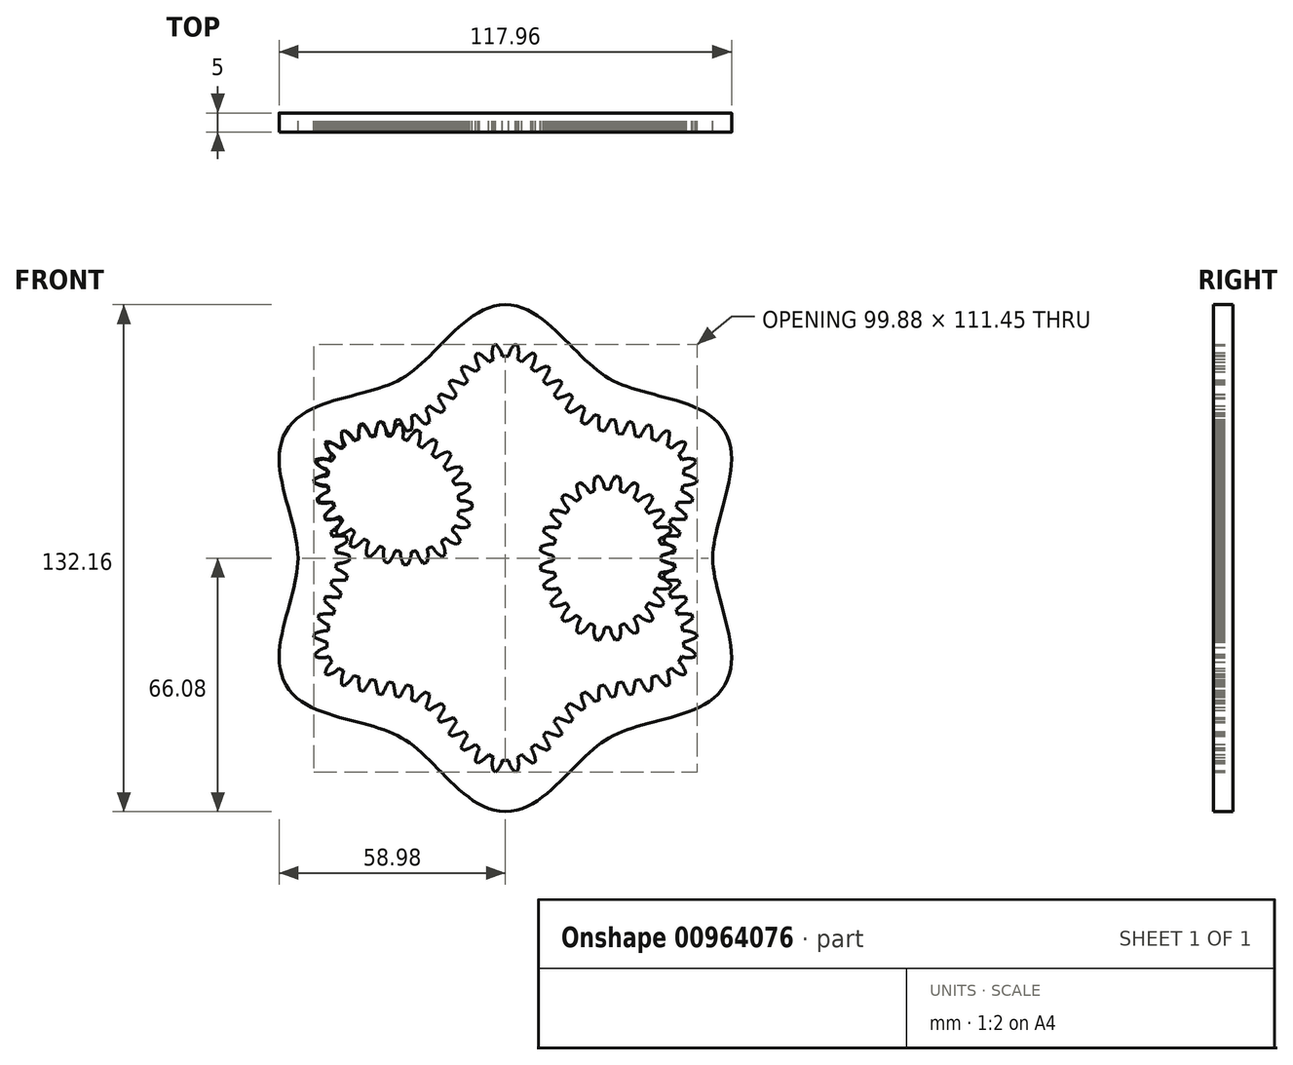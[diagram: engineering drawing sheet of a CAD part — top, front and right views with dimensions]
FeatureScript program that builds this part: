
annotation { "Feature Type Name" : "Feature", "Feature Type Description" : "" }
export const myFeature = defineFeature(function(context is Context, id is Id, definition is map)
    precondition{}
    {
        {
            var Q0;
            Q0=qCreatedBy(makeId("Front.planeOp"),FACE);
            var sketch = newSketch(context, id + "F0", { "sketchPlane" : qUnion([Q0])});
            skPoint(sketch, "E0", {"position": v(0, 66.08) * mm});
            skPoint(sketch, "E1", {"position": v(-59.16, 0) * mm});
            skSolve(sketch);
        }
        {
            var Q0;
            Q0=qCreatedBy(makeId("Front.planeOp"),FACE);
            var sketch = newSketch(context, id + "F1", { "sketchPlane" : qUnion([Q0])});
            skLineSegment(sketch, "E2", {"start": v(0, 0) * mm, "end": v(27.04, 46.83) * mm, "construction": true});
            skPoint(sketch, "E3", {"position": v(0, 66.08) * mm});
            skLineSegment(sketch, "E4", {"start": v(0, 0) * mm, "end": v(15.32, 57.19) * mm, "construction": true});
            skFitSpline(sketch, "E5", {"points": [v(0, 66.08) * mm, v(15.32, 57.19) * mm, v(27.04, 46.83) * mm], "startDerivative": vector(35.27, 0) * mm, "endDerivative": vector(23.83, -13.76) * mm});
            skLineSegment(sketch, "E6", {"start": v(23.2, 49.05) * mm, "end": v(27.04, 46.83) * mm, "construction": true});
            skLineSegment(sketch, "E7", {"start": v(0, 52.7) * mm, "end": v(0.86, 52.7) * mm});
            skLineSegment(sketch, "E8", {"start": v(3.15, 51.97) * mm, "end": v(4.31, 51.2) * mm});
            skLineSegment(sketch, "E9", {"start": v(6.74, 49.56) * mm, "end": v(7.8, 48.58) * mm});
            skLineSegment(sketch, "E10", {"start": v(9.81, 46.2) * mm, "end": v(10.7, 45.27) * mm});
            skLineSegment(sketch, "E11", {"start": v(12.7, 42.61) * mm, "end": v(13.52, 41.6) * mm});
            skLineSegment(sketch, "E12", {"start": v(15.78, 38.88) * mm, "end": v(16.73, 37.92) * mm});
            skLineSegment(sketch, "E13", {"start": v(19.8, 35.5) * mm, "end": v(20.32, 35.2) * mm});
            skLineSegment(sketch, "E14", {"start": v(2.56, 55.72) * mm, "end": v(3.13, 55.4) * mm});
            skLineSegment(sketch, "E15", {"start": v(7.18, 53.52) * mm, "end": v(7.82, 52.97) * mm});
            skLineSegment(sketch, "E16", {"start": v(10.9, 50.1) * mm, "end": v(11.58, 49.43) * mm});
            skLineSegment(sketch, "E17", {"start": v(13.99, 46.43) * mm, "end": v(14.76, 45.72) * mm});
            skLineSegment(sketch, "E18", {"start": v(16.88, 42.82) * mm, "end": v(17.59, 41.93) * mm});
            skLineSegment(sketch, "E19", {"start": v(19.84, 39.7) * mm, "end": v(20.77, 38.84) * mm});
            skArc(sketch, "E20", {"start": v(2.56, 55.72) * mm, "mid": v(1.4, 54.38) * mm, "end": v(0.86, 52.7) * mm});
            skArc(sketch, "E21", {"start": v(3.15, 51.97) * mm, "mid": v(3.46, 53.7) * mm, "end": v(3.13, 55.4) * mm});
            skArc(sketch, "E22", {"start": v(7.18, 53.52) * mm, "mid": v(5.65, 52.48) * mm, "end": v(4.31, 51.2) * mm});
            skArc(sketch, "E23", {"start": v(6.74, 49.56) * mm, "mid": v(7.47, 51.21) * mm, "end": v(7.82, 52.97) * mm});
            skArc(sketch, "E24", {"start": v(10.9, 50.1) * mm, "mid": v(9.29, 49.47) * mm, "end": v(7.8, 48.58) * mm});
            skArc(sketch, "E25", {"start": v(9.81, 46.2) * mm, "mid": v(10.8, 47.76) * mm, "end": v(11.58, 49.43) * mm});
            skArc(sketch, "E26", {"start": v(13.99, 46.43) * mm, "mid": v(12.33, 45.9) * mm, "end": v(10.7, 45.27) * mm});
            skArc(sketch, "E27", {"start": v(12.7, 42.61) * mm, "mid": v(13.78, 44.13) * mm, "end": v(14.76, 45.72) * mm});
            skArc(sketch, "E28", {"start": v(13.52, 41.6) * mm, "mid": v(15.2, 42.19) * mm, "end": v(16.88, 42.82) * mm});
            skArc(sketch, "E29", {"start": v(17.59, 41.93) * mm, "mid": v(16.64, 40.43) * mm, "end": v(15.78, 38.88) * mm});
            skArc(sketch, "E30", {"start": v(16.73, 37.92) * mm, "mid": v(18.35, 38.7) * mm, "end": v(19.84, 39.7) * mm});
            skArc(sketch, "E31", {"start": v(20.77, 38.84) * mm, "mid": v(20.1, 37.22) * mm, "end": v(19.8, 35.5) * mm});
            skPoint(sketch, "E32", {"position": v(0, 52.7) * mm});
            skPoint(sketch, "E33", {"position": v(0, 0) * mm});
            skLineSegment(sketch, "E34", {"start": v(0, 66.08) * mm, "end": v(0, 52.7) * mm});
            skLineSegment(sketch, "E35", {"start": v(20.32, 35.2) * mm, "end": v(27.04, 46.83) * mm});
            skSolve(sketch);
        }
        {
            var Q0;
            Q0 = qSketchRegion(id + "F1", true);
            extrude(context, id + "F2", {"entities" : qUnion([Q0]), "depth" : 5 * mm, "offsetDistance" : 25 * mm});
        }
        {
            var Q0;
            Q0=makeQuery(id+"F2.opExtrude","SWEPT_BODY",BODY,{"disambiguationData":[OSD([sQuery(id+"F1.wireOp",EDGE,"E5"),sQuery(id+"F1.wireOp",EDGE,"E7"),sQuery(id+"F1.wireOp",EDGE,"E8"),sQuery(id+"F1.wireOp",EDGE,"E9"),sQuery(id+"F1.wireOp",EDGE,"E10"),sQuery(id+"F1.wireOp",EDGE,"E11"),sQuery(id+"F1.wireOp",EDGE,"E12"),sQuery(id+"F1.wireOp",EDGE,"E13"),sQuery(id+"F1.wireOp",EDGE,"E14"),sQuery(id+"F1.wireOp",EDGE,"E15"),sQuery(id+"F1.wireOp",EDGE,"E16"),sQuery(id+"F1.wireOp",EDGE,"E17"),sQuery(id+"F1.wireOp",EDGE,"E18"),sQuery(id+"F1.wireOp",EDGE,"E19"),sQuery(id+"F1.wireOp",EDGE,"E20"),sQuery(id+"F1.wireOp",EDGE,"E21"),sQuery(id+"F1.wireOp",EDGE,"E22"),sQuery(id+"F1.wireOp",EDGE,"E23"),sQuery(id+"F1.wireOp",EDGE,"E24"),sQuery(id+"F1.wireOp",EDGE,"E25"),sQuery(id+"F1.wireOp",EDGE,"E26"),sQuery(id+"F1.wireOp",EDGE,"E27"),sQuery(id+"F1.wireOp",EDGE,"E28"),sQuery(id+"F1.wireOp",EDGE,"E29"),sQuery(id+"F1.wireOp",EDGE,"E30"),sQuery(id+"F1.wireOp",EDGE,"E31"),sQuery(id+"F1.wireOp",EDGE,"E34"),sQuery(id+"F1.wireOp",EDGE,"E35")])]});
            var Q1;
            Q1=qCreatedBy(makeId("Right.planeOp"),FACE);
            mirror(context, id + "F3", {"operationType" : NewBodyOperationType.ADD, "entities" : qUnion([Q0]), "mirrorPlane" : qUnion([Q1])});
        }
        {
            var Q0;
            Q0=qCreatedBy(makeId("Top.planeOp"),FACE);
            var sketch = newSketch(context, id + "F4", { "sketchPlane" : qUnion([Q0])});
            skLineSegment(sketch, "E36", {"start": v(0, 0) * mm, "end": v(0, -5) * mm, "construction": true});
            skSolve(sketch);
        }
        {
            var Q0;
            Q0=makeQuery(id+"F2.opExtrude","SWEPT_BODY",BODY,{"disambiguationData":[OSD([sQuery(id+"F1.wireOp",EDGE,"E5"),sQuery(id+"F1.wireOp",EDGE,"E7"),sQuery(id+"F1.wireOp",EDGE,"E8"),sQuery(id+"F1.wireOp",EDGE,"E9"),sQuery(id+"F1.wireOp",EDGE,"E10"),sQuery(id+"F1.wireOp",EDGE,"E11"),sQuery(id+"F1.wireOp",EDGE,"E12"),sQuery(id+"F1.wireOp",EDGE,"E13"),sQuery(id+"F1.wireOp",EDGE,"E14"),sQuery(id+"F1.wireOp",EDGE,"E15"),sQuery(id+"F1.wireOp",EDGE,"E16"),sQuery(id+"F1.wireOp",EDGE,"E17"),sQuery(id+"F1.wireOp",EDGE,"E18"),sQuery(id+"F1.wireOp",EDGE,"E19"),sQuery(id+"F1.wireOp",EDGE,"E20"),sQuery(id+"F1.wireOp",EDGE,"E21"),sQuery(id+"F1.wireOp",EDGE,"E22"),sQuery(id+"F1.wireOp",EDGE,"E23"),sQuery(id+"F1.wireOp",EDGE,"E24"),sQuery(id+"F1.wireOp",EDGE,"E25"),sQuery(id+"F1.wireOp",EDGE,"E26"),sQuery(id+"F1.wireOp",EDGE,"E27"),sQuery(id+"F1.wireOp",EDGE,"E28"),sQuery(id+"F1.wireOp",EDGE,"E29"),sQuery(id+"F1.wireOp",EDGE,"E30"),sQuery(id+"F1.wireOp",EDGE,"E31"),sQuery(id+"F1.wireOp",EDGE,"E34"),sQuery(id+"F1.wireOp",EDGE,"E35")])]});
            var Q1;
            Q1=sQuery(id+"F4.wireOp",EDGE,"E36");
            circularPattern(context, id + "F5", {"operationType" : NewBodyOperationType.ADD, "entities" : qUnion([Q0]), "axis" : qUnion([Q1]), "angle" : 360 * degree, "instanceCount" : 6, "equalSpace" : true});
        }
        {
            var Q0;
            Q0=qCreatedBy(makeId("Front.planeOp"),FACE);
            var sketch = newSketch(context, id + "F6", { "sketchPlane" : qUnion([Q0])});
            skLineSegment(sketch, "E37", {"start": v(-1.54, -16.72) * mm, "end": v(-1.46, -16.57) * mm});
            skLineSegment(sketch, "E38", {"start": v(-1.46, -16.57) * mm, "end": v(-1.39, -16.42) * mm});
            skLineSegment(sketch, "E39", {"start": v(-1.39, -16.42) * mm, "end": v(-1.32, -16.28) * mm});
            skLineSegment(sketch, "E40", {"start": v(-1.32, -16.28) * mm, "end": v(-1.26, -16.15) * mm});
            skLineSegment(sketch, "E41", {"start": v(-1.26, -16.15) * mm, "end": v(-1.2, -16.01) * mm});
            skLineSegment(sketch, "E42", {"start": v(-1.2, -16.01) * mm, "end": v(-1.15, -15.9) * mm});
            skLineSegment(sketch, "E43", {"start": v(-1.15, -15.9) * mm, "end": v(-1.1, -15.77) * mm});
            skLineSegment(sketch, "E44", {"start": v(-1.1, -15.77) * mm, "end": v(-1.06, -15.66) * mm});
            skLineSegment(sketch, "E45", {"start": v(-1.06, -15.66) * mm, "end": v(-1.03, -15.6) * mm});
            skLineSegment(sketch, "E46", {"start": v(-1.03, -15.6) * mm, "end": v(-1.02, -15.56) * mm});
            skLineSegment(sketch, "E47", {"start": v(-1.02, -15.56) * mm, "end": v(-1, -15.49) * mm});
            skLineSegment(sketch, "E48", {"start": v(-1, -15.49) * mm, "end": v(-0.96, -15.4) * mm});
            skLineSegment(sketch, "E49", {"start": v(-0.96, -15.4) * mm, "end": v(-0.93, -15.3) * mm});
            skLineSegment(sketch, "E50", {"start": v(-0.93, -15.3) * mm, "end": v(-0.9, -15.21) * mm});
            skLineSegment(sketch, "E51", {"start": v(-0.9, -15.21) * mm, "end": v(-0.88, -15.13) * mm});
            skLineSegment(sketch, "E52", {"start": v(-0.88, -15.13) * mm, "end": v(-0.86, -15.06) * mm});
            skLineSegment(sketch, "E53", {"start": v(-0.86, -15.06) * mm, "end": v(-0.84, -14.98) * mm});
            skLineSegment(sketch, "E54", {"start": v(-0.84, -14.98) * mm, "end": v(-0.83, -14.92) * mm});
            skLineSegment(sketch, "E55", {"start": v(-0.83, -14.92) * mm, "end": v(-0.81, -14.86) * mm});
            skLineSegment(sketch, "E56", {"start": v(-0.81, -14.86) * mm, "end": v(-0.8, -14.8) * mm});
            skLineSegment(sketch, "E57", {"start": v(-0.8, -14.8) * mm, "end": v(-0.72, -14.44) * mm});
            skLineSegment(sketch, "E58", {"start": v(-0.72, -14.44) * mm, "end": v(-0.71, -14.4) * mm});
            skLineSegment(sketch, "E59", {"start": v(-0.71, -14.4) * mm, "end": v(-0.7, -14.38) * mm});
            skLineSegment(sketch, "E60", {"start": v(-0.7, -14.38) * mm, "end": v(-0.69, -14.33) * mm});
            skLineSegment(sketch, "E61", {"start": v(-0.69, -14.33) * mm, "end": v(-0.67, -14.3) * mm});
            skLineSegment(sketch, "E62", {"start": v(-0.67, -14.3) * mm, "end": v(-0.66, -14.28) * mm});
            skLineSegment(sketch, "E63", {"start": v(-0.66, -14.28) * mm, "end": v(-0.65, -14.23) * mm});
            skLineSegment(sketch, "E64", {"start": v(-0.65, -14.23) * mm, "end": v(-0.63, -14.21) * mm});
            skLineSegment(sketch, "E65", {"start": v(-0.63, -14.21) * mm, "end": v(-0.6, -14.18) * mm});
            skLineSegment(sketch, "E66", {"start": v(-0.6, -14.18) * mm, "end": v(-0.58, -14.15) * mm});
            skLineSegment(sketch, "E67", {"start": v(-0.58, -14.15) * mm, "end": v(-0.55, -14.12) * mm});
            skLineSegment(sketch, "E68", {"start": v(-0.55, -14.12) * mm, "end": v(-0.52, -14.1) * mm});
            skLineSegment(sketch, "E69", {"start": v(-0.52, -14.1) * mm, "end": v(-0.5, -14.09) * mm});
            skLineSegment(sketch, "E70", {"start": v(-0.5, -14.09) * mm, "end": v(-0.48, -14.08) * mm});
            skLineSegment(sketch, "E71", {"start": v(-0.48, -14.08) * mm, "end": v(-0.48, -14.08) * mm});
            skLineSegment(sketch, "E72", {"start": v(-0.48, -14.08) * mm, "end": v(-0.46, -14.07) * mm});
            skLineSegment(sketch, "E73", {"start": v(-0.46, -14.07) * mm, "end": v(-0.44, -14.07) * mm});
            skLineSegment(sketch, "E74", {"start": v(-0.44, -14.07) * mm, "end": v(-0.28, -14.08) * mm});
            skLineSegment(sketch, "E75", {"start": v(-0.28, -14.08) * mm, "end": v(-0.05, -14.08) * mm});
            skLineSegment(sketch, "E76", {"start": v(-0.05, -14.08) * mm, "end": v(0.07, -14.08) * mm});
            skLineSegment(sketch, "E77", {"start": v(0.07, -14.08) * mm, "end": v(0.3, -14.07) * mm});
            skLineSegment(sketch, "E78", {"start": v(0.3, -14.07) * mm, "end": v(0.47, -14.07) * mm});
            skLineSegment(sketch, "E79", {"start": v(0.47, -14.07) * mm, "end": v(0.49, -14.07) * mm});
            skLineSegment(sketch, "E80", {"start": v(0.49, -14.07) * mm, "end": v(0.5, -14.08) * mm});
            skLineSegment(sketch, "E81", {"start": v(0.5, -14.08) * mm, "end": v(0.5, -14.08) * mm});
            skLineSegment(sketch, "E82", {"start": v(0.5, -14.08) * mm, "end": v(0.52, -14.08) * mm});
            skLineSegment(sketch, "E83", {"start": v(0.52, -14.08) * mm, "end": v(0.55, -14.1) * mm});
            skLineSegment(sketch, "E84", {"start": v(0.55, -14.1) * mm, "end": v(0.58, -14.12) * mm});
            skLineSegment(sketch, "E85", {"start": v(0.58, -14.12) * mm, "end": v(0.6, -14.15) * mm});
            skLineSegment(sketch, "E86", {"start": v(0.6, -14.15) * mm, "end": v(0.64, -14.19) * mm});
            skLineSegment(sketch, "E87", {"start": v(0.64, -14.19) * mm, "end": v(0.66, -14.2) * mm});
            skLineSegment(sketch, "E88", {"start": v(0.66, -14.2) * mm, "end": v(0.67, -14.25) * mm});
            skLineSegment(sketch, "E89", {"start": v(0.67, -14.25) * mm, "end": v(0.7, -14.28) * mm});
            skLineSegment(sketch, "E90", {"start": v(0.7, -14.28) * mm, "end": v(0.7, -14.3) * mm});
            skLineSegment(sketch, "E91", {"start": v(0.7, -14.3) * mm, "end": v(0.72, -14.37) * mm});
            skLineSegment(sketch, "E92", {"start": v(0.72, -14.37) * mm, "end": v(0.74, -14.4) * mm});
            skLineSegment(sketch, "E93", {"start": v(0.74, -14.4) * mm, "end": v(0.75, -14.44) * mm});
            skLineSegment(sketch, "E94", {"start": v(0.75, -14.44) * mm, "end": v(0.83, -14.8) * mm});
            skLineSegment(sketch, "E95", {"start": v(0.83, -14.8) * mm, "end": v(0.84, -14.87) * mm});
            skLineSegment(sketch, "E96", {"start": v(0.84, -14.87) * mm, "end": v(0.86, -14.95) * mm});
            skLineSegment(sketch, "E97", {"start": v(0.86, -14.95) * mm, "end": v(0.88, -15.03) * mm});
            skLineSegment(sketch, "E98", {"start": v(0.88, -15.03) * mm, "end": v(0.9, -15.1) * mm});
            skLineSegment(sketch, "E99", {"start": v(0.9, -15.1) * mm, "end": v(0.93, -15.2) * mm});
            skLineSegment(sketch, "E100", {"start": v(0.93, -15.2) * mm, "end": v(0.96, -15.29) * mm});
            skLineSegment(sketch, "E101", {"start": v(0.96, -15.29) * mm, "end": v(0.99, -15.39) * mm});
            skLineSegment(sketch, "E102", {"start": v(0.99, -15.39) * mm, "end": v(1.02, -15.48) * mm});
            skLineSegment(sketch, "E103", {"start": v(1.02, -15.48) * mm, "end": v(1.05, -15.55) * mm});
            skLineSegment(sketch, "E104", {"start": v(1.05, -15.55) * mm, "end": v(1.06, -15.59) * mm});
            skLineSegment(sketch, "E105", {"start": v(1.06, -15.59) * mm, "end": v(1.09, -15.66) * mm});
            skLineSegment(sketch, "E106", {"start": v(1.09, -15.66) * mm, "end": v(1.13, -15.77) * mm});
            skLineSegment(sketch, "E107", {"start": v(1.13, -15.77) * mm, "end": v(1.17, -15.88) * mm});
            skLineSegment(sketch, "E108", {"start": v(1.17, -15.88) * mm, "end": v(1.22, -16) * mm});
            skLineSegment(sketch, "E109", {"start": v(1.22, -16) * mm, "end": v(1.27, -16.1) * mm});
            skLineSegment(sketch, "E110", {"start": v(1.27, -16.1) * mm, "end": v(1.33, -16.23) * mm});
            skLineSegment(sketch, "E111", {"start": v(1.33, -16.23) * mm, "end": v(1.38, -16.35) * mm});
            skLineSegment(sketch, "E112", {"start": v(1.38, -16.35) * mm, "end": v(1.44, -16.47) * mm});
            skLineSegment(sketch, "E113", {"start": v(1.44, -16.47) * mm, "end": v(1.5, -16.6) * mm});
            skLineSegment(sketch, "E114", {"start": v(1.5, -16.6) * mm, "end": v(1.57, -16.72) * mm});
            skLineSegment(sketch, "E115", {"start": v(1.57, -16.72) * mm, "end": v(1.96, -17.44) * mm});
            skLineSegment(sketch, "E116", {"start": v(1.96, -17.44) * mm, "end": v(2.08, -17.43) * mm});
            skLineSegment(sketch, "E117", {"start": v(2.08, -17.43) * mm, "end": v(2.33, -17.4) * mm});
            skLineSegment(sketch, "E118", {"start": v(2.33, -17.4) * mm, "end": v(2.57, -17.38) * mm});
            skLineSegment(sketch, "E119", {"start": v(2.57, -17.38) * mm, "end": v(2.82, -17.36) * mm});
            skLineSegment(sketch, "E120", {"start": v(2.82, -17.36) * mm, "end": v(3.06, -17.33) * mm});
            skLineSegment(sketch, "E121", {"start": v(3.06, -17.33) * mm, "end": v(3.06, -17.33) * mm});
            skLineSegment(sketch, "E122", {"start": v(3.06, -17.33) * mm, "end": v(3.29, -16.64) * mm});
            skLineSegment(sketch, "E123", {"start": v(3.29, -16.64) * mm, "end": v(3.34, -16.5) * mm});
            skLineSegment(sketch, "E124", {"start": v(3.34, -16.5) * mm, "end": v(3.38, -16.35) * mm});
            skLineSegment(sketch, "E125", {"start": v(3.38, -16.35) * mm, "end": v(3.41, -16.21) * mm});
            skLineSegment(sketch, "E126", {"start": v(3.41, -16.21) * mm, "end": v(3.45, -16.08) * mm});
            skLineSegment(sketch, "E127", {"start": v(3.45, -16.08) * mm, "end": v(3.48, -15.96) * mm});
            skLineSegment(sketch, "E128", {"start": v(3.48, -15.96) * mm, "end": v(3.5, -15.84) * mm});
            skLineSegment(sketch, "E129", {"start": v(3.5, -15.84) * mm, "end": v(3.53, -15.72) * mm});
            skLineSegment(sketch, "E130", {"start": v(3.53, -15.72) * mm, "end": v(3.56, -15.6) * mm});
            skLineSegment(sketch, "E131", {"start": v(3.56, -15.6) * mm, "end": v(3.58, -15.5) * mm});
            skLineSegment(sketch, "E132", {"start": v(3.58, -15.5) * mm, "end": v(3.6, -15.4) * mm});
            skLineSegment(sketch, "E133", {"start": v(3.6, -15.4) * mm, "end": v(3.6, -15.34) * mm});
            skLineSegment(sketch, "E134", {"start": v(3.6, -15.34) * mm, "end": v(3.6, -15.31) * mm});
            skLineSegment(sketch, "E135", {"start": v(3.6, -15.31) * mm, "end": v(3.62, -15.25) * mm});
            skLineSegment(sketch, "E136", {"start": v(3.62, -15.25) * mm, "end": v(3.63, -15.16) * mm});
            skLineSegment(sketch, "E137", {"start": v(3.63, -15.16) * mm, "end": v(3.64, -15.08) * mm});
            skLineSegment(sketch, "E138", {"start": v(3.64, -15.08) * mm, "end": v(3.65, -15) * mm});
            skLineSegment(sketch, "E139", {"start": v(3.65, -15) * mm, "end": v(3.66, -14.92) * mm});
            skLineSegment(sketch, "E140", {"start": v(3.66, -14.92) * mm, "end": v(3.67, -14.84) * mm});
            skLineSegment(sketch, "E141", {"start": v(3.67, -14.84) * mm, "end": v(3.67, -14.75) * mm});
            skLineSegment(sketch, "E142", {"start": v(3.67, -14.75) * mm, "end": v(3.67, -14.68) * mm});
            skLineSegment(sketch, "E143", {"start": v(3.67, -14.68) * mm, "end": v(3.68, -14.61) * mm});
            skLineSegment(sketch, "E144", {"start": v(3.68, -14.61) * mm, "end": v(3.68, -14.55) * mm});
            skLineSegment(sketch, "E145", {"start": v(3.68, -14.55) * mm, "end": v(3.68, -14.18) * mm});
            skLineSegment(sketch, "E146", {"start": v(3.68, -14.18) * mm, "end": v(3.69, -14.14) * mm});
            skLineSegment(sketch, "E147", {"start": v(3.69, -14.14) * mm, "end": v(3.7, -14.1) * mm});
            skLineSegment(sketch, "E148", {"start": v(3.7, -14.1) * mm, "end": v(3.7, -14.04) * mm});
            skLineSegment(sketch, "E149", {"start": v(3.7, -14.04) * mm, "end": v(3.7, -14.01) * mm});
            skLineSegment(sketch, "E150", {"start": v(3.7, -14.01) * mm, "end": v(3.72, -13.98) * mm});
            skLineSegment(sketch, "E151", {"start": v(3.72, -13.98) * mm, "end": v(3.73, -13.93) * mm});
            skLineSegment(sketch, "E152", {"start": v(3.73, -13.93) * mm, "end": v(3.74, -13.9) * mm});
            skLineSegment(sketch, "E153", {"start": v(3.74, -13.9) * mm, "end": v(3.77, -13.86) * mm});
            skLineSegment(sketch, "E154", {"start": v(3.77, -13.86) * mm, "end": v(3.78, -13.83) * mm});
            skLineSegment(sketch, "E155", {"start": v(3.78, -13.83) * mm, "end": v(3.8, -13.8) * mm});
            skLineSegment(sketch, "E156", {"start": v(3.8, -13.8) * mm, "end": v(3.83, -13.78) * mm});
            skLineSegment(sketch, "E157", {"start": v(3.83, -13.78) * mm, "end": v(3.85, -13.76) * mm});
            skLineSegment(sketch, "E158", {"start": v(3.85, -13.76) * mm, "end": v(3.86, -13.76) * mm});
            skLineSegment(sketch, "E159", {"start": v(3.86, -13.76) * mm, "end": v(3.86, -13.75) * mm});
            skLineSegment(sketch, "E160", {"start": v(3.86, -13.75) * mm, "end": v(3.88, -13.75) * mm});
            skLineSegment(sketch, "E161", {"start": v(3.88, -13.75) * mm, "end": v(3.89, -13.74) * mm});
            skLineSegment(sketch, "E162", {"start": v(3.89, -13.74) * mm, "end": v(4.1, -13.7) * mm});
            skLineSegment(sketch, "E163", {"start": v(4.1, -13.7) * mm, "end": v(4.29, -13.67) * mm});
            skLineSegment(sketch, "E164", {"start": v(4.29, -13.67) * mm, "end": v(4.4, -13.65) * mm});
            skLineSegment(sketch, "E165", {"start": v(4.4, -13.65) * mm, "end": v(4.58, -13.61) * mm});
            skLineSegment(sketch, "E166", {"start": v(4.58, -13.61) * mm, "end": v(4.8, -13.57) * mm});
            skLineSegment(sketch, "E167", {"start": v(4.8, -13.57) * mm, "end": v(4.8, -13.57) * mm});
            skLineSegment(sketch, "E168", {"start": v(4.8, -13.57) * mm, "end": v(4.82, -13.57) * mm});
            skLineSegment(sketch, "E169", {"start": v(4.82, -13.57) * mm, "end": v(4.83, -13.57) * mm});
            skLineSegment(sketch, "E170", {"start": v(4.83, -13.57) * mm, "end": v(4.84, -13.57) * mm});
            skLineSegment(sketch, "E171", {"start": v(4.84, -13.57) * mm, "end": v(4.87, -13.58) * mm});
            skLineSegment(sketch, "E172", {"start": v(4.87, -13.58) * mm, "end": v(4.9, -13.6) * mm});
            skLineSegment(sketch, "E173", {"start": v(4.9, -13.6) * mm, "end": v(4.92, -13.6) * mm});
            skLineSegment(sketch, "E174", {"start": v(4.92, -13.6) * mm, "end": v(4.95, -13.63) * mm});
            skLineSegment(sketch, "E175", {"start": v(4.95, -13.63) * mm, "end": v(4.98, -13.66) * mm});
            skLineSegment(sketch, "E176", {"start": v(4.98, -13.66) * mm, "end": v(5.01, -13.7) * mm});
            skLineSegment(sketch, "E177", {"start": v(5.01, -13.7) * mm, "end": v(5.05, -13.73) * mm});
            skLineSegment(sketch, "E178", {"start": v(5.05, -13.73) * mm, "end": v(5.07, -13.75) * mm});
            skLineSegment(sketch, "E179", {"start": v(5.07, -13.75) * mm, "end": v(5.09, -13.8) * mm});
            skLineSegment(sketch, "E180", {"start": v(5.09, -13.8) * mm, "end": v(5.1, -13.82) * mm});
            skLineSegment(sketch, "E181", {"start": v(5.1, -13.82) * mm, "end": v(5.13, -13.85) * mm});
            skLineSegment(sketch, "E182", {"start": v(5.13, -13.85) * mm, "end": v(5.15, -13.91) * mm});
            skLineSegment(sketch, "E183", {"start": v(5.15, -13.91) * mm, "end": v(5.16, -13.91) * mm});
            skLineSegment(sketch, "E184", {"start": v(5.16, -13.91) * mm, "end": v(5.27, -14.19) * mm});
            skLineSegment(sketch, "E185", {"start": v(5.27, -14.19) * mm, "end": v(5.3, -14.25) * mm});
            skLineSegment(sketch, "E186", {"start": v(5.3, -14.25) * mm, "end": v(5.32, -14.3) * mm});
            skLineSegment(sketch, "E187", {"start": v(5.32, -14.3) * mm, "end": v(5.34, -14.36) * mm});
            skLineSegment(sketch, "E188", {"start": v(5.34, -14.36) * mm, "end": v(5.38, -14.43) * mm});
            skLineSegment(sketch, "E189", {"start": v(5.38, -14.43) * mm, "end": v(5.4, -14.5) * mm});
            skLineSegment(sketch, "E190", {"start": v(5.4, -14.5) * mm, "end": v(5.44, -14.56) * mm});
            skLineSegment(sketch, "E191", {"start": v(5.44, -14.56) * mm, "end": v(5.48, -14.64) * mm});
            skLineSegment(sketch, "E192", {"start": v(5.48, -14.64) * mm, "end": v(5.52, -14.71) * mm});
            skLineSegment(sketch, "E193", {"start": v(5.52, -14.71) * mm, "end": v(5.56, -14.78) * mm});
            skLineSegment(sketch, "E194", {"start": v(5.56, -14.78) * mm, "end": v(5.6, -14.87) * mm});
            skLineSegment(sketch, "E195", {"start": v(5.6, -14.87) * mm, "end": v(5.64, -14.91) * mm});
            skLineSegment(sketch, "E196", {"start": v(5.64, -14.91) * mm, "end": v(5.66, -14.95) * mm});
            skLineSegment(sketch, "E197", {"start": v(5.66, -14.95) * mm, "end": v(5.7, -15) * mm});
            skLineSegment(sketch, "E198", {"start": v(5.7, -15) * mm, "end": v(5.74, -15.08) * mm});
            skLineSegment(sketch, "E199", {"start": v(5.74, -15.08) * mm, "end": v(5.8, -15.17) * mm});
            skLineSegment(sketch, "E200", {"start": v(5.8, -15.17) * mm, "end": v(5.85, -15.25) * mm});
            skLineSegment(sketch, "E201", {"start": v(5.85, -15.25) * mm, "end": v(5.92, -15.36) * mm});
            skLineSegment(sketch, "E202", {"start": v(5.92, -15.36) * mm, "end": v(6, -15.47) * mm});
            skLineSegment(sketch, "E203", {"start": v(6, -15.47) * mm, "end": v(6.1, -15.6) * mm});
            skLineSegment(sketch, "E204", {"start": v(6.1, -15.6) * mm, "end": v(6.18, -15.71) * mm});
            skLineSegment(sketch, "E205", {"start": v(6.18, -15.71) * mm, "end": v(6.28, -15.84) * mm});
            skLineSegment(sketch, "E206", {"start": v(6.28, -15.84) * mm, "end": v(6.38, -15.96) * mm});
            skLineSegment(sketch, "E207", {"start": v(6.38, -15.96) * mm, "end": v(6.9, -16.59) * mm});
            skLineSegment(sketch, "E208", {"start": v(6.9, -16.59) * mm, "end": v(7.02, -16.55) * mm});
            skLineSegment(sketch, "E209", {"start": v(7.02, -16.55) * mm, "end": v(7.22, -16.5) * mm});
            skLineSegment(sketch, "E210", {"start": v(7.22, -16.5) * mm, "end": v(7.42, -16.44) * mm});
            skLineSegment(sketch, "E211", {"start": v(7.42, -16.44) * mm, "end": v(7.61, -16.38) * mm});
            skLineSegment(sketch, "E212", {"start": v(7.61, -16.38) * mm, "end": v(7.8, -16.32) * mm});
            skLineSegment(sketch, "E213", {"start": v(7.8, -16.32) * mm, "end": v(7.96, -16.27) * mm});
            skLineSegment(sketch, "E214", {"start": v(7.96, -16.27) * mm, "end": v(8.05, -15.52) * mm});
            skLineSegment(sketch, "E215", {"start": v(8.05, -15.52) * mm, "end": v(8.06, -15.37) * mm});
            skLineSegment(sketch, "E216", {"start": v(8.06, -15.37) * mm, "end": v(8.08, -15.2) * mm});
            skLineSegment(sketch, "E217", {"start": v(8.08, -15.2) * mm, "end": v(8.1, -15.05) * mm});
            skLineSegment(sketch, "E218", {"start": v(8.1, -15.05) * mm, "end": v(8.1, -14.9) * mm});
            skLineSegment(sketch, "E219", {"start": v(8.1, -14.9) * mm, "end": v(8.1, -14.76) * mm});
            skLineSegment(sketch, "E220", {"start": v(8.1, -14.76) * mm, "end": v(8.1, -14.63) * mm});
            skLineSegment(sketch, "E221", {"start": v(8.1, -14.63) * mm, "end": v(8.1, -14.5) * mm});
            skLineSegment(sketch, "E222", {"start": v(8.1, -14.5) * mm, "end": v(8.1, -14.39) * mm});
            skLineSegment(sketch, "E223", {"start": v(8.1, -14.39) * mm, "end": v(8.1, -14.28) * mm});
            skLineSegment(sketch, "E224", {"start": v(8.1, -14.28) * mm, "end": v(8.1, -14.21) * mm});
            skLineSegment(sketch, "E225", {"start": v(8.1, -14.21) * mm, "end": v(8.1, -14.18) * mm});
            skLineSegment(sketch, "E226", {"start": v(8.1, -14.18) * mm, "end": v(8.1, -14.12) * mm});
            skLineSegment(sketch, "E227", {"start": v(8.1, -14.12) * mm, "end": v(8.1, -14.03) * mm});
            skLineSegment(sketch, "E228", {"start": v(8.1, -14.03) * mm, "end": v(8.08, -13.95) * mm});
            skLineSegment(sketch, "E229", {"start": v(8.08, -13.95) * mm, "end": v(8.08, -13.87) * mm});
            skLineSegment(sketch, "E230", {"start": v(8.08, -13.87) * mm, "end": v(8.07, -13.8) * mm});
            skLineSegment(sketch, "E231", {"start": v(8.07, -13.8) * mm, "end": v(8.06, -13.73) * mm});
            skLineSegment(sketch, "E232", {"start": v(8.06, -13.73) * mm, "end": v(8.05, -13.67) * mm});
            skLineSegment(sketch, "E233", {"start": v(8.05, -13.67) * mm, "end": v(8.04, -13.61) * mm});
            skLineSegment(sketch, "E234", {"start": v(8.04, -13.61) * mm, "end": v(8.03, -13.56) * mm});
            skLineSegment(sketch, "E235", {"start": v(8.03, -13.56) * mm, "end": v(8.02, -13.52) * mm});
            skLineSegment(sketch, "E236", {"start": v(8.02, -13.52) * mm, "end": v(8.01, -13.47) * mm});
            skLineSegment(sketch, "E237", {"start": v(8.01, -13.47) * mm, "end": v(7.94, -13.13) * mm});
            skLineSegment(sketch, "E238", {"start": v(7.94, -13.13) * mm, "end": v(7.94, -13.13) * mm});
            skLineSegment(sketch, "E239", {"start": v(7.94, -13.13) * mm, "end": v(7.93, -13.05) * mm});
            skLineSegment(sketch, "E240", {"start": v(7.93, -13.05) * mm, "end": v(7.94, -13.05) * mm});
            skLineSegment(sketch, "E241", {"start": v(7.94, -13.05) * mm, "end": v(7.92, -12.98) * mm});
            skLineSegment(sketch, "E242", {"start": v(7.92, -12.98) * mm, "end": v(7.93, -12.95) * mm});
            skLineSegment(sketch, "E243", {"start": v(7.93, -12.95) * mm, "end": v(7.93, -12.91) * mm});
            skLineSegment(sketch, "E244", {"start": v(7.93, -12.91) * mm, "end": v(7.92, -12.87) * mm});
            skLineSegment(sketch, "E245", {"start": v(7.92, -12.87) * mm, "end": v(7.93, -12.84) * mm});
            skLineSegment(sketch, "E246", {"start": v(7.93, -12.84) * mm, "end": v(7.94, -12.8) * mm});
            skLineSegment(sketch, "E247", {"start": v(7.94, -12.8) * mm, "end": v(7.95, -12.75) * mm});
            skLineSegment(sketch, "E248", {"start": v(7.95, -12.75) * mm, "end": v(7.96, -12.7) * mm});
            skLineSegment(sketch, "E249", {"start": v(7.96, -12.7) * mm, "end": v(7.98, -12.67) * mm});
            skLineSegment(sketch, "E250", {"start": v(7.98, -12.67) * mm, "end": v(8, -12.64) * mm});
            skLineSegment(sketch, "E251", {"start": v(8, -12.64) * mm, "end": v(8.02, -12.62) * mm});
            skLineSegment(sketch, "E252", {"start": v(8.02, -12.62) * mm, "end": v(8.03, -12.61) * mm});
            skLineSegment(sketch, "E253", {"start": v(8.03, -12.61) * mm, "end": v(8.03, -12.6) * mm});
            skLineSegment(sketch, "E254", {"start": v(8.03, -12.6) * mm, "end": v(8.05, -12.6) * mm});
            skLineSegment(sketch, "E255", {"start": v(8.05, -12.6) * mm, "end": v(8.06, -12.59) * mm});
            skLineSegment(sketch, "E256", {"start": v(8.06, -12.59) * mm, "end": v(8.26, -12.5) * mm});
            skLineSegment(sketch, "E257", {"start": v(8.26, -12.5) * mm, "end": v(8.44, -12.44) * mm});
            skLineSegment(sketch, "E258", {"start": v(8.44, -12.44) * mm, "end": v(8.53, -12.4) * mm});
            skLineSegment(sketch, "E259", {"start": v(8.53, -12.4) * mm, "end": v(8.7, -12.33) * mm});
            skLineSegment(sketch, "E260", {"start": v(8.7, -12.33) * mm, "end": v(8.9, -12.24) * mm});
            skLineSegment(sketch, "E261", {"start": v(8.9, -12.24) * mm, "end": v(8.92, -12.23) * mm});
            skLineSegment(sketch, "E262", {"start": v(8.92, -12.23) * mm, "end": v(8.94, -12.23) * mm});
            skLineSegment(sketch, "E263", {"start": v(8.94, -12.23) * mm, "end": v(8.94, -12.23) * mm});
            skLineSegment(sketch, "E264", {"start": v(8.94, -12.23) * mm, "end": v(8.95, -12.23) * mm});
            skLineSegment(sketch, "E265", {"start": v(8.95, -12.23) * mm, "end": v(8.99, -12.23) * mm});
            skLineSegment(sketch, "E266", {"start": v(8.99, -12.23) * mm, "end": v(9.02, -12.24) * mm});
            skLineSegment(sketch, "E267", {"start": v(9.02, -12.24) * mm, "end": v(9.06, -12.26) * mm});
            skLineSegment(sketch, "E268", {"start": v(9.06, -12.26) * mm, "end": v(9.1, -12.28) * mm});
            skLineSegment(sketch, "E269", {"start": v(9.1, -12.28) * mm, "end": v(9.13, -12.29) * mm});
            skLineSegment(sketch, "E270", {"start": v(9.13, -12.29) * mm, "end": v(9.16, -12.32) * mm});
            skLineSegment(sketch, "E271", {"start": v(9.16, -12.32) * mm, "end": v(9.19, -12.34) * mm});
            skLineSegment(sketch, "E272", {"start": v(9.19, -12.34) * mm, "end": v(9.22, -12.36) * mm});
            skLineSegment(sketch, "E273", {"start": v(9.22, -12.36) * mm, "end": v(9.25, -12.4) * mm});
            skLineSegment(sketch, "E274", {"start": v(9.25, -12.4) * mm, "end": v(9.28, -12.43) * mm});
            skLineSegment(sketch, "E275", {"start": v(9.28, -12.43) * mm, "end": v(9.3, -12.46) * mm});
            skLineSegment(sketch, "E276", {"start": v(9.3, -12.46) * mm, "end": v(9.34, -12.5) * mm});
            skLineSegment(sketch, "E277", {"start": v(9.34, -12.5) * mm, "end": v(9.34, -12.5) * mm});
            skLineSegment(sketch, "E278", {"start": v(9.34, -12.5) * mm, "end": v(9.53, -12.78) * mm});
            skLineSegment(sketch, "E279", {"start": v(9.53, -12.78) * mm, "end": v(9.55, -12.82) * mm});
            skLineSegment(sketch, "E280", {"start": v(9.55, -12.82) * mm, "end": v(9.6, -12.88) * mm});
            skLineSegment(sketch, "E281", {"start": v(9.6, -12.88) * mm, "end": v(9.64, -12.94) * mm});
            skLineSegment(sketch, "E282", {"start": v(9.64, -12.94) * mm, "end": v(9.68, -13) * mm});
            skLineSegment(sketch, "E283", {"start": v(9.68, -13) * mm, "end": v(9.73, -13.06) * mm});
            skLineSegment(sketch, "E284", {"start": v(9.73, -13.06) * mm, "end": v(9.79, -13.13) * mm});
            skLineSegment(sketch, "E285", {"start": v(9.79, -13.13) * mm, "end": v(9.85, -13.2) * mm});
            skLineSegment(sketch, "E286", {"start": v(9.85, -13.2) * mm, "end": v(9.9, -13.27) * mm});
            skLineSegment(sketch, "E287", {"start": v(9.9, -13.27) * mm, "end": v(9.97, -13.34) * mm});
            skLineSegment(sketch, "E288", {"start": v(9.97, -13.34) * mm, "end": v(10, -13.39) * mm});
            skLineSegment(sketch, "E289", {"start": v(10, -13.39) * mm, "end": v(10.03, -13.41) * mm});
            skLineSegment(sketch, "E290", {"start": v(10.03, -13.41) * mm, "end": v(10.07, -13.45) * mm});
            skLineSegment(sketch, "E291", {"start": v(10.07, -13.45) * mm, "end": v(10.15, -13.53) * mm});
            skLineSegment(sketch, "E292", {"start": v(10.15, -13.53) * mm, "end": v(10.22, -13.6) * mm});
            skLineSegment(sketch, "E293", {"start": v(10.22, -13.6) * mm, "end": v(10.3, -13.69) * mm});
            skLineSegment(sketch, "E294", {"start": v(10.3, -13.69) * mm, "end": v(10.39, -13.77) * mm});
            skLineSegment(sketch, "E295", {"start": v(10.39, -13.77) * mm, "end": v(10.47, -13.85) * mm});
            skLineSegment(sketch, "E296", {"start": v(10.47, -13.85) * mm, "end": v(10.56, -13.92) * mm});
            skLineSegment(sketch, "E297", {"start": v(10.56, -13.92) * mm, "end": v(10.65, -14) * mm});
            skLineSegment(sketch, "E298", {"start": v(10.65, -14) * mm, "end": v(10.74, -14.08) * mm});
            skLineSegment(sketch, "E299", {"start": v(10.74, -14.08) * mm, "end": v(10.86, -14.18) * mm});
            skLineSegment(sketch, "E300", {"start": v(10.86, -14.18) * mm, "end": v(10.98, -14.28) * mm});
            skLineSegment(sketch, "E301", {"start": v(10.98, -14.28) * mm, "end": v(11.6, -14.75) * mm});
            skLineSegment(sketch, "E302", {"start": v(11.6, -14.75) * mm, "end": v(11.73, -14.68) * mm});
            skLineSegment(sketch, "E303", {"start": v(11.73, -14.68) * mm, "end": v(11.88, -14.6) * mm});
            skLineSegment(sketch, "E304", {"start": v(11.88, -14.6) * mm, "end": v(12.02, -14.52) * mm});
            skLineSegment(sketch, "E305", {"start": v(12.02, -14.52) * mm, "end": v(12.17, -14.44) * mm});
            skLineSegment(sketch, "E306", {"start": v(12.17, -14.44) * mm, "end": v(12.31, -14.36) * mm});
            skLineSegment(sketch, "E307", {"start": v(12.31, -14.36) * mm, "end": v(12.45, -14.28) * mm});
            skLineSegment(sketch, "E308", {"start": v(12.45, -14.28) * mm, "end": v(12.55, -14.22) * mm});
            skLineSegment(sketch, "E309", {"start": v(12.55, -14.22) * mm, "end": v(12.49, -13.48) * mm});
            skLineSegment(sketch, "E310", {"start": v(12.49, -13.48) * mm, "end": v(12.47, -13.33) * mm});
            skLineSegment(sketch, "E311", {"start": v(12.47, -13.33) * mm, "end": v(12.46, -13.2) * mm});
            skLineSegment(sketch, "E312", {"start": v(12.46, -13.2) * mm, "end": v(12.44, -13.06) * mm});
            skLineSegment(sketch, "E313", {"start": v(12.44, -13.06) * mm, "end": v(12.42, -12.94) * mm});
            skLineSegment(sketch, "E314", {"start": v(12.42, -12.94) * mm, "end": v(12.4, -12.82) * mm});
            skLineSegment(sketch, "E315", {"start": v(12.4, -12.82) * mm, "end": v(12.38, -12.7) * mm});
            skLineSegment(sketch, "E316", {"start": v(12.38, -12.7) * mm, "end": v(12.35, -12.57) * mm});
            skLineSegment(sketch, "E317", {"start": v(12.35, -12.57) * mm, "end": v(12.33, -12.45) * mm});
            skLineSegment(sketch, "E318", {"start": v(12.33, -12.45) * mm, "end": v(12.3, -12.34) * mm});
            skLineSegment(sketch, "E319", {"start": v(12.3, -12.34) * mm, "end": v(12.27, -12.24) * mm});
            skLineSegment(sketch, "E320", {"start": v(12.27, -12.24) * mm, "end": v(12.26, -12.17) * mm});
            skLineSegment(sketch, "E321", {"start": v(12.26, -12.17) * mm, "end": v(12.25, -12.16) * mm});
            skLineSegment(sketch, "E322", {"start": v(12.25, -12.16) * mm, "end": v(12.24, -12.1) * mm});
            skLineSegment(sketch, "E323", {"start": v(12.24, -12.1) * mm, "end": v(12.21, -12.02) * mm});
            skLineSegment(sketch, "E324", {"start": v(12.21, -12.02) * mm, "end": v(12.19, -11.94) * mm});
            skLineSegment(sketch, "E325", {"start": v(12.19, -11.94) * mm, "end": v(12.16, -11.87) * mm});
            skLineSegment(sketch, "E326", {"start": v(12.16, -11.87) * mm, "end": v(12.14, -11.82) * mm});
            skLineSegment(sketch, "E327", {"start": v(12.14, -11.82) * mm, "end": v(12.12, -11.76) * mm});
            skLineSegment(sketch, "E328", {"start": v(12.12, -11.76) * mm, "end": v(12.1, -11.7) * mm});
            skLineSegment(sketch, "E329", {"start": v(12.1, -11.7) * mm, "end": v(12.08, -11.66) * mm});
            skLineSegment(sketch, "E330", {"start": v(12.08, -11.66) * mm, "end": v(12.06, -11.62) * mm});
            skLineSegment(sketch, "E331", {"start": v(12.06, -11.62) * mm, "end": v(12.04, -11.58) * mm});
            skLineSegment(sketch, "E332", {"start": v(12.04, -11.58) * mm, "end": v(12.03, -11.56) * mm});
            skLineSegment(sketch, "E333", {"start": v(12.03, -11.56) * mm, "end": v(11.87, -11.24) * mm});
            skLineSegment(sketch, "E334", {"start": v(11.87, -11.24) * mm, "end": v(11.87, -11.24) * mm});
            skLineSegment(sketch, "E335", {"start": v(11.87, -11.24) * mm, "end": v(11.83, -11.16) * mm});
            skLineSegment(sketch, "E336", {"start": v(11.83, -11.16) * mm, "end": v(11.84, -11.15) * mm});
            skLineSegment(sketch, "E337", {"start": v(11.84, -11.15) * mm, "end": v(11.8, -11.08) * mm});
            skLineSegment(sketch, "E338", {"start": v(11.8, -11.08) * mm, "end": v(11.82, -11.07) * mm});
            skLineSegment(sketch, "E339", {"start": v(11.82, -11.07) * mm, "end": v(11.79, -11) * mm});
            skLineSegment(sketch, "E340", {"start": v(11.79, -11) * mm, "end": v(11.79, -10.97) * mm});
            skLineSegment(sketch, "E341", {"start": v(11.79, -10.97) * mm, "end": v(11.79, -10.94) * mm});
            skLineSegment(sketch, "E342", {"start": v(11.79, -10.94) * mm, "end": v(11.77, -10.9) * mm});
            skLineSegment(sketch, "E343", {"start": v(11.77, -10.9) * mm, "end": v(11.77, -10.86) * mm});
            skLineSegment(sketch, "E344", {"start": v(11.77, -10.86) * mm, "end": v(11.78, -10.83) * mm});
            skLineSegment(sketch, "E345", {"start": v(11.78, -10.83) * mm, "end": v(11.77, -10.8) * mm});
            skLineSegment(sketch, "E346", {"start": v(11.77, -10.8) * mm, "end": v(11.78, -10.76) * mm});
            skLineSegment(sketch, "E347", {"start": v(11.78, -10.76) * mm, "end": v(11.79, -10.72) * mm});
            skLineSegment(sketch, "E348", {"start": v(11.79, -10.72) * mm, "end": v(11.8, -10.68) * mm});
            skLineSegment(sketch, "E349", {"start": v(11.8, -10.68) * mm, "end": v(11.82, -10.65) * mm});
            skLineSegment(sketch, "E350", {"start": v(11.82, -10.65) * mm, "end": v(11.82, -10.64) * mm});
            skLineSegment(sketch, "E351", {"start": v(11.82, -10.64) * mm, "end": v(11.83, -10.63) * mm});
            skLineSegment(sketch, "E352", {"start": v(11.83, -10.63) * mm, "end": v(11.84, -10.62) * mm});
            skLineSegment(sketch, "E353", {"start": v(11.84, -10.62) * mm, "end": v(11.85, -10.6) * mm});
            skLineSegment(sketch, "E354", {"start": v(11.85, -10.6) * mm, "end": v(12.05, -10.47) * mm});
            skLineSegment(sketch, "E355", {"start": v(12.05, -10.47) * mm, "end": v(12.19, -10.37) * mm});
            skLineSegment(sketch, "E356", {"start": v(12.19, -10.37) * mm, "end": v(12.26, -10.32) * mm});
            skLineSegment(sketch, "E357", {"start": v(12.26, -10.32) * mm, "end": v(12.4, -10.22) * mm});
            skLineSegment(sketch, "E358", {"start": v(12.4, -10.22) * mm, "end": v(12.6, -10.08) * mm});
            skLineSegment(sketch, "E359", {"start": v(12.6, -10.08) * mm, "end": v(12.6, -10.07) * mm});
            skLineSegment(sketch, "E360", {"start": v(12.6, -10.07) * mm, "end": v(12.62, -10.06) * mm});
            skLineSegment(sketch, "E361", {"start": v(12.62, -10.06) * mm, "end": v(12.63, -10.06) * mm});
            skLineSegment(sketch, "E362", {"start": v(12.63, -10.06) * mm, "end": v(12.64, -10.06) * mm});
            skLineSegment(sketch, "E363", {"start": v(12.64, -10.06) * mm, "end": v(12.68, -10.05) * mm});
            skLineSegment(sketch, "E364", {"start": v(12.68, -10.05) * mm, "end": v(12.72, -10.05) * mm});
            skLineSegment(sketch, "E365", {"start": v(12.72, -10.05) * mm, "end": v(12.77, -10.06) * mm});
            skLineSegment(sketch, "E366", {"start": v(12.77, -10.06) * mm, "end": v(12.8, -10.06) * mm});
            skLineSegment(sketch, "E367", {"start": v(12.8, -10.06) * mm, "end": v(12.83, -10.08) * mm});
            skLineSegment(sketch, "E368", {"start": v(12.83, -10.08) * mm, "end": v(12.86, -10.09) * mm});
            skLineSegment(sketch, "E369", {"start": v(12.86, -10.09) * mm, "end": v(12.9, -10.1) * mm});
            skLineSegment(sketch, "E370", {"start": v(12.9, -10.1) * mm, "end": v(12.94, -10.12) * mm});
            skLineSegment(sketch, "E371", {"start": v(12.94, -10.12) * mm, "end": v(12.97, -10.15) * mm});
            skLineSegment(sketch, "E372", {"start": v(12.97, -10.15) * mm, "end": v(13, -10.16) * mm});
            skLineSegment(sketch, "E373", {"start": v(13, -10.16) * mm, "end": v(13.03, -10.18) * mm});
            skLineSegment(sketch, "E374", {"start": v(13.03, -10.18) * mm, "end": v(13.08, -10.22) * mm});
            skLineSegment(sketch, "E375", {"start": v(13.08, -10.22) * mm, "end": v(13.1, -10.24) * mm});
            skLineSegment(sketch, "E376", {"start": v(13.1, -10.24) * mm, "end": v(13.14, -10.26) * mm});
            skLineSegment(sketch, "E377", {"start": v(13.14, -10.26) * mm, "end": v(13.37, -10.49) * mm});
            skLineSegment(sketch, "E378", {"start": v(13.37, -10.49) * mm, "end": v(13.4, -10.52) * mm});
            skLineSegment(sketch, "E379", {"start": v(13.4, -10.52) * mm, "end": v(13.43, -10.55) * mm});
            skLineSegment(sketch, "E380", {"start": v(13.43, -10.55) * mm, "end": v(13.47, -10.6) * mm});
            skLineSegment(sketch, "E381", {"start": v(13.47, -10.6) * mm, "end": v(13.51, -10.63) * mm});
            skLineSegment(sketch, "E382", {"start": v(13.51, -10.63) * mm, "end": v(13.56, -10.67) * mm});
            skLineSegment(sketch, "E383", {"start": v(13.56, -10.67) * mm, "end": v(13.61, -10.7) * mm});
            skLineSegment(sketch, "E384", {"start": v(13.61, -10.7) * mm, "end": v(13.67, -10.76) * mm});
            skLineSegment(sketch, "E385", {"start": v(13.67, -10.76) * mm, "end": v(13.74, -10.81) * mm});
            skLineSegment(sketch, "E386", {"start": v(13.74, -10.81) * mm, "end": v(13.81, -10.86) * mm});
            skLineSegment(sketch, "E387", {"start": v(13.81, -10.86) * mm, "end": v(13.89, -10.92) * mm});
            skLineSegment(sketch, "E388", {"start": v(13.89, -10.92) * mm, "end": v(13.93, -10.95) * mm});
            skLineSegment(sketch, "E389", {"start": v(13.93, -10.95) * mm, "end": v(13.96, -10.96) * mm});
            skLineSegment(sketch, "E390", {"start": v(13.96, -10.96) * mm, "end": v(14, -11) * mm});
            skLineSegment(sketch, "E391", {"start": v(14, -11) * mm, "end": v(14.09, -11.05) * mm});
            skLineSegment(sketch, "E392", {"start": v(14.09, -11.05) * mm, "end": v(14.18, -11.1) * mm});
            skLineSegment(sketch, "E393", {"start": v(14.18, -11.1) * mm, "end": v(14.27, -11.16) * mm});
            skLineSegment(sketch, "E394", {"start": v(14.27, -11.16) * mm, "end": v(14.37, -11.22) * mm});
            skLineSegment(sketch, "E395", {"start": v(14.37, -11.22) * mm, "end": v(14.47, -11.27) * mm});
            skLineSegment(sketch, "E396", {"start": v(14.47, -11.27) * mm, "end": v(14.57, -11.33) * mm});
            skLineSegment(sketch, "E397", {"start": v(14.57, -11.33) * mm, "end": v(14.68, -11.39) * mm});
            skLineSegment(sketch, "E398", {"start": v(14.68, -11.39) * mm, "end": v(14.8, -11.45) * mm});
            skLineSegment(sketch, "E399", {"start": v(14.8, -11.45) * mm, "end": v(14.94, -11.51) * mm});
            skLineSegment(sketch, "E400", {"start": v(14.94, -11.51) * mm, "end": v(15.09, -11.57) * mm});
            skLineSegment(sketch, "E401", {"start": v(15.09, -11.57) * mm, "end": v(15.81, -11.88) * mm});
            skLineSegment(sketch, "E402", {"start": v(15.81, -11.88) * mm, "end": v(15.82, -11.87) * mm});
            skLineSegment(sketch, "E403", {"start": v(15.82, -11.87) * mm, "end": v(15.92, -11.78) * mm});
            skLineSegment(sketch, "E404", {"start": v(15.92, -11.78) * mm, "end": v(16.02, -11.7) * mm});
            skLineSegment(sketch, "E405", {"start": v(16.02, -11.7) * mm, "end": v(16.11, -11.6) * mm});
            skLineSegment(sketch, "E406", {"start": v(16.11, -11.6) * mm, "end": v(16.21, -11.51) * mm});
            skLineSegment(sketch, "E407", {"start": v(16.21, -11.51) * mm, "end": v(16.3, -11.42) * mm});
            skLineSegment(sketch, "E408", {"start": v(16.3, -11.42) * mm, "end": v(16.4, -11.33) * mm});
            skLineSegment(sketch, "E409", {"start": v(16.4, -11.33) * mm, "end": v(16.5, -11.24) * mm});
            skLineSegment(sketch, "E410", {"start": v(16.5, -11.24) * mm, "end": v(16.59, -11.15) * mm});
            skLineSegment(sketch, "E411", {"start": v(16.59, -11.15) * mm, "end": v(16.6, -11.15) * mm});
            skLineSegment(sketch, "E412", {"start": v(16.6, -11.15) * mm, "end": v(16.35, -10.42) * mm});
            skLineSegment(sketch, "E413", {"start": v(16.35, -10.42) * mm, "end": v(16.3, -10.28) * mm});
            skLineSegment(sketch, "E414", {"start": v(16.3, -10.28) * mm, "end": v(16.25, -10.16) * mm});
            skLineSegment(sketch, "E415", {"start": v(16.25, -10.16) * mm, "end": v(16.2, -10.04) * mm});
            skLineSegment(sketch, "E416", {"start": v(16.2, -10.04) * mm, "end": v(16.15, -9.91) * mm});
            skLineSegment(sketch, "E417", {"start": v(16.15, -9.91) * mm, "end": v(16.1, -9.78) * mm});
            skLineSegment(sketch, "E418", {"start": v(16.1, -9.78) * mm, "end": v(16.03, -9.66) * mm});
            skLineSegment(sketch, "E419", {"start": v(16.03, -9.66) * mm, "end": v(15.98, -9.56) * mm});
            skLineSegment(sketch, "E420", {"start": v(15.98, -9.56) * mm, "end": v(15.93, -9.45) * mm});
            skLineSegment(sketch, "E421", {"start": v(15.93, -9.45) * mm, "end": v(15.88, -9.36) * mm});
            skLineSegment(sketch, "E422", {"start": v(15.88, -9.36) * mm, "end": v(15.83, -9.28) * mm});
            skLineSegment(sketch, "E423", {"start": v(15.83, -9.28) * mm, "end": v(15.8, -9.24) * mm});
            skLineSegment(sketch, "E424", {"start": v(15.8, -9.24) * mm, "end": v(15.8, -9.22) * mm});
            skLineSegment(sketch, "E425", {"start": v(15.8, -9.22) * mm, "end": v(15.77, -9.18) * mm});
            skLineSegment(sketch, "E426", {"start": v(15.77, -9.18) * mm, "end": v(15.73, -9.11) * mm});
            skLineSegment(sketch, "E427", {"start": v(15.73, -9.11) * mm, "end": v(15.69, -9.05) * mm});
            skLineSegment(sketch, "E428", {"start": v(15.69, -9.05) * mm, "end": v(15.65, -9) * mm});
            skLineSegment(sketch, "E429", {"start": v(15.65, -9) * mm, "end": v(15.62, -8.95) * mm});
            skLineSegment(sketch, "E430", {"start": v(15.62, -8.95) * mm, "end": v(15.58, -8.9) * mm});
            skLineSegment(sketch, "E431", {"start": v(15.58, -8.9) * mm, "end": v(15.55, -8.87) * mm});
            skLineSegment(sketch, "E432", {"start": v(15.55, -8.87) * mm, "end": v(15.53, -8.84) * mm});
            skLineSegment(sketch, "E433", {"start": v(15.53, -8.84) * mm, "end": v(15.5, -8.81) * mm});
            skLineSegment(sketch, "E434", {"start": v(15.5, -8.81) * mm, "end": v(15.49, -8.8) * mm});
            skLineSegment(sketch, "E435", {"start": v(15.49, -8.8) * mm, "end": v(15.48, -8.78) * mm});
            skLineSegment(sketch, "E436", {"start": v(15.48, -8.78) * mm, "end": v(15.23, -8.53) * mm});
            skLineSegment(sketch, "E437", {"start": v(15.23, -8.53) * mm, "end": v(15.23, -8.52) * mm});
            skLineSegment(sketch, "E438", {"start": v(15.23, -8.52) * mm, "end": v(15.16, -8.45) * mm});
            skLineSegment(sketch, "E439", {"start": v(15.16, -8.45) * mm, "end": v(15.17, -8.44) * mm});
            skLineSegment(sketch, "E440", {"start": v(15.17, -8.44) * mm, "end": v(15.11, -8.38) * mm});
            skLineSegment(sketch, "E441", {"start": v(15.11, -8.38) * mm, "end": v(15.12, -8.37) * mm});
            skLineSegment(sketch, "E442", {"start": v(15.12, -8.37) * mm, "end": v(15.06, -8.3) * mm});
            skLineSegment(sketch, "E443", {"start": v(15.06, -8.3) * mm, "end": v(15.07, -8.3) * mm});
            skLineSegment(sketch, "E444", {"start": v(15.07, -8.3) * mm, "end": v(15.03, -8.24) * mm});
            skLineSegment(sketch, "E445", {"start": v(15.03, -8.24) * mm, "end": v(15.04, -8.22) * mm});
            skLineSegment(sketch, "E446", {"start": v(15.04, -8.22) * mm, "end": v(15, -8.17) * mm});
            skLineSegment(sketch, "E447", {"start": v(15, -8.17) * mm, "end": v(15, -8.15) * mm});
            skLineSegment(sketch, "E448", {"start": v(15, -8.15) * mm, "end": v(14.98, -8.1) * mm});
            skLineSegment(sketch, "E449", {"start": v(14.98, -8.1) * mm, "end": v(15, -8.08) * mm});
            skLineSegment(sketch, "E450", {"start": v(15, -8.08) * mm, "end": v(14.96, -8.04) * mm});
            skLineSegment(sketch, "E451", {"start": v(14.96, -8.04) * mm, "end": v(14.97, -8) * mm});
            skLineSegment(sketch, "E452", {"start": v(14.97, -8) * mm, "end": v(14.97, -7.97) * mm});
            skLineSegment(sketch, "E453", {"start": v(14.97, -7.97) * mm, "end": v(14.97, -7.94) * mm});
            skLineSegment(sketch, "E454", {"start": v(14.97, -7.94) * mm, "end": v(14.97, -7.9) * mm});
            skLineSegment(sketch, "E455", {"start": v(14.97, -7.9) * mm, "end": v(14.98, -7.87) * mm});
            skLineSegment(sketch, "E456", {"start": v(14.98, -7.87) * mm, "end": v(14.98, -7.86) * mm});
            skLineSegment(sketch, "E457", {"start": v(14.98, -7.86) * mm, "end": v(15, -7.84) * mm});
            skLineSegment(sketch, "E458", {"start": v(15, -7.84) * mm, "end": v(15, -7.83) * mm});
            skLineSegment(sketch, "E459", {"start": v(15, -7.83) * mm, "end": v(15.17, -7.62) * mm});
            skLineSegment(sketch, "E460", {"start": v(15.17, -7.62) * mm, "end": v(15.27, -7.5) * mm});
            skLineSegment(sketch, "E461", {"start": v(15.27, -7.5) * mm, "end": v(15.3, -7.45) * mm});
            skLineSegment(sketch, "E462", {"start": v(15.3, -7.45) * mm, "end": v(15.4, -7.33) * mm});
            skLineSegment(sketch, "E463", {"start": v(15.4, -7.33) * mm, "end": v(15.57, -7.12) * mm});
            skLineSegment(sketch, "E464", {"start": v(15.57, -7.12) * mm, "end": v(15.58, -7.1) * mm});
            skLineSegment(sketch, "E465", {"start": v(15.58, -7.1) * mm, "end": v(15.6, -7.1) * mm});
            skLineSegment(sketch, "E466", {"start": v(15.6, -7.1) * mm, "end": v(15.6, -7.1) * mm});
            skLineSegment(sketch, "E467", {"start": v(15.6, -7.1) * mm, "end": v(15.61, -7.1) * mm});
            skLineSegment(sketch, "E468", {"start": v(15.61, -7.1) * mm, "end": v(15.65, -7.07) * mm});
            skLineSegment(sketch, "E469", {"start": v(15.65, -7.07) * mm, "end": v(15.68, -7.05) * mm});
            skLineSegment(sketch, "E470", {"start": v(15.68, -7.05) * mm, "end": v(15.7, -7.06) * mm});
            skLineSegment(sketch, "E471", {"start": v(15.7, -7.06) * mm, "end": v(15.74, -7.05) * mm});
            skLineSegment(sketch, "E472", {"start": v(15.74, -7.05) * mm, "end": v(15.78, -7.04) * mm});
            skLineSegment(sketch, "E473", {"start": v(15.78, -7.04) * mm, "end": v(15.82, -7.06) * mm});
            skLineSegment(sketch, "E474", {"start": v(15.82, -7.06) * mm, "end": v(15.86, -7.05) * mm});
            skLineSegment(sketch, "E475", {"start": v(15.86, -7.05) * mm, "end": v(15.9, -7.05) * mm});
            skLineSegment(sketch, "E476", {"start": v(15.9, -7.05) * mm, "end": v(15.95, -7.08) * mm});
            skLineSegment(sketch, "E477", {"start": v(15.95, -7.08) * mm, "end": v(15.99, -7.08) * mm});
            skLineSegment(sketch, "E478", {"start": v(15.99, -7.08) * mm, "end": v(16.02, -7.08) * mm});
            skLineSegment(sketch, "E479", {"start": v(16.02, -7.08) * mm, "end": v(16.08, -7.11) * mm});
            skLineSegment(sketch, "E480", {"start": v(16.08, -7.11) * mm, "end": v(16.12, -7.12) * mm});
            skLineSegment(sketch, "E481", {"start": v(16.12, -7.12) * mm, "end": v(16.15, -7.13) * mm});
            skLineSegment(sketch, "E482", {"start": v(16.15, -7.13) * mm, "end": v(16.22, -7.17) * mm});
            skLineSegment(sketch, "E483", {"start": v(16.22, -7.17) * mm, "end": v(16.22, -7.17) * mm});
            skLineSegment(sketch, "E484", {"start": v(16.22, -7.17) * mm, "end": v(16.52, -7.35) * mm});
            skLineSegment(sketch, "E485", {"start": v(16.52, -7.35) * mm, "end": v(16.55, -7.36) * mm});
            skLineSegment(sketch, "E486", {"start": v(16.55, -7.36) * mm, "end": v(16.58, -7.38) * mm});
            skLineSegment(sketch, "E487", {"start": v(16.58, -7.38) * mm, "end": v(16.61, -7.4) * mm});
            skLineSegment(sketch, "E488", {"start": v(16.61, -7.4) * mm, "end": v(16.66, -7.42) * mm});
            skLineSegment(sketch, "E489", {"start": v(16.66, -7.42) * mm, "end": v(16.71, -7.45) * mm});
            skLineSegment(sketch, "E490", {"start": v(16.71, -7.45) * mm, "end": v(16.77, -7.48) * mm});
            skLineSegment(sketch, "E491", {"start": v(16.77, -7.48) * mm, "end": v(16.84, -7.5) * mm});
            skLineSegment(sketch, "E492", {"start": v(16.84, -7.5) * mm, "end": v(16.9, -7.53) * mm});
            skLineSegment(sketch, "E493", {"start": v(16.9, -7.53) * mm, "end": v(16.98, -7.56) * mm});
            skLineSegment(sketch, "E494", {"start": v(16.98, -7.56) * mm, "end": v(17.05, -7.6) * mm});
            skLineSegment(sketch, "E495", {"start": v(17.05, -7.6) * mm, "end": v(17.1, -7.6) * mm});
            skLineSegment(sketch, "E496", {"start": v(17.1, -7.6) * mm, "end": v(17.12, -7.61) * mm});
            skLineSegment(sketch, "E497", {"start": v(17.12, -7.61) * mm, "end": v(17.16, -7.63) * mm});
            skLineSegment(sketch, "E498", {"start": v(17.16, -7.63) * mm, "end": v(17.25, -7.66) * mm});
            skLineSegment(sketch, "E499", {"start": v(17.25, -7.66) * mm, "end": v(17.34, -7.68) * mm});
            skLineSegment(sketch, "E500", {"start": v(17.34, -7.68) * mm, "end": v(17.44, -7.7) * mm});
            skLineSegment(sketch, "E501", {"start": v(17.44, -7.7) * mm, "end": v(17.55, -7.74) * mm});
            skLineSegment(sketch, "E502", {"start": v(17.55, -7.74) * mm, "end": v(17.68, -7.77) * mm});
            skLineSegment(sketch, "E503", {"start": v(17.68, -7.77) * mm, "end": v(17.8, -7.8) * mm});
            skLineSegment(sketch, "E504", {"start": v(17.8, -7.8) * mm, "end": v(17.94, -7.82) * mm});
            skLineSegment(sketch, "E505", {"start": v(17.94, -7.82) * mm, "end": v(18.08, -7.84) * mm});
            skLineSegment(sketch, "E506", {"start": v(18.08, -7.84) * mm, "end": v(18.23, -7.86) * mm});
            skLineSegment(sketch, "E507", {"start": v(18.23, -7.86) * mm, "end": v(18.39, -7.88) * mm});
            skLineSegment(sketch, "E508", {"start": v(18.39, -7.88) * mm, "end": v(19.16, -7.95) * mm});
            skLineSegment(sketch, "E509", {"start": v(19.16, -7.95) * mm, "end": v(19.2, -7.88) * mm});
            skLineSegment(sketch, "E510", {"start": v(19.2, -7.88) * mm, "end": v(19.26, -7.79) * mm});
            skLineSegment(sketch, "E511", {"start": v(19.26, -7.79) * mm, "end": v(19.32, -7.7) * mm});
            skLineSegment(sketch, "E512", {"start": v(19.32, -7.7) * mm, "end": v(19.37, -7.6) * mm});
            skLineSegment(sketch, "E513", {"start": v(19.37, -7.6) * mm, "end": v(19.43, -7.51) * mm});
            skLineSegment(sketch, "E514", {"start": v(19.43, -7.51) * mm, "end": v(19.48, -7.42) * mm});
            skLineSegment(sketch, "E515", {"start": v(19.48, -7.42) * mm, "end": v(19.53, -7.33) * mm});
            skLineSegment(sketch, "E516", {"start": v(19.53, -7.33) * mm, "end": v(19.58, -7.24) * mm});
            skLineSegment(sketch, "E517", {"start": v(19.58, -7.24) * mm, "end": v(19.63, -7.15) * mm});
            skLineSegment(sketch, "E518", {"start": v(19.63, -7.15) * mm, "end": v(19.68, -7.06) * mm});
            skLineSegment(sketch, "E519", {"start": v(19.68, -7.06) * mm, "end": v(19.69, -7.04) * mm});
            skLineSegment(sketch, "E520", {"start": v(19.69, -7.04) * mm, "end": v(19.23, -6.4) * mm});
            skLineSegment(sketch, "E521", {"start": v(19.23, -6.4) * mm, "end": v(19.14, -6.27) * mm});
            skLineSegment(sketch, "E522", {"start": v(19.14, -6.27) * mm, "end": v(19.05, -6.14) * mm});
            skLineSegment(sketch, "E523", {"start": v(19.05, -6.14) * mm, "end": v(18.95, -6.03) * mm});
            skLineSegment(sketch, "E524", {"start": v(18.95, -6.03) * mm, "end": v(18.87, -5.93) * mm});
            skLineSegment(sketch, "E525", {"start": v(18.87, -5.93) * mm, "end": v(18.78, -5.83) * mm});
            skLineSegment(sketch, "E526", {"start": v(18.78, -5.83) * mm, "end": v(18.7, -5.74) * mm});
            skLineSegment(sketch, "E527", {"start": v(18.7, -5.74) * mm, "end": v(18.62, -5.66) * mm});
            skLineSegment(sketch, "E528", {"start": v(18.62, -5.66) * mm, "end": v(18.55, -5.6) * mm});
            skLineSegment(sketch, "E529", {"start": v(18.55, -5.6) * mm, "end": v(18.48, -5.53) * mm});
            skLineSegment(sketch, "E530", {"start": v(18.48, -5.53) * mm, "end": v(18.41, -5.47) * mm});
            skLineSegment(sketch, "E531", {"start": v(18.41, -5.47) * mm, "end": v(18.38, -5.44) * mm});
            skLineSegment(sketch, "E532", {"start": v(18.38, -5.44) * mm, "end": v(18.37, -5.43) * mm});
            skLineSegment(sketch, "E533", {"start": v(18.37, -5.43) * mm, "end": v(18.34, -5.4) * mm});
            skLineSegment(sketch, "E534", {"start": v(18.34, -5.4) * mm, "end": v(18.28, -5.35) * mm});
            skLineSegment(sketch, "E535", {"start": v(18.28, -5.35) * mm, "end": v(18.22, -5.3) * mm});
            skLineSegment(sketch, "E536", {"start": v(18.22, -5.3) * mm, "end": v(18.17, -5.27) * mm});
            skLineSegment(sketch, "E537", {"start": v(18.17, -5.27) * mm, "end": v(18.13, -5.24) * mm});
            skLineSegment(sketch, "E538", {"start": v(18.13, -5.24) * mm, "end": v(18.09, -5.22) * mm});
            skLineSegment(sketch, "E539", {"start": v(18.09, -5.22) * mm, "end": v(18.06, -5.2) * mm});
            skLineSegment(sketch, "E540", {"start": v(18.06, -5.2) * mm, "end": v(18.03, -5.18) * mm});
            skLineSegment(sketch, "E541", {"start": v(18.03, -5.18) * mm, "end": v(18.02, -5.17) * mm});
            skLineSegment(sketch, "E542", {"start": v(18.02, -5.17) * mm, "end": v(18, -5.17) * mm});
            skLineSegment(sketch, "E543", {"start": v(18, -5.17) * mm, "end": v(18, -5.17) * mm});
            skLineSegment(sketch, "E544", {"start": v(18, -5.17) * mm, "end": v(17.69, -5.02) * mm});
            skLineSegment(sketch, "E545", {"start": v(17.69, -5.02) * mm, "end": v(17.69, -5.01) * mm});
            skLineSegment(sketch, "E546", {"start": v(17.69, -5.01) * mm, "end": v(17.6, -4.96) * mm});
            skLineSegment(sketch, "E547", {"start": v(17.6, -4.96) * mm, "end": v(17.6, -4.95) * mm});
            skLineSegment(sketch, "E548", {"start": v(17.6, -4.95) * mm, "end": v(17.5, -4.9) * mm});
            skLineSegment(sketch, "E549", {"start": v(17.5, -4.9) * mm, "end": v(17.5, -4.9) * mm});
            skLineSegment(sketch, "E550", {"start": v(17.5, -4.9) * mm, "end": v(17.43, -4.85) * mm});
            skLineSegment(sketch, "E551", {"start": v(17.43, -4.85) * mm, "end": v(17.43, -4.83) * mm});
            skLineSegment(sketch, "E552", {"start": v(17.43, -4.83) * mm, "end": v(17.36, -4.79) * mm});
            skLineSegment(sketch, "E553", {"start": v(17.36, -4.79) * mm, "end": v(17.37, -4.77) * mm});
            skLineSegment(sketch, "E554", {"start": v(17.37, -4.77) * mm, "end": v(17.3, -4.73) * mm});
            skLineSegment(sketch, "E555", {"start": v(17.3, -4.73) * mm, "end": v(17.31, -4.7) * mm});
            skLineSegment(sketch, "E556", {"start": v(17.31, -4.7) * mm, "end": v(17.26, -4.67) * mm});
            skLineSegment(sketch, "E557", {"start": v(17.26, -4.67) * mm, "end": v(17.27, -4.64) * mm});
            skLineSegment(sketch, "E558", {"start": v(17.27, -4.64) * mm, "end": v(17.22, -4.61) * mm});
            skLineSegment(sketch, "E559", {"start": v(17.22, -4.61) * mm, "end": v(17.23, -4.58) * mm});
            skLineSegment(sketch, "E560", {"start": v(17.23, -4.58) * mm, "end": v(17.2, -4.56) * mm});
            skLineSegment(sketch, "E561", {"start": v(17.2, -4.56) * mm, "end": v(17.2, -4.52) * mm});
            skLineSegment(sketch, "E562", {"start": v(17.2, -4.52) * mm, "end": v(17.17, -4.5) * mm});
            skLineSegment(sketch, "E563", {"start": v(17.17, -4.5) * mm, "end": v(17.19, -4.46) * mm});
            skLineSegment(sketch, "E564", {"start": v(17.19, -4.46) * mm, "end": v(17.17, -4.43) * mm});
            skLineSegment(sketch, "E565", {"start": v(17.17, -4.43) * mm, "end": v(17.17, -4.4) * mm});
            skLineSegment(sketch, "E566", {"start": v(17.17, -4.4) * mm, "end": v(17.17, -4.4) * mm});
            skLineSegment(sketch, "E567", {"start": v(17.17, -4.4) * mm, "end": v(17.17, -4.37) * mm});
            skLineSegment(sketch, "E568", {"start": v(17.17, -4.37) * mm, "end": v(17.18, -4.35) * mm});
            skLineSegment(sketch, "E569", {"start": v(17.18, -4.35) * mm, "end": v(17.28, -4.1) * mm});
            skLineSegment(sketch, "E570", {"start": v(17.28, -4.1) * mm, "end": v(17.33, -3.96) * mm});
            skLineSegment(sketch, "E571", {"start": v(17.33, -3.96) * mm, "end": v(17.35, -3.9) * mm});
            skLineSegment(sketch, "E572", {"start": v(17.35, -3.9) * mm, "end": v(17.4, -3.78) * mm});
            skLineSegment(sketch, "E573", {"start": v(17.4, -3.78) * mm, "end": v(17.5, -3.51) * mm});
            skLineSegment(sketch, "E574", {"start": v(17.5, -3.51) * mm, "end": v(17.5, -3.5) * mm});
            skLineSegment(sketch, "E575", {"start": v(17.5, -3.5) * mm, "end": v(17.51, -3.47) * mm});
            skLineSegment(sketch, "E576", {"start": v(17.51, -3.47) * mm, "end": v(17.52, -3.47) * mm});
            skLineSegment(sketch, "E577", {"start": v(17.52, -3.47) * mm, "end": v(17.53, -3.46) * mm});
            skLineSegment(sketch, "E578", {"start": v(17.53, -3.46) * mm, "end": v(17.55, -3.43) * mm});
            skLineSegment(sketch, "E579", {"start": v(17.55, -3.43) * mm, "end": v(17.58, -3.42) * mm});
            skLineSegment(sketch, "E580", {"start": v(17.58, -3.42) * mm, "end": v(17.62, -3.4) * mm});
            skLineSegment(sketch, "E581", {"start": v(17.62, -3.4) * mm, "end": v(17.63, -3.37) * mm});
            skLineSegment(sketch, "E582", {"start": v(17.63, -3.37) * mm, "end": v(17.67, -3.38) * mm});
            skLineSegment(sketch, "E583", {"start": v(17.67, -3.38) * mm, "end": v(17.68, -3.35) * mm});
            skLineSegment(sketch, "E584", {"start": v(17.68, -3.35) * mm, "end": v(17.72, -3.36) * mm});
            skLineSegment(sketch, "E585", {"start": v(17.72, -3.36) * mm, "end": v(17.74, -3.33) * mm});
            skLineSegment(sketch, "E586", {"start": v(17.74, -3.33) * mm, "end": v(17.8, -3.34) * mm});
            skLineSegment(sketch, "E587", {"start": v(17.8, -3.34) * mm, "end": v(17.8, -3.32) * mm});
            skLineSegment(sketch, "E588", {"start": v(17.8, -3.32) * mm, "end": v(17.86, -3.33) * mm});
            skLineSegment(sketch, "E589", {"start": v(17.86, -3.33) * mm, "end": v(17.87, -3.31) * mm});
            skLineSegment(sketch, "E590", {"start": v(17.87, -3.31) * mm, "end": v(17.94, -3.32) * mm});
            skLineSegment(sketch, "E591", {"start": v(17.94, -3.32) * mm, "end": v(17.95, -3.3) * mm});
            skLineSegment(sketch, "E592", {"start": v(17.95, -3.3) * mm, "end": v(18.03, -3.32) * mm});
            skLineSegment(sketch, "E593", {"start": v(18.03, -3.32) * mm, "end": v(18.04, -3.31) * mm});
            skLineSegment(sketch, "E594", {"start": v(18.04, -3.31) * mm, "end": v(18.12, -3.33) * mm});
            skLineSegment(sketch, "E595", {"start": v(18.12, -3.33) * mm, "end": v(18.13, -3.32) * mm});
            skLineSegment(sketch, "E596", {"start": v(18.13, -3.32) * mm, "end": v(18.21, -3.34) * mm});
            skLineSegment(sketch, "E597", {"start": v(18.21, -3.34) * mm, "end": v(18.21, -3.33) * mm});
            skLineSegment(sketch, "E598", {"start": v(18.21, -3.33) * mm, "end": v(18.57, -3.43) * mm});
            skLineSegment(sketch, "E599", {"start": v(18.57, -3.43) * mm, "end": v(18.6, -3.43) * mm});
            skLineSegment(sketch, "E600", {"start": v(18.6, -3.43) * mm, "end": v(18.62, -3.44) * mm});
            skLineSegment(sketch, "E601", {"start": v(18.62, -3.44) * mm, "end": v(18.66, -3.45) * mm});
            skLineSegment(sketch, "E602", {"start": v(18.66, -3.45) * mm, "end": v(18.7, -3.45) * mm});
            skLineSegment(sketch, "E603", {"start": v(18.7, -3.45) * mm, "end": v(18.75, -3.46) * mm});
            skLineSegment(sketch, "E604", {"start": v(18.75, -3.46) * mm, "end": v(18.8, -3.47) * mm});
            skLineSegment(sketch, "E605", {"start": v(18.8, -3.47) * mm, "end": v(18.85, -3.47) * mm});
            skLineSegment(sketch, "E606", {"start": v(18.85, -3.47) * mm, "end": v(18.92, -3.48) * mm});
            skLineSegment(sketch, "E607", {"start": v(18.92, -3.48) * mm, "end": v(18.98, -3.48) * mm});
            skLineSegment(sketch, "E608", {"start": v(18.98, -3.48) * mm, "end": v(19.06, -3.48) * mm});
            skLineSegment(sketch, "E609", {"start": v(19.06, -3.48) * mm, "end": v(19.1, -3.48) * mm});
            skLineSegment(sketch, "E610", {"start": v(19.1, -3.48) * mm, "end": v(19.11, -3.49) * mm});
            skLineSegment(sketch, "E611", {"start": v(19.11, -3.49) * mm, "end": v(19.16, -3.49) * mm});
            skLineSegment(sketch, "E612", {"start": v(19.16, -3.49) * mm, "end": v(19.25, -3.48) * mm});
            skLineSegment(sketch, "E613", {"start": v(19.25, -3.48) * mm, "end": v(19.35, -3.48) * mm});
            skLineSegment(sketch, "E614", {"start": v(19.35, -3.48) * mm, "end": v(19.47, -3.47) * mm});
            skLineSegment(sketch, "E615", {"start": v(19.47, -3.47) * mm, "end": v(19.58, -3.46) * mm});
            skLineSegment(sketch, "E616", {"start": v(19.58, -3.46) * mm, "end": v(19.7, -3.45) * mm});
            skLineSegment(sketch, "E617", {"start": v(19.7, -3.45) * mm, "end": v(19.84, -3.43) * mm});
            skLineSegment(sketch, "E618", {"start": v(19.84, -3.43) * mm, "end": v(19.98, -3.4) * mm});
            skLineSegment(sketch, "E619", {"start": v(19.98, -3.4) * mm, "end": v(20.12, -3.38) * mm});
            skLineSegment(sketch, "E620", {"start": v(20.12, -3.38) * mm, "end": v(20.27, -3.35) * mm});
            skLineSegment(sketch, "E621", {"start": v(20.27, -3.35) * mm, "end": v(20.43, -3.3) * mm});
            skLineSegment(sketch, "E622", {"start": v(20.43, -3.3) * mm, "end": v(21.16, -3.1) * mm});
            skLineSegment(sketch, "E623", {"start": v(21.16, -3.1) * mm, "end": v(21.17, -3.08) * mm});
            skLineSegment(sketch, "E624", {"start": v(21.17, -3.08) * mm, "end": v(21.18, -2.99) * mm});
            skLineSegment(sketch, "E625", {"start": v(21.18, -2.99) * mm, "end": v(21.2, -2.9) * mm});
            skLineSegment(sketch, "E626", {"start": v(21.2, -2.9) * mm, "end": v(21.22, -2.8) * mm});
            skLineSegment(sketch, "E627", {"start": v(21.22, -2.8) * mm, "end": v(21.24, -2.72) * mm});
            skLineSegment(sketch, "E628", {"start": v(21.24, -2.72) * mm, "end": v(21.26, -2.63) * mm});
            skLineSegment(sketch, "E629", {"start": v(21.26, -2.63) * mm, "end": v(21.27, -2.54) * mm});
            skLineSegment(sketch, "E630", {"start": v(21.27, -2.54) * mm, "end": v(21.29, -2.45) * mm});
            skLineSegment(sketch, "E631", {"start": v(21.29, -2.45) * mm, "end": v(21.3, -2.36) * mm});
            skLineSegment(sketch, "E632", {"start": v(21.3, -2.36) * mm, "end": v(21.32, -2.27) * mm});
            skLineSegment(sketch, "E633", {"start": v(21.32, -2.27) * mm, "end": v(21.33, -2.18) * mm});
            skLineSegment(sketch, "E634", {"start": v(21.33, -2.18) * mm, "end": v(21.34, -2.12) * mm});
            skLineSegment(sketch, "E635", {"start": v(21.34, -2.12) * mm, "end": v(20.7, -1.66) * mm});
            skLineSegment(sketch, "E636", {"start": v(20.7, -1.66) * mm, "end": v(20.58, -1.57) * mm});
            skLineSegment(sketch, "E637", {"start": v(20.58, -1.57) * mm, "end": v(20.45, -1.49) * mm});
            skLineSegment(sketch, "E638", {"start": v(20.45, -1.49) * mm, "end": v(20.32, -1.4) * mm});
            skLineSegment(sketch, "E639", {"start": v(20.32, -1.4) * mm, "end": v(20.2, -1.34) * mm});
            skLineSegment(sketch, "E640", {"start": v(20.2, -1.34) * mm, "end": v(20.09, -1.28) * mm});
            skLineSegment(sketch, "E641", {"start": v(20.09, -1.28) * mm, "end": v(19.98, -1.22) * mm});
            skLineSegment(sketch, "E642", {"start": v(19.98, -1.22) * mm, "end": v(19.88, -1.17) * mm});
            skLineSegment(sketch, "E643", {"start": v(19.88, -1.17) * mm, "end": v(19.78, -1.13) * mm});
            skLineSegment(sketch, "E644", {"start": v(19.78, -1.13) * mm, "end": v(19.7, -1.1) * mm});
            skLineSegment(sketch, "E645", {"start": v(19.7, -1.1) * mm, "end": v(19.6, -1.06) * mm});
            skLineSegment(sketch, "E646", {"start": v(19.6, -1.06) * mm, "end": v(19.56, -1.04) * mm});
            skLineSegment(sketch, "E647", {"start": v(19.56, -1.04) * mm, "end": v(19.55, -1.04) * mm});
            skLineSegment(sketch, "E648", {"start": v(19.55, -1.04) * mm, "end": v(19.51, -1.02) * mm});
            skLineSegment(sketch, "E649", {"start": v(19.51, -1.02) * mm, "end": v(19.45, -1) * mm});
            skLineSegment(sketch, "E650", {"start": v(19.45, -1) * mm, "end": v(19.38, -0.98) * mm});
            skLineSegment(sketch, "E651", {"start": v(19.38, -0.98) * mm, "end": v(19.33, -0.97) * mm});
            skLineSegment(sketch, "E652", {"start": v(19.33, -0.97) * mm, "end": v(19.28, -0.95) * mm});
            skLineSegment(sketch, "E653", {"start": v(19.28, -0.95) * mm, "end": v(19.23, -0.94) * mm});
            skLineSegment(sketch, "E654", {"start": v(19.23, -0.94) * mm, "end": v(19.2, -0.94) * mm});
            skLineSegment(sketch, "E655", {"start": v(19.2, -0.94) * mm, "end": v(19.17, -0.93) * mm});
            skLineSegment(sketch, "E656", {"start": v(19.17, -0.93) * mm, "end": v(19.15, -0.93) * mm});
            skLineSegment(sketch, "E657", {"start": v(19.15, -0.93) * mm, "end": v(19.13, -0.93) * mm});
            skLineSegment(sketch, "E658", {"start": v(19.13, -0.93) * mm, "end": v(19.12, -0.92) * mm});
            skLineSegment(sketch, "E659", {"start": v(19.12, -0.92) * mm, "end": v(18.76, -0.9) * mm});
            skLineSegment(sketch, "E660", {"start": v(18.76, -0.9) * mm, "end": v(18.76, -0.9) * mm});
            skLineSegment(sketch, "E661", {"start": v(18.76, -0.9) * mm, "end": v(18.66, -0.88) * mm});
            skLineSegment(sketch, "E662", {"start": v(18.66, -0.88) * mm, "end": v(18.65, -0.87) * mm});
            skLineSegment(sketch, "E663", {"start": v(18.65, -0.87) * mm, "end": v(18.56, -0.86) * mm});
            skLineSegment(sketch, "E664", {"start": v(18.56, -0.86) * mm, "end": v(18.55, -0.84) * mm});
            skLineSegment(sketch, "E665", {"start": v(18.55, -0.84) * mm, "end": v(18.47, -0.83) * mm});
            skLineSegment(sketch, "E666", {"start": v(18.47, -0.83) * mm, "end": v(18.46, -0.8) * mm});
            skLineSegment(sketch, "E667", {"start": v(18.46, -0.8) * mm, "end": v(18.38, -0.8) * mm});
            skLineSegment(sketch, "E668", {"start": v(18.38, -0.8) * mm, "end": v(18.38, -0.77) * mm});
            skLineSegment(sketch, "E669", {"start": v(18.38, -0.77) * mm, "end": v(18.31, -0.76) * mm});
            skLineSegment(sketch, "E670", {"start": v(18.31, -0.76) * mm, "end": v(18.3, -0.74) * mm});
            skLineSegment(sketch, "E671", {"start": v(18.3, -0.74) * mm, "end": v(18.25, -0.72) * mm});
            skLineSegment(sketch, "E672", {"start": v(18.25, -0.72) * mm, "end": v(18.24, -0.7) * mm});
            skLineSegment(sketch, "E673", {"start": v(18.24, -0.7) * mm, "end": v(18.2, -0.68) * mm});
            skLineSegment(sketch, "E674", {"start": v(18.2, -0.68) * mm, "end": v(18.19, -0.65) * mm});
            skLineSegment(sketch, "E675", {"start": v(18.19, -0.65) * mm, "end": v(18.15, -0.64) * mm});
            skLineSegment(sketch, "E676", {"start": v(18.15, -0.64) * mm, "end": v(18.14, -0.6) * mm});
            skLineSegment(sketch, "E677", {"start": v(18.14, -0.6) * mm, "end": v(18.11, -0.6) * mm});
            skLineSegment(sketch, "E678", {"start": v(18.11, -0.6) * mm, "end": v(18.1, -0.56) * mm});
            skLineSegment(sketch, "E679", {"start": v(18.1, -0.56) * mm, "end": v(18.08, -0.53) * mm});
            skLineSegment(sketch, "E680", {"start": v(18.08, -0.53) * mm, "end": v(18.07, -0.5) * mm});
            skLineSegment(sketch, "E681", {"start": v(18.07, -0.5) * mm, "end": v(18.06, -0.5) * mm});
            skLineSegment(sketch, "E682", {"start": v(18.06, -0.5) * mm, "end": v(18.06, -0.47) * mm});
            skLineSegment(sketch, "E683", {"start": v(18.06, -0.47) * mm, "end": v(18.06, -0.44) * mm});
            skLineSegment(sketch, "E684", {"start": v(18.06, -0.44) * mm, "end": v(18.06, -0.17) * mm});
            skLineSegment(sketch, "E685", {"start": v(18.06, -0.17) * mm, "end": v(18.06, -0.02) * mm});
            skLineSegment(sketch, "E686", {"start": v(18.06, -0.02) * mm, "end": v(18.06, 0.02) * mm});
            skLineSegment(sketch, "E687", {"start": v(18.06, 0.02) * mm, "end": v(18.06, 0.17) * mm});
            skLineSegment(sketch, "E688", {"start": v(18.06, 0.17) * mm, "end": v(18.06, 0.44) * mm});
            skLineSegment(sketch, "E689", {"start": v(18.06, 0.44) * mm, "end": v(18.06, 0.47) * mm});
            skLineSegment(sketch, "E690", {"start": v(18.06, 0.47) * mm, "end": v(18.06, 0.5) * mm});
            skLineSegment(sketch, "E691", {"start": v(18.06, 0.5) * mm, "end": v(18.07, 0.5) * mm});
            skLineSegment(sketch, "E692", {"start": v(18.07, 0.5) * mm, "end": v(18.07, 0.5) * mm});
            skLineSegment(sketch, "E693", {"start": v(18.07, 0.5) * mm, "end": v(18.08, 0.55) * mm});
            skLineSegment(sketch, "E694", {"start": v(18.08, 0.55) * mm, "end": v(18.1, 0.56) * mm});
            skLineSegment(sketch, "E695", {"start": v(18.1, 0.56) * mm, "end": v(18.11, 0.6) * mm});
            skLineSegment(sketch, "E696", {"start": v(18.11, 0.6) * mm, "end": v(18.14, 0.6) * mm});
            skLineSegment(sketch, "E697", {"start": v(18.14, 0.6) * mm, "end": v(18.15, 0.64) * mm});
            skLineSegment(sketch, "E698", {"start": v(18.15, 0.64) * mm, "end": v(18.19, 0.65) * mm});
            skLineSegment(sketch, "E699", {"start": v(18.19, 0.65) * mm, "end": v(18.2, 0.68) * mm});
            skLineSegment(sketch, "E700", {"start": v(18.2, 0.68) * mm, "end": v(18.24, 0.7) * mm});
            skLineSegment(sketch, "E701", {"start": v(18.24, 0.7) * mm, "end": v(18.25, 0.72) * mm});
            skLineSegment(sketch, "E702", {"start": v(18.25, 0.72) * mm, "end": v(18.3, 0.74) * mm});
            skLineSegment(sketch, "E703", {"start": v(18.3, 0.74) * mm, "end": v(18.31, 0.76) * mm});
            skLineSegment(sketch, "E704", {"start": v(18.31, 0.76) * mm, "end": v(18.38, 0.77) * mm});
            skLineSegment(sketch, "E705", {"start": v(18.38, 0.77) * mm, "end": v(18.38, 0.8) * mm});
            skLineSegment(sketch, "E706", {"start": v(18.38, 0.8) * mm, "end": v(18.46, 0.8) * mm});
            skLineSegment(sketch, "E707", {"start": v(18.46, 0.8) * mm, "end": v(18.47, 0.83) * mm});
            skLineSegment(sketch, "E708", {"start": v(18.47, 0.83) * mm, "end": v(18.55, 0.84) * mm});
            skLineSegment(sketch, "E709", {"start": v(18.55, 0.84) * mm, "end": v(18.56, 0.86) * mm});
            skLineSegment(sketch, "E710", {"start": v(18.56, 0.86) * mm, "end": v(18.65, 0.87) * mm});
            skLineSegment(sketch, "E711", {"start": v(18.65, 0.87) * mm, "end": v(18.66, 0.88) * mm});
            skLineSegment(sketch, "E712", {"start": v(18.66, 0.88) * mm, "end": v(18.76, 0.9) * mm});
            skLineSegment(sketch, "E713", {"start": v(18.76, 0.9) * mm, "end": v(18.76, 0.9) * mm});
            skLineSegment(sketch, "E714", {"start": v(18.76, 0.9) * mm, "end": v(19.12, 0.93) * mm});
            skLineSegment(sketch, "E715", {"start": v(19.12, 0.93) * mm, "end": v(19.13, 0.93) * mm});
            skLineSegment(sketch, "E716", {"start": v(19.13, 0.93) * mm, "end": v(19.15, 0.93) * mm});
            skLineSegment(sketch, "E717", {"start": v(19.15, 0.93) * mm, "end": v(19.17, 0.93) * mm});
            skLineSegment(sketch, "E718", {"start": v(19.17, 0.93) * mm, "end": v(19.2, 0.94) * mm});
            skLineSegment(sketch, "E719", {"start": v(19.2, 0.94) * mm, "end": v(19.23, 0.94) * mm});
            skLineSegment(sketch, "E720", {"start": v(19.23, 0.94) * mm, "end": v(19.28, 0.95) * mm});
            skLineSegment(sketch, "E721", {"start": v(19.28, 0.95) * mm, "end": v(19.33, 0.97) * mm});
            skLineSegment(sketch, "E722", {"start": v(19.33, 0.97) * mm, "end": v(19.38, 0.98) * mm});
            skLineSegment(sketch, "E723", {"start": v(19.38, 0.98) * mm, "end": v(19.45, 1) * mm});
            skLineSegment(sketch, "E724", {"start": v(19.45, 1) * mm, "end": v(19.51, 1.02) * mm});
            skLineSegment(sketch, "E725", {"start": v(19.51, 1.02) * mm, "end": v(19.55, 1.04) * mm});
            skLineSegment(sketch, "E726", {"start": v(19.55, 1.04) * mm, "end": v(19.57, 1.04) * mm});
            skLineSegment(sketch, "E727", {"start": v(19.57, 1.04) * mm, "end": v(19.6, 1.06) * mm});
            skLineSegment(sketch, "E728", {"start": v(19.6, 1.06) * mm, "end": v(19.7, 1.1) * mm});
            skLineSegment(sketch, "E729", {"start": v(19.7, 1.1) * mm, "end": v(19.78, 1.13) * mm});
            skLineSegment(sketch, "E730", {"start": v(19.78, 1.13) * mm, "end": v(19.88, 1.17) * mm});
            skLineSegment(sketch, "E731", {"start": v(19.88, 1.17) * mm, "end": v(19.98, 1.22) * mm});
            skLineSegment(sketch, "E732", {"start": v(19.98, 1.22) * mm, "end": v(20.09, 1.28) * mm});
            skLineSegment(sketch, "E733", {"start": v(20.09, 1.28) * mm, "end": v(20.2, 1.34) * mm});
            skLineSegment(sketch, "E734", {"start": v(20.2, 1.34) * mm, "end": v(20.32, 1.41) * mm});
            skLineSegment(sketch, "E735", {"start": v(20.32, 1.41) * mm, "end": v(20.45, 1.49) * mm});
            skLineSegment(sketch, "E736", {"start": v(20.45, 1.49) * mm, "end": v(20.58, 1.57) * mm});
            skLineSegment(sketch, "E737", {"start": v(20.58, 1.57) * mm, "end": v(20.7, 1.66) * mm});
            skLineSegment(sketch, "E738", {"start": v(20.7, 1.66) * mm, "end": v(21.34, 2.12) * mm});
            skLineSegment(sketch, "E739", {"start": v(21.34, 2.12) * mm, "end": v(21.34, 2.15) * mm});
            skLineSegment(sketch, "E740", {"start": v(21.34, 2.15) * mm, "end": v(21.32, 2.24) * mm});
            skLineSegment(sketch, "E741", {"start": v(21.32, 2.24) * mm, "end": v(21.3, 2.33) * mm});
            skLineSegment(sketch, "E742", {"start": v(21.3, 2.33) * mm, "end": v(21.3, 2.42) * mm});
            skLineSegment(sketch, "E743", {"start": v(21.3, 2.42) * mm, "end": v(21.28, 2.5) * mm});
            skLineSegment(sketch, "E744", {"start": v(21.28, 2.5) * mm, "end": v(21.26, 2.6) * mm});
            skLineSegment(sketch, "E745", {"start": v(21.26, 2.6) * mm, "end": v(21.24, 2.69) * mm});
            skLineSegment(sketch, "E746", {"start": v(21.24, 2.69) * mm, "end": v(21.23, 2.78) * mm});
            skLineSegment(sketch, "E747", {"start": v(21.23, 2.78) * mm, "end": v(21.2, 2.87) * mm});
            skLineSegment(sketch, "E748", {"start": v(21.2, 2.87) * mm, "end": v(21.2, 2.96) * mm});
            skLineSegment(sketch, "E749", {"start": v(21.2, 2.96) * mm, "end": v(21.17, 3.05) * mm});
            skLineSegment(sketch, "E750", {"start": v(21.17, 3.05) * mm, "end": v(21.15, 3.13) * mm});
            skLineSegment(sketch, "E751", {"start": v(21.15, 3.13) * mm, "end": v(20.42, 3.33) * mm});
            skLineSegment(sketch, "E752", {"start": v(20.42, 3.33) * mm, "end": v(20.26, 3.36) * mm});
            skLineSegment(sketch, "E753", {"start": v(20.26, 3.36) * mm, "end": v(20.11, 3.4) * mm});
            skLineSegment(sketch, "E754", {"start": v(20.11, 3.4) * mm, "end": v(19.97, 3.42) * mm});
            skLineSegment(sketch, "E755", {"start": v(19.97, 3.42) * mm, "end": v(19.83, 3.45) * mm});
            skLineSegment(sketch, "E756", {"start": v(19.83, 3.45) * mm, "end": v(19.7, 3.47) * mm});
            skLineSegment(sketch, "E757", {"start": v(19.7, 3.47) * mm, "end": v(19.58, 3.48) * mm});
            skLineSegment(sketch, "E758", {"start": v(19.58, 3.48) * mm, "end": v(19.46, 3.5) * mm});
            skLineSegment(sketch, "E759", {"start": v(19.46, 3.5) * mm, "end": v(19.35, 3.5) * mm});
            skLineSegment(sketch, "E760", {"start": v(19.35, 3.5) * mm, "end": v(19.24, 3.5) * mm});
            skLineSegment(sketch, "E761", {"start": v(19.24, 3.5) * mm, "end": v(19.16, 3.5) * mm});
            skLineSegment(sketch, "E762", {"start": v(19.16, 3.5) * mm, "end": v(19.1, 3.5) * mm});
            skLineSegment(sketch, "E763", {"start": v(19.1, 3.5) * mm, "end": v(19.1, 3.5) * mm});
            skLineSegment(sketch, "E764", {"start": v(19.1, 3.5) * mm, "end": v(19.05, 3.5) * mm});
            skLineSegment(sketch, "E765", {"start": v(19.05, 3.5) * mm, "end": v(18.98, 3.5) * mm});
            skLineSegment(sketch, "E766", {"start": v(18.98, 3.5) * mm, "end": v(18.91, 3.5) * mm});
            skLineSegment(sketch, "E767", {"start": v(18.91, 3.5) * mm, "end": v(18.85, 3.5) * mm});
            skLineSegment(sketch, "E768", {"start": v(18.85, 3.5) * mm, "end": v(18.8, 3.48) * mm});
            skLineSegment(sketch, "E769", {"start": v(18.8, 3.48) * mm, "end": v(18.74, 3.48) * mm});
            skLineSegment(sketch, "E770", {"start": v(18.74, 3.48) * mm, "end": v(18.7, 3.47) * mm});
            skLineSegment(sketch, "E771", {"start": v(18.7, 3.47) * mm, "end": v(18.66, 3.46) * mm});
            skLineSegment(sketch, "E772", {"start": v(18.66, 3.46) * mm, "end": v(18.62, 3.46) * mm});
            skLineSegment(sketch, "E773", {"start": v(18.62, 3.46) * mm, "end": v(18.6, 3.45) * mm});
            skLineSegment(sketch, "E774", {"start": v(18.6, 3.45) * mm, "end": v(18.57, 3.45) * mm});
            skLineSegment(sketch, "E775", {"start": v(18.57, 3.45) * mm, "end": v(18.21, 3.35) * mm});
            skLineSegment(sketch, "E776", {"start": v(18.21, 3.35) * mm, "end": v(18.2, 3.36) * mm});
            skLineSegment(sketch, "E777", {"start": v(18.2, 3.36) * mm, "end": v(18.13, 3.34) * mm});
            skLineSegment(sketch, "E778", {"start": v(18.13, 3.34) * mm, "end": v(18.12, 3.35) * mm});
            skLineSegment(sketch, "E779", {"start": v(18.12, 3.35) * mm, "end": v(18.03, 3.33) * mm});
            skLineSegment(sketch, "E780", {"start": v(18.03, 3.33) * mm, "end": v(18.03, 3.34) * mm});
            skLineSegment(sketch, "E781", {"start": v(18.03, 3.34) * mm, "end": v(17.95, 3.32) * mm});
            skLineSegment(sketch, "E782", {"start": v(17.95, 3.32) * mm, "end": v(17.94, 3.34) * mm});
            skLineSegment(sketch, "E783", {"start": v(17.94, 3.34) * mm, "end": v(17.87, 3.33) * mm});
            skLineSegment(sketch, "E784", {"start": v(17.87, 3.33) * mm, "end": v(17.86, 3.35) * mm});
            skLineSegment(sketch, "E785", {"start": v(17.86, 3.35) * mm, "end": v(17.8, 3.34) * mm});
            skLineSegment(sketch, "E786", {"start": v(17.8, 3.34) * mm, "end": v(17.79, 3.36) * mm});
            skLineSegment(sketch, "E787", {"start": v(17.79, 3.36) * mm, "end": v(17.73, 3.35) * mm});
            skLineSegment(sketch, "E788", {"start": v(17.73, 3.35) * mm, "end": v(17.72, 3.37) * mm});
            skLineSegment(sketch, "E789", {"start": v(17.72, 3.37) * mm, "end": v(17.67, 3.37) * mm});
            skLineSegment(sketch, "E790", {"start": v(17.67, 3.37) * mm, "end": v(17.66, 3.4) * mm});
            skLineSegment(sketch, "E791", {"start": v(17.66, 3.4) * mm, "end": v(17.62, 3.39) * mm});
            skLineSegment(sketch, "E792", {"start": v(17.62, 3.39) * mm, "end": v(17.61, 3.42) * mm});
            skLineSegment(sketch, "E793", {"start": v(17.61, 3.42) * mm, "end": v(17.58, 3.42) * mm});
            skLineSegment(sketch, "E794", {"start": v(17.58, 3.42) * mm, "end": v(17.57, 3.45) * mm});
            skLineSegment(sketch, "E795", {"start": v(17.57, 3.45) * mm, "end": v(17.54, 3.45) * mm});
            skLineSegment(sketch, "E796", {"start": v(17.54, 3.45) * mm, "end": v(17.52, 3.48) * mm});
            skLineSegment(sketch, "E797", {"start": v(17.52, 3.48) * mm, "end": v(17.51, 3.48) * mm});
            skLineSegment(sketch, "E798", {"start": v(17.51, 3.48) * mm, "end": v(17.5, 3.49) * mm});
            skLineSegment(sketch, "E799", {"start": v(17.5, 3.49) * mm, "end": v(17.5, 3.5) * mm});
            skLineSegment(sketch, "E800", {"start": v(17.5, 3.5) * mm, "end": v(17.49, 3.53) * mm});
            skLineSegment(sketch, "E801", {"start": v(17.49, 3.53) * mm, "end": v(17.4, 3.8) * mm});
            skLineSegment(sketch, "E802", {"start": v(17.4, 3.8) * mm, "end": v(17.35, 3.92) * mm});
            skLineSegment(sketch, "E803", {"start": v(17.35, 3.92) * mm, "end": v(17.32, 3.98) * mm});
            skLineSegment(sketch, "E804", {"start": v(17.32, 3.98) * mm, "end": v(17.27, 4.1) * mm});
            skLineSegment(sketch, "E805", {"start": v(17.27, 4.1) * mm, "end": v(17.17, 4.36) * mm});
            skLineSegment(sketch, "E806", {"start": v(17.17, 4.36) * mm, "end": v(17.17, 4.39) * mm});
            skLineSegment(sketch, "E807", {"start": v(17.17, 4.39) * mm, "end": v(17.16, 4.4) * mm});
            skLineSegment(sketch, "E808", {"start": v(17.16, 4.4) * mm, "end": v(17.16, 4.41) * mm});
            skLineSegment(sketch, "E809", {"start": v(17.16, 4.41) * mm, "end": v(17.16, 4.42) * mm});
            skLineSegment(sketch, "E810", {"start": v(17.16, 4.42) * mm, "end": v(17.16, 4.46) * mm});
            skLineSegment(sketch, "E811", {"start": v(17.16, 4.46) * mm, "end": v(17.18, 4.48) * mm});
            skLineSegment(sketch, "E812", {"start": v(17.18, 4.48) * mm, "end": v(17.17, 4.52) * mm});
            skLineSegment(sketch, "E813", {"start": v(17.17, 4.52) * mm, "end": v(17.2, 4.54) * mm});
            skLineSegment(sketch, "E814", {"start": v(17.2, 4.54) * mm, "end": v(17.19, 4.57) * mm});
            skLineSegment(sketch, "E815", {"start": v(17.19, 4.57) * mm, "end": v(17.22, 4.6) * mm});
            skLineSegment(sketch, "E816", {"start": v(17.22, 4.6) * mm, "end": v(17.22, 4.63) * mm});
            skLineSegment(sketch, "E817", {"start": v(17.22, 4.63) * mm, "end": v(17.26, 4.66) * mm});
            skLineSegment(sketch, "E818", {"start": v(17.26, 4.66) * mm, "end": v(17.25, 4.69) * mm});
            skLineSegment(sketch, "E819", {"start": v(17.25, 4.69) * mm, "end": v(17.3, 4.72) * mm});
            skLineSegment(sketch, "E820", {"start": v(17.3, 4.72) * mm, "end": v(17.3, 4.74) * mm});
            skLineSegment(sketch, "E821", {"start": v(17.3, 4.74) * mm, "end": v(17.36, 4.78) * mm});
            skLineSegment(sketch, "E822", {"start": v(17.36, 4.78) * mm, "end": v(17.36, 4.8) * mm});
            skLineSegment(sketch, "E823", {"start": v(17.36, 4.8) * mm, "end": v(17.43, 4.84) * mm});
            skLineSegment(sketch, "E824", {"start": v(17.43, 4.84) * mm, "end": v(17.42, 4.86) * mm});
            skLineSegment(sketch, "E825", {"start": v(17.42, 4.86) * mm, "end": v(17.5, 4.9) * mm});
            skLineSegment(sketch, "E826", {"start": v(17.5, 4.9) * mm, "end": v(17.5, 4.92) * mm});
            skLineSegment(sketch, "E827", {"start": v(17.5, 4.92) * mm, "end": v(17.59, 4.97) * mm});
            skLineSegment(sketch, "E828", {"start": v(17.59, 4.97) * mm, "end": v(17.58, 4.98) * mm});
            skLineSegment(sketch, "E829", {"start": v(17.58, 4.98) * mm, "end": v(17.68, 5.03) * mm});
            skLineSegment(sketch, "E830", {"start": v(17.68, 5.03) * mm, "end": v(17.68, 5.04) * mm});
            skLineSegment(sketch, "E831", {"start": v(17.68, 5.04) * mm, "end": v(18, 5.18) * mm});
            skLineSegment(sketch, "E832", {"start": v(18, 5.18) * mm, "end": v(18, 5.18) * mm});
            skLineSegment(sketch, "E833", {"start": v(18, 5.18) * mm, "end": v(18, 5.19) * mm});
            skLineSegment(sketch, "E834", {"start": v(18, 5.19) * mm, "end": v(18.03, 5.2) * mm});
            skLineSegment(sketch, "E835", {"start": v(18.03, 5.2) * mm, "end": v(18.05, 5.21) * mm});
            skLineSegment(sketch, "E836", {"start": v(18.05, 5.21) * mm, "end": v(18.08, 5.23) * mm});
            skLineSegment(sketch, "E837", {"start": v(18.08, 5.23) * mm, "end": v(18.12, 5.26) * mm});
            skLineSegment(sketch, "E838", {"start": v(18.12, 5.26) * mm, "end": v(18.16, 5.29) * mm});
            skLineSegment(sketch, "E839", {"start": v(18.16, 5.29) * mm, "end": v(18.21, 5.33) * mm});
            skLineSegment(sketch, "E840", {"start": v(18.21, 5.33) * mm, "end": v(18.27, 5.37) * mm});
            skLineSegment(sketch, "E841", {"start": v(18.27, 5.37) * mm, "end": v(18.33, 5.42) * mm});
            skLineSegment(sketch, "E842", {"start": v(18.33, 5.42) * mm, "end": v(18.36, 5.44) * mm});
            skLineSegment(sketch, "E843", {"start": v(18.36, 5.44) * mm, "end": v(18.37, 5.45) * mm});
            skLineSegment(sketch, "E844", {"start": v(18.37, 5.45) * mm, "end": v(18.4, 5.48) * mm});
            skLineSegment(sketch, "E845", {"start": v(18.4, 5.48) * mm, "end": v(18.47, 5.54) * mm});
            skLineSegment(sketch, "E846", {"start": v(18.47, 5.54) * mm, "end": v(18.54, 5.6) * mm});
            skLineSegment(sketch, "E847", {"start": v(18.54, 5.6) * mm, "end": v(18.61, 5.68) * mm});
            skLineSegment(sketch, "E848", {"start": v(18.61, 5.68) * mm, "end": v(18.7, 5.76) * mm});
            skLineSegment(sketch, "E849", {"start": v(18.7, 5.76) * mm, "end": v(18.77, 5.85) * mm});
            skLineSegment(sketch, "E850", {"start": v(18.77, 5.85) * mm, "end": v(18.86, 5.95) * mm});
            skLineSegment(sketch, "E851", {"start": v(18.86, 5.95) * mm, "end": v(18.95, 6.05) * mm});
            skLineSegment(sketch, "E852", {"start": v(18.95, 6.05) * mm, "end": v(19.04, 6.16) * mm});
            skLineSegment(sketch, "E853", {"start": v(19.04, 6.16) * mm, "end": v(19.13, 6.29) * mm});
            skLineSegment(sketch, "E854", {"start": v(19.13, 6.29) * mm, "end": v(19.22, 6.4) * mm});
            skLineSegment(sketch, "E855", {"start": v(19.22, 6.4) * mm, "end": v(19.68, 7.06) * mm});
            skLineSegment(sketch, "E856", {"start": v(19.68, 7.06) * mm, "end": v(19.65, 7.12) * mm});
            skLineSegment(sketch, "E857", {"start": v(19.65, 7.12) * mm, "end": v(19.6, 7.21) * mm});
            skLineSegment(sketch, "E858", {"start": v(19.6, 7.21) * mm, "end": v(19.55, 7.3) * mm});
            skLineSegment(sketch, "E859", {"start": v(19.55, 7.3) * mm, "end": v(19.5, 7.4) * mm});
            skLineSegment(sketch, "E860", {"start": v(19.5, 7.4) * mm, "end": v(19.44, 7.48) * mm});
            skLineSegment(sketch, "E861", {"start": v(19.44, 7.48) * mm, "end": v(19.39, 7.58) * mm});
            skLineSegment(sketch, "E862", {"start": v(19.39, 7.58) * mm, "end": v(19.34, 7.67) * mm});
            skLineSegment(sketch, "E863", {"start": v(19.34, 7.67) * mm, "end": v(19.28, 7.76) * mm});
            skLineSegment(sketch, "E864", {"start": v(19.28, 7.76) * mm, "end": v(19.23, 7.85) * mm});
            skLineSegment(sketch, "E865", {"start": v(19.23, 7.85) * mm, "end": v(19.17, 7.94) * mm});
            skLineSegment(sketch, "E866", {"start": v(19.17, 7.94) * mm, "end": v(19.15, 7.96) * mm});
            skLineSegment(sketch, "E867", {"start": v(19.15, 7.96) * mm, "end": v(18.38, 7.9) * mm});
            skLineSegment(sketch, "E868", {"start": v(18.38, 7.9) * mm, "end": v(18.22, 7.88) * mm});
            skLineSegment(sketch, "E869", {"start": v(18.22, 7.88) * mm, "end": v(18.08, 7.86) * mm});
            skLineSegment(sketch, "E870", {"start": v(18.08, 7.86) * mm, "end": v(17.93, 7.83) * mm});
            skLineSegment(sketch, "E871", {"start": v(17.93, 7.83) * mm, "end": v(17.8, 7.8) * mm});
            skLineSegment(sketch, "E872", {"start": v(17.8, 7.8) * mm, "end": v(17.67, 7.78) * mm});
            skLineSegment(sketch, "E873", {"start": v(17.67, 7.78) * mm, "end": v(17.54, 7.75) * mm});
            skLineSegment(sketch, "E874", {"start": v(17.54, 7.75) * mm, "end": v(17.43, 7.73) * mm});
            skLineSegment(sketch, "E875", {"start": v(17.43, 7.73) * mm, "end": v(17.34, 7.7) * mm});
            skLineSegment(sketch, "E876", {"start": v(17.34, 7.7) * mm, "end": v(17.24, 7.67) * mm});
            skLineSegment(sketch, "E877", {"start": v(17.24, 7.67) * mm, "end": v(17.15, 7.64) * mm});
            skLineSegment(sketch, "E878", {"start": v(17.15, 7.64) * mm, "end": v(17.1, 7.63) * mm});
            skLineSegment(sketch, "E879", {"start": v(17.1, 7.63) * mm, "end": v(17.09, 7.62) * mm});
            skLineSegment(sketch, "E880", {"start": v(17.09, 7.62) * mm, "end": v(17.04, 7.6) * mm});
            skLineSegment(sketch, "E881", {"start": v(17.04, 7.6) * mm, "end": v(16.97, 7.58) * mm});
            skLineSegment(sketch, "E882", {"start": v(16.97, 7.58) * mm, "end": v(16.9, 7.55) * mm});
            skLineSegment(sketch, "E883", {"start": v(16.9, 7.55) * mm, "end": v(16.83, 7.52) * mm});
            skLineSegment(sketch, "E884", {"start": v(16.83, 7.52) * mm, "end": v(16.76, 7.5) * mm});
            skLineSegment(sketch, "E885", {"start": v(16.76, 7.5) * mm, "end": v(16.7, 7.46) * mm});
            skLineSegment(sketch, "E886", {"start": v(16.7, 7.46) * mm, "end": v(16.65, 7.44) * mm});
            skLineSegment(sketch, "E887", {"start": v(16.65, 7.44) * mm, "end": v(16.62, 7.42) * mm});
            skLineSegment(sketch, "E888", {"start": v(16.62, 7.42) * mm, "end": v(16.58, 7.4) * mm});
            skLineSegment(sketch, "E889", {"start": v(16.58, 7.4) * mm, "end": v(16.54, 7.38) * mm});
            skLineSegment(sketch, "E890", {"start": v(16.54, 7.38) * mm, "end": v(16.51, 7.36) * mm});
            skLineSegment(sketch, "E891", {"start": v(16.51, 7.36) * mm, "end": v(16.2, 7.18) * mm});
            skLineSegment(sketch, "E892", {"start": v(16.2, 7.18) * mm, "end": v(16.2, 7.18) * mm});
            skLineSegment(sketch, "E893", {"start": v(16.2, 7.18) * mm, "end": v(16.13, 7.14) * mm});
            skLineSegment(sketch, "E894", {"start": v(16.13, 7.14) * mm, "end": v(16.12, 7.15) * mm});
            skLineSegment(sketch, "E895", {"start": v(16.12, 7.15) * mm, "end": v(16.06, 7.11) * mm});
            skLineSegment(sketch, "E896", {"start": v(16.06, 7.11) * mm, "end": v(16.06, 7.12) * mm});
            skLineSegment(sketch, "E897", {"start": v(16.06, 7.12) * mm, "end": v(16, 7.1) * mm});
            skLineSegment(sketch, "E898", {"start": v(16, 7.1) * mm, "end": v(16, 7.1) * mm});
            skLineSegment(sketch, "E899", {"start": v(16, 7.1) * mm, "end": v(15.94, 7.08) * mm});
            skLineSegment(sketch, "E900", {"start": v(15.94, 7.08) * mm, "end": v(15.93, 7.09) * mm});
            skLineSegment(sketch, "E901", {"start": v(15.93, 7.09) * mm, "end": v(15.89, 7.06) * mm});
            skLineSegment(sketch, "E902", {"start": v(15.89, 7.06) * mm, "end": v(15.87, 7.08) * mm});
            skLineSegment(sketch, "E903", {"start": v(15.87, 7.08) * mm, "end": v(15.83, 7.06) * mm});
            skLineSegment(sketch, "E904", {"start": v(15.83, 7.06) * mm, "end": v(15.8, 7.07) * mm});
            skLineSegment(sketch, "E905", {"start": v(15.8, 7.07) * mm, "end": v(15.77, 7.05) * mm});
            skLineSegment(sketch, "E906", {"start": v(15.77, 7.05) * mm, "end": v(15.73, 7.07) * mm});
            skLineSegment(sketch, "E907", {"start": v(15.73, 7.07) * mm, "end": v(15.7, 7.08) * mm});
            skLineSegment(sketch, "E908", {"start": v(15.7, 7.08) * mm, "end": v(15.67, 7.07) * mm});
            skLineSegment(sketch, "E909", {"start": v(15.67, 7.07) * mm, "end": v(15.64, 7.09) * mm});
            skLineSegment(sketch, "E910", {"start": v(15.64, 7.09) * mm, "end": v(15.6, 7.1) * mm});
            skLineSegment(sketch, "E911", {"start": v(15.6, 7.1) * mm, "end": v(15.6, 7.1) * mm});
            skLineSegment(sketch, "E912", {"start": v(15.6, 7.1) * mm, "end": v(15.59, 7.11) * mm});
            skLineSegment(sketch, "E913", {"start": v(15.59, 7.11) * mm, "end": v(15.56, 7.14) * mm});
            skLineSegment(sketch, "E914", {"start": v(15.56, 7.14) * mm, "end": v(15.56, 7.14) * mm});
            skLineSegment(sketch, "E915", {"start": v(15.56, 7.14) * mm, "end": v(15.4, 7.34) * mm});
            skLineSegment(sketch, "E916", {"start": v(15.4, 7.34) * mm, "end": v(15.3, 7.47) * mm});
            skLineSegment(sketch, "E917", {"start": v(15.3, 7.47) * mm, "end": v(15.26, 7.51) * mm});
            skLineSegment(sketch, "E918", {"start": v(15.26, 7.51) * mm, "end": v(15.16, 7.64) * mm});
            skLineSegment(sketch, "E919", {"start": v(15.16, 7.64) * mm, "end": v(14.99, 7.84) * mm});
            skLineSegment(sketch, "E920", {"start": v(14.99, 7.84) * mm, "end": v(14.98, 7.86) * mm});
            skLineSegment(sketch, "E921", {"start": v(14.98, 7.86) * mm, "end": v(14.97, 7.87) * mm});
            skLineSegment(sketch, "E922", {"start": v(14.97, 7.87) * mm, "end": v(14.97, 7.88) * mm});
            skLineSegment(sketch, "E923", {"start": v(14.97, 7.88) * mm, "end": v(14.97, 7.89) * mm});
            skLineSegment(sketch, "E924", {"start": v(14.97, 7.89) * mm, "end": v(14.96, 7.93) * mm});
            skLineSegment(sketch, "E925", {"start": v(14.96, 7.93) * mm, "end": v(14.95, 7.96) * mm});
            skLineSegment(sketch, "E926", {"start": v(14.95, 7.96) * mm, "end": v(14.95, 8) * mm});
            skLineSegment(sketch, "E927", {"start": v(14.95, 8) * mm, "end": v(14.97, 8.04) * mm});
            skLineSegment(sketch, "E928", {"start": v(14.97, 8.04) * mm, "end": v(14.95, 8.06) * mm});
            skLineSegment(sketch, "E929", {"start": v(14.95, 8.06) * mm, "end": v(14.98, 8.1) * mm});
            skLineSegment(sketch, "E930", {"start": v(14.98, 8.1) * mm, "end": v(14.97, 8.12) * mm});
            skLineSegment(sketch, "E931", {"start": v(14.97, 8.12) * mm, "end": v(15, 8.16) * mm});
            skLineSegment(sketch, "E932", {"start": v(15, 8.16) * mm, "end": v(14.99, 8.18) * mm});
            skLineSegment(sketch, "E933", {"start": v(14.99, 8.18) * mm, "end": v(15.03, 8.23) * mm});
            skLineSegment(sketch, "E934", {"start": v(15.03, 8.23) * mm, "end": v(15.02, 8.25) * mm});
            skLineSegment(sketch, "E935", {"start": v(15.02, 8.25) * mm, "end": v(15.06, 8.3) * mm});
            skLineSegment(sketch, "E936", {"start": v(15.06, 8.3) * mm, "end": v(15.05, 8.32) * mm});
            skLineSegment(sketch, "E937", {"start": v(15.05, 8.32) * mm, "end": v(15.1, 8.38) * mm});
            skLineSegment(sketch, "E938", {"start": v(15.1, 8.38) * mm, "end": v(15.1, 8.4) * mm});
            skLineSegment(sketch, "E939", {"start": v(15.1, 8.4) * mm, "end": v(15.16, 8.46) * mm});
            skLineSegment(sketch, "E940", {"start": v(15.16, 8.46) * mm, "end": v(15.15, 8.47) * mm});
            skLineSegment(sketch, "E941", {"start": v(15.15, 8.47) * mm, "end": v(15.22, 8.54) * mm});
            skLineSegment(sketch, "E942", {"start": v(15.22, 8.54) * mm, "end": v(15.21, 8.54) * mm});
            skLineSegment(sketch, "E943", {"start": v(15.21, 8.54) * mm, "end": v(15.47, 8.8) * mm});
            skLineSegment(sketch, "E944", {"start": v(15.47, 8.8) * mm, "end": v(15.48, 8.8) * mm});
            skLineSegment(sketch, "E945", {"start": v(15.48, 8.8) * mm, "end": v(15.5, 8.82) * mm});
            skLineSegment(sketch, "E946", {"start": v(15.5, 8.82) * mm, "end": v(15.51, 8.85) * mm});
            skLineSegment(sketch, "E947", {"start": v(15.51, 8.85) * mm, "end": v(15.54, 8.88) * mm});
            skLineSegment(sketch, "E948", {"start": v(15.54, 8.88) * mm, "end": v(15.57, 8.92) * mm});
            skLineSegment(sketch, "E949", {"start": v(15.57, 8.92) * mm, "end": v(15.6, 8.96) * mm});
            skLineSegment(sketch, "E950", {"start": v(15.6, 8.96) * mm, "end": v(15.64, 9.02) * mm});
            skLineSegment(sketch, "E951", {"start": v(15.64, 9.02) * mm, "end": v(15.68, 9.07) * mm});
            skLineSegment(sketch, "E952", {"start": v(15.68, 9.07) * mm, "end": v(15.72, 9.13) * mm});
            skLineSegment(sketch, "E953", {"start": v(15.72, 9.13) * mm, "end": v(15.76, 9.2) * mm});
            skLineSegment(sketch, "E954", {"start": v(15.76, 9.2) * mm, "end": v(15.78, 9.23) * mm});
            skLineSegment(sketch, "E955", {"start": v(15.78, 9.23) * mm, "end": v(15.8, 9.25) * mm});
            skLineSegment(sketch, "E956", {"start": v(15.8, 9.25) * mm, "end": v(15.82, 9.3) * mm});
            skLineSegment(sketch, "E957", {"start": v(15.82, 9.3) * mm, "end": v(15.87, 9.38) * mm});
            skLineSegment(sketch, "E958", {"start": v(15.87, 9.38) * mm, "end": v(15.92, 9.47) * mm});
            skLineSegment(sketch, "E959", {"start": v(15.92, 9.47) * mm, "end": v(15.97, 9.57) * mm});
            skLineSegment(sketch, "E960", {"start": v(15.97, 9.57) * mm, "end": v(16.02, 9.68) * mm});
            skLineSegment(sketch, "E961", {"start": v(16.02, 9.68) * mm, "end": v(16.08, 9.8) * mm});
            skLineSegment(sketch, "E962", {"start": v(16.08, 9.8) * mm, "end": v(16.13, 9.91) * mm});
            skLineSegment(sketch, "E963", {"start": v(16.13, 9.91) * mm, "end": v(16.18, 10.03) * mm});
            skLineSegment(sketch, "E964", {"start": v(16.18, 10.03) * mm, "end": v(16.23, 10.15) * mm});
            skLineSegment(sketch, "E965", {"start": v(16.23, 10.15) * mm, "end": v(16.28, 10.28) * mm});
            skLineSegment(sketch, "E966", {"start": v(16.28, 10.28) * mm, "end": v(16.32, 10.41) * mm});
            skLineSegment(sketch, "E967", {"start": v(16.32, 10.41) * mm, "end": v(16.58, 11.16) * mm});
            skLineSegment(sketch, "E968", {"start": v(16.58, 11.16) * mm, "end": v(16.52, 11.22) * mm});
            skLineSegment(sketch, "E969", {"start": v(16.52, 11.22) * mm, "end": v(16.43, 11.3) * mm});
            skLineSegment(sketch, "E970", {"start": v(16.43, 11.3) * mm, "end": v(16.34, 11.4) * mm});
            skLineSegment(sketch, "E971", {"start": v(16.34, 11.4) * mm, "end": v(16.24, 11.49) * mm});
            skLineSegment(sketch, "E972", {"start": v(16.24, 11.49) * mm, "end": v(16.14, 11.58) * mm});
            skLineSegment(sketch, "E973", {"start": v(16.14, 11.58) * mm, "end": v(16.05, 11.67) * mm});
            skLineSegment(sketch, "E974", {"start": v(16.05, 11.67) * mm, "end": v(15.95, 11.75) * mm});
            skLineSegment(sketch, "E975", {"start": v(15.95, 11.75) * mm, "end": v(15.85, 11.84) * mm});
            skLineSegment(sketch, "E976", {"start": v(15.85, 11.84) * mm, "end": v(15.8, 11.89) * mm});
            skLineSegment(sketch, "E977", {"start": v(15.8, 11.89) * mm, "end": v(15.07, 11.59) * mm});
            skLineSegment(sketch, "E978", {"start": v(15.07, 11.59) * mm, "end": v(14.93, 11.52) * mm});
            skLineSegment(sketch, "E979", {"start": v(14.93, 11.52) * mm, "end": v(14.79, 11.46) * mm});
            skLineSegment(sketch, "E980", {"start": v(14.79, 11.46) * mm, "end": v(14.67, 11.4) * mm});
            skLineSegment(sketch, "E981", {"start": v(14.67, 11.4) * mm, "end": v(14.56, 11.34) * mm});
            skLineSegment(sketch, "E982", {"start": v(14.56, 11.34) * mm, "end": v(14.45, 11.29) * mm});
            skLineSegment(sketch, "E983", {"start": v(14.45, 11.29) * mm, "end": v(14.35, 11.23) * mm});
            skLineSegment(sketch, "E984", {"start": v(14.35, 11.23) * mm, "end": v(14.26, 11.18) * mm});
            skLineSegment(sketch, "E985", {"start": v(14.26, 11.18) * mm, "end": v(14.16, 11.12) * mm});
            skLineSegment(sketch, "E986", {"start": v(14.16, 11.12) * mm, "end": v(14.07, 11.06) * mm});
            skLineSegment(sketch, "E987", {"start": v(14.07, 11.06) * mm, "end": v(13.99, 11) * mm});
            skLineSegment(sketch, "E988", {"start": v(13.99, 11) * mm, "end": v(13.93, 10.97) * mm});
            skLineSegment(sketch, "E989", {"start": v(13.93, 10.97) * mm, "end": v(13.92, 10.96) * mm});
            skLineSegment(sketch, "E990", {"start": v(13.92, 10.96) * mm, "end": v(13.88, 10.93) * mm});
            skLineSegment(sketch, "E991", {"start": v(13.88, 10.93) * mm, "end": v(13.8, 10.87) * mm});
            skLineSegment(sketch, "E992", {"start": v(13.8, 10.87) * mm, "end": v(13.73, 10.82) * mm});
            skLineSegment(sketch, "E993", {"start": v(13.73, 10.82) * mm, "end": v(13.66, 10.77) * mm});
            skLineSegment(sketch, "E994", {"start": v(13.66, 10.77) * mm, "end": v(13.6, 10.72) * mm});
            skLineSegment(sketch, "E995", {"start": v(13.6, 10.72) * mm, "end": v(13.55, 10.68) * mm});
            skLineSegment(sketch, "E996", {"start": v(13.55, 10.68) * mm, "end": v(13.5, 10.64) * mm});
            skLineSegment(sketch, "E997", {"start": v(13.5, 10.64) * mm, "end": v(13.46, 10.6) * mm});
            skLineSegment(sketch, "E998", {"start": v(13.46, 10.6) * mm, "end": v(13.42, 10.57) * mm});
            skLineSegment(sketch, "E999", {"start": v(13.42, 10.57) * mm, "end": v(13.39, 10.53) * mm});
            skLineSegment(sketch, "E1000", {"start": v(13.39, 10.53) * mm, "end": v(13.35, 10.5) * mm});
            skLineSegment(sketch, "E1001", {"start": v(13.35, 10.5) * mm, "end": v(13.12, 10.27) * mm});
            skLineSegment(sketch, "E1002", {"start": v(13.12, 10.27) * mm, "end": v(13.12, 10.27) * mm});
            skLineSegment(sketch, "E1003", {"start": v(13.12, 10.27) * mm, "end": v(13.07, 10.23) * mm});
            skLineSegment(sketch, "E1004", {"start": v(13.07, 10.23) * mm, "end": v(13.06, 10.23) * mm});
            skLineSegment(sketch, "E1005", {"start": v(13.06, 10.23) * mm, "end": v(13.02, 10.19) * mm});
            skLineSegment(sketch, "E1006", {"start": v(13.02, 10.19) * mm, "end": v(13.01, 10.2) * mm});
            skLineSegment(sketch, "E1007", {"start": v(13.01, 10.2) * mm, "end": v(12.97, 10.16) * mm});
            skLineSegment(sketch, "E1008", {"start": v(12.97, 10.16) * mm, "end": v(12.96, 10.16) * mm});
            skLineSegment(sketch, "E1009", {"start": v(12.96, 10.16) * mm, "end": v(12.92, 10.13) * mm});
            skLineSegment(sketch, "E1010", {"start": v(12.92, 10.13) * mm, "end": v(12.91, 10.13) * mm});
            skLineSegment(sketch, "E1011", {"start": v(12.91, 10.13) * mm, "end": v(12.88, 10.1) * mm});
            skLineSegment(sketch, "E1012", {"start": v(12.88, 10.1) * mm, "end": v(12.87, 10.11) * mm});
            skLineSegment(sketch, "E1013", {"start": v(12.87, 10.11) * mm, "end": v(12.84, 10.09) * mm});
            skLineSegment(sketch, "E1014", {"start": v(12.84, 10.09) * mm, "end": v(12.82, 10.1) * mm});
            skLineSegment(sketch, "E1015", {"start": v(12.82, 10.1) * mm, "end": v(12.79, 10.07) * mm});
            skLineSegment(sketch, "E1016", {"start": v(12.79, 10.07) * mm, "end": v(12.77, 10.08) * mm});
            skLineSegment(sketch, "E1017", {"start": v(12.77, 10.08) * mm, "end": v(12.73, 10.07) * mm});
            skLineSegment(sketch, "E1018", {"start": v(12.73, 10.07) * mm, "end": v(12.7, 10.05) * mm});
            skLineSegment(sketch, "E1019", {"start": v(12.7, 10.05) * mm, "end": v(12.67, 10.06) * mm});
            skLineSegment(sketch, "E1020", {"start": v(12.67, 10.06) * mm, "end": v(12.63, 10.07) * mm});
            skLineSegment(sketch, "E1021", {"start": v(12.63, 10.07) * mm, "end": v(12.62, 10.07) * mm});
            skLineSegment(sketch, "E1022", {"start": v(12.62, 10.07) * mm, "end": v(12.62, 10.07) * mm});
            skLineSegment(sketch, "E1023", {"start": v(12.62, 10.07) * mm, "end": v(12.6, 10.07) * mm});
            skLineSegment(sketch, "E1024", {"start": v(12.6, 10.07) * mm, "end": v(12.58, 10.09) * mm});
            skLineSegment(sketch, "E1025", {"start": v(12.58, 10.09) * mm, "end": v(12.58, 10.09) * mm});
            skLineSegment(sketch, "E1026", {"start": v(12.58, 10.09) * mm, "end": v(12.38, 10.23) * mm});
            skLineSegment(sketch, "E1027", {"start": v(12.38, 10.23) * mm, "end": v(12.25, 10.33) * mm});
            skLineSegment(sketch, "E1028", {"start": v(12.25, 10.33) * mm, "end": v(12.18, 10.38) * mm});
            skLineSegment(sketch, "E1029", {"start": v(12.18, 10.38) * mm, "end": v(12.04, 10.48) * mm});
            skLineSegment(sketch, "E1030", {"start": v(12.04, 10.48) * mm, "end": v(11.84, 10.62) * mm});
            skLineSegment(sketch, "E1031", {"start": v(11.84, 10.62) * mm, "end": v(11.83, 10.63) * mm});
            skLineSegment(sketch, "E1032", {"start": v(11.83, 10.63) * mm, "end": v(11.81, 10.64) * mm});
            skLineSegment(sketch, "E1033", {"start": v(11.81, 10.64) * mm, "end": v(11.81, 10.65) * mm});
            skLineSegment(sketch, "E1034", {"start": v(11.81, 10.65) * mm, "end": v(11.8, 10.66) * mm});
            skLineSegment(sketch, "E1035", {"start": v(11.8, 10.66) * mm, "end": v(11.79, 10.7) * mm});
            skLineSegment(sketch, "E1036", {"start": v(11.79, 10.7) * mm, "end": v(11.78, 10.73) * mm});
            skLineSegment(sketch, "E1037", {"start": v(11.78, 10.73) * mm, "end": v(11.77, 10.77) * mm});
            skLineSegment(sketch, "E1038", {"start": v(11.77, 10.77) * mm, "end": v(11.76, 10.82) * mm});
            skLineSegment(sketch, "E1039", {"start": v(11.76, 10.82) * mm, "end": v(11.75, 10.85) * mm});
            skLineSegment(sketch, "E1040", {"start": v(11.75, 10.85) * mm, "end": v(11.77, 10.89) * mm});
            skLineSegment(sketch, "E1041", {"start": v(11.77, 10.89) * mm, "end": v(11.76, 10.92) * mm});
            skLineSegment(sketch, "E1042", {"start": v(11.76, 10.92) * mm, "end": v(11.76, 10.96) * mm});
            skLineSegment(sketch, "E1043", {"start": v(11.76, 10.96) * mm, "end": v(11.78, 11) * mm});
            skLineSegment(sketch, "E1044", {"start": v(11.78, 11) * mm, "end": v(11.77, 11.02) * mm});
            skLineSegment(sketch, "E1045", {"start": v(11.77, 11.02) * mm, "end": v(11.8, 11.08) * mm});
            skLineSegment(sketch, "E1046", {"start": v(11.8, 11.08) * mm, "end": v(11.8, 11.1) * mm});
            skLineSegment(sketch, "E1047", {"start": v(11.8, 11.1) * mm, "end": v(11.83, 11.16) * mm});
            skLineSegment(sketch, "E1048", {"start": v(11.83, 11.16) * mm, "end": v(11.82, 11.17) * mm});
            skLineSegment(sketch, "E1049", {"start": v(11.82, 11.17) * mm, "end": v(11.86, 11.25) * mm});
            skLineSegment(sketch, "E1050", {"start": v(11.86, 11.25) * mm, "end": v(11.85, 11.25) * mm});
            skLineSegment(sketch, "E1051", {"start": v(11.85, 11.25) * mm, "end": v(12.02, 11.57) * mm});
            skLineSegment(sketch, "E1052", {"start": v(12.02, 11.57) * mm, "end": v(12.03, 11.6) * mm});
            skLineSegment(sketch, "E1053", {"start": v(12.03, 11.6) * mm, "end": v(12.05, 11.63) * mm});
            skLineSegment(sketch, "E1054", {"start": v(12.05, 11.63) * mm, "end": v(12.06, 11.67) * mm});
            skLineSegment(sketch, "E1055", {"start": v(12.06, 11.67) * mm, "end": v(12.08, 11.71) * mm});
            skLineSegment(sketch, "E1056", {"start": v(12.08, 11.71) * mm, "end": v(12.1, 11.77) * mm});
            skLineSegment(sketch, "E1057", {"start": v(12.1, 11.77) * mm, "end": v(12.12, 11.82) * mm});
            skLineSegment(sketch, "E1058", {"start": v(12.12, 11.82) * mm, "end": v(12.15, 11.89) * mm});
            skLineSegment(sketch, "E1059", {"start": v(12.15, 11.89) * mm, "end": v(12.17, 11.95) * mm});
            skLineSegment(sketch, "E1060", {"start": v(12.17, 11.95) * mm, "end": v(12.2, 12.03) * mm});
            skLineSegment(sketch, "E1061", {"start": v(12.2, 12.03) * mm, "end": v(12.22, 12.12) * mm});
            skLineSegment(sketch, "E1062", {"start": v(12.22, 12.12) * mm, "end": v(12.23, 12.16) * mm});
            skLineSegment(sketch, "E1063", {"start": v(12.23, 12.16) * mm, "end": v(12.24, 12.2) * mm});
            skLineSegment(sketch, "E1064", {"start": v(12.24, 12.2) * mm, "end": v(12.26, 12.25) * mm});
            skLineSegment(sketch, "E1065", {"start": v(12.26, 12.25) * mm, "end": v(12.28, 12.35) * mm});
            skLineSegment(sketch, "E1066", {"start": v(12.28, 12.35) * mm, "end": v(12.31, 12.46) * mm});
            skLineSegment(sketch, "E1067", {"start": v(12.31, 12.46) * mm, "end": v(12.34, 12.58) * mm});
            skLineSegment(sketch, "E1068", {"start": v(12.34, 12.58) * mm, "end": v(12.36, 12.71) * mm});
            skLineSegment(sketch, "E1069", {"start": v(12.36, 12.71) * mm, "end": v(12.39, 12.84) * mm});
            skLineSegment(sketch, "E1070", {"start": v(12.39, 12.84) * mm, "end": v(12.4, 12.96) * mm});
            skLineSegment(sketch, "E1071", {"start": v(12.4, 12.96) * mm, "end": v(12.42, 13.07) * mm});
            skLineSegment(sketch, "E1072", {"start": v(12.42, 13.07) * mm, "end": v(12.44, 13.2) * mm});
            skLineSegment(sketch, "E1073", {"start": v(12.44, 13.2) * mm, "end": v(12.46, 13.34) * mm});
            skLineSegment(sketch, "E1074", {"start": v(12.46, 13.34) * mm, "end": v(12.47, 13.49) * mm});
            skLineSegment(sketch, "E1075", {"start": v(12.47, 13.49) * mm, "end": v(12.54, 14.23) * mm});
            skLineSegment(sketch, "E1076", {"start": v(12.54, 14.23) * mm, "end": v(12.5, 14.26) * mm});
            skLineSegment(sketch, "E1077", {"start": v(12.5, 14.26) * mm, "end": v(12.36, 14.34) * mm});
            skLineSegment(sketch, "E1078", {"start": v(12.36, 14.34) * mm, "end": v(12.21, 14.42) * mm});
            skLineSegment(sketch, "E1079", {"start": v(12.21, 14.42) * mm, "end": v(12.07, 14.5) * mm});
            skLineSegment(sketch, "E1080", {"start": v(12.07, 14.5) * mm, "end": v(11.92, 14.58) * mm});
            skLineSegment(sketch, "E1081", {"start": v(11.92, 14.58) * mm, "end": v(11.78, 14.66) * mm});
            skLineSegment(sketch, "E1082", {"start": v(11.78, 14.66) * mm, "end": v(11.63, 14.74) * mm});
            skLineSegment(sketch, "E1083", {"start": v(11.63, 14.74) * mm, "end": v(11.59, 14.76) * mm});
            skLineSegment(sketch, "E1084", {"start": v(11.59, 14.76) * mm, "end": v(10.97, 14.29) * mm});
            skLineSegment(sketch, "E1085", {"start": v(10.97, 14.29) * mm, "end": v(10.84, 14.19) * mm});
            skLineSegment(sketch, "E1086", {"start": v(10.84, 14.19) * mm, "end": v(10.73, 14.1) * mm});
            skLineSegment(sketch, "E1087", {"start": v(10.73, 14.1) * mm, "end": v(10.63, 14.01) * mm});
            skLineSegment(sketch, "E1088", {"start": v(10.63, 14.01) * mm, "end": v(10.54, 13.93) * mm});
            skLineSegment(sketch, "E1089", {"start": v(10.54, 13.93) * mm, "end": v(10.45, 13.85) * mm});
            skLineSegment(sketch, "E1090", {"start": v(10.45, 13.85) * mm, "end": v(10.37, 13.78) * mm});
            skLineSegment(sketch, "E1091", {"start": v(10.37, 13.78) * mm, "end": v(10.28, 13.7) * mm});
            skLineSegment(sketch, "E1092", {"start": v(10.28, 13.7) * mm, "end": v(10.2, 13.62) * mm});
            skLineSegment(sketch, "E1093", {"start": v(10.2, 13.62) * mm, "end": v(10.13, 13.54) * mm});
            skLineSegment(sketch, "E1094", {"start": v(10.13, 13.54) * mm, "end": v(10.06, 13.46) * mm});
            skLineSegment(sketch, "E1095", {"start": v(10.06, 13.46) * mm, "end": v(10.01, 13.42) * mm});
            skLineSegment(sketch, "E1096", {"start": v(10.01, 13.42) * mm, "end": v(10, 13.4) * mm});
            skLineSegment(sketch, "E1097", {"start": v(10, 13.4) * mm, "end": v(9.95, 13.35) * mm});
            skLineSegment(sketch, "E1098", {"start": v(9.95, 13.35) * mm, "end": v(9.89, 13.28) * mm});
            skLineSegment(sketch, "E1099", {"start": v(9.89, 13.28) * mm, "end": v(9.83, 13.2) * mm});
            skLineSegment(sketch, "E1100", {"start": v(9.83, 13.2) * mm, "end": v(9.77, 13.14) * mm});
            skLineSegment(sketch, "E1101", {"start": v(9.77, 13.14) * mm, "end": v(9.72, 13.07) * mm});
            skLineSegment(sketch, "E1102", {"start": v(9.72, 13.07) * mm, "end": v(9.67, 13) * mm});
            skLineSegment(sketch, "E1103", {"start": v(9.67, 13) * mm, "end": v(9.62, 12.95) * mm});
            skLineSegment(sketch, "E1104", {"start": v(9.62, 12.95) * mm, "end": v(9.58, 12.88) * mm});
            skLineSegment(sketch, "E1105", {"start": v(9.58, 12.88) * mm, "end": v(9.54, 12.83) * mm});
            skLineSegment(sketch, "E1106", {"start": v(9.54, 12.83) * mm, "end": v(9.5, 12.78) * mm});
            skLineSegment(sketch, "E1107", {"start": v(9.5, 12.78) * mm, "end": v(9.33, 12.5) * mm});
            skLineSegment(sketch, "E1108", {"start": v(9.33, 12.5) * mm, "end": v(9.32, 12.51) * mm});
            skLineSegment(sketch, "E1109", {"start": v(9.32, 12.51) * mm, "end": v(9.3, 12.46) * mm});
            skLineSegment(sketch, "E1110", {"start": v(9.3, 12.46) * mm, "end": v(9.29, 12.47) * mm});
            skLineSegment(sketch, "E1111", {"start": v(9.29, 12.47) * mm, "end": v(9.25, 12.41) * mm});
            skLineSegment(sketch, "E1112", {"start": v(9.25, 12.41) * mm, "end": v(9.24, 12.41) * mm});
            skLineSegment(sketch, "E1113", {"start": v(9.24, 12.41) * mm, "end": v(9.2, 12.36) * mm});
            skLineSegment(sketch, "E1114", {"start": v(9.2, 12.36) * mm, "end": v(9.19, 12.37) * mm});
            skLineSegment(sketch, "E1115", {"start": v(9.19, 12.37) * mm, "end": v(9.16, 12.33) * mm});
            skLineSegment(sketch, "E1116", {"start": v(9.16, 12.33) * mm, "end": v(9.14, 12.33) * mm});
            skLineSegment(sketch, "E1117", {"start": v(9.14, 12.33) * mm, "end": v(9.12, 12.3) * mm});
            skLineSegment(sketch, "E1118", {"start": v(9.12, 12.3) * mm, "end": v(9.1, 12.3) * mm});
            skLineSegment(sketch, "E1119", {"start": v(9.1, 12.3) * mm, "end": v(9.07, 12.27) * mm});
            skLineSegment(sketch, "E1120", {"start": v(9.07, 12.27) * mm, "end": v(9.03, 12.26) * mm});
            skLineSegment(sketch, "E1121", {"start": v(9.03, 12.26) * mm, "end": v(9, 12.24) * mm});
            skLineSegment(sketch, "E1122", {"start": v(9, 12.24) * mm, "end": v(8.96, 12.24) * mm});
            skLineSegment(sketch, "E1123", {"start": v(8.96, 12.24) * mm, "end": v(8.93, 12.24) * mm});
            skLineSegment(sketch, "E1124", {"start": v(8.93, 12.24) * mm, "end": v(8.93, 12.23) * mm});
            skLineSegment(sketch, "E1125", {"start": v(8.93, 12.23) * mm, "end": v(8.92, 12.24) * mm});
            skLineSegment(sketch, "E1126", {"start": v(8.92, 12.24) * mm, "end": v(8.9, 12.25) * mm});
            skLineSegment(sketch, "E1127", {"start": v(8.9, 12.25) * mm, "end": v(8.9, 12.24) * mm});
            skLineSegment(sketch, "E1128", {"start": v(8.9, 12.24) * mm, "end": v(8.69, 12.33) * mm});
            skLineSegment(sketch, "E1129", {"start": v(8.69, 12.33) * mm, "end": v(8.51, 12.4) * mm});
            skLineSegment(sketch, "E1130", {"start": v(8.51, 12.4) * mm, "end": v(8.43, 12.44) * mm});
            skLineSegment(sketch, "E1131", {"start": v(8.43, 12.44) * mm, "end": v(8.25, 12.52) * mm});
            skLineSegment(sketch, "E1132", {"start": v(8.25, 12.52) * mm, "end": v(8.04, 12.6) * mm});
            skLineSegment(sketch, "E1133", {"start": v(8.04, 12.6) * mm, "end": v(8.03, 12.6) * mm});
            skLineSegment(sketch, "E1134", {"start": v(8.03, 12.6) * mm, "end": v(8.02, 12.61) * mm});
            skLineSegment(sketch, "E1135", {"start": v(8.02, 12.61) * mm, "end": v(8.01, 12.62) * mm});
            skLineSegment(sketch, "E1136", {"start": v(8.01, 12.62) * mm, "end": v(8, 12.63) * mm});
            skLineSegment(sketch, "E1137", {"start": v(8, 12.63) * mm, "end": v(7.98, 12.65) * mm});
            skLineSegment(sketch, "E1138", {"start": v(7.98, 12.65) * mm, "end": v(7.97, 12.68) * mm});
            skLineSegment(sketch, "E1139", {"start": v(7.97, 12.68) * mm, "end": v(7.95, 12.72) * mm});
            skLineSegment(sketch, "E1140", {"start": v(7.95, 12.72) * mm, "end": v(7.94, 12.75) * mm});
            skLineSegment(sketch, "E1141", {"start": v(7.94, 12.75) * mm, "end": v(7.93, 12.8) * mm});
            skLineSegment(sketch, "E1142", {"start": v(7.93, 12.8) * mm, "end": v(7.92, 12.85) * mm});
            skLineSegment(sketch, "E1143", {"start": v(7.92, 12.85) * mm, "end": v(7.9, 12.87) * mm});
            skLineSegment(sketch, "E1144", {"start": v(7.9, 12.87) * mm, "end": v(7.92, 12.92) * mm});
            skLineSegment(sketch, "E1145", {"start": v(7.92, 12.92) * mm, "end": v(7.91, 12.95) * mm});
            skLineSegment(sketch, "E1146", {"start": v(7.91, 12.95) * mm, "end": v(7.9, 12.98) * mm});
            skLineSegment(sketch, "E1147", {"start": v(7.9, 12.98) * mm, "end": v(7.92, 13.05) * mm});
            skLineSegment(sketch, "E1148", {"start": v(7.92, 13.05) * mm, "end": v(7.91, 13.06) * mm});
            skLineSegment(sketch, "E1149", {"start": v(7.91, 13.06) * mm, "end": v(7.93, 13.13) * mm});
            skLineSegment(sketch, "E1150", {"start": v(7.93, 13.13) * mm, "end": v(7.92, 13.14) * mm});
            skLineSegment(sketch, "E1151", {"start": v(7.92, 13.14) * mm, "end": v(8, 13.47) * mm});
            skLineSegment(sketch, "E1152", {"start": v(8, 13.47) * mm, "end": v(8, 13.52) * mm});
            skLineSegment(sketch, "E1153", {"start": v(8, 13.52) * mm, "end": v(8.02, 13.57) * mm});
            skLineSegment(sketch, "E1154", {"start": v(8.02, 13.57) * mm, "end": v(8.03, 13.62) * mm});
            skLineSegment(sketch, "E1155", {"start": v(8.03, 13.62) * mm, "end": v(8.03, 13.67) * mm});
            skLineSegment(sketch, "E1156", {"start": v(8.03, 13.67) * mm, "end": v(8.04, 13.73) * mm});
            skLineSegment(sketch, "E1157", {"start": v(8.04, 13.73) * mm, "end": v(8.05, 13.8) * mm});
            skLineSegment(sketch, "E1158", {"start": v(8.05, 13.8) * mm, "end": v(8.06, 13.87) * mm});
            skLineSegment(sketch, "E1159", {"start": v(8.06, 13.87) * mm, "end": v(8.07, 13.96) * mm});
            skLineSegment(sketch, "E1160", {"start": v(8.07, 13.96) * mm, "end": v(8.07, 14.04) * mm});
            skLineSegment(sketch, "E1161", {"start": v(8.07, 14.04) * mm, "end": v(8.08, 14.13) * mm});
            skLineSegment(sketch, "E1162", {"start": v(8.08, 14.13) * mm, "end": v(8.08, 14.19) * mm});
            skLineSegment(sketch, "E1163", {"start": v(8.08, 14.19) * mm, "end": v(8.08, 14.22) * mm});
            skLineSegment(sketch, "E1164", {"start": v(8.08, 14.22) * mm, "end": v(8.09, 14.28) * mm});
            skLineSegment(sketch, "E1165", {"start": v(8.09, 14.28) * mm, "end": v(8.09, 14.4) * mm});
            skLineSegment(sketch, "E1166", {"start": v(8.09, 14.4) * mm, "end": v(8.1, 14.51) * mm});
            skLineSegment(sketch, "E1167", {"start": v(8.1, 14.51) * mm, "end": v(8.09, 14.64) * mm});
            skLineSegment(sketch, "E1168", {"start": v(8.09, 14.64) * mm, "end": v(8.09, 14.77) * mm});
            skLineSegment(sketch, "E1169", {"start": v(8.09, 14.77) * mm, "end": v(8.08, 14.9) * mm});
            skLineSegment(sketch, "E1170", {"start": v(8.08, 14.9) * mm, "end": v(8.07, 15.06) * mm});
            skLineSegment(sketch, "E1171", {"start": v(8.07, 15.06) * mm, "end": v(8.06, 15.21) * mm});
            skLineSegment(sketch, "E1172", {"start": v(8.06, 15.21) * mm, "end": v(8.05, 15.38) * mm});
            skLineSegment(sketch, "E1173", {"start": v(8.05, 15.38) * mm, "end": v(8.03, 15.53) * mm});
            skLineSegment(sketch, "E1174", {"start": v(8.03, 15.53) * mm, "end": v(7.94, 16.28) * mm});
            skLineSegment(sketch, "E1175", {"start": v(7.94, 16.28) * mm, "end": v(7.87, 16.3) * mm});
            skLineSegment(sketch, "E1176", {"start": v(7.87, 16.3) * mm, "end": v(7.68, 16.36) * mm});
            skLineSegment(sketch, "E1177", {"start": v(7.68, 16.36) * mm, "end": v(7.48, 16.42) * mm});
            skLineSegment(sketch, "E1178", {"start": v(7.48, 16.42) * mm, "end": v(7.28, 16.48) * mm});
            skLineSegment(sketch, "E1179", {"start": v(7.28, 16.48) * mm, "end": v(7.08, 16.54) * mm});
            skLineSegment(sketch, "E1180", {"start": v(7.08, 16.54) * mm, "end": v(6.88, 16.6) * mm});
            skLineSegment(sketch, "E1181", {"start": v(6.88, 16.6) * mm, "end": v(6.36, 15.96) * mm});
            skLineSegment(sketch, "E1182", {"start": v(6.36, 15.96) * mm, "end": v(6.26, 15.84) * mm});
            skLineSegment(sketch, "E1183", {"start": v(6.26, 15.84) * mm, "end": v(6.17, 15.72) * mm});
            skLineSegment(sketch, "E1184", {"start": v(6.17, 15.72) * mm, "end": v(6.07, 15.6) * mm});
            skLineSegment(sketch, "E1185", {"start": v(6.07, 15.6) * mm, "end": v(5.99, 15.48) * mm});
            skLineSegment(sketch, "E1186", {"start": v(5.99, 15.48) * mm, "end": v(5.9, 15.36) * mm});
            skLineSegment(sketch, "E1187", {"start": v(5.9, 15.36) * mm, "end": v(5.84, 15.26) * mm});
            skLineSegment(sketch, "E1188", {"start": v(5.84, 15.26) * mm, "end": v(5.78, 15.17) * mm});
            skLineSegment(sketch, "E1189", {"start": v(5.78, 15.17) * mm, "end": v(5.72, 15.09) * mm});
            skLineSegment(sketch, "E1190", {"start": v(5.72, 15.09) * mm, "end": v(5.67, 15) * mm});
            skLineSegment(sketch, "E1191", {"start": v(5.67, 15) * mm, "end": v(5.64, 14.95) * mm});
            skLineSegment(sketch, "E1192", {"start": v(5.64, 14.95) * mm, "end": v(5.62, 14.92) * mm});
            skLineSegment(sketch, "E1193", {"start": v(5.62, 14.92) * mm, "end": v(5.6, 14.87) * mm});
            skLineSegment(sketch, "E1194", {"start": v(5.6, 14.87) * mm, "end": v(5.55, 14.8) * mm});
            skLineSegment(sketch, "E1195", {"start": v(5.55, 14.8) * mm, "end": v(5.5, 14.71) * mm});
            skLineSegment(sketch, "E1196", {"start": v(5.5, 14.71) * mm, "end": v(5.46, 14.64) * mm});
            skLineSegment(sketch, "E1197", {"start": v(5.46, 14.64) * mm, "end": v(5.43, 14.57) * mm});
            skLineSegment(sketch, "E1198", {"start": v(5.43, 14.57) * mm, "end": v(5.4, 14.5) * mm});
            skLineSegment(sketch, "E1199", {"start": v(5.4, 14.5) * mm, "end": v(5.36, 14.43) * mm});
            skLineSegment(sketch, "E1200", {"start": v(5.36, 14.43) * mm, "end": v(5.33, 14.36) * mm});
            skLineSegment(sketch, "E1201", {"start": v(5.33, 14.36) * mm, "end": v(5.3, 14.3) * mm});
            skLineSegment(sketch, "E1202", {"start": v(5.3, 14.3) * mm, "end": v(5.27, 14.25) * mm});
            skLineSegment(sketch, "E1203", {"start": v(5.27, 14.25) * mm, "end": v(5.25, 14.2) * mm});
            skLineSegment(sketch, "E1204", {"start": v(5.25, 14.2) * mm, "end": v(5.14, 13.92) * mm});
            skLineSegment(sketch, "E1205", {"start": v(5.14, 13.92) * mm, "end": v(5.13, 13.92) * mm});
            skLineSegment(sketch, "E1206", {"start": v(5.13, 13.92) * mm, "end": v(5.1, 13.86) * mm});
            skLineSegment(sketch, "E1207", {"start": v(5.1, 13.86) * mm, "end": v(5.1, 13.86) * mm});
            skLineSegment(sketch, "E1208", {"start": v(5.1, 13.86) * mm, "end": v(5.08, 13.8) * mm});
            skLineSegment(sketch, "E1209", {"start": v(5.08, 13.8) * mm, "end": v(5.07, 13.8) * mm});
            skLineSegment(sketch, "E1210", {"start": v(5.07, 13.8) * mm, "end": v(5.05, 13.75) * mm});
            skLineSegment(sketch, "E1211", {"start": v(5.05, 13.75) * mm, "end": v(5.04, 13.76) * mm});
            skLineSegment(sketch, "E1212", {"start": v(5.04, 13.76) * mm, "end": v(5.02, 13.71) * mm});
            skLineSegment(sketch, "E1213", {"start": v(5.02, 13.71) * mm, "end": v(5, 13.71) * mm});
            skLineSegment(sketch, "E1214", {"start": v(5, 13.71) * mm, "end": v(4.99, 13.68) * mm});
            skLineSegment(sketch, "E1215", {"start": v(4.99, 13.68) * mm, "end": v(4.98, 13.68) * mm});
            skLineSegment(sketch, "E1216", {"start": v(4.98, 13.68) * mm, "end": v(4.95, 13.65) * mm});
            skLineSegment(sketch, "E1217", {"start": v(4.95, 13.65) * mm, "end": v(4.92, 13.62) * mm});
            skLineSegment(sketch, "E1218", {"start": v(4.92, 13.62) * mm, "end": v(4.9, 13.6) * mm});
            skLineSegment(sketch, "E1219", {"start": v(4.9, 13.6) * mm, "end": v(4.86, 13.59) * mm});
            skLineSegment(sketch, "E1220", {"start": v(4.86, 13.59) * mm, "end": v(4.84, 13.58) * mm});
            skLineSegment(sketch, "E1221", {"start": v(4.84, 13.58) * mm, "end": v(4.82, 13.57) * mm});
            skLineSegment(sketch, "E1222", {"start": v(4.82, 13.57) * mm, "end": v(4.8, 13.57) * mm});
            skLineSegment(sketch, "E1223", {"start": v(4.8, 13.57) * mm, "end": v(4.8, 13.57) * mm});
            skLineSegment(sketch, "E1224", {"start": v(4.8, 13.57) * mm, "end": v(4.78, 13.58) * mm});
            skLineSegment(sketch, "E1225", {"start": v(4.78, 13.58) * mm, "end": v(4.78, 13.57) * mm});
            skLineSegment(sketch, "E1226", {"start": v(4.78, 13.57) * mm, "end": v(4.57, 13.62) * mm});
            skLineSegment(sketch, "E1227", {"start": v(4.57, 13.62) * mm, "end": v(4.38, 13.65) * mm});
            skLineSegment(sketch, "E1228", {"start": v(4.38, 13.65) * mm, "end": v(4.27, 13.68) * mm});
            skLineSegment(sketch, "E1229", {"start": v(4.27, 13.68) * mm, "end": v(4.08, 13.71) * mm});
            skLineSegment(sketch, "E1230", {"start": v(4.08, 13.71) * mm, "end": v(3.87, 13.75) * mm});
            skLineSegment(sketch, "E1231", {"start": v(3.87, 13.75) * mm, "end": v(3.86, 13.75) * mm});
            skLineSegment(sketch, "E1232", {"start": v(3.86, 13.75) * mm, "end": v(3.85, 13.76) * mm});
            skLineSegment(sketch, "E1233", {"start": v(3.85, 13.76) * mm, "end": v(3.84, 13.76) * mm});
            skLineSegment(sketch, "E1234", {"start": v(3.84, 13.76) * mm, "end": v(3.83, 13.77) * mm});
            skLineSegment(sketch, "E1235", {"start": v(3.83, 13.77) * mm, "end": v(3.8, 13.78) * mm});
            skLineSegment(sketch, "E1236", {"start": v(3.8, 13.78) * mm, "end": v(3.79, 13.8) * mm});
            skLineSegment(sketch, "E1237", {"start": v(3.79, 13.8) * mm, "end": v(3.77, 13.83) * mm});
            skLineSegment(sketch, "E1238", {"start": v(3.77, 13.83) * mm, "end": v(3.75, 13.86) * mm});
            skLineSegment(sketch, "E1239", {"start": v(3.75, 13.86) * mm, "end": v(3.73, 13.89) * mm});
            skLineSegment(sketch, "E1240", {"start": v(3.73, 13.89) * mm, "end": v(3.73, 13.93) * mm});
            skLineSegment(sketch, "E1241", {"start": v(3.73, 13.93) * mm, "end": v(3.7, 13.96) * mm});
            skLineSegment(sketch, "E1242", {"start": v(3.7, 13.96) * mm, "end": v(3.7, 13.99) * mm});
            skLineSegment(sketch, "E1243", {"start": v(3.7, 13.99) * mm, "end": v(3.7, 14.04) * mm});
            skLineSegment(sketch, "E1244", {"start": v(3.7, 14.04) * mm, "end": v(3.68, 14.08) * mm});
            skLineSegment(sketch, "E1245", {"start": v(3.68, 14.08) * mm, "end": v(3.67, 14.11) * mm});
            skLineSegment(sketch, "E1246", {"start": v(3.67, 14.11) * mm, "end": v(3.67, 14.18) * mm});
            skLineSegment(sketch, "E1247", {"start": v(3.67, 14.18) * mm, "end": v(3.66, 14.18) * mm});
            skLineSegment(sketch, "E1248", {"start": v(3.66, 14.18) * mm, "end": v(3.66, 14.56) * mm});
            skLineSegment(sketch, "E1249", {"start": v(3.66, 14.56) * mm, "end": v(3.66, 14.62) * mm});
            skLineSegment(sketch, "E1250", {"start": v(3.66, 14.62) * mm, "end": v(3.66, 14.68) * mm});
            skLineSegment(sketch, "E1251", {"start": v(3.66, 14.68) * mm, "end": v(3.65, 14.76) * mm});
            skLineSegment(sketch, "E1252", {"start": v(3.65, 14.76) * mm, "end": v(3.65, 14.84) * mm});
            skLineSegment(sketch, "E1253", {"start": v(3.65, 14.84) * mm, "end": v(3.64, 14.92) * mm});
            skLineSegment(sketch, "E1254", {"start": v(3.64, 14.92) * mm, "end": v(3.63, 15.01) * mm});
            skLineSegment(sketch, "E1255", {"start": v(3.63, 15.01) * mm, "end": v(3.62, 15.09) * mm});
            skLineSegment(sketch, "E1256", {"start": v(3.62, 15.09) * mm, "end": v(3.61, 15.16) * mm});
            skLineSegment(sketch, "E1257", {"start": v(3.61, 15.16) * mm, "end": v(3.6, 15.26) * mm});
            skLineSegment(sketch, "E1258", {"start": v(3.6, 15.26) * mm, "end": v(3.6, 15.31) * mm});
            skLineSegment(sketch, "E1259", {"start": v(3.6, 15.31) * mm, "end": v(3.59, 15.35) * mm});
            skLineSegment(sketch, "E1260", {"start": v(3.59, 15.35) * mm, "end": v(3.58, 15.4) * mm});
            skLineSegment(sketch, "E1261", {"start": v(3.58, 15.4) * mm, "end": v(3.56, 15.51) * mm});
            skLineSegment(sketch, "E1262", {"start": v(3.56, 15.51) * mm, "end": v(3.54, 15.61) * mm});
            skLineSegment(sketch, "E1263", {"start": v(3.54, 15.61) * mm, "end": v(3.51, 15.73) * mm});
            skLineSegment(sketch, "E1264", {"start": v(3.51, 15.73) * mm, "end": v(3.5, 15.84) * mm});
            skLineSegment(sketch, "E1265", {"start": v(3.5, 15.84) * mm, "end": v(3.46, 15.96) * mm});
            skLineSegment(sketch, "E1266", {"start": v(3.46, 15.96) * mm, "end": v(3.43, 16.08) * mm});
            skLineSegment(sketch, "E1267", {"start": v(3.43, 16.08) * mm, "end": v(3.4, 16.22) * mm});
            skLineSegment(sketch, "E1268", {"start": v(3.4, 16.22) * mm, "end": v(3.36, 16.35) * mm});
            skLineSegment(sketch, "E1269", {"start": v(3.36, 16.35) * mm, "end": v(3.32, 16.5) * mm});
            skLineSegment(sketch, "E1270", {"start": v(3.32, 16.5) * mm, "end": v(3.27, 16.64) * mm});
            skLineSegment(sketch, "E1271", {"start": v(3.27, 16.64) * mm, "end": v(3.04, 17.33) * mm});
            skLineSegment(sketch, "E1272", {"start": v(3.04, 17.33) * mm, "end": v(2.9, 17.35) * mm});
            skLineSegment(sketch, "E1273", {"start": v(2.9, 17.35) * mm, "end": v(2.65, 17.38) * mm});
            skLineSegment(sketch, "E1274", {"start": v(2.65, 17.38) * mm, "end": v(2.4, 17.4) * mm});
            skLineSegment(sketch, "E1275", {"start": v(2.4, 17.4) * mm, "end": v(2.16, 17.42) * mm});
            skLineSegment(sketch, "E1276", {"start": v(2.16, 17.42) * mm, "end": v(1.94, 17.44) * mm});
            skLineSegment(sketch, "E1277", {"start": v(1.94, 17.44) * mm, "end": v(1.56, 16.72) * mm});
            skLineSegment(sketch, "E1278", {"start": v(1.56, 16.72) * mm, "end": v(1.49, 16.6) * mm});
            skLineSegment(sketch, "E1279", {"start": v(1.49, 16.6) * mm, "end": v(1.42, 16.47) * mm});
            skLineSegment(sketch, "E1280", {"start": v(1.42, 16.47) * mm, "end": v(1.37, 16.35) * mm});
            skLineSegment(sketch, "E1281", {"start": v(1.37, 16.35) * mm, "end": v(1.3, 16.23) * mm});
            skLineSegment(sketch, "E1282", {"start": v(1.3, 16.23) * mm, "end": v(1.26, 16.11) * mm});
            skLineSegment(sketch, "E1283", {"start": v(1.26, 16.11) * mm, "end": v(1.2, 16) * mm});
            skLineSegment(sketch, "E1284", {"start": v(1.2, 16) * mm, "end": v(1.16, 15.88) * mm});
            skLineSegment(sketch, "E1285", {"start": v(1.16, 15.88) * mm, "end": v(1.11, 15.77) * mm});
            skLineSegment(sketch, "E1286", {"start": v(1.11, 15.77) * mm, "end": v(1.07, 15.66) * mm});
            skLineSegment(sketch, "E1287", {"start": v(1.07, 15.66) * mm, "end": v(1.04, 15.59) * mm});
            skLineSegment(sketch, "E1288", {"start": v(1.04, 15.59) * mm, "end": v(1.03, 15.55) * mm});
            skLineSegment(sketch, "E1289", {"start": v(1.03, 15.55) * mm, "end": v(1, 15.5) * mm});
            skLineSegment(sketch, "E1290", {"start": v(1, 15.5) * mm, "end": v(0.97, 15.38) * mm});
            skLineSegment(sketch, "E1291", {"start": v(0.97, 15.38) * mm, "end": v(0.94, 15.3) * mm});
            skLineSegment(sketch, "E1292", {"start": v(0.94, 15.3) * mm, "end": v(0.91, 15.2) * mm});
            skLineSegment(sketch, "E1293", {"start": v(0.91, 15.2) * mm, "end": v(0.89, 15.11) * mm});
            skLineSegment(sketch, "E1294", {"start": v(0.89, 15.11) * mm, "end": v(0.86, 15.03) * mm});
            skLineSegment(sketch, "E1295", {"start": v(0.86, 15.03) * mm, "end": v(0.84, 14.95) * mm});
            skLineSegment(sketch, "E1296", {"start": v(0.84, 14.95) * mm, "end": v(0.83, 14.87) * mm});
            skLineSegment(sketch, "E1297", {"start": v(0.83, 14.87) * mm, "end": v(0.81, 14.8) * mm});
            skLineSegment(sketch, "E1298", {"start": v(0.81, 14.8) * mm, "end": v(0.74, 14.44) * mm});
            skLineSegment(sketch, "E1299", {"start": v(0.74, 14.44) * mm, "end": v(0.72, 14.4) * mm});
            skLineSegment(sketch, "E1300", {"start": v(0.72, 14.4) * mm, "end": v(0.7, 14.37) * mm});
            skLineSegment(sketch, "E1301", {"start": v(0.7, 14.37) * mm, "end": v(0.7, 14.3) * mm});
            skLineSegment(sketch, "E1302", {"start": v(0.7, 14.3) * mm, "end": v(0.67, 14.28) * mm});
            skLineSegment(sketch, "E1303", {"start": v(0.67, 14.28) * mm, "end": v(0.65, 14.25) * mm});
            skLineSegment(sketch, "E1304", {"start": v(0.65, 14.25) * mm, "end": v(0.64, 14.2) * mm});
            skLineSegment(sketch, "E1305", {"start": v(0.64, 14.2) * mm, "end": v(0.62, 14.19) * mm});
            skLineSegment(sketch, "E1306", {"start": v(0.62, 14.19) * mm, "end": v(0.6, 14.15) * mm});
            skLineSegment(sketch, "E1307", {"start": v(0.6, 14.15) * mm, "end": v(0.56, 14.12) * mm});
            skLineSegment(sketch, "E1308", {"start": v(0.56, 14.12) * mm, "end": v(0.53, 14.1) * mm});
            skLineSegment(sketch, "E1309", {"start": v(0.53, 14.1) * mm, "end": v(0.5, 14.09) * mm});
            skLineSegment(sketch, "E1310", {"start": v(0.5, 14.09) * mm, "end": v(0.5, 14.08) * mm});
            skLineSegment(sketch, "E1311", {"start": v(0.5, 14.08) * mm, "end": v(0.49, 14.08) * mm});
            skLineSegment(sketch, "E1312", {"start": v(0.49, 14.08) * mm, "end": v(0.47, 14.07) * mm});
            skLineSegment(sketch, "E1313", {"start": v(0.47, 14.07) * mm, "end": v(0.46, 14.07) * mm});
            skLineSegment(sketch, "E1314", {"start": v(0.46, 14.07) * mm, "end": v(0.28, 14.08) * mm});
            skLineSegment(sketch, "E1315", {"start": v(0.28, 14.08) * mm, "end": v(0.06, 14.08) * mm});
            skLineSegment(sketch, "E1316", {"start": v(0.06, 14.08) * mm, "end": v(-0.07, 14.08) * mm});
            skLineSegment(sketch, "E1317", {"start": v(-0.07, 14.08) * mm, "end": v(-0.3, 14.08) * mm});
            skLineSegment(sketch, "E1318", {"start": v(-0.3, 14.08) * mm, "end": v(-0.46, 14.07) * mm});
            skLineSegment(sketch, "E1319", {"start": v(-0.46, 14.07) * mm, "end": v(-0.48, 14.07) * mm});
            skLineSegment(sketch, "E1320", {"start": v(-0.48, 14.07) * mm, "end": v(-0.5, 14.08) * mm});
            skLineSegment(sketch, "E1321", {"start": v(-0.5, 14.08) * mm, "end": v(-0.5, 14.08) * mm});
            skLineSegment(sketch, "E1322", {"start": v(-0.5, 14.08) * mm, "end": v(-0.51, 14.09) * mm});
            skLineSegment(sketch, "E1323", {"start": v(-0.51, 14.09) * mm, "end": v(-0.54, 14.1) * mm});
            skLineSegment(sketch, "E1324", {"start": v(-0.54, 14.1) * mm, "end": v(-0.57, 14.12) * mm});
            skLineSegment(sketch, "E1325", {"start": v(-0.57, 14.12) * mm, "end": v(-0.6, 14.15) * mm});
            skLineSegment(sketch, "E1326", {"start": v(-0.6, 14.15) * mm, "end": v(-0.62, 14.18) * mm});
            skLineSegment(sketch, "E1327", {"start": v(-0.62, 14.18) * mm, "end": v(-0.64, 14.21) * mm});
            skLineSegment(sketch, "E1328", {"start": v(-0.64, 14.21) * mm, "end": v(-0.67, 14.26) * mm});
            skLineSegment(sketch, "E1329", {"start": v(-0.67, 14.26) * mm, "end": v(-0.68, 14.28) * mm});
            skLineSegment(sketch, "E1330", {"start": v(-0.68, 14.28) * mm, "end": v(-0.7, 14.33) * mm});
            skLineSegment(sketch, "E1331", {"start": v(-0.7, 14.33) * mm, "end": v(-0.71, 14.35) * mm});
            skLineSegment(sketch, "E1332", {"start": v(-0.71, 14.35) * mm, "end": v(-0.72, 14.38) * mm});
            skLineSegment(sketch, "E1333", {"start": v(-0.72, 14.38) * mm, "end": v(-0.74, 14.44) * mm});
            skLineSegment(sketch, "E1334", {"start": v(-0.74, 14.44) * mm, "end": v(-0.74, 14.44) * mm});
            skLineSegment(sketch, "E1335", {"start": v(-0.74, 14.44) * mm, "end": v(-0.82, 14.8) * mm});
            skLineSegment(sketch, "E1336", {"start": v(-0.82, 14.8) * mm, "end": v(-0.83, 14.86) * mm});
            skLineSegment(sketch, "E1337", {"start": v(-0.83, 14.86) * mm, "end": v(-0.84, 14.92) * mm});
            skLineSegment(sketch, "E1338", {"start": v(-0.84, 14.92) * mm, "end": v(-0.86, 14.98) * mm});
            skLineSegment(sketch, "E1339", {"start": v(-0.86, 14.98) * mm, "end": v(-0.88, 15.05) * mm});
            skLineSegment(sketch, "E1340", {"start": v(-0.88, 15.05) * mm, "end": v(-0.9, 15.14) * mm});
            skLineSegment(sketch, "E1341", {"start": v(-0.9, 15.14) * mm, "end": v(-0.92, 15.21) * mm});
            skLineSegment(sketch, "E1342", {"start": v(-0.92, 15.21) * mm, "end": v(-0.95, 15.3) * mm});
            skLineSegment(sketch, "E1343", {"start": v(-0.95, 15.3) * mm, "end": v(-0.98, 15.39) * mm});
            skLineSegment(sketch, "E1344", {"start": v(-0.98, 15.39) * mm, "end": v(-1.01, 15.49) * mm});
            skLineSegment(sketch, "E1345", {"start": v(-1.01, 15.49) * mm, "end": v(-1.03, 15.54) * mm});
            skLineSegment(sketch, "E1346", {"start": v(-1.03, 15.54) * mm, "end": v(-1.05, 15.6) * mm});
            skLineSegment(sketch, "E1347", {"start": v(-1.05, 15.6) * mm, "end": v(-1.08, 15.66) * mm});
            skLineSegment(sketch, "E1348", {"start": v(-1.08, 15.66) * mm, "end": v(-1.12, 15.78) * mm});
            skLineSegment(sketch, "E1349", {"start": v(-1.12, 15.78) * mm, "end": v(-1.17, 15.89) * mm});
            skLineSegment(sketch, "E1350", {"start": v(-1.17, 15.89) * mm, "end": v(-1.22, 16.02) * mm});
            skLineSegment(sketch, "E1351", {"start": v(-1.22, 16.02) * mm, "end": v(-1.28, 16.15) * mm});
            skLineSegment(sketch, "E1352", {"start": v(-1.28, 16.15) * mm, "end": v(-1.34, 16.28) * mm});
            skLineSegment(sketch, "E1353", {"start": v(-1.34, 16.28) * mm, "end": v(-1.4, 16.42) * mm});
            skLineSegment(sketch, "E1354", {"start": v(-1.4, 16.42) * mm, "end": v(-1.48, 16.57) * mm});
            skLineSegment(sketch, "E1355", {"start": v(-1.48, 16.57) * mm, "end": v(-1.56, 16.72) * mm});
            skLineSegment(sketch, "E1356", {"start": v(-1.56, 16.72) * mm, "end": v(-1.95, 17.44) * mm});
            skLineSegment(sketch, "E1357", {"start": v(-1.95, 17.44) * mm, "end": v(-2.06, 17.43) * mm});
            skLineSegment(sketch, "E1358", {"start": v(-2.06, 17.43) * mm, "end": v(-2.34, 17.4) * mm});
            skLineSegment(sketch, "E1359", {"start": v(-2.34, 17.4) * mm, "end": v(-2.62, 17.38) * mm});
            skLineSegment(sketch, "E1360", {"start": v(-2.62, 17.38) * mm, "end": v(-2.9, 17.35) * mm});
            skLineSegment(sketch, "E1361", {"start": v(-2.9, 17.35) * mm, "end": v(-3.05, 17.33) * mm});
            skLineSegment(sketch, "E1362", {"start": v(-3.05, 17.33) * mm, "end": v(-3.3, 16.6) * mm});
            skLineSegment(sketch, "E1363", {"start": v(-3.3, 16.6) * mm, "end": v(-3.34, 16.44) * mm});
            skLineSegment(sketch, "E1364", {"start": v(-3.34, 16.44) * mm, "end": v(-3.38, 16.28) * mm});
            skLineSegment(sketch, "E1365", {"start": v(-3.38, 16.28) * mm, "end": v(-3.42, 16.14) * mm});
            skLineSegment(sketch, "E1366", {"start": v(-3.42, 16.14) * mm, "end": v(-3.46, 15.99) * mm});
            skLineSegment(sketch, "E1367", {"start": v(-3.46, 15.99) * mm, "end": v(-3.5, 15.84) * mm});
            skLineSegment(sketch, "E1368", {"start": v(-3.5, 15.84) * mm, "end": v(-3.53, 15.7) * mm});
            skLineSegment(sketch, "E1369", {"start": v(-3.53, 15.7) * mm, "end": v(-3.55, 15.57) * mm});
            skLineSegment(sketch, "E1370", {"start": v(-3.55, 15.57) * mm, "end": v(-3.58, 15.44) * mm});
            skLineSegment(sketch, "E1371", {"start": v(-3.58, 15.44) * mm, "end": v(-3.6, 15.35) * mm});
            skLineSegment(sketch, "E1372", {"start": v(-3.6, 15.35) * mm, "end": v(-3.6, 15.3) * mm});
            skLineSegment(sketch, "E1373", {"start": v(-3.6, 15.3) * mm, "end": v(-3.6, 15.23) * mm});
            skLineSegment(sketch, "E1374", {"start": v(-3.6, 15.23) * mm, "end": v(-3.63, 15.11) * mm});
            skLineSegment(sketch, "E1375", {"start": v(-3.63, 15.11) * mm, "end": v(-3.64, 15) * mm});
            skLineSegment(sketch, "E1376", {"start": v(-3.64, 15) * mm, "end": v(-3.65, 14.9) * mm});
            skLineSegment(sketch, "E1377", {"start": v(-3.65, 14.9) * mm, "end": v(-3.66, 14.8) * mm});
            skLineSegment(sketch, "E1378", {"start": v(-3.66, 14.8) * mm, "end": v(-3.66, 14.72) * mm});
            skLineSegment(sketch, "E1379", {"start": v(-3.66, 14.72) * mm, "end": v(-3.67, 14.63) * mm});
            skLineSegment(sketch, "E1380", {"start": v(-3.67, 14.63) * mm, "end": v(-3.67, 14.56) * mm});
            skLineSegment(sketch, "E1381", {"start": v(-3.67, 14.56) * mm, "end": v(-3.67, 14.18) * mm});
            skLineSegment(sketch, "E1382", {"start": v(-3.67, 14.18) * mm, "end": v(-3.68, 14.18) * mm});
            skLineSegment(sketch, "E1383", {"start": v(-3.68, 14.18) * mm, "end": v(-3.68, 14.1) * mm});
            skLineSegment(sketch, "E1384", {"start": v(-3.68, 14.1) * mm, "end": v(-3.69, 14.1) * mm});
            skLineSegment(sketch, "E1385", {"start": v(-3.69, 14.1) * mm, "end": v(-3.7, 14.02) * mm});
            skLineSegment(sketch, "E1386", {"start": v(-3.7, 14.02) * mm, "end": v(-3.7, 13.99) * mm});
            skLineSegment(sketch, "E1387", {"start": v(-3.7, 13.99) * mm, "end": v(-3.72, 13.95) * mm});
            skLineSegment(sketch, "E1388", {"start": v(-3.72, 13.95) * mm, "end": v(-3.73, 13.9) * mm});
            skLineSegment(sketch, "E1389", {"start": v(-3.73, 13.9) * mm, "end": v(-3.75, 13.87) * mm});
            skLineSegment(sketch, "E1390", {"start": v(-3.75, 13.87) * mm, "end": v(-3.77, 13.85) * mm});
            skLineSegment(sketch, "E1391", {"start": v(-3.77, 13.85) * mm, "end": v(-3.79, 13.81) * mm});
            skLineSegment(sketch, "E1392", {"start": v(-3.79, 13.81) * mm, "end": v(-3.82, 13.78) * mm});
            skLineSegment(sketch, "E1393", {"start": v(-3.82, 13.78) * mm, "end": v(-3.84, 13.76) * mm});
            skLineSegment(sketch, "E1394", {"start": v(-3.84, 13.76) * mm, "end": v(-3.85, 13.76) * mm});
            skLineSegment(sketch, "E1395", {"start": v(-3.85, 13.76) * mm, "end": v(-3.87, 13.75) * mm});
            skLineSegment(sketch, "E1396", {"start": v(-3.87, 13.75) * mm, "end": v(-3.89, 13.75) * mm});
            skLineSegment(sketch, "E1397", {"start": v(-3.89, 13.75) * mm, "end": v(-4.02, 13.72) * mm});
            skLineSegment(sketch, "E1398", {"start": v(-4.02, 13.72) * mm, "end": v(-4.26, 13.68) * mm});
            skLineSegment(sketch, "E1399", {"start": v(-4.26, 13.68) * mm, "end": v(-4.4, 13.65) * mm});
            skLineSegment(sketch, "E1400", {"start": v(-4.4, 13.65) * mm, "end": v(-4.65, 13.6) * mm});
            skLineSegment(sketch, "E1401", {"start": v(-4.65, 13.6) * mm, "end": v(-4.77, 13.57) * mm});
            skLineSegment(sketch, "E1402", {"start": v(-4.77, 13.57) * mm, "end": v(-4.78, 13.58) * mm});
            skLineSegment(sketch, "E1403", {"start": v(-4.78, 13.58) * mm, "end": v(-4.8, 13.57) * mm});
            skLineSegment(sketch, "E1404", {"start": v(-4.8, 13.57) * mm, "end": v(-4.82, 13.57) * mm});
            skLineSegment(sketch, "E1405", {"start": v(-4.82, 13.57) * mm, "end": v(-4.82, 13.57) * mm});
            skLineSegment(sketch, "E1406", {"start": v(-4.82, 13.57) * mm, "end": v(-4.85, 13.58) * mm});
            skLineSegment(sketch, "E1407", {"start": v(-4.85, 13.58) * mm, "end": v(-4.89, 13.6) * mm});
            skLineSegment(sketch, "E1408", {"start": v(-4.89, 13.6) * mm, "end": v(-4.91, 13.62) * mm});
            skLineSegment(sketch, "E1409", {"start": v(-4.91, 13.62) * mm, "end": v(-4.93, 13.62) * mm});
            skLineSegment(sketch, "E1410", {"start": v(-4.93, 13.62) * mm, "end": v(-4.95, 13.65) * mm});
            skLineSegment(sketch, "E1411", {"start": v(-4.95, 13.65) * mm, "end": v(-4.97, 13.65) * mm});
            skLineSegment(sketch, "E1412", {"start": v(-4.97, 13.65) * mm, "end": v(-4.99, 13.69) * mm});
            skLineSegment(sketch, "E1413", {"start": v(-4.99, 13.69) * mm, "end": v(-5, 13.69) * mm});
            skLineSegment(sketch, "E1414", {"start": v(-5, 13.69) * mm, "end": v(-5.03, 13.73) * mm});
            skLineSegment(sketch, "E1415", {"start": v(-5.03, 13.73) * mm, "end": v(-5.04, 13.73) * mm});
            skLineSegment(sketch, "E1416", {"start": v(-5.04, 13.73) * mm, "end": v(-5.06, 13.78) * mm});
            skLineSegment(sketch, "E1417", {"start": v(-5.06, 13.78) * mm, "end": v(-5.07, 13.78) * mm});
            skLineSegment(sketch, "E1418", {"start": v(-5.07, 13.78) * mm, "end": v(-5.1, 13.84) * mm});
            skLineSegment(sketch, "E1419", {"start": v(-5.1, 13.84) * mm, "end": v(-5.1, 13.84) * mm});
            skLineSegment(sketch, "E1420", {"start": v(-5.1, 13.84) * mm, "end": v(-5.13, 13.9) * mm});
            skLineSegment(sketch, "E1421", {"start": v(-5.13, 13.9) * mm, "end": v(-5.14, 13.9) * mm});
            skLineSegment(sketch, "E1422", {"start": v(-5.14, 13.9) * mm, "end": v(-5.26, 14.2) * mm});
            skLineSegment(sketch, "E1423", {"start": v(-5.26, 14.2) * mm, "end": v(-5.29, 14.27) * mm});
            skLineSegment(sketch, "E1424", {"start": v(-5.29, 14.27) * mm, "end": v(-5.32, 14.34) * mm});
            skLineSegment(sketch, "E1425", {"start": v(-5.32, 14.34) * mm, "end": v(-5.35, 14.4) * mm});
            skLineSegment(sketch, "E1426", {"start": v(-5.35, 14.4) * mm, "end": v(-5.39, 14.48) * mm});
            skLineSegment(sketch, "E1427", {"start": v(-5.39, 14.48) * mm, "end": v(-5.43, 14.57) * mm});
            skLineSegment(sketch, "E1428", {"start": v(-5.43, 14.57) * mm, "end": v(-5.48, 14.65) * mm});
            skLineSegment(sketch, "E1429", {"start": v(-5.48, 14.65) * mm, "end": v(-5.53, 14.75) * mm});
            skLineSegment(sketch, "E1430", {"start": v(-5.53, 14.75) * mm, "end": v(-5.59, 14.85) * mm});
            skLineSegment(sketch, "E1431", {"start": v(-5.59, 14.85) * mm, "end": v(-5.63, 14.92) * mm});
            skLineSegment(sketch, "E1432", {"start": v(-5.63, 14.92) * mm, "end": v(-5.65, 14.95) * mm});
            skLineSegment(sketch, "E1433", {"start": v(-5.65, 14.95) * mm, "end": v(-5.7, 15.03) * mm});
            skLineSegment(sketch, "E1434", {"start": v(-5.7, 15.03) * mm, "end": v(-5.77, 15.14) * mm});
            skLineSegment(sketch, "E1435", {"start": v(-5.77, 15.14) * mm, "end": v(-5.84, 15.26) * mm});
            skLineSegment(sketch, "E1436", {"start": v(-5.84, 15.26) * mm, "end": v(-5.93, 15.39) * mm});
            skLineSegment(sketch, "E1437", {"start": v(-5.93, 15.39) * mm, "end": v(-6.02, 15.52) * mm});
            skLineSegment(sketch, "E1438", {"start": v(-6.02, 15.52) * mm, "end": v(-6.13, 15.66) * mm});
            skLineSegment(sketch, "E1439", {"start": v(-6.13, 15.66) * mm, "end": v(-6.24, 15.8) * mm});
            skLineSegment(sketch, "E1440", {"start": v(-6.24, 15.8) * mm, "end": v(-6.36, 15.95) * mm});
            skLineSegment(sketch, "E1441", {"start": v(-6.36, 15.95) * mm, "end": v(-6.89, 16.59) * mm});
            skLineSegment(sketch, "E1442", {"start": v(-6.89, 16.59) * mm, "end": v(-7.01, 16.56) * mm});
            skLineSegment(sketch, "E1443", {"start": v(-7.01, 16.56) * mm, "end": v(-7.31, 16.47) * mm});
            skLineSegment(sketch, "E1444", {"start": v(-7.31, 16.47) * mm, "end": v(-7.62, 16.38) * mm});
            skLineSegment(sketch, "E1445", {"start": v(-7.62, 16.38) * mm, "end": v(-7.92, 16.28) * mm});
            skLineSegment(sketch, "E1446", {"start": v(-7.92, 16.28) * mm, "end": v(-7.95, 16.27) * mm});
            skLineSegment(sketch, "E1447", {"start": v(-7.95, 16.27) * mm, "end": v(-8.05, 15.41) * mm});
            skLineSegment(sketch, "E1448", {"start": v(-8.05, 15.41) * mm, "end": v(-8.07, 15.23) * mm});
            skLineSegment(sketch, "E1449", {"start": v(-8.07, 15.23) * mm, "end": v(-8.08, 15.05) * mm});
            skLineSegment(sketch, "E1450", {"start": v(-8.08, 15.05) * mm, "end": v(-8.09, 14.88) * mm});
            skLineSegment(sketch, "E1451", {"start": v(-8.09, 14.88) * mm, "end": v(-8.1, 14.72) * mm});
            skLineSegment(sketch, "E1452", {"start": v(-8.1, 14.72) * mm, "end": v(-8.1, 14.59) * mm});
            skLineSegment(sketch, "E1453", {"start": v(-8.1, 14.59) * mm, "end": v(-8.1, 14.49) * mm});
            skLineSegment(sketch, "E1454", {"start": v(-8.1, 14.49) * mm, "end": v(-8.1, 14.39) * mm});
            skLineSegment(sketch, "E1455", {"start": v(-8.1, 14.39) * mm, "end": v(-8.1, 14.3) * mm});
            skLineSegment(sketch, "E1456", {"start": v(-8.1, 14.3) * mm, "end": v(-8.09, 14.23) * mm});
            skLineSegment(sketch, "E1457", {"start": v(-8.09, 14.23) * mm, "end": v(-8.09, 14.18) * mm});
            skLineSegment(sketch, "E1458", {"start": v(-8.09, 14.18) * mm, "end": v(-8.08, 14.12) * mm});
            skLineSegment(sketch, "E1459", {"start": v(-8.08, 14.12) * mm, "end": v(-8.08, 14.03) * mm});
            skLineSegment(sketch, "E1460", {"start": v(-8.08, 14.03) * mm, "end": v(-8.07, 13.95) * mm});
            skLineSegment(sketch, "E1461", {"start": v(-8.07, 13.95) * mm, "end": v(-8.07, 13.88) * mm});
            skLineSegment(sketch, "E1462", {"start": v(-8.07, 13.88) * mm, "end": v(-8.06, 13.8) * mm});
            skLineSegment(sketch, "E1463", {"start": v(-8.06, 13.8) * mm, "end": v(-8.05, 13.74) * mm});
            skLineSegment(sketch, "E1464", {"start": v(-8.05, 13.74) * mm, "end": v(-8.04, 13.68) * mm});
            skLineSegment(sketch, "E1465", {"start": v(-8.04, 13.68) * mm, "end": v(-8.03, 13.62) * mm});
            skLineSegment(sketch, "E1466", {"start": v(-8.03, 13.62) * mm, "end": v(-8.02, 13.57) * mm});
            skLineSegment(sketch, "E1467", {"start": v(-8.02, 13.57) * mm, "end": v(-8.01, 13.52) * mm});
            skLineSegment(sketch, "E1468", {"start": v(-8.01, 13.52) * mm, "end": v(-8, 13.48) * mm});
            skLineSegment(sketch, "E1469", {"start": v(-8, 13.48) * mm, "end": v(-7.92, 13.1) * mm});
            skLineSegment(sketch, "E1470", {"start": v(-7.92, 13.1) * mm, "end": v(-7.92, 13.07) * mm});
            skLineSegment(sketch, "E1471", {"start": v(-7.92, 13.07) * mm, "end": v(-7.92, 13.03) * mm});
            skLineSegment(sketch, "E1472", {"start": v(-7.92, 13.03) * mm, "end": v(-7.91, 12.98) * mm});
            skLineSegment(sketch, "E1473", {"start": v(-7.91, 12.98) * mm, "end": v(-7.92, 12.94) * mm});
            skLineSegment(sketch, "E1474", {"start": v(-7.92, 12.94) * mm, "end": v(-7.92, 12.91) * mm});
            skLineSegment(sketch, "E1475", {"start": v(-7.92, 12.91) * mm, "end": v(-7.91, 12.86) * mm});
            skLineSegment(sketch, "E1476", {"start": v(-7.91, 12.86) * mm, "end": v(-7.92, 12.84) * mm});
            skLineSegment(sketch, "E1477", {"start": v(-7.92, 12.84) * mm, "end": v(-7.93, 12.79) * mm});
            skLineSegment(sketch, "E1478", {"start": v(-7.93, 12.79) * mm, "end": v(-7.94, 12.75) * mm});
            skLineSegment(sketch, "E1479", {"start": v(-7.94, 12.75) * mm, "end": v(-7.95, 12.71) * mm});
            skLineSegment(sketch, "E1480", {"start": v(-7.95, 12.71) * mm, "end": v(-7.97, 12.68) * mm});
            skLineSegment(sketch, "E1481", {"start": v(-7.97, 12.68) * mm, "end": v(-7.99, 12.65) * mm});
            skLineSegment(sketch, "E1482", {"start": v(-7.99, 12.65) * mm, "end": v(-8, 12.63) * mm});
            skLineSegment(sketch, "E1483", {"start": v(-8, 12.63) * mm, "end": v(-8.02, 12.62) * mm});
            skLineSegment(sketch, "E1484", {"start": v(-8.02, 12.62) * mm, "end": v(-8.02, 12.61) * mm});
            skLineSegment(sketch, "E1485", {"start": v(-8.02, 12.61) * mm, "end": v(-8.04, 12.6) * mm});
            skLineSegment(sketch, "E1486", {"start": v(-8.04, 12.6) * mm, "end": v(-8.05, 12.6) * mm});
            skLineSegment(sketch, "E1487", {"start": v(-8.05, 12.6) * mm, "end": v(-8.22, 12.53) * mm});
            skLineSegment(sketch, "E1488", {"start": v(-8.22, 12.53) * mm, "end": v(-8.4, 12.45) * mm});
            skLineSegment(sketch, "E1489", {"start": v(-8.4, 12.45) * mm, "end": v(-8.54, 12.4) * mm});
            skLineSegment(sketch, "E1490", {"start": v(-8.54, 12.4) * mm, "end": v(-8.73, 12.31) * mm});
            skLineSegment(sketch, "E1491", {"start": v(-8.73, 12.31) * mm, "end": v(-8.9, 12.24) * mm});
            skLineSegment(sketch, "E1492", {"start": v(-8.9, 12.24) * mm, "end": v(-8.9, 12.24) * mm});
            skLineSegment(sketch, "E1493", {"start": v(-8.9, 12.24) * mm, "end": v(-8.92, 12.24) * mm});
            skLineSegment(sketch, "E1494", {"start": v(-8.92, 12.24) * mm, "end": v(-8.93, 12.23) * mm});
            skLineSegment(sketch, "E1495", {"start": v(-8.93, 12.23) * mm, "end": v(-8.95, 12.23) * mm});
            skLineSegment(sketch, "E1496", {"start": v(-8.95, 12.23) * mm, "end": v(-8.96, 12.24) * mm});
            skLineSegment(sketch, "E1497", {"start": v(-8.96, 12.24) * mm, "end": v(-9, 12.24) * mm});
            skLineSegment(sketch, "E1498", {"start": v(-9, 12.24) * mm, "end": v(-9.02, 12.25) * mm});
            skLineSegment(sketch, "E1499", {"start": v(-9.02, 12.25) * mm, "end": v(-9.05, 12.26) * mm});
            skLineSegment(sketch, "E1500", {"start": v(-9.05, 12.26) * mm, "end": v(-9.06, 12.26) * mm});
            skLineSegment(sketch, "E1501", {"start": v(-9.06, 12.26) * mm, "end": v(-9.1, 12.3) * mm});
            skLineSegment(sketch, "E1502", {"start": v(-9.1, 12.3) * mm, "end": v(-9.11, 12.29) * mm});
            skLineSegment(sketch, "E1503", {"start": v(-9.11, 12.29) * mm, "end": v(-9.14, 12.33) * mm});
            skLineSegment(sketch, "E1504", {"start": v(-9.14, 12.33) * mm, "end": v(-9.16, 12.32) * mm});
            skLineSegment(sketch, "E1505", {"start": v(-9.16, 12.32) * mm, "end": v(-9.2, 12.37) * mm});
            skLineSegment(sketch, "E1506", {"start": v(-9.2, 12.37) * mm, "end": v(-9.2, 12.37) * mm});
            skLineSegment(sketch, "E1507", {"start": v(-9.2, 12.37) * mm, "end": v(-9.25, 12.42) * mm});
            skLineSegment(sketch, "E1508", {"start": v(-9.25, 12.42) * mm, "end": v(-9.26, 12.42) * mm});
            skLineSegment(sketch, "E1509", {"start": v(-9.26, 12.42) * mm, "end": v(-9.3, 12.48) * mm});
            skLineSegment(sketch, "E1510", {"start": v(-9.3, 12.48) * mm, "end": v(-9.31, 12.48) * mm});
            skLineSegment(sketch, "E1511", {"start": v(-9.31, 12.48) * mm, "end": v(-9.54, 12.81) * mm});
            skLineSegment(sketch, "E1512", {"start": v(-9.54, 12.81) * mm, "end": v(-9.58, 12.87) * mm});
            skLineSegment(sketch, "E1513", {"start": v(-9.58, 12.87) * mm, "end": v(-9.63, 12.94) * mm});
            skLineSegment(sketch, "E1514", {"start": v(-9.63, 12.94) * mm, "end": v(-9.68, 13.02) * mm});
            skLineSegment(sketch, "E1515", {"start": v(-9.68, 13.02) * mm, "end": v(-9.74, 13.1) * mm});
            skLineSegment(sketch, "E1516", {"start": v(-9.74, 13.1) * mm, "end": v(-9.8, 13.16) * mm});
            skLineSegment(sketch, "E1517", {"start": v(-9.8, 13.16) * mm, "end": v(-9.84, 13.22) * mm});
            skLineSegment(sketch, "E1518", {"start": v(-9.84, 13.22) * mm, "end": v(-9.9, 13.28) * mm});
            skLineSegment(sketch, "E1519", {"start": v(-9.9, 13.28) * mm, "end": v(-9.95, 13.34) * mm});
            skLineSegment(sketch, "E1520", {"start": v(-9.95, 13.34) * mm, "end": v(-10, 13.39) * mm});
            skLineSegment(sketch, "E1521", {"start": v(-10, 13.39) * mm, "end": v(-10.03, 13.42) * mm});
            skLineSegment(sketch, "E1522", {"start": v(-10.03, 13.42) * mm, "end": v(-10.07, 13.47) * mm});
            skLineSegment(sketch, "E1523", {"start": v(-10.07, 13.47) * mm, "end": v(-10.14, 13.54) * mm});
            skLineSegment(sketch, "E1524", {"start": v(-10.14, 13.54) * mm, "end": v(-10.2, 13.61) * mm});
            skLineSegment(sketch, "E1525", {"start": v(-10.2, 13.61) * mm, "end": v(-10.28, 13.69) * mm});
            skLineSegment(sketch, "E1526", {"start": v(-10.28, 13.69) * mm, "end": v(-10.36, 13.76) * mm});
            skLineSegment(sketch, "E1527", {"start": v(-10.36, 13.76) * mm, "end": v(-10.45, 13.84) * mm});
            skLineSegment(sketch, "E1528", {"start": v(-10.45, 13.84) * mm, "end": v(-10.53, 13.92) * mm});
            skLineSegment(sketch, "E1529", {"start": v(-10.53, 13.92) * mm, "end": v(-10.63, 14) * mm});
            skLineSegment(sketch, "E1530", {"start": v(-10.63, 14) * mm, "end": v(-10.73, 14.08) * mm});
            skLineSegment(sketch, "E1531", {"start": v(-10.73, 14.08) * mm, "end": v(-10.83, 14.17) * mm});
            skLineSegment(sketch, "E1532", {"start": v(-10.83, 14.17) * mm, "end": v(-10.94, 14.26) * mm});
            skLineSegment(sketch, "E1533", {"start": v(-10.94, 14.26) * mm, "end": v(-11.59, 14.76) * mm});
            skLineSegment(sketch, "E1534", {"start": v(-11.59, 14.76) * mm, "end": v(-11.83, 14.63) * mm});
            skLineSegment(sketch, "E1535", {"start": v(-11.83, 14.63) * mm, "end": v(-12.13, 14.47) * mm});
            skLineSegment(sketch, "E1536", {"start": v(-12.13, 14.47) * mm, "end": v(-12.42, 14.3) * mm});
            skLineSegment(sketch, "E1537", {"start": v(-12.42, 14.3) * mm, "end": v(-12.55, 14.23) * mm});
            skLineSegment(sketch, "E1538", {"start": v(-12.55, 14.23) * mm, "end": v(-12.47, 13.43) * mm});
            skLineSegment(sketch, "E1539", {"start": v(-12.47, 13.43) * mm, "end": v(-12.46, 13.3) * mm});
            skLineSegment(sketch, "E1540", {"start": v(-12.46, 13.3) * mm, "end": v(-12.44, 13.16) * mm});
            skLineSegment(sketch, "E1541", {"start": v(-12.44, 13.16) * mm, "end": v(-12.42, 13.03) * mm});
            skLineSegment(sketch, "E1542", {"start": v(-12.42, 13.03) * mm, "end": v(-12.4, 12.9) * mm});
            skLineSegment(sketch, "E1543", {"start": v(-12.4, 12.9) * mm, "end": v(-12.38, 12.8) * mm});
            skLineSegment(sketch, "E1544", {"start": v(-12.38, 12.8) * mm, "end": v(-12.36, 12.68) * mm});
            skLineSegment(sketch, "E1545", {"start": v(-12.36, 12.68) * mm, "end": v(-12.34, 12.57) * mm});
            skLineSegment(sketch, "E1546", {"start": v(-12.34, 12.57) * mm, "end": v(-12.32, 12.46) * mm});
            skLineSegment(sketch, "E1547", {"start": v(-12.32, 12.46) * mm, "end": v(-12.3, 12.36) * mm});
            skLineSegment(sketch, "E1548", {"start": v(-12.3, 12.36) * mm, "end": v(-12.27, 12.27) * mm});
            skLineSegment(sketch, "E1549", {"start": v(-12.27, 12.27) * mm, "end": v(-12.25, 12.2) * mm});
            skLineSegment(sketch, "E1550", {"start": v(-12.25, 12.2) * mm, "end": v(-12.24, 12.15) * mm});
            skLineSegment(sketch, "E1551", {"start": v(-12.24, 12.15) * mm, "end": v(-12.22, 12.09) * mm});
            skLineSegment(sketch, "E1552", {"start": v(-12.22, 12.09) * mm, "end": v(-12.2, 12.01) * mm});
            skLineSegment(sketch, "E1553", {"start": v(-12.2, 12.01) * mm, "end": v(-12.17, 11.94) * mm});
            skLineSegment(sketch, "E1554", {"start": v(-12.17, 11.94) * mm, "end": v(-12.15, 11.87) * mm});
            skLineSegment(sketch, "E1555", {"start": v(-12.15, 11.87) * mm, "end": v(-12.12, 11.8) * mm});
            skLineSegment(sketch, "E1556", {"start": v(-12.12, 11.8) * mm, "end": v(-12.1, 11.75) * mm});
            skLineSegment(sketch, "E1557", {"start": v(-12.1, 11.75) * mm, "end": v(-12.08, 11.7) * mm});
            skLineSegment(sketch, "E1558", {"start": v(-12.08, 11.7) * mm, "end": v(-12.06, 11.66) * mm});
            skLineSegment(sketch, "E1559", {"start": v(-12.06, 11.66) * mm, "end": v(-12.05, 11.62) * mm});
            skLineSegment(sketch, "E1560", {"start": v(-12.05, 11.62) * mm, "end": v(-12.03, 11.58) * mm});
            skLineSegment(sketch, "E1561", {"start": v(-12.03, 11.58) * mm, "end": v(-12.02, 11.56) * mm});
            skLineSegment(sketch, "E1562", {"start": v(-12.02, 11.56) * mm, "end": v(-11.86, 11.26) * mm});
            skLineSegment(sketch, "E1563", {"start": v(-11.86, 11.26) * mm, "end": v(-11.87, 11.26) * mm});
            skLineSegment(sketch, "E1564", {"start": v(-11.87, 11.26) * mm, "end": v(-11.83, 11.18) * mm});
            skLineSegment(sketch, "E1565", {"start": v(-11.83, 11.18) * mm, "end": v(-11.84, 11.17) * mm});
            skLineSegment(sketch, "E1566", {"start": v(-11.84, 11.17) * mm, "end": v(-11.8, 11.1) * mm});
            skLineSegment(sketch, "E1567", {"start": v(-11.8, 11.1) * mm, "end": v(-11.81, 11.1) * mm});
            skLineSegment(sketch, "E1568", {"start": v(-11.81, 11.1) * mm, "end": v(-11.78, 11.04) * mm});
            skLineSegment(sketch, "E1569", {"start": v(-11.78, 11.04) * mm, "end": v(-11.78, 11) * mm});
            skLineSegment(sketch, "E1570", {"start": v(-11.78, 11) * mm, "end": v(-11.78, 10.96) * mm});
            skLineSegment(sketch, "E1571", {"start": v(-11.78, 10.96) * mm, "end": v(-11.76, 10.91) * mm});
            skLineSegment(sketch, "E1572", {"start": v(-11.76, 10.91) * mm, "end": v(-11.77, 10.88) * mm});
            skLineSegment(sketch, "E1573", {"start": v(-11.77, 10.88) * mm, "end": v(-11.77, 10.84) * mm});
            skLineSegment(sketch, "E1574", {"start": v(-11.77, 10.84) * mm, "end": v(-11.76, 10.8) * mm});
            skLineSegment(sketch, "E1575", {"start": v(-11.76, 10.8) * mm, "end": v(-11.77, 10.78) * mm});
            skLineSegment(sketch, "E1576", {"start": v(-11.77, 10.78) * mm, "end": v(-11.78, 10.73) * mm});
            skLineSegment(sketch, "E1577", {"start": v(-11.78, 10.73) * mm, "end": v(-11.8, 10.7) * mm});
            skLineSegment(sketch, "E1578", {"start": v(-11.8, 10.7) * mm, "end": v(-11.8, 10.66) * mm});
            skLineSegment(sketch, "E1579", {"start": v(-11.8, 10.66) * mm, "end": v(-11.82, 10.65) * mm});
            skLineSegment(sketch, "E1580", {"start": v(-11.82, 10.65) * mm, "end": v(-11.82, 10.64) * mm});
            skLineSegment(sketch, "E1581", {"start": v(-11.82, 10.64) * mm, "end": v(-11.84, 10.62) * mm});
            skLineSegment(sketch, "E1582", {"start": v(-11.84, 10.62) * mm, "end": v(-11.85, 10.61) * mm});
            skLineSegment(sketch, "E1583", {"start": v(-11.85, 10.61) * mm, "end": v(-11.98, 10.52) * mm});
            skLineSegment(sketch, "E1584", {"start": v(-11.98, 10.52) * mm, "end": v(-12.16, 10.4) * mm});
            skLineSegment(sketch, "E1585", {"start": v(-12.16, 10.4) * mm, "end": v(-12.28, 10.3) * mm});
            skLineSegment(sketch, "E1586", {"start": v(-12.28, 10.3) * mm, "end": v(-12.45, 10.18) * mm});
            skLineSegment(sketch, "E1587", {"start": v(-12.45, 10.18) * mm, "end": v(-12.58, 10.09) * mm});
            skLineSegment(sketch, "E1588", {"start": v(-12.58, 10.09) * mm, "end": v(-12.58, 10.09) * mm});
            skLineSegment(sketch, "E1589", {"start": v(-12.58, 10.09) * mm, "end": v(-12.6, 10.07) * mm});
            skLineSegment(sketch, "E1590", {"start": v(-12.6, 10.07) * mm, "end": v(-12.62, 10.07) * mm});
            skLineSegment(sketch, "E1591", {"start": v(-12.62, 10.07) * mm, "end": v(-12.64, 10.06) * mm});
            skLineSegment(sketch, "E1592", {"start": v(-12.64, 10.06) * mm, "end": v(-12.65, 10.07) * mm});
            skLineSegment(sketch, "E1593", {"start": v(-12.65, 10.07) * mm, "end": v(-12.68, 10.06) * mm});
            skLineSegment(sketch, "E1594", {"start": v(-12.68, 10.06) * mm, "end": v(-12.7, 10.05) * mm});
            skLineSegment(sketch, "E1595", {"start": v(-12.7, 10.05) * mm, "end": v(-12.73, 10.06) * mm});
            skLineSegment(sketch, "E1596", {"start": v(-12.73, 10.06) * mm, "end": v(-12.77, 10.07) * mm});
            skLineSegment(sketch, "E1597", {"start": v(-12.77, 10.07) * mm, "end": v(-12.78, 10.06) * mm});
            skLineSegment(sketch, "E1598", {"start": v(-12.78, 10.06) * mm, "end": v(-12.8, 10.08) * mm});
            skLineSegment(sketch, "E1599", {"start": v(-12.8, 10.08) * mm, "end": v(-12.82, 10.08) * mm});
            skLineSegment(sketch, "E1600", {"start": v(-12.82, 10.08) * mm, "end": v(-12.85, 10.1) * mm});
            skLineSegment(sketch, "E1601", {"start": v(-12.85, 10.1) * mm, "end": v(-12.87, 10.1) * mm});
            skLineSegment(sketch, "E1602", {"start": v(-12.87, 10.1) * mm, "end": v(-12.9, 10.12) * mm});
            skLineSegment(sketch, "E1603", {"start": v(-12.9, 10.12) * mm, "end": v(-12.91, 10.12) * mm});
            skLineSegment(sketch, "E1604", {"start": v(-12.91, 10.12) * mm, "end": v(-12.95, 10.15) * mm});
            skLineSegment(sketch, "E1605", {"start": v(-12.95, 10.15) * mm, "end": v(-12.96, 10.14) * mm});
            skLineSegment(sketch, "E1606", {"start": v(-12.96, 10.14) * mm, "end": v(-13, 10.18) * mm});
            skLineSegment(sketch, "E1607", {"start": v(-13, 10.18) * mm, "end": v(-13, 10.17) * mm});
            skLineSegment(sketch, "E1608", {"start": v(-13, 10.17) * mm, "end": v(-13.05, 10.21) * mm});
            skLineSegment(sketch, "E1609", {"start": v(-13.05, 10.21) * mm, "end": v(-13.06, 10.2) * mm});
            skLineSegment(sketch, "E1610", {"start": v(-13.06, 10.2) * mm, "end": v(-13.1, 10.25) * mm});
            skLineSegment(sketch, "E1611", {"start": v(-13.1, 10.25) * mm, "end": v(-13.1, 10.25) * mm});
            skLineSegment(sketch, "E1612", {"start": v(-13.1, 10.25) * mm, "end": v(-13.37, 10.5) * mm});
            skLineSegment(sketch, "E1613", {"start": v(-13.37, 10.5) * mm, "end": v(-13.4, 10.54) * mm});
            skLineSegment(sketch, "E1614", {"start": v(-13.4, 10.54) * mm, "end": v(-13.44, 10.57) * mm});
            skLineSegment(sketch, "E1615", {"start": v(-13.44, 10.57) * mm, "end": v(-13.48, 10.6) * mm});
            skLineSegment(sketch, "E1616", {"start": v(-13.48, 10.6) * mm, "end": v(-13.52, 10.65) * mm});
            skLineSegment(sketch, "E1617", {"start": v(-13.52, 10.65) * mm, "end": v(-13.57, 10.69) * mm});
            skLineSegment(sketch, "E1618", {"start": v(-13.57, 10.69) * mm, "end": v(-13.62, 10.73) * mm});
            skLineSegment(sketch, "E1619", {"start": v(-13.62, 10.73) * mm, "end": v(-13.67, 10.77) * mm});
            skLineSegment(sketch, "E1620", {"start": v(-13.67, 10.77) * mm, "end": v(-13.73, 10.82) * mm});
            skLineSegment(sketch, "E1621", {"start": v(-13.73, 10.82) * mm, "end": v(-13.8, 10.86) * mm});
            skLineSegment(sketch, "E1622", {"start": v(-13.8, 10.86) * mm, "end": v(-13.86, 10.91) * mm});
            skLineSegment(sketch, "E1623", {"start": v(-13.86, 10.91) * mm, "end": v(-13.92, 10.95) * mm});
            skLineSegment(sketch, "E1624", {"start": v(-13.92, 10.95) * mm, "end": v(-13.95, 10.98) * mm});
            skLineSegment(sketch, "E1625", {"start": v(-13.95, 10.98) * mm, "end": v(-14.01, 11.02) * mm});
            skLineSegment(sketch, "E1626", {"start": v(-14.01, 11.02) * mm, "end": v(-14.1, 11.07) * mm});
            skLineSegment(sketch, "E1627", {"start": v(-14.1, 11.07) * mm, "end": v(-14.18, 11.12) * mm});
            skLineSegment(sketch, "E1628", {"start": v(-14.18, 11.12) * mm, "end": v(-14.28, 11.18) * mm});
            skLineSegment(sketch, "E1629", {"start": v(-14.28, 11.18) * mm, "end": v(-14.38, 11.24) * mm});
            skLineSegment(sketch, "E1630", {"start": v(-14.38, 11.24) * mm, "end": v(-14.48, 11.3) * mm});
            skLineSegment(sketch, "E1631", {"start": v(-14.48, 11.3) * mm, "end": v(-14.6, 11.35) * mm});
            skLineSegment(sketch, "E1632", {"start": v(-14.6, 11.35) * mm, "end": v(-14.71, 11.41) * mm});
            skLineSegment(sketch, "E1633", {"start": v(-14.71, 11.41) * mm, "end": v(-14.83, 11.47) * mm});
            skLineSegment(sketch, "E1634", {"start": v(-14.83, 11.47) * mm, "end": v(-14.96, 11.53) * mm});
            skLineSegment(sketch, "E1635", {"start": v(-14.96, 11.53) * mm, "end": v(-15.1, 11.6) * mm});
            skLineSegment(sketch, "E1636", {"start": v(-15.1, 11.6) * mm, "end": v(-15.8, 11.88) * mm});
            skLineSegment(sketch, "E1637", {"start": v(-15.8, 11.88) * mm, "end": v(-16.05, 11.66) * mm});
            skLineSegment(sketch, "E1638", {"start": v(-16.05, 11.66) * mm, "end": v(-16.31, 11.42) * mm});
            skLineSegment(sketch, "E1639", {"start": v(-16.31, 11.42) * mm, "end": v(-16.56, 11.18) * mm});
            skLineSegment(sketch, "E1640", {"start": v(-16.56, 11.18) * mm, "end": v(-16.58, 11.16) * mm});
            skLineSegment(sketch, "E1641", {"start": v(-16.58, 11.16) * mm, "end": v(-16.34, 10.44) * mm});
            skLineSegment(sketch, "E1642", {"start": v(-16.34, 10.44) * mm, "end": v(-16.3, 10.3) * mm});
            skLineSegment(sketch, "E1643", {"start": v(-16.3, 10.3) * mm, "end": v(-16.24, 10.17) * mm});
            skLineSegment(sketch, "E1644", {"start": v(-16.24, 10.17) * mm, "end": v(-16.19, 10.04) * mm});
            skLineSegment(sketch, "E1645", {"start": v(-16.19, 10.04) * mm, "end": v(-16.14, 9.92) * mm});
            skLineSegment(sketch, "E1646", {"start": v(-16.14, 9.92) * mm, "end": v(-16.09, 9.8) * mm});
            skLineSegment(sketch, "E1647", {"start": v(-16.09, 9.8) * mm, "end": v(-16.04, 9.7) * mm});
            skLineSegment(sketch, "E1648", {"start": v(-16.04, 9.7) * mm, "end": v(-15.99, 9.6) * mm});
            skLineSegment(sketch, "E1649", {"start": v(-15.99, 9.6) * mm, "end": v(-15.93, 9.5) * mm});
            skLineSegment(sketch, "E1650", {"start": v(-15.93, 9.5) * mm, "end": v(-15.89, 9.4) * mm});
            skLineSegment(sketch, "E1651", {"start": v(-15.89, 9.4) * mm, "end": v(-15.84, 9.31) * mm});
            skLineSegment(sketch, "E1652", {"start": v(-15.84, 9.31) * mm, "end": v(-15.8, 9.26) * mm});
            skLineSegment(sketch, "E1653", {"start": v(-15.8, 9.26) * mm, "end": v(-15.78, 9.22) * mm});
            skLineSegment(sketch, "E1654", {"start": v(-15.78, 9.22) * mm, "end": v(-15.75, 9.16) * mm});
            skLineSegment(sketch, "E1655", {"start": v(-15.75, 9.16) * mm, "end": v(-15.7, 9.1) * mm});
            skLineSegment(sketch, "E1656", {"start": v(-15.7, 9.1) * mm, "end": v(-15.66, 9.04) * mm});
            skLineSegment(sketch, "E1657", {"start": v(-15.66, 9.04) * mm, "end": v(-15.63, 8.98) * mm});
            skLineSegment(sketch, "E1658", {"start": v(-15.63, 8.98) * mm, "end": v(-15.6, 8.94) * mm});
            skLineSegment(sketch, "E1659", {"start": v(-15.6, 8.94) * mm, "end": v(-15.56, 8.9) * mm});
            skLineSegment(sketch, "E1660", {"start": v(-15.56, 8.9) * mm, "end": v(-15.53, 8.86) * mm});
            skLineSegment(sketch, "E1661", {"start": v(-15.53, 8.86) * mm, "end": v(-15.51, 8.84) * mm});
            skLineSegment(sketch, "E1662", {"start": v(-15.51, 8.84) * mm, "end": v(-15.5, 8.81) * mm});
            skLineSegment(sketch, "E1663", {"start": v(-15.5, 8.81) * mm, "end": v(-15.48, 8.8) * mm});
            skLineSegment(sketch, "E1664", {"start": v(-15.48, 8.8) * mm, "end": v(-15.47, 8.79) * mm});
            skLineSegment(sketch, "E1665", {"start": v(-15.47, 8.79) * mm, "end": v(-15.24, 8.56) * mm});
            skLineSegment(sketch, "E1666", {"start": v(-15.24, 8.56) * mm, "end": v(-15.24, 8.55) * mm});
            skLineSegment(sketch, "E1667", {"start": v(-15.24, 8.55) * mm, "end": v(-15.17, 8.48) * mm});
            skLineSegment(sketch, "E1668", {"start": v(-15.17, 8.48) * mm, "end": v(-15.18, 8.47) * mm});
            skLineSegment(sketch, "E1669", {"start": v(-15.18, 8.47) * mm, "end": v(-15.12, 8.4) * mm});
            skLineSegment(sketch, "E1670", {"start": v(-15.12, 8.4) * mm, "end": v(-15.12, 8.4) * mm});
            skLineSegment(sketch, "E1671", {"start": v(-15.12, 8.4) * mm, "end": v(-15.07, 8.34) * mm});
            skLineSegment(sketch, "E1672", {"start": v(-15.07, 8.34) * mm, "end": v(-15.08, 8.32) * mm});
            skLineSegment(sketch, "E1673", {"start": v(-15.08, 8.32) * mm, "end": v(-15.03, 8.27) * mm});
            skLineSegment(sketch, "E1674", {"start": v(-15.03, 8.27) * mm, "end": v(-15.04, 8.25) * mm});
            skLineSegment(sketch, "E1675", {"start": v(-15.04, 8.25) * mm, "end": v(-15, 8.2) * mm});
            skLineSegment(sketch, "E1676", {"start": v(-15, 8.2) * mm, "end": v(-15.01, 8.18) * mm});
            skLineSegment(sketch, "E1677", {"start": v(-15.01, 8.18) * mm, "end": v(-14.98, 8.14) * mm});
            skLineSegment(sketch, "E1678", {"start": v(-14.98, 8.14) * mm, "end": v(-14.99, 8.12) * mm});
            skLineSegment(sketch, "E1679", {"start": v(-14.99, 8.12) * mm, "end": v(-14.96, 8.08) * mm});
            skLineSegment(sketch, "E1680", {"start": v(-14.96, 8.08) * mm, "end": v(-14.96, 8.04) * mm});
            skLineSegment(sketch, "E1681", {"start": v(-14.96, 8.04) * mm, "end": v(-14.97, 8) * mm});
            skLineSegment(sketch, "E1682", {"start": v(-14.97, 8) * mm, "end": v(-14.96, 7.96) * mm});
            skLineSegment(sketch, "E1683", {"start": v(-14.96, 7.96) * mm, "end": v(-14.96, 7.92) * mm});
            skLineSegment(sketch, "E1684", {"start": v(-14.96, 7.92) * mm, "end": v(-14.97, 7.88) * mm});
            skLineSegment(sketch, "E1685", {"start": v(-14.97, 7.88) * mm, "end": v(-14.98, 7.87) * mm});
            skLineSegment(sketch, "E1686", {"start": v(-14.98, 7.87) * mm, "end": v(-15, 7.84) * mm});
            skLineSegment(sketch, "E1687", {"start": v(-15, 7.84) * mm, "end": v(-15, 7.82) * mm});
            skLineSegment(sketch, "E1688", {"start": v(-15, 7.82) * mm, "end": v(-15.1, 7.7) * mm});
            skLineSegment(sketch, "E1689", {"start": v(-15.1, 7.7) * mm, "end": v(-15.24, 7.55) * mm});
            skLineSegment(sketch, "E1690", {"start": v(-15.24, 7.55) * mm, "end": v(-15.33, 7.43) * mm});
            skLineSegment(sketch, "E1691", {"start": v(-15.33, 7.43) * mm, "end": v(-15.46, 7.26) * mm});
            skLineSegment(sketch, "E1692", {"start": v(-15.46, 7.26) * mm, "end": v(-15.55, 7.14) * mm});
            skLineSegment(sketch, "E1693", {"start": v(-15.55, 7.14) * mm, "end": v(-15.56, 7.14) * mm});
            skLineSegment(sketch, "E1694", {"start": v(-15.56, 7.14) * mm, "end": v(-15.58, 7.11) * mm});
            skLineSegment(sketch, "E1695", {"start": v(-15.58, 7.11) * mm, "end": v(-15.6, 7.1) * mm});
            skLineSegment(sketch, "E1696", {"start": v(-15.6, 7.1) * mm, "end": v(-15.62, 7.1) * mm});
            skLineSegment(sketch, "E1697", {"start": v(-15.62, 7.1) * mm, "end": v(-15.66, 7.08) * mm});
            skLineSegment(sketch, "E1698", {"start": v(-15.66, 7.08) * mm, "end": v(-15.69, 7.06) * mm});
            skLineSegment(sketch, "E1699", {"start": v(-15.69, 7.06) * mm, "end": v(-15.72, 7.07) * mm});
            skLineSegment(sketch, "E1700", {"start": v(-15.72, 7.07) * mm, "end": v(-15.75, 7.06) * mm});
            skLineSegment(sketch, "E1701", {"start": v(-15.75, 7.06) * mm, "end": v(-15.78, 7.05) * mm});
            skLineSegment(sketch, "E1702", {"start": v(-15.78, 7.05) * mm, "end": v(-15.82, 7.07) * mm});
            skLineSegment(sketch, "E1703", {"start": v(-15.82, 7.07) * mm, "end": v(-15.84, 7.05) * mm});
            skLineSegment(sketch, "E1704", {"start": v(-15.84, 7.05) * mm, "end": v(-15.88, 7.07) * mm});
            skLineSegment(sketch, "E1705", {"start": v(-15.88, 7.07) * mm, "end": v(-15.9, 7.06) * mm});
            skLineSegment(sketch, "E1706", {"start": v(-15.9, 7.06) * mm, "end": v(-15.94, 7.08) * mm});
            skLineSegment(sketch, "E1707", {"start": v(-15.94, 7.08) * mm, "end": v(-15.95, 7.07) * mm});
            skLineSegment(sketch, "E1708", {"start": v(-15.95, 7.07) * mm, "end": v(-16, 7.1) * mm});
            skLineSegment(sketch, "E1709", {"start": v(-16, 7.1) * mm, "end": v(-16.02, 7.1) * mm});
            skLineSegment(sketch, "E1710", {"start": v(-16.02, 7.1) * mm, "end": v(-16.07, 7.12) * mm});
            skLineSegment(sketch, "E1711", {"start": v(-16.07, 7.12) * mm, "end": v(-16.08, 7.12) * mm});
            skLineSegment(sketch, "E1712", {"start": v(-16.08, 7.12) * mm, "end": v(-16.14, 7.15) * mm});
            skLineSegment(sketch, "E1713", {"start": v(-16.14, 7.15) * mm, "end": v(-16.15, 7.14) * mm});
            skLineSegment(sketch, "E1714", {"start": v(-16.15, 7.14) * mm, "end": v(-16.22, 7.18) * mm});
            skLineSegment(sketch, "E1715", {"start": v(-16.22, 7.18) * mm, "end": v(-16.22, 7.18) * mm});
            skLineSegment(sketch, "E1716", {"start": v(-16.22, 7.18) * mm, "end": v(-16.5, 7.35) * mm});
            skLineSegment(sketch, "E1717", {"start": v(-16.5, 7.35) * mm, "end": v(-16.54, 7.37) * mm});
            skLineSegment(sketch, "E1718", {"start": v(-16.54, 7.37) * mm, "end": v(-16.57, 7.4) * mm});
            skLineSegment(sketch, "E1719", {"start": v(-16.57, 7.4) * mm, "end": v(-16.61, 7.41) * mm});
            skLineSegment(sketch, "E1720", {"start": v(-16.61, 7.41) * mm, "end": v(-16.65, 7.43) * mm});
            skLineSegment(sketch, "E1721", {"start": v(-16.65, 7.43) * mm, "end": v(-16.7, 7.46) * mm});
            skLineSegment(sketch, "E1722", {"start": v(-16.7, 7.46) * mm, "end": v(-16.75, 7.48) * mm});
            skLineSegment(sketch, "E1723", {"start": v(-16.75, 7.48) * mm, "end": v(-16.81, 7.5) * mm});
            skLineSegment(sketch, "E1724", {"start": v(-16.81, 7.5) * mm, "end": v(-16.88, 7.53) * mm});
            skLineSegment(sketch, "E1725", {"start": v(-16.88, 7.53) * mm, "end": v(-16.94, 7.56) * mm});
            skLineSegment(sketch, "E1726", {"start": v(-16.94, 7.56) * mm, "end": v(-17.02, 7.6) * mm});
            skLineSegment(sketch, "E1727", {"start": v(-17.02, 7.6) * mm, "end": v(-17.08, 7.61) * mm});
            skLineSegment(sketch, "E1728", {"start": v(-17.08, 7.61) * mm, "end": v(-17.12, 7.63) * mm});
            skLineSegment(sketch, "E1729", {"start": v(-17.12, 7.63) * mm, "end": v(-17.19, 7.65) * mm});
            skLineSegment(sketch, "E1730", {"start": v(-17.19, 7.65) * mm, "end": v(-17.28, 7.68) * mm});
            skLineSegment(sketch, "E1731", {"start": v(-17.28, 7.68) * mm, "end": v(-17.38, 7.7) * mm});
            skLineSegment(sketch, "E1732", {"start": v(-17.38, 7.7) * mm, "end": v(-17.49, 7.73) * mm});
            skLineSegment(sketch, "E1733", {"start": v(-17.49, 7.73) * mm, "end": v(-17.6, 7.76) * mm});
            skLineSegment(sketch, "E1734", {"start": v(-17.6, 7.76) * mm, "end": v(-17.72, 7.79) * mm});
            skLineSegment(sketch, "E1735", {"start": v(-17.72, 7.79) * mm, "end": v(-17.85, 7.81) * mm});
            skLineSegment(sketch, "E1736", {"start": v(-17.85, 7.81) * mm, "end": v(-17.98, 7.84) * mm});
            skLineSegment(sketch, "E1737", {"start": v(-17.98, 7.84) * mm, "end": v(-18.12, 7.86) * mm});
            skLineSegment(sketch, "E1738", {"start": v(-18.12, 7.86) * mm, "end": v(-18.27, 7.88) * mm});
            skLineSegment(sketch, "E1739", {"start": v(-18.27, 7.88) * mm, "end": v(-18.43, 7.9) * mm});
            skLineSegment(sketch, "E1740", {"start": v(-18.43, 7.9) * mm, "end": v(-19.16, 7.95) * mm});
            skLineSegment(sketch, "E1741", {"start": v(-19.16, 7.95) * mm, "end": v(-19.22, 7.86) * mm});
            skLineSegment(sketch, "E1742", {"start": v(-19.22, 7.86) * mm, "end": v(-19.4, 7.55) * mm});
            skLineSegment(sketch, "E1743", {"start": v(-19.4, 7.55) * mm, "end": v(-19.58, 7.24) * mm});
            skLineSegment(sketch, "E1744", {"start": v(-19.58, 7.24) * mm, "end": v(-19.68, 7.06) * mm});
            skLineSegment(sketch, "E1745", {"start": v(-19.68, 7.06) * mm, "end": v(-19.26, 6.45) * mm});
            skLineSegment(sketch, "E1746", {"start": v(-19.26, 6.45) * mm, "end": v(-19.17, 6.32) * mm});
            skLineSegment(sketch, "E1747", {"start": v(-19.17, 6.32) * mm, "end": v(-19.08, 6.2) * mm});
            skLineSegment(sketch, "E1748", {"start": v(-19.08, 6.2) * mm, "end": v(-18.99, 6.1) * mm});
            skLineSegment(sketch, "E1749", {"start": v(-18.99, 6.1) * mm, "end": v(-18.9, 5.98) * mm});
            skLineSegment(sketch, "E1750", {"start": v(-18.9, 5.98) * mm, "end": v(-18.82, 5.89) * mm});
            skLineSegment(sketch, "E1751", {"start": v(-18.82, 5.89) * mm, "end": v(-18.74, 5.8) * mm});
            skLineSegment(sketch, "E1752", {"start": v(-18.74, 5.8) * mm, "end": v(-18.65, 5.71) * mm});
            skLineSegment(sketch, "E1753", {"start": v(-18.65, 5.71) * mm, "end": v(-18.58, 5.64) * mm});
            skLineSegment(sketch, "E1754", {"start": v(-18.58, 5.64) * mm, "end": v(-18.5, 5.56) * mm});
            skLineSegment(sketch, "E1755", {"start": v(-18.5, 5.56) * mm, "end": v(-18.43, 5.5) * mm});
            skLineSegment(sketch, "E1756", {"start": v(-18.43, 5.5) * mm, "end": v(-18.39, 5.46) * mm});
            skLineSegment(sketch, "E1757", {"start": v(-18.39, 5.46) * mm, "end": v(-18.35, 5.43) * mm});
            skLineSegment(sketch, "E1758", {"start": v(-18.35, 5.43) * mm, "end": v(-18.3, 5.4) * mm});
            skLineSegment(sketch, "E1759", {"start": v(-18.3, 5.4) * mm, "end": v(-18.25, 5.34) * mm});
            skLineSegment(sketch, "E1760", {"start": v(-18.25, 5.34) * mm, "end": v(-18.2, 5.3) * mm});
            skLineSegment(sketch, "E1761", {"start": v(-18.2, 5.3) * mm, "end": v(-18.15, 5.27) * mm});
            skLineSegment(sketch, "E1762", {"start": v(-18.15, 5.27) * mm, "end": v(-18.11, 5.24) * mm});
            skLineSegment(sketch, "E1763", {"start": v(-18.11, 5.24) * mm, "end": v(-18.08, 5.22) * mm});
            skLineSegment(sketch, "E1764", {"start": v(-18.08, 5.22) * mm, "end": v(-18.05, 5.2) * mm});
            skLineSegment(sketch, "E1765", {"start": v(-18.05, 5.2) * mm, "end": v(-18.02, 5.19) * mm});
            skLineSegment(sketch, "E1766", {"start": v(-18.02, 5.19) * mm, "end": v(-18, 5.18) * mm});
            skLineSegment(sketch, "E1767", {"start": v(-18, 5.18) * mm, "end": v(-18, 5.17) * mm});
            skLineSegment(sketch, "E1768", {"start": v(-18, 5.17) * mm, "end": v(-17.7, 5.04) * mm});
            skLineSegment(sketch, "E1769", {"start": v(-17.7, 5.04) * mm, "end": v(-17.7, 5.03) * mm});
            skLineSegment(sketch, "E1770", {"start": v(-17.7, 5.03) * mm, "end": v(-17.6, 4.98) * mm});
            skLineSegment(sketch, "E1771", {"start": v(-17.6, 4.98) * mm, "end": v(-17.6, 4.97) * mm});
            skLineSegment(sketch, "E1772", {"start": v(-17.6, 4.97) * mm, "end": v(-17.51, 4.92) * mm});
            skLineSegment(sketch, "E1773", {"start": v(-17.51, 4.92) * mm, "end": v(-17.52, 4.9) * mm});
            skLineSegment(sketch, "E1774", {"start": v(-17.52, 4.9) * mm, "end": v(-17.44, 4.87) * mm});
            skLineSegment(sketch, "E1775", {"start": v(-17.44, 4.87) * mm, "end": v(-17.44, 4.85) * mm});
            skLineSegment(sketch, "E1776", {"start": v(-17.44, 4.85) * mm, "end": v(-17.37, 4.8) * mm});
            skLineSegment(sketch, "E1777", {"start": v(-17.37, 4.8) * mm, "end": v(-17.37, 4.79) * mm});
            skLineSegment(sketch, "E1778", {"start": v(-17.37, 4.79) * mm, "end": v(-17.31, 4.75) * mm});
            skLineSegment(sketch, "E1779", {"start": v(-17.31, 4.75) * mm, "end": v(-17.32, 4.73) * mm});
            skLineSegment(sketch, "E1780", {"start": v(-17.32, 4.73) * mm, "end": v(-17.27, 4.7) * mm});
            skLineSegment(sketch, "E1781", {"start": v(-17.27, 4.7) * mm, "end": v(-17.27, 4.67) * mm});
            skLineSegment(sketch, "E1782", {"start": v(-17.27, 4.67) * mm, "end": v(-17.23, 4.64) * mm});
            skLineSegment(sketch, "E1783", {"start": v(-17.23, 4.64) * mm, "end": v(-17.23, 4.6) * mm});
            skLineSegment(sketch, "E1784", {"start": v(-17.23, 4.6) * mm, "end": v(-17.2, 4.58) * mm});
            skLineSegment(sketch, "E1785", {"start": v(-17.2, 4.58) * mm, "end": v(-17.2, 4.55) * mm});
            skLineSegment(sketch, "E1786", {"start": v(-17.2, 4.55) * mm, "end": v(-17.18, 4.53) * mm});
            skLineSegment(sketch, "E1787", {"start": v(-17.18, 4.53) * mm, "end": v(-17.19, 4.5) * mm});
            skLineSegment(sketch, "E1788", {"start": v(-17.19, 4.5) * mm, "end": v(-17.17, 4.46) * mm});
            skLineSegment(sketch, "E1789", {"start": v(-17.17, 4.46) * mm, "end": v(-17.16, 4.42) * mm});
            skLineSegment(sketch, "E1790", {"start": v(-17.16, 4.42) * mm, "end": v(-17.17, 4.4) * mm});
            skLineSegment(sketch, "E1791", {"start": v(-17.17, 4.4) * mm, "end": v(-17.17, 4.36) * mm});
            skLineSegment(sketch, "E1792", {"start": v(-17.17, 4.36) * mm, "end": v(-17.18, 4.34) * mm});
            skLineSegment(sketch, "E1793", {"start": v(-17.18, 4.34) * mm, "end": v(-17.24, 4.2) * mm});
            skLineSegment(sketch, "E1794", {"start": v(-17.24, 4.2) * mm, "end": v(-17.31, 4) * mm});
            skLineSegment(sketch, "E1795", {"start": v(-17.31, 4) * mm, "end": v(-17.36, 3.87) * mm});
            skLineSegment(sketch, "E1796", {"start": v(-17.36, 3.87) * mm, "end": v(-17.43, 3.68) * mm});
            skLineSegment(sketch, "E1797", {"start": v(-17.43, 3.68) * mm, "end": v(-17.48, 3.54) * mm});
            skLineSegment(sketch, "E1798", {"start": v(-17.48, 3.54) * mm, "end": v(-17.5, 3.52) * mm});
            skLineSegment(sketch, "E1799", {"start": v(-17.5, 3.52) * mm, "end": v(-17.5, 3.5) * mm});
            skLineSegment(sketch, "E1800", {"start": v(-17.5, 3.5) * mm, "end": v(-17.51, 3.48) * mm});
            skLineSegment(sketch, "E1801", {"start": v(-17.51, 3.48) * mm, "end": v(-17.54, 3.46) * mm});
            skLineSegment(sketch, "E1802", {"start": v(-17.54, 3.46) * mm, "end": v(-17.56, 3.43) * mm});
            skLineSegment(sketch, "E1803", {"start": v(-17.56, 3.43) * mm, "end": v(-17.59, 3.43) * mm});
            skLineSegment(sketch, "E1804", {"start": v(-17.59, 3.43) * mm, "end": v(-17.6, 3.4) * mm});
            skLineSegment(sketch, "E1805", {"start": v(-17.6, 3.4) * mm, "end": v(-17.64, 3.4) * mm});
            skLineSegment(sketch, "E1806", {"start": v(-17.64, 3.4) * mm, "end": v(-17.65, 3.37) * mm});
            skLineSegment(sketch, "E1807", {"start": v(-17.65, 3.37) * mm, "end": v(-17.7, 3.38) * mm});
            skLineSegment(sketch, "E1808", {"start": v(-17.7, 3.38) * mm, "end": v(-17.7, 3.35) * mm});
            skLineSegment(sketch, "E1809", {"start": v(-17.7, 3.35) * mm, "end": v(-17.75, 3.36) * mm});
            skLineSegment(sketch, "E1810", {"start": v(-17.75, 3.36) * mm, "end": v(-17.77, 3.34) * mm});
            skLineSegment(sketch, "E1811", {"start": v(-17.77, 3.34) * mm, "end": v(-17.82, 3.34) * mm});
            skLineSegment(sketch, "E1812", {"start": v(-17.82, 3.34) * mm, "end": v(-17.83, 3.32) * mm});
            skLineSegment(sketch, "E1813", {"start": v(-17.83, 3.32) * mm, "end": v(-17.9, 3.34) * mm});
            skLineSegment(sketch, "E1814", {"start": v(-17.9, 3.34) * mm, "end": v(-17.9, 3.32) * mm});
            skLineSegment(sketch, "E1815", {"start": v(-17.9, 3.32) * mm, "end": v(-17.98, 3.33) * mm});
            skLineSegment(sketch, "E1816", {"start": v(-17.98, 3.33) * mm, "end": v(-17.98, 3.32) * mm});
            skLineSegment(sketch, "E1817", {"start": v(-17.98, 3.32) * mm, "end": v(-18.06, 3.33) * mm});
            skLineSegment(sketch, "E1818", {"start": v(-18.06, 3.33) * mm, "end": v(-18.07, 3.32) * mm});
            skLineSegment(sketch, "E1819", {"start": v(-18.07, 3.32) * mm, "end": v(-18.15, 3.34) * mm});
            skLineSegment(sketch, "E1820", {"start": v(-18.15, 3.34) * mm, "end": v(-18.16, 3.33) * mm});
            skLineSegment(sketch, "E1821", {"start": v(-18.16, 3.33) * mm, "end": v(-18.24, 3.36) * mm});
            skLineSegment(sketch, "E1822", {"start": v(-18.24, 3.36) * mm, "end": v(-18.25, 3.35) * mm});
            skLineSegment(sketch, "E1823", {"start": v(-18.25, 3.35) * mm, "end": v(-18.57, 3.44) * mm});
            skLineSegment(sketch, "E1824", {"start": v(-18.57, 3.44) * mm, "end": v(-18.58, 3.44) * mm});
            skLineSegment(sketch, "E1825", {"start": v(-18.58, 3.44) * mm, "end": v(-18.61, 3.45) * mm});
            skLineSegment(sketch, "E1826", {"start": v(-18.61, 3.45) * mm, "end": v(-18.64, 3.45) * mm});
            skLineSegment(sketch, "E1827", {"start": v(-18.64, 3.45) * mm, "end": v(-18.68, 3.46) * mm});
            skLineSegment(sketch, "E1828", {"start": v(-18.68, 3.46) * mm, "end": v(-18.72, 3.47) * mm});
            skLineSegment(sketch, "E1829", {"start": v(-18.72, 3.47) * mm, "end": v(-18.77, 3.47) * mm});
            skLineSegment(sketch, "E1830", {"start": v(-18.77, 3.47) * mm, "end": v(-18.82, 3.48) * mm});
            skLineSegment(sketch, "E1831", {"start": v(-18.82, 3.48) * mm, "end": v(-18.88, 3.49) * mm});
            skLineSegment(sketch, "E1832", {"start": v(-18.88, 3.49) * mm, "end": v(-18.95, 3.5) * mm});
            skLineSegment(sketch, "E1833", {"start": v(-18.95, 3.5) * mm, "end": v(-19.02, 3.5) * mm});
            skLineSegment(sketch, "E1834", {"start": v(-19.02, 3.5) * mm, "end": v(-19.08, 3.5) * mm});
            skLineSegment(sketch, "E1835", {"start": v(-19.08, 3.5) * mm, "end": v(-19.13, 3.5) * mm});
            skLineSegment(sketch, "E1836", {"start": v(-19.13, 3.5) * mm, "end": v(-19.19, 3.5) * mm});
            skLineSegment(sketch, "E1837", {"start": v(-19.19, 3.5) * mm, "end": v(-19.29, 3.5) * mm});
            skLineSegment(sketch, "E1838", {"start": v(-19.29, 3.5) * mm, "end": v(-19.39, 3.49) * mm});
            skLineSegment(sketch, "E1839", {"start": v(-19.39, 3.49) * mm, "end": v(-19.5, 3.48) * mm});
            skLineSegment(sketch, "E1840", {"start": v(-19.5, 3.48) * mm, "end": v(-19.6, 3.47) * mm});
            skLineSegment(sketch, "E1841", {"start": v(-19.6, 3.47) * mm, "end": v(-19.73, 3.46) * mm});
            skLineSegment(sketch, "E1842", {"start": v(-19.73, 3.46) * mm, "end": v(-19.86, 3.44) * mm});
            skLineSegment(sketch, "E1843", {"start": v(-19.86, 3.44) * mm, "end": v(-20, 3.41) * mm});
            skLineSegment(sketch, "E1844", {"start": v(-20, 3.41) * mm, "end": v(-20.14, 3.39) * mm});
            skLineSegment(sketch, "E1845", {"start": v(-20.14, 3.39) * mm, "end": v(-20.28, 3.35) * mm});
            skLineSegment(sketch, "E1846", {"start": v(-20.28, 3.35) * mm, "end": v(-20.44, 3.31) * mm});
            skLineSegment(sketch, "E1847", {"start": v(-20.44, 3.31) * mm, "end": v(-21.16, 3.12) * mm});
            skLineSegment(sketch, "E1848", {"start": v(-21.16, 3.12) * mm, "end": v(-21.2, 2.9) * mm});
            skLineSegment(sketch, "E1849", {"start": v(-21.2, 2.9) * mm, "end": v(-21.27, 2.55) * mm});
            skLineSegment(sketch, "E1850", {"start": v(-21.27, 2.55) * mm, "end": v(-21.33, 2.2) * mm});
            skLineSegment(sketch, "E1851", {"start": v(-21.33, 2.2) * mm, "end": v(-21.34, 2.12) * mm});
            skLineSegment(sketch, "E1852", {"start": v(-21.34, 2.12) * mm, "end": v(-20.74, 1.68) * mm});
            skLineSegment(sketch, "E1853", {"start": v(-20.74, 1.68) * mm, "end": v(-20.6, 1.58) * mm});
            skLineSegment(sketch, "E1854", {"start": v(-20.6, 1.58) * mm, "end": v(-20.48, 1.5) * mm});
            skLineSegment(sketch, "E1855", {"start": v(-20.48, 1.5) * mm, "end": v(-20.36, 1.42) * mm});
            skLineSegment(sketch, "E1856", {"start": v(-20.36, 1.42) * mm, "end": v(-20.24, 1.35) * mm});
            skLineSegment(sketch, "E1857", {"start": v(-20.24, 1.35) * mm, "end": v(-20.13, 1.3) * mm});
            skLineSegment(sketch, "E1858", {"start": v(-20.13, 1.3) * mm, "end": v(-20.02, 1.23) * mm});
            skLineSegment(sketch, "E1859", {"start": v(-20.02, 1.23) * mm, "end": v(-19.92, 1.18) * mm});
            skLineSegment(sketch, "E1860", {"start": v(-19.92, 1.18) * mm, "end": v(-19.82, 1.14) * mm});
            skLineSegment(sketch, "E1861", {"start": v(-19.82, 1.14) * mm, "end": v(-19.73, 1.1) * mm});
            skLineSegment(sketch, "E1862", {"start": v(-19.73, 1.1) * mm, "end": v(-19.64, 1.06) * mm});
            skLineSegment(sketch, "E1863", {"start": v(-19.64, 1.06) * mm, "end": v(-19.58, 1.04) * mm});
            skLineSegment(sketch, "E1864", {"start": v(-19.58, 1.04) * mm, "end": v(-19.54, 1.02) * mm});
            skLineSegment(sketch, "E1865", {"start": v(-19.54, 1.02) * mm, "end": v(-19.49, 1) * mm});
            skLineSegment(sketch, "E1866", {"start": v(-19.49, 1) * mm, "end": v(-19.42, 0.98) * mm});
            skLineSegment(sketch, "E1867", {"start": v(-19.42, 0.98) * mm, "end": v(-19.36, 0.97) * mm});
            skLineSegment(sketch, "E1868", {"start": v(-19.36, 0.97) * mm, "end": v(-19.3, 0.95) * mm});
            skLineSegment(sketch, "E1869", {"start": v(-19.3, 0.95) * mm, "end": v(-19.26, 0.94) * mm});
            skLineSegment(sketch, "E1870", {"start": v(-19.26, 0.94) * mm, "end": v(-19.22, 0.93) * mm});
            skLineSegment(sketch, "E1871", {"start": v(-19.22, 0.93) * mm, "end": v(-19.19, 0.93) * mm});
            skLineSegment(sketch, "E1872", {"start": v(-19.19, 0.93) * mm, "end": v(-19.16, 0.92) * mm});
            skLineSegment(sketch, "E1873", {"start": v(-19.16, 0.92) * mm, "end": v(-19.14, 0.92) * mm});
            skLineSegment(sketch, "E1874", {"start": v(-19.14, 0.92) * mm, "end": v(-19.13, 0.92) * mm});
            skLineSegment(sketch, "E1875", {"start": v(-19.13, 0.92) * mm, "end": v(-19.12, 0.92) * mm});
            skLineSegment(sketch, "E1876", {"start": v(-19.12, 0.92) * mm, "end": v(-18.79, 0.9) * mm});
            skLineSegment(sketch, "E1877", {"start": v(-18.79, 0.9) * mm, "end": v(-18.78, 0.89) * mm});
            skLineSegment(sketch, "E1878", {"start": v(-18.78, 0.89) * mm, "end": v(-18.68, 0.88) * mm});
            skLineSegment(sketch, "E1879", {"start": v(-18.68, 0.88) * mm, "end": v(-18.68, 0.87) * mm});
            skLineSegment(sketch, "E1880", {"start": v(-18.68, 0.87) * mm, "end": v(-18.58, 0.86) * mm});
            skLineSegment(sketch, "E1881", {"start": v(-18.58, 0.86) * mm, "end": v(-18.58, 0.84) * mm});
            skLineSegment(sketch, "E1882", {"start": v(-18.58, 0.84) * mm, "end": v(-18.5, 0.83) * mm});
            skLineSegment(sketch, "E1883", {"start": v(-18.5, 0.83) * mm, "end": v(-18.49, 0.81) * mm});
            skLineSegment(sketch, "E1884", {"start": v(-18.49, 0.81) * mm, "end": v(-18.4, 0.8) * mm});
            skLineSegment(sketch, "E1885", {"start": v(-18.4, 0.8) * mm, "end": v(-18.4, 0.78) * mm});
            skLineSegment(sketch, "E1886", {"start": v(-18.4, 0.78) * mm, "end": v(-18.34, 0.77) * mm});
            skLineSegment(sketch, "E1887", {"start": v(-18.34, 0.77) * mm, "end": v(-18.33, 0.74) * mm});
            skLineSegment(sketch, "E1888", {"start": v(-18.33, 0.74) * mm, "end": v(-18.27, 0.73) * mm});
            skLineSegment(sketch, "E1889", {"start": v(-18.27, 0.73) * mm, "end": v(-18.27, 0.7) * mm});
            skLineSegment(sketch, "E1890", {"start": v(-18.27, 0.7) * mm, "end": v(-18.21, 0.69) * mm});
            skLineSegment(sketch, "E1891", {"start": v(-18.21, 0.69) * mm, "end": v(-18.2, 0.66) * mm});
            skLineSegment(sketch, "E1892", {"start": v(-18.2, 0.66) * mm, "end": v(-18.16, 0.65) * mm});
            skLineSegment(sketch, "E1893", {"start": v(-18.16, 0.65) * mm, "end": v(-18.16, 0.61) * mm});
            skLineSegment(sketch, "E1894", {"start": v(-18.16, 0.61) * mm, "end": v(-18.12, 0.6) * mm});
            skLineSegment(sketch, "E1895", {"start": v(-18.12, 0.6) * mm, "end": v(-18.12, 0.57) * mm});
            skLineSegment(sketch, "E1896", {"start": v(-18.12, 0.57) * mm, "end": v(-18.1, 0.54) * mm});
            skLineSegment(sketch, "E1897", {"start": v(-18.1, 0.54) * mm, "end": v(-18.07, 0.5) * mm});
            skLineSegment(sketch, "E1898", {"start": v(-18.07, 0.5) * mm, "end": v(-18.06, 0.48) * mm});
            skLineSegment(sketch, "E1899", {"start": v(-18.06, 0.48) * mm, "end": v(-18.06, 0.44) * mm});
            skLineSegment(sketch, "E1900", {"start": v(-18.06, 0.44) * mm, "end": v(-18.06, 0.42) * mm});
            skLineSegment(sketch, "E1901", {"start": v(-18.06, 0.42) * mm, "end": v(-18.06, 0.26) * mm});
            skLineSegment(sketch, "E1902", {"start": v(-18.06, 0.26) * mm, "end": v(-18.06, 0.06) * mm});
            skLineSegment(sketch, "E1903", {"start": v(-18.06, 0.06) * mm, "end": v(-18.06, -0.08) * mm});
            skLineSegment(sketch, "E1904", {"start": v(-18.06, -0.08) * mm, "end": v(-18.06, -0.28) * mm});
            skLineSegment(sketch, "E1905", {"start": v(-18.06, -0.28) * mm, "end": v(-18.06, -0.43) * mm});
            skLineSegment(sketch, "E1906", {"start": v(-18.06, -0.43) * mm, "end": v(-18.06, -0.46) * mm});
            skLineSegment(sketch, "E1907", {"start": v(-18.06, -0.46) * mm, "end": v(-18.06, -0.48) * mm});
            skLineSegment(sketch, "E1908", {"start": v(-18.06, -0.48) * mm, "end": v(-18.07, -0.5) * mm});
            skLineSegment(sketch, "E1909", {"start": v(-18.07, -0.5) * mm, "end": v(-18.08, -0.53) * mm});
            skLineSegment(sketch, "E1910", {"start": v(-18.08, -0.53) * mm, "end": v(-18.1, -0.57) * mm});
            skLineSegment(sketch, "E1911", {"start": v(-18.1, -0.57) * mm, "end": v(-18.12, -0.58) * mm});
            skLineSegment(sketch, "E1912", {"start": v(-18.12, -0.58) * mm, "end": v(-18.12, -0.62) * mm});
            skLineSegment(sketch, "E1913", {"start": v(-18.12, -0.62) * mm, "end": v(-18.16, -0.63) * mm});
            skLineSegment(sketch, "E1914", {"start": v(-18.16, -0.63) * mm, "end": v(-18.16, -0.66) * mm});
            skLineSegment(sketch, "E1915", {"start": v(-18.16, -0.66) * mm, "end": v(-18.2, -0.67) * mm});
            skLineSegment(sketch, "E1916", {"start": v(-18.2, -0.67) * mm, "end": v(-18.21, -0.7) * mm});
            skLineSegment(sketch, "E1917", {"start": v(-18.21, -0.7) * mm, "end": v(-18.26, -0.72) * mm});
            skLineSegment(sketch, "E1918", {"start": v(-18.26, -0.72) * mm, "end": v(-18.27, -0.74) * mm});
            skLineSegment(sketch, "E1919", {"start": v(-18.27, -0.74) * mm, "end": v(-18.33, -0.76) * mm});
            skLineSegment(sketch, "E1920", {"start": v(-18.33, -0.76) * mm, "end": v(-18.33, -0.78) * mm});
            skLineSegment(sketch, "E1921", {"start": v(-18.33, -0.78) * mm, "end": v(-18.4, -0.8) * mm});
            skLineSegment(sketch, "E1922", {"start": v(-18.4, -0.8) * mm, "end": v(-18.4, -0.81) * mm});
            skLineSegment(sketch, "E1923", {"start": v(-18.4, -0.81) * mm, "end": v(-18.49, -0.83) * mm});
            skLineSegment(sketch, "E1924", {"start": v(-18.49, -0.83) * mm, "end": v(-18.5, -0.84) * mm});
            skLineSegment(sketch, "E1925", {"start": v(-18.5, -0.84) * mm, "end": v(-18.58, -0.86) * mm});
            skLineSegment(sketch, "E1926", {"start": v(-18.58, -0.86) * mm, "end": v(-18.58, -0.87) * mm});
            skLineSegment(sketch, "E1927", {"start": v(-18.58, -0.87) * mm, "end": v(-18.68, -0.88) * mm});
            skLineSegment(sketch, "E1928", {"start": v(-18.68, -0.88) * mm, "end": v(-18.68, -0.9) * mm});
            skLineSegment(sketch, "E1929", {"start": v(-18.68, -0.9) * mm, "end": v(-18.78, -0.9) * mm});
            skLineSegment(sketch, "E1930", {"start": v(-18.78, -0.9) * mm, "end": v(-18.78, -0.91) * mm});
            skLineSegment(sketch, "E1931", {"start": v(-18.78, -0.91) * mm, "end": v(-19.12, -0.93) * mm});
            skLineSegment(sketch, "E1932", {"start": v(-19.12, -0.93) * mm, "end": v(-19.13, -0.93) * mm});
            skLineSegment(sketch, "E1933", {"start": v(-19.13, -0.93) * mm, "end": v(-19.14, -0.94) * mm});
            skLineSegment(sketch, "E1934", {"start": v(-19.14, -0.94) * mm, "end": v(-19.16, -0.94) * mm});
            skLineSegment(sketch, "E1935", {"start": v(-19.16, -0.94) * mm, "end": v(-19.19, -0.94) * mm});
            skLineSegment(sketch, "E1936", {"start": v(-19.19, -0.94) * mm, "end": v(-19.22, -0.95) * mm});
            skLineSegment(sketch, "E1937", {"start": v(-19.22, -0.95) * mm, "end": v(-19.26, -0.96) * mm});
            skLineSegment(sketch, "E1938", {"start": v(-19.26, -0.96) * mm, "end": v(-19.3, -0.97) * mm});
            skLineSegment(sketch, "E1939", {"start": v(-19.3, -0.97) * mm, "end": v(-19.36, -0.98) * mm});
            skLineSegment(sketch, "E1940", {"start": v(-19.36, -0.98) * mm, "end": v(-19.42, -1) * mm});
            skLineSegment(sketch, "E1941", {"start": v(-19.42, -1) * mm, "end": v(-19.49, -1.02) * mm});
            skLineSegment(sketch, "E1942", {"start": v(-19.49, -1.02) * mm, "end": v(-19.54, -1.04) * mm});
            skLineSegment(sketch, "E1943", {"start": v(-19.54, -1.04) * mm, "end": v(-19.58, -1.06) * mm});
            skLineSegment(sketch, "E1944", {"start": v(-19.58, -1.06) * mm, "end": v(-19.64, -1.08) * mm});
            skLineSegment(sketch, "E1945", {"start": v(-19.64, -1.08) * mm, "end": v(-19.73, -1.11) * mm});
            skLineSegment(sketch, "E1946", {"start": v(-19.73, -1.11) * mm, "end": v(-19.82, -1.15) * mm});
            skLineSegment(sketch, "E1947", {"start": v(-19.82, -1.15) * mm, "end": v(-19.91, -1.2) * mm});
            skLineSegment(sketch, "E1948", {"start": v(-19.91, -1.2) * mm, "end": v(-20.02, -1.25) * mm});
            skLineSegment(sketch, "E1949", {"start": v(-20.02, -1.25) * mm, "end": v(-20.13, -1.3) * mm});
            skLineSegment(sketch, "E1950", {"start": v(-20.13, -1.3) * mm, "end": v(-20.24, -1.37) * mm});
            skLineSegment(sketch, "E1951", {"start": v(-20.24, -1.37) * mm, "end": v(-20.36, -1.44) * mm});
            skLineSegment(sketch, "E1952", {"start": v(-20.36, -1.44) * mm, "end": v(-20.48, -1.52) * mm});
            skLineSegment(sketch, "E1953", {"start": v(-20.48, -1.52) * mm, "end": v(-20.6, -1.6) * mm});
            skLineSegment(sketch, "E1954", {"start": v(-20.6, -1.6) * mm, "end": v(-20.74, -1.7) * mm});
            skLineSegment(sketch, "E1955", {"start": v(-20.74, -1.7) * mm, "end": v(-21.34, -2.14) * mm});
            skLineSegment(sketch, "E1956", {"start": v(-21.34, -2.14) * mm, "end": v(-21.29, -2.44) * mm});
            skLineSegment(sketch, "E1957", {"start": v(-21.29, -2.44) * mm, "end": v(-21.22, -2.79) * mm});
            skLineSegment(sketch, "E1958", {"start": v(-21.22, -2.79) * mm, "end": v(-21.15, -3.14) * mm});
            skLineSegment(sketch, "E1959", {"start": v(-21.15, -3.14) * mm, "end": v(-20.44, -3.33) * mm});
            skLineSegment(sketch, "E1960", {"start": v(-20.44, -3.33) * mm, "end": v(-20.28, -3.37) * mm});
            skLineSegment(sketch, "E1961", {"start": v(-20.28, -3.37) * mm, "end": v(-20.13, -3.4) * mm});
            skLineSegment(sketch, "E1962", {"start": v(-20.13, -3.4) * mm, "end": v(-20, -3.43) * mm});
            skLineSegment(sketch, "E1963", {"start": v(-20, -3.43) * mm, "end": v(-19.85, -3.45) * mm});
            skLineSegment(sketch, "E1964", {"start": v(-19.85, -3.45) * mm, "end": v(-19.73, -3.47) * mm});
            skLineSegment(sketch, "E1965", {"start": v(-19.73, -3.47) * mm, "end": v(-19.6, -3.49) * mm});
            skLineSegment(sketch, "E1966", {"start": v(-19.6, -3.49) * mm, "end": v(-19.49, -3.5) * mm});
            skLineSegment(sketch, "E1967", {"start": v(-19.49, -3.5) * mm, "end": v(-19.38, -3.5) * mm});
            skLineSegment(sketch, "E1968", {"start": v(-19.38, -3.5) * mm, "end": v(-19.28, -3.51) * mm});
            skLineSegment(sketch, "E1969", {"start": v(-19.28, -3.51) * mm, "end": v(-19.19, -3.51) * mm});
            skLineSegment(sketch, "E1970", {"start": v(-19.19, -3.51) * mm, "end": v(-19.12, -3.51) * mm});
            skLineSegment(sketch, "E1971", {"start": v(-19.12, -3.51) * mm, "end": v(-19.08, -3.51) * mm});
            skLineSegment(sketch, "E1972", {"start": v(-19.08, -3.51) * mm, "end": v(-19.02, -3.51) * mm});
            skLineSegment(sketch, "E1973", {"start": v(-19.02, -3.51) * mm, "end": v(-18.95, -3.5) * mm});
            skLineSegment(sketch, "E1974", {"start": v(-18.95, -3.5) * mm, "end": v(-18.88, -3.5) * mm});
            skLineSegment(sketch, "E1975", {"start": v(-18.88, -3.5) * mm, "end": v(-18.82, -3.5) * mm});
            skLineSegment(sketch, "E1976", {"start": v(-18.82, -3.5) * mm, "end": v(-18.76, -3.5) * mm});
            skLineSegment(sketch, "E1977", {"start": v(-18.76, -3.5) * mm, "end": v(-18.71, -3.48) * mm});
            skLineSegment(sketch, "E1978", {"start": v(-18.71, -3.48) * mm, "end": v(-18.67, -3.48) * mm});
            skLineSegment(sketch, "E1979", {"start": v(-18.67, -3.48) * mm, "end": v(-18.64, -3.47) * mm});
            skLineSegment(sketch, "E1980", {"start": v(-18.64, -3.47) * mm, "end": v(-18.6, -3.46) * mm});
            skLineSegment(sketch, "E1981", {"start": v(-18.6, -3.46) * mm, "end": v(-18.58, -3.46) * mm});
            skLineSegment(sketch, "E1982", {"start": v(-18.58, -3.46) * mm, "end": v(-18.56, -3.45) * mm});
            skLineSegment(sketch, "E1983", {"start": v(-18.56, -3.45) * mm, "end": v(-18.24, -3.37) * mm});
            skLineSegment(sketch, "E1984", {"start": v(-18.24, -3.37) * mm, "end": v(-18.24, -3.37) * mm});
            skLineSegment(sketch, "E1985", {"start": v(-18.24, -3.37) * mm, "end": v(-18.15, -3.35) * mm});
            skLineSegment(sketch, "E1986", {"start": v(-18.15, -3.35) * mm, "end": v(-18.14, -3.36) * mm});
            skLineSegment(sketch, "E1987", {"start": v(-18.14, -3.36) * mm, "end": v(-18.06, -3.34) * mm});
            skLineSegment(sketch, "E1988", {"start": v(-18.06, -3.34) * mm, "end": v(-18.06, -3.35) * mm});
            skLineSegment(sketch, "E1989", {"start": v(-18.06, -3.35) * mm, "end": v(-17.98, -3.33) * mm});
            skLineSegment(sketch, "E1990", {"start": v(-17.98, -3.33) * mm, "end": v(-17.97, -3.35) * mm});
            skLineSegment(sketch, "E1991", {"start": v(-17.97, -3.35) * mm, "end": v(-17.9, -3.33) * mm});
            skLineSegment(sketch, "E1992", {"start": v(-17.9, -3.33) * mm, "end": v(-17.9, -3.35) * mm});
            skLineSegment(sketch, "E1993", {"start": v(-17.9, -3.35) * mm, "end": v(-17.83, -3.34) * mm});
            skLineSegment(sketch, "E1994", {"start": v(-17.83, -3.34) * mm, "end": v(-17.82, -3.36) * mm});
            skLineSegment(sketch, "E1995", {"start": v(-17.82, -3.36) * mm, "end": v(-17.76, -3.35) * mm});
            skLineSegment(sketch, "E1996", {"start": v(-17.76, -3.35) * mm, "end": v(-17.75, -3.37) * mm});
            skLineSegment(sketch, "E1997", {"start": v(-17.75, -3.37) * mm, "end": v(-17.7, -3.37) * mm});
            skLineSegment(sketch, "E1998", {"start": v(-17.7, -3.37) * mm, "end": v(-17.69, -3.4) * mm});
            skLineSegment(sketch, "E1999", {"start": v(-17.69, -3.4) * mm, "end": v(-17.64, -3.39) * mm});
            skLineSegment(sketch, "E2000", {"start": v(-17.64, -3.39) * mm, "end": v(-17.63, -3.41) * mm});
            skLineSegment(sketch, "E2001", {"start": v(-17.63, -3.41) * mm, "end": v(-17.6, -3.41) * mm});
            skLineSegment(sketch, "E2002", {"start": v(-17.6, -3.41) * mm, "end": v(-17.58, -3.44) * mm});
            skLineSegment(sketch, "E2003", {"start": v(-17.58, -3.44) * mm, "end": v(-17.55, -3.46) * mm});
            skLineSegment(sketch, "E2004", {"start": v(-17.55, -3.46) * mm, "end": v(-17.52, -3.48) * mm});
            skLineSegment(sketch, "E2005", {"start": v(-17.52, -3.48) * mm, "end": v(-17.5, -3.5) * mm});
            skLineSegment(sketch, "E2006", {"start": v(-17.5, -3.5) * mm, "end": v(-17.49, -3.53) * mm});
            skLineSegment(sketch, "E2007", {"start": v(-17.49, -3.53) * mm, "end": v(-17.48, -3.55) * mm});
            skLineSegment(sketch, "E2008", {"start": v(-17.48, -3.55) * mm, "end": v(-17.43, -3.7) * mm});
            skLineSegment(sketch, "E2009", {"start": v(-17.43, -3.7) * mm, "end": v(-17.36, -3.89) * mm});
            skLineSegment(sketch, "E2010", {"start": v(-17.36, -3.89) * mm, "end": v(-17.3, -4.02) * mm});
            skLineSegment(sketch, "E2011", {"start": v(-17.3, -4.02) * mm, "end": v(-17.23, -4.21) * mm});
            skLineSegment(sketch, "E2012", {"start": v(-17.23, -4.21) * mm, "end": v(-17.17, -4.35) * mm});
            skLineSegment(sketch, "E2013", {"start": v(-17.17, -4.35) * mm, "end": v(-17.17, -4.38) * mm});
            skLineSegment(sketch, "E2014", {"start": v(-17.17, -4.38) * mm, "end": v(-17.16, -4.4) * mm});
            skLineSegment(sketch, "E2015", {"start": v(-17.16, -4.4) * mm, "end": v(-17.16, -4.42) * mm});
            skLineSegment(sketch, "E2016", {"start": v(-17.16, -4.42) * mm, "end": v(-17.16, -4.45) * mm});
            skLineSegment(sketch, "E2017", {"start": v(-17.16, -4.45) * mm, "end": v(-17.16, -4.5) * mm});
            skLineSegment(sketch, "E2018", {"start": v(-17.16, -4.5) * mm, "end": v(-17.18, -4.5) * mm});
            skLineSegment(sketch, "E2019", {"start": v(-17.18, -4.5) * mm, "end": v(-17.17, -4.54) * mm});
            skLineSegment(sketch, "E2020", {"start": v(-17.17, -4.54) * mm, "end": v(-17.2, -4.56) * mm});
            skLineSegment(sketch, "E2021", {"start": v(-17.2, -4.56) * mm, "end": v(-17.2, -4.6) * mm});
            skLineSegment(sketch, "E2022", {"start": v(-17.2, -4.6) * mm, "end": v(-17.23, -4.62) * mm});
            skLineSegment(sketch, "E2023", {"start": v(-17.23, -4.62) * mm, "end": v(-17.22, -4.65) * mm});
            skLineSegment(sketch, "E2024", {"start": v(-17.22, -4.65) * mm, "end": v(-17.26, -4.68) * mm});
            skLineSegment(sketch, "E2025", {"start": v(-17.26, -4.68) * mm, "end": v(-17.26, -4.7) * mm});
            skLineSegment(sketch, "E2026", {"start": v(-17.26, -4.7) * mm, "end": v(-17.31, -4.74) * mm});
            skLineSegment(sketch, "E2027", {"start": v(-17.31, -4.74) * mm, "end": v(-17.3, -4.76) * mm});
            skLineSegment(sketch, "E2028", {"start": v(-17.3, -4.76) * mm, "end": v(-17.37, -4.8) * mm});
            skLineSegment(sketch, "E2029", {"start": v(-17.37, -4.8) * mm, "end": v(-17.36, -4.82) * mm});
            skLineSegment(sketch, "E2030", {"start": v(-17.36, -4.82) * mm, "end": v(-17.43, -4.86) * mm});
            skLineSegment(sketch, "E2031", {"start": v(-17.43, -4.86) * mm, "end": v(-17.43, -4.88) * mm});
            skLineSegment(sketch, "E2032", {"start": v(-17.43, -4.88) * mm, "end": v(-17.5, -4.92) * mm});
            skLineSegment(sketch, "E2033", {"start": v(-17.5, -4.92) * mm, "end": v(-17.5, -4.94) * mm});
            skLineSegment(sketch, "E2034", {"start": v(-17.5, -4.94) * mm, "end": v(-17.6, -4.98) * mm});
            skLineSegment(sketch, "E2035", {"start": v(-17.6, -4.98) * mm, "end": v(-17.6, -5) * mm});
            skLineSegment(sketch, "E2036", {"start": v(-17.6, -5) * mm, "end": v(-17.69, -5.04) * mm});
            skLineSegment(sketch, "E2037", {"start": v(-17.69, -5.04) * mm, "end": v(-17.69, -5.05) * mm});
            skLineSegment(sketch, "E2038", {"start": v(-17.69, -5.05) * mm, "end": v(-17.99, -5.19) * mm});
            skLineSegment(sketch, "E2039", {"start": v(-17.99, -5.19) * mm, "end": v(-18, -5.2) * mm});
            skLineSegment(sketch, "E2040", {"start": v(-18, -5.2) * mm, "end": v(-18, -5.2) * mm});
            skLineSegment(sketch, "E2041", {"start": v(-18, -5.2) * mm, "end": v(-18.02, -5.2) * mm});
            skLineSegment(sketch, "E2042", {"start": v(-18.02, -5.2) * mm, "end": v(-18.04, -5.22) * mm});
            skLineSegment(sketch, "E2043", {"start": v(-18.04, -5.22) * mm, "end": v(-18.07, -5.24) * mm});
            skLineSegment(sketch, "E2044", {"start": v(-18.07, -5.24) * mm, "end": v(-18.1, -5.26) * mm});
            skLineSegment(sketch, "E2045", {"start": v(-18.1, -5.26) * mm, "end": v(-18.15, -5.29) * mm});
            skLineSegment(sketch, "E2046", {"start": v(-18.15, -5.29) * mm, "end": v(-18.2, -5.32) * mm});
            skLineSegment(sketch, "E2047", {"start": v(-18.2, -5.32) * mm, "end": v(-18.25, -5.36) * mm});
            skLineSegment(sketch, "E2048", {"start": v(-18.25, -5.36) * mm, "end": v(-18.3, -5.4) * mm});
            skLineSegment(sketch, "E2049", {"start": v(-18.3, -5.4) * mm, "end": v(-18.35, -5.44) * mm});
            skLineSegment(sketch, "E2050", {"start": v(-18.35, -5.44) * mm, "end": v(-18.38, -5.47) * mm});
            skLineSegment(sketch, "E2051", {"start": v(-18.38, -5.47) * mm, "end": v(-18.43, -5.52) * mm});
            skLineSegment(sketch, "E2052", {"start": v(-18.43, -5.52) * mm, "end": v(-18.5, -5.58) * mm});
            skLineSegment(sketch, "E2053", {"start": v(-18.5, -5.58) * mm, "end": v(-18.57, -5.65) * mm});
            skLineSegment(sketch, "E2054", {"start": v(-18.57, -5.65) * mm, "end": v(-18.65, -5.73) * mm});
            skLineSegment(sketch, "E2055", {"start": v(-18.65, -5.73) * mm, "end": v(-18.73, -5.81) * mm});
            skLineSegment(sketch, "E2056", {"start": v(-18.73, -5.81) * mm, "end": v(-18.81, -5.9) * mm});
            skLineSegment(sketch, "E2057", {"start": v(-18.81, -5.9) * mm, "end": v(-18.9, -6) * mm});
            skLineSegment(sketch, "E2058", {"start": v(-18.9, -6) * mm, "end": v(-18.98, -6.1) * mm});
            skLineSegment(sketch, "E2059", {"start": v(-18.98, -6.1) * mm, "end": v(-19.07, -6.22) * mm});
            skLineSegment(sketch, "E2060", {"start": v(-19.07, -6.22) * mm, "end": v(-19.16, -6.34) * mm});
            skLineSegment(sketch, "E2061", {"start": v(-19.16, -6.34) * mm, "end": v(-19.25, -6.46) * mm});
            skLineSegment(sketch, "E2062", {"start": v(-19.25, -6.46) * mm, "end": v(-19.67, -7.07) * mm});
            skLineSegment(sketch, "E2063", {"start": v(-19.67, -7.07) * mm, "end": v(-19.64, -7.14) * mm});
            skLineSegment(sketch, "E2064", {"start": v(-19.64, -7.14) * mm, "end": v(-19.46, -7.45) * mm});
            skLineSegment(sketch, "E2065", {"start": v(-19.46, -7.45) * mm, "end": v(-19.28, -7.76) * mm});
            skLineSegment(sketch, "E2066", {"start": v(-19.28, -7.76) * mm, "end": v(-19.15, -7.97) * mm});
            skLineSegment(sketch, "E2067", {"start": v(-19.15, -7.97) * mm, "end": v(-18.42, -7.9) * mm});
            skLineSegment(sketch, "E2068", {"start": v(-18.42, -7.9) * mm, "end": v(-18.26, -7.9) * mm});
            skLineSegment(sketch, "E2069", {"start": v(-18.26, -7.9) * mm, "end": v(-18.1, -7.87) * mm});
            skLineSegment(sketch, "E2070", {"start": v(-18.1, -7.87) * mm, "end": v(-17.97, -7.85) * mm});
            skLineSegment(sketch, "E2071", {"start": v(-17.97, -7.85) * mm, "end": v(-17.83, -7.83) * mm});
            skLineSegment(sketch, "E2072", {"start": v(-17.83, -7.83) * mm, "end": v(-17.7, -7.8) * mm});
            skLineSegment(sketch, "E2073", {"start": v(-17.7, -7.8) * mm, "end": v(-17.59, -7.77) * mm});
            skLineSegment(sketch, "E2074", {"start": v(-17.59, -7.77) * mm, "end": v(-17.48, -7.75) * mm});
            skLineSegment(sketch, "E2075", {"start": v(-17.48, -7.75) * mm, "end": v(-17.37, -7.72) * mm});
            skLineSegment(sketch, "E2076", {"start": v(-17.37, -7.72) * mm, "end": v(-17.27, -7.7) * mm});
            skLineSegment(sketch, "E2077", {"start": v(-17.27, -7.7) * mm, "end": v(-17.18, -7.66) * mm});
            skLineSegment(sketch, "E2078", {"start": v(-17.18, -7.66) * mm, "end": v(-17.1, -7.64) * mm});
            skLineSegment(sketch, "E2079", {"start": v(-17.1, -7.64) * mm, "end": v(-17.07, -7.62) * mm});
            skLineSegment(sketch, "E2080", {"start": v(-17.07, -7.62) * mm, "end": v(-17.01, -7.6) * mm});
            skLineSegment(sketch, "E2081", {"start": v(-17.01, -7.6) * mm, "end": v(-16.93, -7.58) * mm});
            skLineSegment(sketch, "E2082", {"start": v(-16.93, -7.58) * mm, "end": v(-16.86, -7.55) * mm});
            skLineSegment(sketch, "E2083", {"start": v(-16.86, -7.55) * mm, "end": v(-16.8, -7.52) * mm});
            skLineSegment(sketch, "E2084", {"start": v(-16.8, -7.52) * mm, "end": v(-16.74, -7.5) * mm});
            skLineSegment(sketch, "E2085", {"start": v(-16.74, -7.5) * mm, "end": v(-16.7, -7.47) * mm});
            skLineSegment(sketch, "E2086", {"start": v(-16.7, -7.47) * mm, "end": v(-16.64, -7.45) * mm});
            skLineSegment(sketch, "E2087", {"start": v(-16.64, -7.45) * mm, "end": v(-16.6, -7.43) * mm});
            skLineSegment(sketch, "E2088", {"start": v(-16.6, -7.43) * mm, "end": v(-16.56, -7.4) * mm});
            skLineSegment(sketch, "E2089", {"start": v(-16.56, -7.4) * mm, "end": v(-16.53, -7.39) * mm});
            skLineSegment(sketch, "E2090", {"start": v(-16.53, -7.39) * mm, "end": v(-16.5, -7.37) * mm});
            skLineSegment(sketch, "E2091", {"start": v(-16.5, -7.37) * mm, "end": v(-16.21, -7.2) * mm});
            skLineSegment(sketch, "E2092", {"start": v(-16.21, -7.2) * mm, "end": v(-16.2, -7.2) * mm});
            skLineSegment(sketch, "E2093", {"start": v(-16.2, -7.2) * mm, "end": v(-16.14, -7.16) * mm});
            skLineSegment(sketch, "E2094", {"start": v(-16.14, -7.16) * mm, "end": v(-16.13, -7.16) * mm});
            skLineSegment(sketch, "E2095", {"start": v(-16.13, -7.16) * mm, "end": v(-16.07, -7.13) * mm});
            skLineSegment(sketch, "E2096", {"start": v(-16.07, -7.13) * mm, "end": v(-16.04, -7.12) * mm});
            skLineSegment(sketch, "E2097", {"start": v(-16.04, -7.12) * mm, "end": v(-16, -7.11) * mm});
            skLineSegment(sketch, "E2098", {"start": v(-16, -7.11) * mm, "end": v(-15.94, -7.09) * mm});
            skLineSegment(sketch, "E2099", {"start": v(-15.94, -7.09) * mm, "end": v(-15.9, -7.08) * mm});
            skLineSegment(sketch, "E2100", {"start": v(-15.9, -7.08) * mm, "end": v(-15.87, -7.08) * mm});
            skLineSegment(sketch, "E2101", {"start": v(-15.87, -7.08) * mm, "end": v(-15.83, -7.06) * mm});
            skLineSegment(sketch, "E2102", {"start": v(-15.83, -7.06) * mm, "end": v(-15.8, -7.07) * mm});
            skLineSegment(sketch, "E2103", {"start": v(-15.8, -7.07) * mm, "end": v(-15.76, -7.08) * mm});
            skLineSegment(sketch, "E2104", {"start": v(-15.76, -7.08) * mm, "end": v(-15.72, -7.06) * mm});
            skLineSegment(sketch, "E2105", {"start": v(-15.72, -7.06) * mm, "end": v(-15.7, -7.08) * mm});
            skLineSegment(sketch, "E2106", {"start": v(-15.7, -7.08) * mm, "end": v(-15.66, -7.1) * mm});
            skLineSegment(sketch, "E2107", {"start": v(-15.66, -7.1) * mm, "end": v(-15.63, -7.1) * mm});
            skLineSegment(sketch, "E2108", {"start": v(-15.63, -7.1) * mm, "end": v(-15.6, -7.1) * mm});
            skLineSegment(sketch, "E2109", {"start": v(-15.6, -7.1) * mm, "end": v(-15.58, -7.12) * mm});
            skLineSegment(sketch, "E2110", {"start": v(-15.58, -7.12) * mm, "end": v(-15.56, -7.14) * mm});
            skLineSegment(sketch, "E2111", {"start": v(-15.56, -7.14) * mm, "end": v(-15.54, -7.15) * mm});
            skLineSegment(sketch, "E2112", {"start": v(-15.54, -7.15) * mm, "end": v(-15.45, -7.27) * mm});
            skLineSegment(sketch, "E2113", {"start": v(-15.45, -7.27) * mm, "end": v(-15.32, -7.44) * mm});
            skLineSegment(sketch, "E2114", {"start": v(-15.32, -7.44) * mm, "end": v(-15.23, -7.56) * mm});
            skLineSegment(sketch, "E2115", {"start": v(-15.23, -7.56) * mm, "end": v(-15.1, -7.72) * mm});
            skLineSegment(sketch, "E2116", {"start": v(-15.1, -7.72) * mm, "end": v(-15, -7.84) * mm});
            skLineSegment(sketch, "E2117", {"start": v(-15, -7.84) * mm, "end": v(-14.98, -7.85) * mm});
            skLineSegment(sketch, "E2118", {"start": v(-14.98, -7.85) * mm, "end": v(-14.97, -7.87) * mm});
            skLineSegment(sketch, "E2119", {"start": v(-14.97, -7.87) * mm, "end": v(-14.96, -7.89) * mm});
            skLineSegment(sketch, "E2120", {"start": v(-14.96, -7.89) * mm, "end": v(-14.96, -7.9) * mm});
            skLineSegment(sketch, "E2121", {"start": v(-14.96, -7.9) * mm, "end": v(-14.94, -7.94) * mm});
            skLineSegment(sketch, "E2122", {"start": v(-14.94, -7.94) * mm, "end": v(-14.95, -7.98) * mm});
            skLineSegment(sketch, "E2123", {"start": v(-14.95, -7.98) * mm, "end": v(-14.96, -8.01) * mm});
            skLineSegment(sketch, "E2124", {"start": v(-14.96, -8.01) * mm, "end": v(-14.95, -8.05) * mm});
            skLineSegment(sketch, "E2125", {"start": v(-14.95, -8.05) * mm, "end": v(-14.95, -8.1) * mm});
            skLineSegment(sketch, "E2126", {"start": v(-14.95, -8.1) * mm, "end": v(-14.98, -8.13) * mm});
            skLineSegment(sketch, "E2127", {"start": v(-14.98, -8.13) * mm, "end": v(-14.97, -8.15) * mm});
            skLineSegment(sketch, "E2128", {"start": v(-14.97, -8.15) * mm, "end": v(-15, -8.2) * mm});
            skLineSegment(sketch, "E2129", {"start": v(-15, -8.2) * mm, "end": v(-14.99, -8.21) * mm});
            skLineSegment(sketch, "E2130", {"start": v(-14.99, -8.21) * mm, "end": v(-15.03, -8.26) * mm});
            skLineSegment(sketch, "E2131", {"start": v(-15.03, -8.26) * mm, "end": v(-15.02, -8.28) * mm});
            skLineSegment(sketch, "E2132", {"start": v(-15.02, -8.28) * mm, "end": v(-15.07, -8.33) * mm});
            skLineSegment(sketch, "E2133", {"start": v(-15.07, -8.33) * mm, "end": v(-15.06, -8.35) * mm});
            skLineSegment(sketch, "E2134", {"start": v(-15.06, -8.35) * mm, "end": v(-15.11, -8.4) * mm});
            skLineSegment(sketch, "E2135", {"start": v(-15.11, -8.4) * mm, "end": v(-15.1, -8.42) * mm});
            skLineSegment(sketch, "E2136", {"start": v(-15.1, -8.42) * mm, "end": v(-15.17, -8.49) * mm});
            skLineSegment(sketch, "E2137", {"start": v(-15.17, -8.49) * mm, "end": v(-15.16, -8.5) * mm});
            skLineSegment(sketch, "E2138", {"start": v(-15.16, -8.5) * mm, "end": v(-15.23, -8.57) * mm});
            skLineSegment(sketch, "E2139", {"start": v(-15.23, -8.57) * mm, "end": v(-15.23, -8.57) * mm});
            skLineSegment(sketch, "E2140", {"start": v(-15.23, -8.57) * mm, "end": v(-15.46, -8.8) * mm});
            skLineSegment(sketch, "E2141", {"start": v(-15.46, -8.8) * mm, "end": v(-15.47, -8.81) * mm});
            skLineSegment(sketch, "E2142", {"start": v(-15.47, -8.81) * mm, "end": v(-15.48, -8.83) * mm});
            skLineSegment(sketch, "E2143", {"start": v(-15.48, -8.83) * mm, "end": v(-15.5, -8.85) * mm});
            skLineSegment(sketch, "E2144", {"start": v(-15.5, -8.85) * mm, "end": v(-15.52, -8.88) * mm});
            skLineSegment(sketch, "E2145", {"start": v(-15.52, -8.88) * mm, "end": v(-15.55, -8.91) * mm});
            skLineSegment(sketch, "E2146", {"start": v(-15.55, -8.91) * mm, "end": v(-15.58, -8.95) * mm});
            skLineSegment(sketch, "E2147", {"start": v(-15.58, -8.95) * mm, "end": v(-15.62, -9) * mm});
            skLineSegment(sketch, "E2148", {"start": v(-15.62, -9) * mm, "end": v(-15.65, -9.05) * mm});
            skLineSegment(sketch, "E2149", {"start": v(-15.65, -9.05) * mm, "end": v(-15.7, -9.11) * mm});
            skLineSegment(sketch, "E2150", {"start": v(-15.7, -9.11) * mm, "end": v(-15.73, -9.17) * mm});
            skLineSegment(sketch, "E2151", {"start": v(-15.73, -9.17) * mm, "end": v(-15.77, -9.23) * mm});
            skLineSegment(sketch, "E2152", {"start": v(-15.77, -9.23) * mm, "end": v(-15.8, -9.27) * mm});
            skLineSegment(sketch, "E2153", {"start": v(-15.8, -9.27) * mm, "end": v(-15.83, -9.33) * mm});
            skLineSegment(sketch, "E2154", {"start": v(-15.83, -9.33) * mm, "end": v(-15.87, -9.41) * mm});
            skLineSegment(sketch, "E2155", {"start": v(-15.87, -9.41) * mm, "end": v(-15.92, -9.5) * mm});
            skLineSegment(sketch, "E2156", {"start": v(-15.92, -9.5) * mm, "end": v(-15.97, -9.6) * mm});
            skLineSegment(sketch, "E2157", {"start": v(-15.97, -9.6) * mm, "end": v(-16.02, -9.7) * mm});
            skLineSegment(sketch, "E2158", {"start": v(-16.02, -9.7) * mm, "end": v(-16.07, -9.82) * mm});
            skLineSegment(sketch, "E2159", {"start": v(-16.07, -9.82) * mm, "end": v(-16.13, -9.93) * mm});
            skLineSegment(sketch, "E2160", {"start": v(-16.13, -9.93) * mm, "end": v(-16.18, -10.05) * mm});
            skLineSegment(sketch, "E2161", {"start": v(-16.18, -10.05) * mm, "end": v(-16.23, -10.18) * mm});
            skLineSegment(sketch, "E2162", {"start": v(-16.23, -10.18) * mm, "end": v(-16.28, -10.31) * mm});
            skLineSegment(sketch, "E2163", {"start": v(-16.28, -10.31) * mm, "end": v(-16.33, -10.45) * mm});
            skLineSegment(sketch, "E2164", {"start": v(-16.33, -10.45) * mm, "end": v(-16.57, -11.17) * mm});
            skLineSegment(sketch, "E2165", {"start": v(-16.57, -11.17) * mm, "end": v(-16.4, -11.34) * mm});
            skLineSegment(sketch, "E2166", {"start": v(-16.4, -11.34) * mm, "end": v(-16.14, -11.58) * mm});
            skLineSegment(sketch, "E2167", {"start": v(-16.14, -11.58) * mm, "end": v(-15.88, -11.82) * mm});
            skLineSegment(sketch, "E2168", {"start": v(-15.88, -11.82) * mm, "end": v(-15.79, -11.9) * mm});
            skLineSegment(sketch, "E2169", {"start": v(-15.79, -11.9) * mm, "end": v(-15.09, -11.6) * mm});
            skLineSegment(sketch, "E2170", {"start": v(-15.09, -11.6) * mm, "end": v(-14.95, -11.55) * mm});
            skLineSegment(sketch, "E2171", {"start": v(-14.95, -11.55) * mm, "end": v(-14.82, -11.49) * mm});
            skLineSegment(sketch, "E2172", {"start": v(-14.82, -11.49) * mm, "end": v(-14.7, -11.43) * mm});
            skLineSegment(sketch, "E2173", {"start": v(-14.7, -11.43) * mm, "end": v(-14.58, -11.37) * mm});
            skLineSegment(sketch, "E2174", {"start": v(-14.58, -11.37) * mm, "end": v(-14.47, -11.3) * mm});
            skLineSegment(sketch, "E2175", {"start": v(-14.47, -11.3) * mm, "end": v(-14.36, -11.25) * mm});
            skLineSegment(sketch, "E2176", {"start": v(-14.36, -11.25) * mm, "end": v(-14.26, -11.19) * mm});
            skLineSegment(sketch, "E2177", {"start": v(-14.26, -11.19) * mm, "end": v(-14.17, -11.14) * mm});
            skLineSegment(sketch, "E2178", {"start": v(-14.17, -11.14) * mm, "end": v(-14.08, -11.08) * mm});
            skLineSegment(sketch, "E2179", {"start": v(-14.08, -11.08) * mm, "end": v(-14, -11.03) * mm});
            skLineSegment(sketch, "E2180", {"start": v(-14, -11.03) * mm, "end": v(-13.94, -10.99) * mm});
            skLineSegment(sketch, "E2181", {"start": v(-13.94, -10.99) * mm, "end": v(-13.9, -10.96) * mm});
            skLineSegment(sketch, "E2182", {"start": v(-13.9, -10.96) * mm, "end": v(-13.85, -10.92) * mm});
            skLineSegment(sketch, "E2183", {"start": v(-13.85, -10.92) * mm, "end": v(-13.78, -10.87) * mm});
            skLineSegment(sketch, "E2184", {"start": v(-13.78, -10.87) * mm, "end": v(-13.72, -10.83) * mm});
            skLineSegment(sketch, "E2185", {"start": v(-13.72, -10.83) * mm, "end": v(-13.66, -10.78) * mm});
            skLineSegment(sketch, "E2186", {"start": v(-13.66, -10.78) * mm, "end": v(-13.6, -10.74) * mm});
            skLineSegment(sketch, "E2187", {"start": v(-13.6, -10.74) * mm, "end": v(-13.55, -10.7) * mm});
            skLineSegment(sketch, "E2188", {"start": v(-13.55, -10.7) * mm, "end": v(-13.5, -10.66) * mm});
            skLineSegment(sketch, "E2189", {"start": v(-13.5, -10.66) * mm, "end": v(-13.46, -10.62) * mm});
            skLineSegment(sketch, "E2190", {"start": v(-13.46, -10.62) * mm, "end": v(-13.42, -10.58) * mm});
            skLineSegment(sketch, "E2191", {"start": v(-13.42, -10.58) * mm, "end": v(-13.4, -10.55) * mm});
            skLineSegment(sketch, "E2192", {"start": v(-13.4, -10.55) * mm, "end": v(-13.36, -10.52) * mm});
            skLineSegment(sketch, "E2193", {"start": v(-13.36, -10.52) * mm, "end": v(-13.1, -10.26) * mm});
            skLineSegment(sketch, "E2194", {"start": v(-13.1, -10.26) * mm, "end": v(-13.06, -10.24) * mm});
            skLineSegment(sketch, "E2195", {"start": v(-13.06, -10.24) * mm, "end": v(-13.04, -10.22) * mm});
            skLineSegment(sketch, "E2196", {"start": v(-13.04, -10.22) * mm, "end": v(-13, -10.18) * mm});
            skLineSegment(sketch, "E2197", {"start": v(-13, -10.18) * mm, "end": v(-12.97, -10.17) * mm});
            skLineSegment(sketch, "E2198", {"start": v(-12.97, -10.17) * mm, "end": v(-12.94, -10.16) * mm});
            skLineSegment(sketch, "E2199", {"start": v(-12.94, -10.16) * mm, "end": v(-12.9, -10.13) * mm});
            skLineSegment(sketch, "E2200", {"start": v(-12.9, -10.13) * mm, "end": v(-12.87, -10.12) * mm});
            skLineSegment(sketch, "E2201", {"start": v(-12.87, -10.12) * mm, "end": v(-12.83, -10.1) * mm});
            skLineSegment(sketch, "E2202", {"start": v(-12.83, -10.1) * mm, "end": v(-12.78, -10.08) * mm});
            skLineSegment(sketch, "E2203", {"start": v(-12.78, -10.08) * mm, "end": v(-12.74, -10.07) * mm});
            skLineSegment(sketch, "E2204", {"start": v(-12.74, -10.07) * mm, "end": v(-12.7, -10.07) * mm});
            skLineSegment(sketch, "E2205", {"start": v(-12.7, -10.07) * mm, "end": v(-12.66, -10.07) * mm});
            skLineSegment(sketch, "E2206", {"start": v(-12.66, -10.07) * mm, "end": v(-12.63, -10.07) * mm});
            skLineSegment(sketch, "E2207", {"start": v(-12.63, -10.07) * mm, "end": v(-12.61, -10.08) * mm});
            skLineSegment(sketch, "E2208", {"start": v(-12.61, -10.08) * mm, "end": v(-12.6, -10.08) * mm});
            skLineSegment(sketch, "E2209", {"start": v(-12.6, -10.08) * mm, "end": v(-12.58, -10.09) * mm});
            skLineSegment(sketch, "E2210", {"start": v(-12.58, -10.09) * mm, "end": v(-12.56, -10.1) * mm});
            skLineSegment(sketch, "E2211", {"start": v(-12.56, -10.1) * mm, "end": v(-12.44, -10.2) * mm});
            skLineSegment(sketch, "E2212", {"start": v(-12.44, -10.2) * mm, "end": v(-12.27, -10.32) * mm});
            skLineSegment(sketch, "E2213", {"start": v(-12.27, -10.32) * mm, "end": v(-12.14, -10.4) * mm});
            skLineSegment(sketch, "E2214", {"start": v(-12.14, -10.4) * mm, "end": v(-11.97, -10.53) * mm});
            skLineSegment(sketch, "E2215", {"start": v(-11.97, -10.53) * mm, "end": v(-11.84, -10.62) * mm});
            skLineSegment(sketch, "E2216", {"start": v(-11.84, -10.62) * mm, "end": v(-11.82, -10.63) * mm});
            skLineSegment(sketch, "E2217", {"start": v(-11.82, -10.63) * mm, "end": v(-11.81, -10.64) * mm});
            skLineSegment(sketch, "E2218", {"start": v(-11.81, -10.64) * mm, "end": v(-11.8, -10.65) * mm});
            skLineSegment(sketch, "E2219", {"start": v(-11.8, -10.65) * mm, "end": v(-11.8, -10.67) * mm});
            skLineSegment(sketch, "E2220", {"start": v(-11.8, -10.67) * mm, "end": v(-11.78, -10.7) * mm});
            skLineSegment(sketch, "E2221", {"start": v(-11.78, -10.7) * mm, "end": v(-11.76, -10.74) * mm});
            skLineSegment(sketch, "E2222", {"start": v(-11.76, -10.74) * mm, "end": v(-11.76, -10.78) * mm});
            skLineSegment(sketch, "E2223", {"start": v(-11.76, -10.78) * mm, "end": v(-11.74, -10.81) * mm});
            skLineSegment(sketch, "E2224", {"start": v(-11.74, -10.81) * mm, "end": v(-11.76, -10.85) * mm});
            skLineSegment(sketch, "E2225", {"start": v(-11.76, -10.85) * mm, "end": v(-11.75, -10.89) * mm});
            skLineSegment(sketch, "E2226", {"start": v(-11.75, -10.89) * mm, "end": v(-11.75, -10.92) * mm});
            skLineSegment(sketch, "E2227", {"start": v(-11.75, -10.92) * mm, "end": v(-11.77, -10.97) * mm});
            skLineSegment(sketch, "E2228", {"start": v(-11.77, -10.97) * mm, "end": v(-11.77, -11) * mm});
            skLineSegment(sketch, "E2229", {"start": v(-11.77, -11) * mm, "end": v(-11.77, -11.04) * mm});
            skLineSegment(sketch, "E2230", {"start": v(-11.77, -11.04) * mm, "end": v(-11.8, -11.1) * mm});
            skLineSegment(sketch, "E2231", {"start": v(-11.8, -11.1) * mm, "end": v(-11.8, -11.11) * mm});
            skLineSegment(sketch, "E2232", {"start": v(-11.8, -11.11) * mm, "end": v(-11.82, -11.18) * mm});
            skLineSegment(sketch, "E2233", {"start": v(-11.82, -11.18) * mm, "end": v(-11.82, -11.19) * mm});
            skLineSegment(sketch, "E2234", {"start": v(-11.82, -11.19) * mm, "end": v(-11.85, -11.26) * mm});
            skLineSegment(sketch, "E2235", {"start": v(-11.85, -11.26) * mm, "end": v(-11.85, -11.27) * mm});
            skLineSegment(sketch, "E2236", {"start": v(-11.85, -11.27) * mm, "end": v(-12, -11.57) * mm});
            skLineSegment(sketch, "E2237", {"start": v(-12, -11.57) * mm, "end": v(-12.02, -11.6) * mm});
            skLineSegment(sketch, "E2238", {"start": v(-12.02, -11.6) * mm, "end": v(-12.03, -11.62) * mm});
            skLineSegment(sketch, "E2239", {"start": v(-12.03, -11.62) * mm, "end": v(-12.05, -11.67) * mm});
            skLineSegment(sketch, "E2240", {"start": v(-12.05, -11.67) * mm, "end": v(-12.07, -11.7) * mm});
            skLineSegment(sketch, "E2241", {"start": v(-12.07, -11.7) * mm, "end": v(-12.09, -11.76) * mm});
            skLineSegment(sketch, "E2242", {"start": v(-12.09, -11.76) * mm, "end": v(-12.1, -11.82) * mm});
            skLineSegment(sketch, "E2243", {"start": v(-12.1, -11.82) * mm, "end": v(-12.13, -11.88) * mm});
            skLineSegment(sketch, "E2244", {"start": v(-12.13, -11.88) * mm, "end": v(-12.16, -11.94) * mm});
            skLineSegment(sketch, "E2245", {"start": v(-12.16, -11.94) * mm, "end": v(-12.18, -12.02) * mm});
            skLineSegment(sketch, "E2246", {"start": v(-12.18, -12.02) * mm, "end": v(-12.2, -12.1) * mm});
            skLineSegment(sketch, "E2247", {"start": v(-12.2, -12.1) * mm, "end": v(-12.22, -12.16) * mm});
            skLineSegment(sketch, "E2248", {"start": v(-12.22, -12.16) * mm, "end": v(-12.24, -12.2) * mm});
            skLineSegment(sketch, "E2249", {"start": v(-12.24, -12.2) * mm, "end": v(-12.25, -12.28) * mm});
            skLineSegment(sketch, "E2250", {"start": v(-12.25, -12.28) * mm, "end": v(-12.28, -12.37) * mm});
            skLineSegment(sketch, "E2251", {"start": v(-12.28, -12.37) * mm, "end": v(-12.3, -12.47) * mm});
            skLineSegment(sketch, "E2252", {"start": v(-12.3, -12.47) * mm, "end": v(-12.32, -12.58) * mm});
            skLineSegment(sketch, "E2253", {"start": v(-12.32, -12.58) * mm, "end": v(-12.35, -12.68) * mm});
            skLineSegment(sketch, "E2254", {"start": v(-12.35, -12.68) * mm, "end": v(-12.37, -12.8) * mm});
            skLineSegment(sketch, "E2255", {"start": v(-12.37, -12.8) * mm, "end": v(-12.39, -12.92) * mm});
            skLineSegment(sketch, "E2256", {"start": v(-12.39, -12.92) * mm, "end": v(-12.4, -13.04) * mm});
            skLineSegment(sketch, "E2257", {"start": v(-12.4, -13.04) * mm, "end": v(-12.42, -13.17) * mm});
            skLineSegment(sketch, "E2258", {"start": v(-12.42, -13.17) * mm, "end": v(-12.44, -13.3) * mm});
            skLineSegment(sketch, "E2259", {"start": v(-12.44, -13.3) * mm, "end": v(-12.46, -13.44) * mm});
            skLineSegment(sketch, "E2260", {"start": v(-12.46, -13.44) * mm, "end": v(-12.53, -14.24) * mm});
            skLineSegment(sketch, "E2261", {"start": v(-12.53, -14.24) * mm, "end": v(-12.52, -14.24) * mm});
            skLineSegment(sketch, "E2262", {"start": v(-12.52, -14.24) * mm, "end": v(-12.22, -14.41) * mm});
            skLineSegment(sketch, "E2263", {"start": v(-12.22, -14.41) * mm, "end": v(-11.93, -14.58) * mm});
            skLineSegment(sketch, "E2264", {"start": v(-11.93, -14.58) * mm, "end": v(-11.63, -14.73) * mm});
            skLineSegment(sketch, "E2265", {"start": v(-11.63, -14.73) * mm, "end": v(-11.57, -14.77) * mm});
            skLineSegment(sketch, "E2266", {"start": v(-11.57, -14.77) * mm, "end": v(-10.92, -14.26) * mm});
            skLineSegment(sketch, "E2267", {"start": v(-10.92, -14.26) * mm, "end": v(-10.81, -14.18) * mm});
            skLineSegment(sketch, "E2268", {"start": v(-10.81, -14.18) * mm, "end": v(-10.7, -14.1) * mm});
            skLineSegment(sketch, "E2269", {"start": v(-10.7, -14.1) * mm, "end": v(-10.6, -14) * mm});
            skLineSegment(sketch, "E2270", {"start": v(-10.6, -14) * mm, "end": v(-10.52, -13.93) * mm});
            skLineSegment(sketch, "E2271", {"start": v(-10.52, -13.93) * mm, "end": v(-10.43, -13.85) * mm});
            skLineSegment(sketch, "E2272", {"start": v(-10.43, -13.85) * mm, "end": v(-10.34, -13.77) * mm});
            skLineSegment(sketch, "E2273", {"start": v(-10.34, -13.77) * mm, "end": v(-10.27, -13.7) * mm});
            skLineSegment(sketch, "E2274", {"start": v(-10.27, -13.7) * mm, "end": v(-10.2, -13.62) * mm});
            skLineSegment(sketch, "E2275", {"start": v(-10.2, -13.62) * mm, "end": v(-10.12, -13.55) * mm});
            skLineSegment(sketch, "E2276", {"start": v(-10.12, -13.55) * mm, "end": v(-10.06, -13.48) * mm});
            skLineSegment(sketch, "E2277", {"start": v(-10.06, -13.48) * mm, "end": v(-10, -13.43) * mm});
            skLineSegment(sketch, "E2278", {"start": v(-10, -13.43) * mm, "end": v(-9.98, -13.4) * mm});
            skLineSegment(sketch, "E2279", {"start": v(-9.98, -13.4) * mm, "end": v(-9.94, -13.35) * mm});
            skLineSegment(sketch, "E2280", {"start": v(-9.94, -13.35) * mm, "end": v(-9.88, -13.28) * mm});
            skLineSegment(sketch, "E2281", {"start": v(-9.88, -13.28) * mm, "end": v(-9.83, -13.22) * mm});
            skLineSegment(sketch, "E2282", {"start": v(-9.83, -13.22) * mm, "end": v(-9.78, -13.17) * mm});
            skLineSegment(sketch, "E2283", {"start": v(-9.78, -13.17) * mm, "end": v(-9.73, -13.1) * mm});
            skLineSegment(sketch, "E2284", {"start": v(-9.73, -13.1) * mm, "end": v(-9.66, -13.02) * mm});
            skLineSegment(sketch, "E2285", {"start": v(-9.66, -13.02) * mm, "end": v(-9.61, -12.95) * mm});
            skLineSegment(sketch, "E2286", {"start": v(-9.61, -12.95) * mm, "end": v(-9.56, -12.88) * mm});
            skLineSegment(sketch, "E2287", {"start": v(-9.56, -12.88) * mm, "end": v(-9.52, -12.82) * mm});
            skLineSegment(sketch, "E2288", {"start": v(-9.52, -12.82) * mm, "end": v(-9.3, -12.48) * mm});
            skLineSegment(sketch, "E2289", {"start": v(-9.3, -12.48) * mm, "end": v(-9.29, -12.49) * mm});
            skLineSegment(sketch, "E2290", {"start": v(-9.29, -12.49) * mm, "end": v(-9.24, -12.42) * mm});
            skLineSegment(sketch, "E2291", {"start": v(-9.24, -12.42) * mm, "end": v(-9.23, -12.43) * mm});
            skLineSegment(sketch, "E2292", {"start": v(-9.23, -12.43) * mm, "end": v(-9.2, -12.37) * mm});
            skLineSegment(sketch, "E2293", {"start": v(-9.2, -12.37) * mm, "end": v(-9.16, -12.35) * mm});
            skLineSegment(sketch, "E2294", {"start": v(-9.16, -12.35) * mm, "end": v(-9.13, -12.33) * mm});
            skLineSegment(sketch, "E2295", {"start": v(-9.13, -12.33) * mm, "end": v(-9.1, -12.3) * mm});
            skLineSegment(sketch, "E2296", {"start": v(-9.1, -12.3) * mm, "end": v(-9.06, -12.28) * mm});
            skLineSegment(sketch, "E2297", {"start": v(-9.06, -12.28) * mm, "end": v(-9.03, -12.27) * mm});
            skLineSegment(sketch, "E2298", {"start": v(-9.03, -12.27) * mm, "end": v(-9, -12.26) * mm});
            skLineSegment(sketch, "E2299", {"start": v(-9, -12.26) * mm, "end": v(-8.98, -12.25) * mm});
            skLineSegment(sketch, "E2300", {"start": v(-8.98, -12.25) * mm, "end": v(-8.95, -12.24) * mm});
            skLineSegment(sketch, "E2301", {"start": v(-8.95, -12.24) * mm, "end": v(-8.93, -12.24) * mm});
            skLineSegment(sketch, "E2302", {"start": v(-8.93, -12.24) * mm, "end": v(-8.91, -12.24) * mm});
            skLineSegment(sketch, "E2303", {"start": v(-8.91, -12.24) * mm, "end": v(-8.9, -12.25) * mm});
            skLineSegment(sketch, "E2304", {"start": v(-8.9, -12.25) * mm, "end": v(-8.88, -12.25) * mm});
            skLineSegment(sketch, "E2305", {"start": v(-8.88, -12.25) * mm, "end": v(-8.72, -12.32) * mm});
            skLineSegment(sketch, "E2306", {"start": v(-8.72, -12.32) * mm, "end": v(-8.53, -12.4) * mm});
            skLineSegment(sketch, "E2307", {"start": v(-8.53, -12.4) * mm, "end": v(-8.39, -12.46) * mm});
            skLineSegment(sketch, "E2308", {"start": v(-8.39, -12.46) * mm, "end": v(-8.2, -12.53) * mm});
            skLineSegment(sketch, "E2309", {"start": v(-8.2, -12.53) * mm, "end": v(-8.04, -12.6) * mm});
            skLineSegment(sketch, "E2310", {"start": v(-8.04, -12.6) * mm, "end": v(-8.02, -12.6) * mm});
            skLineSegment(sketch, "E2311", {"start": v(-8.02, -12.6) * mm, "end": v(-8.01, -12.61) * mm});
            skLineSegment(sketch, "E2312", {"start": v(-8.01, -12.61) * mm, "end": v(-8, -12.62) * mm});
            skLineSegment(sketch, "E2313", {"start": v(-8, -12.62) * mm, "end": v(-8, -12.63) * mm});
            skLineSegment(sketch, "E2314", {"start": v(-8, -12.63) * mm, "end": v(-7.97, -12.66) * mm});
            skLineSegment(sketch, "E2315", {"start": v(-7.97, -12.66) * mm, "end": v(-7.95, -12.68) * mm});
            skLineSegment(sketch, "E2316", {"start": v(-7.95, -12.68) * mm, "end": v(-7.94, -12.72) * mm});
            skLineSegment(sketch, "E2317", {"start": v(-7.94, -12.72) * mm, "end": v(-7.93, -12.75) * mm});
            skLineSegment(sketch, "E2318", {"start": v(-7.93, -12.75) * mm, "end": v(-7.92, -12.8) * mm});
            skLineSegment(sketch, "E2319", {"start": v(-7.92, -12.8) * mm, "end": v(-7.9, -12.84) * mm});
            skLineSegment(sketch, "E2320", {"start": v(-7.9, -12.84) * mm, "end": v(-7.9, -12.87) * mm});
            skLineSegment(sketch, "E2321", {"start": v(-7.9, -12.87) * mm, "end": v(-7.9, -12.92) * mm});
            skLineSegment(sketch, "E2322", {"start": v(-7.9, -12.92) * mm, "end": v(-7.9, -12.95) * mm});
            skLineSegment(sketch, "E2323", {"start": v(-7.9, -12.95) * mm, "end": v(-7.9, -12.98) * mm});
            skLineSegment(sketch, "E2324", {"start": v(-7.9, -12.98) * mm, "end": v(-7.9, -13.04) * mm});
            skLineSegment(sketch, "E2325", {"start": v(-7.9, -13.04) * mm, "end": v(-7.9, -13.08) * mm});
            skLineSegment(sketch, "E2326", {"start": v(-7.9, -13.08) * mm, "end": v(-7.9, -13.11) * mm});
            skLineSegment(sketch, "E2327", {"start": v(-7.9, -13.11) * mm, "end": v(-8, -13.5) * mm});
            skLineSegment(sketch, "E2328", {"start": v(-8, -13.5) * mm, "end": v(-8, -13.53) * mm});
            skLineSegment(sketch, "E2329", {"start": v(-8, -13.53) * mm, "end": v(-8, -13.58) * mm});
            skLineSegment(sketch, "E2330", {"start": v(-8, -13.58) * mm, "end": v(-8.02, -13.63) * mm});
            skLineSegment(sketch, "E2331", {"start": v(-8.02, -13.63) * mm, "end": v(-8.02, -13.69) * mm});
            skLineSegment(sketch, "E2332", {"start": v(-8.02, -13.69) * mm, "end": v(-8.03, -13.74) * mm});
            skLineSegment(sketch, "E2333", {"start": v(-8.03, -13.74) * mm, "end": v(-8.04, -13.82) * mm});
            skLineSegment(sketch, "E2334", {"start": v(-8.04, -13.82) * mm, "end": v(-8.05, -13.89) * mm});
            skLineSegment(sketch, "E2335", {"start": v(-8.05, -13.89) * mm, "end": v(-8.06, -13.96) * mm});
            skLineSegment(sketch, "E2336", {"start": v(-8.06, -13.96) * mm, "end": v(-8.06, -14.04) * mm});
            skLineSegment(sketch, "E2337", {"start": v(-8.06, -14.04) * mm, "end": v(-8.07, -14.12) * mm});
            skLineSegment(sketch, "E2338", {"start": v(-8.07, -14.12) * mm, "end": v(-8.07, -14.18) * mm});
            skLineSegment(sketch, "E2339", {"start": v(-8.07, -14.18) * mm, "end": v(-8.07, -14.23) * mm});
            skLineSegment(sketch, "E2340", {"start": v(-8.07, -14.23) * mm, "end": v(-8.08, -14.3) * mm});
            skLineSegment(sketch, "E2341", {"start": v(-8.08, -14.3) * mm, "end": v(-8.08, -14.4) * mm});
            skLineSegment(sketch, "E2342", {"start": v(-8.08, -14.4) * mm, "end": v(-8.08, -14.5) * mm});
            skLineSegment(sketch, "E2343", {"start": v(-8.08, -14.5) * mm, "end": v(-8.08, -14.6) * mm});
            skLineSegment(sketch, "E2344", {"start": v(-8.08, -14.6) * mm, "end": v(-8.08, -14.72) * mm});
            skLineSegment(sketch, "E2345", {"start": v(-8.08, -14.72) * mm, "end": v(-8.07, -14.9) * mm});
            skLineSegment(sketch, "E2346", {"start": v(-8.07, -14.9) * mm, "end": v(-8.06, -15.06) * mm});
            skLineSegment(sketch, "E2347", {"start": v(-8.06, -15.06) * mm, "end": v(-8.05, -15.24) * mm});
            skLineSegment(sketch, "E2348", {"start": v(-8.05, -15.24) * mm, "end": v(-8.03, -15.42) * mm});
            skLineSegment(sketch, "E2349", {"start": v(-8.03, -15.42) * mm, "end": v(-7.94, -16.28) * mm});
            skLineSegment(sketch, "E2350", {"start": v(-7.94, -16.28) * mm, "end": v(-7.71, -16.35) * mm});
            skLineSegment(sketch, "E2351", {"start": v(-7.71, -16.35) * mm, "end": v(-7.4, -16.44) * mm});
            skLineSegment(sketch, "E2352", {"start": v(-7.4, -16.44) * mm, "end": v(-7.1, -16.53) * mm});
            skLineSegment(sketch, "E2353", {"start": v(-7.1, -16.53) * mm, "end": v(-6.87, -16.6) * mm});
            skLineSegment(sketch, "E2354", {"start": v(-6.87, -16.6) * mm, "end": v(-6.34, -15.96) * mm});
            skLineSegment(sketch, "E2355", {"start": v(-6.34, -15.96) * mm, "end": v(-6.22, -15.8) * mm});
            skLineSegment(sketch, "E2356", {"start": v(-6.22, -15.8) * mm, "end": v(-6.1, -15.66) * mm});
            skLineSegment(sketch, "E2357", {"start": v(-6.1, -15.66) * mm, "end": v(-6, -15.52) * mm});
            skLineSegment(sketch, "E2358", {"start": v(-6, -15.52) * mm, "end": v(-5.91, -15.4) * mm});
            skLineSegment(sketch, "E2359", {"start": v(-5.91, -15.4) * mm, "end": v(-5.83, -15.26) * mm});
            skLineSegment(sketch, "E2360", {"start": v(-5.83, -15.26) * mm, "end": v(-5.75, -15.15) * mm});
            skLineSegment(sketch, "E2361", {"start": v(-5.75, -15.15) * mm, "end": v(-5.68, -15.03) * mm});
            skLineSegment(sketch, "E2362", {"start": v(-5.68, -15.03) * mm, "end": v(-5.63, -14.96) * mm});
            skLineSegment(sketch, "E2363", {"start": v(-5.63, -14.96) * mm, "end": v(-5.6, -14.92) * mm});
            skLineSegment(sketch, "E2364", {"start": v(-5.6, -14.92) * mm, "end": v(-5.57, -14.85) * mm});
            skLineSegment(sketch, "E2365", {"start": v(-5.57, -14.85) * mm, "end": v(-5.51, -14.75) * mm});
            skLineSegment(sketch, "E2366", {"start": v(-5.51, -14.75) * mm, "end": v(-5.46, -14.66) * mm});
            skLineSegment(sketch, "E2367", {"start": v(-5.46, -14.66) * mm, "end": v(-5.41, -14.57) * mm});
            skLineSegment(sketch, "E2368", {"start": v(-5.41, -14.57) * mm, "end": v(-5.37, -14.49) * mm});
            skLineSegment(sketch, "E2369", {"start": v(-5.37, -14.49) * mm, "end": v(-5.34, -14.4) * mm});
            skLineSegment(sketch, "E2370", {"start": v(-5.34, -14.4) * mm, "end": v(-5.3, -14.34) * mm});
            skLineSegment(sketch, "E2371", {"start": v(-5.3, -14.34) * mm, "end": v(-5.27, -14.27) * mm});
            skLineSegment(sketch, "E2372", {"start": v(-5.27, -14.27) * mm, "end": v(-5.25, -14.21) * mm});
            skLineSegment(sketch, "E2373", {"start": v(-5.25, -14.21) * mm, "end": v(-5.12, -13.9) * mm});
            skLineSegment(sketch, "E2374", {"start": v(-5.12, -13.9) * mm, "end": v(-5.1, -13.87) * mm});
            skLineSegment(sketch, "E2375", {"start": v(-5.1, -13.87) * mm, "end": v(-5.08, -13.84) * mm});
            skLineSegment(sketch, "E2376", {"start": v(-5.08, -13.84) * mm, "end": v(-5.06, -13.78) * mm});
            skLineSegment(sketch, "E2377", {"start": v(-5.06, -13.78) * mm, "end": v(-5.03, -13.76) * mm});
            skLineSegment(sketch, "E2378", {"start": v(-5.03, -13.76) * mm, "end": v(-5, -13.73) * mm});
            skLineSegment(sketch, "E2379", {"start": v(-5, -13.73) * mm, "end": v(-4.99, -13.69) * mm});
            skLineSegment(sketch, "E2380", {"start": v(-4.99, -13.69) * mm, "end": v(-4.96, -13.67) * mm});
            skLineSegment(sketch, "E2381", {"start": v(-4.96, -13.67) * mm, "end": v(-4.93, -13.65) * mm});
            skLineSegment(sketch, "E2382", {"start": v(-4.93, -13.65) * mm, "end": v(-4.9, -13.62) * mm});
            skLineSegment(sketch, "E2383", {"start": v(-4.9, -13.62) * mm, "end": v(-4.87, -13.6) * mm});
            skLineSegment(sketch, "E2384", {"start": v(-4.87, -13.6) * mm, "end": v(-4.83, -13.58) * mm});
            skLineSegment(sketch, "E2385", {"start": v(-4.83, -13.58) * mm, "end": v(-4.8, -13.57) * mm});
            skLineSegment(sketch, "E2386", {"start": v(-4.8, -13.57) * mm, "end": v(-4.8, -13.57) * mm});
            skLineSegment(sketch, "E2387", {"start": v(-4.8, -13.57) * mm, "end": v(-4.77, -13.58) * mm});
            skLineSegment(sketch, "E2388", {"start": v(-4.77, -13.58) * mm, "end": v(-4.76, -13.58) * mm});
            skLineSegment(sketch, "E2389", {"start": v(-4.76, -13.58) * mm, "end": v(-4.64, -13.6) * mm});
            skLineSegment(sketch, "E2390", {"start": v(-4.64, -13.6) * mm, "end": v(-4.38, -13.65) * mm});
            skLineSegment(sketch, "E2391", {"start": v(-4.38, -13.65) * mm, "end": v(-4.24, -13.68) * mm});
            skLineSegment(sketch, "E2392", {"start": v(-4.24, -13.68) * mm, "end": v(-4, -13.73) * mm});
            skLineSegment(sketch, "E2393", {"start": v(-4, -13.73) * mm, "end": v(-3.87, -13.75) * mm});
            skLineSegment(sketch, "E2394", {"start": v(-3.87, -13.75) * mm, "end": v(-3.85, -13.75) * mm});
            skLineSegment(sketch, "E2395", {"start": v(-3.85, -13.75) * mm, "end": v(-3.84, -13.76) * mm});
            skLineSegment(sketch, "E2396", {"start": v(-3.84, -13.76) * mm, "end": v(-3.83, -13.76) * mm});
            skLineSegment(sketch, "E2397", {"start": v(-3.83, -13.76) * mm, "end": v(-3.82, -13.77) * mm});
            skLineSegment(sketch, "E2398", {"start": v(-3.82, -13.77) * mm, "end": v(-3.79, -13.8) * mm});
            skLineSegment(sketch, "E2399", {"start": v(-3.79, -13.8) * mm, "end": v(-3.76, -13.83) * mm});
            skLineSegment(sketch, "E2400", {"start": v(-3.76, -13.83) * mm, "end": v(-3.74, -13.85) * mm});
            skLineSegment(sketch, "E2401", {"start": v(-3.74, -13.85) * mm, "end": v(-3.73, -13.9) * mm});
            skLineSegment(sketch, "E2402", {"start": v(-3.73, -13.9) * mm, "end": v(-3.71, -13.93) * mm});
            skLineSegment(sketch, "E2403", {"start": v(-3.71, -13.93) * mm, "end": v(-3.7, -13.96) * mm});
            skLineSegment(sketch, "E2404", {"start": v(-3.7, -13.96) * mm, "end": v(-3.69, -14.02) * mm});
            skLineSegment(sketch, "E2405", {"start": v(-3.69, -14.02) * mm, "end": v(-3.67, -14.02) * mm});
            skLineSegment(sketch, "E2406", {"start": v(-3.67, -14.02) * mm, "end": v(-3.67, -14.1) * mm});
            skLineSegment(sketch, "E2407", {"start": v(-3.67, -14.1) * mm, "end": v(-3.66, -14.1) * mm});
            skLineSegment(sketch, "E2408", {"start": v(-3.66, -14.1) * mm, "end": v(-3.66, -14.18) * mm});
            skLineSegment(sketch, "E2409", {"start": v(-3.66, -14.18) * mm, "end": v(-3.65, -14.18) * mm});
            skLineSegment(sketch, "E2410", {"start": v(-3.65, -14.18) * mm, "end": v(-3.65, -14.56) * mm});
            skLineSegment(sketch, "E2411", {"start": v(-3.65, -14.56) * mm, "end": v(-3.65, -14.64) * mm});
            skLineSegment(sketch, "E2412", {"start": v(-3.65, -14.64) * mm, "end": v(-3.64, -14.72) * mm});
            skLineSegment(sketch, "E2413", {"start": v(-3.64, -14.72) * mm, "end": v(-3.64, -14.8) * mm});
            skLineSegment(sketch, "E2414", {"start": v(-3.64, -14.8) * mm, "end": v(-3.63, -14.9) * mm});
            skLineSegment(sketch, "E2415", {"start": v(-3.63, -14.9) * mm, "end": v(-3.62, -15) * mm});
            skLineSegment(sketch, "E2416", {"start": v(-3.62, -15) * mm, "end": v(-3.6, -15.12) * mm});
            skLineSegment(sketch, "E2417", {"start": v(-3.6, -15.12) * mm, "end": v(-3.6, -15.23) * mm});
            skLineSegment(sketch, "E2418", {"start": v(-3.6, -15.23) * mm, "end": v(-3.58, -15.3) * mm});
            skLineSegment(sketch, "E2419", {"start": v(-3.58, -15.3) * mm, "end": v(-3.57, -15.35) * mm});
            skLineSegment(sketch, "E2420", {"start": v(-3.57, -15.35) * mm, "end": v(-3.56, -15.44) * mm});
            skLineSegment(sketch, "E2421", {"start": v(-3.56, -15.44) * mm, "end": v(-3.54, -15.57) * mm});
            skLineSegment(sketch, "E2422", {"start": v(-3.54, -15.57) * mm, "end": v(-3.5, -15.7) * mm});
            skLineSegment(sketch, "E2423", {"start": v(-3.5, -15.7) * mm, "end": v(-3.48, -15.84) * mm});
            skLineSegment(sketch, "E2424", {"start": v(-3.48, -15.84) * mm, "end": v(-3.44, -15.99) * mm});
            skLineSegment(sketch, "E2425", {"start": v(-3.44, -15.99) * mm, "end": v(-3.4, -16.14) * mm});
            skLineSegment(sketch, "E2426", {"start": v(-3.4, -16.14) * mm, "end": v(-3.37, -16.29) * mm});
            skLineSegment(sketch, "E2427", {"start": v(-3.37, -16.29) * mm, "end": v(-3.32, -16.44) * mm});
            skLineSegment(sketch, "E2428", {"start": v(-3.32, -16.44) * mm, "end": v(-3.27, -16.6) * mm});
            skLineSegment(sketch, "E2429", {"start": v(-3.27, -16.6) * mm, "end": v(-3.04, -17.34) * mm});
            skLineSegment(sketch, "E2430", {"start": v(-3.04, -17.34) * mm, "end": v(-3, -17.34) * mm});
            skLineSegment(sketch, "E2431", {"start": v(-3, -17.34) * mm, "end": v(-2.71, -17.37) * mm});
            skLineSegment(sketch, "E2432", {"start": v(-2.71, -17.37) * mm, "end": v(-2.43, -17.4) * mm});
            skLineSegment(sketch, "E2433", {"start": v(-2.43, -17.4) * mm, "end": v(-2.15, -17.42) * mm});
            skLineSegment(sketch, "E2434", {"start": v(-2.15, -17.42) * mm, "end": v(-1.93, -17.44) * mm});
            skLineSegment(sketch, "E2435", {"start": v(-1.93, -17.44) * mm, "end": v(-1.54, -16.72) * mm});
            skSolve(sketch);
        }
        {
            var Q0;
            Q0 = qSketchRegion(id + "F6", true);
            var Q1;
            {var subQ0=makeQuery(id+"F2.opExtrude","CAP_FACE",FACE,{"disambiguationData":[OSD([sQuery(id+"F1.wireOp",EDGE,"E5"),sQuery(id+"F1.wireOp",EDGE,"E7"),sQuery(id+"F1.wireOp",EDGE,"E8"),sQuery(id+"F1.wireOp",EDGE,"E9"),sQuery(id+"F1.wireOp",EDGE,"E10"),sQuery(id+"F1.wireOp",EDGE,"E11"),sQuery(id+"F1.wireOp",EDGE,"E12"),sQuery(id+"F1.wireOp",EDGE,"E13"),sQuery(id+"F1.wireOp",EDGE,"E14"),sQuery(id+"F1.wireOp",EDGE,"E15"),sQuery(id+"F1.wireOp",EDGE,"E16"),sQuery(id+"F1.wireOp",EDGE,"E17"),sQuery(id+"F1.wireOp",EDGE,"E18"),sQuery(id+"F1.wireOp",EDGE,"E19"),sQuery(id+"F1.wireOp",EDGE,"E20"),sQuery(id+"F1.wireOp",EDGE,"E21"),sQuery(id+"F1.wireOp",EDGE,"E22"),sQuery(id+"F1.wireOp",EDGE,"E23"),sQuery(id+"F1.wireOp",EDGE,"E24"),sQuery(id+"F1.wireOp",EDGE,"E25"),sQuery(id+"F1.wireOp",EDGE,"E26"),sQuery(id+"F1.wireOp",EDGE,"E27"),sQuery(id+"F1.wireOp",EDGE,"E28"),sQuery(id+"F1.wireOp",EDGE,"E29"),sQuery(id+"F1.wireOp",EDGE,"E30"),sQuery(id+"F1.wireOp",EDGE,"E31"),sQuery(id+"F1.wireOp",EDGE,"E34"),sQuery(id+"F1.wireOp",EDGE,"E35")])],"isStart":false});var subQ1=makeQuery(id+"F3.boolean.opBoolean","MERGE",FACE,{"derivedFrom":[subQ0,makeQuery(id+"F3.opPattern","COPY",FACE,{"derivedFrom":subQ0,"instanceName":"1"})]});Q1=makeQuery(id+"F5.boolean.opBoolean","MERGE",FACE,{"derivedFrom":[subQ1,makeQuery(id+"F5.opPattern","COPY",FACE,{"derivedFrom":subQ1,"instanceName":"1"}),makeQuery(id+"F5.opPattern","COPY",FACE,{"derivedFrom":subQ1,"instanceName":"2"}),makeQuery(id+"F5.opPattern","COPY",FACE,{"derivedFrom":subQ1,"instanceName":"3"}),makeQuery(id+"F5.opPattern","COPY",FACE,{"derivedFrom":subQ1,"instanceName":"4"}),makeQuery(id+"F5.opPattern","COPY",FACE,{"derivedFrom":subQ1,"instanceName":"5"})]});}
            extrude(context, id + "F7", {"entities" : qUnion([Q0]), "endBound" : BoundingType.UP_TO_SURFACE, "depth" : 25 * mm, "endBoundEntityFace" : qUnion([Q1]), "offsetDistance" : 25 * mm});
        }
        {
            var Q0;
            Q0=makeQuery(id+"F7.opExtrude","SWEPT_BODY",BODY,{"disambiguationData":[OSD([sQuery(id+"F6.wireOp",EDGE,"E37"),sQuery(id+"F6.wireOp",EDGE,"E38"),sQuery(id+"F6.wireOp",EDGE,"E39"),sQuery(id+"F6.wireOp",EDGE,"E40"),sQuery(id+"F6.wireOp",EDGE,"E41"),sQuery(id+"F6.wireOp",EDGE,"E42"),sQuery(id+"F6.wireOp",EDGE,"E43"),sQuery(id+"F6.wireOp",EDGE,"E44"),sQuery(id+"F6.wireOp",EDGE,"E45"),sQuery(id+"F6.wireOp",EDGE,"E46"),sQuery(id+"F6.wireOp",EDGE,"E47"),sQuery(id+"F6.wireOp",EDGE,"E48"),sQuery(id+"F6.wireOp",EDGE,"E49"),sQuery(id+"F6.wireOp",EDGE,"E50"),sQuery(id+"F6.wireOp",EDGE,"E51"),sQuery(id+"F6.wireOp",EDGE,"E52"),sQuery(id+"F6.wireOp",EDGE,"E53"),sQuery(id+"F6.wireOp",EDGE,"E54"),sQuery(id+"F6.wireOp",EDGE,"E55"),sQuery(id+"F6.wireOp",EDGE,"E56"),sQuery(id+"F6.wireOp",EDGE,"E57"),sQuery(id+"F6.wireOp",EDGE,"E58"),sQuery(id+"F6.wireOp",EDGE,"E59"),sQuery(id+"F6.wireOp",EDGE,"E60"),sQuery(id+"F6.wireOp",EDGE,"E61"),sQuery(id+"F6.wireOp",EDGE,"E62"),sQuery(id+"F6.wireOp",EDGE,"E63"),sQuery(id+"F6.wireOp",EDGE,"E64"),sQuery(id+"F6.wireOp",EDGE,"E65"),sQuery(id+"F6.wireOp",EDGE,"E66"),sQuery(id+"F6.wireOp",EDGE,"E67"),sQuery(id+"F6.wireOp",EDGE,"E68"),sQuery(id+"F6.wireOp",EDGE,"E69"),sQuery(id+"F6.wireOp",EDGE,"E70"),sQuery(id+"F6.wireOp",EDGE,"E71"),sQuery(id+"F6.wireOp",EDGE,"E72"),sQuery(id+"F6.wireOp",EDGE,"E73"),sQuery(id+"F6.wireOp",EDGE,"E74"),sQuery(id+"F6.wireOp",EDGE,"E75"),sQuery(id+"F6.wireOp",EDGE,"E76"),sQuery(id+"F6.wireOp",EDGE,"E77"),sQuery(id+"F6.wireOp",EDGE,"E78"),sQuery(id+"F6.wireOp",EDGE,"E79"),sQuery(id+"F6.wireOp",EDGE,"E80"),sQuery(id+"F6.wireOp",EDGE,"E81"),sQuery(id+"F6.wireOp",EDGE,"E82"),sQuery(id+"F6.wireOp",EDGE,"E83"),sQuery(id+"F6.wireOp",EDGE,"E84"),sQuery(id+"F6.wireOp",EDGE,"E85"),sQuery(id+"F6.wireOp",EDGE,"E86"),sQuery(id+"F6.wireOp",EDGE,"E87"),sQuery(id+"F6.wireOp",EDGE,"E88"),sQuery(id+"F6.wireOp",EDGE,"E89"),sQuery(id+"F6.wireOp",EDGE,"E90"),sQuery(id+"F6.wireOp",EDGE,"E91"),sQuery(id+"F6.wireOp",EDGE,"E92"),sQuery(id+"F6.wireOp",EDGE,"E93"),sQuery(id+"F6.wireOp",EDGE,"E94"),sQuery(id+"F6.wireOp",EDGE,"E95"),sQuery(id+"F6.wireOp",EDGE,"E96"),sQuery(id+"F6.wireOp",EDGE,"E97"),sQuery(id+"F6.wireOp",EDGE,"E98"),sQuery(id+"F6.wireOp",EDGE,"E99"),sQuery(id+"F6.wireOp",EDGE,"E100"),sQuery(id+"F6.wireOp",EDGE,"E101"),sQuery(id+"F6.wireOp",EDGE,"E102"),sQuery(id+"F6.wireOp",EDGE,"E103"),sQuery(id+"F6.wireOp",EDGE,"E104"),sQuery(id+"F6.wireOp",EDGE,"E105"),sQuery(id+"F6.wireOp",EDGE,"E106"),sQuery(id+"F6.wireOp",EDGE,"E107"),sQuery(id+"F6.wireOp",EDGE,"E108"),sQuery(id+"F6.wireOp",EDGE,"E109"),sQuery(id+"F6.wireOp",EDGE,"E110"),sQuery(id+"F6.wireOp",EDGE,"E111"),sQuery(id+"F6.wireOp",EDGE,"E112"),sQuery(id+"F6.wireOp",EDGE,"E113"),sQuery(id+"F6.wireOp",EDGE,"E114"),sQuery(id+"F6.wireOp",EDGE,"E115"),sQuery(id+"F6.wireOp",EDGE,"E116"),sQuery(id+"F6.wireOp",EDGE,"E117"),sQuery(id+"F6.wireOp",EDGE,"E118"),sQuery(id+"F6.wireOp",EDGE,"E119"),sQuery(id+"F6.wireOp",EDGE,"E120"),sQuery(id+"F6.wireOp",EDGE,"E121"),sQuery(id+"F6.wireOp",EDGE,"E122"),sQuery(id+"F6.wireOp",EDGE,"E123"),sQuery(id+"F6.wireOp",EDGE,"E124"),sQuery(id+"F6.wireOp",EDGE,"E125"),sQuery(id+"F6.wireOp",EDGE,"E126"),sQuery(id+"F6.wireOp",EDGE,"E127"),sQuery(id+"F6.wireOp",EDGE,"E128"),sQuery(id+"F6.wireOp",EDGE,"E129"),sQuery(id+"F6.wireOp",EDGE,"E130"),sQuery(id+"F6.wireOp",EDGE,"E131"),sQuery(id+"F6.wireOp",EDGE,"E132"),sQuery(id+"F6.wireOp",EDGE,"E133"),sQuery(id+"F6.wireOp",EDGE,"E134"),sQuery(id+"F6.wireOp",EDGE,"E135"),sQuery(id+"F6.wireOp",EDGE,"E136"),sQuery(id+"F6.wireOp",EDGE,"E137"),sQuery(id+"F6.wireOp",EDGE,"E138"),sQuery(id+"F6.wireOp",EDGE,"E139"),sQuery(id+"F6.wireOp",EDGE,"E140"),sQuery(id+"F6.wireOp",EDGE,"E141"),sQuery(id+"F6.wireOp",EDGE,"E142"),sQuery(id+"F6.wireOp",EDGE,"E143"),sQuery(id+"F6.wireOp",EDGE,"E144"),sQuery(id+"F6.wireOp",EDGE,"E145"),sQuery(id+"F6.wireOp",EDGE,"E146"),sQuery(id+"F6.wireOp",EDGE,"E147"),sQuery(id+"F6.wireOp",EDGE,"E148"),sQuery(id+"F6.wireOp",EDGE,"E149"),sQuery(id+"F6.wireOp",EDGE,"E150"),sQuery(id+"F6.wireOp",EDGE,"E151"),sQuery(id+"F6.wireOp",EDGE,"E152"),sQuery(id+"F6.wireOp",EDGE,"E153"),sQuery(id+"F6.wireOp",EDGE,"E154"),sQuery(id+"F6.wireOp",EDGE,"E155"),sQuery(id+"F6.wireOp",EDGE,"E156"),sQuery(id+"F6.wireOp",EDGE,"E157"),sQuery(id+"F6.wireOp",EDGE,"E158"),sQuery(id+"F6.wireOp",EDGE,"E159"),sQuery(id+"F6.wireOp",EDGE,"E160"),sQuery(id+"F6.wireOp",EDGE,"E161"),sQuery(id+"F6.wireOp",EDGE,"E162"),sQuery(id+"F6.wireOp",EDGE,"E163"),sQuery(id+"F6.wireOp",EDGE,"E164"),sQuery(id+"F6.wireOp",EDGE,"E165"),sQuery(id+"F6.wireOp",EDGE,"E166"),sQuery(id+"F6.wireOp",EDGE,"E167"),sQuery(id+"F6.wireOp",EDGE,"E168"),sQuery(id+"F6.wireOp",EDGE,"E169"),sQuery(id+"F6.wireOp",EDGE,"E170"),sQuery(id+"F6.wireOp",EDGE,"E171"),sQuery(id+"F6.wireOp",EDGE,"E172"),sQuery(id+"F6.wireOp",EDGE,"E173"),sQuery(id+"F6.wireOp",EDGE,"E174"),sQuery(id+"F6.wireOp",EDGE,"E175"),sQuery(id+"F6.wireOp",EDGE,"E176"),sQuery(id+"F6.wireOp",EDGE,"E177"),sQuery(id+"F6.wireOp",EDGE,"E178"),sQuery(id+"F6.wireOp",EDGE,"E179"),sQuery(id+"F6.wireOp",EDGE,"E180"),sQuery(id+"F6.wireOp",EDGE,"E181"),sQuery(id+"F6.wireOp",EDGE,"E182"),sQuery(id+"F6.wireOp",EDGE,"E183"),sQuery(id+"F6.wireOp",EDGE,"E184"),sQuery(id+"F6.wireOp",EDGE,"E185"),sQuery(id+"F6.wireOp",EDGE,"E186"),sQuery(id+"F6.wireOp",EDGE,"E187"),sQuery(id+"F6.wireOp",EDGE,"E188"),sQuery(id+"F6.wireOp",EDGE,"E189"),sQuery(id+"F6.wireOp",EDGE,"E190"),sQuery(id+"F6.wireOp",EDGE,"E191"),sQuery(id+"F6.wireOp",EDGE,"E192"),sQuery(id+"F6.wireOp",EDGE,"E193"),sQuery(id+"F6.wireOp",EDGE,"E194"),sQuery(id+"F6.wireOp",EDGE,"E195"),sQuery(id+"F6.wireOp",EDGE,"E196"),sQuery(id+"F6.wireOp",EDGE,"E197"),sQuery(id+"F6.wireOp",EDGE,"E198"),sQuery(id+"F6.wireOp",EDGE,"E199"),sQuery(id+"F6.wireOp",EDGE,"E200"),sQuery(id+"F6.wireOp",EDGE,"E201"),sQuery(id+"F6.wireOp",EDGE,"E202"),sQuery(id+"F6.wireOp",EDGE,"E203"),sQuery(id+"F6.wireOp",EDGE,"E204"),sQuery(id+"F6.wireOp",EDGE,"E205"),sQuery(id+"F6.wireOp",EDGE,"E206"),sQuery(id+"F6.wireOp",EDGE,"E207"),sQuery(id+"F6.wireOp",EDGE,"E208"),sQuery(id+"F6.wireOp",EDGE,"E209"),sQuery(id+"F6.wireOp",EDGE,"E210"),sQuery(id+"F6.wireOp",EDGE,"E211"),sQuery(id+"F6.wireOp",EDGE,"E212"),sQuery(id+"F6.wireOp",EDGE,"E213"),sQuery(id+"F6.wireOp",EDGE,"E214"),sQuery(id+"F6.wireOp",EDGE,"E215"),sQuery(id+"F6.wireOp",EDGE,"E216"),sQuery(id+"F6.wireOp",EDGE,"E217"),sQuery(id+"F6.wireOp",EDGE,"E218"),sQuery(id+"F6.wireOp",EDGE,"E219"),sQuery(id+"F6.wireOp",EDGE,"E220"),sQuery(id+"F6.wireOp",EDGE,"E221"),sQuery(id+"F6.wireOp",EDGE,"E222"),sQuery(id+"F6.wireOp",EDGE,"E223"),sQuery(id+"F6.wireOp",EDGE,"E224"),sQuery(id+"F6.wireOp",EDGE,"E225"),sQuery(id+"F6.wireOp",EDGE,"E226"),sQuery(id+"F6.wireOp",EDGE,"E227"),sQuery(id+"F6.wireOp",EDGE,"E228"),sQuery(id+"F6.wireOp",EDGE,"E229"),sQuery(id+"F6.wireOp",EDGE,"E230"),sQuery(id+"F6.wireOp",EDGE,"E231"),sQuery(id+"F6.wireOp",EDGE,"E232"),sQuery(id+"F6.wireOp",EDGE,"E233"),sQuery(id+"F6.wireOp",EDGE,"E234"),sQuery(id+"F6.wireOp",EDGE,"E235"),sQuery(id+"F6.wireOp",EDGE,"E236"),sQuery(id+"F6.wireOp",EDGE,"E237"),sQuery(id+"F6.wireOp",EDGE,"E238"),sQuery(id+"F6.wireOp",EDGE,"E239"),sQuery(id+"F6.wireOp",EDGE,"E240"),sQuery(id+"F6.wireOp",EDGE,"E241"),sQuery(id+"F6.wireOp",EDGE,"E242"),sQuery(id+"F6.wireOp",EDGE,"E243"),sQuery(id+"F6.wireOp",EDGE,"E244"),sQuery(id+"F6.wireOp",EDGE,"E245"),sQuery(id+"F6.wireOp",EDGE,"E246"),sQuery(id+"F6.wireOp",EDGE,"E247"),sQuery(id+"F6.wireOp",EDGE,"E248"),sQuery(id+"F6.wireOp",EDGE,"E249"),sQuery(id+"F6.wireOp",EDGE,"E250"),sQuery(id+"F6.wireOp",EDGE,"E251"),sQuery(id+"F6.wireOp",EDGE,"E252"),sQuery(id+"F6.wireOp",EDGE,"E253"),sQuery(id+"F6.wireOp",EDGE,"E254"),sQuery(id+"F6.wireOp",EDGE,"E255"),sQuery(id+"F6.wireOp",EDGE,"E256"),sQuery(id+"F6.wireOp",EDGE,"E257"),sQuery(id+"F6.wireOp",EDGE,"E258"),sQuery(id+"F6.wireOp",EDGE,"E259"),sQuery(id+"F6.wireOp",EDGE,"E260"),sQuery(id+"F6.wireOp",EDGE,"E261"),sQuery(id+"F6.wireOp",EDGE,"E262"),sQuery(id+"F6.wireOp",EDGE,"E263"),sQuery(id+"F6.wireOp",EDGE,"E264"),sQuery(id+"F6.wireOp",EDGE,"E265"),sQuery(id+"F6.wireOp",EDGE,"E266"),sQuery(id+"F6.wireOp",EDGE,"E267"),sQuery(id+"F6.wireOp",EDGE,"E268"),sQuery(id+"F6.wireOp",EDGE,"E269"),sQuery(id+"F6.wireOp",EDGE,"E270"),sQuery(id+"F6.wireOp",EDGE,"E271"),sQuery(id+"F6.wireOp",EDGE,"E272"),sQuery(id+"F6.wireOp",EDGE,"E273"),sQuery(id+"F6.wireOp",EDGE,"E274"),sQuery(id+"F6.wireOp",EDGE,"E275"),sQuery(id+"F6.wireOp",EDGE,"E276"),sQuery(id+"F6.wireOp",EDGE,"E277"),sQuery(id+"F6.wireOp",EDGE,"E278"),sQuery(id+"F6.wireOp",EDGE,"E279"),sQuery(id+"F6.wireOp",EDGE,"E280"),sQuery(id+"F6.wireOp",EDGE,"E281"),sQuery(id+"F6.wireOp",EDGE,"E282"),sQuery(id+"F6.wireOp",EDGE,"E283"),sQuery(id+"F6.wireOp",EDGE,"E284"),sQuery(id+"F6.wireOp",EDGE,"E285"),sQuery(id+"F6.wireOp",EDGE,"E286"),sQuery(id+"F6.wireOp",EDGE,"E287"),sQuery(id+"F6.wireOp",EDGE,"E288"),sQuery(id+"F6.wireOp",EDGE,"E289"),sQuery(id+"F6.wireOp",EDGE,"E290"),sQuery(id+"F6.wireOp",EDGE,"E291"),sQuery(id+"F6.wireOp",EDGE,"E292"),sQuery(id+"F6.wireOp",EDGE,"E293"),sQuery(id+"F6.wireOp",EDGE,"E294"),sQuery(id+"F6.wireOp",EDGE,"E295"),sQuery(id+"F6.wireOp",EDGE,"E296"),sQuery(id+"F6.wireOp",EDGE,"E297"),sQuery(id+"F6.wireOp",EDGE,"E298"),sQuery(id+"F6.wireOp",EDGE,"E299"),sQuery(id+"F6.wireOp",EDGE,"E300"),sQuery(id+"F6.wireOp",EDGE,"E301"),sQuery(id+"F6.wireOp",EDGE,"E302"),sQuery(id+"F6.wireOp",EDGE,"E303"),sQuery(id+"F6.wireOp",EDGE,"E304"),sQuery(id+"F6.wireOp",EDGE,"E305"),sQuery(id+"F6.wireOp",EDGE,"E306"),sQuery(id+"F6.wireOp",EDGE,"E307"),sQuery(id+"F6.wireOp",EDGE,"E308"),sQuery(id+"F6.wireOp",EDGE,"E309"),sQuery(id+"F6.wireOp",EDGE,"E310"),sQuery(id+"F6.wireOp",EDGE,"E311"),sQuery(id+"F6.wireOp",EDGE,"E312"),sQuery(id+"F6.wireOp",EDGE,"E313"),sQuery(id+"F6.wireOp",EDGE,"E314"),sQuery(id+"F6.wireOp",EDGE,"E315"),sQuery(id+"F6.wireOp",EDGE,"E316"),sQuery(id+"F6.wireOp",EDGE,"E317"),sQuery(id+"F6.wireOp",EDGE,"E318"),sQuery(id+"F6.wireOp",EDGE,"E319"),sQuery(id+"F6.wireOp",EDGE,"E320"),sQuery(id+"F6.wireOp",EDGE,"E321"),sQuery(id+"F6.wireOp",EDGE,"E322"),sQuery(id+"F6.wireOp",EDGE,"E323"),sQuery(id+"F6.wireOp",EDGE,"E324"),sQuery(id+"F6.wireOp",EDGE,"E325"),sQuery(id+"F6.wireOp",EDGE,"E326"),sQuery(id+"F6.wireOp",EDGE,"E327"),sQuery(id+"F6.wireOp",EDGE,"E328"),sQuery(id+"F6.wireOp",EDGE,"E329"),sQuery(id+"F6.wireOp",EDGE,"E330"),sQuery(id+"F6.wireOp",EDGE,"E331"),sQuery(id+"F6.wireOp",EDGE,"E332"),sQuery(id+"F6.wireOp",EDGE,"E333"),sQuery(id+"F6.wireOp",EDGE,"E334"),sQuery(id+"F6.wireOp",EDGE,"E335"),sQuery(id+"F6.wireOp",EDGE,"E336"),sQuery(id+"F6.wireOp",EDGE,"E337"),sQuery(id+"F6.wireOp",EDGE,"E338"),sQuery(id+"F6.wireOp",EDGE,"E339"),sQuery(id+"F6.wireOp",EDGE,"E340"),sQuery(id+"F6.wireOp",EDGE,"E341"),sQuery(id+"F6.wireOp",EDGE,"E342"),sQuery(id+"F6.wireOp",EDGE,"E343"),sQuery(id+"F6.wireOp",EDGE,"E344"),sQuery(id+"F6.wireOp",EDGE,"E345"),sQuery(id+"F6.wireOp",EDGE,"E346"),sQuery(id+"F6.wireOp",EDGE,"E347"),sQuery(id+"F6.wireOp",EDGE,"E348"),sQuery(id+"F6.wireOp",EDGE,"E349"),sQuery(id+"F6.wireOp",EDGE,"E350"),sQuery(id+"F6.wireOp",EDGE,"E351"),sQuery(id+"F6.wireOp",EDGE,"E352"),sQuery(id+"F6.wireOp",EDGE,"E353"),sQuery(id+"F6.wireOp",EDGE,"E354"),sQuery(id+"F6.wireOp",EDGE,"E355"),sQuery(id+"F6.wireOp",EDGE,"E356"),sQuery(id+"F6.wireOp",EDGE,"E357"),sQuery(id+"F6.wireOp",EDGE,"E358"),sQuery(id+"F6.wireOp",EDGE,"E359"),sQuery(id+"F6.wireOp",EDGE,"E360"),sQuery(id+"F6.wireOp",EDGE,"E361"),sQuery(id+"F6.wireOp",EDGE,"E362"),sQuery(id+"F6.wireOp",EDGE,"E363"),sQuery(id+"F6.wireOp",EDGE,"E364"),sQuery(id+"F6.wireOp",EDGE,"E365"),sQuery(id+"F6.wireOp",EDGE,"E366"),sQuery(id+"F6.wireOp",EDGE,"E367"),sQuery(id+"F6.wireOp",EDGE,"E368"),sQuery(id+"F6.wireOp",EDGE,"E369"),sQuery(id+"F6.wireOp",EDGE,"E370"),sQuery(id+"F6.wireOp",EDGE,"E371"),sQuery(id+"F6.wireOp",EDGE,"E372"),sQuery(id+"F6.wireOp",EDGE,"E373"),sQuery(id+"F6.wireOp",EDGE,"E374"),sQuery(id+"F6.wireOp",EDGE,"E375"),sQuery(id+"F6.wireOp",EDGE,"E376"),sQuery(id+"F6.wireOp",EDGE,"E377"),sQuery(id+"F6.wireOp",EDGE,"E378"),sQuery(id+"F6.wireOp",EDGE,"E379"),sQuery(id+"F6.wireOp",EDGE,"E380"),sQuery(id+"F6.wireOp",EDGE,"E381"),sQuery(id+"F6.wireOp",EDGE,"E382"),sQuery(id+"F6.wireOp",EDGE,"E383"),sQuery(id+"F6.wireOp",EDGE,"E384"),sQuery(id+"F6.wireOp",EDGE,"E385"),sQuery(id+"F6.wireOp",EDGE,"E386"),sQuery(id+"F6.wireOp",EDGE,"E387"),sQuery(id+"F6.wireOp",EDGE,"E388"),sQuery(id+"F6.wireOp",EDGE,"E389"),sQuery(id+"F6.wireOp",EDGE,"E390"),sQuery(id+"F6.wireOp",EDGE,"E391"),sQuery(id+"F6.wireOp",EDGE,"E392"),sQuery(id+"F6.wireOp",EDGE,"E393"),sQuery(id+"F6.wireOp",EDGE,"E394"),sQuery(id+"F6.wireOp",EDGE,"E395"),sQuery(id+"F6.wireOp",EDGE,"E396"),sQuery(id+"F6.wireOp",EDGE,"E397"),sQuery(id+"F6.wireOp",EDGE,"E398"),sQuery(id+"F6.wireOp",EDGE,"E399"),sQuery(id+"F6.wireOp",EDGE,"E400"),sQuery(id+"F6.wireOp",EDGE,"E401"),sQuery(id+"F6.wireOp",EDGE,"E402"),sQuery(id+"F6.wireOp",EDGE,"E403"),sQuery(id+"F6.wireOp",EDGE,"E404"),sQuery(id+"F6.wireOp",EDGE,"E405"),sQuery(id+"F6.wireOp",EDGE,"E406"),sQuery(id+"F6.wireOp",EDGE,"E407"),sQuery(id+"F6.wireOp",EDGE,"E408"),sQuery(id+"F6.wireOp",EDGE,"E409"),sQuery(id+"F6.wireOp",EDGE,"E410"),sQuery(id+"F6.wireOp",EDGE,"E411"),sQuery(id+"F6.wireOp",EDGE,"E412"),sQuery(id+"F6.wireOp",EDGE,"E413"),sQuery(id+"F6.wireOp",EDGE,"E414"),sQuery(id+"F6.wireOp",EDGE,"E415"),sQuery(id+"F6.wireOp",EDGE,"E416"),sQuery(id+"F6.wireOp",EDGE,"E417"),sQuery(id+"F6.wireOp",EDGE,"E418"),sQuery(id+"F6.wireOp",EDGE,"E419"),sQuery(id+"F6.wireOp",EDGE,"E420"),sQuery(id+"F6.wireOp",EDGE,"E421"),sQuery(id+"F6.wireOp",EDGE,"E422"),sQuery(id+"F6.wireOp",EDGE,"E423"),sQuery(id+"F6.wireOp",EDGE,"E424"),sQuery(id+"F6.wireOp",EDGE,"E425"),sQuery(id+"F6.wireOp",EDGE,"E426"),sQuery(id+"F6.wireOp",EDGE,"E427"),sQuery(id+"F6.wireOp",EDGE,"E428"),sQuery(id+"F6.wireOp",EDGE,"E429"),sQuery(id+"F6.wireOp",EDGE,"E430"),sQuery(id+"F6.wireOp",EDGE,"E431"),sQuery(id+"F6.wireOp",EDGE,"E432"),sQuery(id+"F6.wireOp",EDGE,"E433"),sQuery(id+"F6.wireOp",EDGE,"E434"),sQuery(id+"F6.wireOp",EDGE,"E435"),sQuery(id+"F6.wireOp",EDGE,"E436"),sQuery(id+"F6.wireOp",EDGE,"E437"),sQuery(id+"F6.wireOp",EDGE,"E438"),sQuery(id+"F6.wireOp",EDGE,"E439"),sQuery(id+"F6.wireOp",EDGE,"E440"),sQuery(id+"F6.wireOp",EDGE,"E441"),sQuery(id+"F6.wireOp",EDGE,"E442"),sQuery(id+"F6.wireOp",EDGE,"E443"),sQuery(id+"F6.wireOp",EDGE,"E444"),sQuery(id+"F6.wireOp",EDGE,"E445"),sQuery(id+"F6.wireOp",EDGE,"E446"),sQuery(id+"F6.wireOp",EDGE,"E447"),sQuery(id+"F6.wireOp",EDGE,"E448"),sQuery(id+"F6.wireOp",EDGE,"E449"),sQuery(id+"F6.wireOp",EDGE,"E450"),sQuery(id+"F6.wireOp",EDGE,"E451"),sQuery(id+"F6.wireOp",EDGE,"E452"),sQuery(id+"F6.wireOp",EDGE,"E453"),sQuery(id+"F6.wireOp",EDGE,"E454"),sQuery(id+"F6.wireOp",EDGE,"E455"),sQuery(id+"F6.wireOp",EDGE,"E456"),sQuery(id+"F6.wireOp",EDGE,"E457"),sQuery(id+"F6.wireOp",EDGE,"E458"),sQuery(id+"F6.wireOp",EDGE,"E459"),sQuery(id+"F6.wireOp",EDGE,"E460"),sQuery(id+"F6.wireOp",EDGE,"E461"),sQuery(id+"F6.wireOp",EDGE,"E462"),sQuery(id+"F6.wireOp",EDGE,"E463"),sQuery(id+"F6.wireOp",EDGE,"E464"),sQuery(id+"F6.wireOp",EDGE,"E465"),sQuery(id+"F6.wireOp",EDGE,"E466"),sQuery(id+"F6.wireOp",EDGE,"E467"),sQuery(id+"F6.wireOp",EDGE,"E468"),sQuery(id+"F6.wireOp",EDGE,"E469"),sQuery(id+"F6.wireOp",EDGE,"E470"),sQuery(id+"F6.wireOp",EDGE,"E471"),sQuery(id+"F6.wireOp",EDGE,"E472"),sQuery(id+"F6.wireOp",EDGE,"E473"),sQuery(id+"F6.wireOp",EDGE,"E474"),sQuery(id+"F6.wireOp",EDGE,"E475"),sQuery(id+"F6.wireOp",EDGE,"E476"),sQuery(id+"F6.wireOp",EDGE,"E477"),sQuery(id+"F6.wireOp",EDGE,"E478"),sQuery(id+"F6.wireOp",EDGE,"E479"),sQuery(id+"F6.wireOp",EDGE,"E480"),sQuery(id+"F6.wireOp",EDGE,"E481"),sQuery(id+"F6.wireOp",EDGE,"E482"),sQuery(id+"F6.wireOp",EDGE,"E483"),sQuery(id+"F6.wireOp",EDGE,"E484"),sQuery(id+"F6.wireOp",EDGE,"E485"),sQuery(id+"F6.wireOp",EDGE,"E486"),sQuery(id+"F6.wireOp",EDGE,"E487"),sQuery(id+"F6.wireOp",EDGE,"E488"),sQuery(id+"F6.wireOp",EDGE,"E489"),sQuery(id+"F6.wireOp",EDGE,"E490"),sQuery(id+"F6.wireOp",EDGE,"E491"),sQuery(id+"F6.wireOp",EDGE,"E492"),sQuery(id+"F6.wireOp",EDGE,"E493"),sQuery(id+"F6.wireOp",EDGE,"E494"),sQuery(id+"F6.wireOp",EDGE,"E495"),sQuery(id+"F6.wireOp",EDGE,"E496"),sQuery(id+"F6.wireOp",EDGE,"E497"),sQuery(id+"F6.wireOp",EDGE,"E498"),sQuery(id+"F6.wireOp",EDGE,"E499"),sQuery(id+"F6.wireOp",EDGE,"E500"),sQuery(id+"F6.wireOp",EDGE,"E501"),sQuery(id+"F6.wireOp",EDGE,"E502"),sQuery(id+"F6.wireOp",EDGE,"E503"),sQuery(id+"F6.wireOp",EDGE,"E504"),sQuery(id+"F6.wireOp",EDGE,"E505"),sQuery(id+"F6.wireOp",EDGE,"E506"),sQuery(id+"F6.wireOp",EDGE,"E507"),sQuery(id+"F6.wireOp",EDGE,"E508"),sQuery(id+"F6.wireOp",EDGE,"E509"),sQuery(id+"F6.wireOp",EDGE,"E510"),sQuery(id+"F6.wireOp",EDGE,"E511"),sQuery(id+"F6.wireOp",EDGE,"E512"),sQuery(id+"F6.wireOp",EDGE,"E513"),sQuery(id+"F6.wireOp",EDGE,"E514"),sQuery(id+"F6.wireOp",EDGE,"E515"),sQuery(id+"F6.wireOp",EDGE,"E516"),sQuery(id+"F6.wireOp",EDGE,"E517"),sQuery(id+"F6.wireOp",EDGE,"E518"),sQuery(id+"F6.wireOp",EDGE,"E519"),sQuery(id+"F6.wireOp",EDGE,"E520"),sQuery(id+"F6.wireOp",EDGE,"E521"),sQuery(id+"F6.wireOp",EDGE,"E522"),sQuery(id+"F6.wireOp",EDGE,"E523"),sQuery(id+"F6.wireOp",EDGE,"E524"),sQuery(id+"F6.wireOp",EDGE,"E525"),sQuery(id+"F6.wireOp",EDGE,"E526"),sQuery(id+"F6.wireOp",EDGE,"E527"),sQuery(id+"F6.wireOp",EDGE,"E528"),sQuery(id+"F6.wireOp",EDGE,"E529"),sQuery(id+"F6.wireOp",EDGE,"E530"),sQuery(id+"F6.wireOp",EDGE,"E531"),sQuery(id+"F6.wireOp",EDGE,"E532"),sQuery(id+"F6.wireOp",EDGE,"E533"),sQuery(id+"F6.wireOp",EDGE,"E534"),sQuery(id+"F6.wireOp",EDGE,"E535"),sQuery(id+"F6.wireOp",EDGE,"E536"),sQuery(id+"F6.wireOp",EDGE,"E537"),sQuery(id+"F6.wireOp",EDGE,"E538"),sQuery(id+"F6.wireOp",EDGE,"E539"),sQuery(id+"F6.wireOp",EDGE,"E540"),sQuery(id+"F6.wireOp",EDGE,"E541"),sQuery(id+"F6.wireOp",EDGE,"E542"),sQuery(id+"F6.wireOp",EDGE,"E543"),sQuery(id+"F6.wireOp",EDGE,"E544"),sQuery(id+"F6.wireOp",EDGE,"E545"),sQuery(id+"F6.wireOp",EDGE,"E546"),sQuery(id+"F6.wireOp",EDGE,"E547"),sQuery(id+"F6.wireOp",EDGE,"E548"),sQuery(id+"F6.wireOp",EDGE,"E549"),sQuery(id+"F6.wireOp",EDGE,"E550"),sQuery(id+"F6.wireOp",EDGE,"E551"),sQuery(id+"F6.wireOp",EDGE,"E552"),sQuery(id+"F6.wireOp",EDGE,"E553"),sQuery(id+"F6.wireOp",EDGE,"E554"),sQuery(id+"F6.wireOp",EDGE,"E555"),sQuery(id+"F6.wireOp",EDGE,"E556"),sQuery(id+"F6.wireOp",EDGE,"E557"),sQuery(id+"F6.wireOp",EDGE,"E558"),sQuery(id+"F6.wireOp",EDGE,"E559"),sQuery(id+"F6.wireOp",EDGE,"E560"),sQuery(id+"F6.wireOp",EDGE,"E561"),sQuery(id+"F6.wireOp",EDGE,"E562"),sQuery(id+"F6.wireOp",EDGE,"E563"),sQuery(id+"F6.wireOp",EDGE,"E564"),sQuery(id+"F6.wireOp",EDGE,"E565"),sQuery(id+"F6.wireOp",EDGE,"E566"),sQuery(id+"F6.wireOp",EDGE,"E567"),sQuery(id+"F6.wireOp",EDGE,"E568"),sQuery(id+"F6.wireOp",EDGE,"E569"),sQuery(id+"F6.wireOp",EDGE,"E570"),sQuery(id+"F6.wireOp",EDGE,"E571"),sQuery(id+"F6.wireOp",EDGE,"E572"),sQuery(id+"F6.wireOp",EDGE,"E573"),sQuery(id+"F6.wireOp",EDGE,"E574"),sQuery(id+"F6.wireOp",EDGE,"E575"),sQuery(id+"F6.wireOp",EDGE,"E576"),sQuery(id+"F6.wireOp",EDGE,"E577"),sQuery(id+"F6.wireOp",EDGE,"E578"),sQuery(id+"F6.wireOp",EDGE,"E579"),sQuery(id+"F6.wireOp",EDGE,"E580"),sQuery(id+"F6.wireOp",EDGE,"E581"),sQuery(id+"F6.wireOp",EDGE,"E582"),sQuery(id+"F6.wireOp",EDGE,"E583"),sQuery(id+"F6.wireOp",EDGE,"E584"),sQuery(id+"F6.wireOp",EDGE,"E585"),sQuery(id+"F6.wireOp",EDGE,"E586"),sQuery(id+"F6.wireOp",EDGE,"E587"),sQuery(id+"F6.wireOp",EDGE,"E588"),sQuery(id+"F6.wireOp",EDGE,"E589"),sQuery(id+"F6.wireOp",EDGE,"E590"),sQuery(id+"F6.wireOp",EDGE,"E591"),sQuery(id+"F6.wireOp",EDGE,"E592"),sQuery(id+"F6.wireOp",EDGE,"E593"),sQuery(id+"F6.wireOp",EDGE,"E594"),sQuery(id+"F6.wireOp",EDGE,"E595"),sQuery(id+"F6.wireOp",EDGE,"E596"),sQuery(id+"F6.wireOp",EDGE,"E597"),sQuery(id+"F6.wireOp",EDGE,"E598"),sQuery(id+"F6.wireOp",EDGE,"E599"),sQuery(id+"F6.wireOp",EDGE,"E600"),sQuery(id+"F6.wireOp",EDGE,"E601"),sQuery(id+"F6.wireOp",EDGE,"E602"),sQuery(id+"F6.wireOp",EDGE,"E603"),sQuery(id+"F6.wireOp",EDGE,"E604"),sQuery(id+"F6.wireOp",EDGE,"E605"),sQuery(id+"F6.wireOp",EDGE,"E606"),sQuery(id+"F6.wireOp",EDGE,"E607"),sQuery(id+"F6.wireOp",EDGE,"E608"),sQuery(id+"F6.wireOp",EDGE,"E609"),sQuery(id+"F6.wireOp",EDGE,"E610"),sQuery(id+"F6.wireOp",EDGE,"E611"),sQuery(id+"F6.wireOp",EDGE,"E612"),sQuery(id+"F6.wireOp",EDGE,"E613"),sQuery(id+"F6.wireOp",EDGE,"E614"),sQuery(id+"F6.wireOp",EDGE,"E615"),sQuery(id+"F6.wireOp",EDGE,"E616"),sQuery(id+"F6.wireOp",EDGE,"E617"),sQuery(id+"F6.wireOp",EDGE,"E618"),sQuery(id+"F6.wireOp",EDGE,"E619"),sQuery(id+"F6.wireOp",EDGE,"E620"),sQuery(id+"F6.wireOp",EDGE,"E621"),sQuery(id+"F6.wireOp",EDGE,"E622"),sQuery(id+"F6.wireOp",EDGE,"E623"),sQuery(id+"F6.wireOp",EDGE,"E624"),sQuery(id+"F6.wireOp",EDGE,"E625"),sQuery(id+"F6.wireOp",EDGE,"E626"),sQuery(id+"F6.wireOp",EDGE,"E627"),sQuery(id+"F6.wireOp",EDGE,"E628"),sQuery(id+"F6.wireOp",EDGE,"E629"),sQuery(id+"F6.wireOp",EDGE,"E630"),sQuery(id+"F6.wireOp",EDGE,"E631"),sQuery(id+"F6.wireOp",EDGE,"E632"),sQuery(id+"F6.wireOp",EDGE,"E633"),sQuery(id+"F6.wireOp",EDGE,"E634"),sQuery(id+"F6.wireOp",EDGE,"E635"),sQuery(id+"F6.wireOp",EDGE,"E636"),sQuery(id+"F6.wireOp",EDGE,"E637"),sQuery(id+"F6.wireOp",EDGE,"E638"),sQuery(id+"F6.wireOp",EDGE,"E639"),sQuery(id+"F6.wireOp",EDGE,"E640"),sQuery(id+"F6.wireOp",EDGE,"E641"),sQuery(id+"F6.wireOp",EDGE,"E642"),sQuery(id+"F6.wireOp",EDGE,"E643"),sQuery(id+"F6.wireOp",EDGE,"E644"),sQuery(id+"F6.wireOp",EDGE,"E645"),sQuery(id+"F6.wireOp",EDGE,"E646"),sQuery(id+"F6.wireOp",EDGE,"E647"),sQuery(id+"F6.wireOp",EDGE,"E648"),sQuery(id+"F6.wireOp",EDGE,"E649"),sQuery(id+"F6.wireOp",EDGE,"E650"),sQuery(id+"F6.wireOp",EDGE,"E651"),sQuery(id+"F6.wireOp",EDGE,"E652"),sQuery(id+"F6.wireOp",EDGE,"E653"),sQuery(id+"F6.wireOp",EDGE,"E654"),sQuery(id+"F6.wireOp",EDGE,"E655"),sQuery(id+"F6.wireOp",EDGE,"E656"),sQuery(id+"F6.wireOp",EDGE,"E657"),sQuery(id+"F6.wireOp",EDGE,"E658"),sQuery(id+"F6.wireOp",EDGE,"E659"),sQuery(id+"F6.wireOp",EDGE,"E660"),sQuery(id+"F6.wireOp",EDGE,"E661"),sQuery(id+"F6.wireOp",EDGE,"E662"),sQuery(id+"F6.wireOp",EDGE,"E663"),sQuery(id+"F6.wireOp",EDGE,"E664"),sQuery(id+"F6.wireOp",EDGE,"E665"),sQuery(id+"F6.wireOp",EDGE,"E666"),sQuery(id+"F6.wireOp",EDGE,"E667"),sQuery(id+"F6.wireOp",EDGE,"E668"),sQuery(id+"F6.wireOp",EDGE,"E669"),sQuery(id+"F6.wireOp",EDGE,"E670"),sQuery(id+"F6.wireOp",EDGE,"E671"),sQuery(id+"F6.wireOp",EDGE,"E672"),sQuery(id+"F6.wireOp",EDGE,"E673"),sQuery(id+"F6.wireOp",EDGE,"E674"),sQuery(id+"F6.wireOp",EDGE,"E675"),sQuery(id+"F6.wireOp",EDGE,"E676"),sQuery(id+"F6.wireOp",EDGE,"E677"),sQuery(id+"F6.wireOp",EDGE,"E678"),sQuery(id+"F6.wireOp",EDGE,"E679"),sQuery(id+"F6.wireOp",EDGE,"E680"),sQuery(id+"F6.wireOp",EDGE,"E681"),sQuery(id+"F6.wireOp",EDGE,"E682"),sQuery(id+"F6.wireOp",EDGE,"E683"),sQuery(id+"F6.wireOp",EDGE,"E684"),sQuery(id+"F6.wireOp",EDGE,"E685"),sQuery(id+"F6.wireOp",EDGE,"E686"),sQuery(id+"F6.wireOp",EDGE,"E687"),sQuery(id+"F6.wireOp",EDGE,"E688"),sQuery(id+"F6.wireOp",EDGE,"E689"),sQuery(id+"F6.wireOp",EDGE,"E690"),sQuery(id+"F6.wireOp",EDGE,"E691"),sQuery(id+"F6.wireOp",EDGE,"E692"),sQuery(id+"F6.wireOp",EDGE,"E693"),sQuery(id+"F6.wireOp",EDGE,"E694"),sQuery(id+"F6.wireOp",EDGE,"E695"),sQuery(id+"F6.wireOp",EDGE,"E696"),sQuery(id+"F6.wireOp",EDGE,"E697"),sQuery(id+"F6.wireOp",EDGE,"E698"),sQuery(id+"F6.wireOp",EDGE,"E699"),sQuery(id+"F6.wireOp",EDGE,"E700"),sQuery(id+"F6.wireOp",EDGE,"E701"),sQuery(id+"F6.wireOp",EDGE,"E702"),sQuery(id+"F6.wireOp",EDGE,"E703"),sQuery(id+"F6.wireOp",EDGE,"E704"),sQuery(id+"F6.wireOp",EDGE,"E705"),sQuery(id+"F6.wireOp",EDGE,"E706"),sQuery(id+"F6.wireOp",EDGE,"E707"),sQuery(id+"F6.wireOp",EDGE,"E708"),sQuery(id+"F6.wireOp",EDGE,"E709"),sQuery(id+"F6.wireOp",EDGE,"E710"),sQuery(id+"F6.wireOp",EDGE,"E711"),sQuery(id+"F6.wireOp",EDGE,"E712"),sQuery(id+"F6.wireOp",EDGE,"E713"),sQuery(id+"F6.wireOp",EDGE,"E714"),sQuery(id+"F6.wireOp",EDGE,"E715"),sQuery(id+"F6.wireOp",EDGE,"E716"),sQuery(id+"F6.wireOp",EDGE,"E717"),sQuery(id+"F6.wireOp",EDGE,"E718"),sQuery(id+"F6.wireOp",EDGE,"E719"),sQuery(id+"F6.wireOp",EDGE,"E720"),sQuery(id+"F6.wireOp",EDGE,"E721"),sQuery(id+"F6.wireOp",EDGE,"E722"),sQuery(id+"F6.wireOp",EDGE,"E723"),sQuery(id+"F6.wireOp",EDGE,"E724"),sQuery(id+"F6.wireOp",EDGE,"E725"),sQuery(id+"F6.wireOp",EDGE,"E726"),sQuery(id+"F6.wireOp",EDGE,"E727"),sQuery(id+"F6.wireOp",EDGE,"E728"),sQuery(id+"F6.wireOp",EDGE,"E729"),sQuery(id+"F6.wireOp",EDGE,"E730"),sQuery(id+"F6.wireOp",EDGE,"E731"),sQuery(id+"F6.wireOp",EDGE,"E732"),sQuery(id+"F6.wireOp",EDGE,"E733"),sQuery(id+"F6.wireOp",EDGE,"E734"),sQuery(id+"F6.wireOp",EDGE,"E735"),sQuery(id+"F6.wireOp",EDGE,"E736"),sQuery(id+"F6.wireOp",EDGE,"E737"),sQuery(id+"F6.wireOp",EDGE,"E738"),sQuery(id+"F6.wireOp",EDGE,"E739"),sQuery(id+"F6.wireOp",EDGE,"E740"),sQuery(id+"F6.wireOp",EDGE,"E741"),sQuery(id+"F6.wireOp",EDGE,"E742"),sQuery(id+"F6.wireOp",EDGE,"E743"),sQuery(id+"F6.wireOp",EDGE,"E744"),sQuery(id+"F6.wireOp",EDGE,"E745"),sQuery(id+"F6.wireOp",EDGE,"E746"),sQuery(id+"F6.wireOp",EDGE,"E747"),sQuery(id+"F6.wireOp",EDGE,"E748"),sQuery(id+"F6.wireOp",EDGE,"E749"),sQuery(id+"F6.wireOp",EDGE,"E750"),sQuery(id+"F6.wireOp",EDGE,"E751"),sQuery(id+"F6.wireOp",EDGE,"E752"),sQuery(id+"F6.wireOp",EDGE,"E753"),sQuery(id+"F6.wireOp",EDGE,"E754"),sQuery(id+"F6.wireOp",EDGE,"E755"),sQuery(id+"F6.wireOp",EDGE,"E756"),sQuery(id+"F6.wireOp",EDGE,"E757"),sQuery(id+"F6.wireOp",EDGE,"E758"),sQuery(id+"F6.wireOp",EDGE,"E759"),sQuery(id+"F6.wireOp",EDGE,"E760"),sQuery(id+"F6.wireOp",EDGE,"E761"),sQuery(id+"F6.wireOp",EDGE,"E762"),sQuery(id+"F6.wireOp",EDGE,"E763"),sQuery(id+"F6.wireOp",EDGE,"E764"),sQuery(id+"F6.wireOp",EDGE,"E765"),sQuery(id+"F6.wireOp",EDGE,"E766"),sQuery(id+"F6.wireOp",EDGE,"E767"),sQuery(id+"F6.wireOp",EDGE,"E768"),sQuery(id+"F6.wireOp",EDGE,"E769"),sQuery(id+"F6.wireOp",EDGE,"E770"),sQuery(id+"F6.wireOp",EDGE,"E771"),sQuery(id+"F6.wireOp",EDGE,"E772"),sQuery(id+"F6.wireOp",EDGE,"E773"),sQuery(id+"F6.wireOp",EDGE,"E774"),sQuery(id+"F6.wireOp",EDGE,"E775"),sQuery(id+"F6.wireOp",EDGE,"E776"),sQuery(id+"F6.wireOp",EDGE,"E777"),sQuery(id+"F6.wireOp",EDGE,"E778"),sQuery(id+"F6.wireOp",EDGE,"E779"),sQuery(id+"F6.wireOp",EDGE,"E780"),sQuery(id+"F6.wireOp",EDGE,"E781"),sQuery(id+"F6.wireOp",EDGE,"E782"),sQuery(id+"F6.wireOp",EDGE,"E783"),sQuery(id+"F6.wireOp",EDGE,"E784"),sQuery(id+"F6.wireOp",EDGE,"E785"),sQuery(id+"F6.wireOp",EDGE,"E786"),sQuery(id+"F6.wireOp",EDGE,"E787"),sQuery(id+"F6.wireOp",EDGE,"E788"),sQuery(id+"F6.wireOp",EDGE,"E789"),sQuery(id+"F6.wireOp",EDGE,"E790"),sQuery(id+"F6.wireOp",EDGE,"E791"),sQuery(id+"F6.wireOp",EDGE,"E792"),sQuery(id+"F6.wireOp",EDGE,"E793"),sQuery(id+"F6.wireOp",EDGE,"E794"),sQuery(id+"F6.wireOp",EDGE,"E795"),sQuery(id+"F6.wireOp",EDGE,"E796"),sQuery(id+"F6.wireOp",EDGE,"E797"),sQuery(id+"F6.wireOp",EDGE,"E798"),sQuery(id+"F6.wireOp",EDGE,"E799"),sQuery(id+"F6.wireOp",EDGE,"E800"),sQuery(id+"F6.wireOp",EDGE,"E801"),sQuery(id+"F6.wireOp",EDGE,"E802"),sQuery(id+"F6.wireOp",EDGE,"E803"),sQuery(id+"F6.wireOp",EDGE,"E804"),sQuery(id+"F6.wireOp",EDGE,"E805"),sQuery(id+"F6.wireOp",EDGE,"E806"),sQuery(id+"F6.wireOp",EDGE,"E807"),sQuery(id+"F6.wireOp",EDGE,"E808"),sQuery(id+"F6.wireOp",EDGE,"E809"),sQuery(id+"F6.wireOp",EDGE,"E810"),sQuery(id+"F6.wireOp",EDGE,"E811"),sQuery(id+"F6.wireOp",EDGE,"E812"),sQuery(id+"F6.wireOp",EDGE,"E813"),sQuery(id+"F6.wireOp",EDGE,"E814"),sQuery(id+"F6.wireOp",EDGE,"E815"),sQuery(id+"F6.wireOp",EDGE,"E816"),sQuery(id+"F6.wireOp",EDGE,"E817"),sQuery(id+"F6.wireOp",EDGE,"E818"),sQuery(id+"F6.wireOp",EDGE,"E819"),sQuery(id+"F6.wireOp",EDGE,"E820"),sQuery(id+"F6.wireOp",EDGE,"E821"),sQuery(id+"F6.wireOp",EDGE,"E822"),sQuery(id+"F6.wireOp",EDGE,"E823"),sQuery(id+"F6.wireOp",EDGE,"E824"),sQuery(id+"F6.wireOp",EDGE,"E825"),sQuery(id+"F6.wireOp",EDGE,"E826"),sQuery(id+"F6.wireOp",EDGE,"E827"),sQuery(id+"F6.wireOp",EDGE,"E828"),sQuery(id+"F6.wireOp",EDGE,"E829"),sQuery(id+"F6.wireOp",EDGE,"E830"),sQuery(id+"F6.wireOp",EDGE,"E831"),sQuery(id+"F6.wireOp",EDGE,"E832"),sQuery(id+"F6.wireOp",EDGE,"E833"),sQuery(id+"F6.wireOp",EDGE,"E834"),sQuery(id+"F6.wireOp",EDGE,"E835"),sQuery(id+"F6.wireOp",EDGE,"E836"),sQuery(id+"F6.wireOp",EDGE,"E837"),sQuery(id+"F6.wireOp",EDGE,"E838"),sQuery(id+"F6.wireOp",EDGE,"E839"),sQuery(id+"F6.wireOp",EDGE,"E840"),sQuery(id+"F6.wireOp",EDGE,"E841"),sQuery(id+"F6.wireOp",EDGE,"E842"),sQuery(id+"F6.wireOp",EDGE,"E843"),sQuery(id+"F6.wireOp",EDGE,"E844"),sQuery(id+"F6.wireOp",EDGE,"E845"),sQuery(id+"F6.wireOp",EDGE,"E846"),sQuery(id+"F6.wireOp",EDGE,"E847"),sQuery(id+"F6.wireOp",EDGE,"E848"),sQuery(id+"F6.wireOp",EDGE,"E849"),sQuery(id+"F6.wireOp",EDGE,"E850"),sQuery(id+"F6.wireOp",EDGE,"E851"),sQuery(id+"F6.wireOp",EDGE,"E852"),sQuery(id+"F6.wireOp",EDGE,"E853"),sQuery(id+"F6.wireOp",EDGE,"E854"),sQuery(id+"F6.wireOp",EDGE,"E855"),sQuery(id+"F6.wireOp",EDGE,"E856"),sQuery(id+"F6.wireOp",EDGE,"E857"),sQuery(id+"F6.wireOp",EDGE,"E858"),sQuery(id+"F6.wireOp",EDGE,"E859"),sQuery(id+"F6.wireOp",EDGE,"E860"),sQuery(id+"F6.wireOp",EDGE,"E861"),sQuery(id+"F6.wireOp",EDGE,"E862"),sQuery(id+"F6.wireOp",EDGE,"E863"),sQuery(id+"F6.wireOp",EDGE,"E864"),sQuery(id+"F6.wireOp",EDGE,"E865"),sQuery(id+"F6.wireOp",EDGE,"E866"),sQuery(id+"F6.wireOp",EDGE,"E867"),sQuery(id+"F6.wireOp",EDGE,"E868"),sQuery(id+"F6.wireOp",EDGE,"E869"),sQuery(id+"F6.wireOp",EDGE,"E870"),sQuery(id+"F6.wireOp",EDGE,"E871"),sQuery(id+"F6.wireOp",EDGE,"E872"),sQuery(id+"F6.wireOp",EDGE,"E873"),sQuery(id+"F6.wireOp",EDGE,"E874"),sQuery(id+"F6.wireOp",EDGE,"E875"),sQuery(id+"F6.wireOp",EDGE,"E876"),sQuery(id+"F6.wireOp",EDGE,"E877"),sQuery(id+"F6.wireOp",EDGE,"E878"),sQuery(id+"F6.wireOp",EDGE,"E879"),sQuery(id+"F6.wireOp",EDGE,"E880"),sQuery(id+"F6.wireOp",EDGE,"E881"),sQuery(id+"F6.wireOp",EDGE,"E882"),sQuery(id+"F6.wireOp",EDGE,"E883"),sQuery(id+"F6.wireOp",EDGE,"E884"),sQuery(id+"F6.wireOp",EDGE,"E885"),sQuery(id+"F6.wireOp",EDGE,"E886"),sQuery(id+"F6.wireOp",EDGE,"E887"),sQuery(id+"F6.wireOp",EDGE,"E888"),sQuery(id+"F6.wireOp",EDGE,"E889"),sQuery(id+"F6.wireOp",EDGE,"E890"),sQuery(id+"F6.wireOp",EDGE,"E891"),sQuery(id+"F6.wireOp",EDGE,"E892"),sQuery(id+"F6.wireOp",EDGE,"E893"),sQuery(id+"F6.wireOp",EDGE,"E894"),sQuery(id+"F6.wireOp",EDGE,"E895"),sQuery(id+"F6.wireOp",EDGE,"E896"),sQuery(id+"F6.wireOp",EDGE,"E897"),sQuery(id+"F6.wireOp",EDGE,"E898"),sQuery(id+"F6.wireOp",EDGE,"E899"),sQuery(id+"F6.wireOp",EDGE,"E900"),sQuery(id+"F6.wireOp",EDGE,"E901"),sQuery(id+"F6.wireOp",EDGE,"E902"),sQuery(id+"F6.wireOp",EDGE,"E903"),sQuery(id+"F6.wireOp",EDGE,"E904"),sQuery(id+"F6.wireOp",EDGE,"E905"),sQuery(id+"F6.wireOp",EDGE,"E906"),sQuery(id+"F6.wireOp",EDGE,"E907"),sQuery(id+"F6.wireOp",EDGE,"E908"),sQuery(id+"F6.wireOp",EDGE,"E909"),sQuery(id+"F6.wireOp",EDGE,"E910"),sQuery(id+"F6.wireOp",EDGE,"E911"),sQuery(id+"F6.wireOp",EDGE,"E911"),sQuery(id+"F6.wireOp",EDGE,"E912"),sQuery(id+"F6.wireOp",EDGE,"E913"),sQuery(id+"F6.wireOp",EDGE,"E914"),sQuery(id+"F6.wireOp",EDGE,"E915"),sQuery(id+"F6.wireOp",EDGE,"E916"),sQuery(id+"F6.wireOp",EDGE,"E917"),sQuery(id+"F6.wireOp",EDGE,"E918"),sQuery(id+"F6.wireOp",EDGE,"E919"),sQuery(id+"F6.wireOp",EDGE,"E920"),sQuery(id+"F6.wireOp",EDGE,"E921"),sQuery(id+"F6.wireOp",EDGE,"E922"),sQuery(id+"F6.wireOp",EDGE,"E923"),sQuery(id+"F6.wireOp",EDGE,"E924"),sQuery(id+"F6.wireOp",EDGE,"E925"),sQuery(id+"F6.wireOp",EDGE,"E926"),sQuery(id+"F6.wireOp",EDGE,"E927"),sQuery(id+"F6.wireOp",EDGE,"E928"),sQuery(id+"F6.wireOp",EDGE,"E929"),sQuery(id+"F6.wireOp",EDGE,"E930"),sQuery(id+"F6.wireOp",EDGE,"E931"),sQuery(id+"F6.wireOp",EDGE,"E932"),sQuery(id+"F6.wireOp",EDGE,"E933"),sQuery(id+"F6.wireOp",EDGE,"E934"),sQuery(id+"F6.wireOp",EDGE,"E935"),sQuery(id+"F6.wireOp",EDGE,"E936"),sQuery(id+"F6.wireOp",EDGE,"E937"),sQuery(id+"F6.wireOp",EDGE,"E938"),sQuery(id+"F6.wireOp",EDGE,"E939"),sQuery(id+"F6.wireOp",EDGE,"E940"),sQuery(id+"F6.wireOp",EDGE,"E941"),sQuery(id+"F6.wireOp",EDGE,"E942"),sQuery(id+"F6.wireOp",EDGE,"E943"),sQuery(id+"F6.wireOp",EDGE,"E944"),sQuery(id+"F6.wireOp",EDGE,"E945"),sQuery(id+"F6.wireOp",EDGE,"E946"),sQuery(id+"F6.wireOp",EDGE,"E947"),sQuery(id+"F6.wireOp",EDGE,"E948"),sQuery(id+"F6.wireOp",EDGE,"E949"),sQuery(id+"F6.wireOp",EDGE,"E950"),sQuery(id+"F6.wireOp",EDGE,"E951"),sQuery(id+"F6.wireOp",EDGE,"E952"),sQuery(id+"F6.wireOp",EDGE,"E953"),sQuery(id+"F6.wireOp",EDGE,"E954"),sQuery(id+"F6.wireOp",EDGE,"E955"),sQuery(id+"F6.wireOp",EDGE,"E956"),sQuery(id+"F6.wireOp",EDGE,"E957"),sQuery(id+"F6.wireOp",EDGE,"E958"),sQuery(id+"F6.wireOp",EDGE,"E959"),sQuery(id+"F6.wireOp",EDGE,"E960"),sQuery(id+"F6.wireOp",EDGE,"E961"),sQuery(id+"F6.wireOp",EDGE,"E962"),sQuery(id+"F6.wireOp",EDGE,"E963"),sQuery(id+"F6.wireOp",EDGE,"E964"),sQuery(id+"F6.wireOp",EDGE,"E965"),sQuery(id+"F6.wireOp",EDGE,"E966"),sQuery(id+"F6.wireOp",EDGE,"E967"),sQuery(id+"F6.wireOp",EDGE,"E968"),sQuery(id+"F6.wireOp",EDGE,"E969"),sQuery(id+"F6.wireOp",EDGE,"E970"),sQuery(id+"F6.wireOp",EDGE,"E971"),sQuery(id+"F6.wireOp",EDGE,"E972"),sQuery(id+"F6.wireOp",EDGE,"E973"),sQuery(id+"F6.wireOp",EDGE,"E974"),sQuery(id+"F6.wireOp",EDGE,"E975"),sQuery(id+"F6.wireOp",EDGE,"E976"),sQuery(id+"F6.wireOp",EDGE,"E977"),sQuery(id+"F6.wireOp",EDGE,"E978"),sQuery(id+"F6.wireOp",EDGE,"E979"),sQuery(id+"F6.wireOp",EDGE,"E980"),sQuery(id+"F6.wireOp",EDGE,"E981"),sQuery(id+"F6.wireOp",EDGE,"E982"),sQuery(id+"F6.wireOp",EDGE,"E983"),sQuery(id+"F6.wireOp",EDGE,"E984"),sQuery(id+"F6.wireOp",EDGE,"E985"),sQuery(id+"F6.wireOp",EDGE,"E986"),sQuery(id+"F6.wireOp",EDGE,"E987"),sQuery(id+"F6.wireOp",EDGE,"E988"),sQuery(id+"F6.wireOp",EDGE,"E989"),sQuery(id+"F6.wireOp",EDGE,"E990"),sQuery(id+"F6.wireOp",EDGE,"E991"),sQuery(id+"F6.wireOp",EDGE,"E992"),sQuery(id+"F6.wireOp",EDGE,"E993"),sQuery(id+"F6.wireOp",EDGE,"E994"),sQuery(id+"F6.wireOp",EDGE,"E995"),sQuery(id+"F6.wireOp",EDGE,"E996"),sQuery(id+"F6.wireOp",EDGE,"E997"),sQuery(id+"F6.wireOp",EDGE,"E998"),sQuery(id+"F6.wireOp",EDGE,"E999"),sQuery(id+"F6.wireOp",EDGE,"E1000"),sQuery(id+"F6.wireOp",EDGE,"E1001"),sQuery(id+"F6.wireOp",EDGE,"E1002"),sQuery(id+"F6.wireOp",EDGE,"E1003"),sQuery(id+"F6.wireOp",EDGE,"E1004"),sQuery(id+"F6.wireOp",EDGE,"E1005"),sQuery(id+"F6.wireOp",EDGE,"E1006"),sQuery(id+"F6.wireOp",EDGE,"E1007"),sQuery(id+"F6.wireOp",EDGE,"E1008"),sQuery(id+"F6.wireOp",EDGE,"E1009"),sQuery(id+"F6.wireOp",EDGE,"E1010"),sQuery(id+"F6.wireOp",EDGE,"E1011"),sQuery(id+"F6.wireOp",EDGE,"E1012"),sQuery(id+"F6.wireOp",EDGE,"E1013"),sQuery(id+"F6.wireOp",EDGE,"E1014"),sQuery(id+"F6.wireOp",EDGE,"E1015"),sQuery(id+"F6.wireOp",EDGE,"E1016"),sQuery(id+"F6.wireOp",EDGE,"E1017"),sQuery(id+"F6.wireOp",EDGE,"E1018"),sQuery(id+"F6.wireOp",EDGE,"E1019"),sQuery(id+"F6.wireOp",EDGE,"E1020"),sQuery(id+"F6.wireOp",EDGE,"E1021"),sQuery(id+"F6.wireOp",EDGE,"E1022"),sQuery(id+"F6.wireOp",EDGE,"E1023"),sQuery(id+"F6.wireOp",EDGE,"E1024"),sQuery(id+"F6.wireOp",EDGE,"E1025"),sQuery(id+"F6.wireOp",EDGE,"E1026"),sQuery(id+"F6.wireOp",EDGE,"E1027"),sQuery(id+"F6.wireOp",EDGE,"E1028"),sQuery(id+"F6.wireOp",EDGE,"E1029"),sQuery(id+"F6.wireOp",EDGE,"E1030"),sQuery(id+"F6.wireOp",EDGE,"E1031"),sQuery(id+"F6.wireOp",EDGE,"E1032"),sQuery(id+"F6.wireOp",EDGE,"E1033"),sQuery(id+"F6.wireOp",EDGE,"E1034"),sQuery(id+"F6.wireOp",EDGE,"E1035"),sQuery(id+"F6.wireOp",EDGE,"E1036"),sQuery(id+"F6.wireOp",EDGE,"E1037"),sQuery(id+"F6.wireOp",EDGE,"E1038"),sQuery(id+"F6.wireOp",EDGE,"E1039"),sQuery(id+"F6.wireOp",EDGE,"E1040"),sQuery(id+"F6.wireOp",EDGE,"E1041"),sQuery(id+"F6.wireOp",EDGE,"E1042"),sQuery(id+"F6.wireOp",EDGE,"E1043"),sQuery(id+"F6.wireOp",EDGE,"E1044"),sQuery(id+"F6.wireOp",EDGE,"E1045"),sQuery(id+"F6.wireOp",EDGE,"E1046"),sQuery(id+"F6.wireOp",EDGE,"E1047"),sQuery(id+"F6.wireOp",EDGE,"E1048"),sQuery(id+"F6.wireOp",EDGE,"E1049"),sQuery(id+"F6.wireOp",EDGE,"E1050"),sQuery(id+"F6.wireOp",EDGE,"E1051"),sQuery(id+"F6.wireOp",EDGE,"E1052"),sQuery(id+"F6.wireOp",EDGE,"E1053"),sQuery(id+"F6.wireOp",EDGE,"E1054"),sQuery(id+"F6.wireOp",EDGE,"E1055"),sQuery(id+"F6.wireOp",EDGE,"E1056"),sQuery(id+"F6.wireOp",EDGE,"E1057"),sQuery(id+"F6.wireOp",EDGE,"E1058"),sQuery(id+"F6.wireOp",EDGE,"E1059"),sQuery(id+"F6.wireOp",EDGE,"E1060"),sQuery(id+"F6.wireOp",EDGE,"E1061"),sQuery(id+"F6.wireOp",EDGE,"E1062"),sQuery(id+"F6.wireOp",EDGE,"E1063"),sQuery(id+"F6.wireOp",EDGE,"E1064"),sQuery(id+"F6.wireOp",EDGE,"E1065"),sQuery(id+"F6.wireOp",EDGE,"E1066"),sQuery(id+"F6.wireOp",EDGE,"E1067"),sQuery(id+"F6.wireOp",EDGE,"E1068"),sQuery(id+"F6.wireOp",EDGE,"E1069"),sQuery(id+"F6.wireOp",EDGE,"E1070"),sQuery(id+"F6.wireOp",EDGE,"E1071"),sQuery(id+"F6.wireOp",EDGE,"E1072"),sQuery(id+"F6.wireOp",EDGE,"E1073"),sQuery(id+"F6.wireOp",EDGE,"E1074"),sQuery(id+"F6.wireOp",EDGE,"E1075"),sQuery(id+"F6.wireOp",EDGE,"E1076"),sQuery(id+"F6.wireOp",EDGE,"E1077"),sQuery(id+"F6.wireOp",EDGE,"E1078"),sQuery(id+"F6.wireOp",EDGE,"E1079"),sQuery(id+"F6.wireOp",EDGE,"E1080"),sQuery(id+"F6.wireOp",EDGE,"E1081"),sQuery(id+"F6.wireOp",EDGE,"E1082"),sQuery(id+"F6.wireOp",EDGE,"E1083"),sQuery(id+"F6.wireOp",EDGE,"E1084"),sQuery(id+"F6.wireOp",EDGE,"E1085"),sQuery(id+"F6.wireOp",EDGE,"E1086"),sQuery(id+"F6.wireOp",EDGE,"E1087"),sQuery(id+"F6.wireOp",EDGE,"E1088"),sQuery(id+"F6.wireOp",EDGE,"E1089"),sQuery(id+"F6.wireOp",EDGE,"E1090"),sQuery(id+"F6.wireOp",EDGE,"E1091"),sQuery(id+"F6.wireOp",EDGE,"E1092"),sQuery(id+"F6.wireOp",EDGE,"E1093"),sQuery(id+"F6.wireOp",EDGE,"E1094"),sQuery(id+"F6.wireOp",EDGE,"E1095"),sQuery(id+"F6.wireOp",EDGE,"E1096"),sQuery(id+"F6.wireOp",EDGE,"E1097"),sQuery(id+"F6.wireOp",EDGE,"E1098"),sQuery(id+"F6.wireOp",EDGE,"E1099"),sQuery(id+"F6.wireOp",EDGE,"E1100"),sQuery(id+"F6.wireOp",EDGE,"E1101"),sQuery(id+"F6.wireOp",EDGE,"E1102"),sQuery(id+"F6.wireOp",EDGE,"E1103"),sQuery(id+"F6.wireOp",EDGE,"E1104"),sQuery(id+"F6.wireOp",EDGE,"E1105"),sQuery(id+"F6.wireOp",EDGE,"E1106"),sQuery(id+"F6.wireOp",EDGE,"E1107"),sQuery(id+"F6.wireOp",EDGE,"E1108"),sQuery(id+"F6.wireOp",EDGE,"E1109"),sQuery(id+"F6.wireOp",EDGE,"E1110"),sQuery(id+"F6.wireOp",EDGE,"E1111"),sQuery(id+"F6.wireOp",EDGE,"E1112"),sQuery(id+"F6.wireOp",EDGE,"E1113"),sQuery(id+"F6.wireOp",EDGE,"E1114"),sQuery(id+"F6.wireOp",EDGE,"E1115"),sQuery(id+"F6.wireOp",EDGE,"E1116"),sQuery(id+"F6.wireOp",EDGE,"E1117"),sQuery(id+"F6.wireOp",EDGE,"E1118"),sQuery(id+"F6.wireOp",EDGE,"E1119"),sQuery(id+"F6.wireOp",EDGE,"E1120"),sQuery(id+"F6.wireOp",EDGE,"E1121"),sQuery(id+"F6.wireOp",EDGE,"E1122"),sQuery(id+"F6.wireOp",EDGE,"E1123"),sQuery(id+"F6.wireOp",EDGE,"E1124"),sQuery(id+"F6.wireOp",EDGE,"E1125"),sQuery(id+"F6.wireOp",EDGE,"E1126"),sQuery(id+"F6.wireOp",EDGE,"E1127"),sQuery(id+"F6.wireOp",EDGE,"E1128"),sQuery(id+"F6.wireOp",EDGE,"E1129"),sQuery(id+"F6.wireOp",EDGE,"E1130"),sQuery(id+"F6.wireOp",EDGE,"E1131"),sQuery(id+"F6.wireOp",EDGE,"E1132"),sQuery(id+"F6.wireOp",EDGE,"E1133"),sQuery(id+"F6.wireOp",EDGE,"E1134"),sQuery(id+"F6.wireOp",EDGE,"E1135"),sQuery(id+"F6.wireOp",EDGE,"E1136"),sQuery(id+"F6.wireOp",EDGE,"E1137"),sQuery(id+"F6.wireOp",EDGE,"E1138"),sQuery(id+"F6.wireOp",EDGE,"E1139"),sQuery(id+"F6.wireOp",EDGE,"E1140"),sQuery(id+"F6.wireOp",EDGE,"E1141"),sQuery(id+"F6.wireOp",EDGE,"E1142"),sQuery(id+"F6.wireOp",EDGE,"E1143"),sQuery(id+"F6.wireOp",EDGE,"E1144"),sQuery(id+"F6.wireOp",EDGE,"E1145"),sQuery(id+"F6.wireOp",EDGE,"E1146"),sQuery(id+"F6.wireOp",EDGE,"E1147"),sQuery(id+"F6.wireOp",EDGE,"E1148"),sQuery(id+"F6.wireOp",EDGE,"E1149"),sQuery(id+"F6.wireOp",EDGE,"E1150"),sQuery(id+"F6.wireOp",EDGE,"E1151"),sQuery(id+"F6.wireOp",EDGE,"E1152"),sQuery(id+"F6.wireOp",EDGE,"E1153"),sQuery(id+"F6.wireOp",EDGE,"E1154"),sQuery(id+"F6.wireOp",EDGE,"E1155"),sQuery(id+"F6.wireOp",EDGE,"E1156"),sQuery(id+"F6.wireOp",EDGE,"E1157"),sQuery(id+"F6.wireOp",EDGE,"E1158"),sQuery(id+"F6.wireOp",EDGE,"E1159"),sQuery(id+"F6.wireOp",EDGE,"E1160"),sQuery(id+"F6.wireOp",EDGE,"E1161"),sQuery(id+"F6.wireOp",EDGE,"E1162"),sQuery(id+"F6.wireOp",EDGE,"E1163"),sQuery(id+"F6.wireOp",EDGE,"E1164"),sQuery(id+"F6.wireOp",EDGE,"E1165"),sQuery(id+"F6.wireOp",EDGE,"E1166"),sQuery(id+"F6.wireOp",EDGE,"E1167"),sQuery(id+"F6.wireOp",EDGE,"E1168"),sQuery(id+"F6.wireOp",EDGE,"E1169"),sQuery(id+"F6.wireOp",EDGE,"E1170"),sQuery(id+"F6.wireOp",EDGE,"E1171"),sQuery(id+"F6.wireOp",EDGE,"E1172"),sQuery(id+"F6.wireOp",EDGE,"E1173"),sQuery(id+"F6.wireOp",EDGE,"E1174"),sQuery(id+"F6.wireOp",EDGE,"E1175"),sQuery(id+"F6.wireOp",EDGE,"E1176"),sQuery(id+"F6.wireOp",EDGE,"E1177"),sQuery(id+"F6.wireOp",EDGE,"E1178"),sQuery(id+"F6.wireOp",EDGE,"E1179"),sQuery(id+"F6.wireOp",EDGE,"E1180"),sQuery(id+"F6.wireOp",EDGE,"E1181"),sQuery(id+"F6.wireOp",EDGE,"E1182"),sQuery(id+"F6.wireOp",EDGE,"E1183"),sQuery(id+"F6.wireOp",EDGE,"E1184"),sQuery(id+"F6.wireOp",EDGE,"E1185"),sQuery(id+"F6.wireOp",EDGE,"E1186"),sQuery(id+"F6.wireOp",EDGE,"E1187"),sQuery(id+"F6.wireOp",EDGE,"E1188"),sQuery(id+"F6.wireOp",EDGE,"E1189"),sQuery(id+"F6.wireOp",EDGE,"E1190"),sQuery(id+"F6.wireOp",EDGE,"E1191"),sQuery(id+"F6.wireOp",EDGE,"E1192"),sQuery(id+"F6.wireOp",EDGE,"E1193"),sQuery(id+"F6.wireOp",EDGE,"E1194"),sQuery(id+"F6.wireOp",EDGE,"E1195"),sQuery(id+"F6.wireOp",EDGE,"E1196"),sQuery(id+"F6.wireOp",EDGE,"E1197"),sQuery(id+"F6.wireOp",EDGE,"E1198"),sQuery(id+"F6.wireOp",EDGE,"E1199"),sQuery(id+"F6.wireOp",EDGE,"E1200"),sQuery(id+"F6.wireOp",EDGE,"E1201"),sQuery(id+"F6.wireOp",EDGE,"E1202"),sQuery(id+"F6.wireOp",EDGE,"E1203"),sQuery(id+"F6.wireOp",EDGE,"E1204"),sQuery(id+"F6.wireOp",EDGE,"E1205"),sQuery(id+"F6.wireOp",EDGE,"E1206"),sQuery(id+"F6.wireOp",EDGE,"E1207"),sQuery(id+"F6.wireOp",EDGE,"E1208"),sQuery(id+"F6.wireOp",EDGE,"E1209"),sQuery(id+"F6.wireOp",EDGE,"E1210"),sQuery(id+"F6.wireOp",EDGE,"E1211"),sQuery(id+"F6.wireOp",EDGE,"E1212"),sQuery(id+"F6.wireOp",EDGE,"E1213"),sQuery(id+"F6.wireOp",EDGE,"E1214"),sQuery(id+"F6.wireOp",EDGE,"E1215"),sQuery(id+"F6.wireOp",EDGE,"E1216"),sQuery(id+"F6.wireOp",EDGE,"E1217"),sQuery(id+"F6.wireOp",EDGE,"E1218"),sQuery(id+"F6.wireOp",EDGE,"E1219"),sQuery(id+"F6.wireOp",EDGE,"E1220"),sQuery(id+"F6.wireOp",EDGE,"E1221"),sQuery(id+"F6.wireOp",EDGE,"E1222"),sQuery(id+"F6.wireOp",EDGE,"E1223"),sQuery(id+"F6.wireOp",EDGE,"E1224"),sQuery(id+"F6.wireOp",EDGE,"E1225"),sQuery(id+"F6.wireOp",EDGE,"E1226"),sQuery(id+"F6.wireOp",EDGE,"E1227"),sQuery(id+"F6.wireOp",EDGE,"E1228"),sQuery(id+"F6.wireOp",EDGE,"E1229"),sQuery(id+"F6.wireOp",EDGE,"E1230"),sQuery(id+"F6.wireOp",EDGE,"E1231"),sQuery(id+"F6.wireOp",EDGE,"E1232"),sQuery(id+"F6.wireOp",EDGE,"E1233"),sQuery(id+"F6.wireOp",EDGE,"E1234"),sQuery(id+"F6.wireOp",EDGE,"E1235"),sQuery(id+"F6.wireOp",EDGE,"E1236"),sQuery(id+"F6.wireOp",EDGE,"E1237"),sQuery(id+"F6.wireOp",EDGE,"E1238"),sQuery(id+"F6.wireOp",EDGE,"E1239"),sQuery(id+"F6.wireOp",EDGE,"E1240"),sQuery(id+"F6.wireOp",EDGE,"E1241"),sQuery(id+"F6.wireOp",EDGE,"E1242"),sQuery(id+"F6.wireOp",EDGE,"E1243"),sQuery(id+"F6.wireOp",EDGE,"E1244"),sQuery(id+"F6.wireOp",EDGE,"E1245"),sQuery(id+"F6.wireOp",EDGE,"E1246"),sQuery(id+"F6.wireOp",EDGE,"E1247"),sQuery(id+"F6.wireOp",EDGE,"E1248"),sQuery(id+"F6.wireOp",EDGE,"E1249"),sQuery(id+"F6.wireOp",EDGE,"E1250"),sQuery(id+"F6.wireOp",EDGE,"E1251"),sQuery(id+"F6.wireOp",EDGE,"E1252"),sQuery(id+"F6.wireOp",EDGE,"E1253"),sQuery(id+"F6.wireOp",EDGE,"E1254"),sQuery(id+"F6.wireOp",EDGE,"E1255"),sQuery(id+"F6.wireOp",EDGE,"E1256"),sQuery(id+"F6.wireOp",EDGE,"E1257"),sQuery(id+"F6.wireOp",EDGE,"E1258"),sQuery(id+"F6.wireOp",EDGE,"E1259"),sQuery(id+"F6.wireOp",EDGE,"E1260"),sQuery(id+"F6.wireOp",EDGE,"E1261"),sQuery(id+"F6.wireOp",EDGE,"E1262"),sQuery(id+"F6.wireOp",EDGE,"E1263"),sQuery(id+"F6.wireOp",EDGE,"E1264"),sQuery(id+"F6.wireOp",EDGE,"E1265"),sQuery(id+"F6.wireOp",EDGE,"E1266"),sQuery(id+"F6.wireOp",EDGE,"E1267"),sQuery(id+"F6.wireOp",EDGE,"E1268"),sQuery(id+"F6.wireOp",EDGE,"E1269"),sQuery(id+"F6.wireOp",EDGE,"E1270"),sQuery(id+"F6.wireOp",EDGE,"E1271"),sQuery(id+"F6.wireOp",EDGE,"E1272"),sQuery(id+"F6.wireOp",EDGE,"E1273"),sQuery(id+"F6.wireOp",EDGE,"E1274"),sQuery(id+"F6.wireOp",EDGE,"E1275"),sQuery(id+"F6.wireOp",EDGE,"E1276"),sQuery(id+"F6.wireOp",EDGE,"E1277"),sQuery(id+"F6.wireOp",EDGE,"E1278"),sQuery(id+"F6.wireOp",EDGE,"E1279"),sQuery(id+"F6.wireOp",EDGE,"E1280"),sQuery(id+"F6.wireOp",EDGE,"E1281"),sQuery(id+"F6.wireOp",EDGE,"E1282"),sQuery(id+"F6.wireOp",EDGE,"E1283"),sQuery(id+"F6.wireOp",EDGE,"E1284"),sQuery(id+"F6.wireOp",EDGE,"E1285"),sQuery(id+"F6.wireOp",EDGE,"E1286"),sQuery(id+"F6.wireOp",EDGE,"E1287"),sQuery(id+"F6.wireOp",EDGE,"E1288"),sQuery(id+"F6.wireOp",EDGE,"E1289"),sQuery(id+"F6.wireOp",EDGE,"E1290"),sQuery(id+"F6.wireOp",EDGE,"E1291"),sQuery(id+"F6.wireOp",EDGE,"E1292"),sQuery(id+"F6.wireOp",EDGE,"E1293"),sQuery(id+"F6.wireOp",EDGE,"E1294"),sQuery(id+"F6.wireOp",EDGE,"E1295"),sQuery(id+"F6.wireOp",EDGE,"E1296"),sQuery(id+"F6.wireOp",EDGE,"E1297"),sQuery(id+"F6.wireOp",EDGE,"E1298"),sQuery(id+"F6.wireOp",EDGE,"E1299"),sQuery(id+"F6.wireOp",EDGE,"E1300"),sQuery(id+"F6.wireOp",EDGE,"E1301"),sQuery(id+"F6.wireOp",EDGE,"E1302"),sQuery(id+"F6.wireOp",EDGE,"E1303"),sQuery(id+"F6.wireOp",EDGE,"E1304"),sQuery(id+"F6.wireOp",EDGE,"E1305"),sQuery(id+"F6.wireOp",EDGE,"E1306"),sQuery(id+"F6.wireOp",EDGE,"E1307"),sQuery(id+"F6.wireOp",EDGE,"E1308"),sQuery(id+"F6.wireOp",EDGE,"E1309"),sQuery(id+"F6.wireOp",EDGE,"E1310"),sQuery(id+"F6.wireOp",EDGE,"E1311"),sQuery(id+"F6.wireOp",EDGE,"E1312"),sQuery(id+"F6.wireOp",EDGE,"E1313"),sQuery(id+"F6.wireOp",EDGE,"E1314"),sQuery(id+"F6.wireOp",EDGE,"E1315"),sQuery(id+"F6.wireOp",EDGE,"E1316"),sQuery(id+"F6.wireOp",EDGE,"E1317"),sQuery(id+"F6.wireOp",EDGE,"E1318"),sQuery(id+"F6.wireOp",EDGE,"E1319"),sQuery(id+"F6.wireOp",EDGE,"E1320"),sQuery(id+"F6.wireOp",EDGE,"E1321"),sQuery(id+"F6.wireOp",EDGE,"E1322"),sQuery(id+"F6.wireOp",EDGE,"E1323"),sQuery(id+"F6.wireOp",EDGE,"E1324"),sQuery(id+"F6.wireOp",EDGE,"E1325"),sQuery(id+"F6.wireOp",EDGE,"E1326"),sQuery(id+"F6.wireOp",EDGE,"E1327"),sQuery(id+"F6.wireOp",EDGE,"E1328"),sQuery(id+"F6.wireOp",EDGE,"E1329"),sQuery(id+"F6.wireOp",EDGE,"E1330"),sQuery(id+"F6.wireOp",EDGE,"E1331"),sQuery(id+"F6.wireOp",EDGE,"E1332"),sQuery(id+"F6.wireOp",EDGE,"E1333"),sQuery(id+"F6.wireOp",EDGE,"E1334"),sQuery(id+"F6.wireOp",EDGE,"E1335"),sQuery(id+"F6.wireOp",EDGE,"E1336"),sQuery(id+"F6.wireOp",EDGE,"E1337"),sQuery(id+"F6.wireOp",EDGE,"E1338"),sQuery(id+"F6.wireOp",EDGE,"E1339"),sQuery(id+"F6.wireOp",EDGE,"E1340"),sQuery(id+"F6.wireOp",EDGE,"E1341"),sQuery(id+"F6.wireOp",EDGE,"E1342"),sQuery(id+"F6.wireOp",EDGE,"E1343"),sQuery(id+"F6.wireOp",EDGE,"E1344"),sQuery(id+"F6.wireOp",EDGE,"E1345"),sQuery(id+"F6.wireOp",EDGE,"E1346"),sQuery(id+"F6.wireOp",EDGE,"E1347"),sQuery(id+"F6.wireOp",EDGE,"E1348"),sQuery(id+"F6.wireOp",EDGE,"E1349"),sQuery(id+"F6.wireOp",EDGE,"E1350"),sQuery(id+"F6.wireOp",EDGE,"E1351"),sQuery(id+"F6.wireOp",EDGE,"E1352"),sQuery(id+"F6.wireOp",EDGE,"E1353"),sQuery(id+"F6.wireOp",EDGE,"E1354"),sQuery(id+"F6.wireOp",EDGE,"E1355"),sQuery(id+"F6.wireOp",EDGE,"E1356"),sQuery(id+"F6.wireOp",EDGE,"E1357"),sQuery(id+"F6.wireOp",EDGE,"E1358"),sQuery(id+"F6.wireOp",EDGE,"E1359"),sQuery(id+"F6.wireOp",EDGE,"E1360"),sQuery(id+"F6.wireOp",EDGE,"E1361"),sQuery(id+"F6.wireOp",EDGE,"E1362"),sQuery(id+"F6.wireOp",EDGE,"E1363"),sQuery(id+"F6.wireOp",EDGE,"E1364"),sQuery(id+"F6.wireOp",EDGE,"E1365"),sQuery(id+"F6.wireOp",EDGE,"E1366"),sQuery(id+"F6.wireOp",EDGE,"E1367"),sQuery(id+"F6.wireOp",EDGE,"E1368"),sQuery(id+"F6.wireOp",EDGE,"E1369"),sQuery(id+"F6.wireOp",EDGE,"E1370"),sQuery(id+"F6.wireOp",EDGE,"E1371"),sQuery(id+"F6.wireOp",EDGE,"E1372"),sQuery(id+"F6.wireOp",EDGE,"E1373"),sQuery(id+"F6.wireOp",EDGE,"E1374"),sQuery(id+"F6.wireOp",EDGE,"E1375"),sQuery(id+"F6.wireOp",EDGE,"E1376"),sQuery(id+"F6.wireOp",EDGE,"E1377"),sQuery(id+"F6.wireOp",EDGE,"E1378"),sQuery(id+"F6.wireOp",EDGE,"E1379"),sQuery(id+"F6.wireOp",EDGE,"E1380"),sQuery(id+"F6.wireOp",EDGE,"E1381"),sQuery(id+"F6.wireOp",EDGE,"E1382"),sQuery(id+"F6.wireOp",EDGE,"E1383"),sQuery(id+"F6.wireOp",EDGE,"E1384"),sQuery(id+"F6.wireOp",EDGE,"E1385"),sQuery(id+"F6.wireOp",EDGE,"E1386"),sQuery(id+"F6.wireOp",EDGE,"E1387"),sQuery(id+"F6.wireOp",EDGE,"E1388"),sQuery(id+"F6.wireOp",EDGE,"E1389"),sQuery(id+"F6.wireOp",EDGE,"E1390"),sQuery(id+"F6.wireOp",EDGE,"E1391"),sQuery(id+"F6.wireOp",EDGE,"E1392"),sQuery(id+"F6.wireOp",EDGE,"E1393"),sQuery(id+"F6.wireOp",EDGE,"E1394"),sQuery(id+"F6.wireOp",EDGE,"E1395"),sQuery(id+"F6.wireOp",EDGE,"E1396"),sQuery(id+"F6.wireOp",EDGE,"E1397"),sQuery(id+"F6.wireOp",EDGE,"E1398"),sQuery(id+"F6.wireOp",EDGE,"E1399"),sQuery(id+"F6.wireOp",EDGE,"E1400"),sQuery(id+"F6.wireOp",EDGE,"E1401"),sQuery(id+"F6.wireOp",EDGE,"E1402"),sQuery(id+"F6.wireOp",EDGE,"E1403"),sQuery(id+"F6.wireOp",EDGE,"E1404"),sQuery(id+"F6.wireOp",EDGE,"E1405"),sQuery(id+"F6.wireOp",EDGE,"E1406"),sQuery(id+"F6.wireOp",EDGE,"E1407"),sQuery(id+"F6.wireOp",EDGE,"E1408"),sQuery(id+"F6.wireOp",EDGE,"E1409"),sQuery(id+"F6.wireOp",EDGE,"E1410"),sQuery(id+"F6.wireOp",EDGE,"E1411"),sQuery(id+"F6.wireOp",EDGE,"E1412"),sQuery(id+"F6.wireOp",EDGE,"E1413"),sQuery(id+"F6.wireOp",EDGE,"E1414"),sQuery(id+"F6.wireOp",EDGE,"E1415"),sQuery(id+"F6.wireOp",EDGE,"E1416"),sQuery(id+"F6.wireOp",EDGE,"E1417"),sQuery(id+"F6.wireOp",EDGE,"E1418"),sQuery(id+"F6.wireOp",EDGE,"E1419"),sQuery(id+"F6.wireOp",EDGE,"E1420"),sQuery(id+"F6.wireOp",EDGE,"E1421"),sQuery(id+"F6.wireOp",EDGE,"E1422"),sQuery(id+"F6.wireOp",EDGE,"E1423"),sQuery(id+"F6.wireOp",EDGE,"E1424"),sQuery(id+"F6.wireOp",EDGE,"E1425"),sQuery(id+"F6.wireOp",EDGE,"E1426"),sQuery(id+"F6.wireOp",EDGE,"E1427"),sQuery(id+"F6.wireOp",EDGE,"E1428"),sQuery(id+"F6.wireOp",EDGE,"E1429"),sQuery(id+"F6.wireOp",EDGE,"E1430"),sQuery(id+"F6.wireOp",EDGE,"E1431"),sQuery(id+"F6.wireOp",EDGE,"E1432"),sQuery(id+"F6.wireOp",EDGE,"E1433"),sQuery(id+"F6.wireOp",EDGE,"E1434"),sQuery(id+"F6.wireOp",EDGE,"E1435"),sQuery(id+"F6.wireOp",EDGE,"E1436"),sQuery(id+"F6.wireOp",EDGE,"E1437"),sQuery(id+"F6.wireOp",EDGE,"E1438"),sQuery(id+"F6.wireOp",EDGE,"E1439"),sQuery(id+"F6.wireOp",EDGE,"E1440"),sQuery(id+"F6.wireOp",EDGE,"E1441"),sQuery(id+"F6.wireOp",EDGE,"E1442"),sQuery(id+"F6.wireOp",EDGE,"E1443"),sQuery(id+"F6.wireOp",EDGE,"E1444"),sQuery(id+"F6.wireOp",EDGE,"E1445"),sQuery(id+"F6.wireOp",EDGE,"E1446"),sQuery(id+"F6.wireOp",EDGE,"E1447"),sQuery(id+"F6.wireOp",EDGE,"E1448"),sQuery(id+"F6.wireOp",EDGE,"E1449"),sQuery(id+"F6.wireOp",EDGE,"E1450"),sQuery(id+"F6.wireOp",EDGE,"E1451"),sQuery(id+"F6.wireOp",EDGE,"E1452"),sQuery(id+"F6.wireOp",EDGE,"E1453"),sQuery(id+"F6.wireOp",EDGE,"E1454"),sQuery(id+"F6.wireOp",EDGE,"E1455"),sQuery(id+"F6.wireOp",EDGE,"E1456"),sQuery(id+"F6.wireOp",EDGE,"E1457"),sQuery(id+"F6.wireOp",EDGE,"E1458"),sQuery(id+"F6.wireOp",EDGE,"E1459"),sQuery(id+"F6.wireOp",EDGE,"E1460"),sQuery(id+"F6.wireOp",EDGE,"E1461"),sQuery(id+"F6.wireOp",EDGE,"E1462"),sQuery(id+"F6.wireOp",EDGE,"E1463"),sQuery(id+"F6.wireOp",EDGE,"E1464"),sQuery(id+"F6.wireOp",EDGE,"E1465"),sQuery(id+"F6.wireOp",EDGE,"E1466"),sQuery(id+"F6.wireOp",EDGE,"E1467"),sQuery(id+"F6.wireOp",EDGE,"E1468"),sQuery(id+"F6.wireOp",EDGE,"E1469"),sQuery(id+"F6.wireOp",EDGE,"E1470"),sQuery(id+"F6.wireOp",EDGE,"E1471"),sQuery(id+"F6.wireOp",EDGE,"E1472"),sQuery(id+"F6.wireOp",EDGE,"E1473"),sQuery(id+"F6.wireOp",EDGE,"E1474"),sQuery(id+"F6.wireOp",EDGE,"E1475"),sQuery(id+"F6.wireOp",EDGE,"E1476"),sQuery(id+"F6.wireOp",EDGE,"E1477"),sQuery(id+"F6.wireOp",EDGE,"E1478"),sQuery(id+"F6.wireOp",EDGE,"E1479"),sQuery(id+"F6.wireOp",EDGE,"E1480"),sQuery(id+"F6.wireOp",EDGE,"E1481"),sQuery(id+"F6.wireOp",EDGE,"E1482"),sQuery(id+"F6.wireOp",EDGE,"E1483"),sQuery(id+"F6.wireOp",EDGE,"E1484"),sQuery(id+"F6.wireOp",EDGE,"E1485"),sQuery(id+"F6.wireOp",EDGE,"E1486"),sQuery(id+"F6.wireOp",EDGE,"E1487"),sQuery(id+"F6.wireOp",EDGE,"E1488"),sQuery(id+"F6.wireOp",EDGE,"E1489"),sQuery(id+"F6.wireOp",EDGE,"E1490"),sQuery(id+"F6.wireOp",EDGE,"E1491"),sQuery(id+"F6.wireOp",EDGE,"E1492"),sQuery(id+"F6.wireOp",EDGE,"E1493"),sQuery(id+"F6.wireOp",EDGE,"E1494"),sQuery(id+"F6.wireOp",EDGE,"E1495"),sQuery(id+"F6.wireOp",EDGE,"E1496"),sQuery(id+"F6.wireOp",EDGE,"E1497"),sQuery(id+"F6.wireOp",EDGE,"E1498"),sQuery(id+"F6.wireOp",EDGE,"E1499"),sQuery(id+"F6.wireOp",EDGE,"E1500"),sQuery(id+"F6.wireOp",EDGE,"E1501"),sQuery(id+"F6.wireOp",EDGE,"E1502"),sQuery(id+"F6.wireOp",EDGE,"E1503"),sQuery(id+"F6.wireOp",EDGE,"E1504"),sQuery(id+"F6.wireOp",EDGE,"E1505"),sQuery(id+"F6.wireOp",EDGE,"E1506"),sQuery(id+"F6.wireOp",EDGE,"E1507"),sQuery(id+"F6.wireOp",EDGE,"E1508"),sQuery(id+"F6.wireOp",EDGE,"E1509"),sQuery(id+"F6.wireOp",EDGE,"E1510"),sQuery(id+"F6.wireOp",EDGE,"E1511"),sQuery(id+"F6.wireOp",EDGE,"E1512"),sQuery(id+"F6.wireOp",EDGE,"E1513"),sQuery(id+"F6.wireOp",EDGE,"E1514"),sQuery(id+"F6.wireOp",EDGE,"E1515"),sQuery(id+"F6.wireOp",EDGE,"E1516"),sQuery(id+"F6.wireOp",EDGE,"E1517"),sQuery(id+"F6.wireOp",EDGE,"E1518"),sQuery(id+"F6.wireOp",EDGE,"E1519"),sQuery(id+"F6.wireOp",EDGE,"E1520"),sQuery(id+"F6.wireOp",EDGE,"E1521"),sQuery(id+"F6.wireOp",EDGE,"E1522"),sQuery(id+"F6.wireOp",EDGE,"E1523"),sQuery(id+"F6.wireOp",EDGE,"E1524"),sQuery(id+"F6.wireOp",EDGE,"E1525"),sQuery(id+"F6.wireOp",EDGE,"E1526"),sQuery(id+"F6.wireOp",EDGE,"E1527"),sQuery(id+"F6.wireOp",EDGE,"E1528"),sQuery(id+"F6.wireOp",EDGE,"E1529"),sQuery(id+"F6.wireOp",EDGE,"E1530"),sQuery(id+"F6.wireOp",EDGE,"E1531"),sQuery(id+"F6.wireOp",EDGE,"E1532"),sQuery(id+"F6.wireOp",EDGE,"E1533"),sQuery(id+"F6.wireOp",EDGE,"E1534"),sQuery(id+"F6.wireOp",EDGE,"E1535"),sQuery(id+"F6.wireOp",EDGE,"E1536"),sQuery(id+"F6.wireOp",EDGE,"E1537"),sQuery(id+"F6.wireOp",EDGE,"E1538"),sQuery(id+"F6.wireOp",EDGE,"E1539"),sQuery(id+"F6.wireOp",EDGE,"E1540"),sQuery(id+"F6.wireOp",EDGE,"E1541"),sQuery(id+"F6.wireOp",EDGE,"E1542"),sQuery(id+"F6.wireOp",EDGE,"E1543"),sQuery(id+"F6.wireOp",EDGE,"E1544"),sQuery(id+"F6.wireOp",EDGE,"E1545"),sQuery(id+"F6.wireOp",EDGE,"E1546"),sQuery(id+"F6.wireOp",EDGE,"E1547"),sQuery(id+"F6.wireOp",EDGE,"E1548"),sQuery(id+"F6.wireOp",EDGE,"E1549"),sQuery(id+"F6.wireOp",EDGE,"E1550"),sQuery(id+"F6.wireOp",EDGE,"E1551"),sQuery(id+"F6.wireOp",EDGE,"E1552"),sQuery(id+"F6.wireOp",EDGE,"E1553"),sQuery(id+"F6.wireOp",EDGE,"E1554"),sQuery(id+"F6.wireOp",EDGE,"E1555"),sQuery(id+"F6.wireOp",EDGE,"E1556"),sQuery(id+"F6.wireOp",EDGE,"E1557"),sQuery(id+"F6.wireOp",EDGE,"E1558"),sQuery(id+"F6.wireOp",EDGE,"E1559"),sQuery(id+"F6.wireOp",EDGE,"E1560"),sQuery(id+"F6.wireOp",EDGE,"E1561"),sQuery(id+"F6.wireOp",EDGE,"E1562"),sQuery(id+"F6.wireOp",EDGE,"E1563"),sQuery(id+"F6.wireOp",EDGE,"E1564"),sQuery(id+"F6.wireOp",EDGE,"E1565"),sQuery(id+"F6.wireOp",EDGE,"E1566"),sQuery(id+"F6.wireOp",EDGE,"E1567"),sQuery(id+"F6.wireOp",EDGE,"E1568"),sQuery(id+"F6.wireOp",EDGE,"E1569"),sQuery(id+"F6.wireOp",EDGE,"E1570"),sQuery(id+"F6.wireOp",EDGE,"E1571"),sQuery(id+"F6.wireOp",EDGE,"E1572"),sQuery(id+"F6.wireOp",EDGE,"E1573"),sQuery(id+"F6.wireOp",EDGE,"E1574"),sQuery(id+"F6.wireOp",EDGE,"E1575"),sQuery(id+"F6.wireOp",EDGE,"E1576"),sQuery(id+"F6.wireOp",EDGE,"E1577"),sQuery(id+"F6.wireOp",EDGE,"E1578"),sQuery(id+"F6.wireOp",EDGE,"E1579"),sQuery(id+"F6.wireOp",EDGE,"E1580"),sQuery(id+"F6.wireOp",EDGE,"E1581"),sQuery(id+"F6.wireOp",EDGE,"E1582"),sQuery(id+"F6.wireOp",EDGE,"E1583"),sQuery(id+"F6.wireOp",EDGE,"E1584"),sQuery(id+"F6.wireOp",EDGE,"E1585"),sQuery(id+"F6.wireOp",EDGE,"E1586"),sQuery(id+"F6.wireOp",EDGE,"E1587"),sQuery(id+"F6.wireOp",EDGE,"E1588"),sQuery(id+"F6.wireOp",EDGE,"E1589"),sQuery(id+"F6.wireOp",EDGE,"E1590"),sQuery(id+"F6.wireOp",EDGE,"E1591"),sQuery(id+"F6.wireOp",EDGE,"E1592"),sQuery(id+"F6.wireOp",EDGE,"E1593"),sQuery(id+"F6.wireOp",EDGE,"E1594"),sQuery(id+"F6.wireOp",EDGE,"E1595"),sQuery(id+"F6.wireOp",EDGE,"E1596"),sQuery(id+"F6.wireOp",EDGE,"E1597"),sQuery(id+"F6.wireOp",EDGE,"E1598"),sQuery(id+"F6.wireOp",EDGE,"E1599"),sQuery(id+"F6.wireOp",EDGE,"E1600"),sQuery(id+"F6.wireOp",EDGE,"E1601"),sQuery(id+"F6.wireOp",EDGE,"E1602"),sQuery(id+"F6.wireOp",EDGE,"E1603"),sQuery(id+"F6.wireOp",EDGE,"E1604"),sQuery(id+"F6.wireOp",EDGE,"E1605"),sQuery(id+"F6.wireOp",EDGE,"E1606"),sQuery(id+"F6.wireOp",EDGE,"E1607"),sQuery(id+"F6.wireOp",EDGE,"E1608"),sQuery(id+"F6.wireOp",EDGE,"E1609"),sQuery(id+"F6.wireOp",EDGE,"E1610"),sQuery(id+"F6.wireOp",EDGE,"E1611"),sQuery(id+"F6.wireOp",EDGE,"E1612"),sQuery(id+"F6.wireOp",EDGE,"E1613"),sQuery(id+"F6.wireOp",EDGE,"E1614"),sQuery(id+"F6.wireOp",EDGE,"E1615"),sQuery(id+"F6.wireOp",EDGE,"E1616"),sQuery(id+"F6.wireOp",EDGE,"E1617"),sQuery(id+"F6.wireOp",EDGE,"E1618"),sQuery(id+"F6.wireOp",EDGE,"E1619"),sQuery(id+"F6.wireOp",EDGE,"E1620"),sQuery(id+"F6.wireOp",EDGE,"E1621"),sQuery(id+"F6.wireOp",EDGE,"E1622"),sQuery(id+"F6.wireOp",EDGE,"E1623"),sQuery(id+"F6.wireOp",EDGE,"E1624"),sQuery(id+"F6.wireOp",EDGE,"E1625"),sQuery(id+"F6.wireOp",EDGE,"E1626"),sQuery(id+"F6.wireOp",EDGE,"E1627"),sQuery(id+"F6.wireOp",EDGE,"E1628"),sQuery(id+"F6.wireOp",EDGE,"E1629"),sQuery(id+"F6.wireOp",EDGE,"E1630"),sQuery(id+"F6.wireOp",EDGE,"E1631"),sQuery(id+"F6.wireOp",EDGE,"E1632"),sQuery(id+"F6.wireOp",EDGE,"E1633"),sQuery(id+"F6.wireOp",EDGE,"E1634"),sQuery(id+"F6.wireOp",EDGE,"E1635"),sQuery(id+"F6.wireOp",EDGE,"E1636"),sQuery(id+"F6.wireOp",EDGE,"E1637"),sQuery(id+"F6.wireOp",EDGE,"E1638"),sQuery(id+"F6.wireOp",EDGE,"E1639"),sQuery(id+"F6.wireOp",EDGE,"E1640"),sQuery(id+"F6.wireOp",EDGE,"E1641"),sQuery(id+"F6.wireOp",EDGE,"E1642"),sQuery(id+"F6.wireOp",EDGE,"E1643"),sQuery(id+"F6.wireOp",EDGE,"E1644"),sQuery(id+"F6.wireOp",EDGE,"E1645"),sQuery(id+"F6.wireOp",EDGE,"E1646"),sQuery(id+"F6.wireOp",EDGE,"E1647"),sQuery(id+"F6.wireOp",EDGE,"E1648"),sQuery(id+"F6.wireOp",EDGE,"E1649"),sQuery(id+"F6.wireOp",EDGE,"E1650"),sQuery(id+"F6.wireOp",EDGE,"E1651"),sQuery(id+"F6.wireOp",EDGE,"E1652"),sQuery(id+"F6.wireOp",EDGE,"E1653"),sQuery(id+"F6.wireOp",EDGE,"E1654"),sQuery(id+"F6.wireOp",EDGE,"E1655"),sQuery(id+"F6.wireOp",EDGE,"E1656"),sQuery(id+"F6.wireOp",EDGE,"E1657"),sQuery(id+"F6.wireOp",EDGE,"E1658"),sQuery(id+"F6.wireOp",EDGE,"E1659"),sQuery(id+"F6.wireOp",EDGE,"E1660"),sQuery(id+"F6.wireOp",EDGE,"E1661"),sQuery(id+"F6.wireOp",EDGE,"E1662"),sQuery(id+"F6.wireOp",EDGE,"E1663"),sQuery(id+"F6.wireOp",EDGE,"E1664"),sQuery(id+"F6.wireOp",EDGE,"E1665"),sQuery(id+"F6.wireOp",EDGE,"E1666"),sQuery(id+"F6.wireOp",EDGE,"E1667"),sQuery(id+"F6.wireOp",EDGE,"E1668"),sQuery(id+"F6.wireOp",EDGE,"E1669"),sQuery(id+"F6.wireOp",EDGE,"E1670"),sQuery(id+"F6.wireOp",EDGE,"E1671"),sQuery(id+"F6.wireOp",EDGE,"E1672"),sQuery(id+"F6.wireOp",EDGE,"E1673"),sQuery(id+"F6.wireOp",EDGE,"E1674"),sQuery(id+"F6.wireOp",EDGE,"E1675"),sQuery(id+"F6.wireOp",EDGE,"E1676"),sQuery(id+"F6.wireOp",EDGE,"E1677"),sQuery(id+"F6.wireOp",EDGE,"E1678"),sQuery(id+"F6.wireOp",EDGE,"E1679"),sQuery(id+"F6.wireOp",EDGE,"E1680"),sQuery(id+"F6.wireOp",EDGE,"E1681"),sQuery(id+"F6.wireOp",EDGE,"E1682"),sQuery(id+"F6.wireOp",EDGE,"E1683"),sQuery(id+"F6.wireOp",EDGE,"E1684"),sQuery(id+"F6.wireOp",EDGE,"E1685"),sQuery(id+"F6.wireOp",EDGE,"E1686"),sQuery(id+"F6.wireOp",EDGE,"E1687"),sQuery(id+"F6.wireOp",EDGE,"E1688"),sQuery(id+"F6.wireOp",EDGE,"E1689"),sQuery(id+"F6.wireOp",EDGE,"E1690"),sQuery(id+"F6.wireOp",EDGE,"E1691"),sQuery(id+"F6.wireOp",EDGE,"E1692"),sQuery(id+"F6.wireOp",EDGE,"E1693"),sQuery(id+"F6.wireOp",EDGE,"E1694"),sQuery(id+"F6.wireOp",EDGE,"E1695"),sQuery(id+"F6.wireOp",EDGE,"E1696"),sQuery(id+"F6.wireOp",EDGE,"E1697"),sQuery(id+"F6.wireOp",EDGE,"E1698"),sQuery(id+"F6.wireOp",EDGE,"E1699"),sQuery(id+"F6.wireOp",EDGE,"E1700"),sQuery(id+"F6.wireOp",EDGE,"E1701"),sQuery(id+"F6.wireOp",EDGE,"E1702"),sQuery(id+"F6.wireOp",EDGE,"E1703"),sQuery(id+"F6.wireOp",EDGE,"E1704"),sQuery(id+"F6.wireOp",EDGE,"E1705"),sQuery(id+"F6.wireOp",EDGE,"E1706"),sQuery(id+"F6.wireOp",EDGE,"E1707"),sQuery(id+"F6.wireOp",EDGE,"E1708"),sQuery(id+"F6.wireOp",EDGE,"E1709"),sQuery(id+"F6.wireOp",EDGE,"E1710"),sQuery(id+"F6.wireOp",EDGE,"E1711"),sQuery(id+"F6.wireOp",EDGE,"E1712"),sQuery(id+"F6.wireOp",EDGE,"E1713"),sQuery(id+"F6.wireOp",EDGE,"E1714"),sQuery(id+"F6.wireOp",EDGE,"E1715"),sQuery(id+"F6.wireOp",EDGE,"E1716"),sQuery(id+"F6.wireOp",EDGE,"E1717"),sQuery(id+"F6.wireOp",EDGE,"E1718"),sQuery(id+"F6.wireOp",EDGE,"E1719"),sQuery(id+"F6.wireOp",EDGE,"E1720"),sQuery(id+"F6.wireOp",EDGE,"E1721"),sQuery(id+"F6.wireOp",EDGE,"E1722"),sQuery(id+"F6.wireOp",EDGE,"E1723"),sQuery(id+"F6.wireOp",EDGE,"E1724"),sQuery(id+"F6.wireOp",EDGE,"E1725"),sQuery(id+"F6.wireOp",EDGE,"E1726"),sQuery(id+"F6.wireOp",EDGE,"E1727"),sQuery(id+"F6.wireOp",EDGE,"E1728"),sQuery(id+"F6.wireOp",EDGE,"E1729"),sQuery(id+"F6.wireOp",EDGE,"E1730"),sQuery(id+"F6.wireOp",EDGE,"E1731"),sQuery(id+"F6.wireOp",EDGE,"E1732"),sQuery(id+"F6.wireOp",EDGE,"E1733"),sQuery(id+"F6.wireOp",EDGE,"E1734"),sQuery(id+"F6.wireOp",EDGE,"E1735"),sQuery(id+"F6.wireOp",EDGE,"E1736"),sQuery(id+"F6.wireOp",EDGE,"E1737"),sQuery(id+"F6.wireOp",EDGE,"E1738"),sQuery(id+"F6.wireOp",EDGE,"E1739"),sQuery(id+"F6.wireOp",EDGE,"E1740"),sQuery(id+"F6.wireOp",EDGE,"E1741"),sQuery(id+"F6.wireOp",EDGE,"E1742"),sQuery(id+"F6.wireOp",EDGE,"E1743"),sQuery(id+"F6.wireOp",EDGE,"E1744"),sQuery(id+"F6.wireOp",EDGE,"E1745"),sQuery(id+"F6.wireOp",EDGE,"E1746"),sQuery(id+"F6.wireOp",EDGE,"E1747"),sQuery(id+"F6.wireOp",EDGE,"E1748"),sQuery(id+"F6.wireOp",EDGE,"E1749"),sQuery(id+"F6.wireOp",EDGE,"E1750"),sQuery(id+"F6.wireOp",EDGE,"E1751"),sQuery(id+"F6.wireOp",EDGE,"E1752"),sQuery(id+"F6.wireOp",EDGE,"E1753"),sQuery(id+"F6.wireOp",EDGE,"E1754"),sQuery(id+"F6.wireOp",EDGE,"E1755"),sQuery(id+"F6.wireOp",EDGE,"E1756"),sQuery(id+"F6.wireOp",EDGE,"E1757"),sQuery(id+"F6.wireOp",EDGE,"E1758"),sQuery(id+"F6.wireOp",EDGE,"E1759"),sQuery(id+"F6.wireOp",EDGE,"E1760"),sQuery(id+"F6.wireOp",EDGE,"E1761"),sQuery(id+"F6.wireOp",EDGE,"E1762"),sQuery(id+"F6.wireOp",EDGE,"E1763"),sQuery(id+"F6.wireOp",EDGE,"E1764"),sQuery(id+"F6.wireOp",EDGE,"E1765"),sQuery(id+"F6.wireOp",EDGE,"E1766"),sQuery(id+"F6.wireOp",EDGE,"E1767"),sQuery(id+"F6.wireOp",EDGE,"E1768"),sQuery(id+"F6.wireOp",EDGE,"E1769"),sQuery(id+"F6.wireOp",EDGE,"E1770"),sQuery(id+"F6.wireOp",EDGE,"E1771"),sQuery(id+"F6.wireOp",EDGE,"E1772"),sQuery(id+"F6.wireOp",EDGE,"E1773"),sQuery(id+"F6.wireOp",EDGE,"E1774"),sQuery(id+"F6.wireOp",EDGE,"E1775"),sQuery(id+"F6.wireOp",EDGE,"E1776"),sQuery(id+"F6.wireOp",EDGE,"E1777"),sQuery(id+"F6.wireOp",EDGE,"E1778"),sQuery(id+"F6.wireOp",EDGE,"E1779"),sQuery(id+"F6.wireOp",EDGE,"E1780"),sQuery(id+"F6.wireOp",EDGE,"E1781"),sQuery(id+"F6.wireOp",EDGE,"E1782"),sQuery(id+"F6.wireOp",EDGE,"E1783"),sQuery(id+"F6.wireOp",EDGE,"E1784"),sQuery(id+"F6.wireOp",EDGE,"E1785"),sQuery(id+"F6.wireOp",EDGE,"E1786"),sQuery(id+"F6.wireOp",EDGE,"E1787"),sQuery(id+"F6.wireOp",EDGE,"E1788"),sQuery(id+"F6.wireOp",EDGE,"E1789"),sQuery(id+"F6.wireOp",EDGE,"E1790"),sQuery(id+"F6.wireOp",EDGE,"E1791"),sQuery(id+"F6.wireOp",EDGE,"E1792"),sQuery(id+"F6.wireOp",EDGE,"E1793"),sQuery(id+"F6.wireOp",EDGE,"E1794"),sQuery(id+"F6.wireOp",EDGE,"E1795"),sQuery(id+"F6.wireOp",EDGE,"E1796"),sQuery(id+"F6.wireOp",EDGE,"E1797"),sQuery(id+"F6.wireOp",EDGE,"E1798"),sQuery(id+"F6.wireOp",EDGE,"E1799"),sQuery(id+"F6.wireOp",EDGE,"E1800"),sQuery(id+"F6.wireOp",EDGE,"E1801"),sQuery(id+"F6.wireOp",EDGE,"E1802"),sQuery(id+"F6.wireOp",EDGE,"E1803"),sQuery(id+"F6.wireOp",EDGE,"E1804"),sQuery(id+"F6.wireOp",EDGE,"E1805"),sQuery(id+"F6.wireOp",EDGE,"E1806"),sQuery(id+"F6.wireOp",EDGE,"E1807"),sQuery(id+"F6.wireOp",EDGE,"E1808"),sQuery(id+"F6.wireOp",EDGE,"E1809"),sQuery(id+"F6.wireOp",EDGE,"E1810"),sQuery(id+"F6.wireOp",EDGE,"E1811"),sQuery(id+"F6.wireOp",EDGE,"E1812"),sQuery(id+"F6.wireOp",EDGE,"E1813"),sQuery(id+"F6.wireOp",EDGE,"E1814"),sQuery(id+"F6.wireOp",EDGE,"E1815"),sQuery(id+"F6.wireOp",EDGE,"E1816"),sQuery(id+"F6.wireOp",EDGE,"E1817"),sQuery(id+"F6.wireOp",EDGE,"E1818"),sQuery(id+"F6.wireOp",EDGE,"E1819"),sQuery(id+"F6.wireOp",EDGE,"E1820"),sQuery(id+"F6.wireOp",EDGE,"E1821"),sQuery(id+"F6.wireOp",EDGE,"E1822"),sQuery(id+"F6.wireOp",EDGE,"E1823"),sQuery(id+"F6.wireOp",EDGE,"E1824"),sQuery(id+"F6.wireOp",EDGE,"E1825"),sQuery(id+"F6.wireOp",EDGE,"E1826"),sQuery(id+"F6.wireOp",EDGE,"E1827"),sQuery(id+"F6.wireOp",EDGE,"E1828"),sQuery(id+"F6.wireOp",EDGE,"E1829"),sQuery(id+"F6.wireOp",EDGE,"E1830"),sQuery(id+"F6.wireOp",EDGE,"E1831"),sQuery(id+"F6.wireOp",EDGE,"E1832"),sQuery(id+"F6.wireOp",EDGE,"E1833"),sQuery(id+"F6.wireOp",EDGE,"E1834"),sQuery(id+"F6.wireOp",EDGE,"E1835"),sQuery(id+"F6.wireOp",EDGE,"E1836"),sQuery(id+"F6.wireOp",EDGE,"E1837"),sQuery(id+"F6.wireOp",EDGE,"E1838"),sQuery(id+"F6.wireOp",EDGE,"E1839"),sQuery(id+"F6.wireOp",EDGE,"E1840"),sQuery(id+"F6.wireOp",EDGE,"E1841"),sQuery(id+"F6.wireOp",EDGE,"E1842"),sQuery(id+"F6.wireOp",EDGE,"E1843"),sQuery(id+"F6.wireOp",EDGE,"E1844"),sQuery(id+"F6.wireOp",EDGE,"E1845"),sQuery(id+"F6.wireOp",EDGE,"E1846"),sQuery(id+"F6.wireOp",EDGE,"E1847"),sQuery(id+"F6.wireOp",EDGE,"E1848"),sQuery(id+"F6.wireOp",EDGE,"E1849"),sQuery(id+"F6.wireOp",EDGE,"E1850"),sQuery(id+"F6.wireOp",EDGE,"E1851"),sQuery(id+"F6.wireOp",EDGE,"E1852"),sQuery(id+"F6.wireOp",EDGE,"E1853"),sQuery(id+"F6.wireOp",EDGE,"E1854"),sQuery(id+"F6.wireOp",EDGE,"E1855"),sQuery(id+"F6.wireOp",EDGE,"E1856"),sQuery(id+"F6.wireOp",EDGE,"E1857"),sQuery(id+"F6.wireOp",EDGE,"E1858"),sQuery(id+"F6.wireOp",EDGE,"E1859"),sQuery(id+"F6.wireOp",EDGE,"E1860"),sQuery(id+"F6.wireOp",EDGE,"E1861"),sQuery(id+"F6.wireOp",EDGE,"E1862"),sQuery(id+"F6.wireOp",EDGE,"E1863"),sQuery(id+"F6.wireOp",EDGE,"E1864"),sQuery(id+"F6.wireOp",EDGE,"E1865"),sQuery(id+"F6.wireOp",EDGE,"E1866"),sQuery(id+"F6.wireOp",EDGE,"E1867"),sQuery(id+"F6.wireOp",EDGE,"E1868"),sQuery(id+"F6.wireOp",EDGE,"E1869"),sQuery(id+"F6.wireOp",EDGE,"E1870"),sQuery(id+"F6.wireOp",EDGE,"E1871"),sQuery(id+"F6.wireOp",EDGE,"E1872"),sQuery(id+"F6.wireOp",EDGE,"E1873"),sQuery(id+"F6.wireOp",EDGE,"E1874"),sQuery(id+"F6.wireOp",EDGE,"E1875"),sQuery(id+"F6.wireOp",EDGE,"E1876"),sQuery(id+"F6.wireOp",EDGE,"E1877"),sQuery(id+"F6.wireOp",EDGE,"E1878"),sQuery(id+"F6.wireOp",EDGE,"E1879"),sQuery(id+"F6.wireOp",EDGE,"E1880"),sQuery(id+"F6.wireOp",EDGE,"E1881"),sQuery(id+"F6.wireOp",EDGE,"E1882"),sQuery(id+"F6.wireOp",EDGE,"E1883"),sQuery(id+"F6.wireOp",EDGE,"E1884"),sQuery(id+"F6.wireOp",EDGE,"E1885"),sQuery(id+"F6.wireOp",EDGE,"E1886"),sQuery(id+"F6.wireOp",EDGE,"E1887"),sQuery(id+"F6.wireOp",EDGE,"E1888"),sQuery(id+"F6.wireOp",EDGE,"E1889"),sQuery(id+"F6.wireOp",EDGE,"E1890"),sQuery(id+"F6.wireOp",EDGE,"E1891"),sQuery(id+"F6.wireOp",EDGE,"E1892"),sQuery(id+"F6.wireOp",EDGE,"E1893"),sQuery(id+"F6.wireOp",EDGE,"E1894"),sQuery(id+"F6.wireOp",EDGE,"E1895"),sQuery(id+"F6.wireOp",EDGE,"E1896"),sQuery(id+"F6.wireOp",EDGE,"E1897"),sQuery(id+"F6.wireOp",EDGE,"E1898"),sQuery(id+"F6.wireOp",EDGE,"E1899"),sQuery(id+"F6.wireOp",EDGE,"E1900"),sQuery(id+"F6.wireOp",EDGE,"E1901"),sQuery(id+"F6.wireOp",EDGE,"E1902"),sQuery(id+"F6.wireOp",EDGE,"E1903"),sQuery(id+"F6.wireOp",EDGE,"E1904"),sQuery(id+"F6.wireOp",EDGE,"E1905"),sQuery(id+"F6.wireOp",EDGE,"E1906"),sQuery(id+"F6.wireOp",EDGE,"E1907"),sQuery(id+"F6.wireOp",EDGE,"E1908"),sQuery(id+"F6.wireOp",EDGE,"E1909"),sQuery(id+"F6.wireOp",EDGE,"E1910"),sQuery(id+"F6.wireOp",EDGE,"E1911"),sQuery(id+"F6.wireOp",EDGE,"E1912"),sQuery(id+"F6.wireOp",EDGE,"E1913"),sQuery(id+"F6.wireOp",EDGE,"E1914"),sQuery(id+"F6.wireOp",EDGE,"E1915"),sQuery(id+"F6.wireOp",EDGE,"E1916"),sQuery(id+"F6.wireOp",EDGE,"E1917"),sQuery(id+"F6.wireOp",EDGE,"E1918"),sQuery(id+"F6.wireOp",EDGE,"E1919"),sQuery(id+"F6.wireOp",EDGE,"E1920"),sQuery(id+"F6.wireOp",EDGE,"E1921"),sQuery(id+"F6.wireOp",EDGE,"E1922"),sQuery(id+"F6.wireOp",EDGE,"E1923"),sQuery(id+"F6.wireOp",EDGE,"E1924"),sQuery(id+"F6.wireOp",EDGE,"E1925"),sQuery(id+"F6.wireOp",EDGE,"E1926"),sQuery(id+"F6.wireOp",EDGE,"E1927"),sQuery(id+"F6.wireOp",EDGE,"E1928"),sQuery(id+"F6.wireOp",EDGE,"E1929"),sQuery(id+"F6.wireOp",EDGE,"E1930"),sQuery(id+"F6.wireOp",EDGE,"E1931"),sQuery(id+"F6.wireOp",EDGE,"E1932"),sQuery(id+"F6.wireOp",EDGE,"E1933"),sQuery(id+"F6.wireOp",EDGE,"E1934"),sQuery(id+"F6.wireOp",EDGE,"E1935"),sQuery(id+"F6.wireOp",EDGE,"E1936"),sQuery(id+"F6.wireOp",EDGE,"E1937"),sQuery(id+"F6.wireOp",EDGE,"E1938"),sQuery(id+"F6.wireOp",EDGE,"E1939"),sQuery(id+"F6.wireOp",EDGE,"E1940"),sQuery(id+"F6.wireOp",EDGE,"E1941"),sQuery(id+"F6.wireOp",EDGE,"E1942"),sQuery(id+"F6.wireOp",EDGE,"E1943"),sQuery(id+"F6.wireOp",EDGE,"E1944"),sQuery(id+"F6.wireOp",EDGE,"E1945"),sQuery(id+"F6.wireOp",EDGE,"E1946"),sQuery(id+"F6.wireOp",EDGE,"E1947"),sQuery(id+"F6.wireOp",EDGE,"E1948"),sQuery(id+"F6.wireOp",EDGE,"E1949"),sQuery(id+"F6.wireOp",EDGE,"E1950"),sQuery(id+"F6.wireOp",EDGE,"E1951"),sQuery(id+"F6.wireOp",EDGE,"E1952"),sQuery(id+"F6.wireOp",EDGE,"E1953"),sQuery(id+"F6.wireOp",EDGE,"E1954"),sQuery(id+"F6.wireOp",EDGE,"E1955"),sQuery(id+"F6.wireOp",EDGE,"E1956"),sQuery(id+"F6.wireOp",EDGE,"E1957"),sQuery(id+"F6.wireOp",EDGE,"E1958"),sQuery(id+"F6.wireOp",EDGE,"E1959"),sQuery(id+"F6.wireOp",EDGE,"E1960"),sQuery(id+"F6.wireOp",EDGE,"E1961"),sQuery(id+"F6.wireOp",EDGE,"E1962"),sQuery(id+"F6.wireOp",EDGE,"E1963"),sQuery(id+"F6.wireOp",EDGE,"E1964"),sQuery(id+"F6.wireOp",EDGE,"E1965"),sQuery(id+"F6.wireOp",EDGE,"E1966"),sQuery(id+"F6.wireOp",EDGE,"E1967"),sQuery(id+"F6.wireOp",EDGE,"E1968"),sQuery(id+"F6.wireOp",EDGE,"E1969"),sQuery(id+"F6.wireOp",EDGE,"E1970"),sQuery(id+"F6.wireOp",EDGE,"E1971"),sQuery(id+"F6.wireOp",EDGE,"E1972"),sQuery(id+"F6.wireOp",EDGE,"E1973"),sQuery(id+"F6.wireOp",EDGE,"E1974"),sQuery(id+"F6.wireOp",EDGE,"E1975"),sQuery(id+"F6.wireOp",EDGE,"E1976"),sQuery(id+"F6.wireOp",EDGE,"E1977"),sQuery(id+"F6.wireOp",EDGE,"E1978"),sQuery(id+"F6.wireOp",EDGE,"E1979"),sQuery(id+"F6.wireOp",EDGE,"E1980"),sQuery(id+"F6.wireOp",EDGE,"E1981"),sQuery(id+"F6.wireOp",EDGE,"E1982"),sQuery(id+"F6.wireOp",EDGE,"E1983"),sQuery(id+"F6.wireOp",EDGE,"E1984"),sQuery(id+"F6.wireOp",EDGE,"E1985"),sQuery(id+"F6.wireOp",EDGE,"E1986"),sQuery(id+"F6.wireOp",EDGE,"E1987"),sQuery(id+"F6.wireOp",EDGE,"E1988"),sQuery(id+"F6.wireOp",EDGE,"E1989"),sQuery(id+"F6.wireOp",EDGE,"E1990"),sQuery(id+"F6.wireOp",EDGE,"E1991"),sQuery(id+"F6.wireOp",EDGE,"E1992"),sQuery(id+"F6.wireOp",EDGE,"E1993"),sQuery(id+"F6.wireOp",EDGE,"E1994"),sQuery(id+"F6.wireOp",EDGE,"E1995"),sQuery(id+"F6.wireOp",EDGE,"E1996"),sQuery(id+"F6.wireOp",EDGE,"E1997"),sQuery(id+"F6.wireOp",EDGE,"E1998"),sQuery(id+"F6.wireOp",EDGE,"E1999"),sQuery(id+"F6.wireOp",EDGE,"E2000"),sQuery(id+"F6.wireOp",EDGE,"E2001"),sQuery(id+"F6.wireOp",EDGE,"E2002"),sQuery(id+"F6.wireOp",EDGE,"E2003"),sQuery(id+"F6.wireOp",EDGE,"E2004"),sQuery(id+"F6.wireOp",EDGE,"E2005"),sQuery(id+"F6.wireOp",EDGE,"E2006"),sQuery(id+"F6.wireOp",EDGE,"E2007"),sQuery(id+"F6.wireOp",EDGE,"E2008"),sQuery(id+"F6.wireOp",EDGE,"E2009"),sQuery(id+"F6.wireOp",EDGE,"E2010"),sQuery(id+"F6.wireOp",EDGE,"E2011"),sQuery(id+"F6.wireOp",EDGE,"E2012"),sQuery(id+"F6.wireOp",EDGE,"E2013"),sQuery(id+"F6.wireOp",EDGE,"E2014"),sQuery(id+"F6.wireOp",EDGE,"E2015"),sQuery(id+"F6.wireOp",EDGE,"E2016"),sQuery(id+"F6.wireOp",EDGE,"E2017"),sQuery(id+"F6.wireOp",EDGE,"E2018"),sQuery(id+"F6.wireOp",EDGE,"E2019"),sQuery(id+"F6.wireOp",EDGE,"E2020"),sQuery(id+"F6.wireOp",EDGE,"E2021"),sQuery(id+"F6.wireOp",EDGE,"E2022"),sQuery(id+"F6.wireOp",EDGE,"E2023"),sQuery(id+"F6.wireOp",EDGE,"E2024"),sQuery(id+"F6.wireOp",EDGE,"E2025"),sQuery(id+"F6.wireOp",EDGE,"E2026"),sQuery(id+"F6.wireOp",EDGE,"E2027"),sQuery(id+"F6.wireOp",EDGE,"E2028"),sQuery(id+"F6.wireOp",EDGE,"E2029"),sQuery(id+"F6.wireOp",EDGE,"E2030"),sQuery(id+"F6.wireOp",EDGE,"E2031"),sQuery(id+"F6.wireOp",EDGE,"E2032"),sQuery(id+"F6.wireOp",EDGE,"E2033"),sQuery(id+"F6.wireOp",EDGE,"E2034"),sQuery(id+"F6.wireOp",EDGE,"E2035"),sQuery(id+"F6.wireOp",EDGE,"E2036"),sQuery(id+"F6.wireOp",EDGE,"E2037"),sQuery(id+"F6.wireOp",EDGE,"E2038"),sQuery(id+"F6.wireOp",EDGE,"E2039"),sQuery(id+"F6.wireOp",EDGE,"E2040"),sQuery(id+"F6.wireOp",EDGE,"E2041"),sQuery(id+"F6.wireOp",EDGE,"E2042"),sQuery(id+"F6.wireOp",EDGE,"E2043"),sQuery(id+"F6.wireOp",EDGE,"E2044"),sQuery(id+"F6.wireOp",EDGE,"E2045"),sQuery(id+"F6.wireOp",EDGE,"E2046"),sQuery(id+"F6.wireOp",EDGE,"E2047"),sQuery(id+"F6.wireOp",EDGE,"E2048"),sQuery(id+"F6.wireOp",EDGE,"E2049"),sQuery(id+"F6.wireOp",EDGE,"E2050"),sQuery(id+"F6.wireOp",EDGE,"E2051"),sQuery(id+"F6.wireOp",EDGE,"E2052"),sQuery(id+"F6.wireOp",EDGE,"E2053"),sQuery(id+"F6.wireOp",EDGE,"E2054"),sQuery(id+"F6.wireOp",EDGE,"E2055"),sQuery(id+"F6.wireOp",EDGE,"E2056"),sQuery(id+"F6.wireOp",EDGE,"E2057"),sQuery(id+"F6.wireOp",EDGE,"E2058"),sQuery(id+"F6.wireOp",EDGE,"E2059"),sQuery(id+"F6.wireOp",EDGE,"E2060"),sQuery(id+"F6.wireOp",EDGE,"E2061"),sQuery(id+"F6.wireOp",EDGE,"E2062"),sQuery(id+"F6.wireOp",EDGE,"E2063"),sQuery(id+"F6.wireOp",EDGE,"E2064"),sQuery(id+"F6.wireOp",EDGE,"E2065"),sQuery(id+"F6.wireOp",EDGE,"E2066"),sQuery(id+"F6.wireOp",EDGE,"E2067"),sQuery(id+"F6.wireOp",EDGE,"E2068"),sQuery(id+"F6.wireOp",EDGE,"E2069"),sQuery(id+"F6.wireOp",EDGE,"E2070"),sQuery(id+"F6.wireOp",EDGE,"E2071"),sQuery(id+"F6.wireOp",EDGE,"E2072"),sQuery(id+"F6.wireOp",EDGE,"E2073"),sQuery(id+"F6.wireOp",EDGE,"E2074"),sQuery(id+"F6.wireOp",EDGE,"E2075"),sQuery(id+"F6.wireOp",EDGE,"E2076"),sQuery(id+"F6.wireOp",EDGE,"E2077"),sQuery(id+"F6.wireOp",EDGE,"E2078"),sQuery(id+"F6.wireOp",EDGE,"E2079"),sQuery(id+"F6.wireOp",EDGE,"E2080"),sQuery(id+"F6.wireOp",EDGE,"E2081"),sQuery(id+"F6.wireOp",EDGE,"E2082"),sQuery(id+"F6.wireOp",EDGE,"E2083"),sQuery(id+"F6.wireOp",EDGE,"E2084"),sQuery(id+"F6.wireOp",EDGE,"E2085"),sQuery(id+"F6.wireOp",EDGE,"E2086"),sQuery(id+"F6.wireOp",EDGE,"E2087"),sQuery(id+"F6.wireOp",EDGE,"E2088"),sQuery(id+"F6.wireOp",EDGE,"E2089"),sQuery(id+"F6.wireOp",EDGE,"E2090"),sQuery(id+"F6.wireOp",EDGE,"E2091"),sQuery(id+"F6.wireOp",EDGE,"E2092"),sQuery(id+"F6.wireOp",EDGE,"E2093"),sQuery(id+"F6.wireOp",EDGE,"E2094"),sQuery(id+"F6.wireOp",EDGE,"E2095"),sQuery(id+"F6.wireOp",EDGE,"E2096"),sQuery(id+"F6.wireOp",EDGE,"E2097"),sQuery(id+"F6.wireOp",EDGE,"E2098"),sQuery(id+"F6.wireOp",EDGE,"E2099"),sQuery(id+"F6.wireOp",EDGE,"E2100"),sQuery(id+"F6.wireOp",EDGE,"E2101"),sQuery(id+"F6.wireOp",EDGE,"E2102"),sQuery(id+"F6.wireOp",EDGE,"E2103"),sQuery(id+"F6.wireOp",EDGE,"E2104"),sQuery(id+"F6.wireOp",EDGE,"E2105"),sQuery(id+"F6.wireOp",EDGE,"E2106"),sQuery(id+"F6.wireOp",EDGE,"E2107"),sQuery(id+"F6.wireOp",EDGE,"E2108"),sQuery(id+"F6.wireOp",EDGE,"E2109"),sQuery(id+"F6.wireOp",EDGE,"E2110"),sQuery(id+"F6.wireOp",EDGE,"E2111"),sQuery(id+"F6.wireOp",EDGE,"E2112"),sQuery(id+"F6.wireOp",EDGE,"E2113"),sQuery(id+"F6.wireOp",EDGE,"E2114"),sQuery(id+"F6.wireOp",EDGE,"E2115"),sQuery(id+"F6.wireOp",EDGE,"E2116"),sQuery(id+"F6.wireOp",EDGE,"E2117"),sQuery(id+"F6.wireOp",EDGE,"E2118"),sQuery(id+"F6.wireOp",EDGE,"E2119"),sQuery(id+"F6.wireOp",EDGE,"E2120"),sQuery(id+"F6.wireOp",EDGE,"E2121"),sQuery(id+"F6.wireOp",EDGE,"E2122"),sQuery(id+"F6.wireOp",EDGE,"E2123"),sQuery(id+"F6.wireOp",EDGE,"E2124"),sQuery(id+"F6.wireOp",EDGE,"E2125"),sQuery(id+"F6.wireOp",EDGE,"E2126"),sQuery(id+"F6.wireOp",EDGE,"E2127"),sQuery(id+"F6.wireOp",EDGE,"E2128"),sQuery(id+"F6.wireOp",EDGE,"E2129"),sQuery(id+"F6.wireOp",EDGE,"E2130"),sQuery(id+"F6.wireOp",EDGE,"E2131"),sQuery(id+"F6.wireOp",EDGE,"E2132"),sQuery(id+"F6.wireOp",EDGE,"E2133"),sQuery(id+"F6.wireOp",EDGE,"E2134"),sQuery(id+"F6.wireOp",EDGE,"E2135"),sQuery(id+"F6.wireOp",EDGE,"E2136"),sQuery(id+"F6.wireOp",EDGE,"E2137"),sQuery(id+"F6.wireOp",EDGE,"E2138"),sQuery(id+"F6.wireOp",EDGE,"E2139"),sQuery(id+"F6.wireOp",EDGE,"E2140"),sQuery(id+"F6.wireOp",EDGE,"E2141"),sQuery(id+"F6.wireOp",EDGE,"E2142"),sQuery(id+"F6.wireOp",EDGE,"E2143"),sQuery(id+"F6.wireOp",EDGE,"E2144"),sQuery(id+"F6.wireOp",EDGE,"E2145"),sQuery(id+"F6.wireOp",EDGE,"E2146"),sQuery(id+"F6.wireOp",EDGE,"E2147"),sQuery(id+"F6.wireOp",EDGE,"E2148"),sQuery(id+"F6.wireOp",EDGE,"E2149"),sQuery(id+"F6.wireOp",EDGE,"E2150"),sQuery(id+"F6.wireOp",EDGE,"E2151"),sQuery(id+"F6.wireOp",EDGE,"E2152"),sQuery(id+"F6.wireOp",EDGE,"E2153"),sQuery(id+"F6.wireOp",EDGE,"E2154"),sQuery(id+"F6.wireOp",EDGE,"E2155"),sQuery(id+"F6.wireOp",EDGE,"E2156"),sQuery(id+"F6.wireOp",EDGE,"E2157"),sQuery(id+"F6.wireOp",EDGE,"E2158"),sQuery(id+"F6.wireOp",EDGE,"E2159"),sQuery(id+"F6.wireOp",EDGE,"E2160"),sQuery(id+"F6.wireOp",EDGE,"E2161"),sQuery(id+"F6.wireOp",EDGE,"E2162"),sQuery(id+"F6.wireOp",EDGE,"E2163"),sQuery(id+"F6.wireOp",EDGE,"E2164"),sQuery(id+"F6.wireOp",EDGE,"E2165"),sQuery(id+"F6.wireOp",EDGE,"E2166"),sQuery(id+"F6.wireOp",EDGE,"E2167"),sQuery(id+"F6.wireOp",EDGE,"E2168"),sQuery(id+"F6.wireOp",EDGE,"E2169"),sQuery(id+"F6.wireOp",EDGE,"E2170"),sQuery(id+"F6.wireOp",EDGE,"E2171"),sQuery(id+"F6.wireOp",EDGE,"E2172"),sQuery(id+"F6.wireOp",EDGE,"E2173"),sQuery(id+"F6.wireOp",EDGE,"E2174"),sQuery(id+"F6.wireOp",EDGE,"E2175"),sQuery(id+"F6.wireOp",EDGE,"E2176"),sQuery(id+"F6.wireOp",EDGE,"E2177"),sQuery(id+"F6.wireOp",EDGE,"E2178"),sQuery(id+"F6.wireOp",EDGE,"E2179"),sQuery(id+"F6.wireOp",EDGE,"E2180"),sQuery(id+"F6.wireOp",EDGE,"E2181"),sQuery(id+"F6.wireOp",EDGE,"E2182"),sQuery(id+"F6.wireOp",EDGE,"E2183"),sQuery(id+"F6.wireOp",EDGE,"E2184"),sQuery(id+"F6.wireOp",EDGE,"E2185"),sQuery(id+"F6.wireOp",EDGE,"E2186"),sQuery(id+"F6.wireOp",EDGE,"E2187"),sQuery(id+"F6.wireOp",EDGE,"E2188"),sQuery(id+"F6.wireOp",EDGE,"E2189"),sQuery(id+"F6.wireOp",EDGE,"E2190"),sQuery(id+"F6.wireOp",EDGE,"E2191"),sQuery(id+"F6.wireOp",EDGE,"E2192"),sQuery(id+"F6.wireOp",EDGE,"E2193"),sQuery(id+"F6.wireOp",EDGE,"E2194"),sQuery(id+"F6.wireOp",EDGE,"E2195"),sQuery(id+"F6.wireOp",EDGE,"E2196"),sQuery(id+"F6.wireOp",EDGE,"E2197"),sQuery(id+"F6.wireOp",EDGE,"E2198"),sQuery(id+"F6.wireOp",EDGE,"E2199"),sQuery(id+"F6.wireOp",EDGE,"E2200"),sQuery(id+"F6.wireOp",EDGE,"E2201"),sQuery(id+"F6.wireOp",EDGE,"E2202"),sQuery(id+"F6.wireOp",EDGE,"E2203"),sQuery(id+"F6.wireOp",EDGE,"E2204"),sQuery(id+"F6.wireOp",EDGE,"E2205"),sQuery(id+"F6.wireOp",EDGE,"E2206"),sQuery(id+"F6.wireOp",EDGE,"E2207"),sQuery(id+"F6.wireOp",EDGE,"E2208"),sQuery(id+"F6.wireOp",EDGE,"E2209"),sQuery(id+"F6.wireOp",EDGE,"E2210"),sQuery(id+"F6.wireOp",EDGE,"E2211"),sQuery(id+"F6.wireOp",EDGE,"E2212"),sQuery(id+"F6.wireOp",EDGE,"E2213"),sQuery(id+"F6.wireOp",EDGE,"E2214"),sQuery(id+"F6.wireOp",EDGE,"E2215"),sQuery(id+"F6.wireOp",EDGE,"E2216"),sQuery(id+"F6.wireOp",EDGE,"E2217"),sQuery(id+"F6.wireOp",EDGE,"E2218"),sQuery(id+"F6.wireOp",EDGE,"E2219"),sQuery(id+"F6.wireOp",EDGE,"E2220"),sQuery(id+"F6.wireOp",EDGE,"E2221"),sQuery(id+"F6.wireOp",EDGE,"E2222"),sQuery(id+"F6.wireOp",EDGE,"E2223"),sQuery(id+"F6.wireOp",EDGE,"E2224"),sQuery(id+"F6.wireOp",EDGE,"E2225"),sQuery(id+"F6.wireOp",EDGE,"E2226"),sQuery(id+"F6.wireOp",EDGE,"E2227"),sQuery(id+"F6.wireOp",EDGE,"E2228"),sQuery(id+"F6.wireOp",EDGE,"E2229"),sQuery(id+"F6.wireOp",EDGE,"E2230"),sQuery(id+"F6.wireOp",EDGE,"E2231"),sQuery(id+"F6.wireOp",EDGE,"E2232"),sQuery(id+"F6.wireOp",EDGE,"E2233"),sQuery(id+"F6.wireOp",EDGE,"E2234"),sQuery(id+"F6.wireOp",EDGE,"E2235"),sQuery(id+"F6.wireOp",EDGE,"E2236"),sQuery(id+"F6.wireOp",EDGE,"E2237"),sQuery(id+"F6.wireOp",EDGE,"E2238"),sQuery(id+"F6.wireOp",EDGE,"E2239"),sQuery(id+"F6.wireOp",EDGE,"E2240"),sQuery(id+"F6.wireOp",EDGE,"E2241"),sQuery(id+"F6.wireOp",EDGE,"E2242"),sQuery(id+"F6.wireOp",EDGE,"E2243"),sQuery(id+"F6.wireOp",EDGE,"E2244"),sQuery(id+"F6.wireOp",EDGE,"E2245"),sQuery(id+"F6.wireOp",EDGE,"E2246"),sQuery(id+"F6.wireOp",EDGE,"E2247"),sQuery(id+"F6.wireOp",EDGE,"E2248"),sQuery(id+"F6.wireOp",EDGE,"E2249"),sQuery(id+"F6.wireOp",EDGE,"E2250"),sQuery(id+"F6.wireOp",EDGE,"E2251"),sQuery(id+"F6.wireOp",EDGE,"E2252"),sQuery(id+"F6.wireOp",EDGE,"E2253"),sQuery(id+"F6.wireOp",EDGE,"E2254"),sQuery(id+"F6.wireOp",EDGE,"E2255"),sQuery(id+"F6.wireOp",EDGE,"E2256"),sQuery(id+"F6.wireOp",EDGE,"E2257"),sQuery(id+"F6.wireOp",EDGE,"E2258"),sQuery(id+"F6.wireOp",EDGE,"E2259"),sQuery(id+"F6.wireOp",EDGE,"E2260"),sQuery(id+"F6.wireOp",EDGE,"E2261"),sQuery(id+"F6.wireOp",EDGE,"E2262"),sQuery(id+"F6.wireOp",EDGE,"E2263"),sQuery(id+"F6.wireOp",EDGE,"E2264"),sQuery(id+"F6.wireOp",EDGE,"E2265"),sQuery(id+"F6.wireOp",EDGE,"E2266"),sQuery(id+"F6.wireOp",EDGE,"E2267"),sQuery(id+"F6.wireOp",EDGE,"E2268"),sQuery(id+"F6.wireOp",EDGE,"E2269"),sQuery(id+"F6.wireOp",EDGE,"E2270"),sQuery(id+"F6.wireOp",EDGE,"E2271"),sQuery(id+"F6.wireOp",EDGE,"E2272"),sQuery(id+"F6.wireOp",EDGE,"E2273"),sQuery(id+"F6.wireOp",EDGE,"E2274"),sQuery(id+"F6.wireOp",EDGE,"E2275"),sQuery(id+"F6.wireOp",EDGE,"E2276"),sQuery(id+"F6.wireOp",EDGE,"E2277"),sQuery(id+"F6.wireOp",EDGE,"E2278"),sQuery(id+"F6.wireOp",EDGE,"E2279"),sQuery(id+"F6.wireOp",EDGE,"E2280"),sQuery(id+"F6.wireOp",EDGE,"E2281"),sQuery(id+"F6.wireOp",EDGE,"E2282"),sQuery(id+"F6.wireOp",EDGE,"E2283"),sQuery(id+"F6.wireOp",EDGE,"E2284"),sQuery(id+"F6.wireOp",EDGE,"E2285"),sQuery(id+"F6.wireOp",EDGE,"E2286"),sQuery(id+"F6.wireOp",EDGE,"E2287"),sQuery(id+"F6.wireOp",EDGE,"E2288"),sQuery(id+"F6.wireOp",EDGE,"E2289"),sQuery(id+"F6.wireOp",EDGE,"E2290"),sQuery(id+"F6.wireOp",EDGE,"E2291"),sQuery(id+"F6.wireOp",EDGE,"E2292"),sQuery(id+"F6.wireOp",EDGE,"E2293"),sQuery(id+"F6.wireOp",EDGE,"E2294"),sQuery(id+"F6.wireOp",EDGE,"E2295"),sQuery(id+"F6.wireOp",EDGE,"E2296"),sQuery(id+"F6.wireOp",EDGE,"E2297"),sQuery(id+"F6.wireOp",EDGE,"E2298"),sQuery(id+"F6.wireOp",EDGE,"E2299"),sQuery(id+"F6.wireOp",EDGE,"E2300"),sQuery(id+"F6.wireOp",EDGE,"E2301"),sQuery(id+"F6.wireOp",EDGE,"E2302"),sQuery(id+"F6.wireOp",EDGE,"E2303"),sQuery(id+"F6.wireOp",EDGE,"E2304"),sQuery(id+"F6.wireOp",EDGE,"E2305"),sQuery(id+"F6.wireOp",EDGE,"E2306"),sQuery(id+"F6.wireOp",EDGE,"E2307"),sQuery(id+"F6.wireOp",EDGE,"E2308"),sQuery(id+"F6.wireOp",EDGE,"E2309"),sQuery(id+"F6.wireOp",EDGE,"E2310"),sQuery(id+"F6.wireOp",EDGE,"E2311"),sQuery(id+"F6.wireOp",EDGE,"E2312"),sQuery(id+"F6.wireOp",EDGE,"E2313"),sQuery(id+"F6.wireOp",EDGE,"E2314"),sQuery(id+"F6.wireOp",EDGE,"E2315"),sQuery(id+"F6.wireOp",EDGE,"E2316"),sQuery(id+"F6.wireOp",EDGE,"E2317"),sQuery(id+"F6.wireOp",EDGE,"E2318"),sQuery(id+"F6.wireOp",EDGE,"E2319"),sQuery(id+"F6.wireOp",EDGE,"E2320"),sQuery(id+"F6.wireOp",EDGE,"E2321"),sQuery(id+"F6.wireOp",EDGE,"E2322"),sQuery(id+"F6.wireOp",EDGE,"E2323"),sQuery(id+"F6.wireOp",EDGE,"E2324"),sQuery(id+"F6.wireOp",EDGE,"E2325"),sQuery(id+"F6.wireOp",EDGE,"E2326"),sQuery(id+"F6.wireOp",EDGE,"E2327"),sQuery(id+"F6.wireOp",EDGE,"E2328"),sQuery(id+"F6.wireOp",EDGE,"E2329"),sQuery(id+"F6.wireOp",EDGE,"E2330"),sQuery(id+"F6.wireOp",EDGE,"E2331"),sQuery(id+"F6.wireOp",EDGE,"E2332"),sQuery(id+"F6.wireOp",EDGE,"E2333"),sQuery(id+"F6.wireOp",EDGE,"E2334"),sQuery(id+"F6.wireOp",EDGE,"E2335"),sQuery(id+"F6.wireOp",EDGE,"E2336"),sQuery(id+"F6.wireOp",EDGE,"E2337"),sQuery(id+"F6.wireOp",EDGE,"E2338"),sQuery(id+"F6.wireOp",EDGE,"E2339"),sQuery(id+"F6.wireOp",EDGE,"E2340"),sQuery(id+"F6.wireOp",EDGE,"E2341"),sQuery(id+"F6.wireOp",EDGE,"E2342"),sQuery(id+"F6.wireOp",EDGE,"E2343"),sQuery(id+"F6.wireOp",EDGE,"E2344"),sQuery(id+"F6.wireOp",EDGE,"E2345"),sQuery(id+"F6.wireOp",EDGE,"E2346"),sQuery(id+"F6.wireOp",EDGE,"E2347"),sQuery(id+"F6.wireOp",EDGE,"E2348"),sQuery(id+"F6.wireOp",EDGE,"E2349"),sQuery(id+"F6.wireOp",EDGE,"E2350"),sQuery(id+"F6.wireOp",EDGE,"E2351"),sQuery(id+"F6.wireOp",EDGE,"E2352"),sQuery(id+"F6.wireOp",EDGE,"E2353"),sQuery(id+"F6.wireOp",EDGE,"E2354"),sQuery(id+"F6.wireOp",EDGE,"E2355"),sQuery(id+"F6.wireOp",EDGE,"E2356"),sQuery(id+"F6.wireOp",EDGE,"E2357"),sQuery(id+"F6.wireOp",EDGE,"E2358"),sQuery(id+"F6.wireOp",EDGE,"E2359"),sQuery(id+"F6.wireOp",EDGE,"E2360"),sQuery(id+"F6.wireOp",EDGE,"E2361"),sQuery(id+"F6.wireOp",EDGE,"E2362"),sQuery(id+"F6.wireOp",EDGE,"E2363"),sQuery(id+"F6.wireOp",EDGE,"E2364"),sQuery(id+"F6.wireOp",EDGE,"E2365"),sQuery(id+"F6.wireOp",EDGE,"E2366"),sQuery(id+"F6.wireOp",EDGE,"E2367"),sQuery(id+"F6.wireOp",EDGE,"E2368"),sQuery(id+"F6.wireOp",EDGE,"E2369"),sQuery(id+"F6.wireOp",EDGE,"E2370"),sQuery(id+"F6.wireOp",EDGE,"E2371"),sQuery(id+"F6.wireOp",EDGE,"E2372"),sQuery(id+"F6.wireOp",EDGE,"E2373"),sQuery(id+"F6.wireOp",EDGE,"E2374"),sQuery(id+"F6.wireOp",EDGE,"E2375"),sQuery(id+"F6.wireOp",EDGE,"E2376"),sQuery(id+"F6.wireOp",EDGE,"E2377"),sQuery(id+"F6.wireOp",EDGE,"E2378"),sQuery(id+"F6.wireOp",EDGE,"E2379"),sQuery(id+"F6.wireOp",EDGE,"E2380"),sQuery(id+"F6.wireOp",EDGE,"E2381"),sQuery(id+"F6.wireOp",EDGE,"E2382"),sQuery(id+"F6.wireOp",EDGE,"E2383"),sQuery(id+"F6.wireOp",EDGE,"E2384"),sQuery(id+"F6.wireOp",EDGE,"E2385"),sQuery(id+"F6.wireOp",EDGE,"E2386"),sQuery(id+"F6.wireOp",EDGE,"E2387"),sQuery(id+"F6.wireOp",EDGE,"E2388"),sQuery(id+"F6.wireOp",EDGE,"E2389"),sQuery(id+"F6.wireOp",EDGE,"E2390"),sQuery(id+"F6.wireOp",EDGE,"E2391"),sQuery(id+"F6.wireOp",EDGE,"E2392"),sQuery(id+"F6.wireOp",EDGE,"E2393"),sQuery(id+"F6.wireOp",EDGE,"E2394"),sQuery(id+"F6.wireOp",EDGE,"E2395"),sQuery(id+"F6.wireOp",EDGE,"E2396"),sQuery(id+"F6.wireOp",EDGE,"E2397"),sQuery(id+"F6.wireOp",EDGE,"E2398"),sQuery(id+"F6.wireOp",EDGE,"E2399"),sQuery(id+"F6.wireOp",EDGE,"E2400"),sQuery(id+"F6.wireOp",EDGE,"E2401"),sQuery(id+"F6.wireOp",EDGE,"E2402"),sQuery(id+"F6.wireOp",EDGE,"E2403"),sQuery(id+"F6.wireOp",EDGE,"E2404"),sQuery(id+"F6.wireOp",EDGE,"E2405"),sQuery(id+"F6.wireOp",EDGE,"E2406"),sQuery(id+"F6.wireOp",EDGE,"E2407"),sQuery(id+"F6.wireOp",EDGE,"E2408"),sQuery(id+"F6.wireOp",EDGE,"E2409"),sQuery(id+"F6.wireOp",EDGE,"E2410"),sQuery(id+"F6.wireOp",EDGE,"E2411"),sQuery(id+"F6.wireOp",EDGE,"E2412"),sQuery(id+"F6.wireOp",EDGE,"E2413"),sQuery(id+"F6.wireOp",EDGE,"E2414"),sQuery(id+"F6.wireOp",EDGE,"E2415"),sQuery(id+"F6.wireOp",EDGE,"E2416"),sQuery(id+"F6.wireOp",EDGE,"E2417"),sQuery(id+"F6.wireOp",EDGE,"E2418"),sQuery(id+"F6.wireOp",EDGE,"E2419"),sQuery(id+"F6.wireOp",EDGE,"E2420"),sQuery(id+"F6.wireOp",EDGE,"E2421"),sQuery(id+"F6.wireOp",EDGE,"E2422"),sQuery(id+"F6.wireOp",EDGE,"E2423"),sQuery(id+"F6.wireOp",EDGE,"E2424"),sQuery(id+"F6.wireOp",EDGE,"E2425"),sQuery(id+"F6.wireOp",EDGE,"E2426"),sQuery(id+"F6.wireOp",EDGE,"E2427"),sQuery(id+"F6.wireOp",EDGE,"E2428"),sQuery(id+"F6.wireOp",EDGE,"E2429"),sQuery(id+"F6.wireOp",EDGE,"E2430"),sQuery(id+"F6.wireOp",EDGE,"E2431"),sQuery(id+"F6.wireOp",EDGE,"E2432"),sQuery(id+"F6.wireOp",EDGE,"E2433"),sQuery(id+"F6.wireOp",EDGE,"E2434"),sQuery(id+"F6.wireOp",EDGE,"E2435")])]});
            var Q1;
            Q1=sQuery(id+"F4.wireOp",EDGE,"E36");
            transform(context, id + "F8", {"entities" : qUnion([Q0]), "transformType" : TransformType.ROTATION, "transformAxis" : qUnion([Q1]), "angle" : 90 * degree, "makeCopy" : false});
        }
        {
            var Q0;
            Q0=qCreatedBy(makeId("Front.planeOp"),FACE);
            var sketch = newSketch(context, id + "F9", { "sketchPlane" : qUnion([Q0])});
            skPoint(sketch, "E2436", {"position": v(14.08, 0) * mm});
            skPoint(sketch, "E2437", {"position": v(40.65, 0) * mm});
            skSolve(sketch);
        }
        {
            var Q0;
            Q0=makeQuery(id+"F7.opExtrude","SWEPT_BODY",BODY,{"disambiguationData":[OSD([sQuery(id+"F6.wireOp",EDGE,"E37"),sQuery(id+"F6.wireOp",EDGE,"E38"),sQuery(id+"F6.wireOp",EDGE,"E39"),sQuery(id+"F6.wireOp",EDGE,"E40"),sQuery(id+"F6.wireOp",EDGE,"E41"),sQuery(id+"F6.wireOp",EDGE,"E42"),sQuery(id+"F6.wireOp",EDGE,"E43"),sQuery(id+"F6.wireOp",EDGE,"E44"),sQuery(id+"F6.wireOp",EDGE,"E45"),sQuery(id+"F6.wireOp",EDGE,"E46"),sQuery(id+"F6.wireOp",EDGE,"E47"),sQuery(id+"F6.wireOp",EDGE,"E48"),sQuery(id+"F6.wireOp",EDGE,"E49"),sQuery(id+"F6.wireOp",EDGE,"E50"),sQuery(id+"F6.wireOp",EDGE,"E51"),sQuery(id+"F6.wireOp",EDGE,"E52"),sQuery(id+"F6.wireOp",EDGE,"E53"),sQuery(id+"F6.wireOp",EDGE,"E54"),sQuery(id+"F6.wireOp",EDGE,"E55"),sQuery(id+"F6.wireOp",EDGE,"E56"),sQuery(id+"F6.wireOp",EDGE,"E57"),sQuery(id+"F6.wireOp",EDGE,"E58"),sQuery(id+"F6.wireOp",EDGE,"E59"),sQuery(id+"F6.wireOp",EDGE,"E60"),sQuery(id+"F6.wireOp",EDGE,"E61"),sQuery(id+"F6.wireOp",EDGE,"E62"),sQuery(id+"F6.wireOp",EDGE,"E63"),sQuery(id+"F6.wireOp",EDGE,"E64"),sQuery(id+"F6.wireOp",EDGE,"E65"),sQuery(id+"F6.wireOp",EDGE,"E66"),sQuery(id+"F6.wireOp",EDGE,"E67"),sQuery(id+"F6.wireOp",EDGE,"E68"),sQuery(id+"F6.wireOp",EDGE,"E69"),sQuery(id+"F6.wireOp",EDGE,"E70"),sQuery(id+"F6.wireOp",EDGE,"E71"),sQuery(id+"F6.wireOp",EDGE,"E72"),sQuery(id+"F6.wireOp",EDGE,"E73"),sQuery(id+"F6.wireOp",EDGE,"E74"),sQuery(id+"F6.wireOp",EDGE,"E75"),sQuery(id+"F6.wireOp",EDGE,"E76"),sQuery(id+"F6.wireOp",EDGE,"E77"),sQuery(id+"F6.wireOp",EDGE,"E78"),sQuery(id+"F6.wireOp",EDGE,"E79"),sQuery(id+"F6.wireOp",EDGE,"E80"),sQuery(id+"F6.wireOp",EDGE,"E81"),sQuery(id+"F6.wireOp",EDGE,"E82"),sQuery(id+"F6.wireOp",EDGE,"E83"),sQuery(id+"F6.wireOp",EDGE,"E84"),sQuery(id+"F6.wireOp",EDGE,"E85"),sQuery(id+"F6.wireOp",EDGE,"E86"),sQuery(id+"F6.wireOp",EDGE,"E87"),sQuery(id+"F6.wireOp",EDGE,"E88"),sQuery(id+"F6.wireOp",EDGE,"E89"),sQuery(id+"F6.wireOp",EDGE,"E90"),sQuery(id+"F6.wireOp",EDGE,"E91"),sQuery(id+"F6.wireOp",EDGE,"E92"),sQuery(id+"F6.wireOp",EDGE,"E93"),sQuery(id+"F6.wireOp",EDGE,"E94"),sQuery(id+"F6.wireOp",EDGE,"E95"),sQuery(id+"F6.wireOp",EDGE,"E96"),sQuery(id+"F6.wireOp",EDGE,"E97"),sQuery(id+"F6.wireOp",EDGE,"E98"),sQuery(id+"F6.wireOp",EDGE,"E99"),sQuery(id+"F6.wireOp",EDGE,"E100"),sQuery(id+"F6.wireOp",EDGE,"E101"),sQuery(id+"F6.wireOp",EDGE,"E102"),sQuery(id+"F6.wireOp",EDGE,"E103"),sQuery(id+"F6.wireOp",EDGE,"E104"),sQuery(id+"F6.wireOp",EDGE,"E105"),sQuery(id+"F6.wireOp",EDGE,"E106"),sQuery(id+"F6.wireOp",EDGE,"E107"),sQuery(id+"F6.wireOp",EDGE,"E108"),sQuery(id+"F6.wireOp",EDGE,"E109"),sQuery(id+"F6.wireOp",EDGE,"E110"),sQuery(id+"F6.wireOp",EDGE,"E111"),sQuery(id+"F6.wireOp",EDGE,"E112"),sQuery(id+"F6.wireOp",EDGE,"E113"),sQuery(id+"F6.wireOp",EDGE,"E114"),sQuery(id+"F6.wireOp",EDGE,"E115"),sQuery(id+"F6.wireOp",EDGE,"E116"),sQuery(id+"F6.wireOp",EDGE,"E117"),sQuery(id+"F6.wireOp",EDGE,"E118"),sQuery(id+"F6.wireOp",EDGE,"E119"),sQuery(id+"F6.wireOp",EDGE,"E120"),sQuery(id+"F6.wireOp",EDGE,"E121"),sQuery(id+"F6.wireOp",EDGE,"E122"),sQuery(id+"F6.wireOp",EDGE,"E123"),sQuery(id+"F6.wireOp",EDGE,"E124"),sQuery(id+"F6.wireOp",EDGE,"E125"),sQuery(id+"F6.wireOp",EDGE,"E126"),sQuery(id+"F6.wireOp",EDGE,"E127"),sQuery(id+"F6.wireOp",EDGE,"E128"),sQuery(id+"F6.wireOp",EDGE,"E129"),sQuery(id+"F6.wireOp",EDGE,"E130"),sQuery(id+"F6.wireOp",EDGE,"E131"),sQuery(id+"F6.wireOp",EDGE,"E132"),sQuery(id+"F6.wireOp",EDGE,"E133"),sQuery(id+"F6.wireOp",EDGE,"E134"),sQuery(id+"F6.wireOp",EDGE,"E135"),sQuery(id+"F6.wireOp",EDGE,"E136"),sQuery(id+"F6.wireOp",EDGE,"E137"),sQuery(id+"F6.wireOp",EDGE,"E138"),sQuery(id+"F6.wireOp",EDGE,"E139"),sQuery(id+"F6.wireOp",EDGE,"E140"),sQuery(id+"F6.wireOp",EDGE,"E141"),sQuery(id+"F6.wireOp",EDGE,"E142"),sQuery(id+"F6.wireOp",EDGE,"E143"),sQuery(id+"F6.wireOp",EDGE,"E144"),sQuery(id+"F6.wireOp",EDGE,"E145"),sQuery(id+"F6.wireOp",EDGE,"E146"),sQuery(id+"F6.wireOp",EDGE,"E147"),sQuery(id+"F6.wireOp",EDGE,"E148"),sQuery(id+"F6.wireOp",EDGE,"E149"),sQuery(id+"F6.wireOp",EDGE,"E150"),sQuery(id+"F6.wireOp",EDGE,"E151"),sQuery(id+"F6.wireOp",EDGE,"E152"),sQuery(id+"F6.wireOp",EDGE,"E153"),sQuery(id+"F6.wireOp",EDGE,"E154"),sQuery(id+"F6.wireOp",EDGE,"E155"),sQuery(id+"F6.wireOp",EDGE,"E156"),sQuery(id+"F6.wireOp",EDGE,"E157"),sQuery(id+"F6.wireOp",EDGE,"E158"),sQuery(id+"F6.wireOp",EDGE,"E159"),sQuery(id+"F6.wireOp",EDGE,"E160"),sQuery(id+"F6.wireOp",EDGE,"E161"),sQuery(id+"F6.wireOp",EDGE,"E162"),sQuery(id+"F6.wireOp",EDGE,"E163"),sQuery(id+"F6.wireOp",EDGE,"E164"),sQuery(id+"F6.wireOp",EDGE,"E165"),sQuery(id+"F6.wireOp",EDGE,"E166"),sQuery(id+"F6.wireOp",EDGE,"E167"),sQuery(id+"F6.wireOp",EDGE,"E168"),sQuery(id+"F6.wireOp",EDGE,"E169"),sQuery(id+"F6.wireOp",EDGE,"E170"),sQuery(id+"F6.wireOp",EDGE,"E171"),sQuery(id+"F6.wireOp",EDGE,"E172"),sQuery(id+"F6.wireOp",EDGE,"E173"),sQuery(id+"F6.wireOp",EDGE,"E174"),sQuery(id+"F6.wireOp",EDGE,"E175"),sQuery(id+"F6.wireOp",EDGE,"E176"),sQuery(id+"F6.wireOp",EDGE,"E177"),sQuery(id+"F6.wireOp",EDGE,"E178"),sQuery(id+"F6.wireOp",EDGE,"E179"),sQuery(id+"F6.wireOp",EDGE,"E180"),sQuery(id+"F6.wireOp",EDGE,"E181"),sQuery(id+"F6.wireOp",EDGE,"E182"),sQuery(id+"F6.wireOp",EDGE,"E183"),sQuery(id+"F6.wireOp",EDGE,"E184"),sQuery(id+"F6.wireOp",EDGE,"E185"),sQuery(id+"F6.wireOp",EDGE,"E186"),sQuery(id+"F6.wireOp",EDGE,"E187"),sQuery(id+"F6.wireOp",EDGE,"E188"),sQuery(id+"F6.wireOp",EDGE,"E189"),sQuery(id+"F6.wireOp",EDGE,"E190"),sQuery(id+"F6.wireOp",EDGE,"E191"),sQuery(id+"F6.wireOp",EDGE,"E192"),sQuery(id+"F6.wireOp",EDGE,"E193"),sQuery(id+"F6.wireOp",EDGE,"E194"),sQuery(id+"F6.wireOp",EDGE,"E195"),sQuery(id+"F6.wireOp",EDGE,"E196"),sQuery(id+"F6.wireOp",EDGE,"E197"),sQuery(id+"F6.wireOp",EDGE,"E198"),sQuery(id+"F6.wireOp",EDGE,"E199"),sQuery(id+"F6.wireOp",EDGE,"E200"),sQuery(id+"F6.wireOp",EDGE,"E201"),sQuery(id+"F6.wireOp",EDGE,"E202"),sQuery(id+"F6.wireOp",EDGE,"E203"),sQuery(id+"F6.wireOp",EDGE,"E204"),sQuery(id+"F6.wireOp",EDGE,"E205"),sQuery(id+"F6.wireOp",EDGE,"E206"),sQuery(id+"F6.wireOp",EDGE,"E207"),sQuery(id+"F6.wireOp",EDGE,"E208"),sQuery(id+"F6.wireOp",EDGE,"E209"),sQuery(id+"F6.wireOp",EDGE,"E210"),sQuery(id+"F6.wireOp",EDGE,"E211"),sQuery(id+"F6.wireOp",EDGE,"E212"),sQuery(id+"F6.wireOp",EDGE,"E213"),sQuery(id+"F6.wireOp",EDGE,"E214"),sQuery(id+"F6.wireOp",EDGE,"E215"),sQuery(id+"F6.wireOp",EDGE,"E216"),sQuery(id+"F6.wireOp",EDGE,"E217"),sQuery(id+"F6.wireOp",EDGE,"E218"),sQuery(id+"F6.wireOp",EDGE,"E219"),sQuery(id+"F6.wireOp",EDGE,"E220"),sQuery(id+"F6.wireOp",EDGE,"E221"),sQuery(id+"F6.wireOp",EDGE,"E222"),sQuery(id+"F6.wireOp",EDGE,"E223"),sQuery(id+"F6.wireOp",EDGE,"E224"),sQuery(id+"F6.wireOp",EDGE,"E225"),sQuery(id+"F6.wireOp",EDGE,"E226"),sQuery(id+"F6.wireOp",EDGE,"E227"),sQuery(id+"F6.wireOp",EDGE,"E228"),sQuery(id+"F6.wireOp",EDGE,"E229"),sQuery(id+"F6.wireOp",EDGE,"E230"),sQuery(id+"F6.wireOp",EDGE,"E231"),sQuery(id+"F6.wireOp",EDGE,"E232"),sQuery(id+"F6.wireOp",EDGE,"E233"),sQuery(id+"F6.wireOp",EDGE,"E234"),sQuery(id+"F6.wireOp",EDGE,"E235"),sQuery(id+"F6.wireOp",EDGE,"E236"),sQuery(id+"F6.wireOp",EDGE,"E237"),sQuery(id+"F6.wireOp",EDGE,"E238"),sQuery(id+"F6.wireOp",EDGE,"E239"),sQuery(id+"F6.wireOp",EDGE,"E240"),sQuery(id+"F6.wireOp",EDGE,"E241"),sQuery(id+"F6.wireOp",EDGE,"E242"),sQuery(id+"F6.wireOp",EDGE,"E243"),sQuery(id+"F6.wireOp",EDGE,"E244"),sQuery(id+"F6.wireOp",EDGE,"E245"),sQuery(id+"F6.wireOp",EDGE,"E246"),sQuery(id+"F6.wireOp",EDGE,"E247"),sQuery(id+"F6.wireOp",EDGE,"E248"),sQuery(id+"F6.wireOp",EDGE,"E249"),sQuery(id+"F6.wireOp",EDGE,"E250"),sQuery(id+"F6.wireOp",EDGE,"E251"),sQuery(id+"F6.wireOp",EDGE,"E252"),sQuery(id+"F6.wireOp",EDGE,"E253"),sQuery(id+"F6.wireOp",EDGE,"E254"),sQuery(id+"F6.wireOp",EDGE,"E255"),sQuery(id+"F6.wireOp",EDGE,"E256"),sQuery(id+"F6.wireOp",EDGE,"E257"),sQuery(id+"F6.wireOp",EDGE,"E258"),sQuery(id+"F6.wireOp",EDGE,"E259"),sQuery(id+"F6.wireOp",EDGE,"E260"),sQuery(id+"F6.wireOp",EDGE,"E261"),sQuery(id+"F6.wireOp",EDGE,"E262"),sQuery(id+"F6.wireOp",EDGE,"E263"),sQuery(id+"F6.wireOp",EDGE,"E264"),sQuery(id+"F6.wireOp",EDGE,"E265"),sQuery(id+"F6.wireOp",EDGE,"E266"),sQuery(id+"F6.wireOp",EDGE,"E267"),sQuery(id+"F6.wireOp",EDGE,"E268"),sQuery(id+"F6.wireOp",EDGE,"E269"),sQuery(id+"F6.wireOp",EDGE,"E270"),sQuery(id+"F6.wireOp",EDGE,"E271"),sQuery(id+"F6.wireOp",EDGE,"E272"),sQuery(id+"F6.wireOp",EDGE,"E273"),sQuery(id+"F6.wireOp",EDGE,"E274"),sQuery(id+"F6.wireOp",EDGE,"E275"),sQuery(id+"F6.wireOp",EDGE,"E276"),sQuery(id+"F6.wireOp",EDGE,"E277"),sQuery(id+"F6.wireOp",EDGE,"E278"),sQuery(id+"F6.wireOp",EDGE,"E279"),sQuery(id+"F6.wireOp",EDGE,"E280"),sQuery(id+"F6.wireOp",EDGE,"E281"),sQuery(id+"F6.wireOp",EDGE,"E282"),sQuery(id+"F6.wireOp",EDGE,"E283"),sQuery(id+"F6.wireOp",EDGE,"E284"),sQuery(id+"F6.wireOp",EDGE,"E285"),sQuery(id+"F6.wireOp",EDGE,"E286"),sQuery(id+"F6.wireOp",EDGE,"E287"),sQuery(id+"F6.wireOp",EDGE,"E288"),sQuery(id+"F6.wireOp",EDGE,"E289"),sQuery(id+"F6.wireOp",EDGE,"E290"),sQuery(id+"F6.wireOp",EDGE,"E291"),sQuery(id+"F6.wireOp",EDGE,"E292"),sQuery(id+"F6.wireOp",EDGE,"E293"),sQuery(id+"F6.wireOp",EDGE,"E294"),sQuery(id+"F6.wireOp",EDGE,"E295"),sQuery(id+"F6.wireOp",EDGE,"E296"),sQuery(id+"F6.wireOp",EDGE,"E297"),sQuery(id+"F6.wireOp",EDGE,"E298"),sQuery(id+"F6.wireOp",EDGE,"E299"),sQuery(id+"F6.wireOp",EDGE,"E300"),sQuery(id+"F6.wireOp",EDGE,"E301"),sQuery(id+"F6.wireOp",EDGE,"E302"),sQuery(id+"F6.wireOp",EDGE,"E303"),sQuery(id+"F6.wireOp",EDGE,"E304"),sQuery(id+"F6.wireOp",EDGE,"E305"),sQuery(id+"F6.wireOp",EDGE,"E306"),sQuery(id+"F6.wireOp",EDGE,"E307"),sQuery(id+"F6.wireOp",EDGE,"E308"),sQuery(id+"F6.wireOp",EDGE,"E309"),sQuery(id+"F6.wireOp",EDGE,"E310"),sQuery(id+"F6.wireOp",EDGE,"E311"),sQuery(id+"F6.wireOp",EDGE,"E312"),sQuery(id+"F6.wireOp",EDGE,"E313"),sQuery(id+"F6.wireOp",EDGE,"E314"),sQuery(id+"F6.wireOp",EDGE,"E315"),sQuery(id+"F6.wireOp",EDGE,"E316"),sQuery(id+"F6.wireOp",EDGE,"E317"),sQuery(id+"F6.wireOp",EDGE,"E318"),sQuery(id+"F6.wireOp",EDGE,"E319"),sQuery(id+"F6.wireOp",EDGE,"E320"),sQuery(id+"F6.wireOp",EDGE,"E321"),sQuery(id+"F6.wireOp",EDGE,"E322"),sQuery(id+"F6.wireOp",EDGE,"E323"),sQuery(id+"F6.wireOp",EDGE,"E324"),sQuery(id+"F6.wireOp",EDGE,"E325"),sQuery(id+"F6.wireOp",EDGE,"E326"),sQuery(id+"F6.wireOp",EDGE,"E327"),sQuery(id+"F6.wireOp",EDGE,"E328"),sQuery(id+"F6.wireOp",EDGE,"E329"),sQuery(id+"F6.wireOp",EDGE,"E330"),sQuery(id+"F6.wireOp",EDGE,"E331"),sQuery(id+"F6.wireOp",EDGE,"E332"),sQuery(id+"F6.wireOp",EDGE,"E333"),sQuery(id+"F6.wireOp",EDGE,"E334"),sQuery(id+"F6.wireOp",EDGE,"E335"),sQuery(id+"F6.wireOp",EDGE,"E336"),sQuery(id+"F6.wireOp",EDGE,"E337"),sQuery(id+"F6.wireOp",EDGE,"E338"),sQuery(id+"F6.wireOp",EDGE,"E339"),sQuery(id+"F6.wireOp",EDGE,"E340"),sQuery(id+"F6.wireOp",EDGE,"E341"),sQuery(id+"F6.wireOp",EDGE,"E342"),sQuery(id+"F6.wireOp",EDGE,"E343"),sQuery(id+"F6.wireOp",EDGE,"E344"),sQuery(id+"F6.wireOp",EDGE,"E345"),sQuery(id+"F6.wireOp",EDGE,"E346"),sQuery(id+"F6.wireOp",EDGE,"E347"),sQuery(id+"F6.wireOp",EDGE,"E348"),sQuery(id+"F6.wireOp",EDGE,"E349"),sQuery(id+"F6.wireOp",EDGE,"E350"),sQuery(id+"F6.wireOp",EDGE,"E351"),sQuery(id+"F6.wireOp",EDGE,"E352"),sQuery(id+"F6.wireOp",EDGE,"E353"),sQuery(id+"F6.wireOp",EDGE,"E354"),sQuery(id+"F6.wireOp",EDGE,"E355"),sQuery(id+"F6.wireOp",EDGE,"E356"),sQuery(id+"F6.wireOp",EDGE,"E357"),sQuery(id+"F6.wireOp",EDGE,"E358"),sQuery(id+"F6.wireOp",EDGE,"E359"),sQuery(id+"F6.wireOp",EDGE,"E360"),sQuery(id+"F6.wireOp",EDGE,"E361"),sQuery(id+"F6.wireOp",EDGE,"E362"),sQuery(id+"F6.wireOp",EDGE,"E363"),sQuery(id+"F6.wireOp",EDGE,"E364"),sQuery(id+"F6.wireOp",EDGE,"E365"),sQuery(id+"F6.wireOp",EDGE,"E366"),sQuery(id+"F6.wireOp",EDGE,"E367"),sQuery(id+"F6.wireOp",EDGE,"E368"),sQuery(id+"F6.wireOp",EDGE,"E369"),sQuery(id+"F6.wireOp",EDGE,"E370"),sQuery(id+"F6.wireOp",EDGE,"E371"),sQuery(id+"F6.wireOp",EDGE,"E372"),sQuery(id+"F6.wireOp",EDGE,"E373"),sQuery(id+"F6.wireOp",EDGE,"E374"),sQuery(id+"F6.wireOp",EDGE,"E375"),sQuery(id+"F6.wireOp",EDGE,"E376"),sQuery(id+"F6.wireOp",EDGE,"E377"),sQuery(id+"F6.wireOp",EDGE,"E378"),sQuery(id+"F6.wireOp",EDGE,"E379"),sQuery(id+"F6.wireOp",EDGE,"E380"),sQuery(id+"F6.wireOp",EDGE,"E381"),sQuery(id+"F6.wireOp",EDGE,"E382"),sQuery(id+"F6.wireOp",EDGE,"E383"),sQuery(id+"F6.wireOp",EDGE,"E384"),sQuery(id+"F6.wireOp",EDGE,"E385"),sQuery(id+"F6.wireOp",EDGE,"E386"),sQuery(id+"F6.wireOp",EDGE,"E387"),sQuery(id+"F6.wireOp",EDGE,"E388"),sQuery(id+"F6.wireOp",EDGE,"E389"),sQuery(id+"F6.wireOp",EDGE,"E390"),sQuery(id+"F6.wireOp",EDGE,"E391"),sQuery(id+"F6.wireOp",EDGE,"E392"),sQuery(id+"F6.wireOp",EDGE,"E393"),sQuery(id+"F6.wireOp",EDGE,"E394"),sQuery(id+"F6.wireOp",EDGE,"E395"),sQuery(id+"F6.wireOp",EDGE,"E396"),sQuery(id+"F6.wireOp",EDGE,"E397"),sQuery(id+"F6.wireOp",EDGE,"E398"),sQuery(id+"F6.wireOp",EDGE,"E399"),sQuery(id+"F6.wireOp",EDGE,"E400"),sQuery(id+"F6.wireOp",EDGE,"E401"),sQuery(id+"F6.wireOp",EDGE,"E402"),sQuery(id+"F6.wireOp",EDGE,"E403"),sQuery(id+"F6.wireOp",EDGE,"E404"),sQuery(id+"F6.wireOp",EDGE,"E405"),sQuery(id+"F6.wireOp",EDGE,"E406"),sQuery(id+"F6.wireOp",EDGE,"E407"),sQuery(id+"F6.wireOp",EDGE,"E408"),sQuery(id+"F6.wireOp",EDGE,"E409"),sQuery(id+"F6.wireOp",EDGE,"E410"),sQuery(id+"F6.wireOp",EDGE,"E411"),sQuery(id+"F6.wireOp",EDGE,"E412"),sQuery(id+"F6.wireOp",EDGE,"E413"),sQuery(id+"F6.wireOp",EDGE,"E414"),sQuery(id+"F6.wireOp",EDGE,"E415"),sQuery(id+"F6.wireOp",EDGE,"E416"),sQuery(id+"F6.wireOp",EDGE,"E417"),sQuery(id+"F6.wireOp",EDGE,"E418"),sQuery(id+"F6.wireOp",EDGE,"E419"),sQuery(id+"F6.wireOp",EDGE,"E420"),sQuery(id+"F6.wireOp",EDGE,"E421"),sQuery(id+"F6.wireOp",EDGE,"E422"),sQuery(id+"F6.wireOp",EDGE,"E423"),sQuery(id+"F6.wireOp",EDGE,"E424"),sQuery(id+"F6.wireOp",EDGE,"E425"),sQuery(id+"F6.wireOp",EDGE,"E426"),sQuery(id+"F6.wireOp",EDGE,"E427"),sQuery(id+"F6.wireOp",EDGE,"E428"),sQuery(id+"F6.wireOp",EDGE,"E429"),sQuery(id+"F6.wireOp",EDGE,"E430"),sQuery(id+"F6.wireOp",EDGE,"E431"),sQuery(id+"F6.wireOp",EDGE,"E432"),sQuery(id+"F6.wireOp",EDGE,"E433"),sQuery(id+"F6.wireOp",EDGE,"E434"),sQuery(id+"F6.wireOp",EDGE,"E435"),sQuery(id+"F6.wireOp",EDGE,"E436"),sQuery(id+"F6.wireOp",EDGE,"E437"),sQuery(id+"F6.wireOp",EDGE,"E438"),sQuery(id+"F6.wireOp",EDGE,"E439"),sQuery(id+"F6.wireOp",EDGE,"E440"),sQuery(id+"F6.wireOp",EDGE,"E441"),sQuery(id+"F6.wireOp",EDGE,"E442"),sQuery(id+"F6.wireOp",EDGE,"E443"),sQuery(id+"F6.wireOp",EDGE,"E444"),sQuery(id+"F6.wireOp",EDGE,"E445"),sQuery(id+"F6.wireOp",EDGE,"E446"),sQuery(id+"F6.wireOp",EDGE,"E447"),sQuery(id+"F6.wireOp",EDGE,"E448"),sQuery(id+"F6.wireOp",EDGE,"E449"),sQuery(id+"F6.wireOp",EDGE,"E450"),sQuery(id+"F6.wireOp",EDGE,"E451"),sQuery(id+"F6.wireOp",EDGE,"E452"),sQuery(id+"F6.wireOp",EDGE,"E453"),sQuery(id+"F6.wireOp",EDGE,"E454"),sQuery(id+"F6.wireOp",EDGE,"E455"),sQuery(id+"F6.wireOp",EDGE,"E456"),sQuery(id+"F6.wireOp",EDGE,"E457"),sQuery(id+"F6.wireOp",EDGE,"E458"),sQuery(id+"F6.wireOp",EDGE,"E459"),sQuery(id+"F6.wireOp",EDGE,"E460"),sQuery(id+"F6.wireOp",EDGE,"E461"),sQuery(id+"F6.wireOp",EDGE,"E462"),sQuery(id+"F6.wireOp",EDGE,"E463"),sQuery(id+"F6.wireOp",EDGE,"E464"),sQuery(id+"F6.wireOp",EDGE,"E465"),sQuery(id+"F6.wireOp",EDGE,"E466"),sQuery(id+"F6.wireOp",EDGE,"E467"),sQuery(id+"F6.wireOp",EDGE,"E468"),sQuery(id+"F6.wireOp",EDGE,"E469"),sQuery(id+"F6.wireOp",EDGE,"E470"),sQuery(id+"F6.wireOp",EDGE,"E471"),sQuery(id+"F6.wireOp",EDGE,"E472"),sQuery(id+"F6.wireOp",EDGE,"E473"),sQuery(id+"F6.wireOp",EDGE,"E474"),sQuery(id+"F6.wireOp",EDGE,"E475"),sQuery(id+"F6.wireOp",EDGE,"E476"),sQuery(id+"F6.wireOp",EDGE,"E477"),sQuery(id+"F6.wireOp",EDGE,"E478"),sQuery(id+"F6.wireOp",EDGE,"E479"),sQuery(id+"F6.wireOp",EDGE,"E480"),sQuery(id+"F6.wireOp",EDGE,"E481"),sQuery(id+"F6.wireOp",EDGE,"E482"),sQuery(id+"F6.wireOp",EDGE,"E483"),sQuery(id+"F6.wireOp",EDGE,"E484"),sQuery(id+"F6.wireOp",EDGE,"E485"),sQuery(id+"F6.wireOp",EDGE,"E486"),sQuery(id+"F6.wireOp",EDGE,"E487"),sQuery(id+"F6.wireOp",EDGE,"E488"),sQuery(id+"F6.wireOp",EDGE,"E489"),sQuery(id+"F6.wireOp",EDGE,"E490"),sQuery(id+"F6.wireOp",EDGE,"E491"),sQuery(id+"F6.wireOp",EDGE,"E492"),sQuery(id+"F6.wireOp",EDGE,"E493"),sQuery(id+"F6.wireOp",EDGE,"E494"),sQuery(id+"F6.wireOp",EDGE,"E495"),sQuery(id+"F6.wireOp",EDGE,"E496"),sQuery(id+"F6.wireOp",EDGE,"E497"),sQuery(id+"F6.wireOp",EDGE,"E498"),sQuery(id+"F6.wireOp",EDGE,"E499"),sQuery(id+"F6.wireOp",EDGE,"E500"),sQuery(id+"F6.wireOp",EDGE,"E501"),sQuery(id+"F6.wireOp",EDGE,"E502"),sQuery(id+"F6.wireOp",EDGE,"E503"),sQuery(id+"F6.wireOp",EDGE,"E504"),sQuery(id+"F6.wireOp",EDGE,"E505"),sQuery(id+"F6.wireOp",EDGE,"E506"),sQuery(id+"F6.wireOp",EDGE,"E507"),sQuery(id+"F6.wireOp",EDGE,"E508"),sQuery(id+"F6.wireOp",EDGE,"E509"),sQuery(id+"F6.wireOp",EDGE,"E510"),sQuery(id+"F6.wireOp",EDGE,"E511"),sQuery(id+"F6.wireOp",EDGE,"E512"),sQuery(id+"F6.wireOp",EDGE,"E513"),sQuery(id+"F6.wireOp",EDGE,"E514"),sQuery(id+"F6.wireOp",EDGE,"E515"),sQuery(id+"F6.wireOp",EDGE,"E516"),sQuery(id+"F6.wireOp",EDGE,"E517"),sQuery(id+"F6.wireOp",EDGE,"E518"),sQuery(id+"F6.wireOp",EDGE,"E519"),sQuery(id+"F6.wireOp",EDGE,"E520"),sQuery(id+"F6.wireOp",EDGE,"E521"),sQuery(id+"F6.wireOp",EDGE,"E522"),sQuery(id+"F6.wireOp",EDGE,"E523"),sQuery(id+"F6.wireOp",EDGE,"E524"),sQuery(id+"F6.wireOp",EDGE,"E525"),sQuery(id+"F6.wireOp",EDGE,"E526"),sQuery(id+"F6.wireOp",EDGE,"E527"),sQuery(id+"F6.wireOp",EDGE,"E528"),sQuery(id+"F6.wireOp",EDGE,"E529"),sQuery(id+"F6.wireOp",EDGE,"E530"),sQuery(id+"F6.wireOp",EDGE,"E531"),sQuery(id+"F6.wireOp",EDGE,"E532"),sQuery(id+"F6.wireOp",EDGE,"E533"),sQuery(id+"F6.wireOp",EDGE,"E534"),sQuery(id+"F6.wireOp",EDGE,"E535"),sQuery(id+"F6.wireOp",EDGE,"E536"),sQuery(id+"F6.wireOp",EDGE,"E537"),sQuery(id+"F6.wireOp",EDGE,"E538"),sQuery(id+"F6.wireOp",EDGE,"E539"),sQuery(id+"F6.wireOp",EDGE,"E540"),sQuery(id+"F6.wireOp",EDGE,"E541"),sQuery(id+"F6.wireOp",EDGE,"E542"),sQuery(id+"F6.wireOp",EDGE,"E543"),sQuery(id+"F6.wireOp",EDGE,"E544"),sQuery(id+"F6.wireOp",EDGE,"E545"),sQuery(id+"F6.wireOp",EDGE,"E546"),sQuery(id+"F6.wireOp",EDGE,"E547"),sQuery(id+"F6.wireOp",EDGE,"E548"),sQuery(id+"F6.wireOp",EDGE,"E549"),sQuery(id+"F6.wireOp",EDGE,"E550"),sQuery(id+"F6.wireOp",EDGE,"E551"),sQuery(id+"F6.wireOp",EDGE,"E552"),sQuery(id+"F6.wireOp",EDGE,"E553"),sQuery(id+"F6.wireOp",EDGE,"E554"),sQuery(id+"F6.wireOp",EDGE,"E555"),sQuery(id+"F6.wireOp",EDGE,"E556"),sQuery(id+"F6.wireOp",EDGE,"E557"),sQuery(id+"F6.wireOp",EDGE,"E558"),sQuery(id+"F6.wireOp",EDGE,"E559"),sQuery(id+"F6.wireOp",EDGE,"E560"),sQuery(id+"F6.wireOp",EDGE,"E561"),sQuery(id+"F6.wireOp",EDGE,"E562"),sQuery(id+"F6.wireOp",EDGE,"E563"),sQuery(id+"F6.wireOp",EDGE,"E564"),sQuery(id+"F6.wireOp",EDGE,"E565"),sQuery(id+"F6.wireOp",EDGE,"E566"),sQuery(id+"F6.wireOp",EDGE,"E567"),sQuery(id+"F6.wireOp",EDGE,"E568"),sQuery(id+"F6.wireOp",EDGE,"E569"),sQuery(id+"F6.wireOp",EDGE,"E570"),sQuery(id+"F6.wireOp",EDGE,"E571"),sQuery(id+"F6.wireOp",EDGE,"E572"),sQuery(id+"F6.wireOp",EDGE,"E573"),sQuery(id+"F6.wireOp",EDGE,"E574"),sQuery(id+"F6.wireOp",EDGE,"E575"),sQuery(id+"F6.wireOp",EDGE,"E576"),sQuery(id+"F6.wireOp",EDGE,"E577"),sQuery(id+"F6.wireOp",EDGE,"E578"),sQuery(id+"F6.wireOp",EDGE,"E579"),sQuery(id+"F6.wireOp",EDGE,"E580"),sQuery(id+"F6.wireOp",EDGE,"E581"),sQuery(id+"F6.wireOp",EDGE,"E582"),sQuery(id+"F6.wireOp",EDGE,"E583"),sQuery(id+"F6.wireOp",EDGE,"E584"),sQuery(id+"F6.wireOp",EDGE,"E585"),sQuery(id+"F6.wireOp",EDGE,"E586"),sQuery(id+"F6.wireOp",EDGE,"E587"),sQuery(id+"F6.wireOp",EDGE,"E588"),sQuery(id+"F6.wireOp",EDGE,"E589"),sQuery(id+"F6.wireOp",EDGE,"E590"),sQuery(id+"F6.wireOp",EDGE,"E591"),sQuery(id+"F6.wireOp",EDGE,"E592"),sQuery(id+"F6.wireOp",EDGE,"E593"),sQuery(id+"F6.wireOp",EDGE,"E594"),sQuery(id+"F6.wireOp",EDGE,"E595"),sQuery(id+"F6.wireOp",EDGE,"E596"),sQuery(id+"F6.wireOp",EDGE,"E597"),sQuery(id+"F6.wireOp",EDGE,"E598"),sQuery(id+"F6.wireOp",EDGE,"E599"),sQuery(id+"F6.wireOp",EDGE,"E600"),sQuery(id+"F6.wireOp",EDGE,"E601"),sQuery(id+"F6.wireOp",EDGE,"E602"),sQuery(id+"F6.wireOp",EDGE,"E603"),sQuery(id+"F6.wireOp",EDGE,"E604"),sQuery(id+"F6.wireOp",EDGE,"E605"),sQuery(id+"F6.wireOp",EDGE,"E606"),sQuery(id+"F6.wireOp",EDGE,"E607"),sQuery(id+"F6.wireOp",EDGE,"E608"),sQuery(id+"F6.wireOp",EDGE,"E609"),sQuery(id+"F6.wireOp",EDGE,"E610"),sQuery(id+"F6.wireOp",EDGE,"E611"),sQuery(id+"F6.wireOp",EDGE,"E612"),sQuery(id+"F6.wireOp",EDGE,"E613"),sQuery(id+"F6.wireOp",EDGE,"E614"),sQuery(id+"F6.wireOp",EDGE,"E615"),sQuery(id+"F6.wireOp",EDGE,"E616"),sQuery(id+"F6.wireOp",EDGE,"E617"),sQuery(id+"F6.wireOp",EDGE,"E618"),sQuery(id+"F6.wireOp",EDGE,"E619"),sQuery(id+"F6.wireOp",EDGE,"E620"),sQuery(id+"F6.wireOp",EDGE,"E621"),sQuery(id+"F6.wireOp",EDGE,"E622"),sQuery(id+"F6.wireOp",EDGE,"E623"),sQuery(id+"F6.wireOp",EDGE,"E624"),sQuery(id+"F6.wireOp",EDGE,"E625"),sQuery(id+"F6.wireOp",EDGE,"E626"),sQuery(id+"F6.wireOp",EDGE,"E627"),sQuery(id+"F6.wireOp",EDGE,"E628"),sQuery(id+"F6.wireOp",EDGE,"E629"),sQuery(id+"F6.wireOp",EDGE,"E630"),sQuery(id+"F6.wireOp",EDGE,"E631"),sQuery(id+"F6.wireOp",EDGE,"E632"),sQuery(id+"F6.wireOp",EDGE,"E633"),sQuery(id+"F6.wireOp",EDGE,"E634"),sQuery(id+"F6.wireOp",EDGE,"E635"),sQuery(id+"F6.wireOp",EDGE,"E636"),sQuery(id+"F6.wireOp",EDGE,"E637"),sQuery(id+"F6.wireOp",EDGE,"E638"),sQuery(id+"F6.wireOp",EDGE,"E639"),sQuery(id+"F6.wireOp",EDGE,"E640"),sQuery(id+"F6.wireOp",EDGE,"E641"),sQuery(id+"F6.wireOp",EDGE,"E642"),sQuery(id+"F6.wireOp",EDGE,"E643"),sQuery(id+"F6.wireOp",EDGE,"E644"),sQuery(id+"F6.wireOp",EDGE,"E645"),sQuery(id+"F6.wireOp",EDGE,"E646"),sQuery(id+"F6.wireOp",EDGE,"E647"),sQuery(id+"F6.wireOp",EDGE,"E648"),sQuery(id+"F6.wireOp",EDGE,"E649"),sQuery(id+"F6.wireOp",EDGE,"E650"),sQuery(id+"F6.wireOp",EDGE,"E651"),sQuery(id+"F6.wireOp",EDGE,"E652"),sQuery(id+"F6.wireOp",EDGE,"E653"),sQuery(id+"F6.wireOp",EDGE,"E654"),sQuery(id+"F6.wireOp",EDGE,"E655"),sQuery(id+"F6.wireOp",EDGE,"E656"),sQuery(id+"F6.wireOp",EDGE,"E657"),sQuery(id+"F6.wireOp",EDGE,"E658"),sQuery(id+"F6.wireOp",EDGE,"E659"),sQuery(id+"F6.wireOp",EDGE,"E660"),sQuery(id+"F6.wireOp",EDGE,"E661"),sQuery(id+"F6.wireOp",EDGE,"E662"),sQuery(id+"F6.wireOp",EDGE,"E663"),sQuery(id+"F6.wireOp",EDGE,"E664"),sQuery(id+"F6.wireOp",EDGE,"E665"),sQuery(id+"F6.wireOp",EDGE,"E666"),sQuery(id+"F6.wireOp",EDGE,"E667"),sQuery(id+"F6.wireOp",EDGE,"E668"),sQuery(id+"F6.wireOp",EDGE,"E669"),sQuery(id+"F6.wireOp",EDGE,"E670"),sQuery(id+"F6.wireOp",EDGE,"E671"),sQuery(id+"F6.wireOp",EDGE,"E672"),sQuery(id+"F6.wireOp",EDGE,"E673"),sQuery(id+"F6.wireOp",EDGE,"E674"),sQuery(id+"F6.wireOp",EDGE,"E675"),sQuery(id+"F6.wireOp",EDGE,"E676"),sQuery(id+"F6.wireOp",EDGE,"E677"),sQuery(id+"F6.wireOp",EDGE,"E678"),sQuery(id+"F6.wireOp",EDGE,"E679"),sQuery(id+"F6.wireOp",EDGE,"E680"),sQuery(id+"F6.wireOp",EDGE,"E681"),sQuery(id+"F6.wireOp",EDGE,"E682"),sQuery(id+"F6.wireOp",EDGE,"E683"),sQuery(id+"F6.wireOp",EDGE,"E684"),sQuery(id+"F6.wireOp",EDGE,"E685"),sQuery(id+"F6.wireOp",EDGE,"E686"),sQuery(id+"F6.wireOp",EDGE,"E687"),sQuery(id+"F6.wireOp",EDGE,"E688"),sQuery(id+"F6.wireOp",EDGE,"E689"),sQuery(id+"F6.wireOp",EDGE,"E690"),sQuery(id+"F6.wireOp",EDGE,"E691"),sQuery(id+"F6.wireOp",EDGE,"E692"),sQuery(id+"F6.wireOp",EDGE,"E693"),sQuery(id+"F6.wireOp",EDGE,"E694"),sQuery(id+"F6.wireOp",EDGE,"E695"),sQuery(id+"F6.wireOp",EDGE,"E696"),sQuery(id+"F6.wireOp",EDGE,"E697"),sQuery(id+"F6.wireOp",EDGE,"E698"),sQuery(id+"F6.wireOp",EDGE,"E699"),sQuery(id+"F6.wireOp",EDGE,"E700"),sQuery(id+"F6.wireOp",EDGE,"E701"),sQuery(id+"F6.wireOp",EDGE,"E702"),sQuery(id+"F6.wireOp",EDGE,"E703"),sQuery(id+"F6.wireOp",EDGE,"E704"),sQuery(id+"F6.wireOp",EDGE,"E705"),sQuery(id+"F6.wireOp",EDGE,"E706"),sQuery(id+"F6.wireOp",EDGE,"E707"),sQuery(id+"F6.wireOp",EDGE,"E708"),sQuery(id+"F6.wireOp",EDGE,"E709"),sQuery(id+"F6.wireOp",EDGE,"E710"),sQuery(id+"F6.wireOp",EDGE,"E711"),sQuery(id+"F6.wireOp",EDGE,"E712"),sQuery(id+"F6.wireOp",EDGE,"E713"),sQuery(id+"F6.wireOp",EDGE,"E714"),sQuery(id+"F6.wireOp",EDGE,"E715"),sQuery(id+"F6.wireOp",EDGE,"E716"),sQuery(id+"F6.wireOp",EDGE,"E717"),sQuery(id+"F6.wireOp",EDGE,"E718"),sQuery(id+"F6.wireOp",EDGE,"E719"),sQuery(id+"F6.wireOp",EDGE,"E720"),sQuery(id+"F6.wireOp",EDGE,"E721"),sQuery(id+"F6.wireOp",EDGE,"E722"),sQuery(id+"F6.wireOp",EDGE,"E723"),sQuery(id+"F6.wireOp",EDGE,"E724"),sQuery(id+"F6.wireOp",EDGE,"E725"),sQuery(id+"F6.wireOp",EDGE,"E726"),sQuery(id+"F6.wireOp",EDGE,"E727"),sQuery(id+"F6.wireOp",EDGE,"E728"),sQuery(id+"F6.wireOp",EDGE,"E729"),sQuery(id+"F6.wireOp",EDGE,"E730"),sQuery(id+"F6.wireOp",EDGE,"E731"),sQuery(id+"F6.wireOp",EDGE,"E732"),sQuery(id+"F6.wireOp",EDGE,"E733"),sQuery(id+"F6.wireOp",EDGE,"E734"),sQuery(id+"F6.wireOp",EDGE,"E735"),sQuery(id+"F6.wireOp",EDGE,"E736"),sQuery(id+"F6.wireOp",EDGE,"E737"),sQuery(id+"F6.wireOp",EDGE,"E738"),sQuery(id+"F6.wireOp",EDGE,"E739"),sQuery(id+"F6.wireOp",EDGE,"E740"),sQuery(id+"F6.wireOp",EDGE,"E741"),sQuery(id+"F6.wireOp",EDGE,"E742"),sQuery(id+"F6.wireOp",EDGE,"E743"),sQuery(id+"F6.wireOp",EDGE,"E744"),sQuery(id+"F6.wireOp",EDGE,"E745"),sQuery(id+"F6.wireOp",EDGE,"E746"),sQuery(id+"F6.wireOp",EDGE,"E747"),sQuery(id+"F6.wireOp",EDGE,"E748"),sQuery(id+"F6.wireOp",EDGE,"E749"),sQuery(id+"F6.wireOp",EDGE,"E750"),sQuery(id+"F6.wireOp",EDGE,"E751"),sQuery(id+"F6.wireOp",EDGE,"E752"),sQuery(id+"F6.wireOp",EDGE,"E753"),sQuery(id+"F6.wireOp",EDGE,"E754"),sQuery(id+"F6.wireOp",EDGE,"E755"),sQuery(id+"F6.wireOp",EDGE,"E756"),sQuery(id+"F6.wireOp",EDGE,"E757"),sQuery(id+"F6.wireOp",EDGE,"E758"),sQuery(id+"F6.wireOp",EDGE,"E759"),sQuery(id+"F6.wireOp",EDGE,"E760"),sQuery(id+"F6.wireOp",EDGE,"E761"),sQuery(id+"F6.wireOp",EDGE,"E762"),sQuery(id+"F6.wireOp",EDGE,"E763"),sQuery(id+"F6.wireOp",EDGE,"E764"),sQuery(id+"F6.wireOp",EDGE,"E765"),sQuery(id+"F6.wireOp",EDGE,"E766"),sQuery(id+"F6.wireOp",EDGE,"E767"),sQuery(id+"F6.wireOp",EDGE,"E768"),sQuery(id+"F6.wireOp",EDGE,"E769"),sQuery(id+"F6.wireOp",EDGE,"E770"),sQuery(id+"F6.wireOp",EDGE,"E771"),sQuery(id+"F6.wireOp",EDGE,"E772"),sQuery(id+"F6.wireOp",EDGE,"E773"),sQuery(id+"F6.wireOp",EDGE,"E774"),sQuery(id+"F6.wireOp",EDGE,"E775"),sQuery(id+"F6.wireOp",EDGE,"E776"),sQuery(id+"F6.wireOp",EDGE,"E777"),sQuery(id+"F6.wireOp",EDGE,"E778"),sQuery(id+"F6.wireOp",EDGE,"E779"),sQuery(id+"F6.wireOp",EDGE,"E780"),sQuery(id+"F6.wireOp",EDGE,"E781"),sQuery(id+"F6.wireOp",EDGE,"E782"),sQuery(id+"F6.wireOp",EDGE,"E783"),sQuery(id+"F6.wireOp",EDGE,"E784"),sQuery(id+"F6.wireOp",EDGE,"E785"),sQuery(id+"F6.wireOp",EDGE,"E786"),sQuery(id+"F6.wireOp",EDGE,"E787"),sQuery(id+"F6.wireOp",EDGE,"E788"),sQuery(id+"F6.wireOp",EDGE,"E789"),sQuery(id+"F6.wireOp",EDGE,"E790"),sQuery(id+"F6.wireOp",EDGE,"E791"),sQuery(id+"F6.wireOp",EDGE,"E792"),sQuery(id+"F6.wireOp",EDGE,"E793"),sQuery(id+"F6.wireOp",EDGE,"E794"),sQuery(id+"F6.wireOp",EDGE,"E795"),sQuery(id+"F6.wireOp",EDGE,"E796"),sQuery(id+"F6.wireOp",EDGE,"E797"),sQuery(id+"F6.wireOp",EDGE,"E798"),sQuery(id+"F6.wireOp",EDGE,"E799"),sQuery(id+"F6.wireOp",EDGE,"E800"),sQuery(id+"F6.wireOp",EDGE,"E801"),sQuery(id+"F6.wireOp",EDGE,"E802"),sQuery(id+"F6.wireOp",EDGE,"E803"),sQuery(id+"F6.wireOp",EDGE,"E804"),sQuery(id+"F6.wireOp",EDGE,"E805"),sQuery(id+"F6.wireOp",EDGE,"E806"),sQuery(id+"F6.wireOp",EDGE,"E807"),sQuery(id+"F6.wireOp",EDGE,"E808"),sQuery(id+"F6.wireOp",EDGE,"E809"),sQuery(id+"F6.wireOp",EDGE,"E810"),sQuery(id+"F6.wireOp",EDGE,"E811"),sQuery(id+"F6.wireOp",EDGE,"E812"),sQuery(id+"F6.wireOp",EDGE,"E813"),sQuery(id+"F6.wireOp",EDGE,"E814"),sQuery(id+"F6.wireOp",EDGE,"E815"),sQuery(id+"F6.wireOp",EDGE,"E816"),sQuery(id+"F6.wireOp",EDGE,"E817"),sQuery(id+"F6.wireOp",EDGE,"E818"),sQuery(id+"F6.wireOp",EDGE,"E819"),sQuery(id+"F6.wireOp",EDGE,"E820"),sQuery(id+"F6.wireOp",EDGE,"E821"),sQuery(id+"F6.wireOp",EDGE,"E822"),sQuery(id+"F6.wireOp",EDGE,"E823"),sQuery(id+"F6.wireOp",EDGE,"E824"),sQuery(id+"F6.wireOp",EDGE,"E825"),sQuery(id+"F6.wireOp",EDGE,"E826"),sQuery(id+"F6.wireOp",EDGE,"E827"),sQuery(id+"F6.wireOp",EDGE,"E828"),sQuery(id+"F6.wireOp",EDGE,"E829"),sQuery(id+"F6.wireOp",EDGE,"E830"),sQuery(id+"F6.wireOp",EDGE,"E831"),sQuery(id+"F6.wireOp",EDGE,"E832"),sQuery(id+"F6.wireOp",EDGE,"E833"),sQuery(id+"F6.wireOp",EDGE,"E834"),sQuery(id+"F6.wireOp",EDGE,"E835"),sQuery(id+"F6.wireOp",EDGE,"E836"),sQuery(id+"F6.wireOp",EDGE,"E837"),sQuery(id+"F6.wireOp",EDGE,"E838"),sQuery(id+"F6.wireOp",EDGE,"E839"),sQuery(id+"F6.wireOp",EDGE,"E840"),sQuery(id+"F6.wireOp",EDGE,"E841"),sQuery(id+"F6.wireOp",EDGE,"E842"),sQuery(id+"F6.wireOp",EDGE,"E843"),sQuery(id+"F6.wireOp",EDGE,"E844"),sQuery(id+"F6.wireOp",EDGE,"E845"),sQuery(id+"F6.wireOp",EDGE,"E846"),sQuery(id+"F6.wireOp",EDGE,"E847"),sQuery(id+"F6.wireOp",EDGE,"E848"),sQuery(id+"F6.wireOp",EDGE,"E849"),sQuery(id+"F6.wireOp",EDGE,"E850"),sQuery(id+"F6.wireOp",EDGE,"E851"),sQuery(id+"F6.wireOp",EDGE,"E852"),sQuery(id+"F6.wireOp",EDGE,"E853"),sQuery(id+"F6.wireOp",EDGE,"E854"),sQuery(id+"F6.wireOp",EDGE,"E855"),sQuery(id+"F6.wireOp",EDGE,"E856"),sQuery(id+"F6.wireOp",EDGE,"E857"),sQuery(id+"F6.wireOp",EDGE,"E858"),sQuery(id+"F6.wireOp",EDGE,"E859"),sQuery(id+"F6.wireOp",EDGE,"E860"),sQuery(id+"F6.wireOp",EDGE,"E861"),sQuery(id+"F6.wireOp",EDGE,"E862"),sQuery(id+"F6.wireOp",EDGE,"E863"),sQuery(id+"F6.wireOp",EDGE,"E864"),sQuery(id+"F6.wireOp",EDGE,"E865"),sQuery(id+"F6.wireOp",EDGE,"E866"),sQuery(id+"F6.wireOp",EDGE,"E867"),sQuery(id+"F6.wireOp",EDGE,"E868"),sQuery(id+"F6.wireOp",EDGE,"E869"),sQuery(id+"F6.wireOp",EDGE,"E870"),sQuery(id+"F6.wireOp",EDGE,"E871"),sQuery(id+"F6.wireOp",EDGE,"E872"),sQuery(id+"F6.wireOp",EDGE,"E873"),sQuery(id+"F6.wireOp",EDGE,"E874"),sQuery(id+"F6.wireOp",EDGE,"E875"),sQuery(id+"F6.wireOp",EDGE,"E876"),sQuery(id+"F6.wireOp",EDGE,"E877"),sQuery(id+"F6.wireOp",EDGE,"E878"),sQuery(id+"F6.wireOp",EDGE,"E879"),sQuery(id+"F6.wireOp",EDGE,"E880"),sQuery(id+"F6.wireOp",EDGE,"E881"),sQuery(id+"F6.wireOp",EDGE,"E882"),sQuery(id+"F6.wireOp",EDGE,"E883"),sQuery(id+"F6.wireOp",EDGE,"E884"),sQuery(id+"F6.wireOp",EDGE,"E885"),sQuery(id+"F6.wireOp",EDGE,"E886"),sQuery(id+"F6.wireOp",EDGE,"E887"),sQuery(id+"F6.wireOp",EDGE,"E888"),sQuery(id+"F6.wireOp",EDGE,"E889"),sQuery(id+"F6.wireOp",EDGE,"E890"),sQuery(id+"F6.wireOp",EDGE,"E891"),sQuery(id+"F6.wireOp",EDGE,"E892"),sQuery(id+"F6.wireOp",EDGE,"E893"),sQuery(id+"F6.wireOp",EDGE,"E894"),sQuery(id+"F6.wireOp",EDGE,"E895"),sQuery(id+"F6.wireOp",EDGE,"E896"),sQuery(id+"F6.wireOp",EDGE,"E897"),sQuery(id+"F6.wireOp",EDGE,"E898"),sQuery(id+"F6.wireOp",EDGE,"E899"),sQuery(id+"F6.wireOp",EDGE,"E900"),sQuery(id+"F6.wireOp",EDGE,"E901"),sQuery(id+"F6.wireOp",EDGE,"E902"),sQuery(id+"F6.wireOp",EDGE,"E903"),sQuery(id+"F6.wireOp",EDGE,"E904"),sQuery(id+"F6.wireOp",EDGE,"E905"),sQuery(id+"F6.wireOp",EDGE,"E906"),sQuery(id+"F6.wireOp",EDGE,"E907"),sQuery(id+"F6.wireOp",EDGE,"E908"),sQuery(id+"F6.wireOp",EDGE,"E909"),sQuery(id+"F6.wireOp",EDGE,"E910"),sQuery(id+"F6.wireOp",EDGE,"E911"),sQuery(id+"F6.wireOp",EDGE,"E911"),sQuery(id+"F6.wireOp",EDGE,"E912"),sQuery(id+"F6.wireOp",EDGE,"E913"),sQuery(id+"F6.wireOp",EDGE,"E914"),sQuery(id+"F6.wireOp",EDGE,"E915"),sQuery(id+"F6.wireOp",EDGE,"E916"),sQuery(id+"F6.wireOp",EDGE,"E917"),sQuery(id+"F6.wireOp",EDGE,"E918"),sQuery(id+"F6.wireOp",EDGE,"E919"),sQuery(id+"F6.wireOp",EDGE,"E920"),sQuery(id+"F6.wireOp",EDGE,"E921"),sQuery(id+"F6.wireOp",EDGE,"E922"),sQuery(id+"F6.wireOp",EDGE,"E923"),sQuery(id+"F6.wireOp",EDGE,"E924"),sQuery(id+"F6.wireOp",EDGE,"E925"),sQuery(id+"F6.wireOp",EDGE,"E926"),sQuery(id+"F6.wireOp",EDGE,"E927"),sQuery(id+"F6.wireOp",EDGE,"E928"),sQuery(id+"F6.wireOp",EDGE,"E929"),sQuery(id+"F6.wireOp",EDGE,"E930"),sQuery(id+"F6.wireOp",EDGE,"E931"),sQuery(id+"F6.wireOp",EDGE,"E932"),sQuery(id+"F6.wireOp",EDGE,"E933"),sQuery(id+"F6.wireOp",EDGE,"E934"),sQuery(id+"F6.wireOp",EDGE,"E935"),sQuery(id+"F6.wireOp",EDGE,"E936"),sQuery(id+"F6.wireOp",EDGE,"E937"),sQuery(id+"F6.wireOp",EDGE,"E938"),sQuery(id+"F6.wireOp",EDGE,"E939"),sQuery(id+"F6.wireOp",EDGE,"E940"),sQuery(id+"F6.wireOp",EDGE,"E941"),sQuery(id+"F6.wireOp",EDGE,"E942"),sQuery(id+"F6.wireOp",EDGE,"E943"),sQuery(id+"F6.wireOp",EDGE,"E944"),sQuery(id+"F6.wireOp",EDGE,"E945"),sQuery(id+"F6.wireOp",EDGE,"E946"),sQuery(id+"F6.wireOp",EDGE,"E947"),sQuery(id+"F6.wireOp",EDGE,"E948"),sQuery(id+"F6.wireOp",EDGE,"E949"),sQuery(id+"F6.wireOp",EDGE,"E950"),sQuery(id+"F6.wireOp",EDGE,"E951"),sQuery(id+"F6.wireOp",EDGE,"E952"),sQuery(id+"F6.wireOp",EDGE,"E953"),sQuery(id+"F6.wireOp",EDGE,"E954"),sQuery(id+"F6.wireOp",EDGE,"E955"),sQuery(id+"F6.wireOp",EDGE,"E956"),sQuery(id+"F6.wireOp",EDGE,"E957"),sQuery(id+"F6.wireOp",EDGE,"E958"),sQuery(id+"F6.wireOp",EDGE,"E959"),sQuery(id+"F6.wireOp",EDGE,"E960"),sQuery(id+"F6.wireOp",EDGE,"E961"),sQuery(id+"F6.wireOp",EDGE,"E962"),sQuery(id+"F6.wireOp",EDGE,"E963"),sQuery(id+"F6.wireOp",EDGE,"E964"),sQuery(id+"F6.wireOp",EDGE,"E965"),sQuery(id+"F6.wireOp",EDGE,"E966"),sQuery(id+"F6.wireOp",EDGE,"E967"),sQuery(id+"F6.wireOp",EDGE,"E968"),sQuery(id+"F6.wireOp",EDGE,"E969"),sQuery(id+"F6.wireOp",EDGE,"E970"),sQuery(id+"F6.wireOp",EDGE,"E971"),sQuery(id+"F6.wireOp",EDGE,"E972"),sQuery(id+"F6.wireOp",EDGE,"E973"),sQuery(id+"F6.wireOp",EDGE,"E974"),sQuery(id+"F6.wireOp",EDGE,"E975"),sQuery(id+"F6.wireOp",EDGE,"E976"),sQuery(id+"F6.wireOp",EDGE,"E977"),sQuery(id+"F6.wireOp",EDGE,"E978"),sQuery(id+"F6.wireOp",EDGE,"E979"),sQuery(id+"F6.wireOp",EDGE,"E980"),sQuery(id+"F6.wireOp",EDGE,"E981"),sQuery(id+"F6.wireOp",EDGE,"E982"),sQuery(id+"F6.wireOp",EDGE,"E983"),sQuery(id+"F6.wireOp",EDGE,"E984"),sQuery(id+"F6.wireOp",EDGE,"E985"),sQuery(id+"F6.wireOp",EDGE,"E986"),sQuery(id+"F6.wireOp",EDGE,"E987"),sQuery(id+"F6.wireOp",EDGE,"E988"),sQuery(id+"F6.wireOp",EDGE,"E989"),sQuery(id+"F6.wireOp",EDGE,"E990"),sQuery(id+"F6.wireOp",EDGE,"E991"),sQuery(id+"F6.wireOp",EDGE,"E992"),sQuery(id+"F6.wireOp",EDGE,"E993"),sQuery(id+"F6.wireOp",EDGE,"E994"),sQuery(id+"F6.wireOp",EDGE,"E995"),sQuery(id+"F6.wireOp",EDGE,"E996"),sQuery(id+"F6.wireOp",EDGE,"E997"),sQuery(id+"F6.wireOp",EDGE,"E998"),sQuery(id+"F6.wireOp",EDGE,"E999"),sQuery(id+"F6.wireOp",EDGE,"E1000"),sQuery(id+"F6.wireOp",EDGE,"E1001"),sQuery(id+"F6.wireOp",EDGE,"E1002"),sQuery(id+"F6.wireOp",EDGE,"E1003"),sQuery(id+"F6.wireOp",EDGE,"E1004"),sQuery(id+"F6.wireOp",EDGE,"E1005"),sQuery(id+"F6.wireOp",EDGE,"E1006"),sQuery(id+"F6.wireOp",EDGE,"E1007"),sQuery(id+"F6.wireOp",EDGE,"E1008"),sQuery(id+"F6.wireOp",EDGE,"E1009"),sQuery(id+"F6.wireOp",EDGE,"E1010"),sQuery(id+"F6.wireOp",EDGE,"E1011"),sQuery(id+"F6.wireOp",EDGE,"E1012"),sQuery(id+"F6.wireOp",EDGE,"E1013"),sQuery(id+"F6.wireOp",EDGE,"E1014"),sQuery(id+"F6.wireOp",EDGE,"E1015"),sQuery(id+"F6.wireOp",EDGE,"E1016"),sQuery(id+"F6.wireOp",EDGE,"E1017"),sQuery(id+"F6.wireOp",EDGE,"E1018"),sQuery(id+"F6.wireOp",EDGE,"E1019"),sQuery(id+"F6.wireOp",EDGE,"E1020"),sQuery(id+"F6.wireOp",EDGE,"E1021"),sQuery(id+"F6.wireOp",EDGE,"E1022"),sQuery(id+"F6.wireOp",EDGE,"E1023"),sQuery(id+"F6.wireOp",EDGE,"E1024"),sQuery(id+"F6.wireOp",EDGE,"E1025"),sQuery(id+"F6.wireOp",EDGE,"E1026"),sQuery(id+"F6.wireOp",EDGE,"E1027"),sQuery(id+"F6.wireOp",EDGE,"E1028"),sQuery(id+"F6.wireOp",EDGE,"E1029"),sQuery(id+"F6.wireOp",EDGE,"E1030"),sQuery(id+"F6.wireOp",EDGE,"E1031"),sQuery(id+"F6.wireOp",EDGE,"E1032"),sQuery(id+"F6.wireOp",EDGE,"E1033"),sQuery(id+"F6.wireOp",EDGE,"E1034"),sQuery(id+"F6.wireOp",EDGE,"E1035"),sQuery(id+"F6.wireOp",EDGE,"E1036"),sQuery(id+"F6.wireOp",EDGE,"E1037"),sQuery(id+"F6.wireOp",EDGE,"E1038"),sQuery(id+"F6.wireOp",EDGE,"E1039"),sQuery(id+"F6.wireOp",EDGE,"E1040"),sQuery(id+"F6.wireOp",EDGE,"E1041"),sQuery(id+"F6.wireOp",EDGE,"E1042"),sQuery(id+"F6.wireOp",EDGE,"E1043"),sQuery(id+"F6.wireOp",EDGE,"E1044"),sQuery(id+"F6.wireOp",EDGE,"E1045"),sQuery(id+"F6.wireOp",EDGE,"E1046"),sQuery(id+"F6.wireOp",EDGE,"E1047"),sQuery(id+"F6.wireOp",EDGE,"E1048"),sQuery(id+"F6.wireOp",EDGE,"E1049"),sQuery(id+"F6.wireOp",EDGE,"E1050"),sQuery(id+"F6.wireOp",EDGE,"E1051"),sQuery(id+"F6.wireOp",EDGE,"E1052"),sQuery(id+"F6.wireOp",EDGE,"E1053"),sQuery(id+"F6.wireOp",EDGE,"E1054"),sQuery(id+"F6.wireOp",EDGE,"E1055"),sQuery(id+"F6.wireOp",EDGE,"E1056"),sQuery(id+"F6.wireOp",EDGE,"E1057"),sQuery(id+"F6.wireOp",EDGE,"E1058"),sQuery(id+"F6.wireOp",EDGE,"E1059"),sQuery(id+"F6.wireOp",EDGE,"E1060"),sQuery(id+"F6.wireOp",EDGE,"E1061"),sQuery(id+"F6.wireOp",EDGE,"E1062"),sQuery(id+"F6.wireOp",EDGE,"E1063"),sQuery(id+"F6.wireOp",EDGE,"E1064"),sQuery(id+"F6.wireOp",EDGE,"E1065"),sQuery(id+"F6.wireOp",EDGE,"E1066"),sQuery(id+"F6.wireOp",EDGE,"E1067"),sQuery(id+"F6.wireOp",EDGE,"E1068"),sQuery(id+"F6.wireOp",EDGE,"E1069"),sQuery(id+"F6.wireOp",EDGE,"E1070"),sQuery(id+"F6.wireOp",EDGE,"E1071"),sQuery(id+"F6.wireOp",EDGE,"E1072"),sQuery(id+"F6.wireOp",EDGE,"E1073"),sQuery(id+"F6.wireOp",EDGE,"E1074"),sQuery(id+"F6.wireOp",EDGE,"E1075"),sQuery(id+"F6.wireOp",EDGE,"E1076"),sQuery(id+"F6.wireOp",EDGE,"E1077"),sQuery(id+"F6.wireOp",EDGE,"E1078"),sQuery(id+"F6.wireOp",EDGE,"E1079"),sQuery(id+"F6.wireOp",EDGE,"E1080"),sQuery(id+"F6.wireOp",EDGE,"E1081"),sQuery(id+"F6.wireOp",EDGE,"E1082"),sQuery(id+"F6.wireOp",EDGE,"E1083"),sQuery(id+"F6.wireOp",EDGE,"E1084"),sQuery(id+"F6.wireOp",EDGE,"E1085"),sQuery(id+"F6.wireOp",EDGE,"E1086"),sQuery(id+"F6.wireOp",EDGE,"E1087"),sQuery(id+"F6.wireOp",EDGE,"E1088"),sQuery(id+"F6.wireOp",EDGE,"E1089"),sQuery(id+"F6.wireOp",EDGE,"E1090"),sQuery(id+"F6.wireOp",EDGE,"E1091"),sQuery(id+"F6.wireOp",EDGE,"E1092"),sQuery(id+"F6.wireOp",EDGE,"E1093"),sQuery(id+"F6.wireOp",EDGE,"E1094"),sQuery(id+"F6.wireOp",EDGE,"E1095"),sQuery(id+"F6.wireOp",EDGE,"E1096"),sQuery(id+"F6.wireOp",EDGE,"E1097"),sQuery(id+"F6.wireOp",EDGE,"E1098"),sQuery(id+"F6.wireOp",EDGE,"E1099"),sQuery(id+"F6.wireOp",EDGE,"E1100"),sQuery(id+"F6.wireOp",EDGE,"E1101"),sQuery(id+"F6.wireOp",EDGE,"E1102"),sQuery(id+"F6.wireOp",EDGE,"E1103"),sQuery(id+"F6.wireOp",EDGE,"E1104"),sQuery(id+"F6.wireOp",EDGE,"E1105"),sQuery(id+"F6.wireOp",EDGE,"E1106"),sQuery(id+"F6.wireOp",EDGE,"E1107"),sQuery(id+"F6.wireOp",EDGE,"E1108"),sQuery(id+"F6.wireOp",EDGE,"E1109"),sQuery(id+"F6.wireOp",EDGE,"E1110"),sQuery(id+"F6.wireOp",EDGE,"E1111"),sQuery(id+"F6.wireOp",EDGE,"E1112"),sQuery(id+"F6.wireOp",EDGE,"E1113"),sQuery(id+"F6.wireOp",EDGE,"E1114"),sQuery(id+"F6.wireOp",EDGE,"E1115"),sQuery(id+"F6.wireOp",EDGE,"E1116"),sQuery(id+"F6.wireOp",EDGE,"E1117"),sQuery(id+"F6.wireOp",EDGE,"E1118"),sQuery(id+"F6.wireOp",EDGE,"E1119"),sQuery(id+"F6.wireOp",EDGE,"E1120"),sQuery(id+"F6.wireOp",EDGE,"E1121"),sQuery(id+"F6.wireOp",EDGE,"E1122"),sQuery(id+"F6.wireOp",EDGE,"E1123"),sQuery(id+"F6.wireOp",EDGE,"E1124"),sQuery(id+"F6.wireOp",EDGE,"E1125"),sQuery(id+"F6.wireOp",EDGE,"E1126"),sQuery(id+"F6.wireOp",EDGE,"E1127"),sQuery(id+"F6.wireOp",EDGE,"E1128"),sQuery(id+"F6.wireOp",EDGE,"E1129"),sQuery(id+"F6.wireOp",EDGE,"E1130"),sQuery(id+"F6.wireOp",EDGE,"E1131"),sQuery(id+"F6.wireOp",EDGE,"E1132"),sQuery(id+"F6.wireOp",EDGE,"E1133"),sQuery(id+"F6.wireOp",EDGE,"E1134"),sQuery(id+"F6.wireOp",EDGE,"E1135"),sQuery(id+"F6.wireOp",EDGE,"E1136"),sQuery(id+"F6.wireOp",EDGE,"E1137"),sQuery(id+"F6.wireOp",EDGE,"E1138"),sQuery(id+"F6.wireOp",EDGE,"E1139"),sQuery(id+"F6.wireOp",EDGE,"E1140"),sQuery(id+"F6.wireOp",EDGE,"E1141"),sQuery(id+"F6.wireOp",EDGE,"E1142"),sQuery(id+"F6.wireOp",EDGE,"E1143"),sQuery(id+"F6.wireOp",EDGE,"E1144"),sQuery(id+"F6.wireOp",EDGE,"E1145"),sQuery(id+"F6.wireOp",EDGE,"E1146"),sQuery(id+"F6.wireOp",EDGE,"E1147"),sQuery(id+"F6.wireOp",EDGE,"E1148"),sQuery(id+"F6.wireOp",EDGE,"E1149"),sQuery(id+"F6.wireOp",EDGE,"E1150"),sQuery(id+"F6.wireOp",EDGE,"E1151"),sQuery(id+"F6.wireOp",EDGE,"E1152"),sQuery(id+"F6.wireOp",EDGE,"E1153"),sQuery(id+"F6.wireOp",EDGE,"E1154"),sQuery(id+"F6.wireOp",EDGE,"E1155"),sQuery(id+"F6.wireOp",EDGE,"E1156"),sQuery(id+"F6.wireOp",EDGE,"E1157"),sQuery(id+"F6.wireOp",EDGE,"E1158"),sQuery(id+"F6.wireOp",EDGE,"E1159"),sQuery(id+"F6.wireOp",EDGE,"E1160"),sQuery(id+"F6.wireOp",EDGE,"E1161"),sQuery(id+"F6.wireOp",EDGE,"E1162"),sQuery(id+"F6.wireOp",EDGE,"E1163"),sQuery(id+"F6.wireOp",EDGE,"E1164"),sQuery(id+"F6.wireOp",EDGE,"E1165"),sQuery(id+"F6.wireOp",EDGE,"E1166"),sQuery(id+"F6.wireOp",EDGE,"E1167"),sQuery(id+"F6.wireOp",EDGE,"E1168"),sQuery(id+"F6.wireOp",EDGE,"E1169"),sQuery(id+"F6.wireOp",EDGE,"E1170"),sQuery(id+"F6.wireOp",EDGE,"E1171"),sQuery(id+"F6.wireOp",EDGE,"E1172"),sQuery(id+"F6.wireOp",EDGE,"E1173"),sQuery(id+"F6.wireOp",EDGE,"E1174"),sQuery(id+"F6.wireOp",EDGE,"E1175"),sQuery(id+"F6.wireOp",EDGE,"E1176"),sQuery(id+"F6.wireOp",EDGE,"E1177"),sQuery(id+"F6.wireOp",EDGE,"E1178"),sQuery(id+"F6.wireOp",EDGE,"E1179"),sQuery(id+"F6.wireOp",EDGE,"E1180"),sQuery(id+"F6.wireOp",EDGE,"E1181"),sQuery(id+"F6.wireOp",EDGE,"E1182"),sQuery(id+"F6.wireOp",EDGE,"E1183"),sQuery(id+"F6.wireOp",EDGE,"E1184"),sQuery(id+"F6.wireOp",EDGE,"E1185"),sQuery(id+"F6.wireOp",EDGE,"E1186"),sQuery(id+"F6.wireOp",EDGE,"E1187"),sQuery(id+"F6.wireOp",EDGE,"E1188"),sQuery(id+"F6.wireOp",EDGE,"E1189"),sQuery(id+"F6.wireOp",EDGE,"E1190"),sQuery(id+"F6.wireOp",EDGE,"E1191"),sQuery(id+"F6.wireOp",EDGE,"E1192"),sQuery(id+"F6.wireOp",EDGE,"E1193"),sQuery(id+"F6.wireOp",EDGE,"E1194"),sQuery(id+"F6.wireOp",EDGE,"E1195"),sQuery(id+"F6.wireOp",EDGE,"E1196"),sQuery(id+"F6.wireOp",EDGE,"E1197"),sQuery(id+"F6.wireOp",EDGE,"E1198"),sQuery(id+"F6.wireOp",EDGE,"E1199"),sQuery(id+"F6.wireOp",EDGE,"E1200"),sQuery(id+"F6.wireOp",EDGE,"E1201"),sQuery(id+"F6.wireOp",EDGE,"E1202"),sQuery(id+"F6.wireOp",EDGE,"E1203"),sQuery(id+"F6.wireOp",EDGE,"E1204"),sQuery(id+"F6.wireOp",EDGE,"E1205"),sQuery(id+"F6.wireOp",EDGE,"E1206"),sQuery(id+"F6.wireOp",EDGE,"E1207"),sQuery(id+"F6.wireOp",EDGE,"E1208"),sQuery(id+"F6.wireOp",EDGE,"E1209"),sQuery(id+"F6.wireOp",EDGE,"E1210"),sQuery(id+"F6.wireOp",EDGE,"E1211"),sQuery(id+"F6.wireOp",EDGE,"E1212"),sQuery(id+"F6.wireOp",EDGE,"E1213"),sQuery(id+"F6.wireOp",EDGE,"E1214"),sQuery(id+"F6.wireOp",EDGE,"E1215"),sQuery(id+"F6.wireOp",EDGE,"E1216"),sQuery(id+"F6.wireOp",EDGE,"E1217"),sQuery(id+"F6.wireOp",EDGE,"E1218"),sQuery(id+"F6.wireOp",EDGE,"E1219"),sQuery(id+"F6.wireOp",EDGE,"E1220"),sQuery(id+"F6.wireOp",EDGE,"E1221"),sQuery(id+"F6.wireOp",EDGE,"E1222"),sQuery(id+"F6.wireOp",EDGE,"E1223"),sQuery(id+"F6.wireOp",EDGE,"E1224"),sQuery(id+"F6.wireOp",EDGE,"E1225"),sQuery(id+"F6.wireOp",EDGE,"E1226"),sQuery(id+"F6.wireOp",EDGE,"E1227"),sQuery(id+"F6.wireOp",EDGE,"E1228"),sQuery(id+"F6.wireOp",EDGE,"E1229"),sQuery(id+"F6.wireOp",EDGE,"E1230"),sQuery(id+"F6.wireOp",EDGE,"E1231"),sQuery(id+"F6.wireOp",EDGE,"E1232"),sQuery(id+"F6.wireOp",EDGE,"E1233"),sQuery(id+"F6.wireOp",EDGE,"E1234"),sQuery(id+"F6.wireOp",EDGE,"E1235"),sQuery(id+"F6.wireOp",EDGE,"E1236"),sQuery(id+"F6.wireOp",EDGE,"E1237"),sQuery(id+"F6.wireOp",EDGE,"E1238"),sQuery(id+"F6.wireOp",EDGE,"E1239"),sQuery(id+"F6.wireOp",EDGE,"E1240"),sQuery(id+"F6.wireOp",EDGE,"E1241"),sQuery(id+"F6.wireOp",EDGE,"E1242"),sQuery(id+"F6.wireOp",EDGE,"E1243"),sQuery(id+"F6.wireOp",EDGE,"E1244"),sQuery(id+"F6.wireOp",EDGE,"E1245"),sQuery(id+"F6.wireOp",EDGE,"E1246"),sQuery(id+"F6.wireOp",EDGE,"E1247"),sQuery(id+"F6.wireOp",EDGE,"E1248"),sQuery(id+"F6.wireOp",EDGE,"E1249"),sQuery(id+"F6.wireOp",EDGE,"E1250"),sQuery(id+"F6.wireOp",EDGE,"E1251"),sQuery(id+"F6.wireOp",EDGE,"E1252"),sQuery(id+"F6.wireOp",EDGE,"E1253"),sQuery(id+"F6.wireOp",EDGE,"E1254"),sQuery(id+"F6.wireOp",EDGE,"E1255"),sQuery(id+"F6.wireOp",EDGE,"E1256"),sQuery(id+"F6.wireOp",EDGE,"E1257"),sQuery(id+"F6.wireOp",EDGE,"E1258"),sQuery(id+"F6.wireOp",EDGE,"E1259"),sQuery(id+"F6.wireOp",EDGE,"E1260"),sQuery(id+"F6.wireOp",EDGE,"E1261"),sQuery(id+"F6.wireOp",EDGE,"E1262"),sQuery(id+"F6.wireOp",EDGE,"E1263"),sQuery(id+"F6.wireOp",EDGE,"E1264"),sQuery(id+"F6.wireOp",EDGE,"E1265"),sQuery(id+"F6.wireOp",EDGE,"E1266"),sQuery(id+"F6.wireOp",EDGE,"E1267"),sQuery(id+"F6.wireOp",EDGE,"E1268"),sQuery(id+"F6.wireOp",EDGE,"E1269"),sQuery(id+"F6.wireOp",EDGE,"E1270"),sQuery(id+"F6.wireOp",EDGE,"E1271"),sQuery(id+"F6.wireOp",EDGE,"E1272"),sQuery(id+"F6.wireOp",EDGE,"E1273"),sQuery(id+"F6.wireOp",EDGE,"E1274"),sQuery(id+"F6.wireOp",EDGE,"E1275"),sQuery(id+"F6.wireOp",EDGE,"E1276"),sQuery(id+"F6.wireOp",EDGE,"E1277"),sQuery(id+"F6.wireOp",EDGE,"E1278"),sQuery(id+"F6.wireOp",EDGE,"E1279"),sQuery(id+"F6.wireOp",EDGE,"E1280"),sQuery(id+"F6.wireOp",EDGE,"E1281"),sQuery(id+"F6.wireOp",EDGE,"E1282"),sQuery(id+"F6.wireOp",EDGE,"E1283"),sQuery(id+"F6.wireOp",EDGE,"E1284"),sQuery(id+"F6.wireOp",EDGE,"E1285"),sQuery(id+"F6.wireOp",EDGE,"E1286"),sQuery(id+"F6.wireOp",EDGE,"E1287"),sQuery(id+"F6.wireOp",EDGE,"E1288"),sQuery(id+"F6.wireOp",EDGE,"E1289"),sQuery(id+"F6.wireOp",EDGE,"E1290"),sQuery(id+"F6.wireOp",EDGE,"E1291"),sQuery(id+"F6.wireOp",EDGE,"E1292"),sQuery(id+"F6.wireOp",EDGE,"E1293"),sQuery(id+"F6.wireOp",EDGE,"E1294"),sQuery(id+"F6.wireOp",EDGE,"E1295"),sQuery(id+"F6.wireOp",EDGE,"E1296"),sQuery(id+"F6.wireOp",EDGE,"E1297"),sQuery(id+"F6.wireOp",EDGE,"E1298"),sQuery(id+"F6.wireOp",EDGE,"E1299"),sQuery(id+"F6.wireOp",EDGE,"E1300"),sQuery(id+"F6.wireOp",EDGE,"E1301"),sQuery(id+"F6.wireOp",EDGE,"E1302"),sQuery(id+"F6.wireOp",EDGE,"E1303"),sQuery(id+"F6.wireOp",EDGE,"E1304"),sQuery(id+"F6.wireOp",EDGE,"E1305"),sQuery(id+"F6.wireOp",EDGE,"E1306"),sQuery(id+"F6.wireOp",EDGE,"E1307"),sQuery(id+"F6.wireOp",EDGE,"E1308"),sQuery(id+"F6.wireOp",EDGE,"E1309"),sQuery(id+"F6.wireOp",EDGE,"E1310"),sQuery(id+"F6.wireOp",EDGE,"E1311"),sQuery(id+"F6.wireOp",EDGE,"E1312"),sQuery(id+"F6.wireOp",EDGE,"E1313"),sQuery(id+"F6.wireOp",EDGE,"E1314"),sQuery(id+"F6.wireOp",EDGE,"E1315"),sQuery(id+"F6.wireOp",EDGE,"E1316"),sQuery(id+"F6.wireOp",EDGE,"E1317"),sQuery(id+"F6.wireOp",EDGE,"E1318"),sQuery(id+"F6.wireOp",EDGE,"E1319"),sQuery(id+"F6.wireOp",EDGE,"E1320"),sQuery(id+"F6.wireOp",EDGE,"E1321"),sQuery(id+"F6.wireOp",EDGE,"E1322"),sQuery(id+"F6.wireOp",EDGE,"E1323"),sQuery(id+"F6.wireOp",EDGE,"E1324"),sQuery(id+"F6.wireOp",EDGE,"E1325"),sQuery(id+"F6.wireOp",EDGE,"E1326"),sQuery(id+"F6.wireOp",EDGE,"E1327"),sQuery(id+"F6.wireOp",EDGE,"E1328"),sQuery(id+"F6.wireOp",EDGE,"E1329"),sQuery(id+"F6.wireOp",EDGE,"E1330"),sQuery(id+"F6.wireOp",EDGE,"E1331"),sQuery(id+"F6.wireOp",EDGE,"E1332"),sQuery(id+"F6.wireOp",EDGE,"E1333"),sQuery(id+"F6.wireOp",EDGE,"E1334"),sQuery(id+"F6.wireOp",EDGE,"E1335"),sQuery(id+"F6.wireOp",EDGE,"E1336"),sQuery(id+"F6.wireOp",EDGE,"E1337"),sQuery(id+"F6.wireOp",EDGE,"E1338"),sQuery(id+"F6.wireOp",EDGE,"E1339"),sQuery(id+"F6.wireOp",EDGE,"E1340"),sQuery(id+"F6.wireOp",EDGE,"E1341"),sQuery(id+"F6.wireOp",EDGE,"E1342"),sQuery(id+"F6.wireOp",EDGE,"E1343"),sQuery(id+"F6.wireOp",EDGE,"E1344"),sQuery(id+"F6.wireOp",EDGE,"E1345"),sQuery(id+"F6.wireOp",EDGE,"E1346"),sQuery(id+"F6.wireOp",EDGE,"E1347"),sQuery(id+"F6.wireOp",EDGE,"E1348"),sQuery(id+"F6.wireOp",EDGE,"E1349"),sQuery(id+"F6.wireOp",EDGE,"E1350"),sQuery(id+"F6.wireOp",EDGE,"E1351"),sQuery(id+"F6.wireOp",EDGE,"E1352"),sQuery(id+"F6.wireOp",EDGE,"E1353"),sQuery(id+"F6.wireOp",EDGE,"E1354"),sQuery(id+"F6.wireOp",EDGE,"E1355"),sQuery(id+"F6.wireOp",EDGE,"E1356"),sQuery(id+"F6.wireOp",EDGE,"E1357"),sQuery(id+"F6.wireOp",EDGE,"E1358"),sQuery(id+"F6.wireOp",EDGE,"E1359"),sQuery(id+"F6.wireOp",EDGE,"E1360"),sQuery(id+"F6.wireOp",EDGE,"E1361"),sQuery(id+"F6.wireOp",EDGE,"E1362"),sQuery(id+"F6.wireOp",EDGE,"E1363"),sQuery(id+"F6.wireOp",EDGE,"E1364"),sQuery(id+"F6.wireOp",EDGE,"E1365"),sQuery(id+"F6.wireOp",EDGE,"E1366"),sQuery(id+"F6.wireOp",EDGE,"E1367"),sQuery(id+"F6.wireOp",EDGE,"E1368"),sQuery(id+"F6.wireOp",EDGE,"E1369"),sQuery(id+"F6.wireOp",EDGE,"E1370"),sQuery(id+"F6.wireOp",EDGE,"E1371"),sQuery(id+"F6.wireOp",EDGE,"E1372"),sQuery(id+"F6.wireOp",EDGE,"E1373"),sQuery(id+"F6.wireOp",EDGE,"E1374"),sQuery(id+"F6.wireOp",EDGE,"E1375"),sQuery(id+"F6.wireOp",EDGE,"E1376"),sQuery(id+"F6.wireOp",EDGE,"E1377"),sQuery(id+"F6.wireOp",EDGE,"E1378"),sQuery(id+"F6.wireOp",EDGE,"E1379"),sQuery(id+"F6.wireOp",EDGE,"E1380"),sQuery(id+"F6.wireOp",EDGE,"E1381"),sQuery(id+"F6.wireOp",EDGE,"E1382"),sQuery(id+"F6.wireOp",EDGE,"E1383"),sQuery(id+"F6.wireOp",EDGE,"E1384"),sQuery(id+"F6.wireOp",EDGE,"E1385"),sQuery(id+"F6.wireOp",EDGE,"E1386"),sQuery(id+"F6.wireOp",EDGE,"E1387"),sQuery(id+"F6.wireOp",EDGE,"E1388"),sQuery(id+"F6.wireOp",EDGE,"E1389"),sQuery(id+"F6.wireOp",EDGE,"E1390"),sQuery(id+"F6.wireOp",EDGE,"E1391"),sQuery(id+"F6.wireOp",EDGE,"E1392"),sQuery(id+"F6.wireOp",EDGE,"E1393"),sQuery(id+"F6.wireOp",EDGE,"E1394"),sQuery(id+"F6.wireOp",EDGE,"E1395"),sQuery(id+"F6.wireOp",EDGE,"E1396"),sQuery(id+"F6.wireOp",EDGE,"E1397"),sQuery(id+"F6.wireOp",EDGE,"E1398"),sQuery(id+"F6.wireOp",EDGE,"E1399"),sQuery(id+"F6.wireOp",EDGE,"E1400"),sQuery(id+"F6.wireOp",EDGE,"E1401"),sQuery(id+"F6.wireOp",EDGE,"E1402"),sQuery(id+"F6.wireOp",EDGE,"E1403"),sQuery(id+"F6.wireOp",EDGE,"E1404"),sQuery(id+"F6.wireOp",EDGE,"E1405"),sQuery(id+"F6.wireOp",EDGE,"E1406"),sQuery(id+"F6.wireOp",EDGE,"E1407"),sQuery(id+"F6.wireOp",EDGE,"E1408"),sQuery(id+"F6.wireOp",EDGE,"E1409"),sQuery(id+"F6.wireOp",EDGE,"E1410"),sQuery(id+"F6.wireOp",EDGE,"E1411"),sQuery(id+"F6.wireOp",EDGE,"E1412"),sQuery(id+"F6.wireOp",EDGE,"E1413"),sQuery(id+"F6.wireOp",EDGE,"E1414"),sQuery(id+"F6.wireOp",EDGE,"E1415"),sQuery(id+"F6.wireOp",EDGE,"E1416"),sQuery(id+"F6.wireOp",EDGE,"E1417"),sQuery(id+"F6.wireOp",EDGE,"E1418"),sQuery(id+"F6.wireOp",EDGE,"E1419"),sQuery(id+"F6.wireOp",EDGE,"E1420"),sQuery(id+"F6.wireOp",EDGE,"E1421"),sQuery(id+"F6.wireOp",EDGE,"E1422"),sQuery(id+"F6.wireOp",EDGE,"E1423"),sQuery(id+"F6.wireOp",EDGE,"E1424"),sQuery(id+"F6.wireOp",EDGE,"E1425"),sQuery(id+"F6.wireOp",EDGE,"E1426"),sQuery(id+"F6.wireOp",EDGE,"E1427"),sQuery(id+"F6.wireOp",EDGE,"E1428"),sQuery(id+"F6.wireOp",EDGE,"E1429"),sQuery(id+"F6.wireOp",EDGE,"E1430"),sQuery(id+"F6.wireOp",EDGE,"E1431"),sQuery(id+"F6.wireOp",EDGE,"E1432"),sQuery(id+"F6.wireOp",EDGE,"E1433"),sQuery(id+"F6.wireOp",EDGE,"E1434"),sQuery(id+"F6.wireOp",EDGE,"E1435"),sQuery(id+"F6.wireOp",EDGE,"E1436"),sQuery(id+"F6.wireOp",EDGE,"E1437"),sQuery(id+"F6.wireOp",EDGE,"E1438"),sQuery(id+"F6.wireOp",EDGE,"E1439"),sQuery(id+"F6.wireOp",EDGE,"E1440"),sQuery(id+"F6.wireOp",EDGE,"E1441"),sQuery(id+"F6.wireOp",EDGE,"E1442"),sQuery(id+"F6.wireOp",EDGE,"E1443"),sQuery(id+"F6.wireOp",EDGE,"E1444"),sQuery(id+"F6.wireOp",EDGE,"E1445"),sQuery(id+"F6.wireOp",EDGE,"E1446"),sQuery(id+"F6.wireOp",EDGE,"E1447"),sQuery(id+"F6.wireOp",EDGE,"E1448"),sQuery(id+"F6.wireOp",EDGE,"E1449"),sQuery(id+"F6.wireOp",EDGE,"E1450"),sQuery(id+"F6.wireOp",EDGE,"E1451"),sQuery(id+"F6.wireOp",EDGE,"E1452"),sQuery(id+"F6.wireOp",EDGE,"E1453"),sQuery(id+"F6.wireOp",EDGE,"E1454"),sQuery(id+"F6.wireOp",EDGE,"E1455"),sQuery(id+"F6.wireOp",EDGE,"E1456"),sQuery(id+"F6.wireOp",EDGE,"E1457"),sQuery(id+"F6.wireOp",EDGE,"E1458"),sQuery(id+"F6.wireOp",EDGE,"E1459"),sQuery(id+"F6.wireOp",EDGE,"E1460"),sQuery(id+"F6.wireOp",EDGE,"E1461"),sQuery(id+"F6.wireOp",EDGE,"E1462"),sQuery(id+"F6.wireOp",EDGE,"E1463"),sQuery(id+"F6.wireOp",EDGE,"E1464"),sQuery(id+"F6.wireOp",EDGE,"E1465"),sQuery(id+"F6.wireOp",EDGE,"E1466"),sQuery(id+"F6.wireOp",EDGE,"E1467"),sQuery(id+"F6.wireOp",EDGE,"E1468"),sQuery(id+"F6.wireOp",EDGE,"E1469"),sQuery(id+"F6.wireOp",EDGE,"E1470"),sQuery(id+"F6.wireOp",EDGE,"E1471"),sQuery(id+"F6.wireOp",EDGE,"E1472"),sQuery(id+"F6.wireOp",EDGE,"E1473"),sQuery(id+"F6.wireOp",EDGE,"E1474"),sQuery(id+"F6.wireOp",EDGE,"E1475"),sQuery(id+"F6.wireOp",EDGE,"E1476"),sQuery(id+"F6.wireOp",EDGE,"E1477"),sQuery(id+"F6.wireOp",EDGE,"E1478"),sQuery(id+"F6.wireOp",EDGE,"E1479"),sQuery(id+"F6.wireOp",EDGE,"E1480"),sQuery(id+"F6.wireOp",EDGE,"E1481"),sQuery(id+"F6.wireOp",EDGE,"E1482"),sQuery(id+"F6.wireOp",EDGE,"E1483"),sQuery(id+"F6.wireOp",EDGE,"E1484"),sQuery(id+"F6.wireOp",EDGE,"E1485"),sQuery(id+"F6.wireOp",EDGE,"E1486"),sQuery(id+"F6.wireOp",EDGE,"E1487"),sQuery(id+"F6.wireOp",EDGE,"E1488"),sQuery(id+"F6.wireOp",EDGE,"E1489"),sQuery(id+"F6.wireOp",EDGE,"E1490"),sQuery(id+"F6.wireOp",EDGE,"E1491"),sQuery(id+"F6.wireOp",EDGE,"E1492"),sQuery(id+"F6.wireOp",EDGE,"E1493"),sQuery(id+"F6.wireOp",EDGE,"E1494"),sQuery(id+"F6.wireOp",EDGE,"E1495"),sQuery(id+"F6.wireOp",EDGE,"E1496"),sQuery(id+"F6.wireOp",EDGE,"E1497"),sQuery(id+"F6.wireOp",EDGE,"E1498"),sQuery(id+"F6.wireOp",EDGE,"E1499"),sQuery(id+"F6.wireOp",EDGE,"E1500"),sQuery(id+"F6.wireOp",EDGE,"E1501"),sQuery(id+"F6.wireOp",EDGE,"E1502"),sQuery(id+"F6.wireOp",EDGE,"E1503"),sQuery(id+"F6.wireOp",EDGE,"E1504"),sQuery(id+"F6.wireOp",EDGE,"E1505"),sQuery(id+"F6.wireOp",EDGE,"E1506"),sQuery(id+"F6.wireOp",EDGE,"E1507"),sQuery(id+"F6.wireOp",EDGE,"E1508"),sQuery(id+"F6.wireOp",EDGE,"E1509"),sQuery(id+"F6.wireOp",EDGE,"E1510"),sQuery(id+"F6.wireOp",EDGE,"E1511"),sQuery(id+"F6.wireOp",EDGE,"E1512"),sQuery(id+"F6.wireOp",EDGE,"E1513"),sQuery(id+"F6.wireOp",EDGE,"E1514"),sQuery(id+"F6.wireOp",EDGE,"E1515"),sQuery(id+"F6.wireOp",EDGE,"E1516"),sQuery(id+"F6.wireOp",EDGE,"E1517"),sQuery(id+"F6.wireOp",EDGE,"E1518"),sQuery(id+"F6.wireOp",EDGE,"E1519"),sQuery(id+"F6.wireOp",EDGE,"E1520"),sQuery(id+"F6.wireOp",EDGE,"E1521"),sQuery(id+"F6.wireOp",EDGE,"E1522"),sQuery(id+"F6.wireOp",EDGE,"E1523"),sQuery(id+"F6.wireOp",EDGE,"E1524"),sQuery(id+"F6.wireOp",EDGE,"E1525"),sQuery(id+"F6.wireOp",EDGE,"E1526"),sQuery(id+"F6.wireOp",EDGE,"E1527"),sQuery(id+"F6.wireOp",EDGE,"E1528"),sQuery(id+"F6.wireOp",EDGE,"E1529"),sQuery(id+"F6.wireOp",EDGE,"E1530"),sQuery(id+"F6.wireOp",EDGE,"E1531"),sQuery(id+"F6.wireOp",EDGE,"E1532"),sQuery(id+"F6.wireOp",EDGE,"E1533"),sQuery(id+"F6.wireOp",EDGE,"E1534"),sQuery(id+"F6.wireOp",EDGE,"E1535"),sQuery(id+"F6.wireOp",EDGE,"E1536"),sQuery(id+"F6.wireOp",EDGE,"E1537"),sQuery(id+"F6.wireOp",EDGE,"E1538"),sQuery(id+"F6.wireOp",EDGE,"E1539"),sQuery(id+"F6.wireOp",EDGE,"E1540"),sQuery(id+"F6.wireOp",EDGE,"E1541"),sQuery(id+"F6.wireOp",EDGE,"E1542"),sQuery(id+"F6.wireOp",EDGE,"E1543"),sQuery(id+"F6.wireOp",EDGE,"E1544"),sQuery(id+"F6.wireOp",EDGE,"E1545"),sQuery(id+"F6.wireOp",EDGE,"E1546"),sQuery(id+"F6.wireOp",EDGE,"E1547"),sQuery(id+"F6.wireOp",EDGE,"E1548"),sQuery(id+"F6.wireOp",EDGE,"E1549"),sQuery(id+"F6.wireOp",EDGE,"E1550"),sQuery(id+"F6.wireOp",EDGE,"E1551"),sQuery(id+"F6.wireOp",EDGE,"E1552"),sQuery(id+"F6.wireOp",EDGE,"E1553"),sQuery(id+"F6.wireOp",EDGE,"E1554"),sQuery(id+"F6.wireOp",EDGE,"E1555"),sQuery(id+"F6.wireOp",EDGE,"E1556"),sQuery(id+"F6.wireOp",EDGE,"E1557"),sQuery(id+"F6.wireOp",EDGE,"E1558"),sQuery(id+"F6.wireOp",EDGE,"E1559"),sQuery(id+"F6.wireOp",EDGE,"E1560"),sQuery(id+"F6.wireOp",EDGE,"E1561"),sQuery(id+"F6.wireOp",EDGE,"E1562"),sQuery(id+"F6.wireOp",EDGE,"E1563"),sQuery(id+"F6.wireOp",EDGE,"E1564"),sQuery(id+"F6.wireOp",EDGE,"E1565"),sQuery(id+"F6.wireOp",EDGE,"E1566"),sQuery(id+"F6.wireOp",EDGE,"E1567"),sQuery(id+"F6.wireOp",EDGE,"E1568"),sQuery(id+"F6.wireOp",EDGE,"E1569"),sQuery(id+"F6.wireOp",EDGE,"E1570"),sQuery(id+"F6.wireOp",EDGE,"E1571"),sQuery(id+"F6.wireOp",EDGE,"E1572"),sQuery(id+"F6.wireOp",EDGE,"E1573"),sQuery(id+"F6.wireOp",EDGE,"E1574"),sQuery(id+"F6.wireOp",EDGE,"E1575"),sQuery(id+"F6.wireOp",EDGE,"E1576"),sQuery(id+"F6.wireOp",EDGE,"E1577"),sQuery(id+"F6.wireOp",EDGE,"E1578"),sQuery(id+"F6.wireOp",EDGE,"E1579"),sQuery(id+"F6.wireOp",EDGE,"E1580"),sQuery(id+"F6.wireOp",EDGE,"E1581"),sQuery(id+"F6.wireOp",EDGE,"E1582"),sQuery(id+"F6.wireOp",EDGE,"E1583"),sQuery(id+"F6.wireOp",EDGE,"E1584"),sQuery(id+"F6.wireOp",EDGE,"E1585"),sQuery(id+"F6.wireOp",EDGE,"E1586"),sQuery(id+"F6.wireOp",EDGE,"E1587"),sQuery(id+"F6.wireOp",EDGE,"E1588"),sQuery(id+"F6.wireOp",EDGE,"E1589"),sQuery(id+"F6.wireOp",EDGE,"E1590"),sQuery(id+"F6.wireOp",EDGE,"E1591"),sQuery(id+"F6.wireOp",EDGE,"E1592"),sQuery(id+"F6.wireOp",EDGE,"E1593"),sQuery(id+"F6.wireOp",EDGE,"E1594"),sQuery(id+"F6.wireOp",EDGE,"E1595"),sQuery(id+"F6.wireOp",EDGE,"E1596"),sQuery(id+"F6.wireOp",EDGE,"E1597"),sQuery(id+"F6.wireOp",EDGE,"E1598"),sQuery(id+"F6.wireOp",EDGE,"E1599"),sQuery(id+"F6.wireOp",EDGE,"E1600"),sQuery(id+"F6.wireOp",EDGE,"E1601"),sQuery(id+"F6.wireOp",EDGE,"E1602"),sQuery(id+"F6.wireOp",EDGE,"E1603"),sQuery(id+"F6.wireOp",EDGE,"E1604"),sQuery(id+"F6.wireOp",EDGE,"E1605"),sQuery(id+"F6.wireOp",EDGE,"E1606"),sQuery(id+"F6.wireOp",EDGE,"E1607"),sQuery(id+"F6.wireOp",EDGE,"E1608"),sQuery(id+"F6.wireOp",EDGE,"E1609"),sQuery(id+"F6.wireOp",EDGE,"E1610"),sQuery(id+"F6.wireOp",EDGE,"E1611"),sQuery(id+"F6.wireOp",EDGE,"E1612"),sQuery(id+"F6.wireOp",EDGE,"E1613"),sQuery(id+"F6.wireOp",EDGE,"E1614"),sQuery(id+"F6.wireOp",EDGE,"E1615"),sQuery(id+"F6.wireOp",EDGE,"E1616"),sQuery(id+"F6.wireOp",EDGE,"E1617"),sQuery(id+"F6.wireOp",EDGE,"E1618"),sQuery(id+"F6.wireOp",EDGE,"E1619"),sQuery(id+"F6.wireOp",EDGE,"E1620"),sQuery(id+"F6.wireOp",EDGE,"E1621"),sQuery(id+"F6.wireOp",EDGE,"E1622"),sQuery(id+"F6.wireOp",EDGE,"E1623"),sQuery(id+"F6.wireOp",EDGE,"E1624"),sQuery(id+"F6.wireOp",EDGE,"E1625"),sQuery(id+"F6.wireOp",EDGE,"E1626"),sQuery(id+"F6.wireOp",EDGE,"E1627"),sQuery(id+"F6.wireOp",EDGE,"E1628"),sQuery(id+"F6.wireOp",EDGE,"E1629"),sQuery(id+"F6.wireOp",EDGE,"E1630"),sQuery(id+"F6.wireOp",EDGE,"E1631"),sQuery(id+"F6.wireOp",EDGE,"E1632"),sQuery(id+"F6.wireOp",EDGE,"E1633"),sQuery(id+"F6.wireOp",EDGE,"E1634"),sQuery(id+"F6.wireOp",EDGE,"E1635"),sQuery(id+"F6.wireOp",EDGE,"E1636"),sQuery(id+"F6.wireOp",EDGE,"E1637"),sQuery(id+"F6.wireOp",EDGE,"E1638"),sQuery(id+"F6.wireOp",EDGE,"E1639"),sQuery(id+"F6.wireOp",EDGE,"E1640"),sQuery(id+"F6.wireOp",EDGE,"E1641"),sQuery(id+"F6.wireOp",EDGE,"E1642"),sQuery(id+"F6.wireOp",EDGE,"E1643"),sQuery(id+"F6.wireOp",EDGE,"E1644"),sQuery(id+"F6.wireOp",EDGE,"E1645"),sQuery(id+"F6.wireOp",EDGE,"E1646"),sQuery(id+"F6.wireOp",EDGE,"E1647"),sQuery(id+"F6.wireOp",EDGE,"E1648"),sQuery(id+"F6.wireOp",EDGE,"E1649"),sQuery(id+"F6.wireOp",EDGE,"E1650"),sQuery(id+"F6.wireOp",EDGE,"E1651"),sQuery(id+"F6.wireOp",EDGE,"E1652"),sQuery(id+"F6.wireOp",EDGE,"E1653"),sQuery(id+"F6.wireOp",EDGE,"E1654"),sQuery(id+"F6.wireOp",EDGE,"E1655"),sQuery(id+"F6.wireOp",EDGE,"E1656"),sQuery(id+"F6.wireOp",EDGE,"E1657"),sQuery(id+"F6.wireOp",EDGE,"E1658"),sQuery(id+"F6.wireOp",EDGE,"E1659"),sQuery(id+"F6.wireOp",EDGE,"E1660"),sQuery(id+"F6.wireOp",EDGE,"E1661"),sQuery(id+"F6.wireOp",EDGE,"E1662"),sQuery(id+"F6.wireOp",EDGE,"E1663"),sQuery(id+"F6.wireOp",EDGE,"E1664"),sQuery(id+"F6.wireOp",EDGE,"E1665"),sQuery(id+"F6.wireOp",EDGE,"E1666"),sQuery(id+"F6.wireOp",EDGE,"E1667"),sQuery(id+"F6.wireOp",EDGE,"E1668"),sQuery(id+"F6.wireOp",EDGE,"E1669"),sQuery(id+"F6.wireOp",EDGE,"E1670"),sQuery(id+"F6.wireOp",EDGE,"E1671"),sQuery(id+"F6.wireOp",EDGE,"E1672"),sQuery(id+"F6.wireOp",EDGE,"E1673"),sQuery(id+"F6.wireOp",EDGE,"E1674"),sQuery(id+"F6.wireOp",EDGE,"E1675"),sQuery(id+"F6.wireOp",EDGE,"E1676"),sQuery(id+"F6.wireOp",EDGE,"E1677"),sQuery(id+"F6.wireOp",EDGE,"E1678"),sQuery(id+"F6.wireOp",EDGE,"E1679"),sQuery(id+"F6.wireOp",EDGE,"E1680"),sQuery(id+"F6.wireOp",EDGE,"E1681"),sQuery(id+"F6.wireOp",EDGE,"E1682"),sQuery(id+"F6.wireOp",EDGE,"E1683"),sQuery(id+"F6.wireOp",EDGE,"E1684"),sQuery(id+"F6.wireOp",EDGE,"E1685"),sQuery(id+"F6.wireOp",EDGE,"E1686"),sQuery(id+"F6.wireOp",EDGE,"E1687"),sQuery(id+"F6.wireOp",EDGE,"E1688"),sQuery(id+"F6.wireOp",EDGE,"E1689"),sQuery(id+"F6.wireOp",EDGE,"E1690"),sQuery(id+"F6.wireOp",EDGE,"E1691"),sQuery(id+"F6.wireOp",EDGE,"E1692"),sQuery(id+"F6.wireOp",EDGE,"E1693"),sQuery(id+"F6.wireOp",EDGE,"E1694"),sQuery(id+"F6.wireOp",EDGE,"E1695"),sQuery(id+"F6.wireOp",EDGE,"E1696"),sQuery(id+"F6.wireOp",EDGE,"E1697"),sQuery(id+"F6.wireOp",EDGE,"E1698"),sQuery(id+"F6.wireOp",EDGE,"E1699"),sQuery(id+"F6.wireOp",EDGE,"E1700"),sQuery(id+"F6.wireOp",EDGE,"E1701"),sQuery(id+"F6.wireOp",EDGE,"E1702"),sQuery(id+"F6.wireOp",EDGE,"E1703"),sQuery(id+"F6.wireOp",EDGE,"E1704"),sQuery(id+"F6.wireOp",EDGE,"E1705"),sQuery(id+"F6.wireOp",EDGE,"E1706"),sQuery(id+"F6.wireOp",EDGE,"E1707"),sQuery(id+"F6.wireOp",EDGE,"E1708"),sQuery(id+"F6.wireOp",EDGE,"E1709"),sQuery(id+"F6.wireOp",EDGE,"E1710"),sQuery(id+"F6.wireOp",EDGE,"E1711"),sQuery(id+"F6.wireOp",EDGE,"E1712"),sQuery(id+"F6.wireOp",EDGE,"E1713"),sQuery(id+"F6.wireOp",EDGE,"E1714"),sQuery(id+"F6.wireOp",EDGE,"E1715"),sQuery(id+"F6.wireOp",EDGE,"E1716"),sQuery(id+"F6.wireOp",EDGE,"E1717"),sQuery(id+"F6.wireOp",EDGE,"E1718"),sQuery(id+"F6.wireOp",EDGE,"E1719"),sQuery(id+"F6.wireOp",EDGE,"E1720"),sQuery(id+"F6.wireOp",EDGE,"E1721"),sQuery(id+"F6.wireOp",EDGE,"E1722"),sQuery(id+"F6.wireOp",EDGE,"E1723"),sQuery(id+"F6.wireOp",EDGE,"E1724"),sQuery(id+"F6.wireOp",EDGE,"E1725"),sQuery(id+"F6.wireOp",EDGE,"E1726"),sQuery(id+"F6.wireOp",EDGE,"E1727"),sQuery(id+"F6.wireOp",EDGE,"E1728"),sQuery(id+"F6.wireOp",EDGE,"E1729"),sQuery(id+"F6.wireOp",EDGE,"E1730"),sQuery(id+"F6.wireOp",EDGE,"E1731"),sQuery(id+"F6.wireOp",EDGE,"E1732"),sQuery(id+"F6.wireOp",EDGE,"E1733"),sQuery(id+"F6.wireOp",EDGE,"E1734"),sQuery(id+"F6.wireOp",EDGE,"E1735"),sQuery(id+"F6.wireOp",EDGE,"E1736"),sQuery(id+"F6.wireOp",EDGE,"E1737"),sQuery(id+"F6.wireOp",EDGE,"E1738"),sQuery(id+"F6.wireOp",EDGE,"E1739"),sQuery(id+"F6.wireOp",EDGE,"E1740"),sQuery(id+"F6.wireOp",EDGE,"E1741"),sQuery(id+"F6.wireOp",EDGE,"E1742"),sQuery(id+"F6.wireOp",EDGE,"E1743"),sQuery(id+"F6.wireOp",EDGE,"E1744"),sQuery(id+"F6.wireOp",EDGE,"E1745"),sQuery(id+"F6.wireOp",EDGE,"E1746"),sQuery(id+"F6.wireOp",EDGE,"E1747"),sQuery(id+"F6.wireOp",EDGE,"E1748"),sQuery(id+"F6.wireOp",EDGE,"E1749"),sQuery(id+"F6.wireOp",EDGE,"E1750"),sQuery(id+"F6.wireOp",EDGE,"E1751"),sQuery(id+"F6.wireOp",EDGE,"E1752"),sQuery(id+"F6.wireOp",EDGE,"E1753"),sQuery(id+"F6.wireOp",EDGE,"E1754"),sQuery(id+"F6.wireOp",EDGE,"E1755"),sQuery(id+"F6.wireOp",EDGE,"E1756"),sQuery(id+"F6.wireOp",EDGE,"E1757"),sQuery(id+"F6.wireOp",EDGE,"E1758"),sQuery(id+"F6.wireOp",EDGE,"E1759"),sQuery(id+"F6.wireOp",EDGE,"E1760"),sQuery(id+"F6.wireOp",EDGE,"E1761"),sQuery(id+"F6.wireOp",EDGE,"E1762"),sQuery(id+"F6.wireOp",EDGE,"E1763"),sQuery(id+"F6.wireOp",EDGE,"E1764"),sQuery(id+"F6.wireOp",EDGE,"E1765"),sQuery(id+"F6.wireOp",EDGE,"E1766"),sQuery(id+"F6.wireOp",EDGE,"E1767"),sQuery(id+"F6.wireOp",EDGE,"E1768"),sQuery(id+"F6.wireOp",EDGE,"E1769"),sQuery(id+"F6.wireOp",EDGE,"E1770"),sQuery(id+"F6.wireOp",EDGE,"E1771"),sQuery(id+"F6.wireOp",EDGE,"E1772"),sQuery(id+"F6.wireOp",EDGE,"E1773"),sQuery(id+"F6.wireOp",EDGE,"E1774"),sQuery(id+"F6.wireOp",EDGE,"E1775"),sQuery(id+"F6.wireOp",EDGE,"E1776"),sQuery(id+"F6.wireOp",EDGE,"E1777"),sQuery(id+"F6.wireOp",EDGE,"E1778"),sQuery(id+"F6.wireOp",EDGE,"E1779"),sQuery(id+"F6.wireOp",EDGE,"E1780"),sQuery(id+"F6.wireOp",EDGE,"E1781"),sQuery(id+"F6.wireOp",EDGE,"E1782"),sQuery(id+"F6.wireOp",EDGE,"E1783"),sQuery(id+"F6.wireOp",EDGE,"E1784"),sQuery(id+"F6.wireOp",EDGE,"E1785"),sQuery(id+"F6.wireOp",EDGE,"E1786"),sQuery(id+"F6.wireOp",EDGE,"E1787"),sQuery(id+"F6.wireOp",EDGE,"E1788"),sQuery(id+"F6.wireOp",EDGE,"E1789"),sQuery(id+"F6.wireOp",EDGE,"E1790"),sQuery(id+"F6.wireOp",EDGE,"E1791"),sQuery(id+"F6.wireOp",EDGE,"E1792"),sQuery(id+"F6.wireOp",EDGE,"E1793"),sQuery(id+"F6.wireOp",EDGE,"E1794"),sQuery(id+"F6.wireOp",EDGE,"E1795"),sQuery(id+"F6.wireOp",EDGE,"E1796"),sQuery(id+"F6.wireOp",EDGE,"E1797"),sQuery(id+"F6.wireOp",EDGE,"E1798"),sQuery(id+"F6.wireOp",EDGE,"E1799"),sQuery(id+"F6.wireOp",EDGE,"E1800"),sQuery(id+"F6.wireOp",EDGE,"E1801"),sQuery(id+"F6.wireOp",EDGE,"E1802"),sQuery(id+"F6.wireOp",EDGE,"E1803"),sQuery(id+"F6.wireOp",EDGE,"E1804"),sQuery(id+"F6.wireOp",EDGE,"E1805"),sQuery(id+"F6.wireOp",EDGE,"E1806"),sQuery(id+"F6.wireOp",EDGE,"E1807"),sQuery(id+"F6.wireOp",EDGE,"E1808"),sQuery(id+"F6.wireOp",EDGE,"E1809"),sQuery(id+"F6.wireOp",EDGE,"E1810"),sQuery(id+"F6.wireOp",EDGE,"E1811"),sQuery(id+"F6.wireOp",EDGE,"E1812"),sQuery(id+"F6.wireOp",EDGE,"E1813"),sQuery(id+"F6.wireOp",EDGE,"E1814"),sQuery(id+"F6.wireOp",EDGE,"E1815"),sQuery(id+"F6.wireOp",EDGE,"E1816"),sQuery(id+"F6.wireOp",EDGE,"E1817"),sQuery(id+"F6.wireOp",EDGE,"E1818"),sQuery(id+"F6.wireOp",EDGE,"E1819"),sQuery(id+"F6.wireOp",EDGE,"E1820"),sQuery(id+"F6.wireOp",EDGE,"E1821"),sQuery(id+"F6.wireOp",EDGE,"E1822"),sQuery(id+"F6.wireOp",EDGE,"E1823"),sQuery(id+"F6.wireOp",EDGE,"E1824"),sQuery(id+"F6.wireOp",EDGE,"E1825"),sQuery(id+"F6.wireOp",EDGE,"E1826"),sQuery(id+"F6.wireOp",EDGE,"E1827"),sQuery(id+"F6.wireOp",EDGE,"E1828"),sQuery(id+"F6.wireOp",EDGE,"E1829"),sQuery(id+"F6.wireOp",EDGE,"E1830"),sQuery(id+"F6.wireOp",EDGE,"E1831"),sQuery(id+"F6.wireOp",EDGE,"E1832"),sQuery(id+"F6.wireOp",EDGE,"E1833"),sQuery(id+"F6.wireOp",EDGE,"E1834"),sQuery(id+"F6.wireOp",EDGE,"E1835"),sQuery(id+"F6.wireOp",EDGE,"E1836"),sQuery(id+"F6.wireOp",EDGE,"E1837"),sQuery(id+"F6.wireOp",EDGE,"E1838"),sQuery(id+"F6.wireOp",EDGE,"E1839"),sQuery(id+"F6.wireOp",EDGE,"E1840"),sQuery(id+"F6.wireOp",EDGE,"E1841"),sQuery(id+"F6.wireOp",EDGE,"E1842"),sQuery(id+"F6.wireOp",EDGE,"E1843"),sQuery(id+"F6.wireOp",EDGE,"E1844"),sQuery(id+"F6.wireOp",EDGE,"E1845"),sQuery(id+"F6.wireOp",EDGE,"E1846"),sQuery(id+"F6.wireOp",EDGE,"E1847"),sQuery(id+"F6.wireOp",EDGE,"E1848"),sQuery(id+"F6.wireOp",EDGE,"E1849"),sQuery(id+"F6.wireOp",EDGE,"E1850"),sQuery(id+"F6.wireOp",EDGE,"E1851"),sQuery(id+"F6.wireOp",EDGE,"E1852"),sQuery(id+"F6.wireOp",EDGE,"E1853"),sQuery(id+"F6.wireOp",EDGE,"E1854"),sQuery(id+"F6.wireOp",EDGE,"E1855"),sQuery(id+"F6.wireOp",EDGE,"E1856"),sQuery(id+"F6.wireOp",EDGE,"E1857"),sQuery(id+"F6.wireOp",EDGE,"E1858"),sQuery(id+"F6.wireOp",EDGE,"E1859"),sQuery(id+"F6.wireOp",EDGE,"E1860"),sQuery(id+"F6.wireOp",EDGE,"E1861"),sQuery(id+"F6.wireOp",EDGE,"E1862"),sQuery(id+"F6.wireOp",EDGE,"E1863"),sQuery(id+"F6.wireOp",EDGE,"E1864"),sQuery(id+"F6.wireOp",EDGE,"E1865"),sQuery(id+"F6.wireOp",EDGE,"E1866"),sQuery(id+"F6.wireOp",EDGE,"E1867"),sQuery(id+"F6.wireOp",EDGE,"E1868"),sQuery(id+"F6.wireOp",EDGE,"E1869"),sQuery(id+"F6.wireOp",EDGE,"E1870"),sQuery(id+"F6.wireOp",EDGE,"E1871"),sQuery(id+"F6.wireOp",EDGE,"E1872"),sQuery(id+"F6.wireOp",EDGE,"E1873"),sQuery(id+"F6.wireOp",EDGE,"E1874"),sQuery(id+"F6.wireOp",EDGE,"E1875"),sQuery(id+"F6.wireOp",EDGE,"E1876"),sQuery(id+"F6.wireOp",EDGE,"E1877"),sQuery(id+"F6.wireOp",EDGE,"E1878"),sQuery(id+"F6.wireOp",EDGE,"E1879"),sQuery(id+"F6.wireOp",EDGE,"E1880"),sQuery(id+"F6.wireOp",EDGE,"E1881"),sQuery(id+"F6.wireOp",EDGE,"E1882"),sQuery(id+"F6.wireOp",EDGE,"E1883"),sQuery(id+"F6.wireOp",EDGE,"E1884"),sQuery(id+"F6.wireOp",EDGE,"E1885"),sQuery(id+"F6.wireOp",EDGE,"E1886"),sQuery(id+"F6.wireOp",EDGE,"E1887"),sQuery(id+"F6.wireOp",EDGE,"E1888"),sQuery(id+"F6.wireOp",EDGE,"E1889"),sQuery(id+"F6.wireOp",EDGE,"E1890"),sQuery(id+"F6.wireOp",EDGE,"E1891"),sQuery(id+"F6.wireOp",EDGE,"E1892"),sQuery(id+"F6.wireOp",EDGE,"E1893"),sQuery(id+"F6.wireOp",EDGE,"E1894"),sQuery(id+"F6.wireOp",EDGE,"E1895"),sQuery(id+"F6.wireOp",EDGE,"E1896"),sQuery(id+"F6.wireOp",EDGE,"E1897"),sQuery(id+"F6.wireOp",EDGE,"E1898"),sQuery(id+"F6.wireOp",EDGE,"E1899"),sQuery(id+"F6.wireOp",EDGE,"E1900"),sQuery(id+"F6.wireOp",EDGE,"E1901"),sQuery(id+"F6.wireOp",EDGE,"E1902"),sQuery(id+"F6.wireOp",EDGE,"E1903"),sQuery(id+"F6.wireOp",EDGE,"E1904"),sQuery(id+"F6.wireOp",EDGE,"E1905"),sQuery(id+"F6.wireOp",EDGE,"E1906"),sQuery(id+"F6.wireOp",EDGE,"E1907"),sQuery(id+"F6.wireOp",EDGE,"E1908"),sQuery(id+"F6.wireOp",EDGE,"E1909"),sQuery(id+"F6.wireOp",EDGE,"E1910"),sQuery(id+"F6.wireOp",EDGE,"E1911"),sQuery(id+"F6.wireOp",EDGE,"E1912"),sQuery(id+"F6.wireOp",EDGE,"E1913"),sQuery(id+"F6.wireOp",EDGE,"E1914"),sQuery(id+"F6.wireOp",EDGE,"E1915"),sQuery(id+"F6.wireOp",EDGE,"E1916"),sQuery(id+"F6.wireOp",EDGE,"E1917"),sQuery(id+"F6.wireOp",EDGE,"E1918"),sQuery(id+"F6.wireOp",EDGE,"E1919"),sQuery(id+"F6.wireOp",EDGE,"E1920"),sQuery(id+"F6.wireOp",EDGE,"E1921"),sQuery(id+"F6.wireOp",EDGE,"E1922"),sQuery(id+"F6.wireOp",EDGE,"E1923"),sQuery(id+"F6.wireOp",EDGE,"E1924"),sQuery(id+"F6.wireOp",EDGE,"E1925"),sQuery(id+"F6.wireOp",EDGE,"E1926"),sQuery(id+"F6.wireOp",EDGE,"E1927"),sQuery(id+"F6.wireOp",EDGE,"E1928"),sQuery(id+"F6.wireOp",EDGE,"E1929"),sQuery(id+"F6.wireOp",EDGE,"E1930"),sQuery(id+"F6.wireOp",EDGE,"E1931"),sQuery(id+"F6.wireOp",EDGE,"E1932"),sQuery(id+"F6.wireOp",EDGE,"E1933"),sQuery(id+"F6.wireOp",EDGE,"E1934"),sQuery(id+"F6.wireOp",EDGE,"E1935"),sQuery(id+"F6.wireOp",EDGE,"E1936"),sQuery(id+"F6.wireOp",EDGE,"E1937"),sQuery(id+"F6.wireOp",EDGE,"E1938"),sQuery(id+"F6.wireOp",EDGE,"E1939"),sQuery(id+"F6.wireOp",EDGE,"E1940"),sQuery(id+"F6.wireOp",EDGE,"E1941"),sQuery(id+"F6.wireOp",EDGE,"E1942"),sQuery(id+"F6.wireOp",EDGE,"E1943"),sQuery(id+"F6.wireOp",EDGE,"E1944"),sQuery(id+"F6.wireOp",EDGE,"E1945"),sQuery(id+"F6.wireOp",EDGE,"E1946"),sQuery(id+"F6.wireOp",EDGE,"E1947"),sQuery(id+"F6.wireOp",EDGE,"E1948"),sQuery(id+"F6.wireOp",EDGE,"E1949"),sQuery(id+"F6.wireOp",EDGE,"E1950"),sQuery(id+"F6.wireOp",EDGE,"E1951"),sQuery(id+"F6.wireOp",EDGE,"E1952"),sQuery(id+"F6.wireOp",EDGE,"E1953"),sQuery(id+"F6.wireOp",EDGE,"E1954"),sQuery(id+"F6.wireOp",EDGE,"E1955"),sQuery(id+"F6.wireOp",EDGE,"E1956"),sQuery(id+"F6.wireOp",EDGE,"E1957"),sQuery(id+"F6.wireOp",EDGE,"E1958"),sQuery(id+"F6.wireOp",EDGE,"E1959"),sQuery(id+"F6.wireOp",EDGE,"E1960"),sQuery(id+"F6.wireOp",EDGE,"E1961"),sQuery(id+"F6.wireOp",EDGE,"E1962"),sQuery(id+"F6.wireOp",EDGE,"E1963"),sQuery(id+"F6.wireOp",EDGE,"E1964"),sQuery(id+"F6.wireOp",EDGE,"E1965"),sQuery(id+"F6.wireOp",EDGE,"E1966"),sQuery(id+"F6.wireOp",EDGE,"E1967"),sQuery(id+"F6.wireOp",EDGE,"E1968"),sQuery(id+"F6.wireOp",EDGE,"E1969"),sQuery(id+"F6.wireOp",EDGE,"E1970"),sQuery(id+"F6.wireOp",EDGE,"E1971"),sQuery(id+"F6.wireOp",EDGE,"E1972"),sQuery(id+"F6.wireOp",EDGE,"E1973"),sQuery(id+"F6.wireOp",EDGE,"E1974"),sQuery(id+"F6.wireOp",EDGE,"E1975"),sQuery(id+"F6.wireOp",EDGE,"E1976"),sQuery(id+"F6.wireOp",EDGE,"E1977"),sQuery(id+"F6.wireOp",EDGE,"E1978"),sQuery(id+"F6.wireOp",EDGE,"E1979"),sQuery(id+"F6.wireOp",EDGE,"E1980"),sQuery(id+"F6.wireOp",EDGE,"E1981"),sQuery(id+"F6.wireOp",EDGE,"E1982"),sQuery(id+"F6.wireOp",EDGE,"E1983"),sQuery(id+"F6.wireOp",EDGE,"E1984"),sQuery(id+"F6.wireOp",EDGE,"E1985"),sQuery(id+"F6.wireOp",EDGE,"E1986"),sQuery(id+"F6.wireOp",EDGE,"E1987"),sQuery(id+"F6.wireOp",EDGE,"E1988"),sQuery(id+"F6.wireOp",EDGE,"E1989"),sQuery(id+"F6.wireOp",EDGE,"E1990"),sQuery(id+"F6.wireOp",EDGE,"E1991"),sQuery(id+"F6.wireOp",EDGE,"E1992"),sQuery(id+"F6.wireOp",EDGE,"E1993"),sQuery(id+"F6.wireOp",EDGE,"E1994"),sQuery(id+"F6.wireOp",EDGE,"E1995"),sQuery(id+"F6.wireOp",EDGE,"E1996"),sQuery(id+"F6.wireOp",EDGE,"E1997"),sQuery(id+"F6.wireOp",EDGE,"E1998"),sQuery(id+"F6.wireOp",EDGE,"E1999"),sQuery(id+"F6.wireOp",EDGE,"E2000"),sQuery(id+"F6.wireOp",EDGE,"E2001"),sQuery(id+"F6.wireOp",EDGE,"E2002"),sQuery(id+"F6.wireOp",EDGE,"E2003"),sQuery(id+"F6.wireOp",EDGE,"E2004"),sQuery(id+"F6.wireOp",EDGE,"E2005"),sQuery(id+"F6.wireOp",EDGE,"E2006"),sQuery(id+"F6.wireOp",EDGE,"E2007"),sQuery(id+"F6.wireOp",EDGE,"E2008"),sQuery(id+"F6.wireOp",EDGE,"E2009"),sQuery(id+"F6.wireOp",EDGE,"E2010"),sQuery(id+"F6.wireOp",EDGE,"E2011"),sQuery(id+"F6.wireOp",EDGE,"E2012"),sQuery(id+"F6.wireOp",EDGE,"E2013"),sQuery(id+"F6.wireOp",EDGE,"E2014"),sQuery(id+"F6.wireOp",EDGE,"E2015"),sQuery(id+"F6.wireOp",EDGE,"E2016"),sQuery(id+"F6.wireOp",EDGE,"E2017"),sQuery(id+"F6.wireOp",EDGE,"E2018"),sQuery(id+"F6.wireOp",EDGE,"E2019"),sQuery(id+"F6.wireOp",EDGE,"E2020"),sQuery(id+"F6.wireOp",EDGE,"E2021"),sQuery(id+"F6.wireOp",EDGE,"E2022"),sQuery(id+"F6.wireOp",EDGE,"E2023"),sQuery(id+"F6.wireOp",EDGE,"E2024"),sQuery(id+"F6.wireOp",EDGE,"E2025"),sQuery(id+"F6.wireOp",EDGE,"E2026"),sQuery(id+"F6.wireOp",EDGE,"E2027"),sQuery(id+"F6.wireOp",EDGE,"E2028"),sQuery(id+"F6.wireOp",EDGE,"E2029"),sQuery(id+"F6.wireOp",EDGE,"E2030"),sQuery(id+"F6.wireOp",EDGE,"E2031"),sQuery(id+"F6.wireOp",EDGE,"E2032"),sQuery(id+"F6.wireOp",EDGE,"E2033"),sQuery(id+"F6.wireOp",EDGE,"E2034"),sQuery(id+"F6.wireOp",EDGE,"E2035"),sQuery(id+"F6.wireOp",EDGE,"E2036"),sQuery(id+"F6.wireOp",EDGE,"E2037"),sQuery(id+"F6.wireOp",EDGE,"E2038"),sQuery(id+"F6.wireOp",EDGE,"E2039"),sQuery(id+"F6.wireOp",EDGE,"E2040"),sQuery(id+"F6.wireOp",EDGE,"E2041"),sQuery(id+"F6.wireOp",EDGE,"E2042"),sQuery(id+"F6.wireOp",EDGE,"E2043"),sQuery(id+"F6.wireOp",EDGE,"E2044"),sQuery(id+"F6.wireOp",EDGE,"E2045"),sQuery(id+"F6.wireOp",EDGE,"E2046"),sQuery(id+"F6.wireOp",EDGE,"E2047"),sQuery(id+"F6.wireOp",EDGE,"E2048"),sQuery(id+"F6.wireOp",EDGE,"E2049"),sQuery(id+"F6.wireOp",EDGE,"E2050"),sQuery(id+"F6.wireOp",EDGE,"E2051"),sQuery(id+"F6.wireOp",EDGE,"E2052"),sQuery(id+"F6.wireOp",EDGE,"E2053"),sQuery(id+"F6.wireOp",EDGE,"E2054"),sQuery(id+"F6.wireOp",EDGE,"E2055"),sQuery(id+"F6.wireOp",EDGE,"E2056"),sQuery(id+"F6.wireOp",EDGE,"E2057"),sQuery(id+"F6.wireOp",EDGE,"E2058"),sQuery(id+"F6.wireOp",EDGE,"E2059"),sQuery(id+"F6.wireOp",EDGE,"E2060"),sQuery(id+"F6.wireOp",EDGE,"E2061"),sQuery(id+"F6.wireOp",EDGE,"E2062"),sQuery(id+"F6.wireOp",EDGE,"E2063"),sQuery(id+"F6.wireOp",EDGE,"E2064"),sQuery(id+"F6.wireOp",EDGE,"E2065"),sQuery(id+"F6.wireOp",EDGE,"E2066"),sQuery(id+"F6.wireOp",EDGE,"E2067"),sQuery(id+"F6.wireOp",EDGE,"E2068"),sQuery(id+"F6.wireOp",EDGE,"E2069"),sQuery(id+"F6.wireOp",EDGE,"E2070"),sQuery(id+"F6.wireOp",EDGE,"E2071"),sQuery(id+"F6.wireOp",EDGE,"E2072"),sQuery(id+"F6.wireOp",EDGE,"E2073"),sQuery(id+"F6.wireOp",EDGE,"E2074"),sQuery(id+"F6.wireOp",EDGE,"E2075"),sQuery(id+"F6.wireOp",EDGE,"E2076"),sQuery(id+"F6.wireOp",EDGE,"E2077"),sQuery(id+"F6.wireOp",EDGE,"E2078"),sQuery(id+"F6.wireOp",EDGE,"E2079"),sQuery(id+"F6.wireOp",EDGE,"E2080"),sQuery(id+"F6.wireOp",EDGE,"E2081"),sQuery(id+"F6.wireOp",EDGE,"E2082"),sQuery(id+"F6.wireOp",EDGE,"E2083"),sQuery(id+"F6.wireOp",EDGE,"E2084"),sQuery(id+"F6.wireOp",EDGE,"E2085"),sQuery(id+"F6.wireOp",EDGE,"E2086"),sQuery(id+"F6.wireOp",EDGE,"E2087"),sQuery(id+"F6.wireOp",EDGE,"E2088"),sQuery(id+"F6.wireOp",EDGE,"E2089"),sQuery(id+"F6.wireOp",EDGE,"E2090"),sQuery(id+"F6.wireOp",EDGE,"E2091"),sQuery(id+"F6.wireOp",EDGE,"E2092"),sQuery(id+"F6.wireOp",EDGE,"E2093"),sQuery(id+"F6.wireOp",EDGE,"E2094"),sQuery(id+"F6.wireOp",EDGE,"E2095"),sQuery(id+"F6.wireOp",EDGE,"E2096"),sQuery(id+"F6.wireOp",EDGE,"E2097"),sQuery(id+"F6.wireOp",EDGE,"E2098"),sQuery(id+"F6.wireOp",EDGE,"E2099"),sQuery(id+"F6.wireOp",EDGE,"E2100"),sQuery(id+"F6.wireOp",EDGE,"E2101"),sQuery(id+"F6.wireOp",EDGE,"E2102"),sQuery(id+"F6.wireOp",EDGE,"E2103"),sQuery(id+"F6.wireOp",EDGE,"E2104"),sQuery(id+"F6.wireOp",EDGE,"E2105"),sQuery(id+"F6.wireOp",EDGE,"E2106"),sQuery(id+"F6.wireOp",EDGE,"E2107"),sQuery(id+"F6.wireOp",EDGE,"E2108"),sQuery(id+"F6.wireOp",EDGE,"E2109"),sQuery(id+"F6.wireOp",EDGE,"E2110"),sQuery(id+"F6.wireOp",EDGE,"E2111"),sQuery(id+"F6.wireOp",EDGE,"E2112"),sQuery(id+"F6.wireOp",EDGE,"E2113"),sQuery(id+"F6.wireOp",EDGE,"E2114"),sQuery(id+"F6.wireOp",EDGE,"E2115"),sQuery(id+"F6.wireOp",EDGE,"E2116"),sQuery(id+"F6.wireOp",EDGE,"E2117"),sQuery(id+"F6.wireOp",EDGE,"E2118"),sQuery(id+"F6.wireOp",EDGE,"E2119"),sQuery(id+"F6.wireOp",EDGE,"E2120"),sQuery(id+"F6.wireOp",EDGE,"E2121"),sQuery(id+"F6.wireOp",EDGE,"E2122"),sQuery(id+"F6.wireOp",EDGE,"E2123"),sQuery(id+"F6.wireOp",EDGE,"E2124"),sQuery(id+"F6.wireOp",EDGE,"E2125"),sQuery(id+"F6.wireOp",EDGE,"E2126"),sQuery(id+"F6.wireOp",EDGE,"E2127"),sQuery(id+"F6.wireOp",EDGE,"E2128"),sQuery(id+"F6.wireOp",EDGE,"E2129"),sQuery(id+"F6.wireOp",EDGE,"E2130"),sQuery(id+"F6.wireOp",EDGE,"E2131"),sQuery(id+"F6.wireOp",EDGE,"E2132"),sQuery(id+"F6.wireOp",EDGE,"E2133"),sQuery(id+"F6.wireOp",EDGE,"E2134"),sQuery(id+"F6.wireOp",EDGE,"E2135"),sQuery(id+"F6.wireOp",EDGE,"E2136"),sQuery(id+"F6.wireOp",EDGE,"E2137"),sQuery(id+"F6.wireOp",EDGE,"E2138"),sQuery(id+"F6.wireOp",EDGE,"E2139"),sQuery(id+"F6.wireOp",EDGE,"E2140"),sQuery(id+"F6.wireOp",EDGE,"E2141"),sQuery(id+"F6.wireOp",EDGE,"E2142"),sQuery(id+"F6.wireOp",EDGE,"E2143"),sQuery(id+"F6.wireOp",EDGE,"E2144"),sQuery(id+"F6.wireOp",EDGE,"E2145"),sQuery(id+"F6.wireOp",EDGE,"E2146"),sQuery(id+"F6.wireOp",EDGE,"E2147"),sQuery(id+"F6.wireOp",EDGE,"E2148"),sQuery(id+"F6.wireOp",EDGE,"E2149"),sQuery(id+"F6.wireOp",EDGE,"E2150"),sQuery(id+"F6.wireOp",EDGE,"E2151"),sQuery(id+"F6.wireOp",EDGE,"E2152"),sQuery(id+"F6.wireOp",EDGE,"E2153"),sQuery(id+"F6.wireOp",EDGE,"E2154"),sQuery(id+"F6.wireOp",EDGE,"E2155"),sQuery(id+"F6.wireOp",EDGE,"E2156"),sQuery(id+"F6.wireOp",EDGE,"E2157"),sQuery(id+"F6.wireOp",EDGE,"E2158"),sQuery(id+"F6.wireOp",EDGE,"E2159"),sQuery(id+"F6.wireOp",EDGE,"E2160"),sQuery(id+"F6.wireOp",EDGE,"E2161"),sQuery(id+"F6.wireOp",EDGE,"E2162"),sQuery(id+"F6.wireOp",EDGE,"E2163"),sQuery(id+"F6.wireOp",EDGE,"E2164"),sQuery(id+"F6.wireOp",EDGE,"E2165"),sQuery(id+"F6.wireOp",EDGE,"E2166"),sQuery(id+"F6.wireOp",EDGE,"E2167"),sQuery(id+"F6.wireOp",EDGE,"E2168"),sQuery(id+"F6.wireOp",EDGE,"E2169"),sQuery(id+"F6.wireOp",EDGE,"E2170"),sQuery(id+"F6.wireOp",EDGE,"E2171"),sQuery(id+"F6.wireOp",EDGE,"E2172"),sQuery(id+"F6.wireOp",EDGE,"E2173"),sQuery(id+"F6.wireOp",EDGE,"E2174"),sQuery(id+"F6.wireOp",EDGE,"E2175"),sQuery(id+"F6.wireOp",EDGE,"E2176"),sQuery(id+"F6.wireOp",EDGE,"E2177"),sQuery(id+"F6.wireOp",EDGE,"E2178"),sQuery(id+"F6.wireOp",EDGE,"E2179"),sQuery(id+"F6.wireOp",EDGE,"E2180"),sQuery(id+"F6.wireOp",EDGE,"E2181"),sQuery(id+"F6.wireOp",EDGE,"E2182"),sQuery(id+"F6.wireOp",EDGE,"E2183"),sQuery(id+"F6.wireOp",EDGE,"E2184"),sQuery(id+"F6.wireOp",EDGE,"E2185"),sQuery(id+"F6.wireOp",EDGE,"E2186"),sQuery(id+"F6.wireOp",EDGE,"E2187"),sQuery(id+"F6.wireOp",EDGE,"E2188"),sQuery(id+"F6.wireOp",EDGE,"E2189"),sQuery(id+"F6.wireOp",EDGE,"E2190"),sQuery(id+"F6.wireOp",EDGE,"E2191"),sQuery(id+"F6.wireOp",EDGE,"E2192"),sQuery(id+"F6.wireOp",EDGE,"E2193"),sQuery(id+"F6.wireOp",EDGE,"E2194"),sQuery(id+"F6.wireOp",EDGE,"E2195"),sQuery(id+"F6.wireOp",EDGE,"E2196"),sQuery(id+"F6.wireOp",EDGE,"E2197"),sQuery(id+"F6.wireOp",EDGE,"E2198"),sQuery(id+"F6.wireOp",EDGE,"E2199"),sQuery(id+"F6.wireOp",EDGE,"E2200"),sQuery(id+"F6.wireOp",EDGE,"E2201"),sQuery(id+"F6.wireOp",EDGE,"E2202"),sQuery(id+"F6.wireOp",EDGE,"E2203"),sQuery(id+"F6.wireOp",EDGE,"E2204"),sQuery(id+"F6.wireOp",EDGE,"E2205"),sQuery(id+"F6.wireOp",EDGE,"E2206"),sQuery(id+"F6.wireOp",EDGE,"E2207"),sQuery(id+"F6.wireOp",EDGE,"E2208"),sQuery(id+"F6.wireOp",EDGE,"E2209"),sQuery(id+"F6.wireOp",EDGE,"E2210"),sQuery(id+"F6.wireOp",EDGE,"E2211"),sQuery(id+"F6.wireOp",EDGE,"E2212"),sQuery(id+"F6.wireOp",EDGE,"E2213"),sQuery(id+"F6.wireOp",EDGE,"E2214"),sQuery(id+"F6.wireOp",EDGE,"E2215"),sQuery(id+"F6.wireOp",EDGE,"E2216"),sQuery(id+"F6.wireOp",EDGE,"E2217"),sQuery(id+"F6.wireOp",EDGE,"E2218"),sQuery(id+"F6.wireOp",EDGE,"E2219"),sQuery(id+"F6.wireOp",EDGE,"E2220"),sQuery(id+"F6.wireOp",EDGE,"E2221"),sQuery(id+"F6.wireOp",EDGE,"E2222"),sQuery(id+"F6.wireOp",EDGE,"E2223"),sQuery(id+"F6.wireOp",EDGE,"E2224"),sQuery(id+"F6.wireOp",EDGE,"E2225"),sQuery(id+"F6.wireOp",EDGE,"E2226"),sQuery(id+"F6.wireOp",EDGE,"E2227"),sQuery(id+"F6.wireOp",EDGE,"E2228"),sQuery(id+"F6.wireOp",EDGE,"E2229"),sQuery(id+"F6.wireOp",EDGE,"E2230"),sQuery(id+"F6.wireOp",EDGE,"E2231"),sQuery(id+"F6.wireOp",EDGE,"E2232"),sQuery(id+"F6.wireOp",EDGE,"E2233"),sQuery(id+"F6.wireOp",EDGE,"E2234"),sQuery(id+"F6.wireOp",EDGE,"E2235"),sQuery(id+"F6.wireOp",EDGE,"E2236"),sQuery(id+"F6.wireOp",EDGE,"E2237"),sQuery(id+"F6.wireOp",EDGE,"E2238"),sQuery(id+"F6.wireOp",EDGE,"E2239"),sQuery(id+"F6.wireOp",EDGE,"E2240"),sQuery(id+"F6.wireOp",EDGE,"E2241"),sQuery(id+"F6.wireOp",EDGE,"E2242"),sQuery(id+"F6.wireOp",EDGE,"E2243"),sQuery(id+"F6.wireOp",EDGE,"E2244"),sQuery(id+"F6.wireOp",EDGE,"E2245"),sQuery(id+"F6.wireOp",EDGE,"E2246"),sQuery(id+"F6.wireOp",EDGE,"E2247"),sQuery(id+"F6.wireOp",EDGE,"E2248"),sQuery(id+"F6.wireOp",EDGE,"E2249"),sQuery(id+"F6.wireOp",EDGE,"E2250"),sQuery(id+"F6.wireOp",EDGE,"E2251"),sQuery(id+"F6.wireOp",EDGE,"E2252"),sQuery(id+"F6.wireOp",EDGE,"E2253"),sQuery(id+"F6.wireOp",EDGE,"E2254"),sQuery(id+"F6.wireOp",EDGE,"E2255"),sQuery(id+"F6.wireOp",EDGE,"E2256"),sQuery(id+"F6.wireOp",EDGE,"E2257"),sQuery(id+"F6.wireOp",EDGE,"E2258"),sQuery(id+"F6.wireOp",EDGE,"E2259"),sQuery(id+"F6.wireOp",EDGE,"E2260"),sQuery(id+"F6.wireOp",EDGE,"E2261"),sQuery(id+"F6.wireOp",EDGE,"E2262"),sQuery(id+"F6.wireOp",EDGE,"E2263"),sQuery(id+"F6.wireOp",EDGE,"E2264"),sQuery(id+"F6.wireOp",EDGE,"E2265"),sQuery(id+"F6.wireOp",EDGE,"E2266"),sQuery(id+"F6.wireOp",EDGE,"E2267"),sQuery(id+"F6.wireOp",EDGE,"E2268"),sQuery(id+"F6.wireOp",EDGE,"E2269"),sQuery(id+"F6.wireOp",EDGE,"E2270"),sQuery(id+"F6.wireOp",EDGE,"E2271"),sQuery(id+"F6.wireOp",EDGE,"E2272"),sQuery(id+"F6.wireOp",EDGE,"E2273"),sQuery(id+"F6.wireOp",EDGE,"E2274"),sQuery(id+"F6.wireOp",EDGE,"E2275"),sQuery(id+"F6.wireOp",EDGE,"E2276"),sQuery(id+"F6.wireOp",EDGE,"E2277"),sQuery(id+"F6.wireOp",EDGE,"E2278"),sQuery(id+"F6.wireOp",EDGE,"E2279"),sQuery(id+"F6.wireOp",EDGE,"E2280"),sQuery(id+"F6.wireOp",EDGE,"E2281"),sQuery(id+"F6.wireOp",EDGE,"E2282"),sQuery(id+"F6.wireOp",EDGE,"E2283"),sQuery(id+"F6.wireOp",EDGE,"E2284"),sQuery(id+"F6.wireOp",EDGE,"E2285"),sQuery(id+"F6.wireOp",EDGE,"E2286"),sQuery(id+"F6.wireOp",EDGE,"E2287"),sQuery(id+"F6.wireOp",EDGE,"E2288"),sQuery(id+"F6.wireOp",EDGE,"E2289"),sQuery(id+"F6.wireOp",EDGE,"E2290"),sQuery(id+"F6.wireOp",EDGE,"E2291"),sQuery(id+"F6.wireOp",EDGE,"E2292"),sQuery(id+"F6.wireOp",EDGE,"E2293"),sQuery(id+"F6.wireOp",EDGE,"E2294"),sQuery(id+"F6.wireOp",EDGE,"E2295"),sQuery(id+"F6.wireOp",EDGE,"E2296"),sQuery(id+"F6.wireOp",EDGE,"E2297"),sQuery(id+"F6.wireOp",EDGE,"E2298"),sQuery(id+"F6.wireOp",EDGE,"E2299"),sQuery(id+"F6.wireOp",EDGE,"E2300"),sQuery(id+"F6.wireOp",EDGE,"E2301"),sQuery(id+"F6.wireOp",EDGE,"E2302"),sQuery(id+"F6.wireOp",EDGE,"E2303"),sQuery(id+"F6.wireOp",EDGE,"E2304"),sQuery(id+"F6.wireOp",EDGE,"E2305"),sQuery(id+"F6.wireOp",EDGE,"E2306"),sQuery(id+"F6.wireOp",EDGE,"E2307"),sQuery(id+"F6.wireOp",EDGE,"E2308"),sQuery(id+"F6.wireOp",EDGE,"E2309"),sQuery(id+"F6.wireOp",EDGE,"E2310"),sQuery(id+"F6.wireOp",EDGE,"E2311"),sQuery(id+"F6.wireOp",EDGE,"E2312"),sQuery(id+"F6.wireOp",EDGE,"E2313"),sQuery(id+"F6.wireOp",EDGE,"E2314"),sQuery(id+"F6.wireOp",EDGE,"E2315"),sQuery(id+"F6.wireOp",EDGE,"E2316"),sQuery(id+"F6.wireOp",EDGE,"E2317"),sQuery(id+"F6.wireOp",EDGE,"E2318"),sQuery(id+"F6.wireOp",EDGE,"E2319"),sQuery(id+"F6.wireOp",EDGE,"E2320"),sQuery(id+"F6.wireOp",EDGE,"E2321"),sQuery(id+"F6.wireOp",EDGE,"E2322"),sQuery(id+"F6.wireOp",EDGE,"E2323"),sQuery(id+"F6.wireOp",EDGE,"E2324"),sQuery(id+"F6.wireOp",EDGE,"E2325"),sQuery(id+"F6.wireOp",EDGE,"E2326"),sQuery(id+"F6.wireOp",EDGE,"E2327"),sQuery(id+"F6.wireOp",EDGE,"E2328"),sQuery(id+"F6.wireOp",EDGE,"E2329"),sQuery(id+"F6.wireOp",EDGE,"E2330"),sQuery(id+"F6.wireOp",EDGE,"E2331"),sQuery(id+"F6.wireOp",EDGE,"E2332"),sQuery(id+"F6.wireOp",EDGE,"E2333"),sQuery(id+"F6.wireOp",EDGE,"E2334"),sQuery(id+"F6.wireOp",EDGE,"E2335"),sQuery(id+"F6.wireOp",EDGE,"E2336"),sQuery(id+"F6.wireOp",EDGE,"E2337"),sQuery(id+"F6.wireOp",EDGE,"E2338"),sQuery(id+"F6.wireOp",EDGE,"E2339"),sQuery(id+"F6.wireOp",EDGE,"E2340"),sQuery(id+"F6.wireOp",EDGE,"E2341"),sQuery(id+"F6.wireOp",EDGE,"E2342"),sQuery(id+"F6.wireOp",EDGE,"E2343"),sQuery(id+"F6.wireOp",EDGE,"E2344"),sQuery(id+"F6.wireOp",EDGE,"E2345"),sQuery(id+"F6.wireOp",EDGE,"E2346"),sQuery(id+"F6.wireOp",EDGE,"E2347"),sQuery(id+"F6.wireOp",EDGE,"E2348"),sQuery(id+"F6.wireOp",EDGE,"E2349"),sQuery(id+"F6.wireOp",EDGE,"E2350"),sQuery(id+"F6.wireOp",EDGE,"E2351"),sQuery(id+"F6.wireOp",EDGE,"E2352"),sQuery(id+"F6.wireOp",EDGE,"E2353"),sQuery(id+"F6.wireOp",EDGE,"E2354"),sQuery(id+"F6.wireOp",EDGE,"E2355"),sQuery(id+"F6.wireOp",EDGE,"E2356"),sQuery(id+"F6.wireOp",EDGE,"E2357"),sQuery(id+"F6.wireOp",EDGE,"E2358"),sQuery(id+"F6.wireOp",EDGE,"E2359"),sQuery(id+"F6.wireOp",EDGE,"E2360"),sQuery(id+"F6.wireOp",EDGE,"E2361"),sQuery(id+"F6.wireOp",EDGE,"E2362"),sQuery(id+"F6.wireOp",EDGE,"E2363"),sQuery(id+"F6.wireOp",EDGE,"E2364"),sQuery(id+"F6.wireOp",EDGE,"E2365"),sQuery(id+"F6.wireOp",EDGE,"E2366"),sQuery(id+"F6.wireOp",EDGE,"E2367"),sQuery(id+"F6.wireOp",EDGE,"E2368"),sQuery(id+"F6.wireOp",EDGE,"E2369"),sQuery(id+"F6.wireOp",EDGE,"E2370"),sQuery(id+"F6.wireOp",EDGE,"E2371"),sQuery(id+"F6.wireOp",EDGE,"E2372"),sQuery(id+"F6.wireOp",EDGE,"E2373"),sQuery(id+"F6.wireOp",EDGE,"E2374"),sQuery(id+"F6.wireOp",EDGE,"E2375"),sQuery(id+"F6.wireOp",EDGE,"E2376"),sQuery(id+"F6.wireOp",EDGE,"E2377"),sQuery(id+"F6.wireOp",EDGE,"E2378"),sQuery(id+"F6.wireOp",EDGE,"E2379"),sQuery(id+"F6.wireOp",EDGE,"E2380"),sQuery(id+"F6.wireOp",EDGE,"E2381"),sQuery(id+"F6.wireOp",EDGE,"E2382"),sQuery(id+"F6.wireOp",EDGE,"E2383"),sQuery(id+"F6.wireOp",EDGE,"E2384"),sQuery(id+"F6.wireOp",EDGE,"E2385"),sQuery(id+"F6.wireOp",EDGE,"E2386"),sQuery(id+"F6.wireOp",EDGE,"E2387"),sQuery(id+"F6.wireOp",EDGE,"E2388"),sQuery(id+"F6.wireOp",EDGE,"E2389"),sQuery(id+"F6.wireOp",EDGE,"E2390"),sQuery(id+"F6.wireOp",EDGE,"E2391"),sQuery(id+"F6.wireOp",EDGE,"E2392"),sQuery(id+"F6.wireOp",EDGE,"E2393"),sQuery(id+"F6.wireOp",EDGE,"E2394"),sQuery(id+"F6.wireOp",EDGE,"E2395"),sQuery(id+"F6.wireOp",EDGE,"E2396"),sQuery(id+"F6.wireOp",EDGE,"E2397"),sQuery(id+"F6.wireOp",EDGE,"E2398"),sQuery(id+"F6.wireOp",EDGE,"E2399"),sQuery(id+"F6.wireOp",EDGE,"E2400"),sQuery(id+"F6.wireOp",EDGE,"E2401"),sQuery(id+"F6.wireOp",EDGE,"E2402"),sQuery(id+"F6.wireOp",EDGE,"E2403"),sQuery(id+"F6.wireOp",EDGE,"E2404"),sQuery(id+"F6.wireOp",EDGE,"E2405"),sQuery(id+"F6.wireOp",EDGE,"E2406"),sQuery(id+"F6.wireOp",EDGE,"E2407"),sQuery(id+"F6.wireOp",EDGE,"E2408"),sQuery(id+"F6.wireOp",EDGE,"E2409"),sQuery(id+"F6.wireOp",EDGE,"E2410"),sQuery(id+"F6.wireOp",EDGE,"E2411"),sQuery(id+"F6.wireOp",EDGE,"E2412"),sQuery(id+"F6.wireOp",EDGE,"E2413"),sQuery(id+"F6.wireOp",EDGE,"E2414"),sQuery(id+"F6.wireOp",EDGE,"E2415"),sQuery(id+"F6.wireOp",EDGE,"E2416"),sQuery(id+"F6.wireOp",EDGE,"E2417"),sQuery(id+"F6.wireOp",EDGE,"E2418"),sQuery(id+"F6.wireOp",EDGE,"E2419"),sQuery(id+"F6.wireOp",EDGE,"E2420"),sQuery(id+"F6.wireOp",EDGE,"E2421"),sQuery(id+"F6.wireOp",EDGE,"E2422"),sQuery(id+"F6.wireOp",EDGE,"E2423"),sQuery(id+"F6.wireOp",EDGE,"E2424"),sQuery(id+"F6.wireOp",EDGE,"E2425"),sQuery(id+"F6.wireOp",EDGE,"E2426"),sQuery(id+"F6.wireOp",EDGE,"E2427"),sQuery(id+"F6.wireOp",EDGE,"E2428"),sQuery(id+"F6.wireOp",EDGE,"E2429"),sQuery(id+"F6.wireOp",EDGE,"E2430"),sQuery(id+"F6.wireOp",EDGE,"E2431"),sQuery(id+"F6.wireOp",EDGE,"E2432"),sQuery(id+"F6.wireOp",EDGE,"E2433"),sQuery(id+"F6.wireOp",EDGE,"E2434"),sQuery(id+"F6.wireOp",EDGE,"E2435")])]});
            var Q1;
            Q1=sQuery(id+"F4.wireOp",EDGE,"E36");
            transform(context, id + "F10", {"entities" : qUnion([Q0]), "transformType" : TransformType.ROTATION, "transformAxis" : qUnion([Q1]), "angle" : 60 * degree, "makeCopy" : true});
        }
        {
            var Q0;
            Q0=makeQuery(id+"F7.opExtrude","SWEPT_BODY",BODY,{"disambiguationData":[OSD([sQuery(id+"F6.wireOp",EDGE,"E37"),sQuery(id+"F6.wireOp",EDGE,"E38"),sQuery(id+"F6.wireOp",EDGE,"E39"),sQuery(id+"F6.wireOp",EDGE,"E40"),sQuery(id+"F6.wireOp",EDGE,"E41"),sQuery(id+"F6.wireOp",EDGE,"E42"),sQuery(id+"F6.wireOp",EDGE,"E43"),sQuery(id+"F6.wireOp",EDGE,"E44"),sQuery(id+"F6.wireOp",EDGE,"E45"),sQuery(id+"F6.wireOp",EDGE,"E46"),sQuery(id+"F6.wireOp",EDGE,"E47"),sQuery(id+"F6.wireOp",EDGE,"E48"),sQuery(id+"F6.wireOp",EDGE,"E49"),sQuery(id+"F6.wireOp",EDGE,"E50"),sQuery(id+"F6.wireOp",EDGE,"E51"),sQuery(id+"F6.wireOp",EDGE,"E52"),sQuery(id+"F6.wireOp",EDGE,"E53"),sQuery(id+"F6.wireOp",EDGE,"E54"),sQuery(id+"F6.wireOp",EDGE,"E55"),sQuery(id+"F6.wireOp",EDGE,"E56"),sQuery(id+"F6.wireOp",EDGE,"E57"),sQuery(id+"F6.wireOp",EDGE,"E58"),sQuery(id+"F6.wireOp",EDGE,"E59"),sQuery(id+"F6.wireOp",EDGE,"E60"),sQuery(id+"F6.wireOp",EDGE,"E61"),sQuery(id+"F6.wireOp",EDGE,"E62"),sQuery(id+"F6.wireOp",EDGE,"E63"),sQuery(id+"F6.wireOp",EDGE,"E64"),sQuery(id+"F6.wireOp",EDGE,"E65"),sQuery(id+"F6.wireOp",EDGE,"E66"),sQuery(id+"F6.wireOp",EDGE,"E67"),sQuery(id+"F6.wireOp",EDGE,"E68"),sQuery(id+"F6.wireOp",EDGE,"E69"),sQuery(id+"F6.wireOp",EDGE,"E70"),sQuery(id+"F6.wireOp",EDGE,"E71"),sQuery(id+"F6.wireOp",EDGE,"E72"),sQuery(id+"F6.wireOp",EDGE,"E73"),sQuery(id+"F6.wireOp",EDGE,"E74"),sQuery(id+"F6.wireOp",EDGE,"E75"),sQuery(id+"F6.wireOp",EDGE,"E76"),sQuery(id+"F6.wireOp",EDGE,"E77"),sQuery(id+"F6.wireOp",EDGE,"E78"),sQuery(id+"F6.wireOp",EDGE,"E79"),sQuery(id+"F6.wireOp",EDGE,"E80"),sQuery(id+"F6.wireOp",EDGE,"E81"),sQuery(id+"F6.wireOp",EDGE,"E82"),sQuery(id+"F6.wireOp",EDGE,"E83"),sQuery(id+"F6.wireOp",EDGE,"E84"),sQuery(id+"F6.wireOp",EDGE,"E85"),sQuery(id+"F6.wireOp",EDGE,"E86"),sQuery(id+"F6.wireOp",EDGE,"E87"),sQuery(id+"F6.wireOp",EDGE,"E88"),sQuery(id+"F6.wireOp",EDGE,"E89"),sQuery(id+"F6.wireOp",EDGE,"E90"),sQuery(id+"F6.wireOp",EDGE,"E91"),sQuery(id+"F6.wireOp",EDGE,"E92"),sQuery(id+"F6.wireOp",EDGE,"E93"),sQuery(id+"F6.wireOp",EDGE,"E94"),sQuery(id+"F6.wireOp",EDGE,"E95"),sQuery(id+"F6.wireOp",EDGE,"E96"),sQuery(id+"F6.wireOp",EDGE,"E97"),sQuery(id+"F6.wireOp",EDGE,"E98"),sQuery(id+"F6.wireOp",EDGE,"E99"),sQuery(id+"F6.wireOp",EDGE,"E100"),sQuery(id+"F6.wireOp",EDGE,"E101"),sQuery(id+"F6.wireOp",EDGE,"E102"),sQuery(id+"F6.wireOp",EDGE,"E103"),sQuery(id+"F6.wireOp",EDGE,"E104"),sQuery(id+"F6.wireOp",EDGE,"E105"),sQuery(id+"F6.wireOp",EDGE,"E106"),sQuery(id+"F6.wireOp",EDGE,"E107"),sQuery(id+"F6.wireOp",EDGE,"E108"),sQuery(id+"F6.wireOp",EDGE,"E109"),sQuery(id+"F6.wireOp",EDGE,"E110"),sQuery(id+"F6.wireOp",EDGE,"E111"),sQuery(id+"F6.wireOp",EDGE,"E112"),sQuery(id+"F6.wireOp",EDGE,"E113"),sQuery(id+"F6.wireOp",EDGE,"E114"),sQuery(id+"F6.wireOp",EDGE,"E115"),sQuery(id+"F6.wireOp",EDGE,"E116"),sQuery(id+"F6.wireOp",EDGE,"E117"),sQuery(id+"F6.wireOp",EDGE,"E118"),sQuery(id+"F6.wireOp",EDGE,"E119"),sQuery(id+"F6.wireOp",EDGE,"E120"),sQuery(id+"F6.wireOp",EDGE,"E121"),sQuery(id+"F6.wireOp",EDGE,"E122"),sQuery(id+"F6.wireOp",EDGE,"E123"),sQuery(id+"F6.wireOp",EDGE,"E124"),sQuery(id+"F6.wireOp",EDGE,"E125"),sQuery(id+"F6.wireOp",EDGE,"E126"),sQuery(id+"F6.wireOp",EDGE,"E127"),sQuery(id+"F6.wireOp",EDGE,"E128"),sQuery(id+"F6.wireOp",EDGE,"E129"),sQuery(id+"F6.wireOp",EDGE,"E130"),sQuery(id+"F6.wireOp",EDGE,"E131"),sQuery(id+"F6.wireOp",EDGE,"E132"),sQuery(id+"F6.wireOp",EDGE,"E133"),sQuery(id+"F6.wireOp",EDGE,"E134"),sQuery(id+"F6.wireOp",EDGE,"E135"),sQuery(id+"F6.wireOp",EDGE,"E136"),sQuery(id+"F6.wireOp",EDGE,"E137"),sQuery(id+"F6.wireOp",EDGE,"E138"),sQuery(id+"F6.wireOp",EDGE,"E139"),sQuery(id+"F6.wireOp",EDGE,"E140"),sQuery(id+"F6.wireOp",EDGE,"E141"),sQuery(id+"F6.wireOp",EDGE,"E142"),sQuery(id+"F6.wireOp",EDGE,"E143"),sQuery(id+"F6.wireOp",EDGE,"E144"),sQuery(id+"F6.wireOp",EDGE,"E145"),sQuery(id+"F6.wireOp",EDGE,"E146"),sQuery(id+"F6.wireOp",EDGE,"E147"),sQuery(id+"F6.wireOp",EDGE,"E148"),sQuery(id+"F6.wireOp",EDGE,"E149"),sQuery(id+"F6.wireOp",EDGE,"E150"),sQuery(id+"F6.wireOp",EDGE,"E151"),sQuery(id+"F6.wireOp",EDGE,"E152"),sQuery(id+"F6.wireOp",EDGE,"E153"),sQuery(id+"F6.wireOp",EDGE,"E154"),sQuery(id+"F6.wireOp",EDGE,"E155"),sQuery(id+"F6.wireOp",EDGE,"E156"),sQuery(id+"F6.wireOp",EDGE,"E157"),sQuery(id+"F6.wireOp",EDGE,"E158"),sQuery(id+"F6.wireOp",EDGE,"E159"),sQuery(id+"F6.wireOp",EDGE,"E160"),sQuery(id+"F6.wireOp",EDGE,"E161"),sQuery(id+"F6.wireOp",EDGE,"E162"),sQuery(id+"F6.wireOp",EDGE,"E163"),sQuery(id+"F6.wireOp",EDGE,"E164"),sQuery(id+"F6.wireOp",EDGE,"E165"),sQuery(id+"F6.wireOp",EDGE,"E166"),sQuery(id+"F6.wireOp",EDGE,"E167"),sQuery(id+"F6.wireOp",EDGE,"E168"),sQuery(id+"F6.wireOp",EDGE,"E169"),sQuery(id+"F6.wireOp",EDGE,"E170"),sQuery(id+"F6.wireOp",EDGE,"E171"),sQuery(id+"F6.wireOp",EDGE,"E172"),sQuery(id+"F6.wireOp",EDGE,"E173"),sQuery(id+"F6.wireOp",EDGE,"E174"),sQuery(id+"F6.wireOp",EDGE,"E175"),sQuery(id+"F6.wireOp",EDGE,"E176"),sQuery(id+"F6.wireOp",EDGE,"E177"),sQuery(id+"F6.wireOp",EDGE,"E178"),sQuery(id+"F6.wireOp",EDGE,"E179"),sQuery(id+"F6.wireOp",EDGE,"E180"),sQuery(id+"F6.wireOp",EDGE,"E181"),sQuery(id+"F6.wireOp",EDGE,"E182"),sQuery(id+"F6.wireOp",EDGE,"E183"),sQuery(id+"F6.wireOp",EDGE,"E184"),sQuery(id+"F6.wireOp",EDGE,"E185"),sQuery(id+"F6.wireOp",EDGE,"E186"),sQuery(id+"F6.wireOp",EDGE,"E187"),sQuery(id+"F6.wireOp",EDGE,"E188"),sQuery(id+"F6.wireOp",EDGE,"E189"),sQuery(id+"F6.wireOp",EDGE,"E190"),sQuery(id+"F6.wireOp",EDGE,"E191"),sQuery(id+"F6.wireOp",EDGE,"E192"),sQuery(id+"F6.wireOp",EDGE,"E193"),sQuery(id+"F6.wireOp",EDGE,"E194"),sQuery(id+"F6.wireOp",EDGE,"E195"),sQuery(id+"F6.wireOp",EDGE,"E196"),sQuery(id+"F6.wireOp",EDGE,"E197"),sQuery(id+"F6.wireOp",EDGE,"E198"),sQuery(id+"F6.wireOp",EDGE,"E199"),sQuery(id+"F6.wireOp",EDGE,"E200"),sQuery(id+"F6.wireOp",EDGE,"E201"),sQuery(id+"F6.wireOp",EDGE,"E202"),sQuery(id+"F6.wireOp",EDGE,"E203"),sQuery(id+"F6.wireOp",EDGE,"E204"),sQuery(id+"F6.wireOp",EDGE,"E205"),sQuery(id+"F6.wireOp",EDGE,"E206"),sQuery(id+"F6.wireOp",EDGE,"E207"),sQuery(id+"F6.wireOp",EDGE,"E208"),sQuery(id+"F6.wireOp",EDGE,"E209"),sQuery(id+"F6.wireOp",EDGE,"E210"),sQuery(id+"F6.wireOp",EDGE,"E211"),sQuery(id+"F6.wireOp",EDGE,"E212"),sQuery(id+"F6.wireOp",EDGE,"E213"),sQuery(id+"F6.wireOp",EDGE,"E214"),sQuery(id+"F6.wireOp",EDGE,"E215"),sQuery(id+"F6.wireOp",EDGE,"E216"),sQuery(id+"F6.wireOp",EDGE,"E217"),sQuery(id+"F6.wireOp",EDGE,"E218"),sQuery(id+"F6.wireOp",EDGE,"E219"),sQuery(id+"F6.wireOp",EDGE,"E220"),sQuery(id+"F6.wireOp",EDGE,"E221"),sQuery(id+"F6.wireOp",EDGE,"E222"),sQuery(id+"F6.wireOp",EDGE,"E223"),sQuery(id+"F6.wireOp",EDGE,"E224"),sQuery(id+"F6.wireOp",EDGE,"E225"),sQuery(id+"F6.wireOp",EDGE,"E226"),sQuery(id+"F6.wireOp",EDGE,"E227"),sQuery(id+"F6.wireOp",EDGE,"E228"),sQuery(id+"F6.wireOp",EDGE,"E229"),sQuery(id+"F6.wireOp",EDGE,"E230"),sQuery(id+"F6.wireOp",EDGE,"E231"),sQuery(id+"F6.wireOp",EDGE,"E232"),sQuery(id+"F6.wireOp",EDGE,"E233"),sQuery(id+"F6.wireOp",EDGE,"E234"),sQuery(id+"F6.wireOp",EDGE,"E235"),sQuery(id+"F6.wireOp",EDGE,"E236"),sQuery(id+"F6.wireOp",EDGE,"E237"),sQuery(id+"F6.wireOp",EDGE,"E238"),sQuery(id+"F6.wireOp",EDGE,"E239"),sQuery(id+"F6.wireOp",EDGE,"E240"),sQuery(id+"F6.wireOp",EDGE,"E241"),sQuery(id+"F6.wireOp",EDGE,"E242"),sQuery(id+"F6.wireOp",EDGE,"E243"),sQuery(id+"F6.wireOp",EDGE,"E244"),sQuery(id+"F6.wireOp",EDGE,"E245"),sQuery(id+"F6.wireOp",EDGE,"E246"),sQuery(id+"F6.wireOp",EDGE,"E247"),sQuery(id+"F6.wireOp",EDGE,"E248"),sQuery(id+"F6.wireOp",EDGE,"E249"),sQuery(id+"F6.wireOp",EDGE,"E250"),sQuery(id+"F6.wireOp",EDGE,"E251"),sQuery(id+"F6.wireOp",EDGE,"E252"),sQuery(id+"F6.wireOp",EDGE,"E253"),sQuery(id+"F6.wireOp",EDGE,"E254"),sQuery(id+"F6.wireOp",EDGE,"E255"),sQuery(id+"F6.wireOp",EDGE,"E256"),sQuery(id+"F6.wireOp",EDGE,"E257"),sQuery(id+"F6.wireOp",EDGE,"E258"),sQuery(id+"F6.wireOp",EDGE,"E259"),sQuery(id+"F6.wireOp",EDGE,"E260"),sQuery(id+"F6.wireOp",EDGE,"E261"),sQuery(id+"F6.wireOp",EDGE,"E262"),sQuery(id+"F6.wireOp",EDGE,"E263"),sQuery(id+"F6.wireOp",EDGE,"E264"),sQuery(id+"F6.wireOp",EDGE,"E265"),sQuery(id+"F6.wireOp",EDGE,"E266"),sQuery(id+"F6.wireOp",EDGE,"E267"),sQuery(id+"F6.wireOp",EDGE,"E268"),sQuery(id+"F6.wireOp",EDGE,"E269"),sQuery(id+"F6.wireOp",EDGE,"E270"),sQuery(id+"F6.wireOp",EDGE,"E271"),sQuery(id+"F6.wireOp",EDGE,"E272"),sQuery(id+"F6.wireOp",EDGE,"E273"),sQuery(id+"F6.wireOp",EDGE,"E274"),sQuery(id+"F6.wireOp",EDGE,"E275"),sQuery(id+"F6.wireOp",EDGE,"E276"),sQuery(id+"F6.wireOp",EDGE,"E277"),sQuery(id+"F6.wireOp",EDGE,"E278"),sQuery(id+"F6.wireOp",EDGE,"E279"),sQuery(id+"F6.wireOp",EDGE,"E280"),sQuery(id+"F6.wireOp",EDGE,"E281"),sQuery(id+"F6.wireOp",EDGE,"E282"),sQuery(id+"F6.wireOp",EDGE,"E283"),sQuery(id+"F6.wireOp",EDGE,"E284"),sQuery(id+"F6.wireOp",EDGE,"E285"),sQuery(id+"F6.wireOp",EDGE,"E286"),sQuery(id+"F6.wireOp",EDGE,"E287"),sQuery(id+"F6.wireOp",EDGE,"E288"),sQuery(id+"F6.wireOp",EDGE,"E289"),sQuery(id+"F6.wireOp",EDGE,"E290"),sQuery(id+"F6.wireOp",EDGE,"E291"),sQuery(id+"F6.wireOp",EDGE,"E292"),sQuery(id+"F6.wireOp",EDGE,"E293"),sQuery(id+"F6.wireOp",EDGE,"E294"),sQuery(id+"F6.wireOp",EDGE,"E295"),sQuery(id+"F6.wireOp",EDGE,"E296"),sQuery(id+"F6.wireOp",EDGE,"E297"),sQuery(id+"F6.wireOp",EDGE,"E298"),sQuery(id+"F6.wireOp",EDGE,"E299"),sQuery(id+"F6.wireOp",EDGE,"E300"),sQuery(id+"F6.wireOp",EDGE,"E301"),sQuery(id+"F6.wireOp",EDGE,"E302"),sQuery(id+"F6.wireOp",EDGE,"E303"),sQuery(id+"F6.wireOp",EDGE,"E304"),sQuery(id+"F6.wireOp",EDGE,"E305"),sQuery(id+"F6.wireOp",EDGE,"E306"),sQuery(id+"F6.wireOp",EDGE,"E307"),sQuery(id+"F6.wireOp",EDGE,"E308"),sQuery(id+"F6.wireOp",EDGE,"E309"),sQuery(id+"F6.wireOp",EDGE,"E310"),sQuery(id+"F6.wireOp",EDGE,"E311"),sQuery(id+"F6.wireOp",EDGE,"E312"),sQuery(id+"F6.wireOp",EDGE,"E313"),sQuery(id+"F6.wireOp",EDGE,"E314"),sQuery(id+"F6.wireOp",EDGE,"E315"),sQuery(id+"F6.wireOp",EDGE,"E316"),sQuery(id+"F6.wireOp",EDGE,"E317"),sQuery(id+"F6.wireOp",EDGE,"E318"),sQuery(id+"F6.wireOp",EDGE,"E319"),sQuery(id+"F6.wireOp",EDGE,"E320"),sQuery(id+"F6.wireOp",EDGE,"E321"),sQuery(id+"F6.wireOp",EDGE,"E322"),sQuery(id+"F6.wireOp",EDGE,"E323"),sQuery(id+"F6.wireOp",EDGE,"E324"),sQuery(id+"F6.wireOp",EDGE,"E325"),sQuery(id+"F6.wireOp",EDGE,"E326"),sQuery(id+"F6.wireOp",EDGE,"E327"),sQuery(id+"F6.wireOp",EDGE,"E328"),sQuery(id+"F6.wireOp",EDGE,"E329"),sQuery(id+"F6.wireOp",EDGE,"E330"),sQuery(id+"F6.wireOp",EDGE,"E331"),sQuery(id+"F6.wireOp",EDGE,"E332"),sQuery(id+"F6.wireOp",EDGE,"E333"),sQuery(id+"F6.wireOp",EDGE,"E334"),sQuery(id+"F6.wireOp",EDGE,"E335"),sQuery(id+"F6.wireOp",EDGE,"E336"),sQuery(id+"F6.wireOp",EDGE,"E337"),sQuery(id+"F6.wireOp",EDGE,"E338"),sQuery(id+"F6.wireOp",EDGE,"E339"),sQuery(id+"F6.wireOp",EDGE,"E340"),sQuery(id+"F6.wireOp",EDGE,"E341"),sQuery(id+"F6.wireOp",EDGE,"E342"),sQuery(id+"F6.wireOp",EDGE,"E343"),sQuery(id+"F6.wireOp",EDGE,"E344"),sQuery(id+"F6.wireOp",EDGE,"E345"),sQuery(id+"F6.wireOp",EDGE,"E346"),sQuery(id+"F6.wireOp",EDGE,"E347"),sQuery(id+"F6.wireOp",EDGE,"E348"),sQuery(id+"F6.wireOp",EDGE,"E349"),sQuery(id+"F6.wireOp",EDGE,"E350"),sQuery(id+"F6.wireOp",EDGE,"E351"),sQuery(id+"F6.wireOp",EDGE,"E352"),sQuery(id+"F6.wireOp",EDGE,"E353"),sQuery(id+"F6.wireOp",EDGE,"E354"),sQuery(id+"F6.wireOp",EDGE,"E355"),sQuery(id+"F6.wireOp",EDGE,"E356"),sQuery(id+"F6.wireOp",EDGE,"E357"),sQuery(id+"F6.wireOp",EDGE,"E358"),sQuery(id+"F6.wireOp",EDGE,"E359"),sQuery(id+"F6.wireOp",EDGE,"E360"),sQuery(id+"F6.wireOp",EDGE,"E361"),sQuery(id+"F6.wireOp",EDGE,"E362"),sQuery(id+"F6.wireOp",EDGE,"E363"),sQuery(id+"F6.wireOp",EDGE,"E364"),sQuery(id+"F6.wireOp",EDGE,"E365"),sQuery(id+"F6.wireOp",EDGE,"E366"),sQuery(id+"F6.wireOp",EDGE,"E367"),sQuery(id+"F6.wireOp",EDGE,"E368"),sQuery(id+"F6.wireOp",EDGE,"E369"),sQuery(id+"F6.wireOp",EDGE,"E370"),sQuery(id+"F6.wireOp",EDGE,"E371"),sQuery(id+"F6.wireOp",EDGE,"E372"),sQuery(id+"F6.wireOp",EDGE,"E373"),sQuery(id+"F6.wireOp",EDGE,"E374"),sQuery(id+"F6.wireOp",EDGE,"E375"),sQuery(id+"F6.wireOp",EDGE,"E376"),sQuery(id+"F6.wireOp",EDGE,"E377"),sQuery(id+"F6.wireOp",EDGE,"E378"),sQuery(id+"F6.wireOp",EDGE,"E379"),sQuery(id+"F6.wireOp",EDGE,"E380"),sQuery(id+"F6.wireOp",EDGE,"E381"),sQuery(id+"F6.wireOp",EDGE,"E382"),sQuery(id+"F6.wireOp",EDGE,"E383"),sQuery(id+"F6.wireOp",EDGE,"E384"),sQuery(id+"F6.wireOp",EDGE,"E385"),sQuery(id+"F6.wireOp",EDGE,"E386"),sQuery(id+"F6.wireOp",EDGE,"E387"),sQuery(id+"F6.wireOp",EDGE,"E388"),sQuery(id+"F6.wireOp",EDGE,"E389"),sQuery(id+"F6.wireOp",EDGE,"E390"),sQuery(id+"F6.wireOp",EDGE,"E391"),sQuery(id+"F6.wireOp",EDGE,"E392"),sQuery(id+"F6.wireOp",EDGE,"E393"),sQuery(id+"F6.wireOp",EDGE,"E394"),sQuery(id+"F6.wireOp",EDGE,"E395"),sQuery(id+"F6.wireOp",EDGE,"E396"),sQuery(id+"F6.wireOp",EDGE,"E397"),sQuery(id+"F6.wireOp",EDGE,"E398"),sQuery(id+"F6.wireOp",EDGE,"E399"),sQuery(id+"F6.wireOp",EDGE,"E400"),sQuery(id+"F6.wireOp",EDGE,"E401"),sQuery(id+"F6.wireOp",EDGE,"E402"),sQuery(id+"F6.wireOp",EDGE,"E403"),sQuery(id+"F6.wireOp",EDGE,"E404"),sQuery(id+"F6.wireOp",EDGE,"E405"),sQuery(id+"F6.wireOp",EDGE,"E406"),sQuery(id+"F6.wireOp",EDGE,"E407"),sQuery(id+"F6.wireOp",EDGE,"E408"),sQuery(id+"F6.wireOp",EDGE,"E409"),sQuery(id+"F6.wireOp",EDGE,"E410"),sQuery(id+"F6.wireOp",EDGE,"E411"),sQuery(id+"F6.wireOp",EDGE,"E412"),sQuery(id+"F6.wireOp",EDGE,"E413"),sQuery(id+"F6.wireOp",EDGE,"E414"),sQuery(id+"F6.wireOp",EDGE,"E415"),sQuery(id+"F6.wireOp",EDGE,"E416"),sQuery(id+"F6.wireOp",EDGE,"E417"),sQuery(id+"F6.wireOp",EDGE,"E418"),sQuery(id+"F6.wireOp",EDGE,"E419"),sQuery(id+"F6.wireOp",EDGE,"E420"),sQuery(id+"F6.wireOp",EDGE,"E421"),sQuery(id+"F6.wireOp",EDGE,"E422"),sQuery(id+"F6.wireOp",EDGE,"E423"),sQuery(id+"F6.wireOp",EDGE,"E424"),sQuery(id+"F6.wireOp",EDGE,"E425"),sQuery(id+"F6.wireOp",EDGE,"E426"),sQuery(id+"F6.wireOp",EDGE,"E427"),sQuery(id+"F6.wireOp",EDGE,"E428"),sQuery(id+"F6.wireOp",EDGE,"E429"),sQuery(id+"F6.wireOp",EDGE,"E430"),sQuery(id+"F6.wireOp",EDGE,"E431"),sQuery(id+"F6.wireOp",EDGE,"E432"),sQuery(id+"F6.wireOp",EDGE,"E433"),sQuery(id+"F6.wireOp",EDGE,"E434"),sQuery(id+"F6.wireOp",EDGE,"E435"),sQuery(id+"F6.wireOp",EDGE,"E436"),sQuery(id+"F6.wireOp",EDGE,"E437"),sQuery(id+"F6.wireOp",EDGE,"E438"),sQuery(id+"F6.wireOp",EDGE,"E439"),sQuery(id+"F6.wireOp",EDGE,"E440"),sQuery(id+"F6.wireOp",EDGE,"E441"),sQuery(id+"F6.wireOp",EDGE,"E442"),sQuery(id+"F6.wireOp",EDGE,"E443"),sQuery(id+"F6.wireOp",EDGE,"E444"),sQuery(id+"F6.wireOp",EDGE,"E445"),sQuery(id+"F6.wireOp",EDGE,"E446"),sQuery(id+"F6.wireOp",EDGE,"E447"),sQuery(id+"F6.wireOp",EDGE,"E448"),sQuery(id+"F6.wireOp",EDGE,"E449"),sQuery(id+"F6.wireOp",EDGE,"E450"),sQuery(id+"F6.wireOp",EDGE,"E451"),sQuery(id+"F6.wireOp",EDGE,"E452"),sQuery(id+"F6.wireOp",EDGE,"E453"),sQuery(id+"F6.wireOp",EDGE,"E454"),sQuery(id+"F6.wireOp",EDGE,"E455"),sQuery(id+"F6.wireOp",EDGE,"E456"),sQuery(id+"F6.wireOp",EDGE,"E457"),sQuery(id+"F6.wireOp",EDGE,"E458"),sQuery(id+"F6.wireOp",EDGE,"E459"),sQuery(id+"F6.wireOp",EDGE,"E460"),sQuery(id+"F6.wireOp",EDGE,"E461"),sQuery(id+"F6.wireOp",EDGE,"E462"),sQuery(id+"F6.wireOp",EDGE,"E463"),sQuery(id+"F6.wireOp",EDGE,"E464"),sQuery(id+"F6.wireOp",EDGE,"E465"),sQuery(id+"F6.wireOp",EDGE,"E466"),sQuery(id+"F6.wireOp",EDGE,"E467"),sQuery(id+"F6.wireOp",EDGE,"E468"),sQuery(id+"F6.wireOp",EDGE,"E469"),sQuery(id+"F6.wireOp",EDGE,"E470"),sQuery(id+"F6.wireOp",EDGE,"E471"),sQuery(id+"F6.wireOp",EDGE,"E472"),sQuery(id+"F6.wireOp",EDGE,"E473"),sQuery(id+"F6.wireOp",EDGE,"E474"),sQuery(id+"F6.wireOp",EDGE,"E475"),sQuery(id+"F6.wireOp",EDGE,"E476"),sQuery(id+"F6.wireOp",EDGE,"E477"),sQuery(id+"F6.wireOp",EDGE,"E478"),sQuery(id+"F6.wireOp",EDGE,"E479"),sQuery(id+"F6.wireOp",EDGE,"E480"),sQuery(id+"F6.wireOp",EDGE,"E481"),sQuery(id+"F6.wireOp",EDGE,"E482"),sQuery(id+"F6.wireOp",EDGE,"E483"),sQuery(id+"F6.wireOp",EDGE,"E484"),sQuery(id+"F6.wireOp",EDGE,"E485"),sQuery(id+"F6.wireOp",EDGE,"E486"),sQuery(id+"F6.wireOp",EDGE,"E487"),sQuery(id+"F6.wireOp",EDGE,"E488"),sQuery(id+"F6.wireOp",EDGE,"E489"),sQuery(id+"F6.wireOp",EDGE,"E490"),sQuery(id+"F6.wireOp",EDGE,"E491"),sQuery(id+"F6.wireOp",EDGE,"E492"),sQuery(id+"F6.wireOp",EDGE,"E493"),sQuery(id+"F6.wireOp",EDGE,"E494"),sQuery(id+"F6.wireOp",EDGE,"E495"),sQuery(id+"F6.wireOp",EDGE,"E496"),sQuery(id+"F6.wireOp",EDGE,"E497"),sQuery(id+"F6.wireOp",EDGE,"E498"),sQuery(id+"F6.wireOp",EDGE,"E499"),sQuery(id+"F6.wireOp",EDGE,"E500"),sQuery(id+"F6.wireOp",EDGE,"E501"),sQuery(id+"F6.wireOp",EDGE,"E502"),sQuery(id+"F6.wireOp",EDGE,"E503"),sQuery(id+"F6.wireOp",EDGE,"E504"),sQuery(id+"F6.wireOp",EDGE,"E505"),sQuery(id+"F6.wireOp",EDGE,"E506"),sQuery(id+"F6.wireOp",EDGE,"E507"),sQuery(id+"F6.wireOp",EDGE,"E508"),sQuery(id+"F6.wireOp",EDGE,"E509"),sQuery(id+"F6.wireOp",EDGE,"E510"),sQuery(id+"F6.wireOp",EDGE,"E511"),sQuery(id+"F6.wireOp",EDGE,"E512"),sQuery(id+"F6.wireOp",EDGE,"E513"),sQuery(id+"F6.wireOp",EDGE,"E514"),sQuery(id+"F6.wireOp",EDGE,"E515"),sQuery(id+"F6.wireOp",EDGE,"E516"),sQuery(id+"F6.wireOp",EDGE,"E517"),sQuery(id+"F6.wireOp",EDGE,"E518"),sQuery(id+"F6.wireOp",EDGE,"E519"),sQuery(id+"F6.wireOp",EDGE,"E520"),sQuery(id+"F6.wireOp",EDGE,"E521"),sQuery(id+"F6.wireOp",EDGE,"E522"),sQuery(id+"F6.wireOp",EDGE,"E523"),sQuery(id+"F6.wireOp",EDGE,"E524"),sQuery(id+"F6.wireOp",EDGE,"E525"),sQuery(id+"F6.wireOp",EDGE,"E526"),sQuery(id+"F6.wireOp",EDGE,"E527"),sQuery(id+"F6.wireOp",EDGE,"E528"),sQuery(id+"F6.wireOp",EDGE,"E529"),sQuery(id+"F6.wireOp",EDGE,"E530"),sQuery(id+"F6.wireOp",EDGE,"E531"),sQuery(id+"F6.wireOp",EDGE,"E532"),sQuery(id+"F6.wireOp",EDGE,"E533"),sQuery(id+"F6.wireOp",EDGE,"E534"),sQuery(id+"F6.wireOp",EDGE,"E535"),sQuery(id+"F6.wireOp",EDGE,"E536"),sQuery(id+"F6.wireOp",EDGE,"E537"),sQuery(id+"F6.wireOp",EDGE,"E538"),sQuery(id+"F6.wireOp",EDGE,"E539"),sQuery(id+"F6.wireOp",EDGE,"E540"),sQuery(id+"F6.wireOp",EDGE,"E541"),sQuery(id+"F6.wireOp",EDGE,"E542"),sQuery(id+"F6.wireOp",EDGE,"E543"),sQuery(id+"F6.wireOp",EDGE,"E544"),sQuery(id+"F6.wireOp",EDGE,"E545"),sQuery(id+"F6.wireOp",EDGE,"E546"),sQuery(id+"F6.wireOp",EDGE,"E547"),sQuery(id+"F6.wireOp",EDGE,"E548"),sQuery(id+"F6.wireOp",EDGE,"E549"),sQuery(id+"F6.wireOp",EDGE,"E550"),sQuery(id+"F6.wireOp",EDGE,"E551"),sQuery(id+"F6.wireOp",EDGE,"E552"),sQuery(id+"F6.wireOp",EDGE,"E553"),sQuery(id+"F6.wireOp",EDGE,"E554"),sQuery(id+"F6.wireOp",EDGE,"E555"),sQuery(id+"F6.wireOp",EDGE,"E556"),sQuery(id+"F6.wireOp",EDGE,"E557"),sQuery(id+"F6.wireOp",EDGE,"E558"),sQuery(id+"F6.wireOp",EDGE,"E559"),sQuery(id+"F6.wireOp",EDGE,"E560"),sQuery(id+"F6.wireOp",EDGE,"E561"),sQuery(id+"F6.wireOp",EDGE,"E562"),sQuery(id+"F6.wireOp",EDGE,"E563"),sQuery(id+"F6.wireOp",EDGE,"E564"),sQuery(id+"F6.wireOp",EDGE,"E565"),sQuery(id+"F6.wireOp",EDGE,"E566"),sQuery(id+"F6.wireOp",EDGE,"E567"),sQuery(id+"F6.wireOp",EDGE,"E568"),sQuery(id+"F6.wireOp",EDGE,"E569"),sQuery(id+"F6.wireOp",EDGE,"E570"),sQuery(id+"F6.wireOp",EDGE,"E571"),sQuery(id+"F6.wireOp",EDGE,"E572"),sQuery(id+"F6.wireOp",EDGE,"E573"),sQuery(id+"F6.wireOp",EDGE,"E574"),sQuery(id+"F6.wireOp",EDGE,"E575"),sQuery(id+"F6.wireOp",EDGE,"E576"),sQuery(id+"F6.wireOp",EDGE,"E577"),sQuery(id+"F6.wireOp",EDGE,"E578"),sQuery(id+"F6.wireOp",EDGE,"E579"),sQuery(id+"F6.wireOp",EDGE,"E580"),sQuery(id+"F6.wireOp",EDGE,"E581"),sQuery(id+"F6.wireOp",EDGE,"E582"),sQuery(id+"F6.wireOp",EDGE,"E583"),sQuery(id+"F6.wireOp",EDGE,"E584"),sQuery(id+"F6.wireOp",EDGE,"E585"),sQuery(id+"F6.wireOp",EDGE,"E586"),sQuery(id+"F6.wireOp",EDGE,"E587"),sQuery(id+"F6.wireOp",EDGE,"E588"),sQuery(id+"F6.wireOp",EDGE,"E589"),sQuery(id+"F6.wireOp",EDGE,"E590"),sQuery(id+"F6.wireOp",EDGE,"E591"),sQuery(id+"F6.wireOp",EDGE,"E592"),sQuery(id+"F6.wireOp",EDGE,"E593"),sQuery(id+"F6.wireOp",EDGE,"E594"),sQuery(id+"F6.wireOp",EDGE,"E595"),sQuery(id+"F6.wireOp",EDGE,"E596"),sQuery(id+"F6.wireOp",EDGE,"E597"),sQuery(id+"F6.wireOp",EDGE,"E598"),sQuery(id+"F6.wireOp",EDGE,"E599"),sQuery(id+"F6.wireOp",EDGE,"E600"),sQuery(id+"F6.wireOp",EDGE,"E601"),sQuery(id+"F6.wireOp",EDGE,"E602"),sQuery(id+"F6.wireOp",EDGE,"E603"),sQuery(id+"F6.wireOp",EDGE,"E604"),sQuery(id+"F6.wireOp",EDGE,"E605"),sQuery(id+"F6.wireOp",EDGE,"E606"),sQuery(id+"F6.wireOp",EDGE,"E607"),sQuery(id+"F6.wireOp",EDGE,"E608"),sQuery(id+"F6.wireOp",EDGE,"E609"),sQuery(id+"F6.wireOp",EDGE,"E610"),sQuery(id+"F6.wireOp",EDGE,"E611"),sQuery(id+"F6.wireOp",EDGE,"E612"),sQuery(id+"F6.wireOp",EDGE,"E613"),sQuery(id+"F6.wireOp",EDGE,"E614"),sQuery(id+"F6.wireOp",EDGE,"E615"),sQuery(id+"F6.wireOp",EDGE,"E616"),sQuery(id+"F6.wireOp",EDGE,"E617"),sQuery(id+"F6.wireOp",EDGE,"E618"),sQuery(id+"F6.wireOp",EDGE,"E619"),sQuery(id+"F6.wireOp",EDGE,"E620"),sQuery(id+"F6.wireOp",EDGE,"E621"),sQuery(id+"F6.wireOp",EDGE,"E622"),sQuery(id+"F6.wireOp",EDGE,"E623"),sQuery(id+"F6.wireOp",EDGE,"E624"),sQuery(id+"F6.wireOp",EDGE,"E625"),sQuery(id+"F6.wireOp",EDGE,"E626"),sQuery(id+"F6.wireOp",EDGE,"E627"),sQuery(id+"F6.wireOp",EDGE,"E628"),sQuery(id+"F6.wireOp",EDGE,"E629"),sQuery(id+"F6.wireOp",EDGE,"E630"),sQuery(id+"F6.wireOp",EDGE,"E631"),sQuery(id+"F6.wireOp",EDGE,"E632"),sQuery(id+"F6.wireOp",EDGE,"E633"),sQuery(id+"F6.wireOp",EDGE,"E634"),sQuery(id+"F6.wireOp",EDGE,"E635"),sQuery(id+"F6.wireOp",EDGE,"E636"),sQuery(id+"F6.wireOp",EDGE,"E637"),sQuery(id+"F6.wireOp",EDGE,"E638"),sQuery(id+"F6.wireOp",EDGE,"E639"),sQuery(id+"F6.wireOp",EDGE,"E640"),sQuery(id+"F6.wireOp",EDGE,"E641"),sQuery(id+"F6.wireOp",EDGE,"E642"),sQuery(id+"F6.wireOp",EDGE,"E643"),sQuery(id+"F6.wireOp",EDGE,"E644"),sQuery(id+"F6.wireOp",EDGE,"E645"),sQuery(id+"F6.wireOp",EDGE,"E646"),sQuery(id+"F6.wireOp",EDGE,"E647"),sQuery(id+"F6.wireOp",EDGE,"E648"),sQuery(id+"F6.wireOp",EDGE,"E649"),sQuery(id+"F6.wireOp",EDGE,"E650"),sQuery(id+"F6.wireOp",EDGE,"E651"),sQuery(id+"F6.wireOp",EDGE,"E652"),sQuery(id+"F6.wireOp",EDGE,"E653"),sQuery(id+"F6.wireOp",EDGE,"E654"),sQuery(id+"F6.wireOp",EDGE,"E655"),sQuery(id+"F6.wireOp",EDGE,"E656"),sQuery(id+"F6.wireOp",EDGE,"E657"),sQuery(id+"F6.wireOp",EDGE,"E658"),sQuery(id+"F6.wireOp",EDGE,"E659"),sQuery(id+"F6.wireOp",EDGE,"E660"),sQuery(id+"F6.wireOp",EDGE,"E661"),sQuery(id+"F6.wireOp",EDGE,"E662"),sQuery(id+"F6.wireOp",EDGE,"E663"),sQuery(id+"F6.wireOp",EDGE,"E664"),sQuery(id+"F6.wireOp",EDGE,"E665"),sQuery(id+"F6.wireOp",EDGE,"E666"),sQuery(id+"F6.wireOp",EDGE,"E667"),sQuery(id+"F6.wireOp",EDGE,"E668"),sQuery(id+"F6.wireOp",EDGE,"E669"),sQuery(id+"F6.wireOp",EDGE,"E670"),sQuery(id+"F6.wireOp",EDGE,"E671"),sQuery(id+"F6.wireOp",EDGE,"E672"),sQuery(id+"F6.wireOp",EDGE,"E673"),sQuery(id+"F6.wireOp",EDGE,"E674"),sQuery(id+"F6.wireOp",EDGE,"E675"),sQuery(id+"F6.wireOp",EDGE,"E676"),sQuery(id+"F6.wireOp",EDGE,"E677"),sQuery(id+"F6.wireOp",EDGE,"E678"),sQuery(id+"F6.wireOp",EDGE,"E679"),sQuery(id+"F6.wireOp",EDGE,"E680"),sQuery(id+"F6.wireOp",EDGE,"E681"),sQuery(id+"F6.wireOp",EDGE,"E682"),sQuery(id+"F6.wireOp",EDGE,"E683"),sQuery(id+"F6.wireOp",EDGE,"E684"),sQuery(id+"F6.wireOp",EDGE,"E685"),sQuery(id+"F6.wireOp",EDGE,"E686"),sQuery(id+"F6.wireOp",EDGE,"E687"),sQuery(id+"F6.wireOp",EDGE,"E688"),sQuery(id+"F6.wireOp",EDGE,"E689"),sQuery(id+"F6.wireOp",EDGE,"E690"),sQuery(id+"F6.wireOp",EDGE,"E691"),sQuery(id+"F6.wireOp",EDGE,"E692"),sQuery(id+"F6.wireOp",EDGE,"E693"),sQuery(id+"F6.wireOp",EDGE,"E694"),sQuery(id+"F6.wireOp",EDGE,"E695"),sQuery(id+"F6.wireOp",EDGE,"E696"),sQuery(id+"F6.wireOp",EDGE,"E697"),sQuery(id+"F6.wireOp",EDGE,"E698"),sQuery(id+"F6.wireOp",EDGE,"E699"),sQuery(id+"F6.wireOp",EDGE,"E700"),sQuery(id+"F6.wireOp",EDGE,"E701"),sQuery(id+"F6.wireOp",EDGE,"E702"),sQuery(id+"F6.wireOp",EDGE,"E703"),sQuery(id+"F6.wireOp",EDGE,"E704"),sQuery(id+"F6.wireOp",EDGE,"E705"),sQuery(id+"F6.wireOp",EDGE,"E706"),sQuery(id+"F6.wireOp",EDGE,"E707"),sQuery(id+"F6.wireOp",EDGE,"E708"),sQuery(id+"F6.wireOp",EDGE,"E709"),sQuery(id+"F6.wireOp",EDGE,"E710"),sQuery(id+"F6.wireOp",EDGE,"E711"),sQuery(id+"F6.wireOp",EDGE,"E712"),sQuery(id+"F6.wireOp",EDGE,"E713"),sQuery(id+"F6.wireOp",EDGE,"E714"),sQuery(id+"F6.wireOp",EDGE,"E715"),sQuery(id+"F6.wireOp",EDGE,"E716"),sQuery(id+"F6.wireOp",EDGE,"E717"),sQuery(id+"F6.wireOp",EDGE,"E718"),sQuery(id+"F6.wireOp",EDGE,"E719"),sQuery(id+"F6.wireOp",EDGE,"E720"),sQuery(id+"F6.wireOp",EDGE,"E721"),sQuery(id+"F6.wireOp",EDGE,"E722"),sQuery(id+"F6.wireOp",EDGE,"E723"),sQuery(id+"F6.wireOp",EDGE,"E724"),sQuery(id+"F6.wireOp",EDGE,"E725"),sQuery(id+"F6.wireOp",EDGE,"E726"),sQuery(id+"F6.wireOp",EDGE,"E727"),sQuery(id+"F6.wireOp",EDGE,"E728"),sQuery(id+"F6.wireOp",EDGE,"E729"),sQuery(id+"F6.wireOp",EDGE,"E730"),sQuery(id+"F6.wireOp",EDGE,"E731"),sQuery(id+"F6.wireOp",EDGE,"E732"),sQuery(id+"F6.wireOp",EDGE,"E733"),sQuery(id+"F6.wireOp",EDGE,"E734"),sQuery(id+"F6.wireOp",EDGE,"E735"),sQuery(id+"F6.wireOp",EDGE,"E736"),sQuery(id+"F6.wireOp",EDGE,"E737"),sQuery(id+"F6.wireOp",EDGE,"E738"),sQuery(id+"F6.wireOp",EDGE,"E739"),sQuery(id+"F6.wireOp",EDGE,"E740"),sQuery(id+"F6.wireOp",EDGE,"E741"),sQuery(id+"F6.wireOp",EDGE,"E742"),sQuery(id+"F6.wireOp",EDGE,"E743"),sQuery(id+"F6.wireOp",EDGE,"E744"),sQuery(id+"F6.wireOp",EDGE,"E745"),sQuery(id+"F6.wireOp",EDGE,"E746"),sQuery(id+"F6.wireOp",EDGE,"E747"),sQuery(id+"F6.wireOp",EDGE,"E748"),sQuery(id+"F6.wireOp",EDGE,"E749"),sQuery(id+"F6.wireOp",EDGE,"E750"),sQuery(id+"F6.wireOp",EDGE,"E751"),sQuery(id+"F6.wireOp",EDGE,"E752"),sQuery(id+"F6.wireOp",EDGE,"E753"),sQuery(id+"F6.wireOp",EDGE,"E754"),sQuery(id+"F6.wireOp",EDGE,"E755"),sQuery(id+"F6.wireOp",EDGE,"E756"),sQuery(id+"F6.wireOp",EDGE,"E757"),sQuery(id+"F6.wireOp",EDGE,"E758"),sQuery(id+"F6.wireOp",EDGE,"E759"),sQuery(id+"F6.wireOp",EDGE,"E760"),sQuery(id+"F6.wireOp",EDGE,"E761"),sQuery(id+"F6.wireOp",EDGE,"E762"),sQuery(id+"F6.wireOp",EDGE,"E763"),sQuery(id+"F6.wireOp",EDGE,"E764"),sQuery(id+"F6.wireOp",EDGE,"E765"),sQuery(id+"F6.wireOp",EDGE,"E766"),sQuery(id+"F6.wireOp",EDGE,"E767"),sQuery(id+"F6.wireOp",EDGE,"E768"),sQuery(id+"F6.wireOp",EDGE,"E769"),sQuery(id+"F6.wireOp",EDGE,"E770"),sQuery(id+"F6.wireOp",EDGE,"E771"),sQuery(id+"F6.wireOp",EDGE,"E772"),sQuery(id+"F6.wireOp",EDGE,"E773"),sQuery(id+"F6.wireOp",EDGE,"E774"),sQuery(id+"F6.wireOp",EDGE,"E775"),sQuery(id+"F6.wireOp",EDGE,"E776"),sQuery(id+"F6.wireOp",EDGE,"E777"),sQuery(id+"F6.wireOp",EDGE,"E778"),sQuery(id+"F6.wireOp",EDGE,"E779"),sQuery(id+"F6.wireOp",EDGE,"E780"),sQuery(id+"F6.wireOp",EDGE,"E781"),sQuery(id+"F6.wireOp",EDGE,"E782"),sQuery(id+"F6.wireOp",EDGE,"E783"),sQuery(id+"F6.wireOp",EDGE,"E784"),sQuery(id+"F6.wireOp",EDGE,"E785"),sQuery(id+"F6.wireOp",EDGE,"E786"),sQuery(id+"F6.wireOp",EDGE,"E787"),sQuery(id+"F6.wireOp",EDGE,"E788"),sQuery(id+"F6.wireOp",EDGE,"E789"),sQuery(id+"F6.wireOp",EDGE,"E790"),sQuery(id+"F6.wireOp",EDGE,"E791"),sQuery(id+"F6.wireOp",EDGE,"E792"),sQuery(id+"F6.wireOp",EDGE,"E793"),sQuery(id+"F6.wireOp",EDGE,"E794"),sQuery(id+"F6.wireOp",EDGE,"E795"),sQuery(id+"F6.wireOp",EDGE,"E796"),sQuery(id+"F6.wireOp",EDGE,"E797"),sQuery(id+"F6.wireOp",EDGE,"E798"),sQuery(id+"F6.wireOp",EDGE,"E799"),sQuery(id+"F6.wireOp",EDGE,"E800"),sQuery(id+"F6.wireOp",EDGE,"E801"),sQuery(id+"F6.wireOp",EDGE,"E802"),sQuery(id+"F6.wireOp",EDGE,"E803"),sQuery(id+"F6.wireOp",EDGE,"E804"),sQuery(id+"F6.wireOp",EDGE,"E805"),sQuery(id+"F6.wireOp",EDGE,"E806"),sQuery(id+"F6.wireOp",EDGE,"E807"),sQuery(id+"F6.wireOp",EDGE,"E808"),sQuery(id+"F6.wireOp",EDGE,"E809"),sQuery(id+"F6.wireOp",EDGE,"E810"),sQuery(id+"F6.wireOp",EDGE,"E811"),sQuery(id+"F6.wireOp",EDGE,"E812"),sQuery(id+"F6.wireOp",EDGE,"E813"),sQuery(id+"F6.wireOp",EDGE,"E814"),sQuery(id+"F6.wireOp",EDGE,"E815"),sQuery(id+"F6.wireOp",EDGE,"E816"),sQuery(id+"F6.wireOp",EDGE,"E817"),sQuery(id+"F6.wireOp",EDGE,"E818"),sQuery(id+"F6.wireOp",EDGE,"E819"),sQuery(id+"F6.wireOp",EDGE,"E820"),sQuery(id+"F6.wireOp",EDGE,"E821"),sQuery(id+"F6.wireOp",EDGE,"E822"),sQuery(id+"F6.wireOp",EDGE,"E823"),sQuery(id+"F6.wireOp",EDGE,"E824"),sQuery(id+"F6.wireOp",EDGE,"E825"),sQuery(id+"F6.wireOp",EDGE,"E826"),sQuery(id+"F6.wireOp",EDGE,"E827"),sQuery(id+"F6.wireOp",EDGE,"E828"),sQuery(id+"F6.wireOp",EDGE,"E829"),sQuery(id+"F6.wireOp",EDGE,"E830"),sQuery(id+"F6.wireOp",EDGE,"E831"),sQuery(id+"F6.wireOp",EDGE,"E832"),sQuery(id+"F6.wireOp",EDGE,"E833"),sQuery(id+"F6.wireOp",EDGE,"E834"),sQuery(id+"F6.wireOp",EDGE,"E835"),sQuery(id+"F6.wireOp",EDGE,"E836"),sQuery(id+"F6.wireOp",EDGE,"E837"),sQuery(id+"F6.wireOp",EDGE,"E838"),sQuery(id+"F6.wireOp",EDGE,"E839"),sQuery(id+"F6.wireOp",EDGE,"E840"),sQuery(id+"F6.wireOp",EDGE,"E841"),sQuery(id+"F6.wireOp",EDGE,"E842"),sQuery(id+"F6.wireOp",EDGE,"E843"),sQuery(id+"F6.wireOp",EDGE,"E844"),sQuery(id+"F6.wireOp",EDGE,"E845"),sQuery(id+"F6.wireOp",EDGE,"E846"),sQuery(id+"F6.wireOp",EDGE,"E847"),sQuery(id+"F6.wireOp",EDGE,"E848"),sQuery(id+"F6.wireOp",EDGE,"E849"),sQuery(id+"F6.wireOp",EDGE,"E850"),sQuery(id+"F6.wireOp",EDGE,"E851"),sQuery(id+"F6.wireOp",EDGE,"E852"),sQuery(id+"F6.wireOp",EDGE,"E853"),sQuery(id+"F6.wireOp",EDGE,"E854"),sQuery(id+"F6.wireOp",EDGE,"E855"),sQuery(id+"F6.wireOp",EDGE,"E856"),sQuery(id+"F6.wireOp",EDGE,"E857"),sQuery(id+"F6.wireOp",EDGE,"E858"),sQuery(id+"F6.wireOp",EDGE,"E859"),sQuery(id+"F6.wireOp",EDGE,"E860"),sQuery(id+"F6.wireOp",EDGE,"E861"),sQuery(id+"F6.wireOp",EDGE,"E862"),sQuery(id+"F6.wireOp",EDGE,"E863"),sQuery(id+"F6.wireOp",EDGE,"E864"),sQuery(id+"F6.wireOp",EDGE,"E865"),sQuery(id+"F6.wireOp",EDGE,"E866"),sQuery(id+"F6.wireOp",EDGE,"E867"),sQuery(id+"F6.wireOp",EDGE,"E868"),sQuery(id+"F6.wireOp",EDGE,"E869"),sQuery(id+"F6.wireOp",EDGE,"E870"),sQuery(id+"F6.wireOp",EDGE,"E871"),sQuery(id+"F6.wireOp",EDGE,"E872"),sQuery(id+"F6.wireOp",EDGE,"E873"),sQuery(id+"F6.wireOp",EDGE,"E874"),sQuery(id+"F6.wireOp",EDGE,"E875"),sQuery(id+"F6.wireOp",EDGE,"E876"),sQuery(id+"F6.wireOp",EDGE,"E877"),sQuery(id+"F6.wireOp",EDGE,"E878"),sQuery(id+"F6.wireOp",EDGE,"E879"),sQuery(id+"F6.wireOp",EDGE,"E880"),sQuery(id+"F6.wireOp",EDGE,"E881"),sQuery(id+"F6.wireOp",EDGE,"E882"),sQuery(id+"F6.wireOp",EDGE,"E883"),sQuery(id+"F6.wireOp",EDGE,"E884"),sQuery(id+"F6.wireOp",EDGE,"E885"),sQuery(id+"F6.wireOp",EDGE,"E886"),sQuery(id+"F6.wireOp",EDGE,"E887"),sQuery(id+"F6.wireOp",EDGE,"E888"),sQuery(id+"F6.wireOp",EDGE,"E889"),sQuery(id+"F6.wireOp",EDGE,"E890"),sQuery(id+"F6.wireOp",EDGE,"E891"),sQuery(id+"F6.wireOp",EDGE,"E892"),sQuery(id+"F6.wireOp",EDGE,"E893"),sQuery(id+"F6.wireOp",EDGE,"E894"),sQuery(id+"F6.wireOp",EDGE,"E895"),sQuery(id+"F6.wireOp",EDGE,"E896"),sQuery(id+"F6.wireOp",EDGE,"E897"),sQuery(id+"F6.wireOp",EDGE,"E898"),sQuery(id+"F6.wireOp",EDGE,"E899"),sQuery(id+"F6.wireOp",EDGE,"E900"),sQuery(id+"F6.wireOp",EDGE,"E901"),sQuery(id+"F6.wireOp",EDGE,"E902"),sQuery(id+"F6.wireOp",EDGE,"E903"),sQuery(id+"F6.wireOp",EDGE,"E904"),sQuery(id+"F6.wireOp",EDGE,"E905"),sQuery(id+"F6.wireOp",EDGE,"E906"),sQuery(id+"F6.wireOp",EDGE,"E907"),sQuery(id+"F6.wireOp",EDGE,"E908"),sQuery(id+"F6.wireOp",EDGE,"E909"),sQuery(id+"F6.wireOp",EDGE,"E910"),sQuery(id+"F6.wireOp",EDGE,"E911"),sQuery(id+"F6.wireOp",EDGE,"E911"),sQuery(id+"F6.wireOp",EDGE,"E912"),sQuery(id+"F6.wireOp",EDGE,"E913"),sQuery(id+"F6.wireOp",EDGE,"E914"),sQuery(id+"F6.wireOp",EDGE,"E915"),sQuery(id+"F6.wireOp",EDGE,"E916"),sQuery(id+"F6.wireOp",EDGE,"E917"),sQuery(id+"F6.wireOp",EDGE,"E918"),sQuery(id+"F6.wireOp",EDGE,"E919"),sQuery(id+"F6.wireOp",EDGE,"E920"),sQuery(id+"F6.wireOp",EDGE,"E921"),sQuery(id+"F6.wireOp",EDGE,"E922"),sQuery(id+"F6.wireOp",EDGE,"E923"),sQuery(id+"F6.wireOp",EDGE,"E924"),sQuery(id+"F6.wireOp",EDGE,"E925"),sQuery(id+"F6.wireOp",EDGE,"E926"),sQuery(id+"F6.wireOp",EDGE,"E927"),sQuery(id+"F6.wireOp",EDGE,"E928"),sQuery(id+"F6.wireOp",EDGE,"E929"),sQuery(id+"F6.wireOp",EDGE,"E930"),sQuery(id+"F6.wireOp",EDGE,"E931"),sQuery(id+"F6.wireOp",EDGE,"E932"),sQuery(id+"F6.wireOp",EDGE,"E933"),sQuery(id+"F6.wireOp",EDGE,"E934"),sQuery(id+"F6.wireOp",EDGE,"E935"),sQuery(id+"F6.wireOp",EDGE,"E936"),sQuery(id+"F6.wireOp",EDGE,"E937"),sQuery(id+"F6.wireOp",EDGE,"E938"),sQuery(id+"F6.wireOp",EDGE,"E939"),sQuery(id+"F6.wireOp",EDGE,"E940"),sQuery(id+"F6.wireOp",EDGE,"E941"),sQuery(id+"F6.wireOp",EDGE,"E942"),sQuery(id+"F6.wireOp",EDGE,"E943"),sQuery(id+"F6.wireOp",EDGE,"E944"),sQuery(id+"F6.wireOp",EDGE,"E945"),sQuery(id+"F6.wireOp",EDGE,"E946"),sQuery(id+"F6.wireOp",EDGE,"E947"),sQuery(id+"F6.wireOp",EDGE,"E948"),sQuery(id+"F6.wireOp",EDGE,"E949"),sQuery(id+"F6.wireOp",EDGE,"E950"),sQuery(id+"F6.wireOp",EDGE,"E951"),sQuery(id+"F6.wireOp",EDGE,"E952"),sQuery(id+"F6.wireOp",EDGE,"E953"),sQuery(id+"F6.wireOp",EDGE,"E954"),sQuery(id+"F6.wireOp",EDGE,"E955"),sQuery(id+"F6.wireOp",EDGE,"E956"),sQuery(id+"F6.wireOp",EDGE,"E957"),sQuery(id+"F6.wireOp",EDGE,"E958"),sQuery(id+"F6.wireOp",EDGE,"E959"),sQuery(id+"F6.wireOp",EDGE,"E960"),sQuery(id+"F6.wireOp",EDGE,"E961"),sQuery(id+"F6.wireOp",EDGE,"E962"),sQuery(id+"F6.wireOp",EDGE,"E963"),sQuery(id+"F6.wireOp",EDGE,"E964"),sQuery(id+"F6.wireOp",EDGE,"E965"),sQuery(id+"F6.wireOp",EDGE,"E966"),sQuery(id+"F6.wireOp",EDGE,"E967"),sQuery(id+"F6.wireOp",EDGE,"E968"),sQuery(id+"F6.wireOp",EDGE,"E969"),sQuery(id+"F6.wireOp",EDGE,"E970"),sQuery(id+"F6.wireOp",EDGE,"E971"),sQuery(id+"F6.wireOp",EDGE,"E972"),sQuery(id+"F6.wireOp",EDGE,"E973"),sQuery(id+"F6.wireOp",EDGE,"E974"),sQuery(id+"F6.wireOp",EDGE,"E975"),sQuery(id+"F6.wireOp",EDGE,"E976"),sQuery(id+"F6.wireOp",EDGE,"E977"),sQuery(id+"F6.wireOp",EDGE,"E978"),sQuery(id+"F6.wireOp",EDGE,"E979"),sQuery(id+"F6.wireOp",EDGE,"E980"),sQuery(id+"F6.wireOp",EDGE,"E981"),sQuery(id+"F6.wireOp",EDGE,"E982"),sQuery(id+"F6.wireOp",EDGE,"E983"),sQuery(id+"F6.wireOp",EDGE,"E984"),sQuery(id+"F6.wireOp",EDGE,"E985"),sQuery(id+"F6.wireOp",EDGE,"E986"),sQuery(id+"F6.wireOp",EDGE,"E987"),sQuery(id+"F6.wireOp",EDGE,"E988"),sQuery(id+"F6.wireOp",EDGE,"E989"),sQuery(id+"F6.wireOp",EDGE,"E990"),sQuery(id+"F6.wireOp",EDGE,"E991"),sQuery(id+"F6.wireOp",EDGE,"E992"),sQuery(id+"F6.wireOp",EDGE,"E993"),sQuery(id+"F6.wireOp",EDGE,"E994"),sQuery(id+"F6.wireOp",EDGE,"E995"),sQuery(id+"F6.wireOp",EDGE,"E996"),sQuery(id+"F6.wireOp",EDGE,"E997"),sQuery(id+"F6.wireOp",EDGE,"E998"),sQuery(id+"F6.wireOp",EDGE,"E999"),sQuery(id+"F6.wireOp",EDGE,"E1000"),sQuery(id+"F6.wireOp",EDGE,"E1001"),sQuery(id+"F6.wireOp",EDGE,"E1002"),sQuery(id+"F6.wireOp",EDGE,"E1003"),sQuery(id+"F6.wireOp",EDGE,"E1004"),sQuery(id+"F6.wireOp",EDGE,"E1005"),sQuery(id+"F6.wireOp",EDGE,"E1006"),sQuery(id+"F6.wireOp",EDGE,"E1007"),sQuery(id+"F6.wireOp",EDGE,"E1008"),sQuery(id+"F6.wireOp",EDGE,"E1009"),sQuery(id+"F6.wireOp",EDGE,"E1010"),sQuery(id+"F6.wireOp",EDGE,"E1011"),sQuery(id+"F6.wireOp",EDGE,"E1012"),sQuery(id+"F6.wireOp",EDGE,"E1013"),sQuery(id+"F6.wireOp",EDGE,"E1014"),sQuery(id+"F6.wireOp",EDGE,"E1015"),sQuery(id+"F6.wireOp",EDGE,"E1016"),sQuery(id+"F6.wireOp",EDGE,"E1017"),sQuery(id+"F6.wireOp",EDGE,"E1018"),sQuery(id+"F6.wireOp",EDGE,"E1019"),sQuery(id+"F6.wireOp",EDGE,"E1020"),sQuery(id+"F6.wireOp",EDGE,"E1021"),sQuery(id+"F6.wireOp",EDGE,"E1022"),sQuery(id+"F6.wireOp",EDGE,"E1023"),sQuery(id+"F6.wireOp",EDGE,"E1024"),sQuery(id+"F6.wireOp",EDGE,"E1025"),sQuery(id+"F6.wireOp",EDGE,"E1026"),sQuery(id+"F6.wireOp",EDGE,"E1027"),sQuery(id+"F6.wireOp",EDGE,"E1028"),sQuery(id+"F6.wireOp",EDGE,"E1029"),sQuery(id+"F6.wireOp",EDGE,"E1030"),sQuery(id+"F6.wireOp",EDGE,"E1031"),sQuery(id+"F6.wireOp",EDGE,"E1032"),sQuery(id+"F6.wireOp",EDGE,"E1033"),sQuery(id+"F6.wireOp",EDGE,"E1034"),sQuery(id+"F6.wireOp",EDGE,"E1035"),sQuery(id+"F6.wireOp",EDGE,"E1036"),sQuery(id+"F6.wireOp",EDGE,"E1037"),sQuery(id+"F6.wireOp",EDGE,"E1038"),sQuery(id+"F6.wireOp",EDGE,"E1039"),sQuery(id+"F6.wireOp",EDGE,"E1040"),sQuery(id+"F6.wireOp",EDGE,"E1041"),sQuery(id+"F6.wireOp",EDGE,"E1042"),sQuery(id+"F6.wireOp",EDGE,"E1043"),sQuery(id+"F6.wireOp",EDGE,"E1044"),sQuery(id+"F6.wireOp",EDGE,"E1045"),sQuery(id+"F6.wireOp",EDGE,"E1046"),sQuery(id+"F6.wireOp",EDGE,"E1047"),sQuery(id+"F6.wireOp",EDGE,"E1048"),sQuery(id+"F6.wireOp",EDGE,"E1049"),sQuery(id+"F6.wireOp",EDGE,"E1050"),sQuery(id+"F6.wireOp",EDGE,"E1051"),sQuery(id+"F6.wireOp",EDGE,"E1052"),sQuery(id+"F6.wireOp",EDGE,"E1053"),sQuery(id+"F6.wireOp",EDGE,"E1054"),sQuery(id+"F6.wireOp",EDGE,"E1055"),sQuery(id+"F6.wireOp",EDGE,"E1056"),sQuery(id+"F6.wireOp",EDGE,"E1057"),sQuery(id+"F6.wireOp",EDGE,"E1058"),sQuery(id+"F6.wireOp",EDGE,"E1059"),sQuery(id+"F6.wireOp",EDGE,"E1060"),sQuery(id+"F6.wireOp",EDGE,"E1061"),sQuery(id+"F6.wireOp",EDGE,"E1062"),sQuery(id+"F6.wireOp",EDGE,"E1063"),sQuery(id+"F6.wireOp",EDGE,"E1064"),sQuery(id+"F6.wireOp",EDGE,"E1065"),sQuery(id+"F6.wireOp",EDGE,"E1066"),sQuery(id+"F6.wireOp",EDGE,"E1067"),sQuery(id+"F6.wireOp",EDGE,"E1068"),sQuery(id+"F6.wireOp",EDGE,"E1069"),sQuery(id+"F6.wireOp",EDGE,"E1070"),sQuery(id+"F6.wireOp",EDGE,"E1071"),sQuery(id+"F6.wireOp",EDGE,"E1072"),sQuery(id+"F6.wireOp",EDGE,"E1073"),sQuery(id+"F6.wireOp",EDGE,"E1074"),sQuery(id+"F6.wireOp",EDGE,"E1075"),sQuery(id+"F6.wireOp",EDGE,"E1076"),sQuery(id+"F6.wireOp",EDGE,"E1077"),sQuery(id+"F6.wireOp",EDGE,"E1078"),sQuery(id+"F6.wireOp",EDGE,"E1079"),sQuery(id+"F6.wireOp",EDGE,"E1080"),sQuery(id+"F6.wireOp",EDGE,"E1081"),sQuery(id+"F6.wireOp",EDGE,"E1082"),sQuery(id+"F6.wireOp",EDGE,"E1083"),sQuery(id+"F6.wireOp",EDGE,"E1084"),sQuery(id+"F6.wireOp",EDGE,"E1085"),sQuery(id+"F6.wireOp",EDGE,"E1086"),sQuery(id+"F6.wireOp",EDGE,"E1087"),sQuery(id+"F6.wireOp",EDGE,"E1088"),sQuery(id+"F6.wireOp",EDGE,"E1089"),sQuery(id+"F6.wireOp",EDGE,"E1090"),sQuery(id+"F6.wireOp",EDGE,"E1091"),sQuery(id+"F6.wireOp",EDGE,"E1092"),sQuery(id+"F6.wireOp",EDGE,"E1093"),sQuery(id+"F6.wireOp",EDGE,"E1094"),sQuery(id+"F6.wireOp",EDGE,"E1095"),sQuery(id+"F6.wireOp",EDGE,"E1096"),sQuery(id+"F6.wireOp",EDGE,"E1097"),sQuery(id+"F6.wireOp",EDGE,"E1098"),sQuery(id+"F6.wireOp",EDGE,"E1099"),sQuery(id+"F6.wireOp",EDGE,"E1100"),sQuery(id+"F6.wireOp",EDGE,"E1101"),sQuery(id+"F6.wireOp",EDGE,"E1102"),sQuery(id+"F6.wireOp",EDGE,"E1103"),sQuery(id+"F6.wireOp",EDGE,"E1104"),sQuery(id+"F6.wireOp",EDGE,"E1105"),sQuery(id+"F6.wireOp",EDGE,"E1106"),sQuery(id+"F6.wireOp",EDGE,"E1107"),sQuery(id+"F6.wireOp",EDGE,"E1108"),sQuery(id+"F6.wireOp",EDGE,"E1109"),sQuery(id+"F6.wireOp",EDGE,"E1110"),sQuery(id+"F6.wireOp",EDGE,"E1111"),sQuery(id+"F6.wireOp",EDGE,"E1112"),sQuery(id+"F6.wireOp",EDGE,"E1113"),sQuery(id+"F6.wireOp",EDGE,"E1114"),sQuery(id+"F6.wireOp",EDGE,"E1115"),sQuery(id+"F6.wireOp",EDGE,"E1116"),sQuery(id+"F6.wireOp",EDGE,"E1117"),sQuery(id+"F6.wireOp",EDGE,"E1118"),sQuery(id+"F6.wireOp",EDGE,"E1119"),sQuery(id+"F6.wireOp",EDGE,"E1120"),sQuery(id+"F6.wireOp",EDGE,"E1121"),sQuery(id+"F6.wireOp",EDGE,"E1122"),sQuery(id+"F6.wireOp",EDGE,"E1123"),sQuery(id+"F6.wireOp",EDGE,"E1124"),sQuery(id+"F6.wireOp",EDGE,"E1125"),sQuery(id+"F6.wireOp",EDGE,"E1126"),sQuery(id+"F6.wireOp",EDGE,"E1127"),sQuery(id+"F6.wireOp",EDGE,"E1128"),sQuery(id+"F6.wireOp",EDGE,"E1129"),sQuery(id+"F6.wireOp",EDGE,"E1130"),sQuery(id+"F6.wireOp",EDGE,"E1131"),sQuery(id+"F6.wireOp",EDGE,"E1132"),sQuery(id+"F6.wireOp",EDGE,"E1133"),sQuery(id+"F6.wireOp",EDGE,"E1134"),sQuery(id+"F6.wireOp",EDGE,"E1135"),sQuery(id+"F6.wireOp",EDGE,"E1136"),sQuery(id+"F6.wireOp",EDGE,"E1137"),sQuery(id+"F6.wireOp",EDGE,"E1138"),sQuery(id+"F6.wireOp",EDGE,"E1139"),sQuery(id+"F6.wireOp",EDGE,"E1140"),sQuery(id+"F6.wireOp",EDGE,"E1141"),sQuery(id+"F6.wireOp",EDGE,"E1142"),sQuery(id+"F6.wireOp",EDGE,"E1143"),sQuery(id+"F6.wireOp",EDGE,"E1144"),sQuery(id+"F6.wireOp",EDGE,"E1145"),sQuery(id+"F6.wireOp",EDGE,"E1146"),sQuery(id+"F6.wireOp",EDGE,"E1147"),sQuery(id+"F6.wireOp",EDGE,"E1148"),sQuery(id+"F6.wireOp",EDGE,"E1149"),sQuery(id+"F6.wireOp",EDGE,"E1150"),sQuery(id+"F6.wireOp",EDGE,"E1151"),sQuery(id+"F6.wireOp",EDGE,"E1152"),sQuery(id+"F6.wireOp",EDGE,"E1153"),sQuery(id+"F6.wireOp",EDGE,"E1154"),sQuery(id+"F6.wireOp",EDGE,"E1155"),sQuery(id+"F6.wireOp",EDGE,"E1156"),sQuery(id+"F6.wireOp",EDGE,"E1157"),sQuery(id+"F6.wireOp",EDGE,"E1158"),sQuery(id+"F6.wireOp",EDGE,"E1159"),sQuery(id+"F6.wireOp",EDGE,"E1160"),sQuery(id+"F6.wireOp",EDGE,"E1161"),sQuery(id+"F6.wireOp",EDGE,"E1162"),sQuery(id+"F6.wireOp",EDGE,"E1163"),sQuery(id+"F6.wireOp",EDGE,"E1164"),sQuery(id+"F6.wireOp",EDGE,"E1165"),sQuery(id+"F6.wireOp",EDGE,"E1166"),sQuery(id+"F6.wireOp",EDGE,"E1167"),sQuery(id+"F6.wireOp",EDGE,"E1168"),sQuery(id+"F6.wireOp",EDGE,"E1169"),sQuery(id+"F6.wireOp",EDGE,"E1170"),sQuery(id+"F6.wireOp",EDGE,"E1171"),sQuery(id+"F6.wireOp",EDGE,"E1172"),sQuery(id+"F6.wireOp",EDGE,"E1173"),sQuery(id+"F6.wireOp",EDGE,"E1174"),sQuery(id+"F6.wireOp",EDGE,"E1175"),sQuery(id+"F6.wireOp",EDGE,"E1176"),sQuery(id+"F6.wireOp",EDGE,"E1177"),sQuery(id+"F6.wireOp",EDGE,"E1178"),sQuery(id+"F6.wireOp",EDGE,"E1179"),sQuery(id+"F6.wireOp",EDGE,"E1180"),sQuery(id+"F6.wireOp",EDGE,"E1181"),sQuery(id+"F6.wireOp",EDGE,"E1182"),sQuery(id+"F6.wireOp",EDGE,"E1183"),sQuery(id+"F6.wireOp",EDGE,"E1184"),sQuery(id+"F6.wireOp",EDGE,"E1185"),sQuery(id+"F6.wireOp",EDGE,"E1186"),sQuery(id+"F6.wireOp",EDGE,"E1187"),sQuery(id+"F6.wireOp",EDGE,"E1188"),sQuery(id+"F6.wireOp",EDGE,"E1189"),sQuery(id+"F6.wireOp",EDGE,"E1190"),sQuery(id+"F6.wireOp",EDGE,"E1191"),sQuery(id+"F6.wireOp",EDGE,"E1192"),sQuery(id+"F6.wireOp",EDGE,"E1193"),sQuery(id+"F6.wireOp",EDGE,"E1194"),sQuery(id+"F6.wireOp",EDGE,"E1195"),sQuery(id+"F6.wireOp",EDGE,"E1196"),sQuery(id+"F6.wireOp",EDGE,"E1197"),sQuery(id+"F6.wireOp",EDGE,"E1198"),sQuery(id+"F6.wireOp",EDGE,"E1199"),sQuery(id+"F6.wireOp",EDGE,"E1200"),sQuery(id+"F6.wireOp",EDGE,"E1201"),sQuery(id+"F6.wireOp",EDGE,"E1202"),sQuery(id+"F6.wireOp",EDGE,"E1203"),sQuery(id+"F6.wireOp",EDGE,"E1204"),sQuery(id+"F6.wireOp",EDGE,"E1205"),sQuery(id+"F6.wireOp",EDGE,"E1206"),sQuery(id+"F6.wireOp",EDGE,"E1207"),sQuery(id+"F6.wireOp",EDGE,"E1208"),sQuery(id+"F6.wireOp",EDGE,"E1209"),sQuery(id+"F6.wireOp",EDGE,"E1210"),sQuery(id+"F6.wireOp",EDGE,"E1211"),sQuery(id+"F6.wireOp",EDGE,"E1212"),sQuery(id+"F6.wireOp",EDGE,"E1213"),sQuery(id+"F6.wireOp",EDGE,"E1214"),sQuery(id+"F6.wireOp",EDGE,"E1215"),sQuery(id+"F6.wireOp",EDGE,"E1216"),sQuery(id+"F6.wireOp",EDGE,"E1217"),sQuery(id+"F6.wireOp",EDGE,"E1218"),sQuery(id+"F6.wireOp",EDGE,"E1219"),sQuery(id+"F6.wireOp",EDGE,"E1220"),sQuery(id+"F6.wireOp",EDGE,"E1221"),sQuery(id+"F6.wireOp",EDGE,"E1222"),sQuery(id+"F6.wireOp",EDGE,"E1223"),sQuery(id+"F6.wireOp",EDGE,"E1224"),sQuery(id+"F6.wireOp",EDGE,"E1225"),sQuery(id+"F6.wireOp",EDGE,"E1226"),sQuery(id+"F6.wireOp",EDGE,"E1227"),sQuery(id+"F6.wireOp",EDGE,"E1228"),sQuery(id+"F6.wireOp",EDGE,"E1229"),sQuery(id+"F6.wireOp",EDGE,"E1230"),sQuery(id+"F6.wireOp",EDGE,"E1231"),sQuery(id+"F6.wireOp",EDGE,"E1232"),sQuery(id+"F6.wireOp",EDGE,"E1233"),sQuery(id+"F6.wireOp",EDGE,"E1234"),sQuery(id+"F6.wireOp",EDGE,"E1235"),sQuery(id+"F6.wireOp",EDGE,"E1236"),sQuery(id+"F6.wireOp",EDGE,"E1237"),sQuery(id+"F6.wireOp",EDGE,"E1238"),sQuery(id+"F6.wireOp",EDGE,"E1239"),sQuery(id+"F6.wireOp",EDGE,"E1240"),sQuery(id+"F6.wireOp",EDGE,"E1241"),sQuery(id+"F6.wireOp",EDGE,"E1242"),sQuery(id+"F6.wireOp",EDGE,"E1243"),sQuery(id+"F6.wireOp",EDGE,"E1244"),sQuery(id+"F6.wireOp",EDGE,"E1245"),sQuery(id+"F6.wireOp",EDGE,"E1246"),sQuery(id+"F6.wireOp",EDGE,"E1247"),sQuery(id+"F6.wireOp",EDGE,"E1248"),sQuery(id+"F6.wireOp",EDGE,"E1249"),sQuery(id+"F6.wireOp",EDGE,"E1250"),sQuery(id+"F6.wireOp",EDGE,"E1251"),sQuery(id+"F6.wireOp",EDGE,"E1252"),sQuery(id+"F6.wireOp",EDGE,"E1253"),sQuery(id+"F6.wireOp",EDGE,"E1254"),sQuery(id+"F6.wireOp",EDGE,"E1255"),sQuery(id+"F6.wireOp",EDGE,"E1256"),sQuery(id+"F6.wireOp",EDGE,"E1257"),sQuery(id+"F6.wireOp",EDGE,"E1258"),sQuery(id+"F6.wireOp",EDGE,"E1259"),sQuery(id+"F6.wireOp",EDGE,"E1260"),sQuery(id+"F6.wireOp",EDGE,"E1261"),sQuery(id+"F6.wireOp",EDGE,"E1262"),sQuery(id+"F6.wireOp",EDGE,"E1263"),sQuery(id+"F6.wireOp",EDGE,"E1264"),sQuery(id+"F6.wireOp",EDGE,"E1265"),sQuery(id+"F6.wireOp",EDGE,"E1266"),sQuery(id+"F6.wireOp",EDGE,"E1267"),sQuery(id+"F6.wireOp",EDGE,"E1268"),sQuery(id+"F6.wireOp",EDGE,"E1269"),sQuery(id+"F6.wireOp",EDGE,"E1270"),sQuery(id+"F6.wireOp",EDGE,"E1271"),sQuery(id+"F6.wireOp",EDGE,"E1272"),sQuery(id+"F6.wireOp",EDGE,"E1273"),sQuery(id+"F6.wireOp",EDGE,"E1274"),sQuery(id+"F6.wireOp",EDGE,"E1275"),sQuery(id+"F6.wireOp",EDGE,"E1276"),sQuery(id+"F6.wireOp",EDGE,"E1277"),sQuery(id+"F6.wireOp",EDGE,"E1278"),sQuery(id+"F6.wireOp",EDGE,"E1279"),sQuery(id+"F6.wireOp",EDGE,"E1280"),sQuery(id+"F6.wireOp",EDGE,"E1281"),sQuery(id+"F6.wireOp",EDGE,"E1282"),sQuery(id+"F6.wireOp",EDGE,"E1283"),sQuery(id+"F6.wireOp",EDGE,"E1284"),sQuery(id+"F6.wireOp",EDGE,"E1285"),sQuery(id+"F6.wireOp",EDGE,"E1286"),sQuery(id+"F6.wireOp",EDGE,"E1287"),sQuery(id+"F6.wireOp",EDGE,"E1288"),sQuery(id+"F6.wireOp",EDGE,"E1289"),sQuery(id+"F6.wireOp",EDGE,"E1290"),sQuery(id+"F6.wireOp",EDGE,"E1291"),sQuery(id+"F6.wireOp",EDGE,"E1292"),sQuery(id+"F6.wireOp",EDGE,"E1293"),sQuery(id+"F6.wireOp",EDGE,"E1294"),sQuery(id+"F6.wireOp",EDGE,"E1295"),sQuery(id+"F6.wireOp",EDGE,"E1296"),sQuery(id+"F6.wireOp",EDGE,"E1297"),sQuery(id+"F6.wireOp",EDGE,"E1298"),sQuery(id+"F6.wireOp",EDGE,"E1299"),sQuery(id+"F6.wireOp",EDGE,"E1300"),sQuery(id+"F6.wireOp",EDGE,"E1301"),sQuery(id+"F6.wireOp",EDGE,"E1302"),sQuery(id+"F6.wireOp",EDGE,"E1303"),sQuery(id+"F6.wireOp",EDGE,"E1304"),sQuery(id+"F6.wireOp",EDGE,"E1305"),sQuery(id+"F6.wireOp",EDGE,"E1306"),sQuery(id+"F6.wireOp",EDGE,"E1307"),sQuery(id+"F6.wireOp",EDGE,"E1308"),sQuery(id+"F6.wireOp",EDGE,"E1309"),sQuery(id+"F6.wireOp",EDGE,"E1310"),sQuery(id+"F6.wireOp",EDGE,"E1311"),sQuery(id+"F6.wireOp",EDGE,"E1312"),sQuery(id+"F6.wireOp",EDGE,"E1313"),sQuery(id+"F6.wireOp",EDGE,"E1314"),sQuery(id+"F6.wireOp",EDGE,"E1315"),sQuery(id+"F6.wireOp",EDGE,"E1316"),sQuery(id+"F6.wireOp",EDGE,"E1317"),sQuery(id+"F6.wireOp",EDGE,"E1318"),sQuery(id+"F6.wireOp",EDGE,"E1319"),sQuery(id+"F6.wireOp",EDGE,"E1320"),sQuery(id+"F6.wireOp",EDGE,"E1321"),sQuery(id+"F6.wireOp",EDGE,"E1322"),sQuery(id+"F6.wireOp",EDGE,"E1323"),sQuery(id+"F6.wireOp",EDGE,"E1324"),sQuery(id+"F6.wireOp",EDGE,"E1325"),sQuery(id+"F6.wireOp",EDGE,"E1326"),sQuery(id+"F6.wireOp",EDGE,"E1327"),sQuery(id+"F6.wireOp",EDGE,"E1328"),sQuery(id+"F6.wireOp",EDGE,"E1329"),sQuery(id+"F6.wireOp",EDGE,"E1330"),sQuery(id+"F6.wireOp",EDGE,"E1331"),sQuery(id+"F6.wireOp",EDGE,"E1332"),sQuery(id+"F6.wireOp",EDGE,"E1333"),sQuery(id+"F6.wireOp",EDGE,"E1334"),sQuery(id+"F6.wireOp",EDGE,"E1335"),sQuery(id+"F6.wireOp",EDGE,"E1336"),sQuery(id+"F6.wireOp",EDGE,"E1337"),sQuery(id+"F6.wireOp",EDGE,"E1338"),sQuery(id+"F6.wireOp",EDGE,"E1339"),sQuery(id+"F6.wireOp",EDGE,"E1340"),sQuery(id+"F6.wireOp",EDGE,"E1341"),sQuery(id+"F6.wireOp",EDGE,"E1342"),sQuery(id+"F6.wireOp",EDGE,"E1343"),sQuery(id+"F6.wireOp",EDGE,"E1344"),sQuery(id+"F6.wireOp",EDGE,"E1345"),sQuery(id+"F6.wireOp",EDGE,"E1346"),sQuery(id+"F6.wireOp",EDGE,"E1347"),sQuery(id+"F6.wireOp",EDGE,"E1348"),sQuery(id+"F6.wireOp",EDGE,"E1349"),sQuery(id+"F6.wireOp",EDGE,"E1350"),sQuery(id+"F6.wireOp",EDGE,"E1351"),sQuery(id+"F6.wireOp",EDGE,"E1352"),sQuery(id+"F6.wireOp",EDGE,"E1353"),sQuery(id+"F6.wireOp",EDGE,"E1354"),sQuery(id+"F6.wireOp",EDGE,"E1355"),sQuery(id+"F6.wireOp",EDGE,"E1356"),sQuery(id+"F6.wireOp",EDGE,"E1357"),sQuery(id+"F6.wireOp",EDGE,"E1358"),sQuery(id+"F6.wireOp",EDGE,"E1359"),sQuery(id+"F6.wireOp",EDGE,"E1360"),sQuery(id+"F6.wireOp",EDGE,"E1361"),sQuery(id+"F6.wireOp",EDGE,"E1362"),sQuery(id+"F6.wireOp",EDGE,"E1363"),sQuery(id+"F6.wireOp",EDGE,"E1364"),sQuery(id+"F6.wireOp",EDGE,"E1365"),sQuery(id+"F6.wireOp",EDGE,"E1366"),sQuery(id+"F6.wireOp",EDGE,"E1367"),sQuery(id+"F6.wireOp",EDGE,"E1368"),sQuery(id+"F6.wireOp",EDGE,"E1369"),sQuery(id+"F6.wireOp",EDGE,"E1370"),sQuery(id+"F6.wireOp",EDGE,"E1371"),sQuery(id+"F6.wireOp",EDGE,"E1372"),sQuery(id+"F6.wireOp",EDGE,"E1373"),sQuery(id+"F6.wireOp",EDGE,"E1374"),sQuery(id+"F6.wireOp",EDGE,"E1375"),sQuery(id+"F6.wireOp",EDGE,"E1376"),sQuery(id+"F6.wireOp",EDGE,"E1377"),sQuery(id+"F6.wireOp",EDGE,"E1378"),sQuery(id+"F6.wireOp",EDGE,"E1379"),sQuery(id+"F6.wireOp",EDGE,"E1380"),sQuery(id+"F6.wireOp",EDGE,"E1381"),sQuery(id+"F6.wireOp",EDGE,"E1382"),sQuery(id+"F6.wireOp",EDGE,"E1383"),sQuery(id+"F6.wireOp",EDGE,"E1384"),sQuery(id+"F6.wireOp",EDGE,"E1385"),sQuery(id+"F6.wireOp",EDGE,"E1386"),sQuery(id+"F6.wireOp",EDGE,"E1387"),sQuery(id+"F6.wireOp",EDGE,"E1388"),sQuery(id+"F6.wireOp",EDGE,"E1389"),sQuery(id+"F6.wireOp",EDGE,"E1390"),sQuery(id+"F6.wireOp",EDGE,"E1391"),sQuery(id+"F6.wireOp",EDGE,"E1392"),sQuery(id+"F6.wireOp",EDGE,"E1393"),sQuery(id+"F6.wireOp",EDGE,"E1394"),sQuery(id+"F6.wireOp",EDGE,"E1395"),sQuery(id+"F6.wireOp",EDGE,"E1396"),sQuery(id+"F6.wireOp",EDGE,"E1397"),sQuery(id+"F6.wireOp",EDGE,"E1398"),sQuery(id+"F6.wireOp",EDGE,"E1399"),sQuery(id+"F6.wireOp",EDGE,"E1400"),sQuery(id+"F6.wireOp",EDGE,"E1401"),sQuery(id+"F6.wireOp",EDGE,"E1402"),sQuery(id+"F6.wireOp",EDGE,"E1403"),sQuery(id+"F6.wireOp",EDGE,"E1404"),sQuery(id+"F6.wireOp",EDGE,"E1405"),sQuery(id+"F6.wireOp",EDGE,"E1406"),sQuery(id+"F6.wireOp",EDGE,"E1407"),sQuery(id+"F6.wireOp",EDGE,"E1408"),sQuery(id+"F6.wireOp",EDGE,"E1409"),sQuery(id+"F6.wireOp",EDGE,"E1410"),sQuery(id+"F6.wireOp",EDGE,"E1411"),sQuery(id+"F6.wireOp",EDGE,"E1412"),sQuery(id+"F6.wireOp",EDGE,"E1413"),sQuery(id+"F6.wireOp",EDGE,"E1414"),sQuery(id+"F6.wireOp",EDGE,"E1415"),sQuery(id+"F6.wireOp",EDGE,"E1416"),sQuery(id+"F6.wireOp",EDGE,"E1417"),sQuery(id+"F6.wireOp",EDGE,"E1418"),sQuery(id+"F6.wireOp",EDGE,"E1419"),sQuery(id+"F6.wireOp",EDGE,"E1420"),sQuery(id+"F6.wireOp",EDGE,"E1421"),sQuery(id+"F6.wireOp",EDGE,"E1422"),sQuery(id+"F6.wireOp",EDGE,"E1423"),sQuery(id+"F6.wireOp",EDGE,"E1424"),sQuery(id+"F6.wireOp",EDGE,"E1425"),sQuery(id+"F6.wireOp",EDGE,"E1426"),sQuery(id+"F6.wireOp",EDGE,"E1427"),sQuery(id+"F6.wireOp",EDGE,"E1428"),sQuery(id+"F6.wireOp",EDGE,"E1429"),sQuery(id+"F6.wireOp",EDGE,"E1430"),sQuery(id+"F6.wireOp",EDGE,"E1431"),sQuery(id+"F6.wireOp",EDGE,"E1432"),sQuery(id+"F6.wireOp",EDGE,"E1433"),sQuery(id+"F6.wireOp",EDGE,"E1434"),sQuery(id+"F6.wireOp",EDGE,"E1435"),sQuery(id+"F6.wireOp",EDGE,"E1436"),sQuery(id+"F6.wireOp",EDGE,"E1437"),sQuery(id+"F6.wireOp",EDGE,"E1438"),sQuery(id+"F6.wireOp",EDGE,"E1439"),sQuery(id+"F6.wireOp",EDGE,"E1440"),sQuery(id+"F6.wireOp",EDGE,"E1441"),sQuery(id+"F6.wireOp",EDGE,"E1442"),sQuery(id+"F6.wireOp",EDGE,"E1443"),sQuery(id+"F6.wireOp",EDGE,"E1444"),sQuery(id+"F6.wireOp",EDGE,"E1445"),sQuery(id+"F6.wireOp",EDGE,"E1446"),sQuery(id+"F6.wireOp",EDGE,"E1447"),sQuery(id+"F6.wireOp",EDGE,"E1448"),sQuery(id+"F6.wireOp",EDGE,"E1449"),sQuery(id+"F6.wireOp",EDGE,"E1450"),sQuery(id+"F6.wireOp",EDGE,"E1451"),sQuery(id+"F6.wireOp",EDGE,"E1452"),sQuery(id+"F6.wireOp",EDGE,"E1453"),sQuery(id+"F6.wireOp",EDGE,"E1454"),sQuery(id+"F6.wireOp",EDGE,"E1455"),sQuery(id+"F6.wireOp",EDGE,"E1456"),sQuery(id+"F6.wireOp",EDGE,"E1457"),sQuery(id+"F6.wireOp",EDGE,"E1458"),sQuery(id+"F6.wireOp",EDGE,"E1459"),sQuery(id+"F6.wireOp",EDGE,"E1460"),sQuery(id+"F6.wireOp",EDGE,"E1461"),sQuery(id+"F6.wireOp",EDGE,"E1462"),sQuery(id+"F6.wireOp",EDGE,"E1463"),sQuery(id+"F6.wireOp",EDGE,"E1464"),sQuery(id+"F6.wireOp",EDGE,"E1465"),sQuery(id+"F6.wireOp",EDGE,"E1466"),sQuery(id+"F6.wireOp",EDGE,"E1467"),sQuery(id+"F6.wireOp",EDGE,"E1468"),sQuery(id+"F6.wireOp",EDGE,"E1469"),sQuery(id+"F6.wireOp",EDGE,"E1470"),sQuery(id+"F6.wireOp",EDGE,"E1471"),sQuery(id+"F6.wireOp",EDGE,"E1472"),sQuery(id+"F6.wireOp",EDGE,"E1473"),sQuery(id+"F6.wireOp",EDGE,"E1474"),sQuery(id+"F6.wireOp",EDGE,"E1475"),sQuery(id+"F6.wireOp",EDGE,"E1476"),sQuery(id+"F6.wireOp",EDGE,"E1477"),sQuery(id+"F6.wireOp",EDGE,"E1478"),sQuery(id+"F6.wireOp",EDGE,"E1479"),sQuery(id+"F6.wireOp",EDGE,"E1480"),sQuery(id+"F6.wireOp",EDGE,"E1481"),sQuery(id+"F6.wireOp",EDGE,"E1482"),sQuery(id+"F6.wireOp",EDGE,"E1483"),sQuery(id+"F6.wireOp",EDGE,"E1484"),sQuery(id+"F6.wireOp",EDGE,"E1485"),sQuery(id+"F6.wireOp",EDGE,"E1486"),sQuery(id+"F6.wireOp",EDGE,"E1487"),sQuery(id+"F6.wireOp",EDGE,"E1488"),sQuery(id+"F6.wireOp",EDGE,"E1489"),sQuery(id+"F6.wireOp",EDGE,"E1490"),sQuery(id+"F6.wireOp",EDGE,"E1491"),sQuery(id+"F6.wireOp",EDGE,"E1492"),sQuery(id+"F6.wireOp",EDGE,"E1493"),sQuery(id+"F6.wireOp",EDGE,"E1494"),sQuery(id+"F6.wireOp",EDGE,"E1495"),sQuery(id+"F6.wireOp",EDGE,"E1496"),sQuery(id+"F6.wireOp",EDGE,"E1497"),sQuery(id+"F6.wireOp",EDGE,"E1498"),sQuery(id+"F6.wireOp",EDGE,"E1499"),sQuery(id+"F6.wireOp",EDGE,"E1500"),sQuery(id+"F6.wireOp",EDGE,"E1501"),sQuery(id+"F6.wireOp",EDGE,"E1502"),sQuery(id+"F6.wireOp",EDGE,"E1503"),sQuery(id+"F6.wireOp",EDGE,"E1504"),sQuery(id+"F6.wireOp",EDGE,"E1505"),sQuery(id+"F6.wireOp",EDGE,"E1506"),sQuery(id+"F6.wireOp",EDGE,"E1507"),sQuery(id+"F6.wireOp",EDGE,"E1508"),sQuery(id+"F6.wireOp",EDGE,"E1509"),sQuery(id+"F6.wireOp",EDGE,"E1510"),sQuery(id+"F6.wireOp",EDGE,"E1511"),sQuery(id+"F6.wireOp",EDGE,"E1512"),sQuery(id+"F6.wireOp",EDGE,"E1513"),sQuery(id+"F6.wireOp",EDGE,"E1514"),sQuery(id+"F6.wireOp",EDGE,"E1515"),sQuery(id+"F6.wireOp",EDGE,"E1516"),sQuery(id+"F6.wireOp",EDGE,"E1517"),sQuery(id+"F6.wireOp",EDGE,"E1518"),sQuery(id+"F6.wireOp",EDGE,"E1519"),sQuery(id+"F6.wireOp",EDGE,"E1520"),sQuery(id+"F6.wireOp",EDGE,"E1521"),sQuery(id+"F6.wireOp",EDGE,"E1522"),sQuery(id+"F6.wireOp",EDGE,"E1523"),sQuery(id+"F6.wireOp",EDGE,"E1524"),sQuery(id+"F6.wireOp",EDGE,"E1525"),sQuery(id+"F6.wireOp",EDGE,"E1526"),sQuery(id+"F6.wireOp",EDGE,"E1527"),sQuery(id+"F6.wireOp",EDGE,"E1528"),sQuery(id+"F6.wireOp",EDGE,"E1529"),sQuery(id+"F6.wireOp",EDGE,"E1530"),sQuery(id+"F6.wireOp",EDGE,"E1531"),sQuery(id+"F6.wireOp",EDGE,"E1532"),sQuery(id+"F6.wireOp",EDGE,"E1533"),sQuery(id+"F6.wireOp",EDGE,"E1534"),sQuery(id+"F6.wireOp",EDGE,"E1535"),sQuery(id+"F6.wireOp",EDGE,"E1536"),sQuery(id+"F6.wireOp",EDGE,"E1537"),sQuery(id+"F6.wireOp",EDGE,"E1538"),sQuery(id+"F6.wireOp",EDGE,"E1539"),sQuery(id+"F6.wireOp",EDGE,"E1540"),sQuery(id+"F6.wireOp",EDGE,"E1541"),sQuery(id+"F6.wireOp",EDGE,"E1542"),sQuery(id+"F6.wireOp",EDGE,"E1543"),sQuery(id+"F6.wireOp",EDGE,"E1544"),sQuery(id+"F6.wireOp",EDGE,"E1545"),sQuery(id+"F6.wireOp",EDGE,"E1546"),sQuery(id+"F6.wireOp",EDGE,"E1547"),sQuery(id+"F6.wireOp",EDGE,"E1548"),sQuery(id+"F6.wireOp",EDGE,"E1549"),sQuery(id+"F6.wireOp",EDGE,"E1550"),sQuery(id+"F6.wireOp",EDGE,"E1551"),sQuery(id+"F6.wireOp",EDGE,"E1552"),sQuery(id+"F6.wireOp",EDGE,"E1553"),sQuery(id+"F6.wireOp",EDGE,"E1554"),sQuery(id+"F6.wireOp",EDGE,"E1555"),sQuery(id+"F6.wireOp",EDGE,"E1556"),sQuery(id+"F6.wireOp",EDGE,"E1557"),sQuery(id+"F6.wireOp",EDGE,"E1558"),sQuery(id+"F6.wireOp",EDGE,"E1559"),sQuery(id+"F6.wireOp",EDGE,"E1560"),sQuery(id+"F6.wireOp",EDGE,"E1561"),sQuery(id+"F6.wireOp",EDGE,"E1562"),sQuery(id+"F6.wireOp",EDGE,"E1563"),sQuery(id+"F6.wireOp",EDGE,"E1564"),sQuery(id+"F6.wireOp",EDGE,"E1565"),sQuery(id+"F6.wireOp",EDGE,"E1566"),sQuery(id+"F6.wireOp",EDGE,"E1567"),sQuery(id+"F6.wireOp",EDGE,"E1568"),sQuery(id+"F6.wireOp",EDGE,"E1569"),sQuery(id+"F6.wireOp",EDGE,"E1570"),sQuery(id+"F6.wireOp",EDGE,"E1571"),sQuery(id+"F6.wireOp",EDGE,"E1572"),sQuery(id+"F6.wireOp",EDGE,"E1573"),sQuery(id+"F6.wireOp",EDGE,"E1574"),sQuery(id+"F6.wireOp",EDGE,"E1575"),sQuery(id+"F6.wireOp",EDGE,"E1576"),sQuery(id+"F6.wireOp",EDGE,"E1577"),sQuery(id+"F6.wireOp",EDGE,"E1578"),sQuery(id+"F6.wireOp",EDGE,"E1579"),sQuery(id+"F6.wireOp",EDGE,"E1580"),sQuery(id+"F6.wireOp",EDGE,"E1581"),sQuery(id+"F6.wireOp",EDGE,"E1582"),sQuery(id+"F6.wireOp",EDGE,"E1583"),sQuery(id+"F6.wireOp",EDGE,"E1584"),sQuery(id+"F6.wireOp",EDGE,"E1585"),sQuery(id+"F6.wireOp",EDGE,"E1586"),sQuery(id+"F6.wireOp",EDGE,"E1587"),sQuery(id+"F6.wireOp",EDGE,"E1588"),sQuery(id+"F6.wireOp",EDGE,"E1589"),sQuery(id+"F6.wireOp",EDGE,"E1590"),sQuery(id+"F6.wireOp",EDGE,"E1591"),sQuery(id+"F6.wireOp",EDGE,"E1592"),sQuery(id+"F6.wireOp",EDGE,"E1593"),sQuery(id+"F6.wireOp",EDGE,"E1594"),sQuery(id+"F6.wireOp",EDGE,"E1595"),sQuery(id+"F6.wireOp",EDGE,"E1596"),sQuery(id+"F6.wireOp",EDGE,"E1597"),sQuery(id+"F6.wireOp",EDGE,"E1598"),sQuery(id+"F6.wireOp",EDGE,"E1599"),sQuery(id+"F6.wireOp",EDGE,"E1600"),sQuery(id+"F6.wireOp",EDGE,"E1601"),sQuery(id+"F6.wireOp",EDGE,"E1602"),sQuery(id+"F6.wireOp",EDGE,"E1603"),sQuery(id+"F6.wireOp",EDGE,"E1604"),sQuery(id+"F6.wireOp",EDGE,"E1605"),sQuery(id+"F6.wireOp",EDGE,"E1606"),sQuery(id+"F6.wireOp",EDGE,"E1607"),sQuery(id+"F6.wireOp",EDGE,"E1608"),sQuery(id+"F6.wireOp",EDGE,"E1609"),sQuery(id+"F6.wireOp",EDGE,"E1610"),sQuery(id+"F6.wireOp",EDGE,"E1611"),sQuery(id+"F6.wireOp",EDGE,"E1612"),sQuery(id+"F6.wireOp",EDGE,"E1613"),sQuery(id+"F6.wireOp",EDGE,"E1614"),sQuery(id+"F6.wireOp",EDGE,"E1615"),sQuery(id+"F6.wireOp",EDGE,"E1616"),sQuery(id+"F6.wireOp",EDGE,"E1617"),sQuery(id+"F6.wireOp",EDGE,"E1618"),sQuery(id+"F6.wireOp",EDGE,"E1619"),sQuery(id+"F6.wireOp",EDGE,"E1620"),sQuery(id+"F6.wireOp",EDGE,"E1621"),sQuery(id+"F6.wireOp",EDGE,"E1622"),sQuery(id+"F6.wireOp",EDGE,"E1623"),sQuery(id+"F6.wireOp",EDGE,"E1624"),sQuery(id+"F6.wireOp",EDGE,"E1625"),sQuery(id+"F6.wireOp",EDGE,"E1626"),sQuery(id+"F6.wireOp",EDGE,"E1627"),sQuery(id+"F6.wireOp",EDGE,"E1628"),sQuery(id+"F6.wireOp",EDGE,"E1629"),sQuery(id+"F6.wireOp",EDGE,"E1630"),sQuery(id+"F6.wireOp",EDGE,"E1631"),sQuery(id+"F6.wireOp",EDGE,"E1632"),sQuery(id+"F6.wireOp",EDGE,"E1633"),sQuery(id+"F6.wireOp",EDGE,"E1634"),sQuery(id+"F6.wireOp",EDGE,"E1635"),sQuery(id+"F6.wireOp",EDGE,"E1636"),sQuery(id+"F6.wireOp",EDGE,"E1637"),sQuery(id+"F6.wireOp",EDGE,"E1638"),sQuery(id+"F6.wireOp",EDGE,"E1639"),sQuery(id+"F6.wireOp",EDGE,"E1640"),sQuery(id+"F6.wireOp",EDGE,"E1641"),sQuery(id+"F6.wireOp",EDGE,"E1642"),sQuery(id+"F6.wireOp",EDGE,"E1643"),sQuery(id+"F6.wireOp",EDGE,"E1644"),sQuery(id+"F6.wireOp",EDGE,"E1645"),sQuery(id+"F6.wireOp",EDGE,"E1646"),sQuery(id+"F6.wireOp",EDGE,"E1647"),sQuery(id+"F6.wireOp",EDGE,"E1648"),sQuery(id+"F6.wireOp",EDGE,"E1649"),sQuery(id+"F6.wireOp",EDGE,"E1650"),sQuery(id+"F6.wireOp",EDGE,"E1651"),sQuery(id+"F6.wireOp",EDGE,"E1652"),sQuery(id+"F6.wireOp",EDGE,"E1653"),sQuery(id+"F6.wireOp",EDGE,"E1654"),sQuery(id+"F6.wireOp",EDGE,"E1655"),sQuery(id+"F6.wireOp",EDGE,"E1656"),sQuery(id+"F6.wireOp",EDGE,"E1657"),sQuery(id+"F6.wireOp",EDGE,"E1658"),sQuery(id+"F6.wireOp",EDGE,"E1659"),sQuery(id+"F6.wireOp",EDGE,"E1660"),sQuery(id+"F6.wireOp",EDGE,"E1661"),sQuery(id+"F6.wireOp",EDGE,"E1662"),sQuery(id+"F6.wireOp",EDGE,"E1663"),sQuery(id+"F6.wireOp",EDGE,"E1664"),sQuery(id+"F6.wireOp",EDGE,"E1665"),sQuery(id+"F6.wireOp",EDGE,"E1666"),sQuery(id+"F6.wireOp",EDGE,"E1667"),sQuery(id+"F6.wireOp",EDGE,"E1668"),sQuery(id+"F6.wireOp",EDGE,"E1669"),sQuery(id+"F6.wireOp",EDGE,"E1670"),sQuery(id+"F6.wireOp",EDGE,"E1671"),sQuery(id+"F6.wireOp",EDGE,"E1672"),sQuery(id+"F6.wireOp",EDGE,"E1673"),sQuery(id+"F6.wireOp",EDGE,"E1674"),sQuery(id+"F6.wireOp",EDGE,"E1675"),sQuery(id+"F6.wireOp",EDGE,"E1676"),sQuery(id+"F6.wireOp",EDGE,"E1677"),sQuery(id+"F6.wireOp",EDGE,"E1678"),sQuery(id+"F6.wireOp",EDGE,"E1679"),sQuery(id+"F6.wireOp",EDGE,"E1680"),sQuery(id+"F6.wireOp",EDGE,"E1681"),sQuery(id+"F6.wireOp",EDGE,"E1682"),sQuery(id+"F6.wireOp",EDGE,"E1683"),sQuery(id+"F6.wireOp",EDGE,"E1684"),sQuery(id+"F6.wireOp",EDGE,"E1685"),sQuery(id+"F6.wireOp",EDGE,"E1686"),sQuery(id+"F6.wireOp",EDGE,"E1687"),sQuery(id+"F6.wireOp",EDGE,"E1688"),sQuery(id+"F6.wireOp",EDGE,"E1689"),sQuery(id+"F6.wireOp",EDGE,"E1690"),sQuery(id+"F6.wireOp",EDGE,"E1691"),sQuery(id+"F6.wireOp",EDGE,"E1692"),sQuery(id+"F6.wireOp",EDGE,"E1693"),sQuery(id+"F6.wireOp",EDGE,"E1694"),sQuery(id+"F6.wireOp",EDGE,"E1695"),sQuery(id+"F6.wireOp",EDGE,"E1696"),sQuery(id+"F6.wireOp",EDGE,"E1697"),sQuery(id+"F6.wireOp",EDGE,"E1698"),sQuery(id+"F6.wireOp",EDGE,"E1699"),sQuery(id+"F6.wireOp",EDGE,"E1700"),sQuery(id+"F6.wireOp",EDGE,"E1701"),sQuery(id+"F6.wireOp",EDGE,"E1702"),sQuery(id+"F6.wireOp",EDGE,"E1703"),sQuery(id+"F6.wireOp",EDGE,"E1704"),sQuery(id+"F6.wireOp",EDGE,"E1705"),sQuery(id+"F6.wireOp",EDGE,"E1706"),sQuery(id+"F6.wireOp",EDGE,"E1707"),sQuery(id+"F6.wireOp",EDGE,"E1708"),sQuery(id+"F6.wireOp",EDGE,"E1709"),sQuery(id+"F6.wireOp",EDGE,"E1710"),sQuery(id+"F6.wireOp",EDGE,"E1711"),sQuery(id+"F6.wireOp",EDGE,"E1712"),sQuery(id+"F6.wireOp",EDGE,"E1713"),sQuery(id+"F6.wireOp",EDGE,"E1714"),sQuery(id+"F6.wireOp",EDGE,"E1715"),sQuery(id+"F6.wireOp",EDGE,"E1716"),sQuery(id+"F6.wireOp",EDGE,"E1717"),sQuery(id+"F6.wireOp",EDGE,"E1718"),sQuery(id+"F6.wireOp",EDGE,"E1719"),sQuery(id+"F6.wireOp",EDGE,"E1720"),sQuery(id+"F6.wireOp",EDGE,"E1721"),sQuery(id+"F6.wireOp",EDGE,"E1722"),sQuery(id+"F6.wireOp",EDGE,"E1723"),sQuery(id+"F6.wireOp",EDGE,"E1724"),sQuery(id+"F6.wireOp",EDGE,"E1725"),sQuery(id+"F6.wireOp",EDGE,"E1726"),sQuery(id+"F6.wireOp",EDGE,"E1727"),sQuery(id+"F6.wireOp",EDGE,"E1728"),sQuery(id+"F6.wireOp",EDGE,"E1729"),sQuery(id+"F6.wireOp",EDGE,"E1730"),sQuery(id+"F6.wireOp",EDGE,"E1731"),sQuery(id+"F6.wireOp",EDGE,"E1732"),sQuery(id+"F6.wireOp",EDGE,"E1733"),sQuery(id+"F6.wireOp",EDGE,"E1734"),sQuery(id+"F6.wireOp",EDGE,"E1735"),sQuery(id+"F6.wireOp",EDGE,"E1736"),sQuery(id+"F6.wireOp",EDGE,"E1737"),sQuery(id+"F6.wireOp",EDGE,"E1738"),sQuery(id+"F6.wireOp",EDGE,"E1739"),sQuery(id+"F6.wireOp",EDGE,"E1740"),sQuery(id+"F6.wireOp",EDGE,"E1741"),sQuery(id+"F6.wireOp",EDGE,"E1742"),sQuery(id+"F6.wireOp",EDGE,"E1743"),sQuery(id+"F6.wireOp",EDGE,"E1744"),sQuery(id+"F6.wireOp",EDGE,"E1745"),sQuery(id+"F6.wireOp",EDGE,"E1746"),sQuery(id+"F6.wireOp",EDGE,"E1747"),sQuery(id+"F6.wireOp",EDGE,"E1748"),sQuery(id+"F6.wireOp",EDGE,"E1749"),sQuery(id+"F6.wireOp",EDGE,"E1750"),sQuery(id+"F6.wireOp",EDGE,"E1751"),sQuery(id+"F6.wireOp",EDGE,"E1752"),sQuery(id+"F6.wireOp",EDGE,"E1753"),sQuery(id+"F6.wireOp",EDGE,"E1754"),sQuery(id+"F6.wireOp",EDGE,"E1755"),sQuery(id+"F6.wireOp",EDGE,"E1756"),sQuery(id+"F6.wireOp",EDGE,"E1757"),sQuery(id+"F6.wireOp",EDGE,"E1758"),sQuery(id+"F6.wireOp",EDGE,"E1759"),sQuery(id+"F6.wireOp",EDGE,"E1760"),sQuery(id+"F6.wireOp",EDGE,"E1761"),sQuery(id+"F6.wireOp",EDGE,"E1762"),sQuery(id+"F6.wireOp",EDGE,"E1763"),sQuery(id+"F6.wireOp",EDGE,"E1764"),sQuery(id+"F6.wireOp",EDGE,"E1765"),sQuery(id+"F6.wireOp",EDGE,"E1766"),sQuery(id+"F6.wireOp",EDGE,"E1767"),sQuery(id+"F6.wireOp",EDGE,"E1768"),sQuery(id+"F6.wireOp",EDGE,"E1769"),sQuery(id+"F6.wireOp",EDGE,"E1770"),sQuery(id+"F6.wireOp",EDGE,"E1771"),sQuery(id+"F6.wireOp",EDGE,"E1772"),sQuery(id+"F6.wireOp",EDGE,"E1773"),sQuery(id+"F6.wireOp",EDGE,"E1774"),sQuery(id+"F6.wireOp",EDGE,"E1775"),sQuery(id+"F6.wireOp",EDGE,"E1776"),sQuery(id+"F6.wireOp",EDGE,"E1777"),sQuery(id+"F6.wireOp",EDGE,"E1778"),sQuery(id+"F6.wireOp",EDGE,"E1779"),sQuery(id+"F6.wireOp",EDGE,"E1780"),sQuery(id+"F6.wireOp",EDGE,"E1781"),sQuery(id+"F6.wireOp",EDGE,"E1782"),sQuery(id+"F6.wireOp",EDGE,"E1783"),sQuery(id+"F6.wireOp",EDGE,"E1784"),sQuery(id+"F6.wireOp",EDGE,"E1785"),sQuery(id+"F6.wireOp",EDGE,"E1786"),sQuery(id+"F6.wireOp",EDGE,"E1787"),sQuery(id+"F6.wireOp",EDGE,"E1788"),sQuery(id+"F6.wireOp",EDGE,"E1789"),sQuery(id+"F6.wireOp",EDGE,"E1790"),sQuery(id+"F6.wireOp",EDGE,"E1791"),sQuery(id+"F6.wireOp",EDGE,"E1792"),sQuery(id+"F6.wireOp",EDGE,"E1793"),sQuery(id+"F6.wireOp",EDGE,"E1794"),sQuery(id+"F6.wireOp",EDGE,"E1795"),sQuery(id+"F6.wireOp",EDGE,"E1796"),sQuery(id+"F6.wireOp",EDGE,"E1797"),sQuery(id+"F6.wireOp",EDGE,"E1798"),sQuery(id+"F6.wireOp",EDGE,"E1799"),sQuery(id+"F6.wireOp",EDGE,"E1800"),sQuery(id+"F6.wireOp",EDGE,"E1801"),sQuery(id+"F6.wireOp",EDGE,"E1802"),sQuery(id+"F6.wireOp",EDGE,"E1803"),sQuery(id+"F6.wireOp",EDGE,"E1804"),sQuery(id+"F6.wireOp",EDGE,"E1805"),sQuery(id+"F6.wireOp",EDGE,"E1806"),sQuery(id+"F6.wireOp",EDGE,"E1807"),sQuery(id+"F6.wireOp",EDGE,"E1808"),sQuery(id+"F6.wireOp",EDGE,"E1809"),sQuery(id+"F6.wireOp",EDGE,"E1810"),sQuery(id+"F6.wireOp",EDGE,"E1811"),sQuery(id+"F6.wireOp",EDGE,"E1812"),sQuery(id+"F6.wireOp",EDGE,"E1813"),sQuery(id+"F6.wireOp",EDGE,"E1814"),sQuery(id+"F6.wireOp",EDGE,"E1815"),sQuery(id+"F6.wireOp",EDGE,"E1816"),sQuery(id+"F6.wireOp",EDGE,"E1817"),sQuery(id+"F6.wireOp",EDGE,"E1818"),sQuery(id+"F6.wireOp",EDGE,"E1819"),sQuery(id+"F6.wireOp",EDGE,"E1820"),sQuery(id+"F6.wireOp",EDGE,"E1821"),sQuery(id+"F6.wireOp",EDGE,"E1822"),sQuery(id+"F6.wireOp",EDGE,"E1823"),sQuery(id+"F6.wireOp",EDGE,"E1824"),sQuery(id+"F6.wireOp",EDGE,"E1825"),sQuery(id+"F6.wireOp",EDGE,"E1826"),sQuery(id+"F6.wireOp",EDGE,"E1827"),sQuery(id+"F6.wireOp",EDGE,"E1828"),sQuery(id+"F6.wireOp",EDGE,"E1829"),sQuery(id+"F6.wireOp",EDGE,"E1830"),sQuery(id+"F6.wireOp",EDGE,"E1831"),sQuery(id+"F6.wireOp",EDGE,"E1832"),sQuery(id+"F6.wireOp",EDGE,"E1833"),sQuery(id+"F6.wireOp",EDGE,"E1834"),sQuery(id+"F6.wireOp",EDGE,"E1835"),sQuery(id+"F6.wireOp",EDGE,"E1836"),sQuery(id+"F6.wireOp",EDGE,"E1837"),sQuery(id+"F6.wireOp",EDGE,"E1838"),sQuery(id+"F6.wireOp",EDGE,"E1839"),sQuery(id+"F6.wireOp",EDGE,"E1840"),sQuery(id+"F6.wireOp",EDGE,"E1841"),sQuery(id+"F6.wireOp",EDGE,"E1842"),sQuery(id+"F6.wireOp",EDGE,"E1843"),sQuery(id+"F6.wireOp",EDGE,"E1844"),sQuery(id+"F6.wireOp",EDGE,"E1845"),sQuery(id+"F6.wireOp",EDGE,"E1846"),sQuery(id+"F6.wireOp",EDGE,"E1847"),sQuery(id+"F6.wireOp",EDGE,"E1848"),sQuery(id+"F6.wireOp",EDGE,"E1849"),sQuery(id+"F6.wireOp",EDGE,"E1850"),sQuery(id+"F6.wireOp",EDGE,"E1851"),sQuery(id+"F6.wireOp",EDGE,"E1852"),sQuery(id+"F6.wireOp",EDGE,"E1853"),sQuery(id+"F6.wireOp",EDGE,"E1854"),sQuery(id+"F6.wireOp",EDGE,"E1855"),sQuery(id+"F6.wireOp",EDGE,"E1856"),sQuery(id+"F6.wireOp",EDGE,"E1857"),sQuery(id+"F6.wireOp",EDGE,"E1858"),sQuery(id+"F6.wireOp",EDGE,"E1859"),sQuery(id+"F6.wireOp",EDGE,"E1860"),sQuery(id+"F6.wireOp",EDGE,"E1861"),sQuery(id+"F6.wireOp",EDGE,"E1862"),sQuery(id+"F6.wireOp",EDGE,"E1863"),sQuery(id+"F6.wireOp",EDGE,"E1864"),sQuery(id+"F6.wireOp",EDGE,"E1865"),sQuery(id+"F6.wireOp",EDGE,"E1866"),sQuery(id+"F6.wireOp",EDGE,"E1867"),sQuery(id+"F6.wireOp",EDGE,"E1868"),sQuery(id+"F6.wireOp",EDGE,"E1869"),sQuery(id+"F6.wireOp",EDGE,"E1870"),sQuery(id+"F6.wireOp",EDGE,"E1871"),sQuery(id+"F6.wireOp",EDGE,"E1872"),sQuery(id+"F6.wireOp",EDGE,"E1873"),sQuery(id+"F6.wireOp",EDGE,"E1874"),sQuery(id+"F6.wireOp",EDGE,"E1875"),sQuery(id+"F6.wireOp",EDGE,"E1876"),sQuery(id+"F6.wireOp",EDGE,"E1877"),sQuery(id+"F6.wireOp",EDGE,"E1878"),sQuery(id+"F6.wireOp",EDGE,"E1879"),sQuery(id+"F6.wireOp",EDGE,"E1880"),sQuery(id+"F6.wireOp",EDGE,"E1881"),sQuery(id+"F6.wireOp",EDGE,"E1882"),sQuery(id+"F6.wireOp",EDGE,"E1883"),sQuery(id+"F6.wireOp",EDGE,"E1884"),sQuery(id+"F6.wireOp",EDGE,"E1885"),sQuery(id+"F6.wireOp",EDGE,"E1886"),sQuery(id+"F6.wireOp",EDGE,"E1887"),sQuery(id+"F6.wireOp",EDGE,"E1888"),sQuery(id+"F6.wireOp",EDGE,"E1889"),sQuery(id+"F6.wireOp",EDGE,"E1890"),sQuery(id+"F6.wireOp",EDGE,"E1891"),sQuery(id+"F6.wireOp",EDGE,"E1892"),sQuery(id+"F6.wireOp",EDGE,"E1893"),sQuery(id+"F6.wireOp",EDGE,"E1894"),sQuery(id+"F6.wireOp",EDGE,"E1895"),sQuery(id+"F6.wireOp",EDGE,"E1896"),sQuery(id+"F6.wireOp",EDGE,"E1897"),sQuery(id+"F6.wireOp",EDGE,"E1898"),sQuery(id+"F6.wireOp",EDGE,"E1899"),sQuery(id+"F6.wireOp",EDGE,"E1900"),sQuery(id+"F6.wireOp",EDGE,"E1901"),sQuery(id+"F6.wireOp",EDGE,"E1902"),sQuery(id+"F6.wireOp",EDGE,"E1903"),sQuery(id+"F6.wireOp",EDGE,"E1904"),sQuery(id+"F6.wireOp",EDGE,"E1905"),sQuery(id+"F6.wireOp",EDGE,"E1906"),sQuery(id+"F6.wireOp",EDGE,"E1907"),sQuery(id+"F6.wireOp",EDGE,"E1908"),sQuery(id+"F6.wireOp",EDGE,"E1909"),sQuery(id+"F6.wireOp",EDGE,"E1910"),sQuery(id+"F6.wireOp",EDGE,"E1911"),sQuery(id+"F6.wireOp",EDGE,"E1912"),sQuery(id+"F6.wireOp",EDGE,"E1913"),sQuery(id+"F6.wireOp",EDGE,"E1914"),sQuery(id+"F6.wireOp",EDGE,"E1915"),sQuery(id+"F6.wireOp",EDGE,"E1916"),sQuery(id+"F6.wireOp",EDGE,"E1917"),sQuery(id+"F6.wireOp",EDGE,"E1918"),sQuery(id+"F6.wireOp",EDGE,"E1919"),sQuery(id+"F6.wireOp",EDGE,"E1920"),sQuery(id+"F6.wireOp",EDGE,"E1921"),sQuery(id+"F6.wireOp",EDGE,"E1922"),sQuery(id+"F6.wireOp",EDGE,"E1923"),sQuery(id+"F6.wireOp",EDGE,"E1924"),sQuery(id+"F6.wireOp",EDGE,"E1925"),sQuery(id+"F6.wireOp",EDGE,"E1926"),sQuery(id+"F6.wireOp",EDGE,"E1927"),sQuery(id+"F6.wireOp",EDGE,"E1928"),sQuery(id+"F6.wireOp",EDGE,"E1929"),sQuery(id+"F6.wireOp",EDGE,"E1930"),sQuery(id+"F6.wireOp",EDGE,"E1931"),sQuery(id+"F6.wireOp",EDGE,"E1932"),sQuery(id+"F6.wireOp",EDGE,"E1933"),sQuery(id+"F6.wireOp",EDGE,"E1934"),sQuery(id+"F6.wireOp",EDGE,"E1935"),sQuery(id+"F6.wireOp",EDGE,"E1936"),sQuery(id+"F6.wireOp",EDGE,"E1937"),sQuery(id+"F6.wireOp",EDGE,"E1938"),sQuery(id+"F6.wireOp",EDGE,"E1939"),sQuery(id+"F6.wireOp",EDGE,"E1940"),sQuery(id+"F6.wireOp",EDGE,"E1941"),sQuery(id+"F6.wireOp",EDGE,"E1942"),sQuery(id+"F6.wireOp",EDGE,"E1943"),sQuery(id+"F6.wireOp",EDGE,"E1944"),sQuery(id+"F6.wireOp",EDGE,"E1945"),sQuery(id+"F6.wireOp",EDGE,"E1946"),sQuery(id+"F6.wireOp",EDGE,"E1947"),sQuery(id+"F6.wireOp",EDGE,"E1948"),sQuery(id+"F6.wireOp",EDGE,"E1949"),sQuery(id+"F6.wireOp",EDGE,"E1950"),sQuery(id+"F6.wireOp",EDGE,"E1951"),sQuery(id+"F6.wireOp",EDGE,"E1952"),sQuery(id+"F6.wireOp",EDGE,"E1953"),sQuery(id+"F6.wireOp",EDGE,"E1954"),sQuery(id+"F6.wireOp",EDGE,"E1955"),sQuery(id+"F6.wireOp",EDGE,"E1956"),sQuery(id+"F6.wireOp",EDGE,"E1957"),sQuery(id+"F6.wireOp",EDGE,"E1958"),sQuery(id+"F6.wireOp",EDGE,"E1959"),sQuery(id+"F6.wireOp",EDGE,"E1960"),sQuery(id+"F6.wireOp",EDGE,"E1961"),sQuery(id+"F6.wireOp",EDGE,"E1962"),sQuery(id+"F6.wireOp",EDGE,"E1963"),sQuery(id+"F6.wireOp",EDGE,"E1964"),sQuery(id+"F6.wireOp",EDGE,"E1965"),sQuery(id+"F6.wireOp",EDGE,"E1966"),sQuery(id+"F6.wireOp",EDGE,"E1967"),sQuery(id+"F6.wireOp",EDGE,"E1968"),sQuery(id+"F6.wireOp",EDGE,"E1969"),sQuery(id+"F6.wireOp",EDGE,"E1970"),sQuery(id+"F6.wireOp",EDGE,"E1971"),sQuery(id+"F6.wireOp",EDGE,"E1972"),sQuery(id+"F6.wireOp",EDGE,"E1973"),sQuery(id+"F6.wireOp",EDGE,"E1974"),sQuery(id+"F6.wireOp",EDGE,"E1975"),sQuery(id+"F6.wireOp",EDGE,"E1976"),sQuery(id+"F6.wireOp",EDGE,"E1977"),sQuery(id+"F6.wireOp",EDGE,"E1978"),sQuery(id+"F6.wireOp",EDGE,"E1979"),sQuery(id+"F6.wireOp",EDGE,"E1980"),sQuery(id+"F6.wireOp",EDGE,"E1981"),sQuery(id+"F6.wireOp",EDGE,"E1982"),sQuery(id+"F6.wireOp",EDGE,"E1983"),sQuery(id+"F6.wireOp",EDGE,"E1984"),sQuery(id+"F6.wireOp",EDGE,"E1985"),sQuery(id+"F6.wireOp",EDGE,"E1986"),sQuery(id+"F6.wireOp",EDGE,"E1987"),sQuery(id+"F6.wireOp",EDGE,"E1988"),sQuery(id+"F6.wireOp",EDGE,"E1989"),sQuery(id+"F6.wireOp",EDGE,"E1990"),sQuery(id+"F6.wireOp",EDGE,"E1991"),sQuery(id+"F6.wireOp",EDGE,"E1992"),sQuery(id+"F6.wireOp",EDGE,"E1993"),sQuery(id+"F6.wireOp",EDGE,"E1994"),sQuery(id+"F6.wireOp",EDGE,"E1995"),sQuery(id+"F6.wireOp",EDGE,"E1996"),sQuery(id+"F6.wireOp",EDGE,"E1997"),sQuery(id+"F6.wireOp",EDGE,"E1998"),sQuery(id+"F6.wireOp",EDGE,"E1999"),sQuery(id+"F6.wireOp",EDGE,"E2000"),sQuery(id+"F6.wireOp",EDGE,"E2001"),sQuery(id+"F6.wireOp",EDGE,"E2002"),sQuery(id+"F6.wireOp",EDGE,"E2003"),sQuery(id+"F6.wireOp",EDGE,"E2004"),sQuery(id+"F6.wireOp",EDGE,"E2005"),sQuery(id+"F6.wireOp",EDGE,"E2006"),sQuery(id+"F6.wireOp",EDGE,"E2007"),sQuery(id+"F6.wireOp",EDGE,"E2008"),sQuery(id+"F6.wireOp",EDGE,"E2009"),sQuery(id+"F6.wireOp",EDGE,"E2010"),sQuery(id+"F6.wireOp",EDGE,"E2011"),sQuery(id+"F6.wireOp",EDGE,"E2012"),sQuery(id+"F6.wireOp",EDGE,"E2013"),sQuery(id+"F6.wireOp",EDGE,"E2014"),sQuery(id+"F6.wireOp",EDGE,"E2015"),sQuery(id+"F6.wireOp",EDGE,"E2016"),sQuery(id+"F6.wireOp",EDGE,"E2017"),sQuery(id+"F6.wireOp",EDGE,"E2018"),sQuery(id+"F6.wireOp",EDGE,"E2019"),sQuery(id+"F6.wireOp",EDGE,"E2020"),sQuery(id+"F6.wireOp",EDGE,"E2021"),sQuery(id+"F6.wireOp",EDGE,"E2022"),sQuery(id+"F6.wireOp",EDGE,"E2023"),sQuery(id+"F6.wireOp",EDGE,"E2024"),sQuery(id+"F6.wireOp",EDGE,"E2025"),sQuery(id+"F6.wireOp",EDGE,"E2026"),sQuery(id+"F6.wireOp",EDGE,"E2027"),sQuery(id+"F6.wireOp",EDGE,"E2028"),sQuery(id+"F6.wireOp",EDGE,"E2029"),sQuery(id+"F6.wireOp",EDGE,"E2030"),sQuery(id+"F6.wireOp",EDGE,"E2031"),sQuery(id+"F6.wireOp",EDGE,"E2032"),sQuery(id+"F6.wireOp",EDGE,"E2033"),sQuery(id+"F6.wireOp",EDGE,"E2034"),sQuery(id+"F6.wireOp",EDGE,"E2035"),sQuery(id+"F6.wireOp",EDGE,"E2036"),sQuery(id+"F6.wireOp",EDGE,"E2037"),sQuery(id+"F6.wireOp",EDGE,"E2038"),sQuery(id+"F6.wireOp",EDGE,"E2039"),sQuery(id+"F6.wireOp",EDGE,"E2040"),sQuery(id+"F6.wireOp",EDGE,"E2041"),sQuery(id+"F6.wireOp",EDGE,"E2042"),sQuery(id+"F6.wireOp",EDGE,"E2043"),sQuery(id+"F6.wireOp",EDGE,"E2044"),sQuery(id+"F6.wireOp",EDGE,"E2045"),sQuery(id+"F6.wireOp",EDGE,"E2046"),sQuery(id+"F6.wireOp",EDGE,"E2047"),sQuery(id+"F6.wireOp",EDGE,"E2048"),sQuery(id+"F6.wireOp",EDGE,"E2049"),sQuery(id+"F6.wireOp",EDGE,"E2050"),sQuery(id+"F6.wireOp",EDGE,"E2051"),sQuery(id+"F6.wireOp",EDGE,"E2052"),sQuery(id+"F6.wireOp",EDGE,"E2053"),sQuery(id+"F6.wireOp",EDGE,"E2054"),sQuery(id+"F6.wireOp",EDGE,"E2055"),sQuery(id+"F6.wireOp",EDGE,"E2056"),sQuery(id+"F6.wireOp",EDGE,"E2057"),sQuery(id+"F6.wireOp",EDGE,"E2058"),sQuery(id+"F6.wireOp",EDGE,"E2059"),sQuery(id+"F6.wireOp",EDGE,"E2060"),sQuery(id+"F6.wireOp",EDGE,"E2061"),sQuery(id+"F6.wireOp",EDGE,"E2062"),sQuery(id+"F6.wireOp",EDGE,"E2063"),sQuery(id+"F6.wireOp",EDGE,"E2064"),sQuery(id+"F6.wireOp",EDGE,"E2065"),sQuery(id+"F6.wireOp",EDGE,"E2066"),sQuery(id+"F6.wireOp",EDGE,"E2067"),sQuery(id+"F6.wireOp",EDGE,"E2068"),sQuery(id+"F6.wireOp",EDGE,"E2069"),sQuery(id+"F6.wireOp",EDGE,"E2070"),sQuery(id+"F6.wireOp",EDGE,"E2071"),sQuery(id+"F6.wireOp",EDGE,"E2072"),sQuery(id+"F6.wireOp",EDGE,"E2073"),sQuery(id+"F6.wireOp",EDGE,"E2074"),sQuery(id+"F6.wireOp",EDGE,"E2075"),sQuery(id+"F6.wireOp",EDGE,"E2076"),sQuery(id+"F6.wireOp",EDGE,"E2077"),sQuery(id+"F6.wireOp",EDGE,"E2078"),sQuery(id+"F6.wireOp",EDGE,"E2079"),sQuery(id+"F6.wireOp",EDGE,"E2080"),sQuery(id+"F6.wireOp",EDGE,"E2081"),sQuery(id+"F6.wireOp",EDGE,"E2082"),sQuery(id+"F6.wireOp",EDGE,"E2083"),sQuery(id+"F6.wireOp",EDGE,"E2084"),sQuery(id+"F6.wireOp",EDGE,"E2085"),sQuery(id+"F6.wireOp",EDGE,"E2086"),sQuery(id+"F6.wireOp",EDGE,"E2087"),sQuery(id+"F6.wireOp",EDGE,"E2088"),sQuery(id+"F6.wireOp",EDGE,"E2089"),sQuery(id+"F6.wireOp",EDGE,"E2090"),sQuery(id+"F6.wireOp",EDGE,"E2091"),sQuery(id+"F6.wireOp",EDGE,"E2092"),sQuery(id+"F6.wireOp",EDGE,"E2093"),sQuery(id+"F6.wireOp",EDGE,"E2094"),sQuery(id+"F6.wireOp",EDGE,"E2095"),sQuery(id+"F6.wireOp",EDGE,"E2096"),sQuery(id+"F6.wireOp",EDGE,"E2097"),sQuery(id+"F6.wireOp",EDGE,"E2098"),sQuery(id+"F6.wireOp",EDGE,"E2099"),sQuery(id+"F6.wireOp",EDGE,"E2100"),sQuery(id+"F6.wireOp",EDGE,"E2101"),sQuery(id+"F6.wireOp",EDGE,"E2102"),sQuery(id+"F6.wireOp",EDGE,"E2103"),sQuery(id+"F6.wireOp",EDGE,"E2104"),sQuery(id+"F6.wireOp",EDGE,"E2105"),sQuery(id+"F6.wireOp",EDGE,"E2106"),sQuery(id+"F6.wireOp",EDGE,"E2107"),sQuery(id+"F6.wireOp",EDGE,"E2108"),sQuery(id+"F6.wireOp",EDGE,"E2109"),sQuery(id+"F6.wireOp",EDGE,"E2110"),sQuery(id+"F6.wireOp",EDGE,"E2111"),sQuery(id+"F6.wireOp",EDGE,"E2112"),sQuery(id+"F6.wireOp",EDGE,"E2113"),sQuery(id+"F6.wireOp",EDGE,"E2114"),sQuery(id+"F6.wireOp",EDGE,"E2115"),sQuery(id+"F6.wireOp",EDGE,"E2116"),sQuery(id+"F6.wireOp",EDGE,"E2117"),sQuery(id+"F6.wireOp",EDGE,"E2118"),sQuery(id+"F6.wireOp",EDGE,"E2119"),sQuery(id+"F6.wireOp",EDGE,"E2120"),sQuery(id+"F6.wireOp",EDGE,"E2121"),sQuery(id+"F6.wireOp",EDGE,"E2122"),sQuery(id+"F6.wireOp",EDGE,"E2123"),sQuery(id+"F6.wireOp",EDGE,"E2124"),sQuery(id+"F6.wireOp",EDGE,"E2125"),sQuery(id+"F6.wireOp",EDGE,"E2126"),sQuery(id+"F6.wireOp",EDGE,"E2127"),sQuery(id+"F6.wireOp",EDGE,"E2128"),sQuery(id+"F6.wireOp",EDGE,"E2129"),sQuery(id+"F6.wireOp",EDGE,"E2130"),sQuery(id+"F6.wireOp",EDGE,"E2131"),sQuery(id+"F6.wireOp",EDGE,"E2132"),sQuery(id+"F6.wireOp",EDGE,"E2133"),sQuery(id+"F6.wireOp",EDGE,"E2134"),sQuery(id+"F6.wireOp",EDGE,"E2135"),sQuery(id+"F6.wireOp",EDGE,"E2136"),sQuery(id+"F6.wireOp",EDGE,"E2137"),sQuery(id+"F6.wireOp",EDGE,"E2138"),sQuery(id+"F6.wireOp",EDGE,"E2139"),sQuery(id+"F6.wireOp",EDGE,"E2140"),sQuery(id+"F6.wireOp",EDGE,"E2141"),sQuery(id+"F6.wireOp",EDGE,"E2142"),sQuery(id+"F6.wireOp",EDGE,"E2143"),sQuery(id+"F6.wireOp",EDGE,"E2144"),sQuery(id+"F6.wireOp",EDGE,"E2145"),sQuery(id+"F6.wireOp",EDGE,"E2146"),sQuery(id+"F6.wireOp",EDGE,"E2147"),sQuery(id+"F6.wireOp",EDGE,"E2148"),sQuery(id+"F6.wireOp",EDGE,"E2149"),sQuery(id+"F6.wireOp",EDGE,"E2150"),sQuery(id+"F6.wireOp",EDGE,"E2151"),sQuery(id+"F6.wireOp",EDGE,"E2152"),sQuery(id+"F6.wireOp",EDGE,"E2153"),sQuery(id+"F6.wireOp",EDGE,"E2154"),sQuery(id+"F6.wireOp",EDGE,"E2155"),sQuery(id+"F6.wireOp",EDGE,"E2156"),sQuery(id+"F6.wireOp",EDGE,"E2157"),sQuery(id+"F6.wireOp",EDGE,"E2158"),sQuery(id+"F6.wireOp",EDGE,"E2159"),sQuery(id+"F6.wireOp",EDGE,"E2160"),sQuery(id+"F6.wireOp",EDGE,"E2161"),sQuery(id+"F6.wireOp",EDGE,"E2162"),sQuery(id+"F6.wireOp",EDGE,"E2163"),sQuery(id+"F6.wireOp",EDGE,"E2164"),sQuery(id+"F6.wireOp",EDGE,"E2165"),sQuery(id+"F6.wireOp",EDGE,"E2166"),sQuery(id+"F6.wireOp",EDGE,"E2167"),sQuery(id+"F6.wireOp",EDGE,"E2168"),sQuery(id+"F6.wireOp",EDGE,"E2169"),sQuery(id+"F6.wireOp",EDGE,"E2170"),sQuery(id+"F6.wireOp",EDGE,"E2171"),sQuery(id+"F6.wireOp",EDGE,"E2172"),sQuery(id+"F6.wireOp",EDGE,"E2173"),sQuery(id+"F6.wireOp",EDGE,"E2174"),sQuery(id+"F6.wireOp",EDGE,"E2175"),sQuery(id+"F6.wireOp",EDGE,"E2176"),sQuery(id+"F6.wireOp",EDGE,"E2177"),sQuery(id+"F6.wireOp",EDGE,"E2178"),sQuery(id+"F6.wireOp",EDGE,"E2179"),sQuery(id+"F6.wireOp",EDGE,"E2180"),sQuery(id+"F6.wireOp",EDGE,"E2181"),sQuery(id+"F6.wireOp",EDGE,"E2182"),sQuery(id+"F6.wireOp",EDGE,"E2183"),sQuery(id+"F6.wireOp",EDGE,"E2184"),sQuery(id+"F6.wireOp",EDGE,"E2185"),sQuery(id+"F6.wireOp",EDGE,"E2186"),sQuery(id+"F6.wireOp",EDGE,"E2187"),sQuery(id+"F6.wireOp",EDGE,"E2188"),sQuery(id+"F6.wireOp",EDGE,"E2189"),sQuery(id+"F6.wireOp",EDGE,"E2190"),sQuery(id+"F6.wireOp",EDGE,"E2191"),sQuery(id+"F6.wireOp",EDGE,"E2192"),sQuery(id+"F6.wireOp",EDGE,"E2193"),sQuery(id+"F6.wireOp",EDGE,"E2194"),sQuery(id+"F6.wireOp",EDGE,"E2195"),sQuery(id+"F6.wireOp",EDGE,"E2196"),sQuery(id+"F6.wireOp",EDGE,"E2197"),sQuery(id+"F6.wireOp",EDGE,"E2198"),sQuery(id+"F6.wireOp",EDGE,"E2199"),sQuery(id+"F6.wireOp",EDGE,"E2200"),sQuery(id+"F6.wireOp",EDGE,"E2201"),sQuery(id+"F6.wireOp",EDGE,"E2202"),sQuery(id+"F6.wireOp",EDGE,"E2203"),sQuery(id+"F6.wireOp",EDGE,"E2204"),sQuery(id+"F6.wireOp",EDGE,"E2205"),sQuery(id+"F6.wireOp",EDGE,"E2206"),sQuery(id+"F6.wireOp",EDGE,"E2207"),sQuery(id+"F6.wireOp",EDGE,"E2208"),sQuery(id+"F6.wireOp",EDGE,"E2209"),sQuery(id+"F6.wireOp",EDGE,"E2210"),sQuery(id+"F6.wireOp",EDGE,"E2211"),sQuery(id+"F6.wireOp",EDGE,"E2212"),sQuery(id+"F6.wireOp",EDGE,"E2213"),sQuery(id+"F6.wireOp",EDGE,"E2214"),sQuery(id+"F6.wireOp",EDGE,"E2215"),sQuery(id+"F6.wireOp",EDGE,"E2216"),sQuery(id+"F6.wireOp",EDGE,"E2217"),sQuery(id+"F6.wireOp",EDGE,"E2218"),sQuery(id+"F6.wireOp",EDGE,"E2219"),sQuery(id+"F6.wireOp",EDGE,"E2220"),sQuery(id+"F6.wireOp",EDGE,"E2221"),sQuery(id+"F6.wireOp",EDGE,"E2222"),sQuery(id+"F6.wireOp",EDGE,"E2223"),sQuery(id+"F6.wireOp",EDGE,"E2224"),sQuery(id+"F6.wireOp",EDGE,"E2225"),sQuery(id+"F6.wireOp",EDGE,"E2226"),sQuery(id+"F6.wireOp",EDGE,"E2227"),sQuery(id+"F6.wireOp",EDGE,"E2228"),sQuery(id+"F6.wireOp",EDGE,"E2229"),sQuery(id+"F6.wireOp",EDGE,"E2230"),sQuery(id+"F6.wireOp",EDGE,"E2231"),sQuery(id+"F6.wireOp",EDGE,"E2232"),sQuery(id+"F6.wireOp",EDGE,"E2233"),sQuery(id+"F6.wireOp",EDGE,"E2234"),sQuery(id+"F6.wireOp",EDGE,"E2235"),sQuery(id+"F6.wireOp",EDGE,"E2236"),sQuery(id+"F6.wireOp",EDGE,"E2237"),sQuery(id+"F6.wireOp",EDGE,"E2238"),sQuery(id+"F6.wireOp",EDGE,"E2239"),sQuery(id+"F6.wireOp",EDGE,"E2240"),sQuery(id+"F6.wireOp",EDGE,"E2241"),sQuery(id+"F6.wireOp",EDGE,"E2242"),sQuery(id+"F6.wireOp",EDGE,"E2243"),sQuery(id+"F6.wireOp",EDGE,"E2244"),sQuery(id+"F6.wireOp",EDGE,"E2245"),sQuery(id+"F6.wireOp",EDGE,"E2246"),sQuery(id+"F6.wireOp",EDGE,"E2247"),sQuery(id+"F6.wireOp",EDGE,"E2248"),sQuery(id+"F6.wireOp",EDGE,"E2249"),sQuery(id+"F6.wireOp",EDGE,"E2250"),sQuery(id+"F6.wireOp",EDGE,"E2251"),sQuery(id+"F6.wireOp",EDGE,"E2252"),sQuery(id+"F6.wireOp",EDGE,"E2253"),sQuery(id+"F6.wireOp",EDGE,"E2254"),sQuery(id+"F6.wireOp",EDGE,"E2255"),sQuery(id+"F6.wireOp",EDGE,"E2256"),sQuery(id+"F6.wireOp",EDGE,"E2257"),sQuery(id+"F6.wireOp",EDGE,"E2258"),sQuery(id+"F6.wireOp",EDGE,"E2259"),sQuery(id+"F6.wireOp",EDGE,"E2260"),sQuery(id+"F6.wireOp",EDGE,"E2261"),sQuery(id+"F6.wireOp",EDGE,"E2262"),sQuery(id+"F6.wireOp",EDGE,"E2263"),sQuery(id+"F6.wireOp",EDGE,"E2264"),sQuery(id+"F6.wireOp",EDGE,"E2265"),sQuery(id+"F6.wireOp",EDGE,"E2266"),sQuery(id+"F6.wireOp",EDGE,"E2267"),sQuery(id+"F6.wireOp",EDGE,"E2268"),sQuery(id+"F6.wireOp",EDGE,"E2269"),sQuery(id+"F6.wireOp",EDGE,"E2270"),sQuery(id+"F6.wireOp",EDGE,"E2271"),sQuery(id+"F6.wireOp",EDGE,"E2272"),sQuery(id+"F6.wireOp",EDGE,"E2273"),sQuery(id+"F6.wireOp",EDGE,"E2274"),sQuery(id+"F6.wireOp",EDGE,"E2275"),sQuery(id+"F6.wireOp",EDGE,"E2276"),sQuery(id+"F6.wireOp",EDGE,"E2277"),sQuery(id+"F6.wireOp",EDGE,"E2278"),sQuery(id+"F6.wireOp",EDGE,"E2279"),sQuery(id+"F6.wireOp",EDGE,"E2280"),sQuery(id+"F6.wireOp",EDGE,"E2281"),sQuery(id+"F6.wireOp",EDGE,"E2282"),sQuery(id+"F6.wireOp",EDGE,"E2283"),sQuery(id+"F6.wireOp",EDGE,"E2284"),sQuery(id+"F6.wireOp",EDGE,"E2285"),sQuery(id+"F6.wireOp",EDGE,"E2286"),sQuery(id+"F6.wireOp",EDGE,"E2287"),sQuery(id+"F6.wireOp",EDGE,"E2288"),sQuery(id+"F6.wireOp",EDGE,"E2289"),sQuery(id+"F6.wireOp",EDGE,"E2290"),sQuery(id+"F6.wireOp",EDGE,"E2291"),sQuery(id+"F6.wireOp",EDGE,"E2292"),sQuery(id+"F6.wireOp",EDGE,"E2293"),sQuery(id+"F6.wireOp",EDGE,"E2294"),sQuery(id+"F6.wireOp",EDGE,"E2295"),sQuery(id+"F6.wireOp",EDGE,"E2296"),sQuery(id+"F6.wireOp",EDGE,"E2297"),sQuery(id+"F6.wireOp",EDGE,"E2298"),sQuery(id+"F6.wireOp",EDGE,"E2299"),sQuery(id+"F6.wireOp",EDGE,"E2300"),sQuery(id+"F6.wireOp",EDGE,"E2301"),sQuery(id+"F6.wireOp",EDGE,"E2302"),sQuery(id+"F6.wireOp",EDGE,"E2303"),sQuery(id+"F6.wireOp",EDGE,"E2304"),sQuery(id+"F6.wireOp",EDGE,"E2305"),sQuery(id+"F6.wireOp",EDGE,"E2306"),sQuery(id+"F6.wireOp",EDGE,"E2307"),sQuery(id+"F6.wireOp",EDGE,"E2308"),sQuery(id+"F6.wireOp",EDGE,"E2309"),sQuery(id+"F6.wireOp",EDGE,"E2310"),sQuery(id+"F6.wireOp",EDGE,"E2311"),sQuery(id+"F6.wireOp",EDGE,"E2312"),sQuery(id+"F6.wireOp",EDGE,"E2313"),sQuery(id+"F6.wireOp",EDGE,"E2314"),sQuery(id+"F6.wireOp",EDGE,"E2315"),sQuery(id+"F6.wireOp",EDGE,"E2316"),sQuery(id+"F6.wireOp",EDGE,"E2317"),sQuery(id+"F6.wireOp",EDGE,"E2318"),sQuery(id+"F6.wireOp",EDGE,"E2319"),sQuery(id+"F6.wireOp",EDGE,"E2320"),sQuery(id+"F6.wireOp",EDGE,"E2321"),sQuery(id+"F6.wireOp",EDGE,"E2322"),sQuery(id+"F6.wireOp",EDGE,"E2323"),sQuery(id+"F6.wireOp",EDGE,"E2324"),sQuery(id+"F6.wireOp",EDGE,"E2325"),sQuery(id+"F6.wireOp",EDGE,"E2326"),sQuery(id+"F6.wireOp",EDGE,"E2327"),sQuery(id+"F6.wireOp",EDGE,"E2328"),sQuery(id+"F6.wireOp",EDGE,"E2329"),sQuery(id+"F6.wireOp",EDGE,"E2330"),sQuery(id+"F6.wireOp",EDGE,"E2331"),sQuery(id+"F6.wireOp",EDGE,"E2332"),sQuery(id+"F6.wireOp",EDGE,"E2333"),sQuery(id+"F6.wireOp",EDGE,"E2334"),sQuery(id+"F6.wireOp",EDGE,"E2335"),sQuery(id+"F6.wireOp",EDGE,"E2336"),sQuery(id+"F6.wireOp",EDGE,"E2337"),sQuery(id+"F6.wireOp",EDGE,"E2338"),sQuery(id+"F6.wireOp",EDGE,"E2339"),sQuery(id+"F6.wireOp",EDGE,"E2340"),sQuery(id+"F6.wireOp",EDGE,"E2341"),sQuery(id+"F6.wireOp",EDGE,"E2342"),sQuery(id+"F6.wireOp",EDGE,"E2343"),sQuery(id+"F6.wireOp",EDGE,"E2344"),sQuery(id+"F6.wireOp",EDGE,"E2345"),sQuery(id+"F6.wireOp",EDGE,"E2346"),sQuery(id+"F6.wireOp",EDGE,"E2347"),sQuery(id+"F6.wireOp",EDGE,"E2348"),sQuery(id+"F6.wireOp",EDGE,"E2349"),sQuery(id+"F6.wireOp",EDGE,"E2350"),sQuery(id+"F6.wireOp",EDGE,"E2351"),sQuery(id+"F6.wireOp",EDGE,"E2352"),sQuery(id+"F6.wireOp",EDGE,"E2353"),sQuery(id+"F6.wireOp",EDGE,"E2354"),sQuery(id+"F6.wireOp",EDGE,"E2355"),sQuery(id+"F6.wireOp",EDGE,"E2356"),sQuery(id+"F6.wireOp",EDGE,"E2357"),sQuery(id+"F6.wireOp",EDGE,"E2358"),sQuery(id+"F6.wireOp",EDGE,"E2359"),sQuery(id+"F6.wireOp",EDGE,"E2360"),sQuery(id+"F6.wireOp",EDGE,"E2361"),sQuery(id+"F6.wireOp",EDGE,"E2362"),sQuery(id+"F6.wireOp",EDGE,"E2363"),sQuery(id+"F6.wireOp",EDGE,"E2364"),sQuery(id+"F6.wireOp",EDGE,"E2365"),sQuery(id+"F6.wireOp",EDGE,"E2366"),sQuery(id+"F6.wireOp",EDGE,"E2367"),sQuery(id+"F6.wireOp",EDGE,"E2368"),sQuery(id+"F6.wireOp",EDGE,"E2369"),sQuery(id+"F6.wireOp",EDGE,"E2370"),sQuery(id+"F6.wireOp",EDGE,"E2371"),sQuery(id+"F6.wireOp",EDGE,"E2372"),sQuery(id+"F6.wireOp",EDGE,"E2373"),sQuery(id+"F6.wireOp",EDGE,"E2374"),sQuery(id+"F6.wireOp",EDGE,"E2375"),sQuery(id+"F6.wireOp",EDGE,"E2376"),sQuery(id+"F6.wireOp",EDGE,"E2377"),sQuery(id+"F6.wireOp",EDGE,"E2378"),sQuery(id+"F6.wireOp",EDGE,"E2379"),sQuery(id+"F6.wireOp",EDGE,"E2380"),sQuery(id+"F6.wireOp",EDGE,"E2381"),sQuery(id+"F6.wireOp",EDGE,"E2382"),sQuery(id+"F6.wireOp",EDGE,"E2383"),sQuery(id+"F6.wireOp",EDGE,"E2384"),sQuery(id+"F6.wireOp",EDGE,"E2385"),sQuery(id+"F6.wireOp",EDGE,"E2386"),sQuery(id+"F6.wireOp",EDGE,"E2387"),sQuery(id+"F6.wireOp",EDGE,"E2388"),sQuery(id+"F6.wireOp",EDGE,"E2389"),sQuery(id+"F6.wireOp",EDGE,"E2390"),sQuery(id+"F6.wireOp",EDGE,"E2391"),sQuery(id+"F6.wireOp",EDGE,"E2392"),sQuery(id+"F6.wireOp",EDGE,"E2393"),sQuery(id+"F6.wireOp",EDGE,"E2394"),sQuery(id+"F6.wireOp",EDGE,"E2395"),sQuery(id+"F6.wireOp",EDGE,"E2396"),sQuery(id+"F6.wireOp",EDGE,"E2397"),sQuery(id+"F6.wireOp",EDGE,"E2398"),sQuery(id+"F6.wireOp",EDGE,"E2399"),sQuery(id+"F6.wireOp",EDGE,"E2400"),sQuery(id+"F6.wireOp",EDGE,"E2401"),sQuery(id+"F6.wireOp",EDGE,"E2402"),sQuery(id+"F6.wireOp",EDGE,"E2403"),sQuery(id+"F6.wireOp",EDGE,"E2404"),sQuery(id+"F6.wireOp",EDGE,"E2405"),sQuery(id+"F6.wireOp",EDGE,"E2406"),sQuery(id+"F6.wireOp",EDGE,"E2407"),sQuery(id+"F6.wireOp",EDGE,"E2408"),sQuery(id+"F6.wireOp",EDGE,"E2409"),sQuery(id+"F6.wireOp",EDGE,"E2410"),sQuery(id+"F6.wireOp",EDGE,"E2411"),sQuery(id+"F6.wireOp",EDGE,"E2412"),sQuery(id+"F6.wireOp",EDGE,"E2413"),sQuery(id+"F6.wireOp",EDGE,"E2414"),sQuery(id+"F6.wireOp",EDGE,"E2415"),sQuery(id+"F6.wireOp",EDGE,"E2416"),sQuery(id+"F6.wireOp",EDGE,"E2417"),sQuery(id+"F6.wireOp",EDGE,"E2418"),sQuery(id+"F6.wireOp",EDGE,"E2419"),sQuery(id+"F6.wireOp",EDGE,"E2420"),sQuery(id+"F6.wireOp",EDGE,"E2421"),sQuery(id+"F6.wireOp",EDGE,"E2422"),sQuery(id+"F6.wireOp",EDGE,"E2423"),sQuery(id+"F6.wireOp",EDGE,"E2424"),sQuery(id+"F6.wireOp",EDGE,"E2425"),sQuery(id+"F6.wireOp",EDGE,"E2426"),sQuery(id+"F6.wireOp",EDGE,"E2427"),sQuery(id+"F6.wireOp",EDGE,"E2428"),sQuery(id+"F6.wireOp",EDGE,"E2429"),sQuery(id+"F6.wireOp",EDGE,"E2430"),sQuery(id+"F6.wireOp",EDGE,"E2431"),sQuery(id+"F6.wireOp",EDGE,"E2432"),sQuery(id+"F6.wireOp",EDGE,"E2433"),sQuery(id+"F6.wireOp",EDGE,"E2434"),sQuery(id+"F6.wireOp",EDGE,"E2435")])]});
            var Q1;
            Q1=sQuery(id+"F9.wireOp",VERTEX,"E2436");
            var Q2;
            Q2=sQuery(id+"F9.wireOp",VERTEX,"E2437");
            transform(context, id + "F11", {"entities" : qUnion([Q0]), "transformType" : TransformType.TRANSLATION_ENTITY, "oppositeDirectionEntity" : false, "transformLine" : qUnion([Q1, Q2]), "makeCopy" : false});
        }
        {
            var Q0;
            Q0=qCreatedBy(makeId("Front.planeOp"),FACE);
            var sketch = newSketch(context, id + "F12", { "sketchPlane" : qUnion([Q0])});
            skPoint(sketch, "E2438", {"position": v(-15.66, 9.01) * mm});
            skPoint(sketch, "E2439", {"position": v(-44.87, 25.9) * mm});
            skSolve(sketch);
        }
        {
            var Q0;
            Q0=makeQuery(id+"F10.opPattern","COPY",BODY,{"derivedFrom":makeQuery(id+"F7.opExtrude","SWEPT_BODY",BODY,{"disambiguationData":[OSD([sQuery(id+"F6.wireOp",EDGE,"E37"),sQuery(id+"F6.wireOp",EDGE,"E38"),sQuery(id+"F6.wireOp",EDGE,"E39"),sQuery(id+"F6.wireOp",EDGE,"E40"),sQuery(id+"F6.wireOp",EDGE,"E41"),sQuery(id+"F6.wireOp",EDGE,"E42"),sQuery(id+"F6.wireOp",EDGE,"E43"),sQuery(id+"F6.wireOp",EDGE,"E44"),sQuery(id+"F6.wireOp",EDGE,"E45"),sQuery(id+"F6.wireOp",EDGE,"E46"),sQuery(id+"F6.wireOp",EDGE,"E47"),sQuery(id+"F6.wireOp",EDGE,"E48"),sQuery(id+"F6.wireOp",EDGE,"E49"),sQuery(id+"F6.wireOp",EDGE,"E50"),sQuery(id+"F6.wireOp",EDGE,"E51"),sQuery(id+"F6.wireOp",EDGE,"E52"),sQuery(id+"F6.wireOp",EDGE,"E53"),sQuery(id+"F6.wireOp",EDGE,"E54"),sQuery(id+"F6.wireOp",EDGE,"E55"),sQuery(id+"F6.wireOp",EDGE,"E56"),sQuery(id+"F6.wireOp",EDGE,"E57"),sQuery(id+"F6.wireOp",EDGE,"E58"),sQuery(id+"F6.wireOp",EDGE,"E59"),sQuery(id+"F6.wireOp",EDGE,"E60"),sQuery(id+"F6.wireOp",EDGE,"E61"),sQuery(id+"F6.wireOp",EDGE,"E62"),sQuery(id+"F6.wireOp",EDGE,"E63"),sQuery(id+"F6.wireOp",EDGE,"E64"),sQuery(id+"F6.wireOp",EDGE,"E65"),sQuery(id+"F6.wireOp",EDGE,"E66"),sQuery(id+"F6.wireOp",EDGE,"E67"),sQuery(id+"F6.wireOp",EDGE,"E68"),sQuery(id+"F6.wireOp",EDGE,"E69"),sQuery(id+"F6.wireOp",EDGE,"E70"),sQuery(id+"F6.wireOp",EDGE,"E71"),sQuery(id+"F6.wireOp",EDGE,"E72"),sQuery(id+"F6.wireOp",EDGE,"E73"),sQuery(id+"F6.wireOp",EDGE,"E74"),sQuery(id+"F6.wireOp",EDGE,"E75"),sQuery(id+"F6.wireOp",EDGE,"E76"),sQuery(id+"F6.wireOp",EDGE,"E77"),sQuery(id+"F6.wireOp",EDGE,"E78"),sQuery(id+"F6.wireOp",EDGE,"E79"),sQuery(id+"F6.wireOp",EDGE,"E80"),sQuery(id+"F6.wireOp",EDGE,"E81"),sQuery(id+"F6.wireOp",EDGE,"E82"),sQuery(id+"F6.wireOp",EDGE,"E83"),sQuery(id+"F6.wireOp",EDGE,"E84"),sQuery(id+"F6.wireOp",EDGE,"E85"),sQuery(id+"F6.wireOp",EDGE,"E86"),sQuery(id+"F6.wireOp",EDGE,"E87"),sQuery(id+"F6.wireOp",EDGE,"E88"),sQuery(id+"F6.wireOp",EDGE,"E89"),sQuery(id+"F6.wireOp",EDGE,"E90"),sQuery(id+"F6.wireOp",EDGE,"E91"),sQuery(id+"F6.wireOp",EDGE,"E92"),sQuery(id+"F6.wireOp",EDGE,"E93"),sQuery(id+"F6.wireOp",EDGE,"E94"),sQuery(id+"F6.wireOp",EDGE,"E95"),sQuery(id+"F6.wireOp",EDGE,"E96"),sQuery(id+"F6.wireOp",EDGE,"E97"),sQuery(id+"F6.wireOp",EDGE,"E98"),sQuery(id+"F6.wireOp",EDGE,"E99"),sQuery(id+"F6.wireOp",EDGE,"E100"),sQuery(id+"F6.wireOp",EDGE,"E101"),sQuery(id+"F6.wireOp",EDGE,"E102"),sQuery(id+"F6.wireOp",EDGE,"E103"),sQuery(id+"F6.wireOp",EDGE,"E104"),sQuery(id+"F6.wireOp",EDGE,"E105"),sQuery(id+"F6.wireOp",EDGE,"E106"),sQuery(id+"F6.wireOp",EDGE,"E107"),sQuery(id+"F6.wireOp",EDGE,"E108"),sQuery(id+"F6.wireOp",EDGE,"E109"),sQuery(id+"F6.wireOp",EDGE,"E110"),sQuery(id+"F6.wireOp",EDGE,"E111"),sQuery(id+"F6.wireOp",EDGE,"E112"),sQuery(id+"F6.wireOp",EDGE,"E113"),sQuery(id+"F6.wireOp",EDGE,"E114"),sQuery(id+"F6.wireOp",EDGE,"E115"),sQuery(id+"F6.wireOp",EDGE,"E116"),sQuery(id+"F6.wireOp",EDGE,"E117"),sQuery(id+"F6.wireOp",EDGE,"E118"),sQuery(id+"F6.wireOp",EDGE,"E119"),sQuery(id+"F6.wireOp",EDGE,"E120"),sQuery(id+"F6.wireOp",EDGE,"E121"),sQuery(id+"F6.wireOp",EDGE,"E122"),sQuery(id+"F6.wireOp",EDGE,"E123"),sQuery(id+"F6.wireOp",EDGE,"E124"),sQuery(id+"F6.wireOp",EDGE,"E125"),sQuery(id+"F6.wireOp",EDGE,"E126"),sQuery(id+"F6.wireOp",EDGE,"E127"),sQuery(id+"F6.wireOp",EDGE,"E128"),sQuery(id+"F6.wireOp",EDGE,"E129"),sQuery(id+"F6.wireOp",EDGE,"E130"),sQuery(id+"F6.wireOp",EDGE,"E131"),sQuery(id+"F6.wireOp",EDGE,"E132"),sQuery(id+"F6.wireOp",EDGE,"E133"),sQuery(id+"F6.wireOp",EDGE,"E134"),sQuery(id+"F6.wireOp",EDGE,"E135"),sQuery(id+"F6.wireOp",EDGE,"E136"),sQuery(id+"F6.wireOp",EDGE,"E137"),sQuery(id+"F6.wireOp",EDGE,"E138"),sQuery(id+"F6.wireOp",EDGE,"E139"),sQuery(id+"F6.wireOp",EDGE,"E140"),sQuery(id+"F6.wireOp",EDGE,"E141"),sQuery(id+"F6.wireOp",EDGE,"E142"),sQuery(id+"F6.wireOp",EDGE,"E143"),sQuery(id+"F6.wireOp",EDGE,"E144"),sQuery(id+"F6.wireOp",EDGE,"E145"),sQuery(id+"F6.wireOp",EDGE,"E146"),sQuery(id+"F6.wireOp",EDGE,"E147"),sQuery(id+"F6.wireOp",EDGE,"E148"),sQuery(id+"F6.wireOp",EDGE,"E149"),sQuery(id+"F6.wireOp",EDGE,"E150"),sQuery(id+"F6.wireOp",EDGE,"E151"),sQuery(id+"F6.wireOp",EDGE,"E152"),sQuery(id+"F6.wireOp",EDGE,"E153"),sQuery(id+"F6.wireOp",EDGE,"E154"),sQuery(id+"F6.wireOp",EDGE,"E155"),sQuery(id+"F6.wireOp",EDGE,"E156"),sQuery(id+"F6.wireOp",EDGE,"E157"),sQuery(id+"F6.wireOp",EDGE,"E158"),sQuery(id+"F6.wireOp",EDGE,"E159"),sQuery(id+"F6.wireOp",EDGE,"E160"),sQuery(id+"F6.wireOp",EDGE,"E161"),sQuery(id+"F6.wireOp",EDGE,"E162"),sQuery(id+"F6.wireOp",EDGE,"E163"),sQuery(id+"F6.wireOp",EDGE,"E164"),sQuery(id+"F6.wireOp",EDGE,"E165"),sQuery(id+"F6.wireOp",EDGE,"E166"),sQuery(id+"F6.wireOp",EDGE,"E167"),sQuery(id+"F6.wireOp",EDGE,"E168"),sQuery(id+"F6.wireOp",EDGE,"E169"),sQuery(id+"F6.wireOp",EDGE,"E170"),sQuery(id+"F6.wireOp",EDGE,"E171"),sQuery(id+"F6.wireOp",EDGE,"E172"),sQuery(id+"F6.wireOp",EDGE,"E173"),sQuery(id+"F6.wireOp",EDGE,"E174"),sQuery(id+"F6.wireOp",EDGE,"E175"),sQuery(id+"F6.wireOp",EDGE,"E176"),sQuery(id+"F6.wireOp",EDGE,"E177"),sQuery(id+"F6.wireOp",EDGE,"E178"),sQuery(id+"F6.wireOp",EDGE,"E179"),sQuery(id+"F6.wireOp",EDGE,"E180"),sQuery(id+"F6.wireOp",EDGE,"E181"),sQuery(id+"F6.wireOp",EDGE,"E182"),sQuery(id+"F6.wireOp",EDGE,"E183"),sQuery(id+"F6.wireOp",EDGE,"E184"),sQuery(id+"F6.wireOp",EDGE,"E185"),sQuery(id+"F6.wireOp",EDGE,"E186"),sQuery(id+"F6.wireOp",EDGE,"E187"),sQuery(id+"F6.wireOp",EDGE,"E188"),sQuery(id+"F6.wireOp",EDGE,"E189"),sQuery(id+"F6.wireOp",EDGE,"E190"),sQuery(id+"F6.wireOp",EDGE,"E191"),sQuery(id+"F6.wireOp",EDGE,"E192"),sQuery(id+"F6.wireOp",EDGE,"E193"),sQuery(id+"F6.wireOp",EDGE,"E194"),sQuery(id+"F6.wireOp",EDGE,"E195"),sQuery(id+"F6.wireOp",EDGE,"E196"),sQuery(id+"F6.wireOp",EDGE,"E197"),sQuery(id+"F6.wireOp",EDGE,"E198"),sQuery(id+"F6.wireOp",EDGE,"E199"),sQuery(id+"F6.wireOp",EDGE,"E200"),sQuery(id+"F6.wireOp",EDGE,"E201"),sQuery(id+"F6.wireOp",EDGE,"E202"),sQuery(id+"F6.wireOp",EDGE,"E203"),sQuery(id+"F6.wireOp",EDGE,"E204"),sQuery(id+"F6.wireOp",EDGE,"E205"),sQuery(id+"F6.wireOp",EDGE,"E206"),sQuery(id+"F6.wireOp",EDGE,"E207"),sQuery(id+"F6.wireOp",EDGE,"E208"),sQuery(id+"F6.wireOp",EDGE,"E209"),sQuery(id+"F6.wireOp",EDGE,"E210"),sQuery(id+"F6.wireOp",EDGE,"E211"),sQuery(id+"F6.wireOp",EDGE,"E212"),sQuery(id+"F6.wireOp",EDGE,"E213"),sQuery(id+"F6.wireOp",EDGE,"E214"),sQuery(id+"F6.wireOp",EDGE,"E215"),sQuery(id+"F6.wireOp",EDGE,"E216"),sQuery(id+"F6.wireOp",EDGE,"E217"),sQuery(id+"F6.wireOp",EDGE,"E218"),sQuery(id+"F6.wireOp",EDGE,"E219"),sQuery(id+"F6.wireOp",EDGE,"E220"),sQuery(id+"F6.wireOp",EDGE,"E221"),sQuery(id+"F6.wireOp",EDGE,"E222"),sQuery(id+"F6.wireOp",EDGE,"E223"),sQuery(id+"F6.wireOp",EDGE,"E224"),sQuery(id+"F6.wireOp",EDGE,"E225"),sQuery(id+"F6.wireOp",EDGE,"E226"),sQuery(id+"F6.wireOp",EDGE,"E227"),sQuery(id+"F6.wireOp",EDGE,"E228"),sQuery(id+"F6.wireOp",EDGE,"E229"),sQuery(id+"F6.wireOp",EDGE,"E230"),sQuery(id+"F6.wireOp",EDGE,"E231"),sQuery(id+"F6.wireOp",EDGE,"E232"),sQuery(id+"F6.wireOp",EDGE,"E233"),sQuery(id+"F6.wireOp",EDGE,"E234"),sQuery(id+"F6.wireOp",EDGE,"E235"),sQuery(id+"F6.wireOp",EDGE,"E236"),sQuery(id+"F6.wireOp",EDGE,"E237"),sQuery(id+"F6.wireOp",EDGE,"E238"),sQuery(id+"F6.wireOp",EDGE,"E239"),sQuery(id+"F6.wireOp",EDGE,"E240"),sQuery(id+"F6.wireOp",EDGE,"E241"),sQuery(id+"F6.wireOp",EDGE,"E242"),sQuery(id+"F6.wireOp",EDGE,"E243"),sQuery(id+"F6.wireOp",EDGE,"E244"),sQuery(id+"F6.wireOp",EDGE,"E245"),sQuery(id+"F6.wireOp",EDGE,"E246"),sQuery(id+"F6.wireOp",EDGE,"E247"),sQuery(id+"F6.wireOp",EDGE,"E248"),sQuery(id+"F6.wireOp",EDGE,"E249"),sQuery(id+"F6.wireOp",EDGE,"E250"),sQuery(id+"F6.wireOp",EDGE,"E251"),sQuery(id+"F6.wireOp",EDGE,"E252"),sQuery(id+"F6.wireOp",EDGE,"E253"),sQuery(id+"F6.wireOp",EDGE,"E254"),sQuery(id+"F6.wireOp",EDGE,"E255"),sQuery(id+"F6.wireOp",EDGE,"E256"),sQuery(id+"F6.wireOp",EDGE,"E257"),sQuery(id+"F6.wireOp",EDGE,"E258"),sQuery(id+"F6.wireOp",EDGE,"E259"),sQuery(id+"F6.wireOp",EDGE,"E260"),sQuery(id+"F6.wireOp",EDGE,"E261"),sQuery(id+"F6.wireOp",EDGE,"E262"),sQuery(id+"F6.wireOp",EDGE,"E263"),sQuery(id+"F6.wireOp",EDGE,"E264"),sQuery(id+"F6.wireOp",EDGE,"E265"),sQuery(id+"F6.wireOp",EDGE,"E266"),sQuery(id+"F6.wireOp",EDGE,"E267"),sQuery(id+"F6.wireOp",EDGE,"E268"),sQuery(id+"F6.wireOp",EDGE,"E269"),sQuery(id+"F6.wireOp",EDGE,"E270"),sQuery(id+"F6.wireOp",EDGE,"E271"),sQuery(id+"F6.wireOp",EDGE,"E272"),sQuery(id+"F6.wireOp",EDGE,"E273"),sQuery(id+"F6.wireOp",EDGE,"E274"),sQuery(id+"F6.wireOp",EDGE,"E275"),sQuery(id+"F6.wireOp",EDGE,"E276"),sQuery(id+"F6.wireOp",EDGE,"E277"),sQuery(id+"F6.wireOp",EDGE,"E278"),sQuery(id+"F6.wireOp",EDGE,"E279"),sQuery(id+"F6.wireOp",EDGE,"E280"),sQuery(id+"F6.wireOp",EDGE,"E281"),sQuery(id+"F6.wireOp",EDGE,"E282"),sQuery(id+"F6.wireOp",EDGE,"E283"),sQuery(id+"F6.wireOp",EDGE,"E284"),sQuery(id+"F6.wireOp",EDGE,"E285"),sQuery(id+"F6.wireOp",EDGE,"E286"),sQuery(id+"F6.wireOp",EDGE,"E287"),sQuery(id+"F6.wireOp",EDGE,"E288"),sQuery(id+"F6.wireOp",EDGE,"E289"),sQuery(id+"F6.wireOp",EDGE,"E290"),sQuery(id+"F6.wireOp",EDGE,"E291"),sQuery(id+"F6.wireOp",EDGE,"E292"),sQuery(id+"F6.wireOp",EDGE,"E293"),sQuery(id+"F6.wireOp",EDGE,"E294"),sQuery(id+"F6.wireOp",EDGE,"E295"),sQuery(id+"F6.wireOp",EDGE,"E296"),sQuery(id+"F6.wireOp",EDGE,"E297"),sQuery(id+"F6.wireOp",EDGE,"E298"),sQuery(id+"F6.wireOp",EDGE,"E299"),sQuery(id+"F6.wireOp",EDGE,"E300"),sQuery(id+"F6.wireOp",EDGE,"E301"),sQuery(id+"F6.wireOp",EDGE,"E302"),sQuery(id+"F6.wireOp",EDGE,"E303"),sQuery(id+"F6.wireOp",EDGE,"E304"),sQuery(id+"F6.wireOp",EDGE,"E305"),sQuery(id+"F6.wireOp",EDGE,"E306"),sQuery(id+"F6.wireOp",EDGE,"E307"),sQuery(id+"F6.wireOp",EDGE,"E308"),sQuery(id+"F6.wireOp",EDGE,"E309"),sQuery(id+"F6.wireOp",EDGE,"E310"),sQuery(id+"F6.wireOp",EDGE,"E311"),sQuery(id+"F6.wireOp",EDGE,"E312"),sQuery(id+"F6.wireOp",EDGE,"E313"),sQuery(id+"F6.wireOp",EDGE,"E314"),sQuery(id+"F6.wireOp",EDGE,"E315"),sQuery(id+"F6.wireOp",EDGE,"E316"),sQuery(id+"F6.wireOp",EDGE,"E317"),sQuery(id+"F6.wireOp",EDGE,"E318"),sQuery(id+"F6.wireOp",EDGE,"E319"),sQuery(id+"F6.wireOp",EDGE,"E320"),sQuery(id+"F6.wireOp",EDGE,"E321"),sQuery(id+"F6.wireOp",EDGE,"E322"),sQuery(id+"F6.wireOp",EDGE,"E323"),sQuery(id+"F6.wireOp",EDGE,"E324"),sQuery(id+"F6.wireOp",EDGE,"E325"),sQuery(id+"F6.wireOp",EDGE,"E326"),sQuery(id+"F6.wireOp",EDGE,"E327"),sQuery(id+"F6.wireOp",EDGE,"E328"),sQuery(id+"F6.wireOp",EDGE,"E329"),sQuery(id+"F6.wireOp",EDGE,"E330"),sQuery(id+"F6.wireOp",EDGE,"E331"),sQuery(id+"F6.wireOp",EDGE,"E332"),sQuery(id+"F6.wireOp",EDGE,"E333"),sQuery(id+"F6.wireOp",EDGE,"E334"),sQuery(id+"F6.wireOp",EDGE,"E335"),sQuery(id+"F6.wireOp",EDGE,"E336"),sQuery(id+"F6.wireOp",EDGE,"E337"),sQuery(id+"F6.wireOp",EDGE,"E338"),sQuery(id+"F6.wireOp",EDGE,"E339"),sQuery(id+"F6.wireOp",EDGE,"E340"),sQuery(id+"F6.wireOp",EDGE,"E341"),sQuery(id+"F6.wireOp",EDGE,"E342"),sQuery(id+"F6.wireOp",EDGE,"E343"),sQuery(id+"F6.wireOp",EDGE,"E344"),sQuery(id+"F6.wireOp",EDGE,"E345"),sQuery(id+"F6.wireOp",EDGE,"E346"),sQuery(id+"F6.wireOp",EDGE,"E347"),sQuery(id+"F6.wireOp",EDGE,"E348"),sQuery(id+"F6.wireOp",EDGE,"E349"),sQuery(id+"F6.wireOp",EDGE,"E350"),sQuery(id+"F6.wireOp",EDGE,"E351"),sQuery(id+"F6.wireOp",EDGE,"E352"),sQuery(id+"F6.wireOp",EDGE,"E353"),sQuery(id+"F6.wireOp",EDGE,"E354"),sQuery(id+"F6.wireOp",EDGE,"E355"),sQuery(id+"F6.wireOp",EDGE,"E356"),sQuery(id+"F6.wireOp",EDGE,"E357"),sQuery(id+"F6.wireOp",EDGE,"E358"),sQuery(id+"F6.wireOp",EDGE,"E359"),sQuery(id+"F6.wireOp",EDGE,"E360"),sQuery(id+"F6.wireOp",EDGE,"E361"),sQuery(id+"F6.wireOp",EDGE,"E362"),sQuery(id+"F6.wireOp",EDGE,"E363"),sQuery(id+"F6.wireOp",EDGE,"E364"),sQuery(id+"F6.wireOp",EDGE,"E365"),sQuery(id+"F6.wireOp",EDGE,"E366"),sQuery(id+"F6.wireOp",EDGE,"E367"),sQuery(id+"F6.wireOp",EDGE,"E368"),sQuery(id+"F6.wireOp",EDGE,"E369"),sQuery(id+"F6.wireOp",EDGE,"E370"),sQuery(id+"F6.wireOp",EDGE,"E371"),sQuery(id+"F6.wireOp",EDGE,"E372"),sQuery(id+"F6.wireOp",EDGE,"E373"),sQuery(id+"F6.wireOp",EDGE,"E374"),sQuery(id+"F6.wireOp",EDGE,"E375"),sQuery(id+"F6.wireOp",EDGE,"E376"),sQuery(id+"F6.wireOp",EDGE,"E377"),sQuery(id+"F6.wireOp",EDGE,"E378"),sQuery(id+"F6.wireOp",EDGE,"E379"),sQuery(id+"F6.wireOp",EDGE,"E380"),sQuery(id+"F6.wireOp",EDGE,"E381"),sQuery(id+"F6.wireOp",EDGE,"E382"),sQuery(id+"F6.wireOp",EDGE,"E383"),sQuery(id+"F6.wireOp",EDGE,"E384"),sQuery(id+"F6.wireOp",EDGE,"E385"),sQuery(id+"F6.wireOp",EDGE,"E386"),sQuery(id+"F6.wireOp",EDGE,"E387"),sQuery(id+"F6.wireOp",EDGE,"E388"),sQuery(id+"F6.wireOp",EDGE,"E389"),sQuery(id+"F6.wireOp",EDGE,"E390"),sQuery(id+"F6.wireOp",EDGE,"E391"),sQuery(id+"F6.wireOp",EDGE,"E392"),sQuery(id+"F6.wireOp",EDGE,"E393"),sQuery(id+"F6.wireOp",EDGE,"E394"),sQuery(id+"F6.wireOp",EDGE,"E395"),sQuery(id+"F6.wireOp",EDGE,"E396"),sQuery(id+"F6.wireOp",EDGE,"E397"),sQuery(id+"F6.wireOp",EDGE,"E398"),sQuery(id+"F6.wireOp",EDGE,"E399"),sQuery(id+"F6.wireOp",EDGE,"E400"),sQuery(id+"F6.wireOp",EDGE,"E401"),sQuery(id+"F6.wireOp",EDGE,"E402"),sQuery(id+"F6.wireOp",EDGE,"E403"),sQuery(id+"F6.wireOp",EDGE,"E404"),sQuery(id+"F6.wireOp",EDGE,"E405"),sQuery(id+"F6.wireOp",EDGE,"E406"),sQuery(id+"F6.wireOp",EDGE,"E407"),sQuery(id+"F6.wireOp",EDGE,"E408"),sQuery(id+"F6.wireOp",EDGE,"E409"),sQuery(id+"F6.wireOp",EDGE,"E410"),sQuery(id+"F6.wireOp",EDGE,"E411"),sQuery(id+"F6.wireOp",EDGE,"E412"),sQuery(id+"F6.wireOp",EDGE,"E413"),sQuery(id+"F6.wireOp",EDGE,"E414"),sQuery(id+"F6.wireOp",EDGE,"E415"),sQuery(id+"F6.wireOp",EDGE,"E416"),sQuery(id+"F6.wireOp",EDGE,"E417"),sQuery(id+"F6.wireOp",EDGE,"E418"),sQuery(id+"F6.wireOp",EDGE,"E419"),sQuery(id+"F6.wireOp",EDGE,"E420"),sQuery(id+"F6.wireOp",EDGE,"E421"),sQuery(id+"F6.wireOp",EDGE,"E422"),sQuery(id+"F6.wireOp",EDGE,"E423"),sQuery(id+"F6.wireOp",EDGE,"E424"),sQuery(id+"F6.wireOp",EDGE,"E425"),sQuery(id+"F6.wireOp",EDGE,"E426"),sQuery(id+"F6.wireOp",EDGE,"E427"),sQuery(id+"F6.wireOp",EDGE,"E428"),sQuery(id+"F6.wireOp",EDGE,"E429"),sQuery(id+"F6.wireOp",EDGE,"E430"),sQuery(id+"F6.wireOp",EDGE,"E431"),sQuery(id+"F6.wireOp",EDGE,"E432"),sQuery(id+"F6.wireOp",EDGE,"E433"),sQuery(id+"F6.wireOp",EDGE,"E434"),sQuery(id+"F6.wireOp",EDGE,"E435"),sQuery(id+"F6.wireOp",EDGE,"E436"),sQuery(id+"F6.wireOp",EDGE,"E437"),sQuery(id+"F6.wireOp",EDGE,"E438"),sQuery(id+"F6.wireOp",EDGE,"E439"),sQuery(id+"F6.wireOp",EDGE,"E440"),sQuery(id+"F6.wireOp",EDGE,"E441"),sQuery(id+"F6.wireOp",EDGE,"E442"),sQuery(id+"F6.wireOp",EDGE,"E443"),sQuery(id+"F6.wireOp",EDGE,"E444"),sQuery(id+"F6.wireOp",EDGE,"E445"),sQuery(id+"F6.wireOp",EDGE,"E446"),sQuery(id+"F6.wireOp",EDGE,"E447"),sQuery(id+"F6.wireOp",EDGE,"E448"),sQuery(id+"F6.wireOp",EDGE,"E449"),sQuery(id+"F6.wireOp",EDGE,"E450"),sQuery(id+"F6.wireOp",EDGE,"E451"),sQuery(id+"F6.wireOp",EDGE,"E452"),sQuery(id+"F6.wireOp",EDGE,"E453"),sQuery(id+"F6.wireOp",EDGE,"E454"),sQuery(id+"F6.wireOp",EDGE,"E455"),sQuery(id+"F6.wireOp",EDGE,"E456"),sQuery(id+"F6.wireOp",EDGE,"E457"),sQuery(id+"F6.wireOp",EDGE,"E458"),sQuery(id+"F6.wireOp",EDGE,"E459"),sQuery(id+"F6.wireOp",EDGE,"E460"),sQuery(id+"F6.wireOp",EDGE,"E461"),sQuery(id+"F6.wireOp",EDGE,"E462"),sQuery(id+"F6.wireOp",EDGE,"E463"),sQuery(id+"F6.wireOp",EDGE,"E464"),sQuery(id+"F6.wireOp",EDGE,"E465"),sQuery(id+"F6.wireOp",EDGE,"E466"),sQuery(id+"F6.wireOp",EDGE,"E467"),sQuery(id+"F6.wireOp",EDGE,"E468"),sQuery(id+"F6.wireOp",EDGE,"E469"),sQuery(id+"F6.wireOp",EDGE,"E470"),sQuery(id+"F6.wireOp",EDGE,"E471"),sQuery(id+"F6.wireOp",EDGE,"E472"),sQuery(id+"F6.wireOp",EDGE,"E473"),sQuery(id+"F6.wireOp",EDGE,"E474"),sQuery(id+"F6.wireOp",EDGE,"E475"),sQuery(id+"F6.wireOp",EDGE,"E476"),sQuery(id+"F6.wireOp",EDGE,"E477"),sQuery(id+"F6.wireOp",EDGE,"E478"),sQuery(id+"F6.wireOp",EDGE,"E479"),sQuery(id+"F6.wireOp",EDGE,"E480"),sQuery(id+"F6.wireOp",EDGE,"E481"),sQuery(id+"F6.wireOp",EDGE,"E482"),sQuery(id+"F6.wireOp",EDGE,"E483"),sQuery(id+"F6.wireOp",EDGE,"E484"),sQuery(id+"F6.wireOp",EDGE,"E485"),sQuery(id+"F6.wireOp",EDGE,"E486"),sQuery(id+"F6.wireOp",EDGE,"E487"),sQuery(id+"F6.wireOp",EDGE,"E488"),sQuery(id+"F6.wireOp",EDGE,"E489"),sQuery(id+"F6.wireOp",EDGE,"E490"),sQuery(id+"F6.wireOp",EDGE,"E491"),sQuery(id+"F6.wireOp",EDGE,"E492"),sQuery(id+"F6.wireOp",EDGE,"E493"),sQuery(id+"F6.wireOp",EDGE,"E494"),sQuery(id+"F6.wireOp",EDGE,"E495"),sQuery(id+"F6.wireOp",EDGE,"E496"),sQuery(id+"F6.wireOp",EDGE,"E497"),sQuery(id+"F6.wireOp",EDGE,"E498"),sQuery(id+"F6.wireOp",EDGE,"E499"),sQuery(id+"F6.wireOp",EDGE,"E500"),sQuery(id+"F6.wireOp",EDGE,"E501"),sQuery(id+"F6.wireOp",EDGE,"E502"),sQuery(id+"F6.wireOp",EDGE,"E503"),sQuery(id+"F6.wireOp",EDGE,"E504"),sQuery(id+"F6.wireOp",EDGE,"E505"),sQuery(id+"F6.wireOp",EDGE,"E506"),sQuery(id+"F6.wireOp",EDGE,"E507"),sQuery(id+"F6.wireOp",EDGE,"E508"),sQuery(id+"F6.wireOp",EDGE,"E509"),sQuery(id+"F6.wireOp",EDGE,"E510"),sQuery(id+"F6.wireOp",EDGE,"E511"),sQuery(id+"F6.wireOp",EDGE,"E512"),sQuery(id+"F6.wireOp",EDGE,"E513"),sQuery(id+"F6.wireOp",EDGE,"E514"),sQuery(id+"F6.wireOp",EDGE,"E515"),sQuery(id+"F6.wireOp",EDGE,"E516"),sQuery(id+"F6.wireOp",EDGE,"E517"),sQuery(id+"F6.wireOp",EDGE,"E518"),sQuery(id+"F6.wireOp",EDGE,"E519"),sQuery(id+"F6.wireOp",EDGE,"E520"),sQuery(id+"F6.wireOp",EDGE,"E521"),sQuery(id+"F6.wireOp",EDGE,"E522"),sQuery(id+"F6.wireOp",EDGE,"E523"),sQuery(id+"F6.wireOp",EDGE,"E524"),sQuery(id+"F6.wireOp",EDGE,"E525"),sQuery(id+"F6.wireOp",EDGE,"E526"),sQuery(id+"F6.wireOp",EDGE,"E527"),sQuery(id+"F6.wireOp",EDGE,"E528"),sQuery(id+"F6.wireOp",EDGE,"E529"),sQuery(id+"F6.wireOp",EDGE,"E530"),sQuery(id+"F6.wireOp",EDGE,"E531"),sQuery(id+"F6.wireOp",EDGE,"E532"),sQuery(id+"F6.wireOp",EDGE,"E533"),sQuery(id+"F6.wireOp",EDGE,"E534"),sQuery(id+"F6.wireOp",EDGE,"E535"),sQuery(id+"F6.wireOp",EDGE,"E536"),sQuery(id+"F6.wireOp",EDGE,"E537"),sQuery(id+"F6.wireOp",EDGE,"E538"),sQuery(id+"F6.wireOp",EDGE,"E539"),sQuery(id+"F6.wireOp",EDGE,"E540"),sQuery(id+"F6.wireOp",EDGE,"E541"),sQuery(id+"F6.wireOp",EDGE,"E542"),sQuery(id+"F6.wireOp",EDGE,"E543"),sQuery(id+"F6.wireOp",EDGE,"E544"),sQuery(id+"F6.wireOp",EDGE,"E545"),sQuery(id+"F6.wireOp",EDGE,"E546"),sQuery(id+"F6.wireOp",EDGE,"E547"),sQuery(id+"F6.wireOp",EDGE,"E548"),sQuery(id+"F6.wireOp",EDGE,"E549"),sQuery(id+"F6.wireOp",EDGE,"E550"),sQuery(id+"F6.wireOp",EDGE,"E551"),sQuery(id+"F6.wireOp",EDGE,"E552"),sQuery(id+"F6.wireOp",EDGE,"E553"),sQuery(id+"F6.wireOp",EDGE,"E554"),sQuery(id+"F6.wireOp",EDGE,"E555"),sQuery(id+"F6.wireOp",EDGE,"E556"),sQuery(id+"F6.wireOp",EDGE,"E557"),sQuery(id+"F6.wireOp",EDGE,"E558"),sQuery(id+"F6.wireOp",EDGE,"E559"),sQuery(id+"F6.wireOp",EDGE,"E560"),sQuery(id+"F6.wireOp",EDGE,"E561"),sQuery(id+"F6.wireOp",EDGE,"E562"),sQuery(id+"F6.wireOp",EDGE,"E563"),sQuery(id+"F6.wireOp",EDGE,"E564"),sQuery(id+"F6.wireOp",EDGE,"E565"),sQuery(id+"F6.wireOp",EDGE,"E566"),sQuery(id+"F6.wireOp",EDGE,"E567"),sQuery(id+"F6.wireOp",EDGE,"E568"),sQuery(id+"F6.wireOp",EDGE,"E569"),sQuery(id+"F6.wireOp",EDGE,"E570"),sQuery(id+"F6.wireOp",EDGE,"E571"),sQuery(id+"F6.wireOp",EDGE,"E572"),sQuery(id+"F6.wireOp",EDGE,"E573"),sQuery(id+"F6.wireOp",EDGE,"E574"),sQuery(id+"F6.wireOp",EDGE,"E575"),sQuery(id+"F6.wireOp",EDGE,"E576"),sQuery(id+"F6.wireOp",EDGE,"E577"),sQuery(id+"F6.wireOp",EDGE,"E578"),sQuery(id+"F6.wireOp",EDGE,"E579"),sQuery(id+"F6.wireOp",EDGE,"E580"),sQuery(id+"F6.wireOp",EDGE,"E581"),sQuery(id+"F6.wireOp",EDGE,"E582"),sQuery(id+"F6.wireOp",EDGE,"E583"),sQuery(id+"F6.wireOp",EDGE,"E584"),sQuery(id+"F6.wireOp",EDGE,"E585"),sQuery(id+"F6.wireOp",EDGE,"E586"),sQuery(id+"F6.wireOp",EDGE,"E587"),sQuery(id+"F6.wireOp",EDGE,"E588"),sQuery(id+"F6.wireOp",EDGE,"E589"),sQuery(id+"F6.wireOp",EDGE,"E590"),sQuery(id+"F6.wireOp",EDGE,"E591"),sQuery(id+"F6.wireOp",EDGE,"E592"),sQuery(id+"F6.wireOp",EDGE,"E593"),sQuery(id+"F6.wireOp",EDGE,"E594"),sQuery(id+"F6.wireOp",EDGE,"E595"),sQuery(id+"F6.wireOp",EDGE,"E596"),sQuery(id+"F6.wireOp",EDGE,"E597"),sQuery(id+"F6.wireOp",EDGE,"E598"),sQuery(id+"F6.wireOp",EDGE,"E599"),sQuery(id+"F6.wireOp",EDGE,"E600"),sQuery(id+"F6.wireOp",EDGE,"E601"),sQuery(id+"F6.wireOp",EDGE,"E602"),sQuery(id+"F6.wireOp",EDGE,"E603"),sQuery(id+"F6.wireOp",EDGE,"E604"),sQuery(id+"F6.wireOp",EDGE,"E605"),sQuery(id+"F6.wireOp",EDGE,"E606"),sQuery(id+"F6.wireOp",EDGE,"E607"),sQuery(id+"F6.wireOp",EDGE,"E608"),sQuery(id+"F6.wireOp",EDGE,"E609"),sQuery(id+"F6.wireOp",EDGE,"E610"),sQuery(id+"F6.wireOp",EDGE,"E611"),sQuery(id+"F6.wireOp",EDGE,"E612"),sQuery(id+"F6.wireOp",EDGE,"E613"),sQuery(id+"F6.wireOp",EDGE,"E614"),sQuery(id+"F6.wireOp",EDGE,"E615"),sQuery(id+"F6.wireOp",EDGE,"E616"),sQuery(id+"F6.wireOp",EDGE,"E617"),sQuery(id+"F6.wireOp",EDGE,"E618"),sQuery(id+"F6.wireOp",EDGE,"E619"),sQuery(id+"F6.wireOp",EDGE,"E620"),sQuery(id+"F6.wireOp",EDGE,"E621"),sQuery(id+"F6.wireOp",EDGE,"E622"),sQuery(id+"F6.wireOp",EDGE,"E623"),sQuery(id+"F6.wireOp",EDGE,"E624"),sQuery(id+"F6.wireOp",EDGE,"E625"),sQuery(id+"F6.wireOp",EDGE,"E626"),sQuery(id+"F6.wireOp",EDGE,"E627"),sQuery(id+"F6.wireOp",EDGE,"E628"),sQuery(id+"F6.wireOp",EDGE,"E629"),sQuery(id+"F6.wireOp",EDGE,"E630"),sQuery(id+"F6.wireOp",EDGE,"E631"),sQuery(id+"F6.wireOp",EDGE,"E632"),sQuery(id+"F6.wireOp",EDGE,"E633"),sQuery(id+"F6.wireOp",EDGE,"E634"),sQuery(id+"F6.wireOp",EDGE,"E635"),sQuery(id+"F6.wireOp",EDGE,"E636"),sQuery(id+"F6.wireOp",EDGE,"E637"),sQuery(id+"F6.wireOp",EDGE,"E638"),sQuery(id+"F6.wireOp",EDGE,"E639"),sQuery(id+"F6.wireOp",EDGE,"E640"),sQuery(id+"F6.wireOp",EDGE,"E641"),sQuery(id+"F6.wireOp",EDGE,"E642"),sQuery(id+"F6.wireOp",EDGE,"E643"),sQuery(id+"F6.wireOp",EDGE,"E644"),sQuery(id+"F6.wireOp",EDGE,"E645"),sQuery(id+"F6.wireOp",EDGE,"E646"),sQuery(id+"F6.wireOp",EDGE,"E647"),sQuery(id+"F6.wireOp",EDGE,"E648"),sQuery(id+"F6.wireOp",EDGE,"E649"),sQuery(id+"F6.wireOp",EDGE,"E650"),sQuery(id+"F6.wireOp",EDGE,"E651"),sQuery(id+"F6.wireOp",EDGE,"E652"),sQuery(id+"F6.wireOp",EDGE,"E653"),sQuery(id+"F6.wireOp",EDGE,"E654"),sQuery(id+"F6.wireOp",EDGE,"E655"),sQuery(id+"F6.wireOp",EDGE,"E656"),sQuery(id+"F6.wireOp",EDGE,"E657"),sQuery(id+"F6.wireOp",EDGE,"E658"),sQuery(id+"F6.wireOp",EDGE,"E659"),sQuery(id+"F6.wireOp",EDGE,"E660"),sQuery(id+"F6.wireOp",EDGE,"E661"),sQuery(id+"F6.wireOp",EDGE,"E662"),sQuery(id+"F6.wireOp",EDGE,"E663"),sQuery(id+"F6.wireOp",EDGE,"E664"),sQuery(id+"F6.wireOp",EDGE,"E665"),sQuery(id+"F6.wireOp",EDGE,"E666"),sQuery(id+"F6.wireOp",EDGE,"E667"),sQuery(id+"F6.wireOp",EDGE,"E668"),sQuery(id+"F6.wireOp",EDGE,"E669"),sQuery(id+"F6.wireOp",EDGE,"E670"),sQuery(id+"F6.wireOp",EDGE,"E671"),sQuery(id+"F6.wireOp",EDGE,"E672"),sQuery(id+"F6.wireOp",EDGE,"E673"),sQuery(id+"F6.wireOp",EDGE,"E674"),sQuery(id+"F6.wireOp",EDGE,"E675"),sQuery(id+"F6.wireOp",EDGE,"E676"),sQuery(id+"F6.wireOp",EDGE,"E677"),sQuery(id+"F6.wireOp",EDGE,"E678"),sQuery(id+"F6.wireOp",EDGE,"E679"),sQuery(id+"F6.wireOp",EDGE,"E680"),sQuery(id+"F6.wireOp",EDGE,"E681"),sQuery(id+"F6.wireOp",EDGE,"E682"),sQuery(id+"F6.wireOp",EDGE,"E683"),sQuery(id+"F6.wireOp",EDGE,"E684"),sQuery(id+"F6.wireOp",EDGE,"E685"),sQuery(id+"F6.wireOp",EDGE,"E686"),sQuery(id+"F6.wireOp",EDGE,"E687"),sQuery(id+"F6.wireOp",EDGE,"E688"),sQuery(id+"F6.wireOp",EDGE,"E689"),sQuery(id+"F6.wireOp",EDGE,"E690"),sQuery(id+"F6.wireOp",EDGE,"E691"),sQuery(id+"F6.wireOp",EDGE,"E692"),sQuery(id+"F6.wireOp",EDGE,"E693"),sQuery(id+"F6.wireOp",EDGE,"E694"),sQuery(id+"F6.wireOp",EDGE,"E695"),sQuery(id+"F6.wireOp",EDGE,"E696"),sQuery(id+"F6.wireOp",EDGE,"E697"),sQuery(id+"F6.wireOp",EDGE,"E698"),sQuery(id+"F6.wireOp",EDGE,"E699"),sQuery(id+"F6.wireOp",EDGE,"E700"),sQuery(id+"F6.wireOp",EDGE,"E701"),sQuery(id+"F6.wireOp",EDGE,"E702"),sQuery(id+"F6.wireOp",EDGE,"E703"),sQuery(id+"F6.wireOp",EDGE,"E704"),sQuery(id+"F6.wireOp",EDGE,"E705"),sQuery(id+"F6.wireOp",EDGE,"E706"),sQuery(id+"F6.wireOp",EDGE,"E707"),sQuery(id+"F6.wireOp",EDGE,"E708"),sQuery(id+"F6.wireOp",EDGE,"E709"),sQuery(id+"F6.wireOp",EDGE,"E710"),sQuery(id+"F6.wireOp",EDGE,"E711"),sQuery(id+"F6.wireOp",EDGE,"E712"),sQuery(id+"F6.wireOp",EDGE,"E713"),sQuery(id+"F6.wireOp",EDGE,"E714"),sQuery(id+"F6.wireOp",EDGE,"E715"),sQuery(id+"F6.wireOp",EDGE,"E716"),sQuery(id+"F6.wireOp",EDGE,"E717"),sQuery(id+"F6.wireOp",EDGE,"E718"),sQuery(id+"F6.wireOp",EDGE,"E719"),sQuery(id+"F6.wireOp",EDGE,"E720"),sQuery(id+"F6.wireOp",EDGE,"E721"),sQuery(id+"F6.wireOp",EDGE,"E722"),sQuery(id+"F6.wireOp",EDGE,"E723"),sQuery(id+"F6.wireOp",EDGE,"E724"),sQuery(id+"F6.wireOp",EDGE,"E725"),sQuery(id+"F6.wireOp",EDGE,"E726"),sQuery(id+"F6.wireOp",EDGE,"E727"),sQuery(id+"F6.wireOp",EDGE,"E728"),sQuery(id+"F6.wireOp",EDGE,"E729"),sQuery(id+"F6.wireOp",EDGE,"E730"),sQuery(id+"F6.wireOp",EDGE,"E731"),sQuery(id+"F6.wireOp",EDGE,"E732"),sQuery(id+"F6.wireOp",EDGE,"E733"),sQuery(id+"F6.wireOp",EDGE,"E734"),sQuery(id+"F6.wireOp",EDGE,"E735"),sQuery(id+"F6.wireOp",EDGE,"E736"),sQuery(id+"F6.wireOp",EDGE,"E737"),sQuery(id+"F6.wireOp",EDGE,"E738"),sQuery(id+"F6.wireOp",EDGE,"E739"),sQuery(id+"F6.wireOp",EDGE,"E740"),sQuery(id+"F6.wireOp",EDGE,"E741"),sQuery(id+"F6.wireOp",EDGE,"E742"),sQuery(id+"F6.wireOp",EDGE,"E743"),sQuery(id+"F6.wireOp",EDGE,"E744"),sQuery(id+"F6.wireOp",EDGE,"E745"),sQuery(id+"F6.wireOp",EDGE,"E746"),sQuery(id+"F6.wireOp",EDGE,"E747"),sQuery(id+"F6.wireOp",EDGE,"E748"),sQuery(id+"F6.wireOp",EDGE,"E749"),sQuery(id+"F6.wireOp",EDGE,"E750"),sQuery(id+"F6.wireOp",EDGE,"E751"),sQuery(id+"F6.wireOp",EDGE,"E752"),sQuery(id+"F6.wireOp",EDGE,"E753"),sQuery(id+"F6.wireOp",EDGE,"E754"),sQuery(id+"F6.wireOp",EDGE,"E755"),sQuery(id+"F6.wireOp",EDGE,"E756"),sQuery(id+"F6.wireOp",EDGE,"E757"),sQuery(id+"F6.wireOp",EDGE,"E758"),sQuery(id+"F6.wireOp",EDGE,"E759"),sQuery(id+"F6.wireOp",EDGE,"E760"),sQuery(id+"F6.wireOp",EDGE,"E761"),sQuery(id+"F6.wireOp",EDGE,"E762"),sQuery(id+"F6.wireOp",EDGE,"E763"),sQuery(id+"F6.wireOp",EDGE,"E764"),sQuery(id+"F6.wireOp",EDGE,"E765"),sQuery(id+"F6.wireOp",EDGE,"E766"),sQuery(id+"F6.wireOp",EDGE,"E767"),sQuery(id+"F6.wireOp",EDGE,"E768"),sQuery(id+"F6.wireOp",EDGE,"E769"),sQuery(id+"F6.wireOp",EDGE,"E770"),sQuery(id+"F6.wireOp",EDGE,"E771"),sQuery(id+"F6.wireOp",EDGE,"E772"),sQuery(id+"F6.wireOp",EDGE,"E773"),sQuery(id+"F6.wireOp",EDGE,"E774"),sQuery(id+"F6.wireOp",EDGE,"E775"),sQuery(id+"F6.wireOp",EDGE,"E776"),sQuery(id+"F6.wireOp",EDGE,"E777"),sQuery(id+"F6.wireOp",EDGE,"E778"),sQuery(id+"F6.wireOp",EDGE,"E779"),sQuery(id+"F6.wireOp",EDGE,"E780"),sQuery(id+"F6.wireOp",EDGE,"E781"),sQuery(id+"F6.wireOp",EDGE,"E782"),sQuery(id+"F6.wireOp",EDGE,"E783"),sQuery(id+"F6.wireOp",EDGE,"E784"),sQuery(id+"F6.wireOp",EDGE,"E785"),sQuery(id+"F6.wireOp",EDGE,"E786"),sQuery(id+"F6.wireOp",EDGE,"E787"),sQuery(id+"F6.wireOp",EDGE,"E788"),sQuery(id+"F6.wireOp",EDGE,"E789"),sQuery(id+"F6.wireOp",EDGE,"E790"),sQuery(id+"F6.wireOp",EDGE,"E791"),sQuery(id+"F6.wireOp",EDGE,"E792"),sQuery(id+"F6.wireOp",EDGE,"E793"),sQuery(id+"F6.wireOp",EDGE,"E794"),sQuery(id+"F6.wireOp",EDGE,"E795"),sQuery(id+"F6.wireOp",EDGE,"E796"),sQuery(id+"F6.wireOp",EDGE,"E797"),sQuery(id+"F6.wireOp",EDGE,"E798"),sQuery(id+"F6.wireOp",EDGE,"E799"),sQuery(id+"F6.wireOp",EDGE,"E800"),sQuery(id+"F6.wireOp",EDGE,"E801"),sQuery(id+"F6.wireOp",EDGE,"E802"),sQuery(id+"F6.wireOp",EDGE,"E803"),sQuery(id+"F6.wireOp",EDGE,"E804"),sQuery(id+"F6.wireOp",EDGE,"E805"),sQuery(id+"F6.wireOp",EDGE,"E806"),sQuery(id+"F6.wireOp",EDGE,"E807"),sQuery(id+"F6.wireOp",EDGE,"E808"),sQuery(id+"F6.wireOp",EDGE,"E809"),sQuery(id+"F6.wireOp",EDGE,"E810"),sQuery(id+"F6.wireOp",EDGE,"E811"),sQuery(id+"F6.wireOp",EDGE,"E812"),sQuery(id+"F6.wireOp",EDGE,"E813"),sQuery(id+"F6.wireOp",EDGE,"E814"),sQuery(id+"F6.wireOp",EDGE,"E815"),sQuery(id+"F6.wireOp",EDGE,"E816"),sQuery(id+"F6.wireOp",EDGE,"E817"),sQuery(id+"F6.wireOp",EDGE,"E818"),sQuery(id+"F6.wireOp",EDGE,"E819"),sQuery(id+"F6.wireOp",EDGE,"E820"),sQuery(id+"F6.wireOp",EDGE,"E821"),sQuery(id+"F6.wireOp",EDGE,"E822"),sQuery(id+"F6.wireOp",EDGE,"E823"),sQuery(id+"F6.wireOp",EDGE,"E824"),sQuery(id+"F6.wireOp",EDGE,"E825"),sQuery(id+"F6.wireOp",EDGE,"E826"),sQuery(id+"F6.wireOp",EDGE,"E827"),sQuery(id+"F6.wireOp",EDGE,"E828"),sQuery(id+"F6.wireOp",EDGE,"E829"),sQuery(id+"F6.wireOp",EDGE,"E830"),sQuery(id+"F6.wireOp",EDGE,"E831"),sQuery(id+"F6.wireOp",EDGE,"E832"),sQuery(id+"F6.wireOp",EDGE,"E833"),sQuery(id+"F6.wireOp",EDGE,"E834"),sQuery(id+"F6.wireOp",EDGE,"E835"),sQuery(id+"F6.wireOp",EDGE,"E836"),sQuery(id+"F6.wireOp",EDGE,"E837"),sQuery(id+"F6.wireOp",EDGE,"E838"),sQuery(id+"F6.wireOp",EDGE,"E839"),sQuery(id+"F6.wireOp",EDGE,"E840"),sQuery(id+"F6.wireOp",EDGE,"E841"),sQuery(id+"F6.wireOp",EDGE,"E842"),sQuery(id+"F6.wireOp",EDGE,"E843"),sQuery(id+"F6.wireOp",EDGE,"E844"),sQuery(id+"F6.wireOp",EDGE,"E845"),sQuery(id+"F6.wireOp",EDGE,"E846"),sQuery(id+"F6.wireOp",EDGE,"E847"),sQuery(id+"F6.wireOp",EDGE,"E848"),sQuery(id+"F6.wireOp",EDGE,"E849"),sQuery(id+"F6.wireOp",EDGE,"E850"),sQuery(id+"F6.wireOp",EDGE,"E851"),sQuery(id+"F6.wireOp",EDGE,"E852"),sQuery(id+"F6.wireOp",EDGE,"E853"),sQuery(id+"F6.wireOp",EDGE,"E854"),sQuery(id+"F6.wireOp",EDGE,"E855"),sQuery(id+"F6.wireOp",EDGE,"E856"),sQuery(id+"F6.wireOp",EDGE,"E857"),sQuery(id+"F6.wireOp",EDGE,"E858"),sQuery(id+"F6.wireOp",EDGE,"E859"),sQuery(id+"F6.wireOp",EDGE,"E860"),sQuery(id+"F6.wireOp",EDGE,"E861"),sQuery(id+"F6.wireOp",EDGE,"E862"),sQuery(id+"F6.wireOp",EDGE,"E863"),sQuery(id+"F6.wireOp",EDGE,"E864"),sQuery(id+"F6.wireOp",EDGE,"E865"),sQuery(id+"F6.wireOp",EDGE,"E866"),sQuery(id+"F6.wireOp",EDGE,"E867"),sQuery(id+"F6.wireOp",EDGE,"E868"),sQuery(id+"F6.wireOp",EDGE,"E869"),sQuery(id+"F6.wireOp",EDGE,"E870"),sQuery(id+"F6.wireOp",EDGE,"E871"),sQuery(id+"F6.wireOp",EDGE,"E872"),sQuery(id+"F6.wireOp",EDGE,"E873"),sQuery(id+"F6.wireOp",EDGE,"E874"),sQuery(id+"F6.wireOp",EDGE,"E875"),sQuery(id+"F6.wireOp",EDGE,"E876"),sQuery(id+"F6.wireOp",EDGE,"E877"),sQuery(id+"F6.wireOp",EDGE,"E878"),sQuery(id+"F6.wireOp",EDGE,"E879"),sQuery(id+"F6.wireOp",EDGE,"E880"),sQuery(id+"F6.wireOp",EDGE,"E881"),sQuery(id+"F6.wireOp",EDGE,"E882"),sQuery(id+"F6.wireOp",EDGE,"E883"),sQuery(id+"F6.wireOp",EDGE,"E884"),sQuery(id+"F6.wireOp",EDGE,"E885"),sQuery(id+"F6.wireOp",EDGE,"E886"),sQuery(id+"F6.wireOp",EDGE,"E887"),sQuery(id+"F6.wireOp",EDGE,"E888"),sQuery(id+"F6.wireOp",EDGE,"E889"),sQuery(id+"F6.wireOp",EDGE,"E890"),sQuery(id+"F6.wireOp",EDGE,"E891"),sQuery(id+"F6.wireOp",EDGE,"E892"),sQuery(id+"F6.wireOp",EDGE,"E893"),sQuery(id+"F6.wireOp",EDGE,"E894"),sQuery(id+"F6.wireOp",EDGE,"E895"),sQuery(id+"F6.wireOp",EDGE,"E896"),sQuery(id+"F6.wireOp",EDGE,"E897"),sQuery(id+"F6.wireOp",EDGE,"E898"),sQuery(id+"F6.wireOp",EDGE,"E899"),sQuery(id+"F6.wireOp",EDGE,"E900"),sQuery(id+"F6.wireOp",EDGE,"E901"),sQuery(id+"F6.wireOp",EDGE,"E902"),sQuery(id+"F6.wireOp",EDGE,"E903"),sQuery(id+"F6.wireOp",EDGE,"E904"),sQuery(id+"F6.wireOp",EDGE,"E905"),sQuery(id+"F6.wireOp",EDGE,"E906"),sQuery(id+"F6.wireOp",EDGE,"E907"),sQuery(id+"F6.wireOp",EDGE,"E908"),sQuery(id+"F6.wireOp",EDGE,"E909"),sQuery(id+"F6.wireOp",EDGE,"E910"),sQuery(id+"F6.wireOp",EDGE,"E911"),sQuery(id+"F6.wireOp",EDGE,"E911"),sQuery(id+"F6.wireOp",EDGE,"E912"),sQuery(id+"F6.wireOp",EDGE,"E913"),sQuery(id+"F6.wireOp",EDGE,"E914"),sQuery(id+"F6.wireOp",EDGE,"E915"),sQuery(id+"F6.wireOp",EDGE,"E916"),sQuery(id+"F6.wireOp",EDGE,"E917"),sQuery(id+"F6.wireOp",EDGE,"E918"),sQuery(id+"F6.wireOp",EDGE,"E919"),sQuery(id+"F6.wireOp",EDGE,"E920"),sQuery(id+"F6.wireOp",EDGE,"E921"),sQuery(id+"F6.wireOp",EDGE,"E922"),sQuery(id+"F6.wireOp",EDGE,"E923"),sQuery(id+"F6.wireOp",EDGE,"E924"),sQuery(id+"F6.wireOp",EDGE,"E925"),sQuery(id+"F6.wireOp",EDGE,"E926"),sQuery(id+"F6.wireOp",EDGE,"E927"),sQuery(id+"F6.wireOp",EDGE,"E928"),sQuery(id+"F6.wireOp",EDGE,"E929"),sQuery(id+"F6.wireOp",EDGE,"E930"),sQuery(id+"F6.wireOp",EDGE,"E931"),sQuery(id+"F6.wireOp",EDGE,"E932"),sQuery(id+"F6.wireOp",EDGE,"E933"),sQuery(id+"F6.wireOp",EDGE,"E934"),sQuery(id+"F6.wireOp",EDGE,"E935"),sQuery(id+"F6.wireOp",EDGE,"E936"),sQuery(id+"F6.wireOp",EDGE,"E937"),sQuery(id+"F6.wireOp",EDGE,"E938"),sQuery(id+"F6.wireOp",EDGE,"E939"),sQuery(id+"F6.wireOp",EDGE,"E940"),sQuery(id+"F6.wireOp",EDGE,"E941"),sQuery(id+"F6.wireOp",EDGE,"E942"),sQuery(id+"F6.wireOp",EDGE,"E943"),sQuery(id+"F6.wireOp",EDGE,"E944"),sQuery(id+"F6.wireOp",EDGE,"E945"),sQuery(id+"F6.wireOp",EDGE,"E946"),sQuery(id+"F6.wireOp",EDGE,"E947"),sQuery(id+"F6.wireOp",EDGE,"E948"),sQuery(id+"F6.wireOp",EDGE,"E949"),sQuery(id+"F6.wireOp",EDGE,"E950"),sQuery(id+"F6.wireOp",EDGE,"E951"),sQuery(id+"F6.wireOp",EDGE,"E952"),sQuery(id+"F6.wireOp",EDGE,"E953"),sQuery(id+"F6.wireOp",EDGE,"E954"),sQuery(id+"F6.wireOp",EDGE,"E955"),sQuery(id+"F6.wireOp",EDGE,"E956"),sQuery(id+"F6.wireOp",EDGE,"E957"),sQuery(id+"F6.wireOp",EDGE,"E958"),sQuery(id+"F6.wireOp",EDGE,"E959"),sQuery(id+"F6.wireOp",EDGE,"E960"),sQuery(id+"F6.wireOp",EDGE,"E961"),sQuery(id+"F6.wireOp",EDGE,"E962"),sQuery(id+"F6.wireOp",EDGE,"E963"),sQuery(id+"F6.wireOp",EDGE,"E964"),sQuery(id+"F6.wireOp",EDGE,"E965"),sQuery(id+"F6.wireOp",EDGE,"E966"),sQuery(id+"F6.wireOp",EDGE,"E967"),sQuery(id+"F6.wireOp",EDGE,"E968"),sQuery(id+"F6.wireOp",EDGE,"E969"),sQuery(id+"F6.wireOp",EDGE,"E970"),sQuery(id+"F6.wireOp",EDGE,"E971"),sQuery(id+"F6.wireOp",EDGE,"E972"),sQuery(id+"F6.wireOp",EDGE,"E973"),sQuery(id+"F6.wireOp",EDGE,"E974"),sQuery(id+"F6.wireOp",EDGE,"E975"),sQuery(id+"F6.wireOp",EDGE,"E976"),sQuery(id+"F6.wireOp",EDGE,"E977"),sQuery(id+"F6.wireOp",EDGE,"E978"),sQuery(id+"F6.wireOp",EDGE,"E979"),sQuery(id+"F6.wireOp",EDGE,"E980"),sQuery(id+"F6.wireOp",EDGE,"E981"),sQuery(id+"F6.wireOp",EDGE,"E982"),sQuery(id+"F6.wireOp",EDGE,"E983"),sQuery(id+"F6.wireOp",EDGE,"E984"),sQuery(id+"F6.wireOp",EDGE,"E985"),sQuery(id+"F6.wireOp",EDGE,"E986"),sQuery(id+"F6.wireOp",EDGE,"E987"),sQuery(id+"F6.wireOp",EDGE,"E988"),sQuery(id+"F6.wireOp",EDGE,"E989"),sQuery(id+"F6.wireOp",EDGE,"E990"),sQuery(id+"F6.wireOp",EDGE,"E991"),sQuery(id+"F6.wireOp",EDGE,"E992"),sQuery(id+"F6.wireOp",EDGE,"E993"),sQuery(id+"F6.wireOp",EDGE,"E994"),sQuery(id+"F6.wireOp",EDGE,"E995"),sQuery(id+"F6.wireOp",EDGE,"E996"),sQuery(id+"F6.wireOp",EDGE,"E997"),sQuery(id+"F6.wireOp",EDGE,"E998"),sQuery(id+"F6.wireOp",EDGE,"E999"),sQuery(id+"F6.wireOp",EDGE,"E1000"),sQuery(id+"F6.wireOp",EDGE,"E1001"),sQuery(id+"F6.wireOp",EDGE,"E1002"),sQuery(id+"F6.wireOp",EDGE,"E1003"),sQuery(id+"F6.wireOp",EDGE,"E1004"),sQuery(id+"F6.wireOp",EDGE,"E1005"),sQuery(id+"F6.wireOp",EDGE,"E1006"),sQuery(id+"F6.wireOp",EDGE,"E1007"),sQuery(id+"F6.wireOp",EDGE,"E1008"),sQuery(id+"F6.wireOp",EDGE,"E1009"),sQuery(id+"F6.wireOp",EDGE,"E1010"),sQuery(id+"F6.wireOp",EDGE,"E1011"),sQuery(id+"F6.wireOp",EDGE,"E1012"),sQuery(id+"F6.wireOp",EDGE,"E1013"),sQuery(id+"F6.wireOp",EDGE,"E1014"),sQuery(id+"F6.wireOp",EDGE,"E1015"),sQuery(id+"F6.wireOp",EDGE,"E1016"),sQuery(id+"F6.wireOp",EDGE,"E1017"),sQuery(id+"F6.wireOp",EDGE,"E1018"),sQuery(id+"F6.wireOp",EDGE,"E1019"),sQuery(id+"F6.wireOp",EDGE,"E1020"),sQuery(id+"F6.wireOp",EDGE,"E1021"),sQuery(id+"F6.wireOp",EDGE,"E1022"),sQuery(id+"F6.wireOp",EDGE,"E1023"),sQuery(id+"F6.wireOp",EDGE,"E1024"),sQuery(id+"F6.wireOp",EDGE,"E1025"),sQuery(id+"F6.wireOp",EDGE,"E1026"),sQuery(id+"F6.wireOp",EDGE,"E1027"),sQuery(id+"F6.wireOp",EDGE,"E1028"),sQuery(id+"F6.wireOp",EDGE,"E1029"),sQuery(id+"F6.wireOp",EDGE,"E1030"),sQuery(id+"F6.wireOp",EDGE,"E1031"),sQuery(id+"F6.wireOp",EDGE,"E1032"),sQuery(id+"F6.wireOp",EDGE,"E1033"),sQuery(id+"F6.wireOp",EDGE,"E1034"),sQuery(id+"F6.wireOp",EDGE,"E1035"),sQuery(id+"F6.wireOp",EDGE,"E1036"),sQuery(id+"F6.wireOp",EDGE,"E1037"),sQuery(id+"F6.wireOp",EDGE,"E1038"),sQuery(id+"F6.wireOp",EDGE,"E1039"),sQuery(id+"F6.wireOp",EDGE,"E1040"),sQuery(id+"F6.wireOp",EDGE,"E1041"),sQuery(id+"F6.wireOp",EDGE,"E1042"),sQuery(id+"F6.wireOp",EDGE,"E1043"),sQuery(id+"F6.wireOp",EDGE,"E1044"),sQuery(id+"F6.wireOp",EDGE,"E1045"),sQuery(id+"F6.wireOp",EDGE,"E1046"),sQuery(id+"F6.wireOp",EDGE,"E1047"),sQuery(id+"F6.wireOp",EDGE,"E1048"),sQuery(id+"F6.wireOp",EDGE,"E1049"),sQuery(id+"F6.wireOp",EDGE,"E1050"),sQuery(id+"F6.wireOp",EDGE,"E1051"),sQuery(id+"F6.wireOp",EDGE,"E1052"),sQuery(id+"F6.wireOp",EDGE,"E1053"),sQuery(id+"F6.wireOp",EDGE,"E1054"),sQuery(id+"F6.wireOp",EDGE,"E1055"),sQuery(id+"F6.wireOp",EDGE,"E1056"),sQuery(id+"F6.wireOp",EDGE,"E1057"),sQuery(id+"F6.wireOp",EDGE,"E1058"),sQuery(id+"F6.wireOp",EDGE,"E1059"),sQuery(id+"F6.wireOp",EDGE,"E1060"),sQuery(id+"F6.wireOp",EDGE,"E1061"),sQuery(id+"F6.wireOp",EDGE,"E1062"),sQuery(id+"F6.wireOp",EDGE,"E1063"),sQuery(id+"F6.wireOp",EDGE,"E1064"),sQuery(id+"F6.wireOp",EDGE,"E1065"),sQuery(id+"F6.wireOp",EDGE,"E1066"),sQuery(id+"F6.wireOp",EDGE,"E1067"),sQuery(id+"F6.wireOp",EDGE,"E1068"),sQuery(id+"F6.wireOp",EDGE,"E1069"),sQuery(id+"F6.wireOp",EDGE,"E1070"),sQuery(id+"F6.wireOp",EDGE,"E1071"),sQuery(id+"F6.wireOp",EDGE,"E1072"),sQuery(id+"F6.wireOp",EDGE,"E1073"),sQuery(id+"F6.wireOp",EDGE,"E1074"),sQuery(id+"F6.wireOp",EDGE,"E1075"),sQuery(id+"F6.wireOp",EDGE,"E1076"),sQuery(id+"F6.wireOp",EDGE,"E1077"),sQuery(id+"F6.wireOp",EDGE,"E1078"),sQuery(id+"F6.wireOp",EDGE,"E1079"),sQuery(id+"F6.wireOp",EDGE,"E1080"),sQuery(id+"F6.wireOp",EDGE,"E1081"),sQuery(id+"F6.wireOp",EDGE,"E1082"),sQuery(id+"F6.wireOp",EDGE,"E1083"),sQuery(id+"F6.wireOp",EDGE,"E1084"),sQuery(id+"F6.wireOp",EDGE,"E1085"),sQuery(id+"F6.wireOp",EDGE,"E1086"),sQuery(id+"F6.wireOp",EDGE,"E1087"),sQuery(id+"F6.wireOp",EDGE,"E1088"),sQuery(id+"F6.wireOp",EDGE,"E1089"),sQuery(id+"F6.wireOp",EDGE,"E1090"),sQuery(id+"F6.wireOp",EDGE,"E1091"),sQuery(id+"F6.wireOp",EDGE,"E1092"),sQuery(id+"F6.wireOp",EDGE,"E1093"),sQuery(id+"F6.wireOp",EDGE,"E1094"),sQuery(id+"F6.wireOp",EDGE,"E1095"),sQuery(id+"F6.wireOp",EDGE,"E1096"),sQuery(id+"F6.wireOp",EDGE,"E1097"),sQuery(id+"F6.wireOp",EDGE,"E1098"),sQuery(id+"F6.wireOp",EDGE,"E1099"),sQuery(id+"F6.wireOp",EDGE,"E1100"),sQuery(id+"F6.wireOp",EDGE,"E1101"),sQuery(id+"F6.wireOp",EDGE,"E1102"),sQuery(id+"F6.wireOp",EDGE,"E1103"),sQuery(id+"F6.wireOp",EDGE,"E1104"),sQuery(id+"F6.wireOp",EDGE,"E1105"),sQuery(id+"F6.wireOp",EDGE,"E1106"),sQuery(id+"F6.wireOp",EDGE,"E1107"),sQuery(id+"F6.wireOp",EDGE,"E1108"),sQuery(id+"F6.wireOp",EDGE,"E1109"),sQuery(id+"F6.wireOp",EDGE,"E1110"),sQuery(id+"F6.wireOp",EDGE,"E1111"),sQuery(id+"F6.wireOp",EDGE,"E1112"),sQuery(id+"F6.wireOp",EDGE,"E1113"),sQuery(id+"F6.wireOp",EDGE,"E1114"),sQuery(id+"F6.wireOp",EDGE,"E1115"),sQuery(id+"F6.wireOp",EDGE,"E1116"),sQuery(id+"F6.wireOp",EDGE,"E1117"),sQuery(id+"F6.wireOp",EDGE,"E1118"),sQuery(id+"F6.wireOp",EDGE,"E1119"),sQuery(id+"F6.wireOp",EDGE,"E1120"),sQuery(id+"F6.wireOp",EDGE,"E1121"),sQuery(id+"F6.wireOp",EDGE,"E1122"),sQuery(id+"F6.wireOp",EDGE,"E1123"),sQuery(id+"F6.wireOp",EDGE,"E1124"),sQuery(id+"F6.wireOp",EDGE,"E1125"),sQuery(id+"F6.wireOp",EDGE,"E1126"),sQuery(id+"F6.wireOp",EDGE,"E1127"),sQuery(id+"F6.wireOp",EDGE,"E1128"),sQuery(id+"F6.wireOp",EDGE,"E1129"),sQuery(id+"F6.wireOp",EDGE,"E1130"),sQuery(id+"F6.wireOp",EDGE,"E1131"),sQuery(id+"F6.wireOp",EDGE,"E1132"),sQuery(id+"F6.wireOp",EDGE,"E1133"),sQuery(id+"F6.wireOp",EDGE,"E1134"),sQuery(id+"F6.wireOp",EDGE,"E1135"),sQuery(id+"F6.wireOp",EDGE,"E1136"),sQuery(id+"F6.wireOp",EDGE,"E1137"),sQuery(id+"F6.wireOp",EDGE,"E1138"),sQuery(id+"F6.wireOp",EDGE,"E1139"),sQuery(id+"F6.wireOp",EDGE,"E1140"),sQuery(id+"F6.wireOp",EDGE,"E1141"),sQuery(id+"F6.wireOp",EDGE,"E1142"),sQuery(id+"F6.wireOp",EDGE,"E1143"),sQuery(id+"F6.wireOp",EDGE,"E1144"),sQuery(id+"F6.wireOp",EDGE,"E1145"),sQuery(id+"F6.wireOp",EDGE,"E1146"),sQuery(id+"F6.wireOp",EDGE,"E1147"),sQuery(id+"F6.wireOp",EDGE,"E1148"),sQuery(id+"F6.wireOp",EDGE,"E1149"),sQuery(id+"F6.wireOp",EDGE,"E1150"),sQuery(id+"F6.wireOp",EDGE,"E1151"),sQuery(id+"F6.wireOp",EDGE,"E1152"),sQuery(id+"F6.wireOp",EDGE,"E1153"),sQuery(id+"F6.wireOp",EDGE,"E1154"),sQuery(id+"F6.wireOp",EDGE,"E1155"),sQuery(id+"F6.wireOp",EDGE,"E1156"),sQuery(id+"F6.wireOp",EDGE,"E1157"),sQuery(id+"F6.wireOp",EDGE,"E1158"),sQuery(id+"F6.wireOp",EDGE,"E1159"),sQuery(id+"F6.wireOp",EDGE,"E1160"),sQuery(id+"F6.wireOp",EDGE,"E1161"),sQuery(id+"F6.wireOp",EDGE,"E1162"),sQuery(id+"F6.wireOp",EDGE,"E1163"),sQuery(id+"F6.wireOp",EDGE,"E1164"),sQuery(id+"F6.wireOp",EDGE,"E1165"),sQuery(id+"F6.wireOp",EDGE,"E1166"),sQuery(id+"F6.wireOp",EDGE,"E1167"),sQuery(id+"F6.wireOp",EDGE,"E1168"),sQuery(id+"F6.wireOp",EDGE,"E1169"),sQuery(id+"F6.wireOp",EDGE,"E1170"),sQuery(id+"F6.wireOp",EDGE,"E1171"),sQuery(id+"F6.wireOp",EDGE,"E1172"),sQuery(id+"F6.wireOp",EDGE,"E1173"),sQuery(id+"F6.wireOp",EDGE,"E1174"),sQuery(id+"F6.wireOp",EDGE,"E1175"),sQuery(id+"F6.wireOp",EDGE,"E1176"),sQuery(id+"F6.wireOp",EDGE,"E1177"),sQuery(id+"F6.wireOp",EDGE,"E1178"),sQuery(id+"F6.wireOp",EDGE,"E1179"),sQuery(id+"F6.wireOp",EDGE,"E1180"),sQuery(id+"F6.wireOp",EDGE,"E1181"),sQuery(id+"F6.wireOp",EDGE,"E1182"),sQuery(id+"F6.wireOp",EDGE,"E1183"),sQuery(id+"F6.wireOp",EDGE,"E1184"),sQuery(id+"F6.wireOp",EDGE,"E1185"),sQuery(id+"F6.wireOp",EDGE,"E1186"),sQuery(id+"F6.wireOp",EDGE,"E1187"),sQuery(id+"F6.wireOp",EDGE,"E1188"),sQuery(id+"F6.wireOp",EDGE,"E1189"),sQuery(id+"F6.wireOp",EDGE,"E1190"),sQuery(id+"F6.wireOp",EDGE,"E1191"),sQuery(id+"F6.wireOp",EDGE,"E1192"),sQuery(id+"F6.wireOp",EDGE,"E1193"),sQuery(id+"F6.wireOp",EDGE,"E1194"),sQuery(id+"F6.wireOp",EDGE,"E1195"),sQuery(id+"F6.wireOp",EDGE,"E1196"),sQuery(id+"F6.wireOp",EDGE,"E1197"),sQuery(id+"F6.wireOp",EDGE,"E1198"),sQuery(id+"F6.wireOp",EDGE,"E1199"),sQuery(id+"F6.wireOp",EDGE,"E1200"),sQuery(id+"F6.wireOp",EDGE,"E1201"),sQuery(id+"F6.wireOp",EDGE,"E1202"),sQuery(id+"F6.wireOp",EDGE,"E1203"),sQuery(id+"F6.wireOp",EDGE,"E1204"),sQuery(id+"F6.wireOp",EDGE,"E1205"),sQuery(id+"F6.wireOp",EDGE,"E1206"),sQuery(id+"F6.wireOp",EDGE,"E1207"),sQuery(id+"F6.wireOp",EDGE,"E1208"),sQuery(id+"F6.wireOp",EDGE,"E1209"),sQuery(id+"F6.wireOp",EDGE,"E1210"),sQuery(id+"F6.wireOp",EDGE,"E1211"),sQuery(id+"F6.wireOp",EDGE,"E1212"),sQuery(id+"F6.wireOp",EDGE,"E1213"),sQuery(id+"F6.wireOp",EDGE,"E1214"),sQuery(id+"F6.wireOp",EDGE,"E1215"),sQuery(id+"F6.wireOp",EDGE,"E1216"),sQuery(id+"F6.wireOp",EDGE,"E1217"),sQuery(id+"F6.wireOp",EDGE,"E1218"),sQuery(id+"F6.wireOp",EDGE,"E1219"),sQuery(id+"F6.wireOp",EDGE,"E1220"),sQuery(id+"F6.wireOp",EDGE,"E1221"),sQuery(id+"F6.wireOp",EDGE,"E1222"),sQuery(id+"F6.wireOp",EDGE,"E1223"),sQuery(id+"F6.wireOp",EDGE,"E1224"),sQuery(id+"F6.wireOp",EDGE,"E1225"),sQuery(id+"F6.wireOp",EDGE,"E1226"),sQuery(id+"F6.wireOp",EDGE,"E1227"),sQuery(id+"F6.wireOp",EDGE,"E1228"),sQuery(id+"F6.wireOp",EDGE,"E1229"),sQuery(id+"F6.wireOp",EDGE,"E1230"),sQuery(id+"F6.wireOp",EDGE,"E1231"),sQuery(id+"F6.wireOp",EDGE,"E1232"),sQuery(id+"F6.wireOp",EDGE,"E1233"),sQuery(id+"F6.wireOp",EDGE,"E1234"),sQuery(id+"F6.wireOp",EDGE,"E1235"),sQuery(id+"F6.wireOp",EDGE,"E1236"),sQuery(id+"F6.wireOp",EDGE,"E1237"),sQuery(id+"F6.wireOp",EDGE,"E1238"),sQuery(id+"F6.wireOp",EDGE,"E1239"),sQuery(id+"F6.wireOp",EDGE,"E1240"),sQuery(id+"F6.wireOp",EDGE,"E1241"),sQuery(id+"F6.wireOp",EDGE,"E1242"),sQuery(id+"F6.wireOp",EDGE,"E1243"),sQuery(id+"F6.wireOp",EDGE,"E1244"),sQuery(id+"F6.wireOp",EDGE,"E1245"),sQuery(id+"F6.wireOp",EDGE,"E1246"),sQuery(id+"F6.wireOp",EDGE,"E1247"),sQuery(id+"F6.wireOp",EDGE,"E1248"),sQuery(id+"F6.wireOp",EDGE,"E1249"),sQuery(id+"F6.wireOp",EDGE,"E1250"),sQuery(id+"F6.wireOp",EDGE,"E1251"),sQuery(id+"F6.wireOp",EDGE,"E1252"),sQuery(id+"F6.wireOp",EDGE,"E1253"),sQuery(id+"F6.wireOp",EDGE,"E1254"),sQuery(id+"F6.wireOp",EDGE,"E1255"),sQuery(id+"F6.wireOp",EDGE,"E1256"),sQuery(id+"F6.wireOp",EDGE,"E1257"),sQuery(id+"F6.wireOp",EDGE,"E1258"),sQuery(id+"F6.wireOp",EDGE,"E1259"),sQuery(id+"F6.wireOp",EDGE,"E1260"),sQuery(id+"F6.wireOp",EDGE,"E1261"),sQuery(id+"F6.wireOp",EDGE,"E1262"),sQuery(id+"F6.wireOp",EDGE,"E1263"),sQuery(id+"F6.wireOp",EDGE,"E1264"),sQuery(id+"F6.wireOp",EDGE,"E1265"),sQuery(id+"F6.wireOp",EDGE,"E1266"),sQuery(id+"F6.wireOp",EDGE,"E1267"),sQuery(id+"F6.wireOp",EDGE,"E1268"),sQuery(id+"F6.wireOp",EDGE,"E1269"),sQuery(id+"F6.wireOp",EDGE,"E1270"),sQuery(id+"F6.wireOp",EDGE,"E1271"),sQuery(id+"F6.wireOp",EDGE,"E1272"),sQuery(id+"F6.wireOp",EDGE,"E1273"),sQuery(id+"F6.wireOp",EDGE,"E1274"),sQuery(id+"F6.wireOp",EDGE,"E1275"),sQuery(id+"F6.wireOp",EDGE,"E1276"),sQuery(id+"F6.wireOp",EDGE,"E1277"),sQuery(id+"F6.wireOp",EDGE,"E1278"),sQuery(id+"F6.wireOp",EDGE,"E1279"),sQuery(id+"F6.wireOp",EDGE,"E1280"),sQuery(id+"F6.wireOp",EDGE,"E1281"),sQuery(id+"F6.wireOp",EDGE,"E1282"),sQuery(id+"F6.wireOp",EDGE,"E1283"),sQuery(id+"F6.wireOp",EDGE,"E1284"),sQuery(id+"F6.wireOp",EDGE,"E1285"),sQuery(id+"F6.wireOp",EDGE,"E1286"),sQuery(id+"F6.wireOp",EDGE,"E1287"),sQuery(id+"F6.wireOp",EDGE,"E1288"),sQuery(id+"F6.wireOp",EDGE,"E1289"),sQuery(id+"F6.wireOp",EDGE,"E1290"),sQuery(id+"F6.wireOp",EDGE,"E1291"),sQuery(id+"F6.wireOp",EDGE,"E1292"),sQuery(id+"F6.wireOp",EDGE,"E1293"),sQuery(id+"F6.wireOp",EDGE,"E1294"),sQuery(id+"F6.wireOp",EDGE,"E1295"),sQuery(id+"F6.wireOp",EDGE,"E1296"),sQuery(id+"F6.wireOp",EDGE,"E1297"),sQuery(id+"F6.wireOp",EDGE,"E1298"),sQuery(id+"F6.wireOp",EDGE,"E1299"),sQuery(id+"F6.wireOp",EDGE,"E1300"),sQuery(id+"F6.wireOp",EDGE,"E1301"),sQuery(id+"F6.wireOp",EDGE,"E1302"),sQuery(id+"F6.wireOp",EDGE,"E1303"),sQuery(id+"F6.wireOp",EDGE,"E1304"),sQuery(id+"F6.wireOp",EDGE,"E1305"),sQuery(id+"F6.wireOp",EDGE,"E1306"),sQuery(id+"F6.wireOp",EDGE,"E1307"),sQuery(id+"F6.wireOp",EDGE,"E1308"),sQuery(id+"F6.wireOp",EDGE,"E1309"),sQuery(id+"F6.wireOp",EDGE,"E1310"),sQuery(id+"F6.wireOp",EDGE,"E1311"),sQuery(id+"F6.wireOp",EDGE,"E1312"),sQuery(id+"F6.wireOp",EDGE,"E1313"),sQuery(id+"F6.wireOp",EDGE,"E1314"),sQuery(id+"F6.wireOp",EDGE,"E1315"),sQuery(id+"F6.wireOp",EDGE,"E1316"),sQuery(id+"F6.wireOp",EDGE,"E1317"),sQuery(id+"F6.wireOp",EDGE,"E1318"),sQuery(id+"F6.wireOp",EDGE,"E1319"),sQuery(id+"F6.wireOp",EDGE,"E1320"),sQuery(id+"F6.wireOp",EDGE,"E1321"),sQuery(id+"F6.wireOp",EDGE,"E1322"),sQuery(id+"F6.wireOp",EDGE,"E1323"),sQuery(id+"F6.wireOp",EDGE,"E1324"),sQuery(id+"F6.wireOp",EDGE,"E1325"),sQuery(id+"F6.wireOp",EDGE,"E1326"),sQuery(id+"F6.wireOp",EDGE,"E1327"),sQuery(id+"F6.wireOp",EDGE,"E1328"),sQuery(id+"F6.wireOp",EDGE,"E1329"),sQuery(id+"F6.wireOp",EDGE,"E1330"),sQuery(id+"F6.wireOp",EDGE,"E1331"),sQuery(id+"F6.wireOp",EDGE,"E1332"),sQuery(id+"F6.wireOp",EDGE,"E1333"),sQuery(id+"F6.wireOp",EDGE,"E1334"),sQuery(id+"F6.wireOp",EDGE,"E1335"),sQuery(id+"F6.wireOp",EDGE,"E1336"),sQuery(id+"F6.wireOp",EDGE,"E1337"),sQuery(id+"F6.wireOp",EDGE,"E1338"),sQuery(id+"F6.wireOp",EDGE,"E1339"),sQuery(id+"F6.wireOp",EDGE,"E1340"),sQuery(id+"F6.wireOp",EDGE,"E1341"),sQuery(id+"F6.wireOp",EDGE,"E1342"),sQuery(id+"F6.wireOp",EDGE,"E1343"),sQuery(id+"F6.wireOp",EDGE,"E1344"),sQuery(id+"F6.wireOp",EDGE,"E1345"),sQuery(id+"F6.wireOp",EDGE,"E1346"),sQuery(id+"F6.wireOp",EDGE,"E1347"),sQuery(id+"F6.wireOp",EDGE,"E1348"),sQuery(id+"F6.wireOp",EDGE,"E1349"),sQuery(id+"F6.wireOp",EDGE,"E1350"),sQuery(id+"F6.wireOp",EDGE,"E1351"),sQuery(id+"F6.wireOp",EDGE,"E1352"),sQuery(id+"F6.wireOp",EDGE,"E1353"),sQuery(id+"F6.wireOp",EDGE,"E1354"),sQuery(id+"F6.wireOp",EDGE,"E1355"),sQuery(id+"F6.wireOp",EDGE,"E1356"),sQuery(id+"F6.wireOp",EDGE,"E1357"),sQuery(id+"F6.wireOp",EDGE,"E1358"),sQuery(id+"F6.wireOp",EDGE,"E1359"),sQuery(id+"F6.wireOp",EDGE,"E1360"),sQuery(id+"F6.wireOp",EDGE,"E1361"),sQuery(id+"F6.wireOp",EDGE,"E1362"),sQuery(id+"F6.wireOp",EDGE,"E1363"),sQuery(id+"F6.wireOp",EDGE,"E1364"),sQuery(id+"F6.wireOp",EDGE,"E1365"),sQuery(id+"F6.wireOp",EDGE,"E1366"),sQuery(id+"F6.wireOp",EDGE,"E1367"),sQuery(id+"F6.wireOp",EDGE,"E1368"),sQuery(id+"F6.wireOp",EDGE,"E1369"),sQuery(id+"F6.wireOp",EDGE,"E1370"),sQuery(id+"F6.wireOp",EDGE,"E1371"),sQuery(id+"F6.wireOp",EDGE,"E1372"),sQuery(id+"F6.wireOp",EDGE,"E1373"),sQuery(id+"F6.wireOp",EDGE,"E1374"),sQuery(id+"F6.wireOp",EDGE,"E1375"),sQuery(id+"F6.wireOp",EDGE,"E1376"),sQuery(id+"F6.wireOp",EDGE,"E1377"),sQuery(id+"F6.wireOp",EDGE,"E1378"),sQuery(id+"F6.wireOp",EDGE,"E1379"),sQuery(id+"F6.wireOp",EDGE,"E1380"),sQuery(id+"F6.wireOp",EDGE,"E1381"),sQuery(id+"F6.wireOp",EDGE,"E1382"),sQuery(id+"F6.wireOp",EDGE,"E1383"),sQuery(id+"F6.wireOp",EDGE,"E1384"),sQuery(id+"F6.wireOp",EDGE,"E1385"),sQuery(id+"F6.wireOp",EDGE,"E1386"),sQuery(id+"F6.wireOp",EDGE,"E1387"),sQuery(id+"F6.wireOp",EDGE,"E1388"),sQuery(id+"F6.wireOp",EDGE,"E1389"),sQuery(id+"F6.wireOp",EDGE,"E1390"),sQuery(id+"F6.wireOp",EDGE,"E1391"),sQuery(id+"F6.wireOp",EDGE,"E1392"),sQuery(id+"F6.wireOp",EDGE,"E1393"),sQuery(id+"F6.wireOp",EDGE,"E1394"),sQuery(id+"F6.wireOp",EDGE,"E1395"),sQuery(id+"F6.wireOp",EDGE,"E1396"),sQuery(id+"F6.wireOp",EDGE,"E1397"),sQuery(id+"F6.wireOp",EDGE,"E1398"),sQuery(id+"F6.wireOp",EDGE,"E1399"),sQuery(id+"F6.wireOp",EDGE,"E1400"),sQuery(id+"F6.wireOp",EDGE,"E1401"),sQuery(id+"F6.wireOp",EDGE,"E1402"),sQuery(id+"F6.wireOp",EDGE,"E1403"),sQuery(id+"F6.wireOp",EDGE,"E1404"),sQuery(id+"F6.wireOp",EDGE,"E1405"),sQuery(id+"F6.wireOp",EDGE,"E1406"),sQuery(id+"F6.wireOp",EDGE,"E1407"),sQuery(id+"F6.wireOp",EDGE,"E1408"),sQuery(id+"F6.wireOp",EDGE,"E1409"),sQuery(id+"F6.wireOp",EDGE,"E1410"),sQuery(id+"F6.wireOp",EDGE,"E1411"),sQuery(id+"F6.wireOp",EDGE,"E1412"),sQuery(id+"F6.wireOp",EDGE,"E1413"),sQuery(id+"F6.wireOp",EDGE,"E1414"),sQuery(id+"F6.wireOp",EDGE,"E1415"),sQuery(id+"F6.wireOp",EDGE,"E1416"),sQuery(id+"F6.wireOp",EDGE,"E1417"),sQuery(id+"F6.wireOp",EDGE,"E1418"),sQuery(id+"F6.wireOp",EDGE,"E1419"),sQuery(id+"F6.wireOp",EDGE,"E1420"),sQuery(id+"F6.wireOp",EDGE,"E1421"),sQuery(id+"F6.wireOp",EDGE,"E1422"),sQuery(id+"F6.wireOp",EDGE,"E1423"),sQuery(id+"F6.wireOp",EDGE,"E1424"),sQuery(id+"F6.wireOp",EDGE,"E1425"),sQuery(id+"F6.wireOp",EDGE,"E1426"),sQuery(id+"F6.wireOp",EDGE,"E1427"),sQuery(id+"F6.wireOp",EDGE,"E1428"),sQuery(id+"F6.wireOp",EDGE,"E1429"),sQuery(id+"F6.wireOp",EDGE,"E1430"),sQuery(id+"F6.wireOp",EDGE,"E1431"),sQuery(id+"F6.wireOp",EDGE,"E1432"),sQuery(id+"F6.wireOp",EDGE,"E1433"),sQuery(id+"F6.wireOp",EDGE,"E1434"),sQuery(id+"F6.wireOp",EDGE,"E1435"),sQuery(id+"F6.wireOp",EDGE,"E1436"),sQuery(id+"F6.wireOp",EDGE,"E1437"),sQuery(id+"F6.wireOp",EDGE,"E1438"),sQuery(id+"F6.wireOp",EDGE,"E1439"),sQuery(id+"F6.wireOp",EDGE,"E1440"),sQuery(id+"F6.wireOp",EDGE,"E1441"),sQuery(id+"F6.wireOp",EDGE,"E1442"),sQuery(id+"F6.wireOp",EDGE,"E1443"),sQuery(id+"F6.wireOp",EDGE,"E1444"),sQuery(id+"F6.wireOp",EDGE,"E1445"),sQuery(id+"F6.wireOp",EDGE,"E1446"),sQuery(id+"F6.wireOp",EDGE,"E1447"),sQuery(id+"F6.wireOp",EDGE,"E1448"),sQuery(id+"F6.wireOp",EDGE,"E1449"),sQuery(id+"F6.wireOp",EDGE,"E1450"),sQuery(id+"F6.wireOp",EDGE,"E1451"),sQuery(id+"F6.wireOp",EDGE,"E1452"),sQuery(id+"F6.wireOp",EDGE,"E1453"),sQuery(id+"F6.wireOp",EDGE,"E1454"),sQuery(id+"F6.wireOp",EDGE,"E1455"),sQuery(id+"F6.wireOp",EDGE,"E1456"),sQuery(id+"F6.wireOp",EDGE,"E1457"),sQuery(id+"F6.wireOp",EDGE,"E1458"),sQuery(id+"F6.wireOp",EDGE,"E1459"),sQuery(id+"F6.wireOp",EDGE,"E1460"),sQuery(id+"F6.wireOp",EDGE,"E1461"),sQuery(id+"F6.wireOp",EDGE,"E1462"),sQuery(id+"F6.wireOp",EDGE,"E1463"),sQuery(id+"F6.wireOp",EDGE,"E1464"),sQuery(id+"F6.wireOp",EDGE,"E1465"),sQuery(id+"F6.wireOp",EDGE,"E1466"),sQuery(id+"F6.wireOp",EDGE,"E1467"),sQuery(id+"F6.wireOp",EDGE,"E1468"),sQuery(id+"F6.wireOp",EDGE,"E1469"),sQuery(id+"F6.wireOp",EDGE,"E1470"),sQuery(id+"F6.wireOp",EDGE,"E1471"),sQuery(id+"F6.wireOp",EDGE,"E1472"),sQuery(id+"F6.wireOp",EDGE,"E1473"),sQuery(id+"F6.wireOp",EDGE,"E1474"),sQuery(id+"F6.wireOp",EDGE,"E1475"),sQuery(id+"F6.wireOp",EDGE,"E1476"),sQuery(id+"F6.wireOp",EDGE,"E1477"),sQuery(id+"F6.wireOp",EDGE,"E1478"),sQuery(id+"F6.wireOp",EDGE,"E1479"),sQuery(id+"F6.wireOp",EDGE,"E1480"),sQuery(id+"F6.wireOp",EDGE,"E1481"),sQuery(id+"F6.wireOp",EDGE,"E1482"),sQuery(id+"F6.wireOp",EDGE,"E1483"),sQuery(id+"F6.wireOp",EDGE,"E1484"),sQuery(id+"F6.wireOp",EDGE,"E1485"),sQuery(id+"F6.wireOp",EDGE,"E1486"),sQuery(id+"F6.wireOp",EDGE,"E1487"),sQuery(id+"F6.wireOp",EDGE,"E1488"),sQuery(id+"F6.wireOp",EDGE,"E1489"),sQuery(id+"F6.wireOp",EDGE,"E1490"),sQuery(id+"F6.wireOp",EDGE,"E1491"),sQuery(id+"F6.wireOp",EDGE,"E1492"),sQuery(id+"F6.wireOp",EDGE,"E1493"),sQuery(id+"F6.wireOp",EDGE,"E1494"),sQuery(id+"F6.wireOp",EDGE,"E1495"),sQuery(id+"F6.wireOp",EDGE,"E1496"),sQuery(id+"F6.wireOp",EDGE,"E1497"),sQuery(id+"F6.wireOp",EDGE,"E1498"),sQuery(id+"F6.wireOp",EDGE,"E1499"),sQuery(id+"F6.wireOp",EDGE,"E1500"),sQuery(id+"F6.wireOp",EDGE,"E1501"),sQuery(id+"F6.wireOp",EDGE,"E1502"),sQuery(id+"F6.wireOp",EDGE,"E1503"),sQuery(id+"F6.wireOp",EDGE,"E1504"),sQuery(id+"F6.wireOp",EDGE,"E1505"),sQuery(id+"F6.wireOp",EDGE,"E1506"),sQuery(id+"F6.wireOp",EDGE,"E1507"),sQuery(id+"F6.wireOp",EDGE,"E1508"),sQuery(id+"F6.wireOp",EDGE,"E1509"),sQuery(id+"F6.wireOp",EDGE,"E1510"),sQuery(id+"F6.wireOp",EDGE,"E1511"),sQuery(id+"F6.wireOp",EDGE,"E1512"),sQuery(id+"F6.wireOp",EDGE,"E1513"),sQuery(id+"F6.wireOp",EDGE,"E1514"),sQuery(id+"F6.wireOp",EDGE,"E1515"),sQuery(id+"F6.wireOp",EDGE,"E1516"),sQuery(id+"F6.wireOp",EDGE,"E1517"),sQuery(id+"F6.wireOp",EDGE,"E1518"),sQuery(id+"F6.wireOp",EDGE,"E1519"),sQuery(id+"F6.wireOp",EDGE,"E1520"),sQuery(id+"F6.wireOp",EDGE,"E1521"),sQuery(id+"F6.wireOp",EDGE,"E1522"),sQuery(id+"F6.wireOp",EDGE,"E1523"),sQuery(id+"F6.wireOp",EDGE,"E1524"),sQuery(id+"F6.wireOp",EDGE,"E1525"),sQuery(id+"F6.wireOp",EDGE,"E1526"),sQuery(id+"F6.wireOp",EDGE,"E1527"),sQuery(id+"F6.wireOp",EDGE,"E1528"),sQuery(id+"F6.wireOp",EDGE,"E1529"),sQuery(id+"F6.wireOp",EDGE,"E1530"),sQuery(id+"F6.wireOp",EDGE,"E1531"),sQuery(id+"F6.wireOp",EDGE,"E1532"),sQuery(id+"F6.wireOp",EDGE,"E1533"),sQuery(id+"F6.wireOp",EDGE,"E1534"),sQuery(id+"F6.wireOp",EDGE,"E1535"),sQuery(id+"F6.wireOp",EDGE,"E1536"),sQuery(id+"F6.wireOp",EDGE,"E1537"),sQuery(id+"F6.wireOp",EDGE,"E1538"),sQuery(id+"F6.wireOp",EDGE,"E1539"),sQuery(id+"F6.wireOp",EDGE,"E1540"),sQuery(id+"F6.wireOp",EDGE,"E1541"),sQuery(id+"F6.wireOp",EDGE,"E1542"),sQuery(id+"F6.wireOp",EDGE,"E1543"),sQuery(id+"F6.wireOp",EDGE,"E1544"),sQuery(id+"F6.wireOp",EDGE,"E1545"),sQuery(id+"F6.wireOp",EDGE,"E1546"),sQuery(id+"F6.wireOp",EDGE,"E1547"),sQuery(id+"F6.wireOp",EDGE,"E1548"),sQuery(id+"F6.wireOp",EDGE,"E1549"),sQuery(id+"F6.wireOp",EDGE,"E1550"),sQuery(id+"F6.wireOp",EDGE,"E1551"),sQuery(id+"F6.wireOp",EDGE,"E1552"),sQuery(id+"F6.wireOp",EDGE,"E1553"),sQuery(id+"F6.wireOp",EDGE,"E1554"),sQuery(id+"F6.wireOp",EDGE,"E1555"),sQuery(id+"F6.wireOp",EDGE,"E1556"),sQuery(id+"F6.wireOp",EDGE,"E1557"),sQuery(id+"F6.wireOp",EDGE,"E1558"),sQuery(id+"F6.wireOp",EDGE,"E1559"),sQuery(id+"F6.wireOp",EDGE,"E1560"),sQuery(id+"F6.wireOp",EDGE,"E1561"),sQuery(id+"F6.wireOp",EDGE,"E1562"),sQuery(id+"F6.wireOp",EDGE,"E1563"),sQuery(id+"F6.wireOp",EDGE,"E1564"),sQuery(id+"F6.wireOp",EDGE,"E1565"),sQuery(id+"F6.wireOp",EDGE,"E1566"),sQuery(id+"F6.wireOp",EDGE,"E1567"),sQuery(id+"F6.wireOp",EDGE,"E1568"),sQuery(id+"F6.wireOp",EDGE,"E1569"),sQuery(id+"F6.wireOp",EDGE,"E1570"),sQuery(id+"F6.wireOp",EDGE,"E1571"),sQuery(id+"F6.wireOp",EDGE,"E1572"),sQuery(id+"F6.wireOp",EDGE,"E1573"),sQuery(id+"F6.wireOp",EDGE,"E1574"),sQuery(id+"F6.wireOp",EDGE,"E1575"),sQuery(id+"F6.wireOp",EDGE,"E1576"),sQuery(id+"F6.wireOp",EDGE,"E1577"),sQuery(id+"F6.wireOp",EDGE,"E1578"),sQuery(id+"F6.wireOp",EDGE,"E1579"),sQuery(id+"F6.wireOp",EDGE,"E1580"),sQuery(id+"F6.wireOp",EDGE,"E1581"),sQuery(id+"F6.wireOp",EDGE,"E1582"),sQuery(id+"F6.wireOp",EDGE,"E1583"),sQuery(id+"F6.wireOp",EDGE,"E1584"),sQuery(id+"F6.wireOp",EDGE,"E1585"),sQuery(id+"F6.wireOp",EDGE,"E1586"),sQuery(id+"F6.wireOp",EDGE,"E1587"),sQuery(id+"F6.wireOp",EDGE,"E1588"),sQuery(id+"F6.wireOp",EDGE,"E1589"),sQuery(id+"F6.wireOp",EDGE,"E1590"),sQuery(id+"F6.wireOp",EDGE,"E1591"),sQuery(id+"F6.wireOp",EDGE,"E1592"),sQuery(id+"F6.wireOp",EDGE,"E1593"),sQuery(id+"F6.wireOp",EDGE,"E1594"),sQuery(id+"F6.wireOp",EDGE,"E1595"),sQuery(id+"F6.wireOp",EDGE,"E1596"),sQuery(id+"F6.wireOp",EDGE,"E1597"),sQuery(id+"F6.wireOp",EDGE,"E1598"),sQuery(id+"F6.wireOp",EDGE,"E1599"),sQuery(id+"F6.wireOp",EDGE,"E1600"),sQuery(id+"F6.wireOp",EDGE,"E1601"),sQuery(id+"F6.wireOp",EDGE,"E1602"),sQuery(id+"F6.wireOp",EDGE,"E1603"),sQuery(id+"F6.wireOp",EDGE,"E1604"),sQuery(id+"F6.wireOp",EDGE,"E1605"),sQuery(id+"F6.wireOp",EDGE,"E1606"),sQuery(id+"F6.wireOp",EDGE,"E1607"),sQuery(id+"F6.wireOp",EDGE,"E1608"),sQuery(id+"F6.wireOp",EDGE,"E1609"),sQuery(id+"F6.wireOp",EDGE,"E1610"),sQuery(id+"F6.wireOp",EDGE,"E1611"),sQuery(id+"F6.wireOp",EDGE,"E1612"),sQuery(id+"F6.wireOp",EDGE,"E1613"),sQuery(id+"F6.wireOp",EDGE,"E1614"),sQuery(id+"F6.wireOp",EDGE,"E1615"),sQuery(id+"F6.wireOp",EDGE,"E1616"),sQuery(id+"F6.wireOp",EDGE,"E1617"),sQuery(id+"F6.wireOp",EDGE,"E1618"),sQuery(id+"F6.wireOp",EDGE,"E1619"),sQuery(id+"F6.wireOp",EDGE,"E1620"),sQuery(id+"F6.wireOp",EDGE,"E1621"),sQuery(id+"F6.wireOp",EDGE,"E1622"),sQuery(id+"F6.wireOp",EDGE,"E1623"),sQuery(id+"F6.wireOp",EDGE,"E1624"),sQuery(id+"F6.wireOp",EDGE,"E1625"),sQuery(id+"F6.wireOp",EDGE,"E1626"),sQuery(id+"F6.wireOp",EDGE,"E1627"),sQuery(id+"F6.wireOp",EDGE,"E1628"),sQuery(id+"F6.wireOp",EDGE,"E1629"),sQuery(id+"F6.wireOp",EDGE,"E1630"),sQuery(id+"F6.wireOp",EDGE,"E1631"),sQuery(id+"F6.wireOp",EDGE,"E1632"),sQuery(id+"F6.wireOp",EDGE,"E1633"),sQuery(id+"F6.wireOp",EDGE,"E1634"),sQuery(id+"F6.wireOp",EDGE,"E1635"),sQuery(id+"F6.wireOp",EDGE,"E1636"),sQuery(id+"F6.wireOp",EDGE,"E1637"),sQuery(id+"F6.wireOp",EDGE,"E1638"),sQuery(id+"F6.wireOp",EDGE,"E1639"),sQuery(id+"F6.wireOp",EDGE,"E1640"),sQuery(id+"F6.wireOp",EDGE,"E1641"),sQuery(id+"F6.wireOp",EDGE,"E1642"),sQuery(id+"F6.wireOp",EDGE,"E1643"),sQuery(id+"F6.wireOp",EDGE,"E1644"),sQuery(id+"F6.wireOp",EDGE,"E1645"),sQuery(id+"F6.wireOp",EDGE,"E1646"),sQuery(id+"F6.wireOp",EDGE,"E1647"),sQuery(id+"F6.wireOp",EDGE,"E1648"),sQuery(id+"F6.wireOp",EDGE,"E1649"),sQuery(id+"F6.wireOp",EDGE,"E1650"),sQuery(id+"F6.wireOp",EDGE,"E1651"),sQuery(id+"F6.wireOp",EDGE,"E1652"),sQuery(id+"F6.wireOp",EDGE,"E1653"),sQuery(id+"F6.wireOp",EDGE,"E1654"),sQuery(id+"F6.wireOp",EDGE,"E1655"),sQuery(id+"F6.wireOp",EDGE,"E1656"),sQuery(id+"F6.wireOp",EDGE,"E1657"),sQuery(id+"F6.wireOp",EDGE,"E1658"),sQuery(id+"F6.wireOp",EDGE,"E1659"),sQuery(id+"F6.wireOp",EDGE,"E1660"),sQuery(id+"F6.wireOp",EDGE,"E1661"),sQuery(id+"F6.wireOp",EDGE,"E1662"),sQuery(id+"F6.wireOp",EDGE,"E1663"),sQuery(id+"F6.wireOp",EDGE,"E1664"),sQuery(id+"F6.wireOp",EDGE,"E1665"),sQuery(id+"F6.wireOp",EDGE,"E1666"),sQuery(id+"F6.wireOp",EDGE,"E1667"),sQuery(id+"F6.wireOp",EDGE,"E1668"),sQuery(id+"F6.wireOp",EDGE,"E1669"),sQuery(id+"F6.wireOp",EDGE,"E1670"),sQuery(id+"F6.wireOp",EDGE,"E1671"),sQuery(id+"F6.wireOp",EDGE,"E1672"),sQuery(id+"F6.wireOp",EDGE,"E1673"),sQuery(id+"F6.wireOp",EDGE,"E1674"),sQuery(id+"F6.wireOp",EDGE,"E1675"),sQuery(id+"F6.wireOp",EDGE,"E1676"),sQuery(id+"F6.wireOp",EDGE,"E1677"),sQuery(id+"F6.wireOp",EDGE,"E1678"),sQuery(id+"F6.wireOp",EDGE,"E1679"),sQuery(id+"F6.wireOp",EDGE,"E1680"),sQuery(id+"F6.wireOp",EDGE,"E1681"),sQuery(id+"F6.wireOp",EDGE,"E1682"),sQuery(id+"F6.wireOp",EDGE,"E1683"),sQuery(id+"F6.wireOp",EDGE,"E1684"),sQuery(id+"F6.wireOp",EDGE,"E1685"),sQuery(id+"F6.wireOp",EDGE,"E1686"),sQuery(id+"F6.wireOp",EDGE,"E1687"),sQuery(id+"F6.wireOp",EDGE,"E1688"),sQuery(id+"F6.wireOp",EDGE,"E1689"),sQuery(id+"F6.wireOp",EDGE,"E1690"),sQuery(id+"F6.wireOp",EDGE,"E1691"),sQuery(id+"F6.wireOp",EDGE,"E1692"),sQuery(id+"F6.wireOp",EDGE,"E1693"),sQuery(id+"F6.wireOp",EDGE,"E1694"),sQuery(id+"F6.wireOp",EDGE,"E1695"),sQuery(id+"F6.wireOp",EDGE,"E1696"),sQuery(id+"F6.wireOp",EDGE,"E1697"),sQuery(id+"F6.wireOp",EDGE,"E1698"),sQuery(id+"F6.wireOp",EDGE,"E1699"),sQuery(id+"F6.wireOp",EDGE,"E1700"),sQuery(id+"F6.wireOp",EDGE,"E1701"),sQuery(id+"F6.wireOp",EDGE,"E1702"),sQuery(id+"F6.wireOp",EDGE,"E1703"),sQuery(id+"F6.wireOp",EDGE,"E1704"),sQuery(id+"F6.wireOp",EDGE,"E1705"),sQuery(id+"F6.wireOp",EDGE,"E1706"),sQuery(id+"F6.wireOp",EDGE,"E1707"),sQuery(id+"F6.wireOp",EDGE,"E1708"),sQuery(id+"F6.wireOp",EDGE,"E1709"),sQuery(id+"F6.wireOp",EDGE,"E1710"),sQuery(id+"F6.wireOp",EDGE,"E1711"),sQuery(id+"F6.wireOp",EDGE,"E1712"),sQuery(id+"F6.wireOp",EDGE,"E1713"),sQuery(id+"F6.wireOp",EDGE,"E1714"),sQuery(id+"F6.wireOp",EDGE,"E1715"),sQuery(id+"F6.wireOp",EDGE,"E1716"),sQuery(id+"F6.wireOp",EDGE,"E1717"),sQuery(id+"F6.wireOp",EDGE,"E1718"),sQuery(id+"F6.wireOp",EDGE,"E1719"),sQuery(id+"F6.wireOp",EDGE,"E1720"),sQuery(id+"F6.wireOp",EDGE,"E1721"),sQuery(id+"F6.wireOp",EDGE,"E1722"),sQuery(id+"F6.wireOp",EDGE,"E1723"),sQuery(id+"F6.wireOp",EDGE,"E1724"),sQuery(id+"F6.wireOp",EDGE,"E1725"),sQuery(id+"F6.wireOp",EDGE,"E1726"),sQuery(id+"F6.wireOp",EDGE,"E1727"),sQuery(id+"F6.wireOp",EDGE,"E1728"),sQuery(id+"F6.wireOp",EDGE,"E1729"),sQuery(id+"F6.wireOp",EDGE,"E1730"),sQuery(id+"F6.wireOp",EDGE,"E1731"),sQuery(id+"F6.wireOp",EDGE,"E1732"),sQuery(id+"F6.wireOp",EDGE,"E1733"),sQuery(id+"F6.wireOp",EDGE,"E1734"),sQuery(id+"F6.wireOp",EDGE,"E1735"),sQuery(id+"F6.wireOp",EDGE,"E1736"),sQuery(id+"F6.wireOp",EDGE,"E1737"),sQuery(id+"F6.wireOp",EDGE,"E1738"),sQuery(id+"F6.wireOp",EDGE,"E1739"),sQuery(id+"F6.wireOp",EDGE,"E1740"),sQuery(id+"F6.wireOp",EDGE,"E1741"),sQuery(id+"F6.wireOp",EDGE,"E1742"),sQuery(id+"F6.wireOp",EDGE,"E1743"),sQuery(id+"F6.wireOp",EDGE,"E1744"),sQuery(id+"F6.wireOp",EDGE,"E1745"),sQuery(id+"F6.wireOp",EDGE,"E1746"),sQuery(id+"F6.wireOp",EDGE,"E1747"),sQuery(id+"F6.wireOp",EDGE,"E1748"),sQuery(id+"F6.wireOp",EDGE,"E1749"),sQuery(id+"F6.wireOp",EDGE,"E1750"),sQuery(id+"F6.wireOp",EDGE,"E1751"),sQuery(id+"F6.wireOp",EDGE,"E1752"),sQuery(id+"F6.wireOp",EDGE,"E1753"),sQuery(id+"F6.wireOp",EDGE,"E1754"),sQuery(id+"F6.wireOp",EDGE,"E1755"),sQuery(id+"F6.wireOp",EDGE,"E1756"),sQuery(id+"F6.wireOp",EDGE,"E1757"),sQuery(id+"F6.wireOp",EDGE,"E1758"),sQuery(id+"F6.wireOp",EDGE,"E1759"),sQuery(id+"F6.wireOp",EDGE,"E1760"),sQuery(id+"F6.wireOp",EDGE,"E1761"),sQuery(id+"F6.wireOp",EDGE,"E1762"),sQuery(id+"F6.wireOp",EDGE,"E1763"),sQuery(id+"F6.wireOp",EDGE,"E1764"),sQuery(id+"F6.wireOp",EDGE,"E1765"),sQuery(id+"F6.wireOp",EDGE,"E1766"),sQuery(id+"F6.wireOp",EDGE,"E1767"),sQuery(id+"F6.wireOp",EDGE,"E1768"),sQuery(id+"F6.wireOp",EDGE,"E1769"),sQuery(id+"F6.wireOp",EDGE,"E1770"),sQuery(id+"F6.wireOp",EDGE,"E1771"),sQuery(id+"F6.wireOp",EDGE,"E1772"),sQuery(id+"F6.wireOp",EDGE,"E1773"),sQuery(id+"F6.wireOp",EDGE,"E1774"),sQuery(id+"F6.wireOp",EDGE,"E1775"),sQuery(id+"F6.wireOp",EDGE,"E1776"),sQuery(id+"F6.wireOp",EDGE,"E1777"),sQuery(id+"F6.wireOp",EDGE,"E1778"),sQuery(id+"F6.wireOp",EDGE,"E1779"),sQuery(id+"F6.wireOp",EDGE,"E1780"),sQuery(id+"F6.wireOp",EDGE,"E1781"),sQuery(id+"F6.wireOp",EDGE,"E1782"),sQuery(id+"F6.wireOp",EDGE,"E1783"),sQuery(id+"F6.wireOp",EDGE,"E1784"),sQuery(id+"F6.wireOp",EDGE,"E1785"),sQuery(id+"F6.wireOp",EDGE,"E1786"),sQuery(id+"F6.wireOp",EDGE,"E1787"),sQuery(id+"F6.wireOp",EDGE,"E1788"),sQuery(id+"F6.wireOp",EDGE,"E1789"),sQuery(id+"F6.wireOp",EDGE,"E1790"),sQuery(id+"F6.wireOp",EDGE,"E1791"),sQuery(id+"F6.wireOp",EDGE,"E1792"),sQuery(id+"F6.wireOp",EDGE,"E1793"),sQuery(id+"F6.wireOp",EDGE,"E1794"),sQuery(id+"F6.wireOp",EDGE,"E1795"),sQuery(id+"F6.wireOp",EDGE,"E1796"),sQuery(id+"F6.wireOp",EDGE,"E1797"),sQuery(id+"F6.wireOp",EDGE,"E1798"),sQuery(id+"F6.wireOp",EDGE,"E1799"),sQuery(id+"F6.wireOp",EDGE,"E1800"),sQuery(id+"F6.wireOp",EDGE,"E1801"),sQuery(id+"F6.wireOp",EDGE,"E1802"),sQuery(id+"F6.wireOp",EDGE,"E1803"),sQuery(id+"F6.wireOp",EDGE,"E1804"),sQuery(id+"F6.wireOp",EDGE,"E1805"),sQuery(id+"F6.wireOp",EDGE,"E1806"),sQuery(id+"F6.wireOp",EDGE,"E1807"),sQuery(id+"F6.wireOp",EDGE,"E1808"),sQuery(id+"F6.wireOp",EDGE,"E1809"),sQuery(id+"F6.wireOp",EDGE,"E1810"),sQuery(id+"F6.wireOp",EDGE,"E1811"),sQuery(id+"F6.wireOp",EDGE,"E1812"),sQuery(id+"F6.wireOp",EDGE,"E1813"),sQuery(id+"F6.wireOp",EDGE,"E1814"),sQuery(id+"F6.wireOp",EDGE,"E1815"),sQuery(id+"F6.wireOp",EDGE,"E1816"),sQuery(id+"F6.wireOp",EDGE,"E1817"),sQuery(id+"F6.wireOp",EDGE,"E1818"),sQuery(id+"F6.wireOp",EDGE,"E1819"),sQuery(id+"F6.wireOp",EDGE,"E1820"),sQuery(id+"F6.wireOp",EDGE,"E1821"),sQuery(id+"F6.wireOp",EDGE,"E1822"),sQuery(id+"F6.wireOp",EDGE,"E1823"),sQuery(id+"F6.wireOp",EDGE,"E1824"),sQuery(id+"F6.wireOp",EDGE,"E1825"),sQuery(id+"F6.wireOp",EDGE,"E1826"),sQuery(id+"F6.wireOp",EDGE,"E1827"),sQuery(id+"F6.wireOp",EDGE,"E1828"),sQuery(id+"F6.wireOp",EDGE,"E1829"),sQuery(id+"F6.wireOp",EDGE,"E1830"),sQuery(id+"F6.wireOp",EDGE,"E1831"),sQuery(id+"F6.wireOp",EDGE,"E1832"),sQuery(id+"F6.wireOp",EDGE,"E1833"),sQuery(id+"F6.wireOp",EDGE,"E1834"),sQuery(id+"F6.wireOp",EDGE,"E1835"),sQuery(id+"F6.wireOp",EDGE,"E1836"),sQuery(id+"F6.wireOp",EDGE,"E1837"),sQuery(id+"F6.wireOp",EDGE,"E1838"),sQuery(id+"F6.wireOp",EDGE,"E1839"),sQuery(id+"F6.wireOp",EDGE,"E1840"),sQuery(id+"F6.wireOp",EDGE,"E1841"),sQuery(id+"F6.wireOp",EDGE,"E1842"),sQuery(id+"F6.wireOp",EDGE,"E1843"),sQuery(id+"F6.wireOp",EDGE,"E1844"),sQuery(id+"F6.wireOp",EDGE,"E1845"),sQuery(id+"F6.wireOp",EDGE,"E1846"),sQuery(id+"F6.wireOp",EDGE,"E1847"),sQuery(id+"F6.wireOp",EDGE,"E1848"),sQuery(id+"F6.wireOp",EDGE,"E1849"),sQuery(id+"F6.wireOp",EDGE,"E1850"),sQuery(id+"F6.wireOp",EDGE,"E1851"),sQuery(id+"F6.wireOp",EDGE,"E1852"),sQuery(id+"F6.wireOp",EDGE,"E1853"),sQuery(id+"F6.wireOp",EDGE,"E1854"),sQuery(id+"F6.wireOp",EDGE,"E1855"),sQuery(id+"F6.wireOp",EDGE,"E1856"),sQuery(id+"F6.wireOp",EDGE,"E1857"),sQuery(id+"F6.wireOp",EDGE,"E1858"),sQuery(id+"F6.wireOp",EDGE,"E1859"),sQuery(id+"F6.wireOp",EDGE,"E1860"),sQuery(id+"F6.wireOp",EDGE,"E1861"),sQuery(id+"F6.wireOp",EDGE,"E1862"),sQuery(id+"F6.wireOp",EDGE,"E1863"),sQuery(id+"F6.wireOp",EDGE,"E1864"),sQuery(id+"F6.wireOp",EDGE,"E1865"),sQuery(id+"F6.wireOp",EDGE,"E1866"),sQuery(id+"F6.wireOp",EDGE,"E1867"),sQuery(id+"F6.wireOp",EDGE,"E1868"),sQuery(id+"F6.wireOp",EDGE,"E1869"),sQuery(id+"F6.wireOp",EDGE,"E1870"),sQuery(id+"F6.wireOp",EDGE,"E1871"),sQuery(id+"F6.wireOp",EDGE,"E1872"),sQuery(id+"F6.wireOp",EDGE,"E1873"),sQuery(id+"F6.wireOp",EDGE,"E1874"),sQuery(id+"F6.wireOp",EDGE,"E1875"),sQuery(id+"F6.wireOp",EDGE,"E1876"),sQuery(id+"F6.wireOp",EDGE,"E1877"),sQuery(id+"F6.wireOp",EDGE,"E1878"),sQuery(id+"F6.wireOp",EDGE,"E1879"),sQuery(id+"F6.wireOp",EDGE,"E1880"),sQuery(id+"F6.wireOp",EDGE,"E1881"),sQuery(id+"F6.wireOp",EDGE,"E1882"),sQuery(id+"F6.wireOp",EDGE,"E1883"),sQuery(id+"F6.wireOp",EDGE,"E1884"),sQuery(id+"F6.wireOp",EDGE,"E1885"),sQuery(id+"F6.wireOp",EDGE,"E1886"),sQuery(id+"F6.wireOp",EDGE,"E1887"),sQuery(id+"F6.wireOp",EDGE,"E1888"),sQuery(id+"F6.wireOp",EDGE,"E1889"),sQuery(id+"F6.wireOp",EDGE,"E1890"),sQuery(id+"F6.wireOp",EDGE,"E1891"),sQuery(id+"F6.wireOp",EDGE,"E1892"),sQuery(id+"F6.wireOp",EDGE,"E1893"),sQuery(id+"F6.wireOp",EDGE,"E1894"),sQuery(id+"F6.wireOp",EDGE,"E1895"),sQuery(id+"F6.wireOp",EDGE,"E1896"),sQuery(id+"F6.wireOp",EDGE,"E1897"),sQuery(id+"F6.wireOp",EDGE,"E1898"),sQuery(id+"F6.wireOp",EDGE,"E1899"),sQuery(id+"F6.wireOp",EDGE,"E1900"),sQuery(id+"F6.wireOp",EDGE,"E1901"),sQuery(id+"F6.wireOp",EDGE,"E1902"),sQuery(id+"F6.wireOp",EDGE,"E1903"),sQuery(id+"F6.wireOp",EDGE,"E1904"),sQuery(id+"F6.wireOp",EDGE,"E1905"),sQuery(id+"F6.wireOp",EDGE,"E1906"),sQuery(id+"F6.wireOp",EDGE,"E1907"),sQuery(id+"F6.wireOp",EDGE,"E1908"),sQuery(id+"F6.wireOp",EDGE,"E1909"),sQuery(id+"F6.wireOp",EDGE,"E1910"),sQuery(id+"F6.wireOp",EDGE,"E1911"),sQuery(id+"F6.wireOp",EDGE,"E1912"),sQuery(id+"F6.wireOp",EDGE,"E1913"),sQuery(id+"F6.wireOp",EDGE,"E1914"),sQuery(id+"F6.wireOp",EDGE,"E1915"),sQuery(id+"F6.wireOp",EDGE,"E1916"),sQuery(id+"F6.wireOp",EDGE,"E1917"),sQuery(id+"F6.wireOp",EDGE,"E1918"),sQuery(id+"F6.wireOp",EDGE,"E1919"),sQuery(id+"F6.wireOp",EDGE,"E1920"),sQuery(id+"F6.wireOp",EDGE,"E1921"),sQuery(id+"F6.wireOp",EDGE,"E1922"),sQuery(id+"F6.wireOp",EDGE,"E1923"),sQuery(id+"F6.wireOp",EDGE,"E1924"),sQuery(id+"F6.wireOp",EDGE,"E1925"),sQuery(id+"F6.wireOp",EDGE,"E1926"),sQuery(id+"F6.wireOp",EDGE,"E1927"),sQuery(id+"F6.wireOp",EDGE,"E1928"),sQuery(id+"F6.wireOp",EDGE,"E1929"),sQuery(id+"F6.wireOp",EDGE,"E1930"),sQuery(id+"F6.wireOp",EDGE,"E1931"),sQuery(id+"F6.wireOp",EDGE,"E1932"),sQuery(id+"F6.wireOp",EDGE,"E1933"),sQuery(id+"F6.wireOp",EDGE,"E1934"),sQuery(id+"F6.wireOp",EDGE,"E1935"),sQuery(id+"F6.wireOp",EDGE,"E1936"),sQuery(id+"F6.wireOp",EDGE,"E1937"),sQuery(id+"F6.wireOp",EDGE,"E1938"),sQuery(id+"F6.wireOp",EDGE,"E1939"),sQuery(id+"F6.wireOp",EDGE,"E1940"),sQuery(id+"F6.wireOp",EDGE,"E1941"),sQuery(id+"F6.wireOp",EDGE,"E1942"),sQuery(id+"F6.wireOp",EDGE,"E1943"),sQuery(id+"F6.wireOp",EDGE,"E1944"),sQuery(id+"F6.wireOp",EDGE,"E1945"),sQuery(id+"F6.wireOp",EDGE,"E1946"),sQuery(id+"F6.wireOp",EDGE,"E1947"),sQuery(id+"F6.wireOp",EDGE,"E1948"),sQuery(id+"F6.wireOp",EDGE,"E1949"),sQuery(id+"F6.wireOp",EDGE,"E1950"),sQuery(id+"F6.wireOp",EDGE,"E1951"),sQuery(id+"F6.wireOp",EDGE,"E1952"),sQuery(id+"F6.wireOp",EDGE,"E1953"),sQuery(id+"F6.wireOp",EDGE,"E1954"),sQuery(id+"F6.wireOp",EDGE,"E1955"),sQuery(id+"F6.wireOp",EDGE,"E1956"),sQuery(id+"F6.wireOp",EDGE,"E1957"),sQuery(id+"F6.wireOp",EDGE,"E1958"),sQuery(id+"F6.wireOp",EDGE,"E1959"),sQuery(id+"F6.wireOp",EDGE,"E1960"),sQuery(id+"F6.wireOp",EDGE,"E1961"),sQuery(id+"F6.wireOp",EDGE,"E1962"),sQuery(id+"F6.wireOp",EDGE,"E1963"),sQuery(id+"F6.wireOp",EDGE,"E1964"),sQuery(id+"F6.wireOp",EDGE,"E1965"),sQuery(id+"F6.wireOp",EDGE,"E1966"),sQuery(id+"F6.wireOp",EDGE,"E1967"),sQuery(id+"F6.wireOp",EDGE,"E1968"),sQuery(id+"F6.wireOp",EDGE,"E1969"),sQuery(id+"F6.wireOp",EDGE,"E1970"),sQuery(id+"F6.wireOp",EDGE,"E1971"),sQuery(id+"F6.wireOp",EDGE,"E1972"),sQuery(id+"F6.wireOp",EDGE,"E1973"),sQuery(id+"F6.wireOp",EDGE,"E1974"),sQuery(id+"F6.wireOp",EDGE,"E1975"),sQuery(id+"F6.wireOp",EDGE,"E1976"),sQuery(id+"F6.wireOp",EDGE,"E1977"),sQuery(id+"F6.wireOp",EDGE,"E1978"),sQuery(id+"F6.wireOp",EDGE,"E1979"),sQuery(id+"F6.wireOp",EDGE,"E1980"),sQuery(id+"F6.wireOp",EDGE,"E1981"),sQuery(id+"F6.wireOp",EDGE,"E1982"),sQuery(id+"F6.wireOp",EDGE,"E1983"),sQuery(id+"F6.wireOp",EDGE,"E1984"),sQuery(id+"F6.wireOp",EDGE,"E1985"),sQuery(id+"F6.wireOp",EDGE,"E1986"),sQuery(id+"F6.wireOp",EDGE,"E1987"),sQuery(id+"F6.wireOp",EDGE,"E1988"),sQuery(id+"F6.wireOp",EDGE,"E1989"),sQuery(id+"F6.wireOp",EDGE,"E1990"),sQuery(id+"F6.wireOp",EDGE,"E1991"),sQuery(id+"F6.wireOp",EDGE,"E1992"),sQuery(id+"F6.wireOp",EDGE,"E1993"),sQuery(id+"F6.wireOp",EDGE,"E1994"),sQuery(id+"F6.wireOp",EDGE,"E1995"),sQuery(id+"F6.wireOp",EDGE,"E1996"),sQuery(id+"F6.wireOp",EDGE,"E1997"),sQuery(id+"F6.wireOp",EDGE,"E1998"),sQuery(id+"F6.wireOp",EDGE,"E1999"),sQuery(id+"F6.wireOp",EDGE,"E2000"),sQuery(id+"F6.wireOp",EDGE,"E2001"),sQuery(id+"F6.wireOp",EDGE,"E2002"),sQuery(id+"F6.wireOp",EDGE,"E2003"),sQuery(id+"F6.wireOp",EDGE,"E2004"),sQuery(id+"F6.wireOp",EDGE,"E2005"),sQuery(id+"F6.wireOp",EDGE,"E2006"),sQuery(id+"F6.wireOp",EDGE,"E2007"),sQuery(id+"F6.wireOp",EDGE,"E2008"),sQuery(id+"F6.wireOp",EDGE,"E2009"),sQuery(id+"F6.wireOp",EDGE,"E2010"),sQuery(id+"F6.wireOp",EDGE,"E2011"),sQuery(id+"F6.wireOp",EDGE,"E2012"),sQuery(id+"F6.wireOp",EDGE,"E2013"),sQuery(id+"F6.wireOp",EDGE,"E2014"),sQuery(id+"F6.wireOp",EDGE,"E2015"),sQuery(id+"F6.wireOp",EDGE,"E2016"),sQuery(id+"F6.wireOp",EDGE,"E2017"),sQuery(id+"F6.wireOp",EDGE,"E2018"),sQuery(id+"F6.wireOp",EDGE,"E2019"),sQuery(id+"F6.wireOp",EDGE,"E2020"),sQuery(id+"F6.wireOp",EDGE,"E2021"),sQuery(id+"F6.wireOp",EDGE,"E2022"),sQuery(id+"F6.wireOp",EDGE,"E2023"),sQuery(id+"F6.wireOp",EDGE,"E2024"),sQuery(id+"F6.wireOp",EDGE,"E2025"),sQuery(id+"F6.wireOp",EDGE,"E2026"),sQuery(id+"F6.wireOp",EDGE,"E2027"),sQuery(id+"F6.wireOp",EDGE,"E2028"),sQuery(id+"F6.wireOp",EDGE,"E2029"),sQuery(id+"F6.wireOp",EDGE,"E2030"),sQuery(id+"F6.wireOp",EDGE,"E2031"),sQuery(id+"F6.wireOp",EDGE,"E2032"),sQuery(id+"F6.wireOp",EDGE,"E2033"),sQuery(id+"F6.wireOp",EDGE,"E2034"),sQuery(id+"F6.wireOp",EDGE,"E2035"),sQuery(id+"F6.wireOp",EDGE,"E2036"),sQuery(id+"F6.wireOp",EDGE,"E2037"),sQuery(id+"F6.wireOp",EDGE,"E2038"),sQuery(id+"F6.wireOp",EDGE,"E2039"),sQuery(id+"F6.wireOp",EDGE,"E2040"),sQuery(id+"F6.wireOp",EDGE,"E2041"),sQuery(id+"F6.wireOp",EDGE,"E2042"),sQuery(id+"F6.wireOp",EDGE,"E2043"),sQuery(id+"F6.wireOp",EDGE,"E2044"),sQuery(id+"F6.wireOp",EDGE,"E2045"),sQuery(id+"F6.wireOp",EDGE,"E2046"),sQuery(id+"F6.wireOp",EDGE,"E2047"),sQuery(id+"F6.wireOp",EDGE,"E2048"),sQuery(id+"F6.wireOp",EDGE,"E2049"),sQuery(id+"F6.wireOp",EDGE,"E2050"),sQuery(id+"F6.wireOp",EDGE,"E2051"),sQuery(id+"F6.wireOp",EDGE,"E2052"),sQuery(id+"F6.wireOp",EDGE,"E2053"),sQuery(id+"F6.wireOp",EDGE,"E2054"),sQuery(id+"F6.wireOp",EDGE,"E2055"),sQuery(id+"F6.wireOp",EDGE,"E2056"),sQuery(id+"F6.wireOp",EDGE,"E2057"),sQuery(id+"F6.wireOp",EDGE,"E2058"),sQuery(id+"F6.wireOp",EDGE,"E2059"),sQuery(id+"F6.wireOp",EDGE,"E2060"),sQuery(id+"F6.wireOp",EDGE,"E2061"),sQuery(id+"F6.wireOp",EDGE,"E2062"),sQuery(id+"F6.wireOp",EDGE,"E2063"),sQuery(id+"F6.wireOp",EDGE,"E2064"),sQuery(id+"F6.wireOp",EDGE,"E2065"),sQuery(id+"F6.wireOp",EDGE,"E2066"),sQuery(id+"F6.wireOp",EDGE,"E2067"),sQuery(id+"F6.wireOp",EDGE,"E2068"),sQuery(id+"F6.wireOp",EDGE,"E2069"),sQuery(id+"F6.wireOp",EDGE,"E2070"),sQuery(id+"F6.wireOp",EDGE,"E2071"),sQuery(id+"F6.wireOp",EDGE,"E2072"),sQuery(id+"F6.wireOp",EDGE,"E2073"),sQuery(id+"F6.wireOp",EDGE,"E2074"),sQuery(id+"F6.wireOp",EDGE,"E2075"),sQuery(id+"F6.wireOp",EDGE,"E2076"),sQuery(id+"F6.wireOp",EDGE,"E2077"),sQuery(id+"F6.wireOp",EDGE,"E2078"),sQuery(id+"F6.wireOp",EDGE,"E2079"),sQuery(id+"F6.wireOp",EDGE,"E2080"),sQuery(id+"F6.wireOp",EDGE,"E2081"),sQuery(id+"F6.wireOp",EDGE,"E2082"),sQuery(id+"F6.wireOp",EDGE,"E2083"),sQuery(id+"F6.wireOp",EDGE,"E2084"),sQuery(id+"F6.wireOp",EDGE,"E2085"),sQuery(id+"F6.wireOp",EDGE,"E2086"),sQuery(id+"F6.wireOp",EDGE,"E2087"),sQuery(id+"F6.wireOp",EDGE,"E2088"),sQuery(id+"F6.wireOp",EDGE,"E2089"),sQuery(id+"F6.wireOp",EDGE,"E2090"),sQuery(id+"F6.wireOp",EDGE,"E2091"),sQuery(id+"F6.wireOp",EDGE,"E2092"),sQuery(id+"F6.wireOp",EDGE,"E2093"),sQuery(id+"F6.wireOp",EDGE,"E2094"),sQuery(id+"F6.wireOp",EDGE,"E2095"),sQuery(id+"F6.wireOp",EDGE,"E2096"),sQuery(id+"F6.wireOp",EDGE,"E2097"),sQuery(id+"F6.wireOp",EDGE,"E2098"),sQuery(id+"F6.wireOp",EDGE,"E2099"),sQuery(id+"F6.wireOp",EDGE,"E2100"),sQuery(id+"F6.wireOp",EDGE,"E2101"),sQuery(id+"F6.wireOp",EDGE,"E2102"),sQuery(id+"F6.wireOp",EDGE,"E2103"),sQuery(id+"F6.wireOp",EDGE,"E2104"),sQuery(id+"F6.wireOp",EDGE,"E2105"),sQuery(id+"F6.wireOp",EDGE,"E2106"),sQuery(id+"F6.wireOp",EDGE,"E2107"),sQuery(id+"F6.wireOp",EDGE,"E2108"),sQuery(id+"F6.wireOp",EDGE,"E2109"),sQuery(id+"F6.wireOp",EDGE,"E2110"),sQuery(id+"F6.wireOp",EDGE,"E2111"),sQuery(id+"F6.wireOp",EDGE,"E2112"),sQuery(id+"F6.wireOp",EDGE,"E2113"),sQuery(id+"F6.wireOp",EDGE,"E2114"),sQuery(id+"F6.wireOp",EDGE,"E2115"),sQuery(id+"F6.wireOp",EDGE,"E2116"),sQuery(id+"F6.wireOp",EDGE,"E2117"),sQuery(id+"F6.wireOp",EDGE,"E2118"),sQuery(id+"F6.wireOp",EDGE,"E2119"),sQuery(id+"F6.wireOp",EDGE,"E2120"),sQuery(id+"F6.wireOp",EDGE,"E2121"),sQuery(id+"F6.wireOp",EDGE,"E2122"),sQuery(id+"F6.wireOp",EDGE,"E2123"),sQuery(id+"F6.wireOp",EDGE,"E2124"),sQuery(id+"F6.wireOp",EDGE,"E2125"),sQuery(id+"F6.wireOp",EDGE,"E2126"),sQuery(id+"F6.wireOp",EDGE,"E2127"),sQuery(id+"F6.wireOp",EDGE,"E2128"),sQuery(id+"F6.wireOp",EDGE,"E2129"),sQuery(id+"F6.wireOp",EDGE,"E2130"),sQuery(id+"F6.wireOp",EDGE,"E2131"),sQuery(id+"F6.wireOp",EDGE,"E2132"),sQuery(id+"F6.wireOp",EDGE,"E2133"),sQuery(id+"F6.wireOp",EDGE,"E2134"),sQuery(id+"F6.wireOp",EDGE,"E2135"),sQuery(id+"F6.wireOp",EDGE,"E2136"),sQuery(id+"F6.wireOp",EDGE,"E2137"),sQuery(id+"F6.wireOp",EDGE,"E2138"),sQuery(id+"F6.wireOp",EDGE,"E2139"),sQuery(id+"F6.wireOp",EDGE,"E2140"),sQuery(id+"F6.wireOp",EDGE,"E2141"),sQuery(id+"F6.wireOp",EDGE,"E2142"),sQuery(id+"F6.wireOp",EDGE,"E2143"),sQuery(id+"F6.wireOp",EDGE,"E2144"),sQuery(id+"F6.wireOp",EDGE,"E2145"),sQuery(id+"F6.wireOp",EDGE,"E2146"),sQuery(id+"F6.wireOp",EDGE,"E2147"),sQuery(id+"F6.wireOp",EDGE,"E2148"),sQuery(id+"F6.wireOp",EDGE,"E2149"),sQuery(id+"F6.wireOp",EDGE,"E2150"),sQuery(id+"F6.wireOp",EDGE,"E2151"),sQuery(id+"F6.wireOp",EDGE,"E2152"),sQuery(id+"F6.wireOp",EDGE,"E2153"),sQuery(id+"F6.wireOp",EDGE,"E2154"),sQuery(id+"F6.wireOp",EDGE,"E2155"),sQuery(id+"F6.wireOp",EDGE,"E2156"),sQuery(id+"F6.wireOp",EDGE,"E2157"),sQuery(id+"F6.wireOp",EDGE,"E2158"),sQuery(id+"F6.wireOp",EDGE,"E2159"),sQuery(id+"F6.wireOp",EDGE,"E2160"),sQuery(id+"F6.wireOp",EDGE,"E2161"),sQuery(id+"F6.wireOp",EDGE,"E2162"),sQuery(id+"F6.wireOp",EDGE,"E2163"),sQuery(id+"F6.wireOp",EDGE,"E2164"),sQuery(id+"F6.wireOp",EDGE,"E2165"),sQuery(id+"F6.wireOp",EDGE,"E2166"),sQuery(id+"F6.wireOp",EDGE,"E2167"),sQuery(id+"F6.wireOp",EDGE,"E2168"),sQuery(id+"F6.wireOp",EDGE,"E2169"),sQuery(id+"F6.wireOp",EDGE,"E2170"),sQuery(id+"F6.wireOp",EDGE,"E2171"),sQuery(id+"F6.wireOp",EDGE,"E2172"),sQuery(id+"F6.wireOp",EDGE,"E2173"),sQuery(id+"F6.wireOp",EDGE,"E2174"),sQuery(id+"F6.wireOp",EDGE,"E2175"),sQuery(id+"F6.wireOp",EDGE,"E2176"),sQuery(id+"F6.wireOp",EDGE,"E2177"),sQuery(id+"F6.wireOp",EDGE,"E2178"),sQuery(id+"F6.wireOp",EDGE,"E2179"),sQuery(id+"F6.wireOp",EDGE,"E2180"),sQuery(id+"F6.wireOp",EDGE,"E2181"),sQuery(id+"F6.wireOp",EDGE,"E2182"),sQuery(id+"F6.wireOp",EDGE,"E2183"),sQuery(id+"F6.wireOp",EDGE,"E2184"),sQuery(id+"F6.wireOp",EDGE,"E2185"),sQuery(id+"F6.wireOp",EDGE,"E2186"),sQuery(id+"F6.wireOp",EDGE,"E2187"),sQuery(id+"F6.wireOp",EDGE,"E2188"),sQuery(id+"F6.wireOp",EDGE,"E2189"),sQuery(id+"F6.wireOp",EDGE,"E2190"),sQuery(id+"F6.wireOp",EDGE,"E2191"),sQuery(id+"F6.wireOp",EDGE,"E2192"),sQuery(id+"F6.wireOp",EDGE,"E2193"),sQuery(id+"F6.wireOp",EDGE,"E2194"),sQuery(id+"F6.wireOp",EDGE,"E2195"),sQuery(id+"F6.wireOp",EDGE,"E2196"),sQuery(id+"F6.wireOp",EDGE,"E2197"),sQuery(id+"F6.wireOp",EDGE,"E2198"),sQuery(id+"F6.wireOp",EDGE,"E2199"),sQuery(id+"F6.wireOp",EDGE,"E2200"),sQuery(id+"F6.wireOp",EDGE,"E2201"),sQuery(id+"F6.wireOp",EDGE,"E2202"),sQuery(id+"F6.wireOp",EDGE,"E2203"),sQuery(id+"F6.wireOp",EDGE,"E2204"),sQuery(id+"F6.wireOp",EDGE,"E2205"),sQuery(id+"F6.wireOp",EDGE,"E2206"),sQuery(id+"F6.wireOp",EDGE,"E2207"),sQuery(id+"F6.wireOp",EDGE,"E2208"),sQuery(id+"F6.wireOp",EDGE,"E2209"),sQuery(id+"F6.wireOp",EDGE,"E2210"),sQuery(id+"F6.wireOp",EDGE,"E2211"),sQuery(id+"F6.wireOp",EDGE,"E2212"),sQuery(id+"F6.wireOp",EDGE,"E2213"),sQuery(id+"F6.wireOp",EDGE,"E2214"),sQuery(id+"F6.wireOp",EDGE,"E2215"),sQuery(id+"F6.wireOp",EDGE,"E2216"),sQuery(id+"F6.wireOp",EDGE,"E2217"),sQuery(id+"F6.wireOp",EDGE,"E2218"),sQuery(id+"F6.wireOp",EDGE,"E2219"),sQuery(id+"F6.wireOp",EDGE,"E2220"),sQuery(id+"F6.wireOp",EDGE,"E2221"),sQuery(id+"F6.wireOp",EDGE,"E2222"),sQuery(id+"F6.wireOp",EDGE,"E2223"),sQuery(id+"F6.wireOp",EDGE,"E2224"),sQuery(id+"F6.wireOp",EDGE,"E2225"),sQuery(id+"F6.wireOp",EDGE,"E2226"),sQuery(id+"F6.wireOp",EDGE,"E2227"),sQuery(id+"F6.wireOp",EDGE,"E2228"),sQuery(id+"F6.wireOp",EDGE,"E2229"),sQuery(id+"F6.wireOp",EDGE,"E2230"),sQuery(id+"F6.wireOp",EDGE,"E2231"),sQuery(id+"F6.wireOp",EDGE,"E2232"),sQuery(id+"F6.wireOp",EDGE,"E2233"),sQuery(id+"F6.wireOp",EDGE,"E2234"),sQuery(id+"F6.wireOp",EDGE,"E2235"),sQuery(id+"F6.wireOp",EDGE,"E2236"),sQuery(id+"F6.wireOp",EDGE,"E2237"),sQuery(id+"F6.wireOp",EDGE,"E2238"),sQuery(id+"F6.wireOp",EDGE,"E2239"),sQuery(id+"F6.wireOp",EDGE,"E2240"),sQuery(id+"F6.wireOp",EDGE,"E2241"),sQuery(id+"F6.wireOp",EDGE,"E2242"),sQuery(id+"F6.wireOp",EDGE,"E2243"),sQuery(id+"F6.wireOp",EDGE,"E2244"),sQuery(id+"F6.wireOp",EDGE,"E2245"),sQuery(id+"F6.wireOp",EDGE,"E2246"),sQuery(id+"F6.wireOp",EDGE,"E2247"),sQuery(id+"F6.wireOp",EDGE,"E2248"),sQuery(id+"F6.wireOp",EDGE,"E2249"),sQuery(id+"F6.wireOp",EDGE,"E2250"),sQuery(id+"F6.wireOp",EDGE,"E2251"),sQuery(id+"F6.wireOp",EDGE,"E2252"),sQuery(id+"F6.wireOp",EDGE,"E2253"),sQuery(id+"F6.wireOp",EDGE,"E2254"),sQuery(id+"F6.wireOp",EDGE,"E2255"),sQuery(id+"F6.wireOp",EDGE,"E2256"),sQuery(id+"F6.wireOp",EDGE,"E2257"),sQuery(id+"F6.wireOp",EDGE,"E2258"),sQuery(id+"F6.wireOp",EDGE,"E2259"),sQuery(id+"F6.wireOp",EDGE,"E2260"),sQuery(id+"F6.wireOp",EDGE,"E2261"),sQuery(id+"F6.wireOp",EDGE,"E2262"),sQuery(id+"F6.wireOp",EDGE,"E2263"),sQuery(id+"F6.wireOp",EDGE,"E2264"),sQuery(id+"F6.wireOp",EDGE,"E2265"),sQuery(id+"F6.wireOp",EDGE,"E2266"),sQuery(id+"F6.wireOp",EDGE,"E2267"),sQuery(id+"F6.wireOp",EDGE,"E2268"),sQuery(id+"F6.wireOp",EDGE,"E2269"),sQuery(id+"F6.wireOp",EDGE,"E2270"),sQuery(id+"F6.wireOp",EDGE,"E2271"),sQuery(id+"F6.wireOp",EDGE,"E2272"),sQuery(id+"F6.wireOp",EDGE,"E2273"),sQuery(id+"F6.wireOp",EDGE,"E2274"),sQuery(id+"F6.wireOp",EDGE,"E2275"),sQuery(id+"F6.wireOp",EDGE,"E2276"),sQuery(id+"F6.wireOp",EDGE,"E2277"),sQuery(id+"F6.wireOp",EDGE,"E2278"),sQuery(id+"F6.wireOp",EDGE,"E2279"),sQuery(id+"F6.wireOp",EDGE,"E2280"),sQuery(id+"F6.wireOp",EDGE,"E2281"),sQuery(id+"F6.wireOp",EDGE,"E2282"),sQuery(id+"F6.wireOp",EDGE,"E2283"),sQuery(id+"F6.wireOp",EDGE,"E2284"),sQuery(id+"F6.wireOp",EDGE,"E2285"),sQuery(id+"F6.wireOp",EDGE,"E2286"),sQuery(id+"F6.wireOp",EDGE,"E2287"),sQuery(id+"F6.wireOp",EDGE,"E2288"),sQuery(id+"F6.wireOp",EDGE,"E2289"),sQuery(id+"F6.wireOp",EDGE,"E2290"),sQuery(id+"F6.wireOp",EDGE,"E2291"),sQuery(id+"F6.wireOp",EDGE,"E2292"),sQuery(id+"F6.wireOp",EDGE,"E2293"),sQuery(id+"F6.wireOp",EDGE,"E2294"),sQuery(id+"F6.wireOp",EDGE,"E2295"),sQuery(id+"F6.wireOp",EDGE,"E2296"),sQuery(id+"F6.wireOp",EDGE,"E2297"),sQuery(id+"F6.wireOp",EDGE,"E2298"),sQuery(id+"F6.wireOp",EDGE,"E2299"),sQuery(id+"F6.wireOp",EDGE,"E2300"),sQuery(id+"F6.wireOp",EDGE,"E2301"),sQuery(id+"F6.wireOp",EDGE,"E2302"),sQuery(id+"F6.wireOp",EDGE,"E2303"),sQuery(id+"F6.wireOp",EDGE,"E2304"),sQuery(id+"F6.wireOp",EDGE,"E2305"),sQuery(id+"F6.wireOp",EDGE,"E2306"),sQuery(id+"F6.wireOp",EDGE,"E2307"),sQuery(id+"F6.wireOp",EDGE,"E2308"),sQuery(id+"F6.wireOp",EDGE,"E2309"),sQuery(id+"F6.wireOp",EDGE,"E2310"),sQuery(id+"F6.wireOp",EDGE,"E2311"),sQuery(id+"F6.wireOp",EDGE,"E2312"),sQuery(id+"F6.wireOp",EDGE,"E2313"),sQuery(id+"F6.wireOp",EDGE,"E2314"),sQuery(id+"F6.wireOp",EDGE,"E2315"),sQuery(id+"F6.wireOp",EDGE,"E2316"),sQuery(id+"F6.wireOp",EDGE,"E2317"),sQuery(id+"F6.wireOp",EDGE,"E2318"),sQuery(id+"F6.wireOp",EDGE,"E2319"),sQuery(id+"F6.wireOp",EDGE,"E2320"),sQuery(id+"F6.wireOp",EDGE,"E2321"),sQuery(id+"F6.wireOp",EDGE,"E2322"),sQuery(id+"F6.wireOp",EDGE,"E2323"),sQuery(id+"F6.wireOp",EDGE,"E2324"),sQuery(id+"F6.wireOp",EDGE,"E2325"),sQuery(id+"F6.wireOp",EDGE,"E2326"),sQuery(id+"F6.wireOp",EDGE,"E2327"),sQuery(id+"F6.wireOp",EDGE,"E2328"),sQuery(id+"F6.wireOp",EDGE,"E2329"),sQuery(id+"F6.wireOp",EDGE,"E2330"),sQuery(id+"F6.wireOp",EDGE,"E2331"),sQuery(id+"F6.wireOp",EDGE,"E2332"),sQuery(id+"F6.wireOp",EDGE,"E2333"),sQuery(id+"F6.wireOp",EDGE,"E2334"),sQuery(id+"F6.wireOp",EDGE,"E2335"),sQuery(id+"F6.wireOp",EDGE,"E2336"),sQuery(id+"F6.wireOp",EDGE,"E2337"),sQuery(id+"F6.wireOp",EDGE,"E2338"),sQuery(id+"F6.wireOp",EDGE,"E2339"),sQuery(id+"F6.wireOp",EDGE,"E2340"),sQuery(id+"F6.wireOp",EDGE,"E2341"),sQuery(id+"F6.wireOp",EDGE,"E2342"),sQuery(id+"F6.wireOp",EDGE,"E2343"),sQuery(id+"F6.wireOp",EDGE,"E2344"),sQuery(id+"F6.wireOp",EDGE,"E2345"),sQuery(id+"F6.wireOp",EDGE,"E2346"),sQuery(id+"F6.wireOp",EDGE,"E2347"),sQuery(id+"F6.wireOp",EDGE,"E2348"),sQuery(id+"F6.wireOp",EDGE,"E2349"),sQuery(id+"F6.wireOp",EDGE,"E2350"),sQuery(id+"F6.wireOp",EDGE,"E2351"),sQuery(id+"F6.wireOp",EDGE,"E2352"),sQuery(id+"F6.wireOp",EDGE,"E2353"),sQuery(id+"F6.wireOp",EDGE,"E2354"),sQuery(id+"F6.wireOp",EDGE,"E2355"),sQuery(id+"F6.wireOp",EDGE,"E2356"),sQuery(id+"F6.wireOp",EDGE,"E2357"),sQuery(id+"F6.wireOp",EDGE,"E2358"),sQuery(id+"F6.wireOp",EDGE,"E2359"),sQuery(id+"F6.wireOp",EDGE,"E2360"),sQuery(id+"F6.wireOp",EDGE,"E2361"),sQuery(id+"F6.wireOp",EDGE,"E2362"),sQuery(id+"F6.wireOp",EDGE,"E2363"),sQuery(id+"F6.wireOp",EDGE,"E2364"),sQuery(id+"F6.wireOp",EDGE,"E2365"),sQuery(id+"F6.wireOp",EDGE,"E2366"),sQuery(id+"F6.wireOp",EDGE,"E2367"),sQuery(id+"F6.wireOp",EDGE,"E2368"),sQuery(id+"F6.wireOp",EDGE,"E2369"),sQuery(id+"F6.wireOp",EDGE,"E2370"),sQuery(id+"F6.wireOp",EDGE,"E2371"),sQuery(id+"F6.wireOp",EDGE,"E2372"),sQuery(id+"F6.wireOp",EDGE,"E2373"),sQuery(id+"F6.wireOp",EDGE,"E2374"),sQuery(id+"F6.wireOp",EDGE,"E2375"),sQuery(id+"F6.wireOp",EDGE,"E2376"),sQuery(id+"F6.wireOp",EDGE,"E2377"),sQuery(id+"F6.wireOp",EDGE,"E2378"),sQuery(id+"F6.wireOp",EDGE,"E2379"),sQuery(id+"F6.wireOp",EDGE,"E2380"),sQuery(id+"F6.wireOp",EDGE,"E2381"),sQuery(id+"F6.wireOp",EDGE,"E2382"),sQuery(id+"F6.wireOp",EDGE,"E2383"),sQuery(id+"F6.wireOp",EDGE,"E2384"),sQuery(id+"F6.wireOp",EDGE,"E2385"),sQuery(id+"F6.wireOp",EDGE,"E2386"),sQuery(id+"F6.wireOp",EDGE,"E2387"),sQuery(id+"F6.wireOp",EDGE,"E2388"),sQuery(id+"F6.wireOp",EDGE,"E2389"),sQuery(id+"F6.wireOp",EDGE,"E2390"),sQuery(id+"F6.wireOp",EDGE,"E2391"),sQuery(id+"F6.wireOp",EDGE,"E2392"),sQuery(id+"F6.wireOp",EDGE,"E2393"),sQuery(id+"F6.wireOp",EDGE,"E2394"),sQuery(id+"F6.wireOp",EDGE,"E2395"),sQuery(id+"F6.wireOp",EDGE,"E2396"),sQuery(id+"F6.wireOp",EDGE,"E2397"),sQuery(id+"F6.wireOp",EDGE,"E2398"),sQuery(id+"F6.wireOp",EDGE,"E2399"),sQuery(id+"F6.wireOp",EDGE,"E2400"),sQuery(id+"F6.wireOp",EDGE,"E2401"),sQuery(id+"F6.wireOp",EDGE,"E2402"),sQuery(id+"F6.wireOp",EDGE,"E2403"),sQuery(id+"F6.wireOp",EDGE,"E2404"),sQuery(id+"F6.wireOp",EDGE,"E2405"),sQuery(id+"F6.wireOp",EDGE,"E2406"),sQuery(id+"F6.wireOp",EDGE,"E2407"),sQuery(id+"F6.wireOp",EDGE,"E2408"),sQuery(id+"F6.wireOp",EDGE,"E2409"),sQuery(id+"F6.wireOp",EDGE,"E2410"),sQuery(id+"F6.wireOp",EDGE,"E2411"),sQuery(id+"F6.wireOp",EDGE,"E2412"),sQuery(id+"F6.wireOp",EDGE,"E2413"),sQuery(id+"F6.wireOp",EDGE,"E2414"),sQuery(id+"F6.wireOp",EDGE,"E2415"),sQuery(id+"F6.wireOp",EDGE,"E2416"),sQuery(id+"F6.wireOp",EDGE,"E2417"),sQuery(id+"F6.wireOp",EDGE,"E2418"),sQuery(id+"F6.wireOp",EDGE,"E2419"),sQuery(id+"F6.wireOp",EDGE,"E2420"),sQuery(id+"F6.wireOp",EDGE,"E2421"),sQuery(id+"F6.wireOp",EDGE,"E2422"),sQuery(id+"F6.wireOp",EDGE,"E2423"),sQuery(id+"F6.wireOp",EDGE,"E2424"),sQuery(id+"F6.wireOp",EDGE,"E2425"),sQuery(id+"F6.wireOp",EDGE,"E2426"),sQuery(id+"F6.wireOp",EDGE,"E2427"),sQuery(id+"F6.wireOp",EDGE,"E2428"),sQuery(id+"F6.wireOp",EDGE,"E2429"),sQuery(id+"F6.wireOp",EDGE,"E2430"),sQuery(id+"F6.wireOp",EDGE,"E2431"),sQuery(id+"F6.wireOp",EDGE,"E2432"),sQuery(id+"F6.wireOp",EDGE,"E2433"),sQuery(id+"F6.wireOp",EDGE,"E2434"),sQuery(id+"F6.wireOp",EDGE,"E2435")])]}),"instanceName":"1"});
            var Q1;
            Q1=sQuery(id+"F12.wireOp",VERTEX,"E2438");
            var Q2;
            Q2=sQuery(id+"F12.wireOp",VERTEX,"E2439");
            transform(context, id + "F13", {"entities" : qUnion([Q0]), "transformType" : TransformType.TRANSLATION_ENTITY, "oppositeDirectionEntity" : false, "transformLine" : qUnion([Q1, Q2]), "makeCopy" : false});
        }
    });
